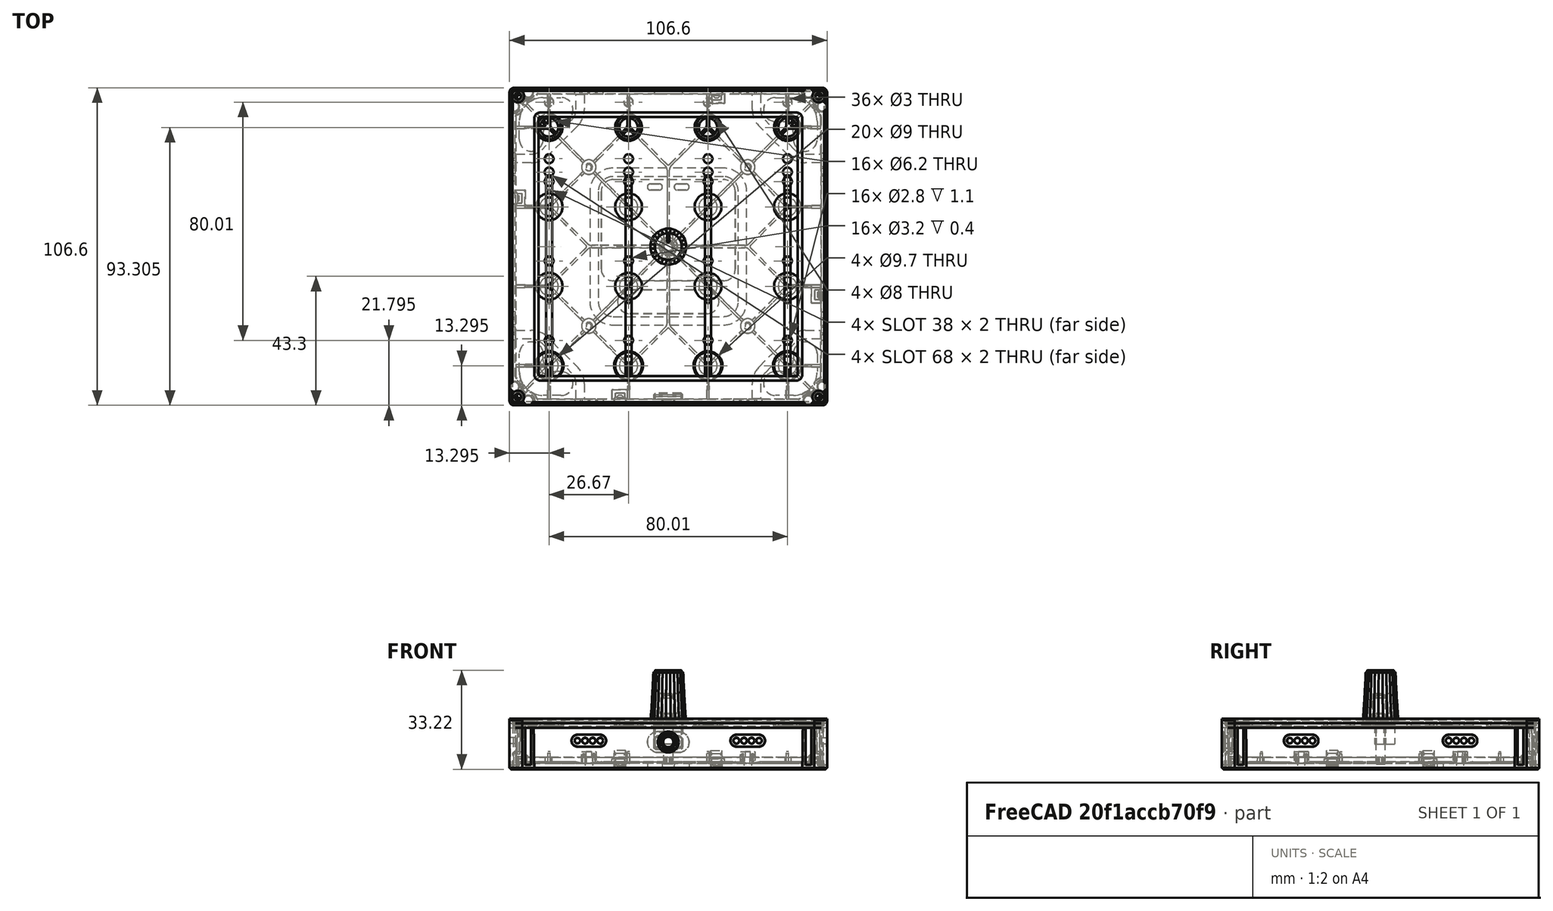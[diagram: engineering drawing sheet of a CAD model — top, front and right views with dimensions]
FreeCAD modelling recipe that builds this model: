
FCSTD DOCUMENT  (FreeCAD 0.20R29410 (Git))
Label: grid_module
License: All rights reserved
LicenseURL: http://en.wikipedia.org/wiki/All_rights_reserved
objects: Sketcher::SketchObject×346, App::Part×144, PartDesign::Body×128, PartDesign::Pocket×109, PartDesign::Chamfer×80, PartDesign::Pad×69, PartDesign::Revolution×59, PartDesign::Fillet×40, PartDesign::AdditiveLoft×36, Part::Feature×15, App::VRMLObject×11, Mesh::Feature×4, PartDesign::Hole×1, PartDesign::Draft×1
note: 1279 computed .brp shape members not serialized (recipe doc carries the construction recipe); baked Part::Feature solids carry a one-line shape summary decoded from their .brp

FEATURE [Sketcher::SketchObject] Sketch
  FullyConstrained = false
  MapMode = 5
  Support = -> [XY_Plane]
  sketch-geometry (25):
    g0: LineSegment StartX=-0.789915 StartY=6 StartZ=0 EndX=-2.31591 EndY=5.59111 EndZ=0
    g1: LineSegment StartX=-2.31591 StartY=5.59111 StartZ=0 EndX=-3.68409 EndY=4.80119 EndZ=0
    g2: LineSegment StartX=-3.68409 StartY=4.80119 StartZ=0 EndX=-4.80119 EndY=3.68409 EndZ=0
    g3: LineSegment StartX=-4.80119 StartY=3.68409 StartZ=0 EndX=-5.59111 EndY=2.31591 EndZ=0
    g4: LineSegment StartX=-5.59111 StartY=2.31591 StartZ=0 EndX=-6 EndY=0.789915 EndZ=0
    g5: LineSegment StartX=-6 StartY=0.789915 StartZ=0 EndX=-6 EndY=-0.789915 EndZ=0
    g6: LineSegment StartX=-6 StartY=-0.789915 StartZ=0 EndX=-5.59111 EndY=-2.31591 EndZ=0
    g7: LineSegment StartX=-5.59111 StartY=-2.31591 StartZ=0 EndX=-4.80119 EndY=-3.68409 EndZ=0
    g8: LineSegment StartX=-4.80119 StartY=-3.68409 StartZ=0 EndX=-3.68409 EndY=-4.80119 EndZ=0
    g9: LineSegment StartX=-3.68409 StartY=-4.80119 StartZ=0 EndX=-2.31591 EndY=-5.59111 EndZ=0
    g10: LineSegment StartX=-2.31591 StartY=-5.59111 StartZ=0 EndX=-0.789915 EndY=-6 EndZ=0
    g11: LineSegment StartX=-0.789915 StartY=-6 StartZ=0 EndX=0.789915 EndY=-6 EndZ=0
    g12: LineSegment StartX=0.789915 StartY=-6 StartZ=0 EndX=2.31591 EndY=-5.59111 EndZ=0
    g13: LineSegment StartX=2.31591 StartY=-5.59111 StartZ=0 EndX=3.68409 EndY=-4.80119 EndZ=0
    g14: LineSegment StartX=3.68409 StartY=-4.80119 StartZ=0 EndX=4.80119 EndY=-3.68409 EndZ=0
    g15: LineSegment StartX=4.80119 StartY=-3.68409 StartZ=0 EndX=5.59111 EndY=-2.31591 EndZ=0
    g16: LineSegment StartX=5.59111 StartY=-2.31591 StartZ=0 EndX=6 EndY=-0.789915 EndZ=0
    g17: LineSegment StartX=6 StartY=-0.789915 StartZ=0 EndX=6 EndY=0.789915 EndZ=0
    g18: LineSegment StartX=6 StartY=0.789915 StartZ=0 EndX=5.59111 EndY=2.31591 EndZ=0
    g19: LineSegment StartX=5.59111 StartY=2.31591 StartZ=0 EndX=4.80119 EndY=3.68409 EndZ=0
    g20: LineSegment StartX=4.80119 StartY=3.68409 StartZ=0 EndX=3.68409 EndY=4.80119 EndZ=0
    g21: LineSegment StartX=3.68409 StartY=4.80119 StartZ=0 EndX=2.31591 EndY=5.59111 EndZ=0
    g22: LineSegment StartX=2.31591 StartY=5.59111 StartZ=0 EndX=0.789915 EndY=6 EndZ=0
    g23: LineSegment StartX=0.789915 StartY=6 StartZ=0 EndX=-0.789915 EndY=6 EndZ=0
    g24: Circle CenterX=0 CenterY=0 CenterZ=0 NormalX=0 NormalY=0 NormalZ=1 AngleXU=0 Radius=6.05177
  constraints (52):
    c: Coincident(g0,g1)
    c: Coincident(g1,g2)
    c: Coincident(g2,g3)
    c: Coincident(g3,g4)
    c: Coincident(g4,g5)
    c: Coincident(g5,g6)
    c: Coincident(g6,g7)
    c: Coincident(g7,g8)
    c: Coincident(g8,g9)
    c: Coincident(g9,g10)
    c: Coincident(g10,g11)
    c: Coincident(g11,g12)
    c: Coincident(g12,g13)
    c: Coincident(g13,g14)
    c: Coincident(g14,g15)
    c: Coincident(g15,g16)
    c: Coincident(g16,g17)
    c: Coincident(g17,g18)
    c: Coincident(g18,g19)
    c: Coincident(g19,g20)
    c: Coincident(g20,g21)
    c: Coincident(g21,g22)
    c: Coincident(g22,g23)
    c: Coincident(g23,g0)
    c: Equal(g0, g1-g23) x23
    c: PointOnObject(g0,g24)
    c: PointOnObject(g1,g24)
    c: PointOnObject(g2,g24)
    c: PointOnObject(g3,g24)
    c: PointOnObject(g4,g24)
    c: PointOnObject(g5,g24)
    c: PointOnObject(g6,g24)
    c: PointOnObject(g7,g24)
    c: PointOnObject(g8,g24)
    c: PointOnObject(g9,g24)
    c: PointOnObject(g10,g24)
    c: PointOnObject(g11,g24)
    c: PointOnObject(g12,g24)
    c: PointOnObject(g13,g24)
    c: PointOnObject(g14,g24)
    c: PointOnObject(g15,g24)
    c: PointOnObject(g16,g24)
    c: PointOnObject(g17,g24)
    c: PointOnObject(g18,g24)
    c: PointOnObject(g19,g24)
    c: PointOnObject(g20,g24)
    c: PointOnObject(g21,g24)
    c: PointOnObject(g22,g24)
    c: PointOnObject(g23,g24)
    c: Coincident(g24,g-1)
    c: Horizontal(g23)
    c: DistanceX(g4,g17) = 12
FEATURE [Sketcher::SketchObject] Sketch001
  AttachmentOffset = pos=(0,0,7) rot=(0,0,1;0rad)
  FullyConstrained = false
  MapMode = 5
  Placement = pos=(0,0,7) rot=(0,0,1;0rad)
  Support = -> [XY_Plane]
  sketch-geometry (25):
    g0: LineSegment StartX=-0.724089 StartY=5.5 StartZ=0 EndX=-2.12292 EndY=5.12518 EndZ=0
    g1: LineSegment StartX=-2.12292 StartY=5.12518 StartZ=0 EndX=-3.37708 EndY=4.4011 EndZ=0
    g2: LineSegment StartX=-3.37708 StartY=4.4011 StartZ=0 EndX=-4.4011 EndY=3.37708 EndZ=0
    g3: LineSegment StartX=-4.4011 StartY=3.37708 StartZ=0 EndX=-5.12518 EndY=2.12292 EndZ=0
    g4: LineSegment StartX=-5.12518 StartY=2.12292 StartZ=0 EndX=-5.5 EndY=0.724089 EndZ=0
    g5: LineSegment StartX=-5.5 StartY=0.724089 StartZ=0 EndX=-5.5 EndY=-0.724089 EndZ=0
    g6: LineSegment StartX=-5.5 StartY=-0.724089 StartZ=0 EndX=-5.12518 EndY=-2.12292 EndZ=0
    g7: LineSegment StartX=-5.12518 StartY=-2.12292 StartZ=0 EndX=-4.4011 EndY=-3.37708 EndZ=0
    g8: LineSegment StartX=-4.4011 StartY=-3.37708 StartZ=0 EndX=-3.37708 EndY=-4.4011 EndZ=0
    g9: LineSegment StartX=-3.37708 StartY=-4.4011 StartZ=0 EndX=-2.12292 EndY=-5.12518 EndZ=0
    g10: LineSegment StartX=-2.12292 StartY=-5.12518 StartZ=0 EndX=-0.724089 EndY=-5.5 EndZ=0
    g11: LineSegment StartX=-0.724089 StartY=-5.5 StartZ=0 EndX=0.724089 EndY=-5.5 EndZ=0
    g12: LineSegment StartX=0.724089 StartY=-5.5 StartZ=0 EndX=2.12292 EndY=-5.12518 EndZ=0
    g13: LineSegment StartX=2.12292 StartY=-5.12518 StartZ=0 EndX=3.37708 EndY=-4.4011 EndZ=0
    g14: LineSegment StartX=3.37708 StartY=-4.4011 StartZ=0 EndX=4.4011 EndY=-3.37708 EndZ=0
    g15: LineSegment StartX=4.4011 StartY=-3.37708 StartZ=0 EndX=5.12518 EndY=-2.12292 EndZ=0
    g16: LineSegment StartX=5.12518 StartY=-2.12292 StartZ=0 EndX=5.5 EndY=-0.724089 EndZ=0
    g17: LineSegment StartX=5.5 StartY=-0.724089 StartZ=0 EndX=5.5 EndY=0.724089 EndZ=0
    g18: LineSegment StartX=5.5 StartY=0.724089 StartZ=0 EndX=5.12518 EndY=2.12292 EndZ=0
    g19: LineSegment StartX=5.12518 StartY=2.12292 StartZ=0 EndX=4.4011 EndY=3.37708 EndZ=0
    g20: LineSegment StartX=4.4011 StartY=3.37708 StartZ=0 EndX=3.37708 EndY=4.4011 EndZ=0
    g21: LineSegment StartX=3.37708 StartY=4.4011 StartZ=0 EndX=2.12292 EndY=5.12518 EndZ=0
    g22: LineSegment StartX=2.12292 StartY=5.12518 StartZ=0 EndX=0.724089 EndY=5.5 EndZ=0
    g23: LineSegment StartX=0.724089 StartY=5.5 StartZ=0 EndX=-0.724089 EndY=5.5 EndZ=0
    g24: Circle CenterX=0 CenterY=0 CenterZ=0 NormalX=0 NormalY=0 NormalZ=1 AngleXU=0 Radius=5.54746
  constraints (52):
    c: Coincident(g0,g1)
    c: Coincident(g1,g2)
    c: Coincident(g2,g3)
    c: Coincident(g3,g4)
    c: Coincident(g4,g5)
    c: Coincident(g5,g6)
    c: Coincident(g6,g7)
    c: Coincident(g7,g8)
    c: Coincident(g8,g9)
    c: Coincident(g9,g10)
    c: Coincident(g10,g11)
    c: Coincident(g11,g12)
    c: Coincident(g12,g13)
    c: Coincident(g13,g14)
    c: Coincident(g14,g15)
    c: Coincident(g15,g16)
    c: Coincident(g16,g17)
    c: Coincident(g17,g18)
    c: Coincident(g18,g19)
    c: Coincident(g19,g20)
    c: Coincident(g20,g21)
    c: Coincident(g21,g22)
    c: Coincident(g22,g23)
    c: Coincident(g23,g0)
    c: Equal(g0, g1-g23) x23
    c: PointOnObject(g0,g24)
    c: PointOnObject(g1,g24)
    c: PointOnObject(g2,g24)
    c: PointOnObject(g3,g24)
    c: PointOnObject(g4,g24)
    c: PointOnObject(g5,g24)
    c: PointOnObject(g6,g24)
    c: PointOnObject(g7,g24)
    c: PointOnObject(g8,g24)
    c: PointOnObject(g9,g24)
    c: PointOnObject(g10,g24)
    c: PointOnObject(g11,g24)
    c: PointOnObject(g12,g24)
    c: PointOnObject(g13,g24)
    c: PointOnObject(g14,g24)
    c: PointOnObject(g15,g24)
    c: PointOnObject(g16,g24)
    c: PointOnObject(g17,g24)
    c: PointOnObject(g18,g24)
    c: PointOnObject(g19,g24)
    c: PointOnObject(g20,g24)
    c: PointOnObject(g21,g24)
    c: PointOnObject(g22,g24)
    c: PointOnObject(g23,g24)
    c: Coincident(g24,g-1)
    c: Horizontal(g23)
    c: DistanceX(g4,g17) = 11
FEATURE [Sketcher::SketchObject] Sketch002
  AttachmentOffset = pos=(0,0,17) rot=(0,0,1;0rad)
  FullyConstrained = false
  MapMode = 5
  Placement = pos=(0,0,17) rot=(0,0,1;0rad)
  Support = -> [XY_Plane]
  sketch-geometry (25):
    g0: LineSegment StartX=-4.65926 StartY=1.92993 StartZ=0 EndX=-5 EndY=0.658262 EndZ=0
    g1: LineSegment StartX=-5 StartY=0.658262 StartZ=0 EndX=-5 EndY=-0.658262 EndZ=0
    g2: LineSegment StartX=-5 StartY=-0.658262 StartZ=0 EndX=-4.65926 EndY=-1.92993 EndZ=0
    g3: LineSegment StartX=-4.65926 StartY=-1.92993 StartZ=0 EndX=-4.001 EndY=-3.07007 EndZ=0
    g4: LineSegment StartX=-4.001 StartY=-3.07007 StartZ=0 EndX=-3.07007 EndY=-4.001 EndZ=0
    g5: LineSegment StartX=-3.07007 StartY=-4.001 StartZ=0 EndX=-1.92993 EndY=-4.65926 EndZ=0
    g6: LineSegment StartX=-1.92993 StartY=-4.65926 StartZ=0 EndX=-0.658262 EndY=-5 EndZ=0
    g7: LineSegment StartX=-0.658262 StartY=-5 StartZ=0 EndX=0.658262 EndY=-5 EndZ=0
    g8: LineSegment StartX=0.658262 StartY=-5 StartZ=0 EndX=1.92993 EndY=-4.65926 EndZ=0
    g9: LineSegment StartX=1.92993 StartY=-4.65926 StartZ=0 EndX=3.07007 EndY=-4.001 EndZ=0
    g10: LineSegment StartX=3.07007 StartY=-4.001 StartZ=0 EndX=4.001 EndY=-3.07007 EndZ=0
    g11: LineSegment StartX=4.001 StartY=-3.07007 StartZ=0 EndX=4.65926 EndY=-1.92993 EndZ=0
    g12: LineSegment StartX=4.65926 StartY=-1.92993 StartZ=0 EndX=5 EndY=-0.658262 EndZ=0
    g13: LineSegment StartX=5 StartY=-0.658262 StartZ=0 EndX=5 EndY=0.658262 EndZ=0
    g14: LineSegment StartX=5 StartY=0.658262 StartZ=0 EndX=4.65926 EndY=1.92993 EndZ=0
    g15: LineSegment StartX=4.65926 StartY=1.92993 StartZ=0 EndX=4.001 EndY=3.07007 EndZ=0
    g16: LineSegment StartX=4.001 StartY=3.07007 StartZ=0 EndX=3.07007 EndY=4.001 EndZ=0
    g17: LineSegment StartX=3.07007 StartY=4.001 StartZ=0 EndX=1.92993 EndY=4.65926 EndZ=0
    g18: LineSegment StartX=1.92993 StartY=4.65926 StartZ=0 EndX=0.658262 EndY=5 EndZ=0
    g19: LineSegment StartX=0.658262 StartY=5 StartZ=0 EndX=-0.658262 EndY=5 EndZ=0
    g20: LineSegment StartX=-0.658262 StartY=5 StartZ=0 EndX=-1.92993 EndY=4.65926 EndZ=0
    g21: LineSegment StartX=-1.92993 StartY=4.65926 StartZ=0 EndX=-3.07007 EndY=4.001 EndZ=0
    g22: LineSegment StartX=-3.07007 StartY=4.001 StartZ=0 EndX=-4.001 EndY=3.07007 EndZ=0
    g23: LineSegment StartX=-4.001 StartY=3.07007 StartZ=0 EndX=-4.65926 EndY=1.92993 EndZ=0
    g24: Circle CenterX=0 CenterY=0 CenterZ=0 NormalX=0 NormalY=0 NormalZ=1 AngleXU=0 Radius=5.04314
  constraints (52):
    c: Coincident(g0,g1)
    c: Coincident(g1,g2)
    c: Coincident(g2,g3)
    c: Coincident(g3,g4)
    c: Coincident(g4,g5)
    c: Coincident(g5,g6)
    c: Coincident(g6,g7)
    c: Coincident(g7,g8)
    c: Coincident(g8,g9)
    c: Coincident(g9,g10)
    c: Coincident(g10,g11)
    c: Coincident(g11,g12)
    c: Coincident(g12,g13)
    c: Coincident(g13,g14)
    c: Coincident(g14,g15)
    c: Coincident(g15,g16)
    c: Coincident(g16,g17)
    c: Coincident(g17,g18)
    c: Coincident(g18,g19)
    c: Coincident(g19,g20)
    c: Coincident(g20,g21)
    c: Coincident(g21,g22)
    c: Coincident(g22,g23)
    c: Coincident(g23,g0)
    c: Equal(g0, g1-g23) x23
    c: PointOnObject(g0,g24)
    c: PointOnObject(g1,g24)
    c: PointOnObject(g2,g24)
    c: PointOnObject(g3,g24)
    c: PointOnObject(g4,g24)
    c: PointOnObject(g5,g24)
    c: PointOnObject(g6,g24)
    c: PointOnObject(g7,g24)
    c: PointOnObject(g8,g24)
    c: PointOnObject(g9,g24)
    c: PointOnObject(g10,g24)
    c: PointOnObject(g11,g24)
    c: PointOnObject(g12,g24)
    c: PointOnObject(g13,g24)
    c: PointOnObject(g14,g24)
    c: PointOnObject(g15,g24)
    c: PointOnObject(g16,g24)
    c: PointOnObject(g17,g24)
    c: PointOnObject(g18,g24)
    c: PointOnObject(g19,g24)
    c: PointOnObject(g20,g24)
    c: PointOnObject(g21,g24)
    c: PointOnObject(g22,g24)
    c: PointOnObject(g23,g24)
    c: Coincident(g24,g-1)
    c: Horizontal(g19)
    c: DistanceX(g0,g13) = 10
FEATURE [PartDesign::AdditiveLoft] AdditiveLoft
  AllowMultiFace = false
  Closed = false
  Profile = -> Sketch
  Refine = true
  Ruled = false
  Sections = -> [Sketch001,Sketch002]
FEATURE [Sketcher::SketchObject] Sketch003
  FullyConstrained = false
  MapMode = 5
  Placement = pos=(0,0,17) rot=(0,0,1;0rad)
  Support = -> [AdditiveLoft]
  sketch-geometry (1):
    g0: Circle CenterX=0 CenterY=0 CenterZ=0 NormalX=0 NormalY=0 NormalZ=1 AngleXU=0 Radius=4.5
  constraints (2):
    c: Coincident(g0,g-1)
    c: Radius(g0) = 4.5
FEATURE [PartDesign::Pad] Pad
  AllowMultiFace = false
  BaseFeature = -> AdditiveLoft
  Direction = (1,1,1)
  Length = 0.7
  Length2 = 100
  Profile = -> Sketch003
  Refine = true
  Type = 0
FEATURE [Sketcher::SketchObject] Sketch004
  AttachmentOffset = pos=(0,0,17.7) rot=(0,0,1;0rad)
  FullyConstrained = false
  MapMode = 5
  Placement = pos=(0,0,17.7) rot=(0,0,1;0rad)
  Support = -> [XY_Plane001]
  sketch-geometry (10):
    g0: LineSegment StartX=-0.2 StartY=1.5 StartZ=0 EndX=0.2 EndY=1.5 EndZ=0
    g1: LineSegment StartX=0.4 StartY=1.7 StartZ=0 EndX=0.4 EndY=4.2 EndZ=0
    g2: LineSegment StartX=0.2 StartY=4.4 StartZ=0 EndX=-0.2 EndY=4.4 EndZ=0
    g3: LineSegment StartX=-0.4 StartY=4.2 StartZ=0 EndX=-0.4 EndY=1.7 EndZ=0
    g4: ArcOfCircle CenterX=-0.2 CenterY=1.7 CenterZ=0 NormalX=0 NormalY=0 NormalZ=1 AngleXU=0 Radius=0.2 StartAngle=3.14159 EndAngle=4.71239
    g5: ArcOfCircle CenterX=0.2 CenterY=1.7 CenterZ=0 NormalX=0 NormalY=0 NormalZ=1 AngleXU=0 Radius=0.2 StartAngle=4.71239 EndAngle=6.28319
    g6: ArcOfCircle CenterX=0.2 CenterY=4.2 CenterZ=0 NormalX=0 NormalY=0 NormalZ=1 AngleXU=0 Radius=0.2 StartAngle=1.4e-15 EndAngle=1.5708
    g7: ArcOfCircle CenterX=-0.2 CenterY=4.2 CenterZ=0 NormalX=0 NormalY=0 NormalZ=1 AngleXU=0 Radius=0.2 StartAngle=1.5708 EndAngle=3.14159
    g8: LineSegment StartX=-0.2 StartY=1.7 StartZ=0 EndX=0 EndY=0 EndZ=0
    g9: LineSegment StartX=0 StartY=0 StartZ=0 EndX=0.2 EndY=1.7 EndZ=0
  constraints (24):
    c: Horizontal(g0)
    c: Horizontal(g2)
    c: Vertical(g1)
    c: Vertical(g3)
    c: Tangent(g3,g4) = -1.5708
    c: Tangent(g0,g4) = -1.5708
    c: Tangent(g0,g5) = -1.5708
    c: Tangent(g1,g5) = -1.5708
    c: Tangent(g1,g6) = -1.5708
    c: Tangent(g2,g6) = -1.5708
    c: Tangent(g2,g7) = -1.5708
    c: Tangent(g3,g7) = -1.5708
    c: Radius(g7) = 0.2
    c: Equal(g7,g6)
    c: Equal(g7,g5)
    c: Equal(g7,g4)
    c: Coincident(g8,g4)
    c: Coincident(g8,g-1)
    c: Coincident(g9,g-1)
    c: Coincident(g9,g5)
    c: Equal(g9,g8)
    c: DistanceX(g3,g1) = 0.8
    c: DistanceY(g-1,g2) = 4.4
    c: DistanceY(g-1,g0) = 1.5
FEATURE [PartDesign::Pad] Pad001
  AllowMultiFace = false
  Direction = (1,1,1)
  Length = 0.02
  Length2 = 100
  Profile = -> Sketch004
  Refine = true
  Type = 0
FEATURE [PartDesign::Body] Body001  label="Indicator"
  Group = -> [Sketch004,Pad001]
  Origin = -> Origin001
  Tip = -> Pad001
FEATURE [Sketcher::SketchObject] Sketch005
  FullyConstrained = false
  MapMode = 5
  Placement = pos=(0,0,0) rot=(1,0,0;3.14159rad)
  Support = -> [Pad]
  sketch-geometry (1):
    g0: Circle CenterX=0 CenterY=0 CenterZ=0 NormalX=0 NormalY=0 NormalZ=1 AngleXU=0 Radius=5
  constraints (2):
    c: Coincident(g0,g-1)
    c: Radius(g0) = 5
FEATURE [PartDesign::Pocket] Pocket
  AllowMultiFace = false
  BaseFeature = -> Pad
  Direction = (1,1,1)
  Length = 1
  Length2 = 100
  Profile = -> Sketch005
  Refine = true
  Type = 0
FEATURE [Sketcher::SketchObject] Sketch006
  FullyConstrained = false
  MapMode = 5
  Placement = pos=(0,0,1) rot=(1,0,0;3.14159rad)
  Support = -> [Pocket]
  sketch-geometry (1):
    g0: Circle CenterX=0 CenterY=0 CenterZ=0 NormalX=0 NormalY=0 NormalZ=1 AngleXU=0 Radius=4.65
  constraints (2):
    c: Coincident(g0,g-1)
    c: Radius(g0) = 4.65
FEATURE [PartDesign::Pocket] Pocket001
  AllowMultiFace = false
  BaseFeature = -> Pocket
  Direction = (1,1,1)
  Length = 1
  Length2 = 100
  Profile = -> Sketch006
  Refine = true
  Type = 0
FEATURE [Sketcher::SketchObject] Sketch007
  FullyConstrained = false
  MapMode = 5
  Placement = pos=(0,0,2) rot=(1,0,0;3.14159rad)
  Support = -> [Pocket001]
  sketch-geometry (2):
    g0: ArcOfCircle CenterX=0 CenterY=0 CenterZ=0 NormalX=0 NormalY=0 NormalZ=1 AngleXU=0 Radius=3 StartAngle=2.19024 EndAngle=7.23453
    g1: LineSegment StartX=-1.74176 StartY=2.4426 StartZ=0 EndX=1.74176 EndY=2.4426 EndZ=0
  constraints (5):
    c: Coincident(g0,g-1)
    c: Coincident(g1,g0)
    c: Coincident(g1,g0)
    c: Horizontal(g1)
    c: Radius(g0) = 3
FEATURE [PartDesign::Pocket] Pocket002
  AllowMultiFace = false
  BaseFeature = -> Pocket001
  Direction = (1,1,1)
  Length = 8
  Length2 = 100
  Profile = -> Sketch007
  Refine = true
  Type = 0
FEATURE [PartDesign::Chamfer] Chamfer
  Angle = 45
  Base = -> Pocket002 [Edge82,Edge83]
  BaseFeature = -> Pocket002
  ChamferType = 0
  FlipDirection = false
  Size = 1.4
  Size2 = 1
  SupportTransform = false
  UseAllEdges = false
FEATURE [PartDesign::Chamfer] Chamfer001
  Angle = 45
  Base = -> Chamfer [Edge8]
  BaseFeature = -> Chamfer
  ChamferType = 0
  FlipDirection = false
  Size = 0.3
  Size2 = 1
  SupportTransform = false
  UseAllEdges = false
FEATURE [PartDesign::Fillet] Fillet
  Base = -> Chamfer001 [Edge93,Face36]
  BaseFeature = -> Chamfer001
  Radius = 0.1
  SupportTransform = false
  UseAllEdges = false
FEATURE [PartDesign::Body] Body
  Group = -> [Sketch,Sketch001,Sketch002,AdditiveLoft,Sketch003,Pad,Sketch005,Pocket,Sketch006,Pocket001,Sketch007,Pocket002,Chamfer,Chamfer001,Fillet]
  Origin = -> Origin
  Tip = -> Fillet
FEATURE [App::Part] Part  label="Cap1"
  Group = -> [Body,Body001]
  Origin = -> Origin004
  Placement = pos=(-40.005,40.005,0) rot=(0,0,1;0rad)
  expr: .Placement.Base.x = -40.005
  expr: .Placement.Base.y = 40.005
FEATURE [Sketcher::SketchObject] Sketch012
  AttachmentOffset = pos=(0,0,7) rot=(0,0,1;0rad)
  FullyConstrained = false
  MapMode = 5
  Placement = pos=(0,0,7) rot=(0,0,1;0rad)
  Support = -> [XY_Plane005]
  sketch-geometry (25):
    g0: LineSegment StartX=-0.724089 StartY=5.5 StartZ=0 EndX=-2.12292 EndY=5.12518 EndZ=0
    g1: LineSegment StartX=-2.12292 StartY=5.12518 StartZ=0 EndX=-3.37708 EndY=4.4011 EndZ=0
    g2: LineSegment StartX=-3.37708 StartY=4.4011 StartZ=0 EndX=-4.4011 EndY=3.37708 EndZ=0
    g3: LineSegment StartX=-4.4011 StartY=3.37708 StartZ=0 EndX=-5.12518 EndY=2.12292 EndZ=0
    g4: LineSegment StartX=-5.12518 StartY=2.12292 StartZ=0 EndX=-5.5 EndY=0.724089 EndZ=0
    g5: LineSegment StartX=-5.5 StartY=0.724089 StartZ=0 EndX=-5.5 EndY=-0.724089 EndZ=0
    g6: LineSegment StartX=-5.5 StartY=-0.724089 StartZ=0 EndX=-5.12518 EndY=-2.12292 EndZ=0
    g7: LineSegment StartX=-5.12518 StartY=-2.12292 StartZ=0 EndX=-4.4011 EndY=-3.37708 EndZ=0
    g8: LineSegment StartX=-4.4011 StartY=-3.37708 StartZ=0 EndX=-3.37708 EndY=-4.4011 EndZ=0
    g9: LineSegment StartX=-3.37708 StartY=-4.4011 StartZ=0 EndX=-2.12292 EndY=-5.12518 EndZ=0
    g10: LineSegment StartX=-2.12292 StartY=-5.12518 StartZ=0 EndX=-0.724089 EndY=-5.5 EndZ=0
    g11: LineSegment StartX=-0.724089 StartY=-5.5 StartZ=0 EndX=0.724089 EndY=-5.5 EndZ=0
    g12: LineSegment StartX=0.724089 StartY=-5.5 StartZ=0 EndX=2.12292 EndY=-5.12518 EndZ=0
    g13: LineSegment StartX=2.12292 StartY=-5.12518 StartZ=0 EndX=3.37708 EndY=-4.4011 EndZ=0
    g14: LineSegment StartX=3.37708 StartY=-4.4011 StartZ=0 EndX=4.4011 EndY=-3.37708 EndZ=0
    g15: LineSegment StartX=4.4011 StartY=-3.37708 StartZ=0 EndX=5.12518 EndY=-2.12292 EndZ=0
    g16: LineSegment StartX=5.12518 StartY=-2.12292 StartZ=0 EndX=5.5 EndY=-0.724089 EndZ=0
    g17: LineSegment StartX=5.5 StartY=-0.724089 StartZ=0 EndX=5.5 EndY=0.724089 EndZ=0
    g18: LineSegment StartX=5.5 StartY=0.724089 StartZ=0 EndX=5.12518 EndY=2.12292 EndZ=0
    g19: LineSegment StartX=5.12518 StartY=2.12292 StartZ=0 EndX=4.4011 EndY=3.37708 EndZ=0
    g20: LineSegment StartX=4.4011 StartY=3.37708 StartZ=0 EndX=3.37708 EndY=4.4011 EndZ=0
    g21: LineSegment StartX=3.37708 StartY=4.4011 StartZ=0 EndX=2.12292 EndY=5.12518 EndZ=0
    g22: LineSegment StartX=2.12292 StartY=5.12518 StartZ=0 EndX=0.724089 EndY=5.5 EndZ=0
    g23: LineSegment StartX=0.724089 StartY=5.5 StartZ=0 EndX=-0.724089 EndY=5.5 EndZ=0
    g24: Circle CenterX=0 CenterY=0 CenterZ=0 NormalX=0 NormalY=0 NormalZ=1 AngleXU=0 Radius=5.54746
  constraints (52):
    c: Coincident(g0,g1)
    c: Coincident(g1,g2)
    c: Coincident(g2,g3)
    c: Coincident(g3,g4)
    c: Coincident(g4,g5)
    c: Coincident(g5,g6)
    c: Coincident(g6,g7)
    c: Coincident(g7,g8)
    c: Coincident(g8,g9)
    c: Coincident(g9,g10)
    c: Coincident(g10,g11)
    c: Coincident(g11,g12)
    c: Coincident(g12,g13)
    c: Coincident(g13,g14)
    c: Coincident(g14,g15)
    c: Coincident(g15,g16)
    c: Coincident(g16,g17)
    c: Coincident(g17,g18)
    c: Coincident(g18,g19)
    c: Coincident(g19,g20)
    c: Coincident(g20,g21)
    c: Coincident(g21,g22)
    c: Coincident(g22,g23)
    c: Coincident(g23,g0)
    c: Equal(g0, g1-g23) x23
    c: PointOnObject(g0,g24)
    c: PointOnObject(g1,g24)
    c: PointOnObject(g2,g24)
    c: PointOnObject(g3,g24)
    c: PointOnObject(g4,g24)
    c: PointOnObject(g5,g24)
    c: PointOnObject(g6,g24)
    c: PointOnObject(g7,g24)
    c: PointOnObject(g8,g24)
    c: PointOnObject(g9,g24)
    c: PointOnObject(g10,g24)
    c: PointOnObject(g11,g24)
    c: PointOnObject(g12,g24)
    c: PointOnObject(g13,g24)
    c: PointOnObject(g14,g24)
    c: PointOnObject(g15,g24)
    c: PointOnObject(g16,g24)
    c: PointOnObject(g17,g24)
    c: PointOnObject(g18,g24)
    c: PointOnObject(g19,g24)
    c: PointOnObject(g20,g24)
    c: PointOnObject(g21,g24)
    c: PointOnObject(g22,g24)
    c: PointOnObject(g23,g24)
    c: Coincident(g24,g-1)
    c: Horizontal(g23)
    c: DistanceX(g4,g17) = 11
FEATURE [Sketcher::SketchObject] Sketch013
  FullyConstrained = false
  MapMode = 5
  Support = -> [XY_Plane005]
  sketch-geometry (25):
    g0: LineSegment StartX=-0.789915 StartY=6 StartZ=0 EndX=-2.31591 EndY=5.59111 EndZ=0
    g1: LineSegment StartX=-2.31591 StartY=5.59111 StartZ=0 EndX=-3.68409 EndY=4.80119 EndZ=0
    g2: LineSegment StartX=-3.68409 StartY=4.80119 StartZ=0 EndX=-4.80119 EndY=3.68409 EndZ=0
    g3: LineSegment StartX=-4.80119 StartY=3.68409 StartZ=0 EndX=-5.59111 EndY=2.31591 EndZ=0
    g4: LineSegment StartX=-5.59111 StartY=2.31591 StartZ=0 EndX=-6 EndY=0.789915 EndZ=0
    g5: LineSegment StartX=-6 StartY=0.789915 StartZ=0 EndX=-6 EndY=-0.789915 EndZ=0
    g6: LineSegment StartX=-6 StartY=-0.789915 StartZ=0 EndX=-5.59111 EndY=-2.31591 EndZ=0
    g7: LineSegment StartX=-5.59111 StartY=-2.31591 StartZ=0 EndX=-4.80119 EndY=-3.68409 EndZ=0
    g8: LineSegment StartX=-4.80119 StartY=-3.68409 StartZ=0 EndX=-3.68409 EndY=-4.80119 EndZ=0
    g9: LineSegment StartX=-3.68409 StartY=-4.80119 StartZ=0 EndX=-2.31591 EndY=-5.59111 EndZ=0
    g10: LineSegment StartX=-2.31591 StartY=-5.59111 StartZ=0 EndX=-0.789915 EndY=-6 EndZ=0
    g11: LineSegment StartX=-0.789915 StartY=-6 StartZ=0 EndX=0.789915 EndY=-6 EndZ=0
    g12: LineSegment StartX=0.789915 StartY=-6 StartZ=0 EndX=2.31591 EndY=-5.59111 EndZ=0
    g13: LineSegment StartX=2.31591 StartY=-5.59111 StartZ=0 EndX=3.68409 EndY=-4.80119 EndZ=0
    g14: LineSegment StartX=3.68409 StartY=-4.80119 StartZ=0 EndX=4.80119 EndY=-3.68409 EndZ=0
    g15: LineSegment StartX=4.80119 StartY=-3.68409 StartZ=0 EndX=5.59111 EndY=-2.31591 EndZ=0
    g16: LineSegment StartX=5.59111 StartY=-2.31591 StartZ=0 EndX=6 EndY=-0.789915 EndZ=0
    g17: LineSegment StartX=6 StartY=-0.789915 StartZ=0 EndX=6 EndY=0.789915 EndZ=0
    g18: LineSegment StartX=6 StartY=0.789915 StartZ=0 EndX=5.59111 EndY=2.31591 EndZ=0
    g19: LineSegment StartX=5.59111 StartY=2.31591 StartZ=0 EndX=4.80119 EndY=3.68409 EndZ=0
    g20: LineSegment StartX=4.80119 StartY=3.68409 StartZ=0 EndX=3.68409 EndY=4.80119 EndZ=0
    g21: LineSegment StartX=3.68409 StartY=4.80119 StartZ=0 EndX=2.31591 EndY=5.59111 EndZ=0
    g22: LineSegment StartX=2.31591 StartY=5.59111 StartZ=0 EndX=0.789915 EndY=6 EndZ=0
    g23: LineSegment StartX=0.789915 StartY=6 StartZ=0 EndX=-0.789915 EndY=6 EndZ=0
    g24: Circle CenterX=0 CenterY=0 CenterZ=0 NormalX=0 NormalY=0 NormalZ=1 AngleXU=0 Radius=6.05177
  constraints (52):
    c: Coincident(g0,g1)
    c: Coincident(g1,g2)
    c: Coincident(g2,g3)
    c: Coincident(g3,g4)
    c: Coincident(g4,g5)
    c: Coincident(g5,g6)
    c: Coincident(g6,g7)
    c: Coincident(g7,g8)
    c: Coincident(g8,g9)
    c: Coincident(g9,g10)
    c: Coincident(g10,g11)
    c: Coincident(g11,g12)
    c: Coincident(g12,g13)
    c: Coincident(g13,g14)
    c: Coincident(g14,g15)
    c: Coincident(g15,g16)
    c: Coincident(g16,g17)
    c: Coincident(g17,g18)
    c: Coincident(g18,g19)
    c: Coincident(g19,g20)
    c: Coincident(g20,g21)
    c: Coincident(g21,g22)
    c: Coincident(g22,g23)
    c: Coincident(g23,g0)
    c: Equal(g0, g1-g23) x23
    c: PointOnObject(g0,g24)
    c: PointOnObject(g1,g24)
    c: PointOnObject(g2,g24)
    c: PointOnObject(g3,g24)
    c: PointOnObject(g4,g24)
    c: PointOnObject(g5,g24)
    c: PointOnObject(g6,g24)
    c: PointOnObject(g7,g24)
    c: PointOnObject(g8,g24)
    c: PointOnObject(g9,g24)
    c: PointOnObject(g10,g24)
    c: PointOnObject(g11,g24)
    c: PointOnObject(g12,g24)
    c: PointOnObject(g13,g24)
    c: PointOnObject(g14,g24)
    c: PointOnObject(g15,g24)
    c: PointOnObject(g16,g24)
    c: PointOnObject(g17,g24)
    c: PointOnObject(g18,g24)
    c: PointOnObject(g19,g24)
    c: PointOnObject(g20,g24)
    c: PointOnObject(g21,g24)
    c: PointOnObject(g22,g24)
    c: PointOnObject(g23,g24)
    c: Coincident(g24,g-1)
    c: Horizontal(g23)
    c: DistanceX(g4,g17) = 12
FEATURE [Sketcher::SketchObject] Sketch014
  AttachmentOffset = pos=(0,0,17) rot=(0,0,1;0rad)
  FullyConstrained = false
  MapMode = 5
  Placement = pos=(0,0,17) rot=(0,0,1;0rad)
  Support = -> [XY_Plane005]
  sketch-geometry (25):
    g0: LineSegment StartX=-4.65926 StartY=1.92993 StartZ=0 EndX=-5 EndY=0.658262 EndZ=0
    g1: LineSegment StartX=-5 StartY=0.658262 StartZ=0 EndX=-5 EndY=-0.658262 EndZ=0
    g2: LineSegment StartX=-5 StartY=-0.658262 StartZ=0 EndX=-4.65926 EndY=-1.92993 EndZ=0
    g3: LineSegment StartX=-4.65926 StartY=-1.92993 StartZ=0 EndX=-4.001 EndY=-3.07007 EndZ=0
    g4: LineSegment StartX=-4.001 StartY=-3.07007 StartZ=0 EndX=-3.07007 EndY=-4.001 EndZ=0
    g5: LineSegment StartX=-3.07007 StartY=-4.001 StartZ=0 EndX=-1.92993 EndY=-4.65926 EndZ=0
    g6: LineSegment StartX=-1.92993 StartY=-4.65926 StartZ=0 EndX=-0.658262 EndY=-5 EndZ=0
    g7: LineSegment StartX=-0.658262 StartY=-5 StartZ=0 EndX=0.658262 EndY=-5 EndZ=0
    g8: LineSegment StartX=0.658262 StartY=-5 StartZ=0 EndX=1.92993 EndY=-4.65926 EndZ=0
    g9: LineSegment StartX=1.92993 StartY=-4.65926 StartZ=0 EndX=3.07007 EndY=-4.001 EndZ=0
    g10: LineSegment StartX=3.07007 StartY=-4.001 StartZ=0 EndX=4.001 EndY=-3.07007 EndZ=0
    g11: LineSegment StartX=4.001 StartY=-3.07007 StartZ=0 EndX=4.65926 EndY=-1.92993 EndZ=0
    g12: LineSegment StartX=4.65926 StartY=-1.92993 StartZ=0 EndX=5 EndY=-0.658262 EndZ=0
    g13: LineSegment StartX=5 StartY=-0.658262 StartZ=0 EndX=5 EndY=0.658262 EndZ=0
    g14: LineSegment StartX=5 StartY=0.658262 StartZ=0 EndX=4.65926 EndY=1.92993 EndZ=0
    g15: LineSegment StartX=4.65926 StartY=1.92993 StartZ=0 EndX=4.001 EndY=3.07007 EndZ=0
    g16: LineSegment StartX=4.001 StartY=3.07007 StartZ=0 EndX=3.07007 EndY=4.001 EndZ=0
    g17: LineSegment StartX=3.07007 StartY=4.001 StartZ=0 EndX=1.92993 EndY=4.65926 EndZ=0
    g18: LineSegment StartX=1.92993 StartY=4.65926 StartZ=0 EndX=0.658262 EndY=5 EndZ=0
    g19: LineSegment StartX=0.658262 StartY=5 StartZ=0 EndX=-0.658262 EndY=5 EndZ=0
    g20: LineSegment StartX=-0.658262 StartY=5 StartZ=0 EndX=-1.92993 EndY=4.65926 EndZ=0
    g21: LineSegment StartX=-1.92993 StartY=4.65926 StartZ=0 EndX=-3.07007 EndY=4.001 EndZ=0
    g22: LineSegment StartX=-3.07007 StartY=4.001 StartZ=0 EndX=-4.001 EndY=3.07007 EndZ=0
    g23: LineSegment StartX=-4.001 StartY=3.07007 StartZ=0 EndX=-4.65926 EndY=1.92993 EndZ=0
    g24: Circle CenterX=0 CenterY=0 CenterZ=0 NormalX=0 NormalY=0 NormalZ=1 AngleXU=0 Radius=5.04314
  constraints (52):
    c: Coincident(g0,g1)
    c: Coincident(g1,g2)
    c: Coincident(g2,g3)
    c: Coincident(g3,g4)
    c: Coincident(g4,g5)
    c: Coincident(g5,g6)
    c: Coincident(g6,g7)
    c: Coincident(g7,g8)
    c: Coincident(g8,g9)
    c: Coincident(g9,g10)
    c: Coincident(g10,g11)
    c: Coincident(g11,g12)
    c: Coincident(g12,g13)
    c: Coincident(g13,g14)
    c: Coincident(g14,g15)
    c: Coincident(g15,g16)
    c: Coincident(g16,g17)
    c: Coincident(g17,g18)
    c: Coincident(g18,g19)
    c: Coincident(g19,g20)
    c: Coincident(g20,g21)
    c: Coincident(g21,g22)
    c: Coincident(g22,g23)
    c: Coincident(g23,g0)
    c: Equal(g0, g1-g23) x23
    c: PointOnObject(g0,g24)
    c: PointOnObject(g1,g24)
    c: PointOnObject(g2,g24)
    c: PointOnObject(g3,g24)
    c: PointOnObject(g4,g24)
    c: PointOnObject(g5,g24)
    c: PointOnObject(g6,g24)
    c: PointOnObject(g7,g24)
    c: PointOnObject(g8,g24)
    c: PointOnObject(g9,g24)
    c: PointOnObject(g10,g24)
    c: PointOnObject(g11,g24)
    c: PointOnObject(g12,g24)
    c: PointOnObject(g13,g24)
    c: PointOnObject(g14,g24)
    c: PointOnObject(g15,g24)
    c: PointOnObject(g16,g24)
    c: PointOnObject(g17,g24)
    c: PointOnObject(g18,g24)
    c: PointOnObject(g19,g24)
    c: PointOnObject(g20,g24)
    c: PointOnObject(g21,g24)
    c: PointOnObject(g22,g24)
    c: PointOnObject(g23,g24)
    c: Coincident(g24,g-1)
    c: Horizontal(g19)
    c: DistanceX(g0,g13) = 10
FEATURE [PartDesign::AdditiveLoft] AdditiveLoft001
  AllowMultiFace = false
  Closed = false
  Profile = -> Sketch013
  Refine = true
  Ruled = false
  Sections = -> [Sketch012,Sketch014]
FEATURE [Sketcher::SketchObject] Sketch011
  FullyConstrained = false
  MapMode = 5
  Placement = pos=(0,0,17) rot=(0,0,1;0rad)
  Support = -> [AdditiveLoft001]
  sketch-geometry (1):
    g0: Circle CenterX=0 CenterY=0 CenterZ=0 NormalX=0 NormalY=0 NormalZ=1 AngleXU=0 Radius=4.5
  constraints (2):
    c: Coincident(g0,g-1)
    c: Radius(g0) = 4.5
FEATURE [PartDesign::Pad] Pad002
  AllowMultiFace = false
  BaseFeature = -> AdditiveLoft001
  Direction = (1,1,1)
  Length = 0.7
  Length2 = 100
  Profile = -> Sketch011
  Refine = true
  Type = 0
FEATURE [Sketcher::SketchObject] Sketch010
  FullyConstrained = false
  MapMode = 5
  Placement = pos=(0,0,0) rot=(1,0,0;3.14159rad)
  Support = -> [Pad002]
  sketch-geometry (1):
    g0: Circle CenterX=0 CenterY=0 CenterZ=0 NormalX=0 NormalY=0 NormalZ=1 AngleXU=0 Radius=5
  constraints (2):
    c: Coincident(g0,g-1)
    c: Radius(g0) = 5
FEATURE [PartDesign::Pocket] Pocket004
  AllowMultiFace = false
  BaseFeature = -> Pad002
  Direction = (1,1,1)
  Length = 1
  Length2 = 100
  Profile = -> Sketch010
  Refine = true
  Type = 0
FEATURE [Sketcher::SketchObject] Sketch008
  FullyConstrained = false
  MapMode = 5
  Placement = pos=(0,0,1) rot=(1,0,0;3.14159rad)
  Support = -> [Pocket004]
  sketch-geometry (1):
    g0: Circle CenterX=0 CenterY=0 CenterZ=0 NormalX=0 NormalY=0 NormalZ=1 AngleXU=0 Radius=4.65
  constraints (2):
    c: Coincident(g0,g-1)
    c: Radius(g0) = 4.65
FEATURE [PartDesign::Pocket] Pocket003
  AllowMultiFace = false
  BaseFeature = -> Pocket004
  Direction = (1,1,1)
  Length = 1
  Length2 = 100
  Profile = -> Sketch008
  Refine = true
  Type = 0
FEATURE [Sketcher::SketchObject] Sketch009
  FullyConstrained = false
  MapMode = 5
  Placement = pos=(0,0,2) rot=(1,0,0;3.14159rad)
  Support = -> [Pocket003]
  sketch-geometry (2):
    g0: ArcOfCircle CenterX=0 CenterY=0 CenterZ=0 NormalX=0 NormalY=0 NormalZ=1 AngleXU=0 Radius=3 StartAngle=2.19024 EndAngle=7.23453
    g1: LineSegment StartX=-1.74176 StartY=2.4426 StartZ=0 EndX=1.74176 EndY=2.4426 EndZ=0
  constraints (5):
    c: Coincident(g0,g-1)
    c: Coincident(g1,g0)
    c: Coincident(g1,g0)
    c: Horizontal(g1)
    c: Radius(g0) = 3
FEATURE [PartDesign::Pocket] Pocket005
  AllowMultiFace = false
  BaseFeature = -> Pocket003
  Direction = (1,1,1)
  Length = 8
  Length2 = 100
  Profile = -> Sketch009
  Refine = true
  Type = 0
FEATURE [PartDesign::Chamfer] Chamfer002
  Angle = 45
  Base = -> Pocket005 [Edge82,Edge83]
  BaseFeature = -> Pocket005
  ChamferType = 0
  FlipDirection = false
  Size = 1.4
  Size2 = 1
  SupportTransform = false
  UseAllEdges = false
FEATURE [PartDesign::Chamfer] Chamfer003
  Angle = 45
  Base = -> Chamfer002 [Edge8]
  BaseFeature = -> Chamfer002
  ChamferType = 0
  FlipDirection = false
  Size = 0.3
  Size2 = 1
  SupportTransform = false
  UseAllEdges = false
FEATURE [PartDesign::Fillet] Fillet001
  Base = -> Chamfer003 [Edge93,Face36]
  BaseFeature = -> Chamfer003
  Radius = 0.1
  SupportTransform = false
  UseAllEdges = false
FEATURE [PartDesign::Body] Body002
  Group = -> [Sketch013,Sketch012,Sketch014,AdditiveLoft001,Sketch011,Pad002,Sketch010,Pocket004,Sketch008,Pocket003,Sketch009,Pocket005,Chamfer002,Chamfer003,Fillet001]
  Origin = -> Origin005
  Tip = -> Fillet001
FEATURE [Sketcher::SketchObject] Sketch015
  AttachmentOffset = pos=(0,0,17.7) rot=(0,0,1;0rad)
  FullyConstrained = false
  MapMode = 5
  Placement = pos=(0,0,17.7) rot=(0,0,1;0rad)
  Support = -> [XY_Plane006]
  sketch-geometry (10):
    g0: LineSegment StartX=-0.2 StartY=1.5 StartZ=0 EndX=0.2 EndY=1.5 EndZ=0
    g1: LineSegment StartX=0.4 StartY=1.7 StartZ=0 EndX=0.4 EndY=4.2 EndZ=0
    g2: LineSegment StartX=0.2 StartY=4.4 StartZ=0 EndX=-0.2 EndY=4.4 EndZ=0
    g3: LineSegment StartX=-0.4 StartY=4.2 StartZ=0 EndX=-0.4 EndY=1.7 EndZ=0
    g4: ArcOfCircle CenterX=-0.2 CenterY=1.7 CenterZ=0 NormalX=0 NormalY=0 NormalZ=1 AngleXU=0 Radius=0.2 StartAngle=3.14159 EndAngle=4.71239
    g5: ArcOfCircle CenterX=0.2 CenterY=1.7 CenterZ=0 NormalX=0 NormalY=0 NormalZ=1 AngleXU=0 Radius=0.2 StartAngle=4.71239 EndAngle=6.28319
    g6: ArcOfCircle CenterX=0.2 CenterY=4.2 CenterZ=0 NormalX=0 NormalY=0 NormalZ=1 AngleXU=0 Radius=0.2 StartAngle=1.4e-15 EndAngle=1.5708
    g7: ArcOfCircle CenterX=-0.2 CenterY=4.2 CenterZ=0 NormalX=0 NormalY=0 NormalZ=1 AngleXU=0 Radius=0.2 StartAngle=1.5708 EndAngle=3.14159
    g8: LineSegment StartX=-0.2 StartY=1.7 StartZ=0 EndX=0 EndY=0 EndZ=0
    g9: LineSegment StartX=0 StartY=0 StartZ=0 EndX=0.2 EndY=1.7 EndZ=0
  constraints (24):
    c: Horizontal(g0)
    c: Horizontal(g2)
    c: Vertical(g1)
    c: Vertical(g3)
    c: Tangent(g3,g4) = -1.5708
    c: Tangent(g0,g4) = -1.5708
    c: Tangent(g0,g5) = -1.5708
    c: Tangent(g1,g5) = -1.5708
    c: Tangent(g1,g6) = -1.5708
    c: Tangent(g2,g6) = -1.5708
    c: Tangent(g2,g7) = -1.5708
    c: Tangent(g3,g7) = -1.5708
    c: Radius(g7) = 0.2
    c: Equal(g7,g6)
    c: Equal(g7,g5)
    c: Equal(g7,g4)
    c: Coincident(g8,g4)
    c: Coincident(g8,g-1)
    c: Coincident(g9,g-1)
    c: Coincident(g9,g5)
    c: Equal(g9,g8)
    c: DistanceX(g3,g1) = 0.8
    c: DistanceY(g-1,g2) = 4.4
    c: DistanceY(g-1,g0) = 1.5
FEATURE [PartDesign::Pad] Pad003
  AllowMultiFace = false
  Direction = (1,1,1)
  Length = 0.02
  Length2 = 100
  Profile = -> Sketch015
  Refine = true
  Type = 0
FEATURE [PartDesign::Body] Body003  label="Indicator001"
  Group = -> [Sketch015,Pad003]
  Origin = -> Origin006
  Tip = -> Pad003
FEATURE [App::Part] Part001  label="Cap2"
  Group = -> [Body002,Body003]
  Origin = -> Origin007
  Placement = pos=(-13.34,40.005,0) rot=(0,0,1;0rad)
  expr: .Placement.Base.x = -13.335
  expr: .Placement.Base.y = 40.005
FEATURE [Sketcher::SketchObject] Sketch020
  AttachmentOffset = pos=(0,0,7) rot=(0,0,1;0rad)
  FullyConstrained = false
  MapMode = 5
  Placement = pos=(0,0,7) rot=(0,0,1;0rad)
  Support = -> [XY_Plane008]
  sketch-geometry (25):
    g0: LineSegment StartX=-0.724089 StartY=5.5 StartZ=0 EndX=-2.12292 EndY=5.12518 EndZ=0
    g1: LineSegment StartX=-2.12292 StartY=5.12518 StartZ=0 EndX=-3.37708 EndY=4.4011 EndZ=0
    g2: LineSegment StartX=-3.37708 StartY=4.4011 StartZ=0 EndX=-4.4011 EndY=3.37708 EndZ=0
    g3: LineSegment StartX=-4.4011 StartY=3.37708 StartZ=0 EndX=-5.12518 EndY=2.12292 EndZ=0
    g4: LineSegment StartX=-5.12518 StartY=2.12292 StartZ=0 EndX=-5.5 EndY=0.724089 EndZ=0
    g5: LineSegment StartX=-5.5 StartY=0.724089 StartZ=0 EndX=-5.5 EndY=-0.724089 EndZ=0
    g6: LineSegment StartX=-5.5 StartY=-0.724089 StartZ=0 EndX=-5.12518 EndY=-2.12292 EndZ=0
    g7: LineSegment StartX=-5.12518 StartY=-2.12292 StartZ=0 EndX=-4.4011 EndY=-3.37708 EndZ=0
    g8: LineSegment StartX=-4.4011 StartY=-3.37708 StartZ=0 EndX=-3.37708 EndY=-4.4011 EndZ=0
    g9: LineSegment StartX=-3.37708 StartY=-4.4011 StartZ=0 EndX=-2.12292 EndY=-5.12518 EndZ=0
    g10: LineSegment StartX=-2.12292 StartY=-5.12518 StartZ=0 EndX=-0.724089 EndY=-5.5 EndZ=0
    g11: LineSegment StartX=-0.724089 StartY=-5.5 StartZ=0 EndX=0.724089 EndY=-5.5 EndZ=0
    g12: LineSegment StartX=0.724089 StartY=-5.5 StartZ=0 EndX=2.12292 EndY=-5.12518 EndZ=0
    g13: LineSegment StartX=2.12292 StartY=-5.12518 StartZ=0 EndX=3.37708 EndY=-4.4011 EndZ=0
    g14: LineSegment StartX=3.37708 StartY=-4.4011 StartZ=0 EndX=4.4011 EndY=-3.37708 EndZ=0
    g15: LineSegment StartX=4.4011 StartY=-3.37708 StartZ=0 EndX=5.12518 EndY=-2.12292 EndZ=0
    g16: LineSegment StartX=5.12518 StartY=-2.12292 StartZ=0 EndX=5.5 EndY=-0.724089 EndZ=0
    g17: LineSegment StartX=5.5 StartY=-0.724089 StartZ=0 EndX=5.5 EndY=0.724089 EndZ=0
    g18: LineSegment StartX=5.5 StartY=0.724089 StartZ=0 EndX=5.12518 EndY=2.12292 EndZ=0
    g19: LineSegment StartX=5.12518 StartY=2.12292 StartZ=0 EndX=4.4011 EndY=3.37708 EndZ=0
    g20: LineSegment StartX=4.4011 StartY=3.37708 StartZ=0 EndX=3.37708 EndY=4.4011 EndZ=0
    g21: LineSegment StartX=3.37708 StartY=4.4011 StartZ=0 EndX=2.12292 EndY=5.12518 EndZ=0
    g22: LineSegment StartX=2.12292 StartY=5.12518 StartZ=0 EndX=0.724089 EndY=5.5 EndZ=0
    g23: LineSegment StartX=0.724089 StartY=5.5 StartZ=0 EndX=-0.724089 EndY=5.5 EndZ=0
    g24: Circle CenterX=0 CenterY=0 CenterZ=0 NormalX=0 NormalY=0 NormalZ=1 AngleXU=0 Radius=5.54746
  constraints (52):
    c: Coincident(g0,g1)
    c: Coincident(g1,g2)
    c: Coincident(g2,g3)
    c: Coincident(g3,g4)
    c: Coincident(g4,g5)
    c: Coincident(g5,g6)
    c: Coincident(g6,g7)
    c: Coincident(g7,g8)
    c: Coincident(g8,g9)
    c: Coincident(g9,g10)
    c: Coincident(g10,g11)
    c: Coincident(g11,g12)
    c: Coincident(g12,g13)
    c: Coincident(g13,g14)
    c: Coincident(g14,g15)
    c: Coincident(g15,g16)
    c: Coincident(g16,g17)
    c: Coincident(g17,g18)
    c: Coincident(g18,g19)
    c: Coincident(g19,g20)
    c: Coincident(g20,g21)
    c: Coincident(g21,g22)
    c: Coincident(g22,g23)
    c: Coincident(g23,g0)
    c: Equal(g0, g1-g23) x23
    c: PointOnObject(g0,g24)
    c: PointOnObject(g1,g24)
    c: PointOnObject(g2,g24)
    c: PointOnObject(g3,g24)
    c: PointOnObject(g4,g24)
    c: PointOnObject(g5,g24)
    c: PointOnObject(g6,g24)
    c: PointOnObject(g7,g24)
    c: PointOnObject(g8,g24)
    c: PointOnObject(g9,g24)
    c: PointOnObject(g10,g24)
    c: PointOnObject(g11,g24)
    c: PointOnObject(g12,g24)
    c: PointOnObject(g13,g24)
    c: PointOnObject(g14,g24)
    c: PointOnObject(g15,g24)
    c: PointOnObject(g16,g24)
    c: PointOnObject(g17,g24)
    c: PointOnObject(g18,g24)
    c: PointOnObject(g19,g24)
    c: PointOnObject(g20,g24)
    c: PointOnObject(g21,g24)
    c: PointOnObject(g22,g24)
    c: PointOnObject(g23,g24)
    c: Coincident(g24,g-1)
    c: Horizontal(g23)
    c: DistanceX(g4,g17) = 11
FEATURE [Sketcher::SketchObject] Sketch021
  FullyConstrained = false
  MapMode = 5
  Support = -> [XY_Plane008]
  sketch-geometry (25):
    g0: LineSegment StartX=-0.789915 StartY=6 StartZ=0 EndX=-2.31591 EndY=5.59111 EndZ=0
    g1: LineSegment StartX=-2.31591 StartY=5.59111 StartZ=0 EndX=-3.68409 EndY=4.80119 EndZ=0
    g2: LineSegment StartX=-3.68409 StartY=4.80119 StartZ=0 EndX=-4.80119 EndY=3.68409 EndZ=0
    g3: LineSegment StartX=-4.80119 StartY=3.68409 StartZ=0 EndX=-5.59111 EndY=2.31591 EndZ=0
    g4: LineSegment StartX=-5.59111 StartY=2.31591 StartZ=0 EndX=-6 EndY=0.789915 EndZ=0
    g5: LineSegment StartX=-6 StartY=0.789915 StartZ=0 EndX=-6 EndY=-0.789915 EndZ=0
    g6: LineSegment StartX=-6 StartY=-0.789915 StartZ=0 EndX=-5.59111 EndY=-2.31591 EndZ=0
    g7: LineSegment StartX=-5.59111 StartY=-2.31591 StartZ=0 EndX=-4.80119 EndY=-3.68409 EndZ=0
    g8: LineSegment StartX=-4.80119 StartY=-3.68409 StartZ=0 EndX=-3.68409 EndY=-4.80119 EndZ=0
    g9: LineSegment StartX=-3.68409 StartY=-4.80119 StartZ=0 EndX=-2.31591 EndY=-5.59111 EndZ=0
    g10: LineSegment StartX=-2.31591 StartY=-5.59111 StartZ=0 EndX=-0.789915 EndY=-6 EndZ=0
    g11: LineSegment StartX=-0.789915 StartY=-6 StartZ=0 EndX=0.789915 EndY=-6 EndZ=0
    g12: LineSegment StartX=0.789915 StartY=-6 StartZ=0 EndX=2.31591 EndY=-5.59111 EndZ=0
    g13: LineSegment StartX=2.31591 StartY=-5.59111 StartZ=0 EndX=3.68409 EndY=-4.80119 EndZ=0
    g14: LineSegment StartX=3.68409 StartY=-4.80119 StartZ=0 EndX=4.80119 EndY=-3.68409 EndZ=0
    g15: LineSegment StartX=4.80119 StartY=-3.68409 StartZ=0 EndX=5.59111 EndY=-2.31591 EndZ=0
    g16: LineSegment StartX=5.59111 StartY=-2.31591 StartZ=0 EndX=6 EndY=-0.789915 EndZ=0
    g17: LineSegment StartX=6 StartY=-0.789915 StartZ=0 EndX=6 EndY=0.789915 EndZ=0
    g18: LineSegment StartX=6 StartY=0.789915 StartZ=0 EndX=5.59111 EndY=2.31591 EndZ=0
    g19: LineSegment StartX=5.59111 StartY=2.31591 StartZ=0 EndX=4.80119 EndY=3.68409 EndZ=0
    g20: LineSegment StartX=4.80119 StartY=3.68409 StartZ=0 EndX=3.68409 EndY=4.80119 EndZ=0
    g21: LineSegment StartX=3.68409 StartY=4.80119 StartZ=0 EndX=2.31591 EndY=5.59111 EndZ=0
    g22: LineSegment StartX=2.31591 StartY=5.59111 StartZ=0 EndX=0.789915 EndY=6 EndZ=0
    g23: LineSegment StartX=0.789915 StartY=6 StartZ=0 EndX=-0.789915 EndY=6 EndZ=0
    g24: Circle CenterX=0 CenterY=0 CenterZ=0 NormalX=0 NormalY=0 NormalZ=1 AngleXU=0 Radius=6.05177
  constraints (52):
    c: Coincident(g0,g1)
    c: Coincident(g1,g2)
    c: Coincident(g2,g3)
    c: Coincident(g3,g4)
    c: Coincident(g4,g5)
    c: Coincident(g5,g6)
    c: Coincident(g6,g7)
    c: Coincident(g7,g8)
    c: Coincident(g8,g9)
    c: Coincident(g9,g10)
    c: Coincident(g10,g11)
    c: Coincident(g11,g12)
    c: Coincident(g12,g13)
    c: Coincident(g13,g14)
    c: Coincident(g14,g15)
    c: Coincident(g15,g16)
    c: Coincident(g16,g17)
    c: Coincident(g17,g18)
    c: Coincident(g18,g19)
    c: Coincident(g19,g20)
    c: Coincident(g20,g21)
    c: Coincident(g21,g22)
    c: Coincident(g22,g23)
    c: Coincident(g23,g0)
    c: Equal(g0, g1-g23) x23
    c: PointOnObject(g0,g24)
    c: PointOnObject(g1,g24)
    c: PointOnObject(g2,g24)
    c: PointOnObject(g3,g24)
    c: PointOnObject(g4,g24)
    c: PointOnObject(g5,g24)
    c: PointOnObject(g6,g24)
    c: PointOnObject(g7,g24)
    c: PointOnObject(g8,g24)
    c: PointOnObject(g9,g24)
    c: PointOnObject(g10,g24)
    c: PointOnObject(g11,g24)
    c: PointOnObject(g12,g24)
    c: PointOnObject(g13,g24)
    c: PointOnObject(g14,g24)
    c: PointOnObject(g15,g24)
    c: PointOnObject(g16,g24)
    c: PointOnObject(g17,g24)
    c: PointOnObject(g18,g24)
    c: PointOnObject(g19,g24)
    c: PointOnObject(g20,g24)
    c: PointOnObject(g21,g24)
    c: PointOnObject(g22,g24)
    c: PointOnObject(g23,g24)
    c: Coincident(g24,g-1)
    c: Horizontal(g23)
    c: DistanceX(g4,g17) = 12
FEATURE [Sketcher::SketchObject] Sketch022
  AttachmentOffset = pos=(0,0,17) rot=(0,0,1;0rad)
  FullyConstrained = false
  MapMode = 5
  Placement = pos=(0,0,17) rot=(0,0,1;0rad)
  Support = -> [XY_Plane008]
  sketch-geometry (25):
    g0: LineSegment StartX=-4.65926 StartY=1.92993 StartZ=0 EndX=-5 EndY=0.658262 EndZ=0
    g1: LineSegment StartX=-5 StartY=0.658262 StartZ=0 EndX=-5 EndY=-0.658262 EndZ=0
    g2: LineSegment StartX=-5 StartY=-0.658262 StartZ=0 EndX=-4.65926 EndY=-1.92993 EndZ=0
    g3: LineSegment StartX=-4.65926 StartY=-1.92993 StartZ=0 EndX=-4.001 EndY=-3.07007 EndZ=0
    g4: LineSegment StartX=-4.001 StartY=-3.07007 StartZ=0 EndX=-3.07007 EndY=-4.001 EndZ=0
    g5: LineSegment StartX=-3.07007 StartY=-4.001 StartZ=0 EndX=-1.92993 EndY=-4.65926 EndZ=0
    g6: LineSegment StartX=-1.92993 StartY=-4.65926 StartZ=0 EndX=-0.658262 EndY=-5 EndZ=0
    g7: LineSegment StartX=-0.658262 StartY=-5 StartZ=0 EndX=0.658262 EndY=-5 EndZ=0
    g8: LineSegment StartX=0.658262 StartY=-5 StartZ=0 EndX=1.92993 EndY=-4.65926 EndZ=0
    g9: LineSegment StartX=1.92993 StartY=-4.65926 StartZ=0 EndX=3.07007 EndY=-4.001 EndZ=0
    g10: LineSegment StartX=3.07007 StartY=-4.001 StartZ=0 EndX=4.001 EndY=-3.07007 EndZ=0
    g11: LineSegment StartX=4.001 StartY=-3.07007 StartZ=0 EndX=4.65926 EndY=-1.92993 EndZ=0
    g12: LineSegment StartX=4.65926 StartY=-1.92993 StartZ=0 EndX=5 EndY=-0.658262 EndZ=0
    g13: LineSegment StartX=5 StartY=-0.658262 StartZ=0 EndX=5 EndY=0.658262 EndZ=0
    g14: LineSegment StartX=5 StartY=0.658262 StartZ=0 EndX=4.65926 EndY=1.92993 EndZ=0
    g15: LineSegment StartX=4.65926 StartY=1.92993 StartZ=0 EndX=4.001 EndY=3.07007 EndZ=0
    g16: LineSegment StartX=4.001 StartY=3.07007 StartZ=0 EndX=3.07007 EndY=4.001 EndZ=0
    g17: LineSegment StartX=3.07007 StartY=4.001 StartZ=0 EndX=1.92993 EndY=4.65926 EndZ=0
    g18: LineSegment StartX=1.92993 StartY=4.65926 StartZ=0 EndX=0.658262 EndY=5 EndZ=0
    g19: LineSegment StartX=0.658262 StartY=5 StartZ=0 EndX=-0.658262 EndY=5 EndZ=0
    g20: LineSegment StartX=-0.658262 StartY=5 StartZ=0 EndX=-1.92993 EndY=4.65926 EndZ=0
    g21: LineSegment StartX=-1.92993 StartY=4.65926 StartZ=0 EndX=-3.07007 EndY=4.001 EndZ=0
    g22: LineSegment StartX=-3.07007 StartY=4.001 StartZ=0 EndX=-4.001 EndY=3.07007 EndZ=0
    g23: LineSegment StartX=-4.001 StartY=3.07007 StartZ=0 EndX=-4.65926 EndY=1.92993 EndZ=0
    g24: Circle CenterX=0 CenterY=0 CenterZ=0 NormalX=0 NormalY=0 NormalZ=1 AngleXU=0 Radius=5.04314
  constraints (52):
    c: Coincident(g0,g1)
    c: Coincident(g1,g2)
    c: Coincident(g2,g3)
    c: Coincident(g3,g4)
    c: Coincident(g4,g5)
    c: Coincident(g5,g6)
    c: Coincident(g6,g7)
    c: Coincident(g7,g8)
    c: Coincident(g8,g9)
    c: Coincident(g9,g10)
    c: Coincident(g10,g11)
    c: Coincident(g11,g12)
    c: Coincident(g12,g13)
    c: Coincident(g13,g14)
    c: Coincident(g14,g15)
    c: Coincident(g15,g16)
    c: Coincident(g16,g17)
    c: Coincident(g17,g18)
    c: Coincident(g18,g19)
    c: Coincident(g19,g20)
    c: Coincident(g20,g21)
    c: Coincident(g21,g22)
    c: Coincident(g22,g23)
    c: Coincident(g23,g0)
    c: Equal(g0, g1-g23) x23
    c: PointOnObject(g0,g24)
    c: PointOnObject(g1,g24)
    c: PointOnObject(g2,g24)
    c: PointOnObject(g3,g24)
    c: PointOnObject(g4,g24)
    c: PointOnObject(g5,g24)
    c: PointOnObject(g6,g24)
    c: PointOnObject(g7,g24)
    c: PointOnObject(g8,g24)
    c: PointOnObject(g9,g24)
    c: PointOnObject(g10,g24)
    c: PointOnObject(g11,g24)
    c: PointOnObject(g12,g24)
    c: PointOnObject(g13,g24)
    c: PointOnObject(g14,g24)
    c: PointOnObject(g15,g24)
    c: PointOnObject(g16,g24)
    c: PointOnObject(g17,g24)
    c: PointOnObject(g18,g24)
    c: PointOnObject(g19,g24)
    c: PointOnObject(g20,g24)
    c: PointOnObject(g21,g24)
    c: PointOnObject(g22,g24)
    c: PointOnObject(g23,g24)
    c: Coincident(g24,g-1)
    c: Horizontal(g19)
    c: DistanceX(g0,g13) = 10
FEATURE [PartDesign::AdditiveLoft] AdditiveLoft002
  AllowMultiFace = false
  Closed = false
  Profile = -> Sketch021
  Refine = true
  Ruled = false
  Sections = -> [Sketch020,Sketch022]
FEATURE [Sketcher::SketchObject] Sketch019
  FullyConstrained = false
  MapMode = 5
  Placement = pos=(0,0,17) rot=(0,0,1;0rad)
  Support = -> [AdditiveLoft002]
  sketch-geometry (1):
    g0: Circle CenterX=0 CenterY=0 CenterZ=0 NormalX=0 NormalY=0 NormalZ=1 AngleXU=0 Radius=4.5
  constraints (2):
    c: Coincident(g0,g-1)
    c: Radius(g0) = 4.5
FEATURE [PartDesign::Pad] Pad004
  AllowMultiFace = false
  BaseFeature = -> AdditiveLoft002
  Direction = (1,1,1)
  Length = 0.7
  Length2 = 100
  Profile = -> Sketch019
  Refine = true
  Type = 0
FEATURE [Sketcher::SketchObject] Sketch018
  FullyConstrained = false
  MapMode = 5
  Placement = pos=(0,0,0) rot=(1,0,0;3.14159rad)
  Support = -> [Pad004]
  sketch-geometry (1):
    g0: Circle CenterX=0 CenterY=0 CenterZ=0 NormalX=0 NormalY=0 NormalZ=1 AngleXU=0 Radius=5
  constraints (2):
    c: Coincident(g0,g-1)
    c: Radius(g0) = 5
FEATURE [PartDesign::Pocket] Pocket007
  AllowMultiFace = false
  BaseFeature = -> Pad004
  Direction = (1,1,1)
  Length = 1
  Length2 = 100
  Profile = -> Sketch018
  Refine = true
  Type = 0
FEATURE [Sketcher::SketchObject] Sketch016
  FullyConstrained = false
  MapMode = 5
  Placement = pos=(0,0,1) rot=(1,0,0;3.14159rad)
  Support = -> [Pocket007]
  sketch-geometry (1):
    g0: Circle CenterX=0 CenterY=0 CenterZ=0 NormalX=0 NormalY=0 NormalZ=1 AngleXU=0 Radius=4.65
  constraints (2):
    c: Coincident(g0,g-1)
    c: Radius(g0) = 4.65
FEATURE [PartDesign::Pocket] Pocket006
  AllowMultiFace = false
  BaseFeature = -> Pocket007
  Direction = (1,1,1)
  Length = 1
  Length2 = 100
  Profile = -> Sketch016
  Refine = true
  Type = 0
FEATURE [Sketcher::SketchObject] Sketch017
  FullyConstrained = false
  MapMode = 5
  Placement = pos=(0,0,2) rot=(1,0,0;3.14159rad)
  Support = -> [Pocket006]
  sketch-geometry (2):
    g0: ArcOfCircle CenterX=0 CenterY=0 CenterZ=0 NormalX=0 NormalY=0 NormalZ=1 AngleXU=0 Radius=3 StartAngle=2.19024 EndAngle=7.23453
    g1: LineSegment StartX=-1.74176 StartY=2.4426 StartZ=0 EndX=1.74176 EndY=2.4426 EndZ=0
  constraints (5):
    c: Coincident(g0,g-1)
    c: Coincident(g1,g0)
    c: Coincident(g1,g0)
    c: Horizontal(g1)
    c: Radius(g0) = 3
FEATURE [PartDesign::Pocket] Pocket008
  AllowMultiFace = false
  BaseFeature = -> Pocket006
  Direction = (1,1,1)
  Length = 8
  Length2 = 100
  Profile = -> Sketch017
  Refine = true
  Type = 0
FEATURE [PartDesign::Chamfer] Chamfer005
  Angle = 45
  Base = -> Pocket008 [Edge82,Edge83]
  BaseFeature = -> Pocket008
  ChamferType = 0
  FlipDirection = false
  Size = 1.4
  Size2 = 1
  SupportTransform = false
  UseAllEdges = false
FEATURE [PartDesign::Chamfer] Chamfer004
  Angle = 45
  Base = -> Chamfer005 [Edge8]
  BaseFeature = -> Chamfer005
  ChamferType = 0
  FlipDirection = false
  Size = 0.3
  Size2 = 1
  SupportTransform = false
  UseAllEdges = false
FEATURE [PartDesign::Fillet] Fillet002
  Base = -> Chamfer004 [Edge93,Face36]
  BaseFeature = -> Chamfer004
  Radius = 0.1
  SupportTransform = false
  UseAllEdges = false
FEATURE [PartDesign::Body] Body004
  Group = -> [Sketch021,Sketch020,Sketch022,AdditiveLoft002,Sketch019,Pad004,Sketch018,Pocket007,Sketch016,Pocket006,Sketch017,Pocket008,Chamfer005,Chamfer004,Fillet002]
  Origin = -> Origin010
  Tip = -> Fillet002
FEATURE [Sketcher::SketchObject] Sketch023
  AttachmentOffset = pos=(0,0,17.7) rot=(0,0,1;0rad)
  FullyConstrained = false
  MapMode = 5
  Placement = pos=(0,0,17.7) rot=(0,0,1;0rad)
  Support = -> [XY_Plane009]
  sketch-geometry (10):
    g0: LineSegment StartX=-0.2 StartY=1.5 StartZ=0 EndX=0.2 EndY=1.5 EndZ=0
    g1: LineSegment StartX=0.4 StartY=1.7 StartZ=0 EndX=0.4 EndY=4.2 EndZ=0
    g2: LineSegment StartX=0.2 StartY=4.4 StartZ=0 EndX=-0.2 EndY=4.4 EndZ=0
    g3: LineSegment StartX=-0.4 StartY=4.2 StartZ=0 EndX=-0.4 EndY=1.7 EndZ=0
    g4: ArcOfCircle CenterX=-0.2 CenterY=1.7 CenterZ=0 NormalX=0 NormalY=0 NormalZ=1 AngleXU=0 Radius=0.2 StartAngle=3.14159 EndAngle=4.71239
    g5: ArcOfCircle CenterX=0.2 CenterY=1.7 CenterZ=0 NormalX=0 NormalY=0 NormalZ=1 AngleXU=0 Radius=0.2 StartAngle=4.71239 EndAngle=6.28319
    g6: ArcOfCircle CenterX=0.2 CenterY=4.2 CenterZ=0 NormalX=0 NormalY=0 NormalZ=1 AngleXU=0 Radius=0.2 StartAngle=1.4e-15 EndAngle=1.5708
    g7: ArcOfCircle CenterX=-0.2 CenterY=4.2 CenterZ=0 NormalX=0 NormalY=0 NormalZ=1 AngleXU=0 Radius=0.2 StartAngle=1.5708 EndAngle=3.14159
    g8: LineSegment StartX=-0.2 StartY=1.7 StartZ=0 EndX=0 EndY=0 EndZ=0
    g9: LineSegment StartX=0 StartY=0 StartZ=0 EndX=0.2 EndY=1.7 EndZ=0
  constraints (24):
    c: Horizontal(g0)
    c: Horizontal(g2)
    c: Vertical(g1)
    c: Vertical(g3)
    c: Tangent(g3,g4) = -1.5708
    c: Tangent(g0,g4) = -1.5708
    c: Tangent(g0,g5) = -1.5708
    c: Tangent(g1,g5) = -1.5708
    c: Tangent(g1,g6) = -1.5708
    c: Tangent(g2,g6) = -1.5708
    c: Tangent(g2,g7) = -1.5708
    c: Tangent(g3,g7) = -1.5708
    c: Radius(g7) = 0.2
    c: Equal(g7,g6)
    c: Equal(g7,g5)
    c: Equal(g7,g4)
    c: Coincident(g8,g4)
    c: Coincident(g8,g-1)
    c: Coincident(g9,g-1)
    c: Coincident(g9,g5)
    c: Equal(g9,g8)
    c: DistanceX(g3,g1) = 0.8
    c: DistanceY(g-1,g2) = 4.4
    c: DistanceY(g-1,g0) = 1.5
FEATURE [PartDesign::Pad] Pad005
  AllowMultiFace = false
  Direction = (1,1,1)
  Length = 0.02
  Length2 = 100
  Profile = -> Sketch023
  Refine = true
  Type = 0
FEATURE [PartDesign::Body] Body005  label="Indicator002"
  Group = -> [Sketch023,Pad005]
  Origin = -> Origin009
  Tip = -> Pad005
FEATURE [App::Part] Part002  label="Cap3"
  Group = -> [Body004,Body005]
  Origin = -> Origin008
  Placement = pos=(13.335,40.005,0) rot=(0,0,1;0rad)
  expr: .Placement.Base.x = 13.335
  expr: .Placement.Base.y = 40.005
FEATURE [Sketcher::SketchObject] Sketch028
  AttachmentOffset = pos=(0,0,7) rot=(0,0,1;0rad)
  FullyConstrained = false
  MapMode = 5
  Placement = pos=(0,0,7) rot=(0,0,1;0rad)
  Support = -> [XY_Plane011]
  sketch-geometry (25):
    g0: LineSegment StartX=-0.724089 StartY=5.5 StartZ=0 EndX=-2.12292 EndY=5.12518 EndZ=0
    g1: LineSegment StartX=-2.12292 StartY=5.12518 StartZ=0 EndX=-3.37708 EndY=4.4011 EndZ=0
    g2: LineSegment StartX=-3.37708 StartY=4.4011 StartZ=0 EndX=-4.4011 EndY=3.37708 EndZ=0
    g3: LineSegment StartX=-4.4011 StartY=3.37708 StartZ=0 EndX=-5.12518 EndY=2.12292 EndZ=0
    g4: LineSegment StartX=-5.12518 StartY=2.12292 StartZ=0 EndX=-5.5 EndY=0.724089 EndZ=0
    g5: LineSegment StartX=-5.5 StartY=0.724089 StartZ=0 EndX=-5.5 EndY=-0.724089 EndZ=0
    g6: LineSegment StartX=-5.5 StartY=-0.724089 StartZ=0 EndX=-5.12518 EndY=-2.12292 EndZ=0
    g7: LineSegment StartX=-5.12518 StartY=-2.12292 StartZ=0 EndX=-4.4011 EndY=-3.37708 EndZ=0
    g8: LineSegment StartX=-4.4011 StartY=-3.37708 StartZ=0 EndX=-3.37708 EndY=-4.4011 EndZ=0
    g9: LineSegment StartX=-3.37708 StartY=-4.4011 StartZ=0 EndX=-2.12292 EndY=-5.12518 EndZ=0
    g10: LineSegment StartX=-2.12292 StartY=-5.12518 StartZ=0 EndX=-0.724089 EndY=-5.5 EndZ=0
    g11: LineSegment StartX=-0.724089 StartY=-5.5 StartZ=0 EndX=0.724089 EndY=-5.5 EndZ=0
    g12: LineSegment StartX=0.724089 StartY=-5.5 StartZ=0 EndX=2.12292 EndY=-5.12518 EndZ=0
    g13: LineSegment StartX=2.12292 StartY=-5.12518 StartZ=0 EndX=3.37708 EndY=-4.4011 EndZ=0
    g14: LineSegment StartX=3.37708 StartY=-4.4011 StartZ=0 EndX=4.4011 EndY=-3.37708 EndZ=0
    g15: LineSegment StartX=4.4011 StartY=-3.37708 StartZ=0 EndX=5.12518 EndY=-2.12292 EndZ=0
    g16: LineSegment StartX=5.12518 StartY=-2.12292 StartZ=0 EndX=5.5 EndY=-0.724089 EndZ=0
    g17: LineSegment StartX=5.5 StartY=-0.724089 StartZ=0 EndX=5.5 EndY=0.724089 EndZ=0
    g18: LineSegment StartX=5.5 StartY=0.724089 StartZ=0 EndX=5.12518 EndY=2.12292 EndZ=0
    g19: LineSegment StartX=5.12518 StartY=2.12292 StartZ=0 EndX=4.4011 EndY=3.37708 EndZ=0
    g20: LineSegment StartX=4.4011 StartY=3.37708 StartZ=0 EndX=3.37708 EndY=4.4011 EndZ=0
    g21: LineSegment StartX=3.37708 StartY=4.4011 StartZ=0 EndX=2.12292 EndY=5.12518 EndZ=0
    g22: LineSegment StartX=2.12292 StartY=5.12518 StartZ=0 EndX=0.724089 EndY=5.5 EndZ=0
    g23: LineSegment StartX=0.724089 StartY=5.5 StartZ=0 EndX=-0.724089 EndY=5.5 EndZ=0
    g24: Circle CenterX=0 CenterY=0 CenterZ=0 NormalX=0 NormalY=0 NormalZ=1 AngleXU=0 Radius=5.54746
  constraints (52):
    c: Coincident(g0,g1)
    c: Coincident(g1,g2)
    c: Coincident(g2,g3)
    c: Coincident(g3,g4)
    c: Coincident(g4,g5)
    c: Coincident(g5,g6)
    c: Coincident(g6,g7)
    c: Coincident(g7,g8)
    c: Coincident(g8,g9)
    c: Coincident(g9,g10)
    c: Coincident(g10,g11)
    c: Coincident(g11,g12)
    c: Coincident(g12,g13)
    c: Coincident(g13,g14)
    c: Coincident(g14,g15)
    c: Coincident(g15,g16)
    c: Coincident(g16,g17)
    c: Coincident(g17,g18)
    c: Coincident(g18,g19)
    c: Coincident(g19,g20)
    c: Coincident(g20,g21)
    c: Coincident(g21,g22)
    c: Coincident(g22,g23)
    c: Coincident(g23,g0)
    c: Equal(g0, g1-g23) x23
    c: PointOnObject(g0,g24)
    c: PointOnObject(g1,g24)
    c: PointOnObject(g2,g24)
    c: PointOnObject(g3,g24)
    c: PointOnObject(g4,g24)
    c: PointOnObject(g5,g24)
    c: PointOnObject(g6,g24)
    c: PointOnObject(g7,g24)
    c: PointOnObject(g8,g24)
    c: PointOnObject(g9,g24)
    c: PointOnObject(g10,g24)
    c: PointOnObject(g11,g24)
    c: PointOnObject(g12,g24)
    c: PointOnObject(g13,g24)
    c: PointOnObject(g14,g24)
    c: PointOnObject(g15,g24)
    c: PointOnObject(g16,g24)
    c: PointOnObject(g17,g24)
    c: PointOnObject(g18,g24)
    c: PointOnObject(g19,g24)
    c: PointOnObject(g20,g24)
    c: PointOnObject(g21,g24)
    c: PointOnObject(g22,g24)
    c: PointOnObject(g23,g24)
    c: Coincident(g24,g-1)
    c: Horizontal(g23)
    c: DistanceX(g4,g17) = 11
FEATURE [Sketcher::SketchObject] Sketch029
  FullyConstrained = false
  MapMode = 5
  Support = -> [XY_Plane011]
  sketch-geometry (25):
    g0: LineSegment StartX=-0.789915 StartY=6 StartZ=0 EndX=-2.31591 EndY=5.59111 EndZ=0
    g1: LineSegment StartX=-2.31591 StartY=5.59111 StartZ=0 EndX=-3.68409 EndY=4.80119 EndZ=0
    g2: LineSegment StartX=-3.68409 StartY=4.80119 StartZ=0 EndX=-4.80119 EndY=3.68409 EndZ=0
    g3: LineSegment StartX=-4.80119 StartY=3.68409 StartZ=0 EndX=-5.59111 EndY=2.31591 EndZ=0
    g4: LineSegment StartX=-5.59111 StartY=2.31591 StartZ=0 EndX=-6 EndY=0.789915 EndZ=0
    g5: LineSegment StartX=-6 StartY=0.789915 StartZ=0 EndX=-6 EndY=-0.789915 EndZ=0
    g6: LineSegment StartX=-6 StartY=-0.789915 StartZ=0 EndX=-5.59111 EndY=-2.31591 EndZ=0
    g7: LineSegment StartX=-5.59111 StartY=-2.31591 StartZ=0 EndX=-4.80119 EndY=-3.68409 EndZ=0
    g8: LineSegment StartX=-4.80119 StartY=-3.68409 StartZ=0 EndX=-3.68409 EndY=-4.80119 EndZ=0
    g9: LineSegment StartX=-3.68409 StartY=-4.80119 StartZ=0 EndX=-2.31591 EndY=-5.59111 EndZ=0
    g10: LineSegment StartX=-2.31591 StartY=-5.59111 StartZ=0 EndX=-0.789915 EndY=-6 EndZ=0
    g11: LineSegment StartX=-0.789915 StartY=-6 StartZ=0 EndX=0.789915 EndY=-6 EndZ=0
    g12: LineSegment StartX=0.789915 StartY=-6 StartZ=0 EndX=2.31591 EndY=-5.59111 EndZ=0
    g13: LineSegment StartX=2.31591 StartY=-5.59111 StartZ=0 EndX=3.68409 EndY=-4.80119 EndZ=0
    g14: LineSegment StartX=3.68409 StartY=-4.80119 StartZ=0 EndX=4.80119 EndY=-3.68409 EndZ=0
    g15: LineSegment StartX=4.80119 StartY=-3.68409 StartZ=0 EndX=5.59111 EndY=-2.31591 EndZ=0
    g16: LineSegment StartX=5.59111 StartY=-2.31591 StartZ=0 EndX=6 EndY=-0.789915 EndZ=0
    g17: LineSegment StartX=6 StartY=-0.789915 StartZ=0 EndX=6 EndY=0.789915 EndZ=0
    g18: LineSegment StartX=6 StartY=0.789915 StartZ=0 EndX=5.59111 EndY=2.31591 EndZ=0
    g19: LineSegment StartX=5.59111 StartY=2.31591 StartZ=0 EndX=4.80119 EndY=3.68409 EndZ=0
    g20: LineSegment StartX=4.80119 StartY=3.68409 StartZ=0 EndX=3.68409 EndY=4.80119 EndZ=0
    g21: LineSegment StartX=3.68409 StartY=4.80119 StartZ=0 EndX=2.31591 EndY=5.59111 EndZ=0
    g22: LineSegment StartX=2.31591 StartY=5.59111 StartZ=0 EndX=0.789915 EndY=6 EndZ=0
    g23: LineSegment StartX=0.789915 StartY=6 StartZ=0 EndX=-0.789915 EndY=6 EndZ=0
    g24: Circle CenterX=0 CenterY=0 CenterZ=0 NormalX=0 NormalY=0 NormalZ=1 AngleXU=0 Radius=6.05177
  constraints (52):
    c: Coincident(g0,g1)
    c: Coincident(g1,g2)
    c: Coincident(g2,g3)
    c: Coincident(g3,g4)
    c: Coincident(g4,g5)
    c: Coincident(g5,g6)
    c: Coincident(g6,g7)
    c: Coincident(g7,g8)
    c: Coincident(g8,g9)
    c: Coincident(g9,g10)
    c: Coincident(g10,g11)
    c: Coincident(g11,g12)
    c: Coincident(g12,g13)
    c: Coincident(g13,g14)
    c: Coincident(g14,g15)
    c: Coincident(g15,g16)
    c: Coincident(g16,g17)
    c: Coincident(g17,g18)
    c: Coincident(g18,g19)
    c: Coincident(g19,g20)
    c: Coincident(g20,g21)
    c: Coincident(g21,g22)
    c: Coincident(g22,g23)
    c: Coincident(g23,g0)
    c: Equal(g0, g1-g23) x23
    c: PointOnObject(g0,g24)
    c: PointOnObject(g1,g24)
    c: PointOnObject(g2,g24)
    c: PointOnObject(g3,g24)
    c: PointOnObject(g4,g24)
    c: PointOnObject(g5,g24)
    c: PointOnObject(g6,g24)
    c: PointOnObject(g7,g24)
    c: PointOnObject(g8,g24)
    c: PointOnObject(g9,g24)
    c: PointOnObject(g10,g24)
    c: PointOnObject(g11,g24)
    c: PointOnObject(g12,g24)
    c: PointOnObject(g13,g24)
    c: PointOnObject(g14,g24)
    c: PointOnObject(g15,g24)
    c: PointOnObject(g16,g24)
    c: PointOnObject(g17,g24)
    c: PointOnObject(g18,g24)
    c: PointOnObject(g19,g24)
    c: PointOnObject(g20,g24)
    c: PointOnObject(g21,g24)
    c: PointOnObject(g22,g24)
    c: PointOnObject(g23,g24)
    c: Coincident(g24,g-1)
    c: Horizontal(g23)
    c: DistanceX(g4,g17) = 12
FEATURE [Sketcher::SketchObject] Sketch030
  AttachmentOffset = pos=(0,0,17) rot=(0,0,1;0rad)
  FullyConstrained = false
  MapMode = 5
  Placement = pos=(0,0,17) rot=(0,0,1;0rad)
  Support = -> [XY_Plane011]
  sketch-geometry (25):
    g0: LineSegment StartX=-4.65926 StartY=1.92993 StartZ=0 EndX=-5 EndY=0.658262 EndZ=0
    g1: LineSegment StartX=-5 StartY=0.658262 StartZ=0 EndX=-5 EndY=-0.658262 EndZ=0
    g2: LineSegment StartX=-5 StartY=-0.658262 StartZ=0 EndX=-4.65926 EndY=-1.92993 EndZ=0
    g3: LineSegment StartX=-4.65926 StartY=-1.92993 StartZ=0 EndX=-4.001 EndY=-3.07007 EndZ=0
    g4: LineSegment StartX=-4.001 StartY=-3.07007 StartZ=0 EndX=-3.07007 EndY=-4.001 EndZ=0
    g5: LineSegment StartX=-3.07007 StartY=-4.001 StartZ=0 EndX=-1.92993 EndY=-4.65926 EndZ=0
    g6: LineSegment StartX=-1.92993 StartY=-4.65926 StartZ=0 EndX=-0.658262 EndY=-5 EndZ=0
    g7: LineSegment StartX=-0.658262 StartY=-5 StartZ=0 EndX=0.658262 EndY=-5 EndZ=0
    g8: LineSegment StartX=0.658262 StartY=-5 StartZ=0 EndX=1.92993 EndY=-4.65926 EndZ=0
    g9: LineSegment StartX=1.92993 StartY=-4.65926 StartZ=0 EndX=3.07007 EndY=-4.001 EndZ=0
    g10: LineSegment StartX=3.07007 StartY=-4.001 StartZ=0 EndX=4.001 EndY=-3.07007 EndZ=0
    g11: LineSegment StartX=4.001 StartY=-3.07007 StartZ=0 EndX=4.65926 EndY=-1.92993 EndZ=0
    g12: LineSegment StartX=4.65926 StartY=-1.92993 StartZ=0 EndX=5 EndY=-0.658262 EndZ=0
    g13: LineSegment StartX=5 StartY=-0.658262 StartZ=0 EndX=5 EndY=0.658262 EndZ=0
    g14: LineSegment StartX=5 StartY=0.658262 StartZ=0 EndX=4.65926 EndY=1.92993 EndZ=0
    g15: LineSegment StartX=4.65926 StartY=1.92993 StartZ=0 EndX=4.001 EndY=3.07007 EndZ=0
    g16: LineSegment StartX=4.001 StartY=3.07007 StartZ=0 EndX=3.07007 EndY=4.001 EndZ=0
    g17: LineSegment StartX=3.07007 StartY=4.001 StartZ=0 EndX=1.92993 EndY=4.65926 EndZ=0
    g18: LineSegment StartX=1.92993 StartY=4.65926 StartZ=0 EndX=0.658262 EndY=5 EndZ=0
    g19: LineSegment StartX=0.658262 StartY=5 StartZ=0 EndX=-0.658262 EndY=5 EndZ=0
    g20: LineSegment StartX=-0.658262 StartY=5 StartZ=0 EndX=-1.92993 EndY=4.65926 EndZ=0
    g21: LineSegment StartX=-1.92993 StartY=4.65926 StartZ=0 EndX=-3.07007 EndY=4.001 EndZ=0
    g22: LineSegment StartX=-3.07007 StartY=4.001 StartZ=0 EndX=-4.001 EndY=3.07007 EndZ=0
    g23: LineSegment StartX=-4.001 StartY=3.07007 StartZ=0 EndX=-4.65926 EndY=1.92993 EndZ=0
    g24: Circle CenterX=0 CenterY=0 CenterZ=0 NormalX=0 NormalY=0 NormalZ=1 AngleXU=0 Radius=5.04314
  constraints (52):
    c: Coincident(g0,g1)
    c: Coincident(g1,g2)
    c: Coincident(g2,g3)
    c: Coincident(g3,g4)
    c: Coincident(g4,g5)
    c: Coincident(g5,g6)
    c: Coincident(g6,g7)
    c: Coincident(g7,g8)
    c: Coincident(g8,g9)
    c: Coincident(g9,g10)
    c: Coincident(g10,g11)
    c: Coincident(g11,g12)
    c: Coincident(g12,g13)
    c: Coincident(g13,g14)
    c: Coincident(g14,g15)
    c: Coincident(g15,g16)
    c: Coincident(g16,g17)
    c: Coincident(g17,g18)
    c: Coincident(g18,g19)
    c: Coincident(g19,g20)
    c: Coincident(g20,g21)
    c: Coincident(g21,g22)
    c: Coincident(g22,g23)
    c: Coincident(g23,g0)
    c: Equal(g0, g1-g23) x23
    c: PointOnObject(g0,g24)
    c: PointOnObject(g1,g24)
    c: PointOnObject(g2,g24)
    c: PointOnObject(g3,g24)
    c: PointOnObject(g4,g24)
    c: PointOnObject(g5,g24)
    c: PointOnObject(g6,g24)
    c: PointOnObject(g7,g24)
    c: PointOnObject(g8,g24)
    c: PointOnObject(g9,g24)
    c: PointOnObject(g10,g24)
    c: PointOnObject(g11,g24)
    c: PointOnObject(g12,g24)
    c: PointOnObject(g13,g24)
    c: PointOnObject(g14,g24)
    c: PointOnObject(g15,g24)
    c: PointOnObject(g16,g24)
    c: PointOnObject(g17,g24)
    c: PointOnObject(g18,g24)
    c: PointOnObject(g19,g24)
    c: PointOnObject(g20,g24)
    c: PointOnObject(g21,g24)
    c: PointOnObject(g22,g24)
    c: PointOnObject(g23,g24)
    c: Coincident(g24,g-1)
    c: Horizontal(g19)
    c: DistanceX(g0,g13) = 10
FEATURE [PartDesign::AdditiveLoft] AdditiveLoft003
  AllowMultiFace = false
  Closed = false
  Profile = -> Sketch029
  Refine = true
  Ruled = false
  Sections = -> [Sketch028,Sketch030]
FEATURE [Sketcher::SketchObject] Sketch027
  FullyConstrained = false
  MapMode = 5
  Placement = pos=(0,0,17) rot=(0,0,1;0rad)
  Support = -> [AdditiveLoft003]
  sketch-geometry (1):
    g0: Circle CenterX=0 CenterY=0 CenterZ=0 NormalX=0 NormalY=0 NormalZ=1 AngleXU=0 Radius=4.5
  constraints (2):
    c: Coincident(g0,g-1)
    c: Radius(g0) = 4.5
FEATURE [PartDesign::Pad] Pad006
  AllowMultiFace = false
  BaseFeature = -> AdditiveLoft003
  Direction = (1,1,1)
  Length = 0.7
  Length2 = 100
  Profile = -> Sketch027
  Refine = true
  Type = 0
FEATURE [Sketcher::SketchObject] Sketch026
  FullyConstrained = false
  MapMode = 5
  Placement = pos=(0,0,0) rot=(1,0,0;3.14159rad)
  Support = -> [Pad006]
  sketch-geometry (1):
    g0: Circle CenterX=0 CenterY=0 CenterZ=0 NormalX=0 NormalY=0 NormalZ=1 AngleXU=0 Radius=5
  constraints (2):
    c: Coincident(g0,g-1)
    c: Radius(g0) = 5
FEATURE [PartDesign::Pocket] Pocket010
  AllowMultiFace = false
  BaseFeature = -> Pad006
  Direction = (1,1,1)
  Length = 1
  Length2 = 100
  Profile = -> Sketch026
  Refine = true
  Type = 0
FEATURE [Sketcher::SketchObject] Sketch024
  FullyConstrained = false
  MapMode = 5
  Placement = pos=(0,0,1) rot=(1,0,0;3.14159rad)
  Support = -> [Pocket010]
  sketch-geometry (1):
    g0: Circle CenterX=0 CenterY=0 CenterZ=0 NormalX=0 NormalY=0 NormalZ=1 AngleXU=0 Radius=4.65
  constraints (2):
    c: Coincident(g0,g-1)
    c: Radius(g0) = 4.65
FEATURE [PartDesign::Pocket] Pocket009
  AllowMultiFace = false
  BaseFeature = -> Pocket010
  Direction = (1,1,1)
  Length = 1
  Length2 = 100
  Profile = -> Sketch024
  Refine = true
  Type = 0
FEATURE [Sketcher::SketchObject] Sketch025
  FullyConstrained = false
  MapMode = 5
  Placement = pos=(0,0,2) rot=(1,0,0;3.14159rad)
  Support = -> [Pocket009]
  sketch-geometry (2):
    g0: ArcOfCircle CenterX=0 CenterY=0 CenterZ=0 NormalX=0 NormalY=0 NormalZ=1 AngleXU=0 Radius=3 StartAngle=2.19024 EndAngle=7.23453
    g1: LineSegment StartX=-1.74176 StartY=2.4426 StartZ=0 EndX=1.74176 EndY=2.4426 EndZ=0
  constraints (5):
    c: Coincident(g0,g-1)
    c: Coincident(g1,g0)
    c: Coincident(g1,g0)
    c: Horizontal(g1)
    c: Radius(g0) = 3
FEATURE [PartDesign::Pocket] Pocket011
  AllowMultiFace = false
  BaseFeature = -> Pocket009
  Direction = (1,1,1)
  Length = 8
  Length2 = 100
  Profile = -> Sketch025
  Refine = true
  Type = 0
FEATURE [PartDesign::Chamfer] Chamfer007
  Angle = 45
  Base = -> Pocket011 [Edge82,Edge83]
  BaseFeature = -> Pocket011
  ChamferType = 0
  FlipDirection = false
  Size = 1.4
  Size2 = 1
  SupportTransform = false
  UseAllEdges = false
FEATURE [PartDesign::Chamfer] Chamfer006
  Angle = 45
  Base = -> Chamfer007 [Edge8]
  BaseFeature = -> Chamfer007
  ChamferType = 0
  FlipDirection = false
  Size = 0.3
  Size2 = 1
  SupportTransform = false
  UseAllEdges = false
FEATURE [PartDesign::Fillet] Fillet003
  Base = -> Chamfer006 [Edge93,Face36]
  BaseFeature = -> Chamfer006
  Radius = 0.1
  SupportTransform = false
  UseAllEdges = false
FEATURE [PartDesign::Body] Body006
  Group = -> [Sketch029,Sketch028,Sketch030,AdditiveLoft003,Sketch027,Pad006,Sketch026,Pocket010,Sketch024,Pocket009,Sketch025,Pocket011,Chamfer007,Chamfer006,Fillet003]
  Origin = -> Origin013
  Tip = -> Fillet003
FEATURE [Sketcher::SketchObject] Sketch031
  AttachmentOffset = pos=(0,0,17.7) rot=(0,0,1;0rad)
  FullyConstrained = false
  MapMode = 5
  Placement = pos=(0,0,17.7) rot=(0,0,1;0rad)
  Support = -> [XY_Plane012]
  sketch-geometry (10):
    g0: LineSegment StartX=-0.2 StartY=1.5 StartZ=0 EndX=0.2 EndY=1.5 EndZ=0
    g1: LineSegment StartX=0.4 StartY=1.7 StartZ=0 EndX=0.4 EndY=4.2 EndZ=0
    g2: LineSegment StartX=0.2 StartY=4.4 StartZ=0 EndX=-0.2 EndY=4.4 EndZ=0
    g3: LineSegment StartX=-0.4 StartY=4.2 StartZ=0 EndX=-0.4 EndY=1.7 EndZ=0
    g4: ArcOfCircle CenterX=-0.2 CenterY=1.7 CenterZ=0 NormalX=0 NormalY=0 NormalZ=1 AngleXU=0 Radius=0.2 StartAngle=3.14159 EndAngle=4.71239
    g5: ArcOfCircle CenterX=0.2 CenterY=1.7 CenterZ=0 NormalX=0 NormalY=0 NormalZ=1 AngleXU=0 Radius=0.2 StartAngle=4.71239 EndAngle=6.28319
    g6: ArcOfCircle CenterX=0.2 CenterY=4.2 CenterZ=0 NormalX=0 NormalY=0 NormalZ=1 AngleXU=0 Radius=0.2 StartAngle=1.4e-15 EndAngle=1.5708
    g7: ArcOfCircle CenterX=-0.2 CenterY=4.2 CenterZ=0 NormalX=0 NormalY=0 NormalZ=1 AngleXU=0 Radius=0.2 StartAngle=1.5708 EndAngle=3.14159
    g8: LineSegment StartX=-0.2 StartY=1.7 StartZ=0 EndX=0 EndY=0 EndZ=0
    g9: LineSegment StartX=0 StartY=0 StartZ=0 EndX=0.2 EndY=1.7 EndZ=0
  constraints (24):
    c: Horizontal(g0)
    c: Horizontal(g2)
    c: Vertical(g1)
    c: Vertical(g3)
    c: Tangent(g3,g4) = -1.5708
    c: Tangent(g0,g4) = -1.5708
    c: Tangent(g0,g5) = -1.5708
    c: Tangent(g1,g5) = -1.5708
    c: Tangent(g1,g6) = -1.5708
    c: Tangent(g2,g6) = -1.5708
    c: Tangent(g2,g7) = -1.5708
    c: Tangent(g3,g7) = -1.5708
    c: Radius(g7) = 0.2
    c: Equal(g7,g6)
    c: Equal(g7,g5)
    c: Equal(g7,g4)
    c: Coincident(g8,g4)
    c: Coincident(g8,g-1)
    c: Coincident(g9,g-1)
    c: Coincident(g9,g5)
    c: Equal(g9,g8)
    c: DistanceX(g3,g1) = 0.8
    c: DistanceY(g-1,g2) = 4.4
    c: DistanceY(g-1,g0) = 1.5
FEATURE [PartDesign::Pad] Pad007
  AllowMultiFace = false
  Direction = (1,1,1)
  Length = 0.02
  Length2 = 100
  Profile = -> Sketch031
  Refine = true
  Type = 0
FEATURE [PartDesign::Body] Body007  label="Indicator003"
  Group = -> [Sketch031,Pad007]
  Origin = -> Origin012
  Tip = -> Pad007
FEATURE [App::Part] Part003  label="Cap4"
  Group = -> [Body006,Body007]
  Origin = -> Origin011
  Placement = pos=(40.005,40.005,0) rot=(0,0,1;0rad)
  expr: .Placement.Base.x = 40.005
  expr: .Placement.Base.y = 40.005
FEATURE [Sketcher::SketchObject] Sketch036
  AttachmentOffset = pos=(0,0,7) rot=(0,0,1;0rad)
  FullyConstrained = false
  MapMode = 5
  Placement = pos=(0,0,7) rot=(0,0,1;0rad)
  Support = -> [XY_Plane014]
  sketch-geometry (25):
    g0: LineSegment StartX=-0.724089 StartY=5.5 StartZ=0 EndX=-2.12292 EndY=5.12518 EndZ=0
    g1: LineSegment StartX=-2.12292 StartY=5.12518 StartZ=0 EndX=-3.37708 EndY=4.4011 EndZ=0
    g2: LineSegment StartX=-3.37708 StartY=4.4011 StartZ=0 EndX=-4.4011 EndY=3.37708 EndZ=0
    g3: LineSegment StartX=-4.4011 StartY=3.37708 StartZ=0 EndX=-5.12518 EndY=2.12292 EndZ=0
    g4: LineSegment StartX=-5.12518 StartY=2.12292 StartZ=0 EndX=-5.5 EndY=0.724089 EndZ=0
    g5: LineSegment StartX=-5.5 StartY=0.724089 StartZ=0 EndX=-5.5 EndY=-0.724089 EndZ=0
    g6: LineSegment StartX=-5.5 StartY=-0.724089 StartZ=0 EndX=-5.12518 EndY=-2.12292 EndZ=0
    g7: LineSegment StartX=-5.12518 StartY=-2.12292 StartZ=0 EndX=-4.4011 EndY=-3.37708 EndZ=0
    g8: LineSegment StartX=-4.4011 StartY=-3.37708 StartZ=0 EndX=-3.37708 EndY=-4.4011 EndZ=0
    g9: LineSegment StartX=-3.37708 StartY=-4.4011 StartZ=0 EndX=-2.12292 EndY=-5.12518 EndZ=0
    g10: LineSegment StartX=-2.12292 StartY=-5.12518 StartZ=0 EndX=-0.724089 EndY=-5.5 EndZ=0
    g11: LineSegment StartX=-0.724089 StartY=-5.5 StartZ=0 EndX=0.724089 EndY=-5.5 EndZ=0
    g12: LineSegment StartX=0.724089 StartY=-5.5 StartZ=0 EndX=2.12292 EndY=-5.12518 EndZ=0
    g13: LineSegment StartX=2.12292 StartY=-5.12518 StartZ=0 EndX=3.37708 EndY=-4.4011 EndZ=0
    g14: LineSegment StartX=3.37708 StartY=-4.4011 StartZ=0 EndX=4.4011 EndY=-3.37708 EndZ=0
    g15: LineSegment StartX=4.4011 StartY=-3.37708 StartZ=0 EndX=5.12518 EndY=-2.12292 EndZ=0
    g16: LineSegment StartX=5.12518 StartY=-2.12292 StartZ=0 EndX=5.5 EndY=-0.724089 EndZ=0
    g17: LineSegment StartX=5.5 StartY=-0.724089 StartZ=0 EndX=5.5 EndY=0.724089 EndZ=0
    g18: LineSegment StartX=5.5 StartY=0.724089 StartZ=0 EndX=5.12518 EndY=2.12292 EndZ=0
    g19: LineSegment StartX=5.12518 StartY=2.12292 StartZ=0 EndX=4.4011 EndY=3.37708 EndZ=0
    g20: LineSegment StartX=4.4011 StartY=3.37708 StartZ=0 EndX=3.37708 EndY=4.4011 EndZ=0
    g21: LineSegment StartX=3.37708 StartY=4.4011 StartZ=0 EndX=2.12292 EndY=5.12518 EndZ=0
    g22: LineSegment StartX=2.12292 StartY=5.12518 StartZ=0 EndX=0.724089 EndY=5.5 EndZ=0
    g23: LineSegment StartX=0.724089 StartY=5.5 StartZ=0 EndX=-0.724089 EndY=5.5 EndZ=0
    g24: Circle CenterX=0 CenterY=0 CenterZ=0 NormalX=0 NormalY=0 NormalZ=1 AngleXU=0 Radius=5.54746
  constraints (52):
    c: Coincident(g0,g1)
    c: Coincident(g1,g2)
    c: Coincident(g2,g3)
    c: Coincident(g3,g4)
    c: Coincident(g4,g5)
    c: Coincident(g5,g6)
    c: Coincident(g6,g7)
    c: Coincident(g7,g8)
    c: Coincident(g8,g9)
    c: Coincident(g9,g10)
    c: Coincident(g10,g11)
    c: Coincident(g11,g12)
    c: Coincident(g12,g13)
    c: Coincident(g13,g14)
    c: Coincident(g14,g15)
    c: Coincident(g15,g16)
    c: Coincident(g16,g17)
    c: Coincident(g17,g18)
    c: Coincident(g18,g19)
    c: Coincident(g19,g20)
    c: Coincident(g20,g21)
    c: Coincident(g21,g22)
    c: Coincident(g22,g23)
    c: Coincident(g23,g0)
    c: Equal(g0, g1-g23) x23
    c: PointOnObject(g0,g24)
    c: PointOnObject(g1,g24)
    c: PointOnObject(g2,g24)
    c: PointOnObject(g3,g24)
    c: PointOnObject(g4,g24)
    c: PointOnObject(g5,g24)
    c: PointOnObject(g6,g24)
    c: PointOnObject(g7,g24)
    c: PointOnObject(g8,g24)
    c: PointOnObject(g9,g24)
    c: PointOnObject(g10,g24)
    c: PointOnObject(g11,g24)
    c: PointOnObject(g12,g24)
    c: PointOnObject(g13,g24)
    c: PointOnObject(g14,g24)
    c: PointOnObject(g15,g24)
    c: PointOnObject(g16,g24)
    c: PointOnObject(g17,g24)
    c: PointOnObject(g18,g24)
    c: PointOnObject(g19,g24)
    c: PointOnObject(g20,g24)
    c: PointOnObject(g21,g24)
    c: PointOnObject(g22,g24)
    c: PointOnObject(g23,g24)
    c: Coincident(g24,g-1)
    c: Horizontal(g23)
    c: DistanceX(g4,g17) = 11
FEATURE [Sketcher::SketchObject] Sketch041
  FullyConstrained = false
  MapMode = 5
  Support = -> [XY_Plane014]
  sketch-geometry (25):
    g0: LineSegment StartX=-0.789915 StartY=6 StartZ=0 EndX=-2.31591 EndY=5.59111 EndZ=0
    g1: LineSegment StartX=-2.31591 StartY=5.59111 StartZ=0 EndX=-3.68409 EndY=4.80119 EndZ=0
    g2: LineSegment StartX=-3.68409 StartY=4.80119 StartZ=0 EndX=-4.80119 EndY=3.68409 EndZ=0
    g3: LineSegment StartX=-4.80119 StartY=3.68409 StartZ=0 EndX=-5.59111 EndY=2.31591 EndZ=0
    g4: LineSegment StartX=-5.59111 StartY=2.31591 StartZ=0 EndX=-6 EndY=0.789915 EndZ=0
    g5: LineSegment StartX=-6 StartY=0.789915 StartZ=0 EndX=-6 EndY=-0.789915 EndZ=0
    g6: LineSegment StartX=-6 StartY=-0.789915 StartZ=0 EndX=-5.59111 EndY=-2.31591 EndZ=0
    g7: LineSegment StartX=-5.59111 StartY=-2.31591 StartZ=0 EndX=-4.80119 EndY=-3.68409 EndZ=0
    g8: LineSegment StartX=-4.80119 StartY=-3.68409 StartZ=0 EndX=-3.68409 EndY=-4.80119 EndZ=0
    g9: LineSegment StartX=-3.68409 StartY=-4.80119 StartZ=0 EndX=-2.31591 EndY=-5.59111 EndZ=0
    g10: LineSegment StartX=-2.31591 StartY=-5.59111 StartZ=0 EndX=-0.789915 EndY=-6 EndZ=0
    g11: LineSegment StartX=-0.789915 StartY=-6 StartZ=0 EndX=0.789915 EndY=-6 EndZ=0
    g12: LineSegment StartX=0.789915 StartY=-6 StartZ=0 EndX=2.31591 EndY=-5.59111 EndZ=0
    g13: LineSegment StartX=2.31591 StartY=-5.59111 StartZ=0 EndX=3.68409 EndY=-4.80119 EndZ=0
    g14: LineSegment StartX=3.68409 StartY=-4.80119 StartZ=0 EndX=4.80119 EndY=-3.68409 EndZ=0
    g15: LineSegment StartX=4.80119 StartY=-3.68409 StartZ=0 EndX=5.59111 EndY=-2.31591 EndZ=0
    g16: LineSegment StartX=5.59111 StartY=-2.31591 StartZ=0 EndX=6 EndY=-0.789915 EndZ=0
    g17: LineSegment StartX=6 StartY=-0.789915 StartZ=0 EndX=6 EndY=0.789915 EndZ=0
    g18: LineSegment StartX=6 StartY=0.789915 StartZ=0 EndX=5.59111 EndY=2.31591 EndZ=0
    g19: LineSegment StartX=5.59111 StartY=2.31591 StartZ=0 EndX=4.80119 EndY=3.68409 EndZ=0
    g20: LineSegment StartX=4.80119 StartY=3.68409 StartZ=0 EndX=3.68409 EndY=4.80119 EndZ=0
    g21: LineSegment StartX=3.68409 StartY=4.80119 StartZ=0 EndX=2.31591 EndY=5.59111 EndZ=0
    g22: LineSegment StartX=2.31591 StartY=5.59111 StartZ=0 EndX=0.789915 EndY=6 EndZ=0
    g23: LineSegment StartX=0.789915 StartY=6 StartZ=0 EndX=-0.789915 EndY=6 EndZ=0
    g24: Circle CenterX=0 CenterY=0 CenterZ=0 NormalX=0 NormalY=0 NormalZ=1 AngleXU=0 Radius=6.05177
  constraints (52):
    c: Coincident(g0,g1)
    c: Coincident(g1,g2)
    c: Coincident(g2,g3)
    c: Coincident(g3,g4)
    c: Coincident(g4,g5)
    c: Coincident(g5,g6)
    c: Coincident(g6,g7)
    c: Coincident(g7,g8)
    c: Coincident(g8,g9)
    c: Coincident(g9,g10)
    c: Coincident(g10,g11)
    c: Coincident(g11,g12)
    c: Coincident(g12,g13)
    c: Coincident(g13,g14)
    c: Coincident(g14,g15)
    c: Coincident(g15,g16)
    c: Coincident(g16,g17)
    c: Coincident(g17,g18)
    c: Coincident(g18,g19)
    c: Coincident(g19,g20)
    c: Coincident(g20,g21)
    c: Coincident(g21,g22)
    c: Coincident(g22,g23)
    c: Coincident(g23,g0)
    c: Equal(g0, g1-g23) x23
    c: PointOnObject(g0,g24)
    c: PointOnObject(g1,g24)
    c: PointOnObject(g2,g24)
    c: PointOnObject(g3,g24)
    c: PointOnObject(g4,g24)
    c: PointOnObject(g5,g24)
    c: PointOnObject(g6,g24)
    c: PointOnObject(g7,g24)
    c: PointOnObject(g8,g24)
    c: PointOnObject(g9,g24)
    c: PointOnObject(g10,g24)
    c: PointOnObject(g11,g24)
    c: PointOnObject(g12,g24)
    c: PointOnObject(g13,g24)
    c: PointOnObject(g14,g24)
    c: PointOnObject(g15,g24)
    c: PointOnObject(g16,g24)
    c: PointOnObject(g17,g24)
    c: PointOnObject(g18,g24)
    c: PointOnObject(g19,g24)
    c: PointOnObject(g20,g24)
    c: PointOnObject(g21,g24)
    c: PointOnObject(g22,g24)
    c: PointOnObject(g23,g24)
    c: Coincident(g24,g-1)
    c: Horizontal(g23)
    c: DistanceX(g4,g17) = 12
FEATURE [Sketcher::SketchObject] Sketch042
  AttachmentOffset = pos=(0,0,17) rot=(0,0,1;0rad)
  FullyConstrained = false
  MapMode = 5
  Placement = pos=(0,0,17) rot=(0,0,1;0rad)
  Support = -> [XY_Plane014]
  sketch-geometry (25):
    g0: LineSegment StartX=-4.65926 StartY=1.92993 StartZ=0 EndX=-5 EndY=0.658262 EndZ=0
    g1: LineSegment StartX=-5 StartY=0.658262 StartZ=0 EndX=-5 EndY=-0.658262 EndZ=0
    g2: LineSegment StartX=-5 StartY=-0.658262 StartZ=0 EndX=-4.65926 EndY=-1.92993 EndZ=0
    g3: LineSegment StartX=-4.65926 StartY=-1.92993 StartZ=0 EndX=-4.001 EndY=-3.07007 EndZ=0
    g4: LineSegment StartX=-4.001 StartY=-3.07007 StartZ=0 EndX=-3.07007 EndY=-4.001 EndZ=0
    g5: LineSegment StartX=-3.07007 StartY=-4.001 StartZ=0 EndX=-1.92993 EndY=-4.65926 EndZ=0
    g6: LineSegment StartX=-1.92993 StartY=-4.65926 StartZ=0 EndX=-0.658262 EndY=-5 EndZ=0
    g7: LineSegment StartX=-0.658262 StartY=-5 StartZ=0 EndX=0.658262 EndY=-5 EndZ=0
    g8: LineSegment StartX=0.658262 StartY=-5 StartZ=0 EndX=1.92993 EndY=-4.65926 EndZ=0
    g9: LineSegment StartX=1.92993 StartY=-4.65926 StartZ=0 EndX=3.07007 EndY=-4.001 EndZ=0
    g10: LineSegment StartX=3.07007 StartY=-4.001 StartZ=0 EndX=4.001 EndY=-3.07007 EndZ=0
    g11: LineSegment StartX=4.001 StartY=-3.07007 StartZ=0 EndX=4.65926 EndY=-1.92993 EndZ=0
    g12: LineSegment StartX=4.65926 StartY=-1.92993 StartZ=0 EndX=5 EndY=-0.658262 EndZ=0
    g13: LineSegment StartX=5 StartY=-0.658262 StartZ=0 EndX=5 EndY=0.658262 EndZ=0
    g14: LineSegment StartX=5 StartY=0.658262 StartZ=0 EndX=4.65926 EndY=1.92993 EndZ=0
    g15: LineSegment StartX=4.65926 StartY=1.92993 StartZ=0 EndX=4.001 EndY=3.07007 EndZ=0
    g16: LineSegment StartX=4.001 StartY=3.07007 StartZ=0 EndX=3.07007 EndY=4.001 EndZ=0
    g17: LineSegment StartX=3.07007 StartY=4.001 StartZ=0 EndX=1.92993 EndY=4.65926 EndZ=0
    g18: LineSegment StartX=1.92993 StartY=4.65926 StartZ=0 EndX=0.658262 EndY=5 EndZ=0
    g19: LineSegment StartX=0.658262 StartY=5 StartZ=0 EndX=-0.658262 EndY=5 EndZ=0
    g20: LineSegment StartX=-0.658262 StartY=5 StartZ=0 EndX=-1.92993 EndY=4.65926 EndZ=0
    g21: LineSegment StartX=-1.92993 StartY=4.65926 StartZ=0 EndX=-3.07007 EndY=4.001 EndZ=0
    g22: LineSegment StartX=-3.07007 StartY=4.001 StartZ=0 EndX=-4.001 EndY=3.07007 EndZ=0
    g23: LineSegment StartX=-4.001 StartY=3.07007 StartZ=0 EndX=-4.65926 EndY=1.92993 EndZ=0
    g24: Circle CenterX=0 CenterY=0 CenterZ=0 NormalX=0 NormalY=0 NormalZ=1 AngleXU=0 Radius=5.04314
  constraints (52):
    c: Coincident(g0,g1)
    c: Coincident(g1,g2)
    c: Coincident(g2,g3)
    c: Coincident(g3,g4)
    c: Coincident(g4,g5)
    c: Coincident(g5,g6)
    c: Coincident(g6,g7)
    c: Coincident(g7,g8)
    c: Coincident(g8,g9)
    c: Coincident(g9,g10)
    c: Coincident(g10,g11)
    c: Coincident(g11,g12)
    c: Coincident(g12,g13)
    c: Coincident(g13,g14)
    c: Coincident(g14,g15)
    c: Coincident(g15,g16)
    c: Coincident(g16,g17)
    c: Coincident(g17,g18)
    c: Coincident(g18,g19)
    c: Coincident(g19,g20)
    c: Coincident(g20,g21)
    c: Coincident(g21,g22)
    c: Coincident(g22,g23)
    c: Coincident(g23,g0)
    c: Equal(g0, g1-g23) x23
    c: PointOnObject(g0,g24)
    c: PointOnObject(g1,g24)
    c: PointOnObject(g2,g24)
    c: PointOnObject(g3,g24)
    c: PointOnObject(g4,g24)
    c: PointOnObject(g5,g24)
    c: PointOnObject(g6,g24)
    c: PointOnObject(g7,g24)
    c: PointOnObject(g8,g24)
    c: PointOnObject(g9,g24)
    c: PointOnObject(g10,g24)
    c: PointOnObject(g11,g24)
    c: PointOnObject(g12,g24)
    c: PointOnObject(g13,g24)
    c: PointOnObject(g14,g24)
    c: PointOnObject(g15,g24)
    c: PointOnObject(g16,g24)
    c: PointOnObject(g17,g24)
    c: PointOnObject(g18,g24)
    c: PointOnObject(g19,g24)
    c: PointOnObject(g20,g24)
    c: PointOnObject(g21,g24)
    c: PointOnObject(g22,g24)
    c: PointOnObject(g23,g24)
    c: Coincident(g24,g-1)
    c: Horizontal(g19)
    c: DistanceX(g0,g13) = 10
FEATURE [PartDesign::AdditiveLoft] AdditiveLoft006
  AllowMultiFace = false
  Closed = false
  Profile = -> Sketch041
  Refine = true
  Ruled = false
  Sections = -> [Sketch036,Sketch042]
FEATURE [Sketcher::SketchObject] Sketch035
  FullyConstrained = false
  MapMode = 5
  Placement = pos=(0,0,17) rot=(0,0,1;0rad)
  Support = -> [AdditiveLoft006]
  sketch-geometry (1):
    g0: Circle CenterX=0 CenterY=0 CenterZ=0 NormalX=0 NormalY=0 NormalZ=1 AngleXU=0 Radius=4.5
  constraints (2):
    c: Coincident(g0,g-1)
    c: Radius(g0) = 4.5
FEATURE [PartDesign::Pad] Pad008
  AllowMultiFace = false
  BaseFeature = -> AdditiveLoft006
  Direction = (1,1,1)
  Length = 0.7
  Length2 = 100
  Profile = -> Sketch035
  Refine = true
  Type = 0
FEATURE [Sketcher::SketchObject] Sketch034
  FullyConstrained = false
  MapMode = 5
  Placement = pos=(0,0,0) rot=(1,0,0;3.14159rad)
  Support = -> [Pad008]
  sketch-geometry (1):
    g0: Circle CenterX=0 CenterY=0 CenterZ=0 NormalX=0 NormalY=0 NormalZ=1 AngleXU=0 Radius=5
  constraints (2):
    c: Coincident(g0,g-1)
    c: Radius(g0) = 5
FEATURE [PartDesign::Pocket] Pocket013
  AllowMultiFace = false
  BaseFeature = -> Pad008
  Direction = (1,1,1)
  Length = 1
  Length2 = 100
  Profile = -> Sketch034
  Refine = true
  Type = 0
FEATURE [Sketcher::SketchObject] Sketch032
  FullyConstrained = false
  MapMode = 5
  Placement = pos=(0,0,1) rot=(1,0,0;3.14159rad)
  Support = -> [Pocket013]
  sketch-geometry (1):
    g0: Circle CenterX=0 CenterY=0 CenterZ=0 NormalX=0 NormalY=0 NormalZ=1 AngleXU=0 Radius=4.65
  constraints (2):
    c: Coincident(g0,g-1)
    c: Radius(g0) = 4.65
FEATURE [PartDesign::Pocket] Pocket012
  AllowMultiFace = false
  BaseFeature = -> Pocket013
  Direction = (1,1,1)
  Length = 1
  Length2 = 100
  Profile = -> Sketch032
  Refine = true
  Type = 0
FEATURE [Sketcher::SketchObject] Sketch033
  FullyConstrained = false
  MapMode = 5
  Placement = pos=(0,0,2) rot=(1,0,0;3.14159rad)
  Support = -> [Pocket012]
  sketch-geometry (2):
    g0: ArcOfCircle CenterX=0 CenterY=0 CenterZ=0 NormalX=0 NormalY=0 NormalZ=1 AngleXU=0 Radius=3 StartAngle=2.19024 EndAngle=7.23453
    g1: LineSegment StartX=-1.74176 StartY=2.4426 StartZ=0 EndX=1.74176 EndY=2.4426 EndZ=0
  constraints (5):
    c: Coincident(g0,g-1)
    c: Coincident(g1,g0)
    c: Coincident(g1,g0)
    c: Horizontal(g1)
    c: Radius(g0) = 3
FEATURE [PartDesign::Pocket] Pocket014
  AllowMultiFace = false
  BaseFeature = -> Pocket012
  Direction = (1,1,1)
  Length = 8
  Length2 = 100
  Profile = -> Sketch033
  Refine = true
  Type = 0
FEATURE [PartDesign::Chamfer] Chamfer008
  Angle = 45
  Base = -> Pocket014 [Edge82,Edge83]
  BaseFeature = -> Pocket014
  ChamferType = 0
  FlipDirection = false
  Size = 1.4
  Size2 = 1
  SupportTransform = false
  UseAllEdges = false
FEATURE [PartDesign::Chamfer] Chamfer009
  Angle = 45
  Base = -> Chamfer008 [Edge8]
  BaseFeature = -> Chamfer008
  ChamferType = 0
  FlipDirection = false
  Size = 0.3
  Size2 = 1
  SupportTransform = false
  UseAllEdges = false
FEATURE [PartDesign::Fillet] Fillet004
  Base = -> Chamfer009 [Edge93,Face36]
  BaseFeature = -> Chamfer009
  Radius = 0.1
  SupportTransform = false
  UseAllEdges = false
FEATURE [PartDesign::Body] Body008
  Group = -> [Sketch041,Sketch036,Sketch042,AdditiveLoft006,Sketch035,Pad008,Sketch034,Pocket013,Sketch032,Pocket012,Sketch033,Pocket014,Chamfer008,Chamfer009,Fillet004]
  Origin = -> Origin022
  Tip = -> Fillet004
FEATURE [Sketcher::SketchObject] Sketch043
  AttachmentOffset = pos=(0,0,17.7) rot=(0,0,1;0rad)
  FullyConstrained = false
  MapMode = 5
  Placement = pos=(0,0,17.7) rot=(0,0,1;0rad)
  Support = -> [XY_Plane015]
  sketch-geometry (10):
    g0: LineSegment StartX=-0.2 StartY=1.5 StartZ=0 EndX=0.2 EndY=1.5 EndZ=0
    g1: LineSegment StartX=0.4 StartY=1.7 StartZ=0 EndX=0.4 EndY=4.2 EndZ=0
    g2: LineSegment StartX=0.2 StartY=4.4 StartZ=0 EndX=-0.2 EndY=4.4 EndZ=0
    g3: LineSegment StartX=-0.4 StartY=4.2 StartZ=0 EndX=-0.4 EndY=1.7 EndZ=0
    g4: ArcOfCircle CenterX=-0.2 CenterY=1.7 CenterZ=0 NormalX=0 NormalY=0 NormalZ=1 AngleXU=0 Radius=0.2 StartAngle=3.14159 EndAngle=4.71239
    g5: ArcOfCircle CenterX=0.2 CenterY=1.7 CenterZ=0 NormalX=0 NormalY=0 NormalZ=1 AngleXU=0 Radius=0.2 StartAngle=4.71239 EndAngle=6.28319
    g6: ArcOfCircle CenterX=0.2 CenterY=4.2 CenterZ=0 NormalX=0 NormalY=0 NormalZ=1 AngleXU=0 Radius=0.2 StartAngle=1.4e-15 EndAngle=1.5708
    g7: ArcOfCircle CenterX=-0.2 CenterY=4.2 CenterZ=0 NormalX=0 NormalY=0 NormalZ=1 AngleXU=0 Radius=0.2 StartAngle=1.5708 EndAngle=3.14159
    g8: LineSegment StartX=-0.2 StartY=1.7 StartZ=0 EndX=0 EndY=0 EndZ=0
    g9: LineSegment StartX=0 StartY=0 StartZ=0 EndX=0.2 EndY=1.7 EndZ=0
  constraints (24):
    c: Horizontal(g0)
    c: Horizontal(g2)
    c: Vertical(g1)
    c: Vertical(g3)
    c: Tangent(g3,g4) = -1.5708
    c: Tangent(g0,g4) = -1.5708
    c: Tangent(g0,g5) = -1.5708
    c: Tangent(g1,g5) = -1.5708
    c: Tangent(g1,g6) = -1.5708
    c: Tangent(g2,g6) = -1.5708
    c: Tangent(g2,g7) = -1.5708
    c: Tangent(g3,g7) = -1.5708
    c: Radius(g7) = 0.2
    c: Equal(g7,g6)
    c: Equal(g7,g5)
    c: Equal(g7,g4)
    c: Coincident(g8,g4)
    c: Coincident(g8,g-1)
    c: Coincident(g9,g-1)
    c: Coincident(g9,g5)
    c: Equal(g9,g8)
    c: DistanceX(g3,g1) = 0.8
    c: DistanceY(g-1,g2) = 4.4
    c: DistanceY(g-1,g0) = 1.5
FEATURE [PartDesign::Pad] Pad009
  AllowMultiFace = false
  Direction = (1,1,1)
  Length = 0.02
  Length2 = 100
  Profile = -> Sketch043
  Refine = true
  Type = 0
FEATURE [PartDesign::Body] Body009  label="Indicator004"
  Group = -> [Sketch043,Pad009]
  Origin = -> Origin023
  Tip = -> Pad009
FEATURE [App::Part] Part006  label="Cap007"
  Group = -> [Body008,Body009]
  Origin = -> Origin024
  Placement = pos=(-40.005,13.335,0) rot=(0,0,1;0rad)
  expr: .Placement.Base.x = -40.005
  expr: .Placement.Base.y = 13.335
FEATURE [Sketcher::SketchObject] Sketch044
  AttachmentOffset = pos=(0,0,7) rot=(0,0,1;0rad)
  FullyConstrained = false
  MapMode = 5
  Placement = pos=(0,0,7) rot=(0,0,1;0rad)
  Support = -> [XY_Plane017]
  sketch-geometry (25):
    g0: LineSegment StartX=-0.724089 StartY=5.5 StartZ=0 EndX=-2.12292 EndY=5.12518 EndZ=0
    g1: LineSegment StartX=-2.12292 StartY=5.12518 StartZ=0 EndX=-3.37708 EndY=4.4011 EndZ=0
    g2: LineSegment StartX=-3.37708 StartY=4.4011 StartZ=0 EndX=-4.4011 EndY=3.37708 EndZ=0
    g3: LineSegment StartX=-4.4011 StartY=3.37708 StartZ=0 EndX=-5.12518 EndY=2.12292 EndZ=0
    g4: LineSegment StartX=-5.12518 StartY=2.12292 StartZ=0 EndX=-5.5 EndY=0.724089 EndZ=0
    g5: LineSegment StartX=-5.5 StartY=0.724089 StartZ=0 EndX=-5.5 EndY=-0.724089 EndZ=0
    g6: LineSegment StartX=-5.5 StartY=-0.724089 StartZ=0 EndX=-5.12518 EndY=-2.12292 EndZ=0
    g7: LineSegment StartX=-5.12518 StartY=-2.12292 StartZ=0 EndX=-4.4011 EndY=-3.37708 EndZ=0
    g8: LineSegment StartX=-4.4011 StartY=-3.37708 StartZ=0 EndX=-3.37708 EndY=-4.4011 EndZ=0
    g9: LineSegment StartX=-3.37708 StartY=-4.4011 StartZ=0 EndX=-2.12292 EndY=-5.12518 EndZ=0
    g10: LineSegment StartX=-2.12292 StartY=-5.12518 StartZ=0 EndX=-0.724089 EndY=-5.5 EndZ=0
    g11: LineSegment StartX=-0.724089 StartY=-5.5 StartZ=0 EndX=0.724089 EndY=-5.5 EndZ=0
    g12: LineSegment StartX=0.724089 StartY=-5.5 StartZ=0 EndX=2.12292 EndY=-5.12518 EndZ=0
    g13: LineSegment StartX=2.12292 StartY=-5.12518 StartZ=0 EndX=3.37708 EndY=-4.4011 EndZ=0
    g14: LineSegment StartX=3.37708 StartY=-4.4011 StartZ=0 EndX=4.4011 EndY=-3.37708 EndZ=0
    g15: LineSegment StartX=4.4011 StartY=-3.37708 StartZ=0 EndX=5.12518 EndY=-2.12292 EndZ=0
    g16: LineSegment StartX=5.12518 StartY=-2.12292 StartZ=0 EndX=5.5 EndY=-0.724089 EndZ=0
    g17: LineSegment StartX=5.5 StartY=-0.724089 StartZ=0 EndX=5.5 EndY=0.724089 EndZ=0
    g18: LineSegment StartX=5.5 StartY=0.724089 StartZ=0 EndX=5.12518 EndY=2.12292 EndZ=0
    g19: LineSegment StartX=5.12518 StartY=2.12292 StartZ=0 EndX=4.4011 EndY=3.37708 EndZ=0
    g20: LineSegment StartX=4.4011 StartY=3.37708 StartZ=0 EndX=3.37708 EndY=4.4011 EndZ=0
    g21: LineSegment StartX=3.37708 StartY=4.4011 StartZ=0 EndX=2.12292 EndY=5.12518 EndZ=0
    g22: LineSegment StartX=2.12292 StartY=5.12518 StartZ=0 EndX=0.724089 EndY=5.5 EndZ=0
    g23: LineSegment StartX=0.724089 StartY=5.5 StartZ=0 EndX=-0.724089 EndY=5.5 EndZ=0
    g24: Circle CenterX=0 CenterY=0 CenterZ=0 NormalX=0 NormalY=0 NormalZ=1 AngleXU=0 Radius=5.54746
  constraints (52):
    c: Coincident(g0,g1)
    c: Coincident(g1,g2)
    c: Coincident(g2,g3)
    c: Coincident(g3,g4)
    c: Coincident(g4,g5)
    c: Coincident(g5,g6)
    c: Coincident(g6,g7)
    c: Coincident(g7,g8)
    c: Coincident(g8,g9)
    c: Coincident(g9,g10)
    c: Coincident(g10,g11)
    c: Coincident(g11,g12)
    c: Coincident(g12,g13)
    c: Coincident(g13,g14)
    c: Coincident(g14,g15)
    c: Coincident(g15,g16)
    c: Coincident(g16,g17)
    c: Coincident(g17,g18)
    c: Coincident(g18,g19)
    c: Coincident(g19,g20)
    c: Coincident(g20,g21)
    c: Coincident(g21,g22)
    c: Coincident(g22,g23)
    c: Coincident(g23,g0)
    c: Equal(g0, g1-g23) x23
    c: PointOnObject(g0,g24)
    c: PointOnObject(g1,g24)
    c: PointOnObject(g2,g24)
    c: PointOnObject(g3,g24)
    c: PointOnObject(g4,g24)
    c: PointOnObject(g5,g24)
    c: PointOnObject(g6,g24)
    c: PointOnObject(g7,g24)
    c: PointOnObject(g8,g24)
    c: PointOnObject(g9,g24)
    c: PointOnObject(g10,g24)
    c: PointOnObject(g11,g24)
    c: PointOnObject(g12,g24)
    c: PointOnObject(g13,g24)
    c: PointOnObject(g14,g24)
    c: PointOnObject(g15,g24)
    c: PointOnObject(g16,g24)
    c: PointOnObject(g17,g24)
    c: PointOnObject(g18,g24)
    c: PointOnObject(g19,g24)
    c: PointOnObject(g20,g24)
    c: PointOnObject(g21,g24)
    c: PointOnObject(g22,g24)
    c: PointOnObject(g23,g24)
    c: Coincident(g24,g-1)
    c: Horizontal(g23)
    c: DistanceX(g4,g17) = 11
FEATURE [Sketcher::SketchObject] Sketch045
  FullyConstrained = false
  MapMode = 5
  Support = -> [XY_Plane017]
  sketch-geometry (25):
    g0: LineSegment StartX=-0.789915 StartY=6 StartZ=0 EndX=-2.31591 EndY=5.59111 EndZ=0
    g1: LineSegment StartX=-2.31591 StartY=5.59111 StartZ=0 EndX=-3.68409 EndY=4.80119 EndZ=0
    g2: LineSegment StartX=-3.68409 StartY=4.80119 StartZ=0 EndX=-4.80119 EndY=3.68409 EndZ=0
    g3: LineSegment StartX=-4.80119 StartY=3.68409 StartZ=0 EndX=-5.59111 EndY=2.31591 EndZ=0
    g4: LineSegment StartX=-5.59111 StartY=2.31591 StartZ=0 EndX=-6 EndY=0.789915 EndZ=0
    g5: LineSegment StartX=-6 StartY=0.789915 StartZ=0 EndX=-6 EndY=-0.789915 EndZ=0
    g6: LineSegment StartX=-6 StartY=-0.789915 StartZ=0 EndX=-5.59111 EndY=-2.31591 EndZ=0
    g7: LineSegment StartX=-5.59111 StartY=-2.31591 StartZ=0 EndX=-4.80119 EndY=-3.68409 EndZ=0
    g8: LineSegment StartX=-4.80119 StartY=-3.68409 StartZ=0 EndX=-3.68409 EndY=-4.80119 EndZ=0
    g9: LineSegment StartX=-3.68409 StartY=-4.80119 StartZ=0 EndX=-2.31591 EndY=-5.59111 EndZ=0
    g10: LineSegment StartX=-2.31591 StartY=-5.59111 StartZ=0 EndX=-0.789915 EndY=-6 EndZ=0
    g11: LineSegment StartX=-0.789915 StartY=-6 StartZ=0 EndX=0.789915 EndY=-6 EndZ=0
    g12: LineSegment StartX=0.789915 StartY=-6 StartZ=0 EndX=2.31591 EndY=-5.59111 EndZ=0
    g13: LineSegment StartX=2.31591 StartY=-5.59111 StartZ=0 EndX=3.68409 EndY=-4.80119 EndZ=0
    g14: LineSegment StartX=3.68409 StartY=-4.80119 StartZ=0 EndX=4.80119 EndY=-3.68409 EndZ=0
    g15: LineSegment StartX=4.80119 StartY=-3.68409 StartZ=0 EndX=5.59111 EndY=-2.31591 EndZ=0
    g16: LineSegment StartX=5.59111 StartY=-2.31591 StartZ=0 EndX=6 EndY=-0.789915 EndZ=0
    g17: LineSegment StartX=6 StartY=-0.789915 StartZ=0 EndX=6 EndY=0.789915 EndZ=0
    g18: LineSegment StartX=6 StartY=0.789915 StartZ=0 EndX=5.59111 EndY=2.31591 EndZ=0
    g19: LineSegment StartX=5.59111 StartY=2.31591 StartZ=0 EndX=4.80119 EndY=3.68409 EndZ=0
    g20: LineSegment StartX=4.80119 StartY=3.68409 StartZ=0 EndX=3.68409 EndY=4.80119 EndZ=0
    g21: LineSegment StartX=3.68409 StartY=4.80119 StartZ=0 EndX=2.31591 EndY=5.59111 EndZ=0
    g22: LineSegment StartX=2.31591 StartY=5.59111 StartZ=0 EndX=0.789915 EndY=6 EndZ=0
    g23: LineSegment StartX=0.789915 StartY=6 StartZ=0 EndX=-0.789915 EndY=6 EndZ=0
    g24: Circle CenterX=0 CenterY=0 CenterZ=0 NormalX=0 NormalY=0 NormalZ=1 AngleXU=0 Radius=6.05177
  constraints (52):
    c: Coincident(g0,g1)
    c: Coincident(g1,g2)
    c: Coincident(g2,g3)
    c: Coincident(g3,g4)
    c: Coincident(g4,g5)
    c: Coincident(g5,g6)
    c: Coincident(g6,g7)
    c: Coincident(g7,g8)
    c: Coincident(g8,g9)
    c: Coincident(g9,g10)
    c: Coincident(g10,g11)
    c: Coincident(g11,g12)
    c: Coincident(g12,g13)
    c: Coincident(g13,g14)
    c: Coincident(g14,g15)
    c: Coincident(g15,g16)
    c: Coincident(g16,g17)
    c: Coincident(g17,g18)
    c: Coincident(g18,g19)
    c: Coincident(g19,g20)
    c: Coincident(g20,g21)
    c: Coincident(g21,g22)
    c: Coincident(g22,g23)
    c: Coincident(g23,g0)
    c: Equal(g0, g1-g23) x23
    c: PointOnObject(g0,g24)
    c: PointOnObject(g1,g24)
    c: PointOnObject(g2,g24)
    c: PointOnObject(g3,g24)
    c: PointOnObject(g4,g24)
    c: PointOnObject(g5,g24)
    c: PointOnObject(g6,g24)
    c: PointOnObject(g7,g24)
    c: PointOnObject(g8,g24)
    c: PointOnObject(g9,g24)
    c: PointOnObject(g10,g24)
    c: PointOnObject(g11,g24)
    c: PointOnObject(g12,g24)
    c: PointOnObject(g13,g24)
    c: PointOnObject(g14,g24)
    c: PointOnObject(g15,g24)
    c: PointOnObject(g16,g24)
    c: PointOnObject(g17,g24)
    c: PointOnObject(g18,g24)
    c: PointOnObject(g19,g24)
    c: PointOnObject(g20,g24)
    c: PointOnObject(g21,g24)
    c: PointOnObject(g22,g24)
    c: PointOnObject(g23,g24)
    c: Coincident(g24,g-1)
    c: Horizontal(g23)
    c: DistanceX(g4,g17) = 12
FEATURE [Sketcher::SketchObject] Sketch046
  AttachmentOffset = pos=(0,0,17) rot=(0,0,1;0rad)
  FullyConstrained = false
  MapMode = 5
  Placement = pos=(0,0,17) rot=(0,0,1;0rad)
  Support = -> [XY_Plane017]
  sketch-geometry (25):
    g0: LineSegment StartX=-4.65926 StartY=1.92993 StartZ=0 EndX=-5 EndY=0.658262 EndZ=0
    g1: LineSegment StartX=-5 StartY=0.658262 StartZ=0 EndX=-5 EndY=-0.658262 EndZ=0
    g2: LineSegment StartX=-5 StartY=-0.658262 StartZ=0 EndX=-4.65926 EndY=-1.92993 EndZ=0
    g3: LineSegment StartX=-4.65926 StartY=-1.92993 StartZ=0 EndX=-4.001 EndY=-3.07007 EndZ=0
    g4: LineSegment StartX=-4.001 StartY=-3.07007 StartZ=0 EndX=-3.07007 EndY=-4.001 EndZ=0
    g5: LineSegment StartX=-3.07007 StartY=-4.001 StartZ=0 EndX=-1.92993 EndY=-4.65926 EndZ=0
    g6: LineSegment StartX=-1.92993 StartY=-4.65926 StartZ=0 EndX=-0.658262 EndY=-5 EndZ=0
    g7: LineSegment StartX=-0.658262 StartY=-5 StartZ=0 EndX=0.658262 EndY=-5 EndZ=0
    g8: LineSegment StartX=0.658262 StartY=-5 StartZ=0 EndX=1.92993 EndY=-4.65926 EndZ=0
    g9: LineSegment StartX=1.92993 StartY=-4.65926 StartZ=0 EndX=3.07007 EndY=-4.001 EndZ=0
    g10: LineSegment StartX=3.07007 StartY=-4.001 StartZ=0 EndX=4.001 EndY=-3.07007 EndZ=0
    g11: LineSegment StartX=4.001 StartY=-3.07007 StartZ=0 EndX=4.65926 EndY=-1.92993 EndZ=0
    g12: LineSegment StartX=4.65926 StartY=-1.92993 StartZ=0 EndX=5 EndY=-0.658262 EndZ=0
    g13: LineSegment StartX=5 StartY=-0.658262 StartZ=0 EndX=5 EndY=0.658262 EndZ=0
    g14: LineSegment StartX=5 StartY=0.658262 StartZ=0 EndX=4.65926 EndY=1.92993 EndZ=0
    g15: LineSegment StartX=4.65926 StartY=1.92993 StartZ=0 EndX=4.001 EndY=3.07007 EndZ=0
    g16: LineSegment StartX=4.001 StartY=3.07007 StartZ=0 EndX=3.07007 EndY=4.001 EndZ=0
    g17: LineSegment StartX=3.07007 StartY=4.001 StartZ=0 EndX=1.92993 EndY=4.65926 EndZ=0
    g18: LineSegment StartX=1.92993 StartY=4.65926 StartZ=0 EndX=0.658262 EndY=5 EndZ=0
    g19: LineSegment StartX=0.658262 StartY=5 StartZ=0 EndX=-0.658262 EndY=5 EndZ=0
    g20: LineSegment StartX=-0.658262 StartY=5 StartZ=0 EndX=-1.92993 EndY=4.65926 EndZ=0
    g21: LineSegment StartX=-1.92993 StartY=4.65926 StartZ=0 EndX=-3.07007 EndY=4.001 EndZ=0
    g22: LineSegment StartX=-3.07007 StartY=4.001 StartZ=0 EndX=-4.001 EndY=3.07007 EndZ=0
    g23: LineSegment StartX=-4.001 StartY=3.07007 StartZ=0 EndX=-4.65926 EndY=1.92993 EndZ=0
    g24: Circle CenterX=0 CenterY=0 CenterZ=0 NormalX=0 NormalY=0 NormalZ=1 AngleXU=0 Radius=5.04314
  constraints (52):
    c: Coincident(g0,g1)
    c: Coincident(g1,g2)
    c: Coincident(g2,g3)
    c: Coincident(g3,g4)
    c: Coincident(g4,g5)
    c: Coincident(g5,g6)
    c: Coincident(g6,g7)
    c: Coincident(g7,g8)
    c: Coincident(g8,g9)
    c: Coincident(g9,g10)
    c: Coincident(g10,g11)
    c: Coincident(g11,g12)
    c: Coincident(g12,g13)
    c: Coincident(g13,g14)
    c: Coincident(g14,g15)
    c: Coincident(g15,g16)
    c: Coincident(g16,g17)
    c: Coincident(g17,g18)
    c: Coincident(g18,g19)
    c: Coincident(g19,g20)
    c: Coincident(g20,g21)
    c: Coincident(g21,g22)
    c: Coincident(g22,g23)
    c: Coincident(g23,g0)
    c: Equal(g0, g1-g23) x23
    c: PointOnObject(g0,g24)
    c: PointOnObject(g1,g24)
    c: PointOnObject(g2,g24)
    c: PointOnObject(g3,g24)
    c: PointOnObject(g4,g24)
    c: PointOnObject(g5,g24)
    c: PointOnObject(g6,g24)
    c: PointOnObject(g7,g24)
    c: PointOnObject(g8,g24)
    c: PointOnObject(g9,g24)
    c: PointOnObject(g10,g24)
    c: PointOnObject(g11,g24)
    c: PointOnObject(g12,g24)
    c: PointOnObject(g13,g24)
    c: PointOnObject(g14,g24)
    c: PointOnObject(g15,g24)
    c: PointOnObject(g16,g24)
    c: PointOnObject(g17,g24)
    c: PointOnObject(g18,g24)
    c: PointOnObject(g19,g24)
    c: PointOnObject(g20,g24)
    c: PointOnObject(g21,g24)
    c: PointOnObject(g22,g24)
    c: PointOnObject(g23,g24)
    c: Coincident(g24,g-1)
    c: Horizontal(g19)
    c: DistanceX(g0,g13) = 10
FEATURE [PartDesign::AdditiveLoft] AdditiveLoft004
  AllowMultiFace = false
  Closed = false
  Profile = -> Sketch045
  Refine = true
  Ruled = false
  Sections = -> [Sketch044,Sketch046]
FEATURE [Sketcher::SketchObject] Sketch040
  FullyConstrained = false
  MapMode = 5
  Placement = pos=(0,0,17) rot=(0,0,1;0rad)
  Support = -> [AdditiveLoft004]
  sketch-geometry (1):
    g0: Circle CenterX=0 CenterY=0 CenterZ=0 NormalX=0 NormalY=0 NormalZ=1 AngleXU=0 Radius=4.5
  constraints (2):
    c: Coincident(g0,g-1)
    c: Radius(g0) = 4.5
FEATURE [PartDesign::Pad] Pad010
  AllowMultiFace = false
  BaseFeature = -> AdditiveLoft004
  Direction = (1,1,1)
  Length = 0.7
  Length2 = 100
  Profile = -> Sketch040
  Refine = true
  Type = 0
FEATURE [Sketcher::SketchObject] Sketch039
  FullyConstrained = false
  MapMode = 5
  Placement = pos=(0,0,0) rot=(1,0,0;3.14159rad)
  Support = -> [Pad010]
  sketch-geometry (1):
    g0: Circle CenterX=0 CenterY=0 CenterZ=0 NormalX=0 NormalY=0 NormalZ=1 AngleXU=0 Radius=5
  constraints (2):
    c: Coincident(g0,g-1)
    c: Radius(g0) = 5
FEATURE [PartDesign::Pocket] Pocket016
  AllowMultiFace = false
  BaseFeature = -> Pad010
  Direction = (1,1,1)
  Length = 1
  Length2 = 100
  Profile = -> Sketch039
  Refine = true
  Type = 0
FEATURE [Sketcher::SketchObject] Sketch037
  FullyConstrained = false
  MapMode = 5
  Placement = pos=(0,0,1) rot=(1,0,0;3.14159rad)
  Support = -> [Pocket016]
  sketch-geometry (1):
    g0: Circle CenterX=0 CenterY=0 CenterZ=0 NormalX=0 NormalY=0 NormalZ=1 AngleXU=0 Radius=4.65
  constraints (2):
    c: Coincident(g0,g-1)
    c: Radius(g0) = 4.65
FEATURE [PartDesign::Pocket] Pocket015
  AllowMultiFace = false
  BaseFeature = -> Pocket016
  Direction = (1,1,1)
  Length = 1
  Length2 = 100
  Profile = -> Sketch037
  Refine = true
  Type = 0
FEATURE [Sketcher::SketchObject] Sketch038
  FullyConstrained = false
  MapMode = 5
  Placement = pos=(0,0,2) rot=(1,0,0;3.14159rad)
  Support = -> [Pocket015]
  sketch-geometry (2):
    g0: ArcOfCircle CenterX=0 CenterY=0 CenterZ=0 NormalX=0 NormalY=0 NormalZ=1 AngleXU=0 Radius=3 StartAngle=2.19024 EndAngle=7.23453
    g1: LineSegment StartX=-1.74176 StartY=2.4426 StartZ=0 EndX=1.74176 EndY=2.4426 EndZ=0
  constraints (5):
    c: Coincident(g0,g-1)
    c: Coincident(g1,g0)
    c: Coincident(g1,g0)
    c: Horizontal(g1)
    c: Radius(g0) = 3
FEATURE [PartDesign::Pocket] Pocket017
  AllowMultiFace = false
  BaseFeature = -> Pocket015
  Direction = (1,1,1)
  Length = 8
  Length2 = 100
  Profile = -> Sketch038
  Refine = true
  Type = 0
FEATURE [PartDesign::Chamfer] Chamfer012
  Angle = 45
  Base = -> Pocket017 [Edge82,Edge83]
  BaseFeature = -> Pocket017
  ChamferType = 0
  FlipDirection = false
  Size = 1.4
  Size2 = 1
  SupportTransform = false
  UseAllEdges = false
FEATURE [PartDesign::Chamfer] Chamfer011
  Angle = 45
  Base = -> Chamfer012 [Edge8]
  BaseFeature = -> Chamfer012
  ChamferType = 0
  FlipDirection = false
  Size = 0.3
  Size2 = 1
  SupportTransform = false
  UseAllEdges = false
FEATURE [PartDesign::Fillet] Fillet005
  Base = -> Chamfer011 [Edge93,Face36]
  BaseFeature = -> Chamfer011
  Radius = 0.1
  SupportTransform = false
  UseAllEdges = false
FEATURE [PartDesign::Body] Body010
  Group = -> [Sketch045,Sketch044,Sketch046,AdditiveLoft004,Sketch040,Pad010,Sketch039,Pocket016,Sketch037,Pocket015,Sketch038,Pocket017,Chamfer012,Chamfer011,Fillet005]
  Origin = -> Origin025
  Tip = -> Fillet005
FEATURE [Sketcher::SketchObject] Sketch047
  AttachmentOffset = pos=(0,0,17.7) rot=(0,0,1;0rad)
  FullyConstrained = false
  MapMode = 5
  Placement = pos=(0,0,17.7) rot=(0,0,1;0rad)
  Support = -> [XY_Plane018]
  sketch-geometry (10):
    g0: LineSegment StartX=-0.2 StartY=1.5 StartZ=0 EndX=0.2 EndY=1.5 EndZ=0
    g1: LineSegment StartX=0.4 StartY=1.7 StartZ=0 EndX=0.4 EndY=4.2 EndZ=0
    g2: LineSegment StartX=0.2 StartY=4.4 StartZ=0 EndX=-0.2 EndY=4.4 EndZ=0
    g3: LineSegment StartX=-0.4 StartY=4.2 StartZ=0 EndX=-0.4 EndY=1.7 EndZ=0
    g4: ArcOfCircle CenterX=-0.2 CenterY=1.7 CenterZ=0 NormalX=0 NormalY=0 NormalZ=1 AngleXU=0 Radius=0.2 StartAngle=3.14159 EndAngle=4.71239
    g5: ArcOfCircle CenterX=0.2 CenterY=1.7 CenterZ=0 NormalX=0 NormalY=0 NormalZ=1 AngleXU=0 Radius=0.2 StartAngle=4.71239 EndAngle=6.28319
    g6: ArcOfCircle CenterX=0.2 CenterY=4.2 CenterZ=0 NormalX=0 NormalY=0 NormalZ=1 AngleXU=0 Radius=0.2 StartAngle=1.4e-15 EndAngle=1.5708
    g7: ArcOfCircle CenterX=-0.2 CenterY=4.2 CenterZ=0 NormalX=0 NormalY=0 NormalZ=1 AngleXU=0 Radius=0.2 StartAngle=1.5708 EndAngle=3.14159
    g8: LineSegment StartX=-0.2 StartY=1.7 StartZ=0 EndX=0 EndY=0 EndZ=0
    g9: LineSegment StartX=0 StartY=0 StartZ=0 EndX=0.2 EndY=1.7 EndZ=0
  constraints (24):
    c: Horizontal(g0)
    c: Horizontal(g2)
    c: Vertical(g1)
    c: Vertical(g3)
    c: Tangent(g3,g4) = -1.5708
    c: Tangent(g0,g4) = -1.5708
    c: Tangent(g0,g5) = -1.5708
    c: Tangent(g1,g5) = -1.5708
    c: Tangent(g1,g6) = -1.5708
    c: Tangent(g2,g6) = -1.5708
    c: Tangent(g2,g7) = -1.5708
    c: Tangent(g3,g7) = -1.5708
    c: Radius(g7) = 0.2
    c: Equal(g7,g6)
    c: Equal(g7,g5)
    c: Equal(g7,g4)
    c: Coincident(g8,g4)
    c: Coincident(g8,g-1)
    c: Coincident(g9,g-1)
    c: Coincident(g9,g5)
    c: Equal(g9,g8)
    c: DistanceX(g3,g1) = 0.8
    c: DistanceY(g-1,g2) = 4.4
    c: DistanceY(g-1,g0) = 1.5
FEATURE [PartDesign::Pad] Pad011
  AllowMultiFace = false
  Direction = (1,1,1)
  Length = 0.02
  Length2 = 100
  Profile = -> Sketch047
  Refine = true
  Type = 0
FEATURE [PartDesign::Body] Body011  label="Indicator005"
  Group = -> [Sketch047,Pad011]
  Origin = -> Origin015
  Tip = -> Pad011
FEATURE [App::Part] Part007  label="Cap008"
  Group = -> [Body010,Body011]
  Origin = -> Origin014
  Placement = pos=(-13.335,13.335,0) rot=(0,0,1;0rad)
  expr: .Placement.Base.x = -13.335
  expr: .Placement.Base.y = 13.335
FEATURE [Sketcher::SketchObject] Sketch052
  AttachmentOffset = pos=(0,0,7) rot=(0,0,1;0rad)
  FullyConstrained = false
  MapMode = 5
  Placement = pos=(0,0,7) rot=(0,0,1;0rad)
  Support = -> [XY_Plane020]
  sketch-geometry (25):
    g0: LineSegment StartX=-0.724089 StartY=5.5 StartZ=0 EndX=-2.12292 EndY=5.12518 EndZ=0
    g1: LineSegment StartX=-2.12292 StartY=5.12518 StartZ=0 EndX=-3.37708 EndY=4.4011 EndZ=0
    g2: LineSegment StartX=-3.37708 StartY=4.4011 StartZ=0 EndX=-4.4011 EndY=3.37708 EndZ=0
    g3: LineSegment StartX=-4.4011 StartY=3.37708 StartZ=0 EndX=-5.12518 EndY=2.12292 EndZ=0
    g4: LineSegment StartX=-5.12518 StartY=2.12292 StartZ=0 EndX=-5.5 EndY=0.724089 EndZ=0
    g5: LineSegment StartX=-5.5 StartY=0.724089 StartZ=0 EndX=-5.5 EndY=-0.724089 EndZ=0
    g6: LineSegment StartX=-5.5 StartY=-0.724089 StartZ=0 EndX=-5.12518 EndY=-2.12292 EndZ=0
    g7: LineSegment StartX=-5.12518 StartY=-2.12292 StartZ=0 EndX=-4.4011 EndY=-3.37708 EndZ=0
    g8: LineSegment StartX=-4.4011 StartY=-3.37708 StartZ=0 EndX=-3.37708 EndY=-4.4011 EndZ=0
    g9: LineSegment StartX=-3.37708 StartY=-4.4011 StartZ=0 EndX=-2.12292 EndY=-5.12518 EndZ=0
    g10: LineSegment StartX=-2.12292 StartY=-5.12518 StartZ=0 EndX=-0.724089 EndY=-5.5 EndZ=0
    g11: LineSegment StartX=-0.724089 StartY=-5.5 StartZ=0 EndX=0.724089 EndY=-5.5 EndZ=0
    g12: LineSegment StartX=0.724089 StartY=-5.5 StartZ=0 EndX=2.12292 EndY=-5.12518 EndZ=0
    g13: LineSegment StartX=2.12292 StartY=-5.12518 StartZ=0 EndX=3.37708 EndY=-4.4011 EndZ=0
    g14: LineSegment StartX=3.37708 StartY=-4.4011 StartZ=0 EndX=4.4011 EndY=-3.37708 EndZ=0
    g15: LineSegment StartX=4.4011 StartY=-3.37708 StartZ=0 EndX=5.12518 EndY=-2.12292 EndZ=0
    g16: LineSegment StartX=5.12518 StartY=-2.12292 StartZ=0 EndX=5.5 EndY=-0.724089 EndZ=0
    g17: LineSegment StartX=5.5 StartY=-0.724089 StartZ=0 EndX=5.5 EndY=0.724089 EndZ=0
    g18: LineSegment StartX=5.5 StartY=0.724089 StartZ=0 EndX=5.12518 EndY=2.12292 EndZ=0
    g19: LineSegment StartX=5.12518 StartY=2.12292 StartZ=0 EndX=4.4011 EndY=3.37708 EndZ=0
    g20: LineSegment StartX=4.4011 StartY=3.37708 StartZ=0 EndX=3.37708 EndY=4.4011 EndZ=0
    g21: LineSegment StartX=3.37708 StartY=4.4011 StartZ=0 EndX=2.12292 EndY=5.12518 EndZ=0
    g22: LineSegment StartX=2.12292 StartY=5.12518 StartZ=0 EndX=0.724089 EndY=5.5 EndZ=0
    g23: LineSegment StartX=0.724089 StartY=5.5 StartZ=0 EndX=-0.724089 EndY=5.5 EndZ=0
    g24: Circle CenterX=0 CenterY=0 CenterZ=0 NormalX=0 NormalY=0 NormalZ=1 AngleXU=0 Radius=5.54746
  constraints (52):
    c: Coincident(g0,g1)
    c: Coincident(g1,g2)
    c: Coincident(g2,g3)
    c: Coincident(g3,g4)
    c: Coincident(g4,g5)
    c: Coincident(g5,g6)
    c: Coincident(g6,g7)
    c: Coincident(g7,g8)
    c: Coincident(g8,g9)
    c: Coincident(g9,g10)
    c: Coincident(g10,g11)
    c: Coincident(g11,g12)
    c: Coincident(g12,g13)
    c: Coincident(g13,g14)
    c: Coincident(g14,g15)
    c: Coincident(g15,g16)
    c: Coincident(g16,g17)
    c: Coincident(g17,g18)
    c: Coincident(g18,g19)
    c: Coincident(g19,g20)
    c: Coincident(g20,g21)
    c: Coincident(g21,g22)
    c: Coincident(g22,g23)
    c: Coincident(g23,g0)
    c: Equal(g0, g1-g23) x23
    c: PointOnObject(g0,g24)
    c: PointOnObject(g1,g24)
    c: PointOnObject(g2,g24)
    c: PointOnObject(g3,g24)
    c: PointOnObject(g4,g24)
    c: PointOnObject(g5,g24)
    c: PointOnObject(g6,g24)
    c: PointOnObject(g7,g24)
    c: PointOnObject(g8,g24)
    c: PointOnObject(g9,g24)
    c: PointOnObject(g10,g24)
    c: PointOnObject(g11,g24)
    c: PointOnObject(g12,g24)
    c: PointOnObject(g13,g24)
    c: PointOnObject(g14,g24)
    c: PointOnObject(g15,g24)
    c: PointOnObject(g16,g24)
    c: PointOnObject(g17,g24)
    c: PointOnObject(g18,g24)
    c: PointOnObject(g19,g24)
    c: PointOnObject(g20,g24)
    c: PointOnObject(g21,g24)
    c: PointOnObject(g22,g24)
    c: PointOnObject(g23,g24)
    c: Coincident(g24,g-1)
    c: Horizontal(g23)
    c: DistanceX(g4,g17) = 11
FEATURE [Sketcher::SketchObject] Sketch053
  FullyConstrained = false
  MapMode = 5
  Support = -> [XY_Plane020]
  sketch-geometry (25):
    g0: LineSegment StartX=-0.789915 StartY=6 StartZ=0 EndX=-2.31591 EndY=5.59111 EndZ=0
    g1: LineSegment StartX=-2.31591 StartY=5.59111 StartZ=0 EndX=-3.68409 EndY=4.80119 EndZ=0
    g2: LineSegment StartX=-3.68409 StartY=4.80119 StartZ=0 EndX=-4.80119 EndY=3.68409 EndZ=0
    g3: LineSegment StartX=-4.80119 StartY=3.68409 StartZ=0 EndX=-5.59111 EndY=2.31591 EndZ=0
    g4: LineSegment StartX=-5.59111 StartY=2.31591 StartZ=0 EndX=-6 EndY=0.789915 EndZ=0
    g5: LineSegment StartX=-6 StartY=0.789915 StartZ=0 EndX=-6 EndY=-0.789915 EndZ=0
    g6: LineSegment StartX=-6 StartY=-0.789915 StartZ=0 EndX=-5.59111 EndY=-2.31591 EndZ=0
    g7: LineSegment StartX=-5.59111 StartY=-2.31591 StartZ=0 EndX=-4.80119 EndY=-3.68409 EndZ=0
    g8: LineSegment StartX=-4.80119 StartY=-3.68409 StartZ=0 EndX=-3.68409 EndY=-4.80119 EndZ=0
    g9: LineSegment StartX=-3.68409 StartY=-4.80119 StartZ=0 EndX=-2.31591 EndY=-5.59111 EndZ=0
    g10: LineSegment StartX=-2.31591 StartY=-5.59111 StartZ=0 EndX=-0.789915 EndY=-6 EndZ=0
    g11: LineSegment StartX=-0.789915 StartY=-6 StartZ=0 EndX=0.789915 EndY=-6 EndZ=0
    g12: LineSegment StartX=0.789915 StartY=-6 StartZ=0 EndX=2.31591 EndY=-5.59111 EndZ=0
    g13: LineSegment StartX=2.31591 StartY=-5.59111 StartZ=0 EndX=3.68409 EndY=-4.80119 EndZ=0
    g14: LineSegment StartX=3.68409 StartY=-4.80119 StartZ=0 EndX=4.80119 EndY=-3.68409 EndZ=0
    g15: LineSegment StartX=4.80119 StartY=-3.68409 StartZ=0 EndX=5.59111 EndY=-2.31591 EndZ=0
    g16: LineSegment StartX=5.59111 StartY=-2.31591 StartZ=0 EndX=6 EndY=-0.789915 EndZ=0
    g17: LineSegment StartX=6 StartY=-0.789915 StartZ=0 EndX=6 EndY=0.789915 EndZ=0
    g18: LineSegment StartX=6 StartY=0.789915 StartZ=0 EndX=5.59111 EndY=2.31591 EndZ=0
    g19: LineSegment StartX=5.59111 StartY=2.31591 StartZ=0 EndX=4.80119 EndY=3.68409 EndZ=0
    g20: LineSegment StartX=4.80119 StartY=3.68409 StartZ=0 EndX=3.68409 EndY=4.80119 EndZ=0
    g21: LineSegment StartX=3.68409 StartY=4.80119 StartZ=0 EndX=2.31591 EndY=5.59111 EndZ=0
    g22: LineSegment StartX=2.31591 StartY=5.59111 StartZ=0 EndX=0.789915 EndY=6 EndZ=0
    g23: LineSegment StartX=0.789915 StartY=6 StartZ=0 EndX=-0.789915 EndY=6 EndZ=0
    g24: Circle CenterX=0 CenterY=0 CenterZ=0 NormalX=0 NormalY=0 NormalZ=1 AngleXU=0 Radius=6.05177
  constraints (52):
    c: Coincident(g0,g1)
    c: Coincident(g1,g2)
    c: Coincident(g2,g3)
    c: Coincident(g3,g4)
    c: Coincident(g4,g5)
    c: Coincident(g5,g6)
    c: Coincident(g6,g7)
    c: Coincident(g7,g8)
    c: Coincident(g8,g9)
    c: Coincident(g9,g10)
    c: Coincident(g10,g11)
    c: Coincident(g11,g12)
    c: Coincident(g12,g13)
    c: Coincident(g13,g14)
    c: Coincident(g14,g15)
    c: Coincident(g15,g16)
    c: Coincident(g16,g17)
    c: Coincident(g17,g18)
    c: Coincident(g18,g19)
    c: Coincident(g19,g20)
    c: Coincident(g20,g21)
    c: Coincident(g21,g22)
    c: Coincident(g22,g23)
    c: Coincident(g23,g0)
    c: Equal(g0, g1-g23) x23
    c: PointOnObject(g0,g24)
    c: PointOnObject(g1,g24)
    c: PointOnObject(g2,g24)
    c: PointOnObject(g3,g24)
    c: PointOnObject(g4,g24)
    c: PointOnObject(g5,g24)
    c: PointOnObject(g6,g24)
    c: PointOnObject(g7,g24)
    c: PointOnObject(g8,g24)
    c: PointOnObject(g9,g24)
    c: PointOnObject(g10,g24)
    c: PointOnObject(g11,g24)
    c: PointOnObject(g12,g24)
    c: PointOnObject(g13,g24)
    c: PointOnObject(g14,g24)
    c: PointOnObject(g15,g24)
    c: PointOnObject(g16,g24)
    c: PointOnObject(g17,g24)
    c: PointOnObject(g18,g24)
    c: PointOnObject(g19,g24)
    c: PointOnObject(g20,g24)
    c: PointOnObject(g21,g24)
    c: PointOnObject(g22,g24)
    c: PointOnObject(g23,g24)
    c: Coincident(g24,g-1)
    c: Horizontal(g23)
    c: DistanceX(g4,g17) = 12
FEATURE [Sketcher::SketchObject] Sketch054
  AttachmentOffset = pos=(0,0,17) rot=(0,0,1;0rad)
  FullyConstrained = false
  MapMode = 5
  Placement = pos=(0,0,17) rot=(0,0,1;0rad)
  Support = -> [XY_Plane020]
  sketch-geometry (25):
    g0: LineSegment StartX=-4.65926 StartY=1.92993 StartZ=0 EndX=-5 EndY=0.658262 EndZ=0
    g1: LineSegment StartX=-5 StartY=0.658262 StartZ=0 EndX=-5 EndY=-0.658262 EndZ=0
    g2: LineSegment StartX=-5 StartY=-0.658262 StartZ=0 EndX=-4.65926 EndY=-1.92993 EndZ=0
    g3: LineSegment StartX=-4.65926 StartY=-1.92993 StartZ=0 EndX=-4.001 EndY=-3.07007 EndZ=0
    g4: LineSegment StartX=-4.001 StartY=-3.07007 StartZ=0 EndX=-3.07007 EndY=-4.001 EndZ=0
    g5: LineSegment StartX=-3.07007 StartY=-4.001 StartZ=0 EndX=-1.92993 EndY=-4.65926 EndZ=0
    g6: LineSegment StartX=-1.92993 StartY=-4.65926 StartZ=0 EndX=-0.658262 EndY=-5 EndZ=0
    g7: LineSegment StartX=-0.658262 StartY=-5 StartZ=0 EndX=0.658262 EndY=-5 EndZ=0
    g8: LineSegment StartX=0.658262 StartY=-5 StartZ=0 EndX=1.92993 EndY=-4.65926 EndZ=0
    g9: LineSegment StartX=1.92993 StartY=-4.65926 StartZ=0 EndX=3.07007 EndY=-4.001 EndZ=0
    g10: LineSegment StartX=3.07007 StartY=-4.001 StartZ=0 EndX=4.001 EndY=-3.07007 EndZ=0
    g11: LineSegment StartX=4.001 StartY=-3.07007 StartZ=0 EndX=4.65926 EndY=-1.92993 EndZ=0
    g12: LineSegment StartX=4.65926 StartY=-1.92993 StartZ=0 EndX=5 EndY=-0.658262 EndZ=0
    g13: LineSegment StartX=5 StartY=-0.658262 StartZ=0 EndX=5 EndY=0.658262 EndZ=0
    g14: LineSegment StartX=5 StartY=0.658262 StartZ=0 EndX=4.65926 EndY=1.92993 EndZ=0
    g15: LineSegment StartX=4.65926 StartY=1.92993 StartZ=0 EndX=4.001 EndY=3.07007 EndZ=0
    g16: LineSegment StartX=4.001 StartY=3.07007 StartZ=0 EndX=3.07007 EndY=4.001 EndZ=0
    g17: LineSegment StartX=3.07007 StartY=4.001 StartZ=0 EndX=1.92993 EndY=4.65926 EndZ=0
    g18: LineSegment StartX=1.92993 StartY=4.65926 StartZ=0 EndX=0.658262 EndY=5 EndZ=0
    g19: LineSegment StartX=0.658262 StartY=5 StartZ=0 EndX=-0.658262 EndY=5 EndZ=0
    g20: LineSegment StartX=-0.658262 StartY=5 StartZ=0 EndX=-1.92993 EndY=4.65926 EndZ=0
    g21: LineSegment StartX=-1.92993 StartY=4.65926 StartZ=0 EndX=-3.07007 EndY=4.001 EndZ=0
    g22: LineSegment StartX=-3.07007 StartY=4.001 StartZ=0 EndX=-4.001 EndY=3.07007 EndZ=0
    g23: LineSegment StartX=-4.001 StartY=3.07007 StartZ=0 EndX=-4.65926 EndY=1.92993 EndZ=0
    g24: Circle CenterX=0 CenterY=0 CenterZ=0 NormalX=0 NormalY=0 NormalZ=1 AngleXU=0 Radius=5.04314
  constraints (52):
    c: Coincident(g0,g1)
    c: Coincident(g1,g2)
    c: Coincident(g2,g3)
    c: Coincident(g3,g4)
    c: Coincident(g4,g5)
    c: Coincident(g5,g6)
    c: Coincident(g6,g7)
    c: Coincident(g7,g8)
    c: Coincident(g8,g9)
    c: Coincident(g9,g10)
    c: Coincident(g10,g11)
    c: Coincident(g11,g12)
    c: Coincident(g12,g13)
    c: Coincident(g13,g14)
    c: Coincident(g14,g15)
    c: Coincident(g15,g16)
    c: Coincident(g16,g17)
    c: Coincident(g17,g18)
    c: Coincident(g18,g19)
    c: Coincident(g19,g20)
    c: Coincident(g20,g21)
    c: Coincident(g21,g22)
    c: Coincident(g22,g23)
    c: Coincident(g23,g0)
    c: Equal(g0, g1-g23) x23
    c: PointOnObject(g0,g24)
    c: PointOnObject(g1,g24)
    c: PointOnObject(g2,g24)
    c: PointOnObject(g3,g24)
    c: PointOnObject(g4,g24)
    c: PointOnObject(g5,g24)
    c: PointOnObject(g6,g24)
    c: PointOnObject(g7,g24)
    c: PointOnObject(g8,g24)
    c: PointOnObject(g9,g24)
    c: PointOnObject(g10,g24)
    c: PointOnObject(g11,g24)
    c: PointOnObject(g12,g24)
    c: PointOnObject(g13,g24)
    c: PointOnObject(g14,g24)
    c: PointOnObject(g15,g24)
    c: PointOnObject(g16,g24)
    c: PointOnObject(g17,g24)
    c: PointOnObject(g18,g24)
    c: PointOnObject(g19,g24)
    c: PointOnObject(g20,g24)
    c: PointOnObject(g21,g24)
    c: PointOnObject(g22,g24)
    c: PointOnObject(g23,g24)
    c: Coincident(g24,g-1)
    c: Horizontal(g19)
    c: DistanceX(g0,g13) = 10
FEATURE [PartDesign::AdditiveLoft] AdditiveLoft005
  AllowMultiFace = false
  Closed = false
  Profile = -> Sketch053
  Refine = true
  Ruled = false
  Sections = -> [Sketch052,Sketch054]
FEATURE [Sketcher::SketchObject] Sketch051
  FullyConstrained = false
  MapMode = 5
  Placement = pos=(0,0,17) rot=(0,0,1;0rad)
  Support = -> [AdditiveLoft005]
  sketch-geometry (1):
    g0: Circle CenterX=0 CenterY=0 CenterZ=0 NormalX=0 NormalY=0 NormalZ=1 AngleXU=0 Radius=4.5
  constraints (2):
    c: Coincident(g0,g-1)
    c: Radius(g0) = 4.5
FEATURE [PartDesign::Pad] Pad012
  AllowMultiFace = false
  BaseFeature = -> AdditiveLoft005
  Direction = (1,1,1)
  Length = 0.7
  Length2 = 100
  Profile = -> Sketch051
  Refine = true
  Type = 0
FEATURE [Sketcher::SketchObject] Sketch050
  FullyConstrained = false
  MapMode = 5
  Placement = pos=(0,0,0) rot=(1,0,0;3.14159rad)
  Support = -> [Pad012]
  sketch-geometry (1):
    g0: Circle CenterX=0 CenterY=0 CenterZ=0 NormalX=0 NormalY=0 NormalZ=1 AngleXU=0 Radius=5
  constraints (2):
    c: Coincident(g0,g-1)
    c: Radius(g0) = 5
FEATURE [PartDesign::Pocket] Pocket019
  AllowMultiFace = false
  BaseFeature = -> Pad012
  Direction = (1,1,1)
  Length = 1
  Length2 = 100
  Profile = -> Sketch050
  Refine = true
  Type = 0
FEATURE [Sketcher::SketchObject] Sketch048
  FullyConstrained = false
  MapMode = 5
  Placement = pos=(0,0,1) rot=(1,0,0;3.14159rad)
  Support = -> [Pocket019]
  sketch-geometry (1):
    g0: Circle CenterX=0 CenterY=0 CenterZ=0 NormalX=0 NormalY=0 NormalZ=1 AngleXU=0 Radius=4.65
  constraints (2):
    c: Coincident(g0,g-1)
    c: Radius(g0) = 4.65
FEATURE [PartDesign::Pocket] Pocket018
  AllowMultiFace = false
  BaseFeature = -> Pocket019
  Direction = (1,1,1)
  Length = 1
  Length2 = 100
  Profile = -> Sketch048
  Refine = true
  Type = 0
FEATURE [Sketcher::SketchObject] Sketch049
  FullyConstrained = false
  MapMode = 5
  Placement = pos=(0,0,2) rot=(1,0,0;3.14159rad)
  Support = -> [Pocket018]
  sketch-geometry (2):
    g0: ArcOfCircle CenterX=0 CenterY=0 CenterZ=0 NormalX=0 NormalY=0 NormalZ=1 AngleXU=0 Radius=3 StartAngle=2.19024 EndAngle=7.23453
    g1: LineSegment StartX=-1.74176 StartY=2.4426 StartZ=0 EndX=1.74176 EndY=2.4426 EndZ=0
  constraints (5):
    c: Coincident(g0,g-1)
    c: Coincident(g1,g0)
    c: Coincident(g1,g0)
    c: Horizontal(g1)
    c: Radius(g0) = 3
FEATURE [PartDesign::Pocket] Pocket020
  AllowMultiFace = false
  BaseFeature = -> Pocket018
  Direction = (1,1,1)
  Length = 8
  Length2 = 100
  Profile = -> Sketch049
  Refine = true
  Type = 0
FEATURE [PartDesign::Chamfer] Chamfer014
  Angle = 45
  Base = -> Pocket020 [Edge82,Edge83]
  BaseFeature = -> Pocket020
  ChamferType = 0
  FlipDirection = false
  Size = 1.4
  Size2 = 1
  SupportTransform = false
  UseAllEdges = false
FEATURE [PartDesign::Chamfer] Chamfer010
  Angle = 45
  Base = -> Chamfer014 [Edge8]
  BaseFeature = -> Chamfer014
  ChamferType = 0
  FlipDirection = false
  Size = 0.3
  Size2 = 1
  SupportTransform = false
  UseAllEdges = false
FEATURE [PartDesign::Fillet] Fillet007
  Base = -> Chamfer010 [Edge93,Face36]
  BaseFeature = -> Chamfer010
  Radius = 0.1
  SupportTransform = false
  UseAllEdges = false
FEATURE [PartDesign::Body] Body012
  Group = -> [Sketch053,Sketch052,Sketch054,AdditiveLoft005,Sketch051,Pad012,Sketch050,Pocket019,Sketch048,Pocket018,Sketch049,Pocket020,Chamfer014,Chamfer010,Fillet007]
  Origin = -> Origin018
  Tip = -> Fillet007
FEATURE [Sketcher::SketchObject] Sketch055
  AttachmentOffset = pos=(0,0,17.7) rot=(0,0,1;0rad)
  FullyConstrained = false
  MapMode = 5
  Placement = pos=(0,0,17.7) rot=(0,0,1;0rad)
  Support = -> [XY_Plane021]
  sketch-geometry (10):
    g0: LineSegment StartX=-0.2 StartY=1.5 StartZ=0 EndX=0.2 EndY=1.5 EndZ=0
    g1: LineSegment StartX=0.4 StartY=1.7 StartZ=0 EndX=0.4 EndY=4.2 EndZ=0
    g2: LineSegment StartX=0.2 StartY=4.4 StartZ=0 EndX=-0.2 EndY=4.4 EndZ=0
    g3: LineSegment StartX=-0.4 StartY=4.2 StartZ=0 EndX=-0.4 EndY=1.7 EndZ=0
    g4: ArcOfCircle CenterX=-0.2 CenterY=1.7 CenterZ=0 NormalX=0 NormalY=0 NormalZ=1 AngleXU=0 Radius=0.2 StartAngle=3.14159 EndAngle=4.71239
    g5: ArcOfCircle CenterX=0.2 CenterY=1.7 CenterZ=0 NormalX=0 NormalY=0 NormalZ=1 AngleXU=0 Radius=0.2 StartAngle=4.71239 EndAngle=6.28319
    g6: ArcOfCircle CenterX=0.2 CenterY=4.2 CenterZ=0 NormalX=0 NormalY=0 NormalZ=1 AngleXU=0 Radius=0.2 StartAngle=1.4e-15 EndAngle=1.5708
    g7: ArcOfCircle CenterX=-0.2 CenterY=4.2 CenterZ=0 NormalX=0 NormalY=0 NormalZ=1 AngleXU=0 Radius=0.2 StartAngle=1.5708 EndAngle=3.14159
    g8: LineSegment StartX=-0.2 StartY=1.7 StartZ=0 EndX=0 EndY=0 EndZ=0
    g9: LineSegment StartX=0 StartY=0 StartZ=0 EndX=0.2 EndY=1.7 EndZ=0
  constraints (24):
    c: Horizontal(g0)
    c: Horizontal(g2)
    c: Vertical(g1)
    c: Vertical(g3)
    c: Tangent(g3,g4) = -1.5708
    c: Tangent(g0,g4) = -1.5708
    c: Tangent(g0,g5) = -1.5708
    c: Tangent(g1,g5) = -1.5708
    c: Tangent(g1,g6) = -1.5708
    c: Tangent(g2,g6) = -1.5708
    c: Tangent(g2,g7) = -1.5708
    c: Tangent(g3,g7) = -1.5708
    c: Radius(g7) = 0.2
    c: Equal(g7,g6)
    c: Equal(g7,g5)
    c: Equal(g7,g4)
    c: Coincident(g8,g4)
    c: Coincident(g8,g-1)
    c: Coincident(g9,g-1)
    c: Coincident(g9,g5)
    c: Equal(g9,g8)
    c: DistanceX(g3,g1) = 0.8
    c: DistanceY(g-1,g2) = 4.4
    c: DistanceY(g-1,g0) = 1.5
FEATURE [PartDesign::Pad] Pad013
  AllowMultiFace = false
  Direction = (1,1,1)
  Length = 0.02
  Length2 = 100
  Profile = -> Sketch055
  Refine = true
  Type = 0
FEATURE [PartDesign::Body] Body013  label="Indicator006"
  Group = -> [Sketch055,Pad013]
  Origin = -> Origin016
  Tip = -> Pad013
FEATURE [App::Part] Part005  label="Cap006"
  Group = -> [Body012,Body013]
  Origin = -> Origin017
  Placement = pos=(13.335,13.335,0) rot=(0,0,1;0rad)
  expr: .Placement.Base.x = 13.335
  expr: .Placement.Base.y = 13.335
FEATURE [Sketcher::SketchObject] Sketch060
  AttachmentOffset = pos=(0,0,7) rot=(0,0,1;0rad)
  FullyConstrained = false
  MapMode = 5
  Placement = pos=(0,0,7) rot=(0,0,1;0rad)
  Support = -> [XY_Plane023]
  sketch-geometry (25):
    g0: LineSegment StartX=-0.724089 StartY=5.5 StartZ=0 EndX=-2.12292 EndY=5.12518 EndZ=0
    g1: LineSegment StartX=-2.12292 StartY=5.12518 StartZ=0 EndX=-3.37708 EndY=4.4011 EndZ=0
    g2: LineSegment StartX=-3.37708 StartY=4.4011 StartZ=0 EndX=-4.4011 EndY=3.37708 EndZ=0
    g3: LineSegment StartX=-4.4011 StartY=3.37708 StartZ=0 EndX=-5.12518 EndY=2.12292 EndZ=0
    g4: LineSegment StartX=-5.12518 StartY=2.12292 StartZ=0 EndX=-5.5 EndY=0.724089 EndZ=0
    g5: LineSegment StartX=-5.5 StartY=0.724089 StartZ=0 EndX=-5.5 EndY=-0.724089 EndZ=0
    g6: LineSegment StartX=-5.5 StartY=-0.724089 StartZ=0 EndX=-5.12518 EndY=-2.12292 EndZ=0
    g7: LineSegment StartX=-5.12518 StartY=-2.12292 StartZ=0 EndX=-4.4011 EndY=-3.37708 EndZ=0
    g8: LineSegment StartX=-4.4011 StartY=-3.37708 StartZ=0 EndX=-3.37708 EndY=-4.4011 EndZ=0
    g9: LineSegment StartX=-3.37708 StartY=-4.4011 StartZ=0 EndX=-2.12292 EndY=-5.12518 EndZ=0
    g10: LineSegment StartX=-2.12292 StartY=-5.12518 StartZ=0 EndX=-0.724089 EndY=-5.5 EndZ=0
    g11: LineSegment StartX=-0.724089 StartY=-5.5 StartZ=0 EndX=0.724089 EndY=-5.5 EndZ=0
    g12: LineSegment StartX=0.724089 StartY=-5.5 StartZ=0 EndX=2.12292 EndY=-5.12518 EndZ=0
    g13: LineSegment StartX=2.12292 StartY=-5.12518 StartZ=0 EndX=3.37708 EndY=-4.4011 EndZ=0
    g14: LineSegment StartX=3.37708 StartY=-4.4011 StartZ=0 EndX=4.4011 EndY=-3.37708 EndZ=0
    g15: LineSegment StartX=4.4011 StartY=-3.37708 StartZ=0 EndX=5.12518 EndY=-2.12292 EndZ=0
    g16: LineSegment StartX=5.12518 StartY=-2.12292 StartZ=0 EndX=5.5 EndY=-0.724089 EndZ=0
    g17: LineSegment StartX=5.5 StartY=-0.724089 StartZ=0 EndX=5.5 EndY=0.724089 EndZ=0
    g18: LineSegment StartX=5.5 StartY=0.724089 StartZ=0 EndX=5.12518 EndY=2.12292 EndZ=0
    g19: LineSegment StartX=5.12518 StartY=2.12292 StartZ=0 EndX=4.4011 EndY=3.37708 EndZ=0
    g20: LineSegment StartX=4.4011 StartY=3.37708 StartZ=0 EndX=3.37708 EndY=4.4011 EndZ=0
    g21: LineSegment StartX=3.37708 StartY=4.4011 StartZ=0 EndX=2.12292 EndY=5.12518 EndZ=0
    g22: LineSegment StartX=2.12292 StartY=5.12518 StartZ=0 EndX=0.724089 EndY=5.5 EndZ=0
    g23: LineSegment StartX=0.724089 StartY=5.5 StartZ=0 EndX=-0.724089 EndY=5.5 EndZ=0
    g24: Circle CenterX=0 CenterY=0 CenterZ=0 NormalX=0 NormalY=0 NormalZ=1 AngleXU=0 Radius=5.54746
  constraints (52):
    c: Coincident(g0,g1)
    c: Coincident(g1,g2)
    c: Coincident(g2,g3)
    c: Coincident(g3,g4)
    c: Coincident(g4,g5)
    c: Coincident(g5,g6)
    c: Coincident(g6,g7)
    c: Coincident(g7,g8)
    c: Coincident(g8,g9)
    c: Coincident(g9,g10)
    c: Coincident(g10,g11)
    c: Coincident(g11,g12)
    c: Coincident(g12,g13)
    c: Coincident(g13,g14)
    c: Coincident(g14,g15)
    c: Coincident(g15,g16)
    c: Coincident(g16,g17)
    c: Coincident(g17,g18)
    c: Coincident(g18,g19)
    c: Coincident(g19,g20)
    c: Coincident(g20,g21)
    c: Coincident(g21,g22)
    c: Coincident(g22,g23)
    c: Coincident(g23,g0)
    c: Equal(g0, g1-g23) x23
    c: PointOnObject(g0,g24)
    c: PointOnObject(g1,g24)
    c: PointOnObject(g2,g24)
    c: PointOnObject(g3,g24)
    c: PointOnObject(g4,g24)
    c: PointOnObject(g5,g24)
    c: PointOnObject(g6,g24)
    c: PointOnObject(g7,g24)
    c: PointOnObject(g8,g24)
    c: PointOnObject(g9,g24)
    c: PointOnObject(g10,g24)
    c: PointOnObject(g11,g24)
    c: PointOnObject(g12,g24)
    c: PointOnObject(g13,g24)
    c: PointOnObject(g14,g24)
    c: PointOnObject(g15,g24)
    c: PointOnObject(g16,g24)
    c: PointOnObject(g17,g24)
    c: PointOnObject(g18,g24)
    c: PointOnObject(g19,g24)
    c: PointOnObject(g20,g24)
    c: PointOnObject(g21,g24)
    c: PointOnObject(g22,g24)
    c: PointOnObject(g23,g24)
    c: Coincident(g24,g-1)
    c: Horizontal(g23)
    c: DistanceX(g4,g17) = 11
FEATURE [Sketcher::SketchObject] Sketch061
  FullyConstrained = false
  MapMode = 5
  Support = -> [XY_Plane023]
  sketch-geometry (25):
    g0: LineSegment StartX=-0.789915 StartY=6 StartZ=0 EndX=-2.31591 EndY=5.59111 EndZ=0
    g1: LineSegment StartX=-2.31591 StartY=5.59111 StartZ=0 EndX=-3.68409 EndY=4.80119 EndZ=0
    g2: LineSegment StartX=-3.68409 StartY=4.80119 StartZ=0 EndX=-4.80119 EndY=3.68409 EndZ=0
    g3: LineSegment StartX=-4.80119 StartY=3.68409 StartZ=0 EndX=-5.59111 EndY=2.31591 EndZ=0
    g4: LineSegment StartX=-5.59111 StartY=2.31591 StartZ=0 EndX=-6 EndY=0.789915 EndZ=0
    g5: LineSegment StartX=-6 StartY=0.789915 StartZ=0 EndX=-6 EndY=-0.789915 EndZ=0
    g6: LineSegment StartX=-6 StartY=-0.789915 StartZ=0 EndX=-5.59111 EndY=-2.31591 EndZ=0
    g7: LineSegment StartX=-5.59111 StartY=-2.31591 StartZ=0 EndX=-4.80119 EndY=-3.68409 EndZ=0
    g8: LineSegment StartX=-4.80119 StartY=-3.68409 StartZ=0 EndX=-3.68409 EndY=-4.80119 EndZ=0
    g9: LineSegment StartX=-3.68409 StartY=-4.80119 StartZ=0 EndX=-2.31591 EndY=-5.59111 EndZ=0
    g10: LineSegment StartX=-2.31591 StartY=-5.59111 StartZ=0 EndX=-0.789915 EndY=-6 EndZ=0
    g11: LineSegment StartX=-0.789915 StartY=-6 StartZ=0 EndX=0.789915 EndY=-6 EndZ=0
    g12: LineSegment StartX=0.789915 StartY=-6 StartZ=0 EndX=2.31591 EndY=-5.59111 EndZ=0
    g13: LineSegment StartX=2.31591 StartY=-5.59111 StartZ=0 EndX=3.68409 EndY=-4.80119 EndZ=0
    g14: LineSegment StartX=3.68409 StartY=-4.80119 StartZ=0 EndX=4.80119 EndY=-3.68409 EndZ=0
    g15: LineSegment StartX=4.80119 StartY=-3.68409 StartZ=0 EndX=5.59111 EndY=-2.31591 EndZ=0
    g16: LineSegment StartX=5.59111 StartY=-2.31591 StartZ=0 EndX=6 EndY=-0.789915 EndZ=0
    g17: LineSegment StartX=6 StartY=-0.789915 StartZ=0 EndX=6 EndY=0.789915 EndZ=0
    g18: LineSegment StartX=6 StartY=0.789915 StartZ=0 EndX=5.59111 EndY=2.31591 EndZ=0
    g19: LineSegment StartX=5.59111 StartY=2.31591 StartZ=0 EndX=4.80119 EndY=3.68409 EndZ=0
    g20: LineSegment StartX=4.80119 StartY=3.68409 StartZ=0 EndX=3.68409 EndY=4.80119 EndZ=0
    g21: LineSegment StartX=3.68409 StartY=4.80119 StartZ=0 EndX=2.31591 EndY=5.59111 EndZ=0
    g22: LineSegment StartX=2.31591 StartY=5.59111 StartZ=0 EndX=0.789915 EndY=6 EndZ=0
    g23: LineSegment StartX=0.789915 StartY=6 StartZ=0 EndX=-0.789915 EndY=6 EndZ=0
    g24: Circle CenterX=0 CenterY=0 CenterZ=0 NormalX=0 NormalY=0 NormalZ=1 AngleXU=0 Radius=6.05177
  constraints (52):
    c: Coincident(g0,g1)
    c: Coincident(g1,g2)
    c: Coincident(g2,g3)
    c: Coincident(g3,g4)
    c: Coincident(g4,g5)
    c: Coincident(g5,g6)
    c: Coincident(g6,g7)
    c: Coincident(g7,g8)
    c: Coincident(g8,g9)
    c: Coincident(g9,g10)
    c: Coincident(g10,g11)
    c: Coincident(g11,g12)
    c: Coincident(g12,g13)
    c: Coincident(g13,g14)
    c: Coincident(g14,g15)
    c: Coincident(g15,g16)
    c: Coincident(g16,g17)
    c: Coincident(g17,g18)
    c: Coincident(g18,g19)
    c: Coincident(g19,g20)
    c: Coincident(g20,g21)
    c: Coincident(g21,g22)
    c: Coincident(g22,g23)
    c: Coincident(g23,g0)
    c: Equal(g0, g1-g23) x23
    c: PointOnObject(g0,g24)
    c: PointOnObject(g1,g24)
    c: PointOnObject(g2,g24)
    c: PointOnObject(g3,g24)
    c: PointOnObject(g4,g24)
    c: PointOnObject(g5,g24)
    c: PointOnObject(g6,g24)
    c: PointOnObject(g7,g24)
    c: PointOnObject(g8,g24)
    c: PointOnObject(g9,g24)
    c: PointOnObject(g10,g24)
    c: PointOnObject(g11,g24)
    c: PointOnObject(g12,g24)
    c: PointOnObject(g13,g24)
    c: PointOnObject(g14,g24)
    c: PointOnObject(g15,g24)
    c: PointOnObject(g16,g24)
    c: PointOnObject(g17,g24)
    c: PointOnObject(g18,g24)
    c: PointOnObject(g19,g24)
    c: PointOnObject(g20,g24)
    c: PointOnObject(g21,g24)
    c: PointOnObject(g22,g24)
    c: PointOnObject(g23,g24)
    c: Coincident(g24,g-1)
    c: Horizontal(g23)
    c: DistanceX(g4,g17) = 12
FEATURE [Sketcher::SketchObject] Sketch062
  AttachmentOffset = pos=(0,0,17) rot=(0,0,1;0rad)
  FullyConstrained = false
  MapMode = 5
  Placement = pos=(0,0,17) rot=(0,0,1;0rad)
  Support = -> [XY_Plane023]
  sketch-geometry (25):
    g0: LineSegment StartX=-4.65926 StartY=1.92993 StartZ=0 EndX=-5 EndY=0.658262 EndZ=0
    g1: LineSegment StartX=-5 StartY=0.658262 StartZ=0 EndX=-5 EndY=-0.658262 EndZ=0
    g2: LineSegment StartX=-5 StartY=-0.658262 StartZ=0 EndX=-4.65926 EndY=-1.92993 EndZ=0
    g3: LineSegment StartX=-4.65926 StartY=-1.92993 StartZ=0 EndX=-4.001 EndY=-3.07007 EndZ=0
    g4: LineSegment StartX=-4.001 StartY=-3.07007 StartZ=0 EndX=-3.07007 EndY=-4.001 EndZ=0
    g5: LineSegment StartX=-3.07007 StartY=-4.001 StartZ=0 EndX=-1.92993 EndY=-4.65926 EndZ=0
    g6: LineSegment StartX=-1.92993 StartY=-4.65926 StartZ=0 EndX=-0.658262 EndY=-5 EndZ=0
    g7: LineSegment StartX=-0.658262 StartY=-5 StartZ=0 EndX=0.658262 EndY=-5 EndZ=0
    g8: LineSegment StartX=0.658262 StartY=-5 StartZ=0 EndX=1.92993 EndY=-4.65926 EndZ=0
    g9: LineSegment StartX=1.92993 StartY=-4.65926 StartZ=0 EndX=3.07007 EndY=-4.001 EndZ=0
    g10: LineSegment StartX=3.07007 StartY=-4.001 StartZ=0 EndX=4.001 EndY=-3.07007 EndZ=0
    g11: LineSegment StartX=4.001 StartY=-3.07007 StartZ=0 EndX=4.65926 EndY=-1.92993 EndZ=0
    g12: LineSegment StartX=4.65926 StartY=-1.92993 StartZ=0 EndX=5 EndY=-0.658262 EndZ=0
    g13: LineSegment StartX=5 StartY=-0.658262 StartZ=0 EndX=5 EndY=0.658262 EndZ=0
    g14: LineSegment StartX=5 StartY=0.658262 StartZ=0 EndX=4.65926 EndY=1.92993 EndZ=0
    g15: LineSegment StartX=4.65926 StartY=1.92993 StartZ=0 EndX=4.001 EndY=3.07007 EndZ=0
    g16: LineSegment StartX=4.001 StartY=3.07007 StartZ=0 EndX=3.07007 EndY=4.001 EndZ=0
    g17: LineSegment StartX=3.07007 StartY=4.001 StartZ=0 EndX=1.92993 EndY=4.65926 EndZ=0
    g18: LineSegment StartX=1.92993 StartY=4.65926 StartZ=0 EndX=0.658262 EndY=5 EndZ=0
    g19: LineSegment StartX=0.658262 StartY=5 StartZ=0 EndX=-0.658262 EndY=5 EndZ=0
    g20: LineSegment StartX=-0.658262 StartY=5 StartZ=0 EndX=-1.92993 EndY=4.65926 EndZ=0
    g21: LineSegment StartX=-1.92993 StartY=4.65926 StartZ=0 EndX=-3.07007 EndY=4.001 EndZ=0
    g22: LineSegment StartX=-3.07007 StartY=4.001 StartZ=0 EndX=-4.001 EndY=3.07007 EndZ=0
    g23: LineSegment StartX=-4.001 StartY=3.07007 StartZ=0 EndX=-4.65926 EndY=1.92993 EndZ=0
    g24: Circle CenterX=0 CenterY=0 CenterZ=0 NormalX=0 NormalY=0 NormalZ=1 AngleXU=0 Radius=5.04314
  constraints (52):
    c: Coincident(g0,g1)
    c: Coincident(g1,g2)
    c: Coincident(g2,g3)
    c: Coincident(g3,g4)
    c: Coincident(g4,g5)
    c: Coincident(g5,g6)
    c: Coincident(g6,g7)
    c: Coincident(g7,g8)
    c: Coincident(g8,g9)
    c: Coincident(g9,g10)
    c: Coincident(g10,g11)
    c: Coincident(g11,g12)
    c: Coincident(g12,g13)
    c: Coincident(g13,g14)
    c: Coincident(g14,g15)
    c: Coincident(g15,g16)
    c: Coincident(g16,g17)
    c: Coincident(g17,g18)
    c: Coincident(g18,g19)
    c: Coincident(g19,g20)
    c: Coincident(g20,g21)
    c: Coincident(g21,g22)
    c: Coincident(g22,g23)
    c: Coincident(g23,g0)
    c: Equal(g0, g1-g23) x23
    c: PointOnObject(g0,g24)
    c: PointOnObject(g1,g24)
    c: PointOnObject(g2,g24)
    c: PointOnObject(g3,g24)
    c: PointOnObject(g4,g24)
    c: PointOnObject(g5,g24)
    c: PointOnObject(g6,g24)
    c: PointOnObject(g7,g24)
    c: PointOnObject(g8,g24)
    c: PointOnObject(g9,g24)
    c: PointOnObject(g10,g24)
    c: PointOnObject(g11,g24)
    c: PointOnObject(g12,g24)
    c: PointOnObject(g13,g24)
    c: PointOnObject(g14,g24)
    c: PointOnObject(g15,g24)
    c: PointOnObject(g16,g24)
    c: PointOnObject(g17,g24)
    c: PointOnObject(g18,g24)
    c: PointOnObject(g19,g24)
    c: PointOnObject(g20,g24)
    c: PointOnObject(g21,g24)
    c: PointOnObject(g22,g24)
    c: PointOnObject(g23,g24)
    c: Coincident(g24,g-1)
    c: Horizontal(g19)
    c: DistanceX(g0,g13) = 10
FEATURE [PartDesign::AdditiveLoft] AdditiveLoft007
  AllowMultiFace = false
  Closed = false
  Profile = -> Sketch061
  Refine = true
  Ruled = false
  Sections = -> [Sketch060,Sketch062]
FEATURE [Sketcher::SketchObject] Sketch059
  FullyConstrained = false
  MapMode = 5
  Placement = pos=(0,0,17) rot=(0,0,1;0rad)
  Support = -> [AdditiveLoft007]
  sketch-geometry (1):
    g0: Circle CenterX=0 CenterY=0 CenterZ=0 NormalX=0 NormalY=0 NormalZ=1 AngleXU=0 Radius=4.5
  constraints (2):
    c: Coincident(g0,g-1)
    c: Radius(g0) = 4.5
FEATURE [PartDesign::Pad] Pad014
  AllowMultiFace = false
  BaseFeature = -> AdditiveLoft007
  Direction = (1,1,1)
  Length = 0.7
  Length2 = 100
  Profile = -> Sketch059
  Refine = true
  Type = 0
FEATURE [Sketcher::SketchObject] Sketch058
  FullyConstrained = false
  MapMode = 5
  Placement = pos=(0,0,0) rot=(1,0,0;3.14159rad)
  Support = -> [Pad014]
  sketch-geometry (1):
    g0: Circle CenterX=0 CenterY=0 CenterZ=0 NormalX=0 NormalY=0 NormalZ=1 AngleXU=0 Radius=5
  constraints (2):
    c: Coincident(g0,g-1)
    c: Radius(g0) = 5
FEATURE [PartDesign::Pocket] Pocket022
  AllowMultiFace = false
  BaseFeature = -> Pad014
  Direction = (1,1,1)
  Length = 1
  Length2 = 100
  Profile = -> Sketch058
  Refine = true
  Type = 0
FEATURE [Sketcher::SketchObject] Sketch056
  FullyConstrained = false
  MapMode = 5
  Placement = pos=(0,0,1) rot=(1,0,0;3.14159rad)
  Support = -> [Pocket022]
  sketch-geometry (1):
    g0: Circle CenterX=0 CenterY=0 CenterZ=0 NormalX=0 NormalY=0 NormalZ=1 AngleXU=0 Radius=4.65
  constraints (2):
    c: Coincident(g0,g-1)
    c: Radius(g0) = 4.65
FEATURE [PartDesign::Pocket] Pocket021
  AllowMultiFace = false
  BaseFeature = -> Pocket022
  Direction = (1,1,1)
  Length = 1
  Length2 = 100
  Profile = -> Sketch056
  Refine = true
  Type = 0
FEATURE [Sketcher::SketchObject] Sketch057
  FullyConstrained = false
  MapMode = 5
  Placement = pos=(0,0,2) rot=(1,0,0;3.14159rad)
  Support = -> [Pocket021]
  sketch-geometry (2):
    g0: ArcOfCircle CenterX=0 CenterY=0 CenterZ=0 NormalX=0 NormalY=0 NormalZ=1 AngleXU=0 Radius=3 StartAngle=2.19024 EndAngle=7.23453
    g1: LineSegment StartX=-1.74176 StartY=2.4426 StartZ=0 EndX=1.74176 EndY=2.4426 EndZ=0
  constraints (5):
    c: Coincident(g0,g-1)
    c: Coincident(g1,g0)
    c: Coincident(g1,g0)
    c: Horizontal(g1)
    c: Radius(g0) = 3
FEATURE [PartDesign::Pocket] Pocket023
  AllowMultiFace = false
  BaseFeature = -> Pocket021
  Direction = (1,1,1)
  Length = 8
  Length2 = 100
  Profile = -> Sketch057
  Refine = true
  Type = 0
FEATURE [PartDesign::Chamfer] Chamfer013
  Angle = 45
  Base = -> Pocket023 [Edge82,Edge83]
  BaseFeature = -> Pocket023
  ChamferType = 0
  FlipDirection = false
  Size = 1.4
  Size2 = 1
  SupportTransform = false
  UseAllEdges = false
FEATURE [PartDesign::Chamfer] Chamfer015
  Angle = 45
  Base = -> Chamfer013 [Edge8]
  BaseFeature = -> Chamfer013
  ChamferType = 0
  FlipDirection = false
  Size = 0.3
  Size2 = 1
  SupportTransform = false
  UseAllEdges = false
FEATURE [PartDesign::Fillet] Fillet006
  Base = -> Chamfer015 [Edge93,Face36]
  BaseFeature = -> Chamfer015
  Radius = 0.1
  SupportTransform = false
  UseAllEdges = false
FEATURE [PartDesign::Body] Body014
  Group = -> [Sketch061,Sketch060,Sketch062,AdditiveLoft007,Sketch059,Pad014,Sketch058,Pocket022,Sketch056,Pocket021,Sketch057,Pocket023,Chamfer013,Chamfer015,Fillet006]
  Origin = -> Origin021
  Tip = -> Fillet006
FEATURE [Sketcher::SketchObject] Sketch063
  AttachmentOffset = pos=(0,0,17.7) rot=(0,0,1;0rad)
  FullyConstrained = false
  MapMode = 5
  Placement = pos=(0,0,17.7) rot=(0,0,1;0rad)
  Support = -> [XY_Plane024]
  sketch-geometry (10):
    g0: LineSegment StartX=-0.2 StartY=1.5 StartZ=0 EndX=0.2 EndY=1.5 EndZ=0
    g1: LineSegment StartX=0.4 StartY=1.7 StartZ=0 EndX=0.4 EndY=4.2 EndZ=0
    g2: LineSegment StartX=0.2 StartY=4.4 StartZ=0 EndX=-0.2 EndY=4.4 EndZ=0
    g3: LineSegment StartX=-0.4 StartY=4.2 StartZ=0 EndX=-0.4 EndY=1.7 EndZ=0
    g4: ArcOfCircle CenterX=-0.2 CenterY=1.7 CenterZ=0 NormalX=0 NormalY=0 NormalZ=1 AngleXU=0 Radius=0.2 StartAngle=3.14159 EndAngle=4.71239
    g5: ArcOfCircle CenterX=0.2 CenterY=1.7 CenterZ=0 NormalX=0 NormalY=0 NormalZ=1 AngleXU=0 Radius=0.2 StartAngle=4.71239 EndAngle=6.28319
    g6: ArcOfCircle CenterX=0.2 CenterY=4.2 CenterZ=0 NormalX=0 NormalY=0 NormalZ=1 AngleXU=0 Radius=0.2 StartAngle=1.4e-15 EndAngle=1.5708
    g7: ArcOfCircle CenterX=-0.2 CenterY=4.2 CenterZ=0 NormalX=0 NormalY=0 NormalZ=1 AngleXU=0 Radius=0.2 StartAngle=1.5708 EndAngle=3.14159
    g8: LineSegment StartX=-0.2 StartY=1.7 StartZ=0 EndX=0 EndY=0 EndZ=0
    g9: LineSegment StartX=0 StartY=0 StartZ=0 EndX=0.2 EndY=1.7 EndZ=0
  constraints (24):
    c: Horizontal(g0)
    c: Horizontal(g2)
    c: Vertical(g1)
    c: Vertical(g3)
    c: Tangent(g3,g4) = -1.5708
    c: Tangent(g0,g4) = -1.5708
    c: Tangent(g0,g5) = -1.5708
    c: Tangent(g1,g5) = -1.5708
    c: Tangent(g1,g6) = -1.5708
    c: Tangent(g2,g6) = -1.5708
    c: Tangent(g2,g7) = -1.5708
    c: Tangent(g3,g7) = -1.5708
    c: Radius(g7) = 0.2
    c: Equal(g7,g6)
    c: Equal(g7,g5)
    c: Equal(g7,g4)
    c: Coincident(g8,g4)
    c: Coincident(g8,g-1)
    c: Coincident(g9,g-1)
    c: Coincident(g9,g5)
    c: Equal(g9,g8)
    c: DistanceX(g3,g1) = 0.8
    c: DistanceY(g-1,g2) = 4.4
    c: DistanceY(g-1,g0) = 1.5
FEATURE [PartDesign::Pad] Pad015
  AllowMultiFace = false
  Direction = (1,1,1)
  Length = 0.02
  Length2 = 100
  Profile = -> Sketch063
  Refine = true
  Type = 0
FEATURE [PartDesign::Body] Body015  label="Indicator007"
  Group = -> [Sketch063,Pad015]
  Origin = -> Origin019
  Tip = -> Pad015
FEATURE [App::Part] Part004  label="Cap005"
  Group = -> [Body014,Body015]
  Origin = -> Origin020
  Placement = pos=(40.005,13.335,0) rot=(0,0,1;0rad)
  expr: .Placement.Base.x = 40.005
  expr: .Placement.Base.y = 13.335
FEATURE [Sketcher::SketchObject] Sketch068
  AttachmentOffset = pos=(0,0,7) rot=(0,0,1;0rad)
  FullyConstrained = false
  MapMode = 5
  Placement = pos=(0,0,7) rot=(0,0,1;0rad)
  Support = -> [XY_Plane026]
  sketch-geometry (25):
    g0: LineSegment StartX=-0.724089 StartY=5.5 StartZ=0 EndX=-2.12292 EndY=5.12518 EndZ=0
    g1: LineSegment StartX=-2.12292 StartY=5.12518 StartZ=0 EndX=-3.37708 EndY=4.4011 EndZ=0
    g2: LineSegment StartX=-3.37708 StartY=4.4011 StartZ=0 EndX=-4.4011 EndY=3.37708 EndZ=0
    g3: LineSegment StartX=-4.4011 StartY=3.37708 StartZ=0 EndX=-5.12518 EndY=2.12292 EndZ=0
    g4: LineSegment StartX=-5.12518 StartY=2.12292 StartZ=0 EndX=-5.5 EndY=0.724089 EndZ=0
    g5: LineSegment StartX=-5.5 StartY=0.724089 StartZ=0 EndX=-5.5 EndY=-0.724089 EndZ=0
    g6: LineSegment StartX=-5.5 StartY=-0.724089 StartZ=0 EndX=-5.12518 EndY=-2.12292 EndZ=0
    g7: LineSegment StartX=-5.12518 StartY=-2.12292 StartZ=0 EndX=-4.4011 EndY=-3.37708 EndZ=0
    g8: LineSegment StartX=-4.4011 StartY=-3.37708 StartZ=0 EndX=-3.37708 EndY=-4.4011 EndZ=0
    g9: LineSegment StartX=-3.37708 StartY=-4.4011 StartZ=0 EndX=-2.12292 EndY=-5.12518 EndZ=0
    g10: LineSegment StartX=-2.12292 StartY=-5.12518 StartZ=0 EndX=-0.724089 EndY=-5.5 EndZ=0
    g11: LineSegment StartX=-0.724089 StartY=-5.5 StartZ=0 EndX=0.724089 EndY=-5.5 EndZ=0
    g12: LineSegment StartX=0.724089 StartY=-5.5 StartZ=0 EndX=2.12292 EndY=-5.12518 EndZ=0
    g13: LineSegment StartX=2.12292 StartY=-5.12518 StartZ=0 EndX=3.37708 EndY=-4.4011 EndZ=0
    g14: LineSegment StartX=3.37708 StartY=-4.4011 StartZ=0 EndX=4.4011 EndY=-3.37708 EndZ=0
    g15: LineSegment StartX=4.4011 StartY=-3.37708 StartZ=0 EndX=5.12518 EndY=-2.12292 EndZ=0
    g16: LineSegment StartX=5.12518 StartY=-2.12292 StartZ=0 EndX=5.5 EndY=-0.724089 EndZ=0
    g17: LineSegment StartX=5.5 StartY=-0.724089 StartZ=0 EndX=5.5 EndY=0.724089 EndZ=0
    g18: LineSegment StartX=5.5 StartY=0.724089 StartZ=0 EndX=5.12518 EndY=2.12292 EndZ=0
    g19: LineSegment StartX=5.12518 StartY=2.12292 StartZ=0 EndX=4.4011 EndY=3.37708 EndZ=0
    g20: LineSegment StartX=4.4011 StartY=3.37708 StartZ=0 EndX=3.37708 EndY=4.4011 EndZ=0
    g21: LineSegment StartX=3.37708 StartY=4.4011 StartZ=0 EndX=2.12292 EndY=5.12518 EndZ=0
    g22: LineSegment StartX=2.12292 StartY=5.12518 StartZ=0 EndX=0.724089 EndY=5.5 EndZ=0
    g23: LineSegment StartX=0.724089 StartY=5.5 StartZ=0 EndX=-0.724089 EndY=5.5 EndZ=0
    g24: Circle CenterX=0 CenterY=0 CenterZ=0 NormalX=0 NormalY=0 NormalZ=1 AngleXU=0 Radius=5.54746
  constraints (52):
    c: Coincident(g0,g1)
    c: Coincident(g1,g2)
    c: Coincident(g2,g3)
    c: Coincident(g3,g4)
    c: Coincident(g4,g5)
    c: Coincident(g5,g6)
    c: Coincident(g6,g7)
    c: Coincident(g7,g8)
    c: Coincident(g8,g9)
    c: Coincident(g9,g10)
    c: Coincident(g10,g11)
    c: Coincident(g11,g12)
    c: Coincident(g12,g13)
    c: Coincident(g13,g14)
    c: Coincident(g14,g15)
    c: Coincident(g15,g16)
    c: Coincident(g16,g17)
    c: Coincident(g17,g18)
    c: Coincident(g18,g19)
    c: Coincident(g19,g20)
    c: Coincident(g20,g21)
    c: Coincident(g21,g22)
    c: Coincident(g22,g23)
    c: Coincident(g23,g0)
    c: Equal(g0, g1-g23) x23
    c: PointOnObject(g0,g24)
    c: PointOnObject(g1,g24)
    c: PointOnObject(g2,g24)
    c: PointOnObject(g3,g24)
    c: PointOnObject(g4,g24)
    c: PointOnObject(g5,g24)
    c: PointOnObject(g6,g24)
    c: PointOnObject(g7,g24)
    c: PointOnObject(g8,g24)
    c: PointOnObject(g9,g24)
    c: PointOnObject(g10,g24)
    c: PointOnObject(g11,g24)
    c: PointOnObject(g12,g24)
    c: PointOnObject(g13,g24)
    c: PointOnObject(g14,g24)
    c: PointOnObject(g15,g24)
    c: PointOnObject(g16,g24)
    c: PointOnObject(g17,g24)
    c: PointOnObject(g18,g24)
    c: PointOnObject(g19,g24)
    c: PointOnObject(g20,g24)
    c: PointOnObject(g21,g24)
    c: PointOnObject(g22,g24)
    c: PointOnObject(g23,g24)
    c: Coincident(g24,g-1)
    c: Horizontal(g23)
    c: DistanceX(g4,g17) = 11
FEATURE [Sketcher::SketchObject] Sketch073
  FullyConstrained = false
  MapMode = 5
  Support = -> [XY_Plane026]
  sketch-geometry (25):
    g0: LineSegment StartX=-0.789915 StartY=6 StartZ=0 EndX=-2.31591 EndY=5.59111 EndZ=0
    g1: LineSegment StartX=-2.31591 StartY=5.59111 StartZ=0 EndX=-3.68409 EndY=4.80119 EndZ=0
    g2: LineSegment StartX=-3.68409 StartY=4.80119 StartZ=0 EndX=-4.80119 EndY=3.68409 EndZ=0
    g3: LineSegment StartX=-4.80119 StartY=3.68409 StartZ=0 EndX=-5.59111 EndY=2.31591 EndZ=0
    g4: LineSegment StartX=-5.59111 StartY=2.31591 StartZ=0 EndX=-6 EndY=0.789915 EndZ=0
    g5: LineSegment StartX=-6 StartY=0.789915 StartZ=0 EndX=-6 EndY=-0.789915 EndZ=0
    g6: LineSegment StartX=-6 StartY=-0.789915 StartZ=0 EndX=-5.59111 EndY=-2.31591 EndZ=0
    g7: LineSegment StartX=-5.59111 StartY=-2.31591 StartZ=0 EndX=-4.80119 EndY=-3.68409 EndZ=0
    g8: LineSegment StartX=-4.80119 StartY=-3.68409 StartZ=0 EndX=-3.68409 EndY=-4.80119 EndZ=0
    g9: LineSegment StartX=-3.68409 StartY=-4.80119 StartZ=0 EndX=-2.31591 EndY=-5.59111 EndZ=0
    g10: LineSegment StartX=-2.31591 StartY=-5.59111 StartZ=0 EndX=-0.789915 EndY=-6 EndZ=0
    g11: LineSegment StartX=-0.789915 StartY=-6 StartZ=0 EndX=0.789915 EndY=-6 EndZ=0
    g12: LineSegment StartX=0.789915 StartY=-6 StartZ=0 EndX=2.31591 EndY=-5.59111 EndZ=0
    g13: LineSegment StartX=2.31591 StartY=-5.59111 StartZ=0 EndX=3.68409 EndY=-4.80119 EndZ=0
    g14: LineSegment StartX=3.68409 StartY=-4.80119 StartZ=0 EndX=4.80119 EndY=-3.68409 EndZ=0
    g15: LineSegment StartX=4.80119 StartY=-3.68409 StartZ=0 EndX=5.59111 EndY=-2.31591 EndZ=0
    g16: LineSegment StartX=5.59111 StartY=-2.31591 StartZ=0 EndX=6 EndY=-0.789915 EndZ=0
    g17: LineSegment StartX=6 StartY=-0.789915 StartZ=0 EndX=6 EndY=0.789915 EndZ=0
    g18: LineSegment StartX=6 StartY=0.789915 StartZ=0 EndX=5.59111 EndY=2.31591 EndZ=0
    g19: LineSegment StartX=5.59111 StartY=2.31591 StartZ=0 EndX=4.80119 EndY=3.68409 EndZ=0
    g20: LineSegment StartX=4.80119 StartY=3.68409 StartZ=0 EndX=3.68409 EndY=4.80119 EndZ=0
    g21: LineSegment StartX=3.68409 StartY=4.80119 StartZ=0 EndX=2.31591 EndY=5.59111 EndZ=0
    g22: LineSegment StartX=2.31591 StartY=5.59111 StartZ=0 EndX=0.789915 EndY=6 EndZ=0
    g23: LineSegment StartX=0.789915 StartY=6 StartZ=0 EndX=-0.789915 EndY=6 EndZ=0
    g24: Circle CenterX=0 CenterY=0 CenterZ=0 NormalX=0 NormalY=0 NormalZ=1 AngleXU=0 Radius=6.05177
  constraints (52):
    c: Coincident(g0,g1)
    c: Coincident(g1,g2)
    c: Coincident(g2,g3)
    c: Coincident(g3,g4)
    c: Coincident(g4,g5)
    c: Coincident(g5,g6)
    c: Coincident(g6,g7)
    c: Coincident(g7,g8)
    c: Coincident(g8,g9)
    c: Coincident(g9,g10)
    c: Coincident(g10,g11)
    c: Coincident(g11,g12)
    c: Coincident(g12,g13)
    c: Coincident(g13,g14)
    c: Coincident(g14,g15)
    c: Coincident(g15,g16)
    c: Coincident(g16,g17)
    c: Coincident(g17,g18)
    c: Coincident(g18,g19)
    c: Coincident(g19,g20)
    c: Coincident(g20,g21)
    c: Coincident(g21,g22)
    c: Coincident(g22,g23)
    c: Coincident(g23,g0)
    c: Equal(g0, g1-g23) x23
    c: PointOnObject(g0,g24)
    c: PointOnObject(g1,g24)
    c: PointOnObject(g2,g24)
    c: PointOnObject(g3,g24)
    c: PointOnObject(g4,g24)
    c: PointOnObject(g5,g24)
    c: PointOnObject(g6,g24)
    c: PointOnObject(g7,g24)
    c: PointOnObject(g8,g24)
    c: PointOnObject(g9,g24)
    c: PointOnObject(g10,g24)
    c: PointOnObject(g11,g24)
    c: PointOnObject(g12,g24)
    c: PointOnObject(g13,g24)
    c: PointOnObject(g14,g24)
    c: PointOnObject(g15,g24)
    c: PointOnObject(g16,g24)
    c: PointOnObject(g17,g24)
    c: PointOnObject(g18,g24)
    c: PointOnObject(g19,g24)
    c: PointOnObject(g20,g24)
    c: PointOnObject(g21,g24)
    c: PointOnObject(g22,g24)
    c: PointOnObject(g23,g24)
    c: Coincident(g24,g-1)
    c: Horizontal(g23)
    c: DistanceX(g4,g17) = 12
FEATURE [Sketcher::SketchObject] Sketch074
  AttachmentOffset = pos=(0,0,17) rot=(0,0,1;0rad)
  FullyConstrained = false
  MapMode = 5
  Placement = pos=(0,0,17) rot=(0,0,1;0rad)
  Support = -> [XY_Plane026]
  sketch-geometry (25):
    g0: LineSegment StartX=-4.65926 StartY=1.92993 StartZ=0 EndX=-5 EndY=0.658262 EndZ=0
    g1: LineSegment StartX=-5 StartY=0.658262 StartZ=0 EndX=-5 EndY=-0.658262 EndZ=0
    g2: LineSegment StartX=-5 StartY=-0.658262 StartZ=0 EndX=-4.65926 EndY=-1.92993 EndZ=0
    g3: LineSegment StartX=-4.65926 StartY=-1.92993 StartZ=0 EndX=-4.001 EndY=-3.07007 EndZ=0
    g4: LineSegment StartX=-4.001 StartY=-3.07007 StartZ=0 EndX=-3.07007 EndY=-4.001 EndZ=0
    g5: LineSegment StartX=-3.07007 StartY=-4.001 StartZ=0 EndX=-1.92993 EndY=-4.65926 EndZ=0
    g6: LineSegment StartX=-1.92993 StartY=-4.65926 StartZ=0 EndX=-0.658262 EndY=-5 EndZ=0
    g7: LineSegment StartX=-0.658262 StartY=-5 StartZ=0 EndX=0.658262 EndY=-5 EndZ=0
    g8: LineSegment StartX=0.658262 StartY=-5 StartZ=0 EndX=1.92993 EndY=-4.65926 EndZ=0
    g9: LineSegment StartX=1.92993 StartY=-4.65926 StartZ=0 EndX=3.07007 EndY=-4.001 EndZ=0
    g10: LineSegment StartX=3.07007 StartY=-4.001 StartZ=0 EndX=4.001 EndY=-3.07007 EndZ=0
    g11: LineSegment StartX=4.001 StartY=-3.07007 StartZ=0 EndX=4.65926 EndY=-1.92993 EndZ=0
    g12: LineSegment StartX=4.65926 StartY=-1.92993 StartZ=0 EndX=5 EndY=-0.658262 EndZ=0
    g13: LineSegment StartX=5 StartY=-0.658262 StartZ=0 EndX=5 EndY=0.658262 EndZ=0
    g14: LineSegment StartX=5 StartY=0.658262 StartZ=0 EndX=4.65926 EndY=1.92993 EndZ=0
    g15: LineSegment StartX=4.65926 StartY=1.92993 StartZ=0 EndX=4.001 EndY=3.07007 EndZ=0
    g16: LineSegment StartX=4.001 StartY=3.07007 StartZ=0 EndX=3.07007 EndY=4.001 EndZ=0
    g17: LineSegment StartX=3.07007 StartY=4.001 StartZ=0 EndX=1.92993 EndY=4.65926 EndZ=0
    g18: LineSegment StartX=1.92993 StartY=4.65926 StartZ=0 EndX=0.658262 EndY=5 EndZ=0
    g19: LineSegment StartX=0.658262 StartY=5 StartZ=0 EndX=-0.658262 EndY=5 EndZ=0
    g20: LineSegment StartX=-0.658262 StartY=5 StartZ=0 EndX=-1.92993 EndY=4.65926 EndZ=0
    g21: LineSegment StartX=-1.92993 StartY=4.65926 StartZ=0 EndX=-3.07007 EndY=4.001 EndZ=0
    g22: LineSegment StartX=-3.07007 StartY=4.001 StartZ=0 EndX=-4.001 EndY=3.07007 EndZ=0
    g23: LineSegment StartX=-4.001 StartY=3.07007 StartZ=0 EndX=-4.65926 EndY=1.92993 EndZ=0
    g24: Circle CenterX=0 CenterY=0 CenterZ=0 NormalX=0 NormalY=0 NormalZ=1 AngleXU=0 Radius=5.04314
  constraints (52):
    c: Coincident(g0,g1)
    c: Coincident(g1,g2)
    c: Coincident(g2,g3)
    c: Coincident(g3,g4)
    c: Coincident(g4,g5)
    c: Coincident(g5,g6)
    c: Coincident(g6,g7)
    c: Coincident(g7,g8)
    c: Coincident(g8,g9)
    c: Coincident(g9,g10)
    c: Coincident(g10,g11)
    c: Coincident(g11,g12)
    c: Coincident(g12,g13)
    c: Coincident(g13,g14)
    c: Coincident(g14,g15)
    c: Coincident(g15,g16)
    c: Coincident(g16,g17)
    c: Coincident(g17,g18)
    c: Coincident(g18,g19)
    c: Coincident(g19,g20)
    c: Coincident(g20,g21)
    c: Coincident(g21,g22)
    c: Coincident(g22,g23)
    c: Coincident(g23,g0)
    c: Equal(g0, g1-g23) x23
    c: PointOnObject(g0,g24)
    c: PointOnObject(g1,g24)
    c: PointOnObject(g2,g24)
    c: PointOnObject(g3,g24)
    c: PointOnObject(g4,g24)
    c: PointOnObject(g5,g24)
    c: PointOnObject(g6,g24)
    c: PointOnObject(g7,g24)
    c: PointOnObject(g8,g24)
    c: PointOnObject(g9,g24)
    c: PointOnObject(g10,g24)
    c: PointOnObject(g11,g24)
    c: PointOnObject(g12,g24)
    c: PointOnObject(g13,g24)
    c: PointOnObject(g14,g24)
    c: PointOnObject(g15,g24)
    c: PointOnObject(g16,g24)
    c: PointOnObject(g17,g24)
    c: PointOnObject(g18,g24)
    c: PointOnObject(g19,g24)
    c: PointOnObject(g20,g24)
    c: PointOnObject(g21,g24)
    c: PointOnObject(g22,g24)
    c: PointOnObject(g23,g24)
    c: Coincident(g24,g-1)
    c: Horizontal(g19)
    c: DistanceX(g0,g13) = 10
FEATURE [PartDesign::AdditiveLoft] AdditiveLoft014
  AllowMultiFace = false
  Closed = false
  Profile = -> Sketch073
  Refine = true
  Ruled = false
  Sections = -> [Sketch068,Sketch074]
FEATURE [Sketcher::SketchObject] Sketch067
  FullyConstrained = false
  MapMode = 5
  Placement = pos=(0,0,17) rot=(0,0,1;0rad)
  Support = -> [AdditiveLoft014]
  sketch-geometry (1):
    g0: Circle CenterX=0 CenterY=0 CenterZ=0 NormalX=0 NormalY=0 NormalZ=1 AngleXU=0 Radius=4.5
  constraints (2):
    c: Coincident(g0,g-1)
    c: Radius(g0) = 4.5
FEATURE [PartDesign::Pad] Pad016
  AllowMultiFace = false
  BaseFeature = -> AdditiveLoft014
  Direction = (1,1,1)
  Length = 0.7
  Length2 = 100
  Profile = -> Sketch067
  Refine = true
  Type = 0
FEATURE [Sketcher::SketchObject] Sketch066
  FullyConstrained = false
  MapMode = 5
  Placement = pos=(0,0,0) rot=(1,0,0;3.14159rad)
  Support = -> [Pad016]
  sketch-geometry (1):
    g0: Circle CenterX=0 CenterY=0 CenterZ=0 NormalX=0 NormalY=0 NormalZ=1 AngleXU=0 Radius=5
  constraints (2):
    c: Coincident(g0,g-1)
    c: Radius(g0) = 5
FEATURE [PartDesign::Pocket] Pocket025
  AllowMultiFace = false
  BaseFeature = -> Pad016
  Direction = (1,1,1)
  Length = 1
  Length2 = 100
  Profile = -> Sketch066
  Refine = true
  Type = 0
FEATURE [Sketcher::SketchObject] Sketch064
  FullyConstrained = false
  MapMode = 5
  Placement = pos=(0,0,1) rot=(1,0,0;3.14159rad)
  Support = -> [Pocket025]
  sketch-geometry (1):
    g0: Circle CenterX=0 CenterY=0 CenterZ=0 NormalX=0 NormalY=0 NormalZ=1 AngleXU=0 Radius=4.65
  constraints (2):
    c: Coincident(g0,g-1)
    c: Radius(g0) = 4.65
FEATURE [PartDesign::Pocket] Pocket024
  AllowMultiFace = false
  BaseFeature = -> Pocket025
  Direction = (1,1,1)
  Length = 1
  Length2 = 100
  Profile = -> Sketch064
  Refine = true
  Type = 0
FEATURE [Sketcher::SketchObject] Sketch065
  FullyConstrained = false
  MapMode = 5
  Placement = pos=(0,0,2) rot=(1,0,0;3.14159rad)
  Support = -> [Pocket024]
  sketch-geometry (2):
    g0: ArcOfCircle CenterX=0 CenterY=0 CenterZ=0 NormalX=0 NormalY=0 NormalZ=1 AngleXU=0 Radius=3 StartAngle=2.19024 EndAngle=7.23453
    g1: LineSegment StartX=-1.74176 StartY=2.4426 StartZ=0 EndX=1.74176 EndY=2.4426 EndZ=0
  constraints (5):
    c: Coincident(g0,g-1)
    c: Coincident(g1,g0)
    c: Coincident(g1,g0)
    c: Horizontal(g1)
    c: Radius(g0) = 3
FEATURE [PartDesign::Pocket] Pocket026
  AllowMultiFace = false
  BaseFeature = -> Pocket024
  Direction = (1,1,1)
  Length = 8
  Length2 = 100
  Profile = -> Sketch065
  Refine = true
  Type = 0
FEATURE [PartDesign::Chamfer] Chamfer016
  Angle = 45
  Base = -> Pocket026 [Edge82,Edge83]
  BaseFeature = -> Pocket026
  ChamferType = 0
  FlipDirection = false
  Size = 1.4
  Size2 = 1
  SupportTransform = false
  UseAllEdges = false
FEATURE [PartDesign::Chamfer] Chamfer017
  Angle = 45
  Base = -> Chamfer016 [Edge8]
  BaseFeature = -> Chamfer016
  ChamferType = 0
  FlipDirection = false
  Size = 0.3
  Size2 = 1
  SupportTransform = false
  UseAllEdges = false
FEATURE [PartDesign::Fillet] Fillet008
  Base = -> Chamfer017 [Edge93,Face36]
  BaseFeature = -> Chamfer017
  Radius = 0.1
  SupportTransform = false
  UseAllEdges = false
FEATURE [PartDesign::Body] Body016
  Group = -> [Sketch073,Sketch068,Sketch074,AdditiveLoft014,Sketch067,Pad016,Sketch066,Pocket025,Sketch064,Pocket024,Sketch065,Pocket026,Chamfer016,Chamfer017,Fillet008]
  Origin = -> Origin046
  Tip = -> Fillet008
FEATURE [Sketcher::SketchObject] Sketch075
  AttachmentOffset = pos=(0,0,17.7) rot=(0,0,1;0rad)
  FullyConstrained = false
  MapMode = 5
  Placement = pos=(0,0,17.7) rot=(0,0,1;0rad)
  Support = -> [XY_Plane027]
  sketch-geometry (10):
    g0: LineSegment StartX=-0.2 StartY=1.5 StartZ=0 EndX=0.2 EndY=1.5 EndZ=0
    g1: LineSegment StartX=0.4 StartY=1.7 StartZ=0 EndX=0.4 EndY=4.2 EndZ=0
    g2: LineSegment StartX=0.2 StartY=4.4 StartZ=0 EndX=-0.2 EndY=4.4 EndZ=0
    g3: LineSegment StartX=-0.4 StartY=4.2 StartZ=0 EndX=-0.4 EndY=1.7 EndZ=0
    g4: ArcOfCircle CenterX=-0.2 CenterY=1.7 CenterZ=0 NormalX=0 NormalY=0 NormalZ=1 AngleXU=0 Radius=0.2 StartAngle=3.14159 EndAngle=4.71239
    g5: ArcOfCircle CenterX=0.2 CenterY=1.7 CenterZ=0 NormalX=0 NormalY=0 NormalZ=1 AngleXU=0 Radius=0.2 StartAngle=4.71239 EndAngle=6.28319
    g6: ArcOfCircle CenterX=0.2 CenterY=4.2 CenterZ=0 NormalX=0 NormalY=0 NormalZ=1 AngleXU=0 Radius=0.2 StartAngle=1.4e-15 EndAngle=1.5708
    g7: ArcOfCircle CenterX=-0.2 CenterY=4.2 CenterZ=0 NormalX=0 NormalY=0 NormalZ=1 AngleXU=0 Radius=0.2 StartAngle=1.5708 EndAngle=3.14159
    g8: LineSegment StartX=-0.2 StartY=1.7 StartZ=0 EndX=0 EndY=0 EndZ=0
    g9: LineSegment StartX=0 StartY=0 StartZ=0 EndX=0.2 EndY=1.7 EndZ=0
  constraints (24):
    c: Horizontal(g0)
    c: Horizontal(g2)
    c: Vertical(g1)
    c: Vertical(g3)
    c: Tangent(g3,g4) = -1.5708
    c: Tangent(g0,g4) = -1.5708
    c: Tangent(g0,g5) = -1.5708
    c: Tangent(g1,g5) = -1.5708
    c: Tangent(g1,g6) = -1.5708
    c: Tangent(g2,g6) = -1.5708
    c: Tangent(g2,g7) = -1.5708
    c: Tangent(g3,g7) = -1.5708
    c: Radius(g7) = 0.2
    c: Equal(g7,g6)
    c: Equal(g7,g5)
    c: Equal(g7,g4)
    c: Coincident(g8,g4)
    c: Coincident(g8,g-1)
    c: Coincident(g9,g-1)
    c: Coincident(g9,g5)
    c: Equal(g9,g8)
    c: DistanceX(g3,g1) = 0.8
    c: DistanceY(g-1,g2) = 4.4
    c: DistanceY(g-1,g0) = 1.5
FEATURE [PartDesign::Pad] Pad017
  AllowMultiFace = false
  Direction = (1,1,1)
  Length = 0.02
  Length2 = 100
  Profile = -> Sketch075
  Refine = true
  Type = 0
FEATURE [PartDesign::Body] Body017  label="Indicator008"
  Group = -> [Sketch075,Pad017]
  Origin = -> Origin047
  Tip = -> Pad017
FEATURE [App::Part] Part014  label="Cap015"
  Group = -> [Body016,Body017]
  Origin = -> Origin048
  Placement = pos=(-40.005,-40.005,0) rot=(0,0,1;0rad)
  expr: .Placement.Base.x = -40.005
  expr: .Placement.Base.y = -40.005
FEATURE [Sketcher::SketchObject] Sketch076
  AttachmentOffset = pos=(0,0,7) rot=(0,0,1;0rad)
  FullyConstrained = false
  MapMode = 5
  Placement = pos=(0,0,7) rot=(0,0,1;0rad)
  Support = -> [XY_Plane029]
  sketch-geometry (25):
    g0: LineSegment StartX=-0.724089 StartY=5.5 StartZ=0 EndX=-2.12292 EndY=5.12518 EndZ=0
    g1: LineSegment StartX=-2.12292 StartY=5.12518 StartZ=0 EndX=-3.37708 EndY=4.4011 EndZ=0
    g2: LineSegment StartX=-3.37708 StartY=4.4011 StartZ=0 EndX=-4.4011 EndY=3.37708 EndZ=0
    g3: LineSegment StartX=-4.4011 StartY=3.37708 StartZ=0 EndX=-5.12518 EndY=2.12292 EndZ=0
    g4: LineSegment StartX=-5.12518 StartY=2.12292 StartZ=0 EndX=-5.5 EndY=0.724089 EndZ=0
    g5: LineSegment StartX=-5.5 StartY=0.724089 StartZ=0 EndX=-5.5 EndY=-0.724089 EndZ=0
    g6: LineSegment StartX=-5.5 StartY=-0.724089 StartZ=0 EndX=-5.12518 EndY=-2.12292 EndZ=0
    g7: LineSegment StartX=-5.12518 StartY=-2.12292 StartZ=0 EndX=-4.4011 EndY=-3.37708 EndZ=0
    g8: LineSegment StartX=-4.4011 StartY=-3.37708 StartZ=0 EndX=-3.37708 EndY=-4.4011 EndZ=0
    g9: LineSegment StartX=-3.37708 StartY=-4.4011 StartZ=0 EndX=-2.12292 EndY=-5.12518 EndZ=0
    g10: LineSegment StartX=-2.12292 StartY=-5.12518 StartZ=0 EndX=-0.724089 EndY=-5.5 EndZ=0
    g11: LineSegment StartX=-0.724089 StartY=-5.5 StartZ=0 EndX=0.724089 EndY=-5.5 EndZ=0
    g12: LineSegment StartX=0.724089 StartY=-5.5 StartZ=0 EndX=2.12292 EndY=-5.12518 EndZ=0
    g13: LineSegment StartX=2.12292 StartY=-5.12518 StartZ=0 EndX=3.37708 EndY=-4.4011 EndZ=0
    g14: LineSegment StartX=3.37708 StartY=-4.4011 StartZ=0 EndX=4.4011 EndY=-3.37708 EndZ=0
    g15: LineSegment StartX=4.4011 StartY=-3.37708 StartZ=0 EndX=5.12518 EndY=-2.12292 EndZ=0
    g16: LineSegment StartX=5.12518 StartY=-2.12292 StartZ=0 EndX=5.5 EndY=-0.724089 EndZ=0
    g17: LineSegment StartX=5.5 StartY=-0.724089 StartZ=0 EndX=5.5 EndY=0.724089 EndZ=0
    g18: LineSegment StartX=5.5 StartY=0.724089 StartZ=0 EndX=5.12518 EndY=2.12292 EndZ=0
    g19: LineSegment StartX=5.12518 StartY=2.12292 StartZ=0 EndX=4.4011 EndY=3.37708 EndZ=0
    g20: LineSegment StartX=4.4011 StartY=3.37708 StartZ=0 EndX=3.37708 EndY=4.4011 EndZ=0
    g21: LineSegment StartX=3.37708 StartY=4.4011 StartZ=0 EndX=2.12292 EndY=5.12518 EndZ=0
    g22: LineSegment StartX=2.12292 StartY=5.12518 StartZ=0 EndX=0.724089 EndY=5.5 EndZ=0
    g23: LineSegment StartX=0.724089 StartY=5.5 StartZ=0 EndX=-0.724089 EndY=5.5 EndZ=0
    g24: Circle CenterX=0 CenterY=0 CenterZ=0 NormalX=0 NormalY=0 NormalZ=1 AngleXU=0 Radius=5.54746
  constraints (52):
    c: Coincident(g0,g1)
    c: Coincident(g1,g2)
    c: Coincident(g2,g3)
    c: Coincident(g3,g4)
    c: Coincident(g4,g5)
    c: Coincident(g5,g6)
    c: Coincident(g6,g7)
    c: Coincident(g7,g8)
    c: Coincident(g8,g9)
    c: Coincident(g9,g10)
    c: Coincident(g10,g11)
    c: Coincident(g11,g12)
    c: Coincident(g12,g13)
    c: Coincident(g13,g14)
    c: Coincident(g14,g15)
    c: Coincident(g15,g16)
    c: Coincident(g16,g17)
    c: Coincident(g17,g18)
    c: Coincident(g18,g19)
    c: Coincident(g19,g20)
    c: Coincident(g20,g21)
    c: Coincident(g21,g22)
    c: Coincident(g22,g23)
    c: Coincident(g23,g0)
    c: Equal(g0, g1-g23) x23
    c: PointOnObject(g0,g24)
    c: PointOnObject(g1,g24)
    c: PointOnObject(g2,g24)
    c: PointOnObject(g3,g24)
    c: PointOnObject(g4,g24)
    c: PointOnObject(g5,g24)
    c: PointOnObject(g6,g24)
    c: PointOnObject(g7,g24)
    c: PointOnObject(g8,g24)
    c: PointOnObject(g9,g24)
    c: PointOnObject(g10,g24)
    c: PointOnObject(g11,g24)
    c: PointOnObject(g12,g24)
    c: PointOnObject(g13,g24)
    c: PointOnObject(g14,g24)
    c: PointOnObject(g15,g24)
    c: PointOnObject(g16,g24)
    c: PointOnObject(g17,g24)
    c: PointOnObject(g18,g24)
    c: PointOnObject(g19,g24)
    c: PointOnObject(g20,g24)
    c: PointOnObject(g21,g24)
    c: PointOnObject(g22,g24)
    c: PointOnObject(g23,g24)
    c: Coincident(g24,g-1)
    c: Horizontal(g23)
    c: DistanceX(g4,g17) = 11
FEATURE [Sketcher::SketchObject] Sketch077
  FullyConstrained = false
  MapMode = 5
  Support = -> [XY_Plane029]
  sketch-geometry (25):
    g0: LineSegment StartX=-0.789915 StartY=6 StartZ=0 EndX=-2.31591 EndY=5.59111 EndZ=0
    g1: LineSegment StartX=-2.31591 StartY=5.59111 StartZ=0 EndX=-3.68409 EndY=4.80119 EndZ=0
    g2: LineSegment StartX=-3.68409 StartY=4.80119 StartZ=0 EndX=-4.80119 EndY=3.68409 EndZ=0
    g3: LineSegment StartX=-4.80119 StartY=3.68409 StartZ=0 EndX=-5.59111 EndY=2.31591 EndZ=0
    g4: LineSegment StartX=-5.59111 StartY=2.31591 StartZ=0 EndX=-6 EndY=0.789915 EndZ=0
    g5: LineSegment StartX=-6 StartY=0.789915 StartZ=0 EndX=-6 EndY=-0.789915 EndZ=0
    g6: LineSegment StartX=-6 StartY=-0.789915 StartZ=0 EndX=-5.59111 EndY=-2.31591 EndZ=0
    g7: LineSegment StartX=-5.59111 StartY=-2.31591 StartZ=0 EndX=-4.80119 EndY=-3.68409 EndZ=0
    g8: LineSegment StartX=-4.80119 StartY=-3.68409 StartZ=0 EndX=-3.68409 EndY=-4.80119 EndZ=0
    g9: LineSegment StartX=-3.68409 StartY=-4.80119 StartZ=0 EndX=-2.31591 EndY=-5.59111 EndZ=0
    g10: LineSegment StartX=-2.31591 StartY=-5.59111 StartZ=0 EndX=-0.789915 EndY=-6 EndZ=0
    g11: LineSegment StartX=-0.789915 StartY=-6 StartZ=0 EndX=0.789915 EndY=-6 EndZ=0
    g12: LineSegment StartX=0.789915 StartY=-6 StartZ=0 EndX=2.31591 EndY=-5.59111 EndZ=0
    g13: LineSegment StartX=2.31591 StartY=-5.59111 StartZ=0 EndX=3.68409 EndY=-4.80119 EndZ=0
    g14: LineSegment StartX=3.68409 StartY=-4.80119 StartZ=0 EndX=4.80119 EndY=-3.68409 EndZ=0
    g15: LineSegment StartX=4.80119 StartY=-3.68409 StartZ=0 EndX=5.59111 EndY=-2.31591 EndZ=0
    g16: LineSegment StartX=5.59111 StartY=-2.31591 StartZ=0 EndX=6 EndY=-0.789915 EndZ=0
    g17: LineSegment StartX=6 StartY=-0.789915 StartZ=0 EndX=6 EndY=0.789915 EndZ=0
    g18: LineSegment StartX=6 StartY=0.789915 StartZ=0 EndX=5.59111 EndY=2.31591 EndZ=0
    g19: LineSegment StartX=5.59111 StartY=2.31591 StartZ=0 EndX=4.80119 EndY=3.68409 EndZ=0
    g20: LineSegment StartX=4.80119 StartY=3.68409 StartZ=0 EndX=3.68409 EndY=4.80119 EndZ=0
    g21: LineSegment StartX=3.68409 StartY=4.80119 StartZ=0 EndX=2.31591 EndY=5.59111 EndZ=0
    g22: LineSegment StartX=2.31591 StartY=5.59111 StartZ=0 EndX=0.789915 EndY=6 EndZ=0
    g23: LineSegment StartX=0.789915 StartY=6 StartZ=0 EndX=-0.789915 EndY=6 EndZ=0
    g24: Circle CenterX=0 CenterY=0 CenterZ=0 NormalX=0 NormalY=0 NormalZ=1 AngleXU=0 Radius=6.05177
  constraints (52):
    c: Coincident(g0,g1)
    c: Coincident(g1,g2)
    c: Coincident(g2,g3)
    c: Coincident(g3,g4)
    c: Coincident(g4,g5)
    c: Coincident(g5,g6)
    c: Coincident(g6,g7)
    c: Coincident(g7,g8)
    c: Coincident(g8,g9)
    c: Coincident(g9,g10)
    c: Coincident(g10,g11)
    c: Coincident(g11,g12)
    c: Coincident(g12,g13)
    c: Coincident(g13,g14)
    c: Coincident(g14,g15)
    c: Coincident(g15,g16)
    c: Coincident(g16,g17)
    c: Coincident(g17,g18)
    c: Coincident(g18,g19)
    c: Coincident(g19,g20)
    c: Coincident(g20,g21)
    c: Coincident(g21,g22)
    c: Coincident(g22,g23)
    c: Coincident(g23,g0)
    c: Equal(g0, g1-g23) x23
    c: PointOnObject(g0,g24)
    c: PointOnObject(g1,g24)
    c: PointOnObject(g2,g24)
    c: PointOnObject(g3,g24)
    c: PointOnObject(g4,g24)
    c: PointOnObject(g5,g24)
    c: PointOnObject(g6,g24)
    c: PointOnObject(g7,g24)
    c: PointOnObject(g8,g24)
    c: PointOnObject(g9,g24)
    c: PointOnObject(g10,g24)
    c: PointOnObject(g11,g24)
    c: PointOnObject(g12,g24)
    c: PointOnObject(g13,g24)
    c: PointOnObject(g14,g24)
    c: PointOnObject(g15,g24)
    c: PointOnObject(g16,g24)
    c: PointOnObject(g17,g24)
    c: PointOnObject(g18,g24)
    c: PointOnObject(g19,g24)
    c: PointOnObject(g20,g24)
    c: PointOnObject(g21,g24)
    c: PointOnObject(g22,g24)
    c: PointOnObject(g23,g24)
    c: Coincident(g24,g-1)
    c: Horizontal(g23)
    c: DistanceX(g4,g17) = 12
FEATURE [Sketcher::SketchObject] Sketch078
  AttachmentOffset = pos=(0,0,17) rot=(0,0,1;0rad)
  FullyConstrained = false
  MapMode = 5
  Placement = pos=(0,0,17) rot=(0,0,1;0rad)
  Support = -> [XY_Plane029]
  sketch-geometry (25):
    g0: LineSegment StartX=-4.65926 StartY=1.92993 StartZ=0 EndX=-5 EndY=0.658262 EndZ=0
    g1: LineSegment StartX=-5 StartY=0.658262 StartZ=0 EndX=-5 EndY=-0.658262 EndZ=0
    g2: LineSegment StartX=-5 StartY=-0.658262 StartZ=0 EndX=-4.65926 EndY=-1.92993 EndZ=0
    g3: LineSegment StartX=-4.65926 StartY=-1.92993 StartZ=0 EndX=-4.001 EndY=-3.07007 EndZ=0
    g4: LineSegment StartX=-4.001 StartY=-3.07007 StartZ=0 EndX=-3.07007 EndY=-4.001 EndZ=0
    g5: LineSegment StartX=-3.07007 StartY=-4.001 StartZ=0 EndX=-1.92993 EndY=-4.65926 EndZ=0
    g6: LineSegment StartX=-1.92993 StartY=-4.65926 StartZ=0 EndX=-0.658262 EndY=-5 EndZ=0
    g7: LineSegment StartX=-0.658262 StartY=-5 StartZ=0 EndX=0.658262 EndY=-5 EndZ=0
    g8: LineSegment StartX=0.658262 StartY=-5 StartZ=0 EndX=1.92993 EndY=-4.65926 EndZ=0
    g9: LineSegment StartX=1.92993 StartY=-4.65926 StartZ=0 EndX=3.07007 EndY=-4.001 EndZ=0
    g10: LineSegment StartX=3.07007 StartY=-4.001 StartZ=0 EndX=4.001 EndY=-3.07007 EndZ=0
    g11: LineSegment StartX=4.001 StartY=-3.07007 StartZ=0 EndX=4.65926 EndY=-1.92993 EndZ=0
    g12: LineSegment StartX=4.65926 StartY=-1.92993 StartZ=0 EndX=5 EndY=-0.658262 EndZ=0
    g13: LineSegment StartX=5 StartY=-0.658262 StartZ=0 EndX=5 EndY=0.658262 EndZ=0
    g14: LineSegment StartX=5 StartY=0.658262 StartZ=0 EndX=4.65926 EndY=1.92993 EndZ=0
    g15: LineSegment StartX=4.65926 StartY=1.92993 StartZ=0 EndX=4.001 EndY=3.07007 EndZ=0
    g16: LineSegment StartX=4.001 StartY=3.07007 StartZ=0 EndX=3.07007 EndY=4.001 EndZ=0
    g17: LineSegment StartX=3.07007 StartY=4.001 StartZ=0 EndX=1.92993 EndY=4.65926 EndZ=0
    g18: LineSegment StartX=1.92993 StartY=4.65926 StartZ=0 EndX=0.658262 EndY=5 EndZ=0
    g19: LineSegment StartX=0.658262 StartY=5 StartZ=0 EndX=-0.658262 EndY=5 EndZ=0
    g20: LineSegment StartX=-0.658262 StartY=5 StartZ=0 EndX=-1.92993 EndY=4.65926 EndZ=0
    g21: LineSegment StartX=-1.92993 StartY=4.65926 StartZ=0 EndX=-3.07007 EndY=4.001 EndZ=0
    g22: LineSegment StartX=-3.07007 StartY=4.001 StartZ=0 EndX=-4.001 EndY=3.07007 EndZ=0
    g23: LineSegment StartX=-4.001 StartY=3.07007 StartZ=0 EndX=-4.65926 EndY=1.92993 EndZ=0
    g24: Circle CenterX=0 CenterY=0 CenterZ=0 NormalX=0 NormalY=0 NormalZ=1 AngleXU=0 Radius=5.04314
  constraints (52):
    c: Coincident(g0,g1)
    c: Coincident(g1,g2)
    c: Coincident(g2,g3)
    c: Coincident(g3,g4)
    c: Coincident(g4,g5)
    c: Coincident(g5,g6)
    c: Coincident(g6,g7)
    c: Coincident(g7,g8)
    c: Coincident(g8,g9)
    c: Coincident(g9,g10)
    c: Coincident(g10,g11)
    c: Coincident(g11,g12)
    c: Coincident(g12,g13)
    c: Coincident(g13,g14)
    c: Coincident(g14,g15)
    c: Coincident(g15,g16)
    c: Coincident(g16,g17)
    c: Coincident(g17,g18)
    c: Coincident(g18,g19)
    c: Coincident(g19,g20)
    c: Coincident(g20,g21)
    c: Coincident(g21,g22)
    c: Coincident(g22,g23)
    c: Coincident(g23,g0)
    c: Equal(g0, g1-g23) x23
    c: PointOnObject(g0,g24)
    c: PointOnObject(g1,g24)
    c: PointOnObject(g2,g24)
    c: PointOnObject(g3,g24)
    c: PointOnObject(g4,g24)
    c: PointOnObject(g5,g24)
    c: PointOnObject(g6,g24)
    c: PointOnObject(g7,g24)
    c: PointOnObject(g8,g24)
    c: PointOnObject(g9,g24)
    c: PointOnObject(g10,g24)
    c: PointOnObject(g11,g24)
    c: PointOnObject(g12,g24)
    c: PointOnObject(g13,g24)
    c: PointOnObject(g14,g24)
    c: PointOnObject(g15,g24)
    c: PointOnObject(g16,g24)
    c: PointOnObject(g17,g24)
    c: PointOnObject(g18,g24)
    c: PointOnObject(g19,g24)
    c: PointOnObject(g20,g24)
    c: PointOnObject(g21,g24)
    c: PointOnObject(g22,g24)
    c: PointOnObject(g23,g24)
    c: Coincident(g24,g-1)
    c: Horizontal(g19)
    c: DistanceX(g0,g13) = 10
FEATURE [PartDesign::AdditiveLoft] AdditiveLoft008
  AllowMultiFace = false
  Closed = false
  Profile = -> Sketch077
  Refine = true
  Ruled = false
  Sections = -> [Sketch076,Sketch078]
FEATURE [Sketcher::SketchObject] Sketch072
  FullyConstrained = false
  MapMode = 5
  Placement = pos=(0,0,17) rot=(0,0,1;0rad)
  Support = -> [AdditiveLoft008]
  sketch-geometry (1):
    g0: Circle CenterX=0 CenterY=0 CenterZ=0 NormalX=0 NormalY=0 NormalZ=1 AngleXU=0 Radius=4.5
  constraints (2):
    c: Coincident(g0,g-1)
    c: Radius(g0) = 4.5
FEATURE [PartDesign::Pad] Pad018
  AllowMultiFace = false
  BaseFeature = -> AdditiveLoft008
  Direction = (1,1,1)
  Length = 0.7
  Length2 = 100
  Profile = -> Sketch072
  Refine = true
  Type = 0
FEATURE [Sketcher::SketchObject] Sketch071
  FullyConstrained = false
  MapMode = 5
  Placement = pos=(0,0,0) rot=(1,0,0;3.14159rad)
  Support = -> [Pad018]
  sketch-geometry (1):
    g0: Circle CenterX=0 CenterY=0 CenterZ=0 NormalX=0 NormalY=0 NormalZ=1 AngleXU=0 Radius=5
  constraints (2):
    c: Coincident(g0,g-1)
    c: Radius(g0) = 5
FEATURE [PartDesign::Pocket] Pocket028
  AllowMultiFace = false
  BaseFeature = -> Pad018
  Direction = (1,1,1)
  Length = 1
  Length2 = 100
  Profile = -> Sketch071
  Refine = true
  Type = 0
FEATURE [Sketcher::SketchObject] Sketch069
  FullyConstrained = false
  MapMode = 5
  Placement = pos=(0,0,1) rot=(1,0,0;3.14159rad)
  Support = -> [Pocket028]
  sketch-geometry (1):
    g0: Circle CenterX=0 CenterY=0 CenterZ=0 NormalX=0 NormalY=0 NormalZ=1 AngleXU=0 Radius=4.65
  constraints (2):
    c: Coincident(g0,g-1)
    c: Radius(g0) = 4.65
FEATURE [PartDesign::Pocket] Pocket027
  AllowMultiFace = false
  BaseFeature = -> Pocket028
  Direction = (1,1,1)
  Length = 1
  Length2 = 100
  Profile = -> Sketch069
  Refine = true
  Type = 0
FEATURE [Sketcher::SketchObject] Sketch070
  FullyConstrained = false
  MapMode = 5
  Placement = pos=(0,0,2) rot=(1,0,0;3.14159rad)
  Support = -> [Pocket027]
  sketch-geometry (2):
    g0: ArcOfCircle CenterX=0 CenterY=0 CenterZ=0 NormalX=0 NormalY=0 NormalZ=1 AngleXU=0 Radius=3 StartAngle=2.19024 EndAngle=7.23453
    g1: LineSegment StartX=-1.74176 StartY=2.4426 StartZ=0 EndX=1.74176 EndY=2.4426 EndZ=0
  constraints (5):
    c: Coincident(g0,g-1)
    c: Coincident(g1,g0)
    c: Coincident(g1,g0)
    c: Horizontal(g1)
    c: Radius(g0) = 3
FEATURE [PartDesign::Pocket] Pocket029
  AllowMultiFace = false
  BaseFeature = -> Pocket027
  Direction = (1,1,1)
  Length = 8
  Length2 = 100
  Profile = -> Sketch070
  Refine = true
  Type = 0
FEATURE [PartDesign::Chamfer] Chamfer021
  Angle = 45
  Base = -> Pocket029 [Edge82,Edge83]
  BaseFeature = -> Pocket029
  ChamferType = 0
  FlipDirection = false
  Size = 1.4
  Size2 = 1
  SupportTransform = false
  UseAllEdges = false
FEATURE [PartDesign::Chamfer] Chamfer020
  Angle = 45
  Base = -> Chamfer021 [Edge8]
  BaseFeature = -> Chamfer021
  ChamferType = 0
  FlipDirection = false
  Size = 0.3
  Size2 = 1
  SupportTransform = false
  UseAllEdges = false
FEATURE [PartDesign::Fillet] Fillet009
  Base = -> Chamfer020 [Edge93,Face36]
  BaseFeature = -> Chamfer020
  Radius = 0.1
  SupportTransform = false
  UseAllEdges = false
FEATURE [PartDesign::Body] Body018
  Group = -> [Sketch077,Sketch076,Sketch078,AdditiveLoft008,Sketch072,Pad018,Sketch071,Pocket028,Sketch069,Pocket027,Sketch070,Pocket029,Chamfer021,Chamfer020,Fillet009]
  Origin = -> Origin049
  Tip = -> Fillet009
FEATURE [Sketcher::SketchObject] Sketch079
  AttachmentOffset = pos=(0,0,17.7) rot=(0,0,1;0rad)
  FullyConstrained = false
  MapMode = 5
  Placement = pos=(0,0,17.7) rot=(0,0,1;0rad)
  Support = -> [XY_Plane030]
  sketch-geometry (10):
    g0: LineSegment StartX=-0.2 StartY=1.5 StartZ=0 EndX=0.2 EndY=1.5 EndZ=0
    g1: LineSegment StartX=0.4 StartY=1.7 StartZ=0 EndX=0.4 EndY=4.2 EndZ=0
    g2: LineSegment StartX=0.2 StartY=4.4 StartZ=0 EndX=-0.2 EndY=4.4 EndZ=0
    g3: LineSegment StartX=-0.4 StartY=4.2 StartZ=0 EndX=-0.4 EndY=1.7 EndZ=0
    g4: ArcOfCircle CenterX=-0.2 CenterY=1.7 CenterZ=0 NormalX=0 NormalY=0 NormalZ=1 AngleXU=0 Radius=0.2 StartAngle=3.14159 EndAngle=4.71239
    g5: ArcOfCircle CenterX=0.2 CenterY=1.7 CenterZ=0 NormalX=0 NormalY=0 NormalZ=1 AngleXU=0 Radius=0.2 StartAngle=4.71239 EndAngle=6.28319
    g6: ArcOfCircle CenterX=0.2 CenterY=4.2 CenterZ=0 NormalX=0 NormalY=0 NormalZ=1 AngleXU=0 Radius=0.2 StartAngle=1.4e-15 EndAngle=1.5708
    g7: ArcOfCircle CenterX=-0.2 CenterY=4.2 CenterZ=0 NormalX=0 NormalY=0 NormalZ=1 AngleXU=0 Radius=0.2 StartAngle=1.5708 EndAngle=3.14159
    g8: LineSegment StartX=-0.2 StartY=1.7 StartZ=0 EndX=0 EndY=0 EndZ=0
    g9: LineSegment StartX=0 StartY=0 StartZ=0 EndX=0.2 EndY=1.7 EndZ=0
  constraints (24):
    c: Horizontal(g0)
    c: Horizontal(g2)
    c: Vertical(g1)
    c: Vertical(g3)
    c: Tangent(g3,g4) = -1.5708
    c: Tangent(g0,g4) = -1.5708
    c: Tangent(g0,g5) = -1.5708
    c: Tangent(g1,g5) = -1.5708
    c: Tangent(g1,g6) = -1.5708
    c: Tangent(g2,g6) = -1.5708
    c: Tangent(g2,g7) = -1.5708
    c: Tangent(g3,g7) = -1.5708
    c: Radius(g7) = 0.2
    c: Equal(g7,g6)
    c: Equal(g7,g5)
    c: Equal(g7,g4)
    c: Coincident(g8,g4)
    c: Coincident(g8,g-1)
    c: Coincident(g9,g-1)
    c: Coincident(g9,g5)
    c: Equal(g9,g8)
    c: DistanceX(g3,g1) = 0.8
    c: DistanceY(g-1,g2) = 4.4
    c: DistanceY(g-1,g0) = 1.5
FEATURE [PartDesign::Pad] Pad019
  AllowMultiFace = false
  Direction = (1,1,1)
  Length = 0.02
  Length2 = 100
  Profile = -> Sketch079
  Refine = true
  Type = 0
FEATURE [PartDesign::Body] Body019  label="Indicator009"
  Group = -> [Sketch079,Pad019]
  Origin = -> Origin027
  Tip = -> Pad019
FEATURE [App::Part] Part015  label="Cap016"
  Group = -> [Body018,Body019]
  Origin = -> Origin026
  Placement = pos=(-13.335,-40.005,0) rot=(0,0,1;0rad)
  expr: .Placement.Base.x = -13.335
  expr: .Placement.Base.y = -40.005
FEATURE [Sketcher::SketchObject] Sketch084
  AttachmentOffset = pos=(0,0,7) rot=(0,0,1;0rad)
  FullyConstrained = false
  MapMode = 5
  Placement = pos=(0,0,7) rot=(0,0,1;0rad)
  Support = -> [XY_Plane033]
  sketch-geometry (25):
    g0: LineSegment StartX=-0.724089 StartY=5.5 StartZ=0 EndX=-2.12292 EndY=5.12518 EndZ=0
    g1: LineSegment StartX=-2.12292 StartY=5.12518 StartZ=0 EndX=-3.37708 EndY=4.4011 EndZ=0
    g2: LineSegment StartX=-3.37708 StartY=4.4011 StartZ=0 EndX=-4.4011 EndY=3.37708 EndZ=0
    g3: LineSegment StartX=-4.4011 StartY=3.37708 StartZ=0 EndX=-5.12518 EndY=2.12292 EndZ=0
    g4: LineSegment StartX=-5.12518 StartY=2.12292 StartZ=0 EndX=-5.5 EndY=0.724089 EndZ=0
    g5: LineSegment StartX=-5.5 StartY=0.724089 StartZ=0 EndX=-5.5 EndY=-0.724089 EndZ=0
    g6: LineSegment StartX=-5.5 StartY=-0.724089 StartZ=0 EndX=-5.12518 EndY=-2.12292 EndZ=0
    g7: LineSegment StartX=-5.12518 StartY=-2.12292 StartZ=0 EndX=-4.4011 EndY=-3.37708 EndZ=0
    g8: LineSegment StartX=-4.4011 StartY=-3.37708 StartZ=0 EndX=-3.37708 EndY=-4.4011 EndZ=0
    g9: LineSegment StartX=-3.37708 StartY=-4.4011 StartZ=0 EndX=-2.12292 EndY=-5.12518 EndZ=0
    g10: LineSegment StartX=-2.12292 StartY=-5.12518 StartZ=0 EndX=-0.724089 EndY=-5.5 EndZ=0
    g11: LineSegment StartX=-0.724089 StartY=-5.5 StartZ=0 EndX=0.724089 EndY=-5.5 EndZ=0
    g12: LineSegment StartX=0.724089 StartY=-5.5 StartZ=0 EndX=2.12292 EndY=-5.12518 EndZ=0
    g13: LineSegment StartX=2.12292 StartY=-5.12518 StartZ=0 EndX=3.37708 EndY=-4.4011 EndZ=0
    g14: LineSegment StartX=3.37708 StartY=-4.4011 StartZ=0 EndX=4.4011 EndY=-3.37708 EndZ=0
    g15: LineSegment StartX=4.4011 StartY=-3.37708 StartZ=0 EndX=5.12518 EndY=-2.12292 EndZ=0
    g16: LineSegment StartX=5.12518 StartY=-2.12292 StartZ=0 EndX=5.5 EndY=-0.724089 EndZ=0
    g17: LineSegment StartX=5.5 StartY=-0.724089 StartZ=0 EndX=5.5 EndY=0.724089 EndZ=0
    g18: LineSegment StartX=5.5 StartY=0.724089 StartZ=0 EndX=5.12518 EndY=2.12292 EndZ=0
    g19: LineSegment StartX=5.12518 StartY=2.12292 StartZ=0 EndX=4.4011 EndY=3.37708 EndZ=0
    g20: LineSegment StartX=4.4011 StartY=3.37708 StartZ=0 EndX=3.37708 EndY=4.4011 EndZ=0
    g21: LineSegment StartX=3.37708 StartY=4.4011 StartZ=0 EndX=2.12292 EndY=5.12518 EndZ=0
    g22: LineSegment StartX=2.12292 StartY=5.12518 StartZ=0 EndX=0.724089 EndY=5.5 EndZ=0
    g23: LineSegment StartX=0.724089 StartY=5.5 StartZ=0 EndX=-0.724089 EndY=5.5 EndZ=0
    g24: Circle CenterX=0 CenterY=0 CenterZ=0 NormalX=0 NormalY=0 NormalZ=1 AngleXU=0 Radius=5.54746
  constraints (52):
    c: Coincident(g0,g1)
    c: Coincident(g1,g2)
    c: Coincident(g2,g3)
    c: Coincident(g3,g4)
    c: Coincident(g4,g5)
    c: Coincident(g5,g6)
    c: Coincident(g6,g7)
    c: Coincident(g7,g8)
    c: Coincident(g8,g9)
    c: Coincident(g9,g10)
    c: Coincident(g10,g11)
    c: Coincident(g11,g12)
    c: Coincident(g12,g13)
    c: Coincident(g13,g14)
    c: Coincident(g14,g15)
    c: Coincident(g15,g16)
    c: Coincident(g16,g17)
    c: Coincident(g17,g18)
    c: Coincident(g18,g19)
    c: Coincident(g19,g20)
    c: Coincident(g20,g21)
    c: Coincident(g21,g22)
    c: Coincident(g22,g23)
    c: Coincident(g23,g0)
    c: Equal(g0, g1-g23) x23
    c: PointOnObject(g0,g24)
    c: PointOnObject(g1,g24)
    c: PointOnObject(g2,g24)
    c: PointOnObject(g3,g24)
    c: PointOnObject(g4,g24)
    c: PointOnObject(g5,g24)
    c: PointOnObject(g6,g24)
    c: PointOnObject(g7,g24)
    c: PointOnObject(g8,g24)
    c: PointOnObject(g9,g24)
    c: PointOnObject(g10,g24)
    c: PointOnObject(g11,g24)
    c: PointOnObject(g12,g24)
    c: PointOnObject(g13,g24)
    c: PointOnObject(g14,g24)
    c: PointOnObject(g15,g24)
    c: PointOnObject(g16,g24)
    c: PointOnObject(g17,g24)
    c: PointOnObject(g18,g24)
    c: PointOnObject(g19,g24)
    c: PointOnObject(g20,g24)
    c: PointOnObject(g21,g24)
    c: PointOnObject(g22,g24)
    c: PointOnObject(g23,g24)
    c: Coincident(g24,g-1)
    c: Horizontal(g23)
    c: DistanceX(g4,g17) = 11
FEATURE [Sketcher::SketchObject] Sketch085
  FullyConstrained = false
  MapMode = 5
  Support = -> [XY_Plane033]
  sketch-geometry (25):
    g0: LineSegment StartX=-0.789915 StartY=6 StartZ=0 EndX=-2.31591 EndY=5.59111 EndZ=0
    g1: LineSegment StartX=-2.31591 StartY=5.59111 StartZ=0 EndX=-3.68409 EndY=4.80119 EndZ=0
    g2: LineSegment StartX=-3.68409 StartY=4.80119 StartZ=0 EndX=-4.80119 EndY=3.68409 EndZ=0
    g3: LineSegment StartX=-4.80119 StartY=3.68409 StartZ=0 EndX=-5.59111 EndY=2.31591 EndZ=0
    g4: LineSegment StartX=-5.59111 StartY=2.31591 StartZ=0 EndX=-6 EndY=0.789915 EndZ=0
    g5: LineSegment StartX=-6 StartY=0.789915 StartZ=0 EndX=-6 EndY=-0.789915 EndZ=0
    g6: LineSegment StartX=-6 StartY=-0.789915 StartZ=0 EndX=-5.59111 EndY=-2.31591 EndZ=0
    g7: LineSegment StartX=-5.59111 StartY=-2.31591 StartZ=0 EndX=-4.80119 EndY=-3.68409 EndZ=0
    g8: LineSegment StartX=-4.80119 StartY=-3.68409 StartZ=0 EndX=-3.68409 EndY=-4.80119 EndZ=0
    g9: LineSegment StartX=-3.68409 StartY=-4.80119 StartZ=0 EndX=-2.31591 EndY=-5.59111 EndZ=0
    g10: LineSegment StartX=-2.31591 StartY=-5.59111 StartZ=0 EndX=-0.789915 EndY=-6 EndZ=0
    g11: LineSegment StartX=-0.789915 StartY=-6 StartZ=0 EndX=0.789915 EndY=-6 EndZ=0
    g12: LineSegment StartX=0.789915 StartY=-6 StartZ=0 EndX=2.31591 EndY=-5.59111 EndZ=0
    g13: LineSegment StartX=2.31591 StartY=-5.59111 StartZ=0 EndX=3.68409 EndY=-4.80119 EndZ=0
    g14: LineSegment StartX=3.68409 StartY=-4.80119 StartZ=0 EndX=4.80119 EndY=-3.68409 EndZ=0
    g15: LineSegment StartX=4.80119 StartY=-3.68409 StartZ=0 EndX=5.59111 EndY=-2.31591 EndZ=0
    g16: LineSegment StartX=5.59111 StartY=-2.31591 StartZ=0 EndX=6 EndY=-0.789915 EndZ=0
    g17: LineSegment StartX=6 StartY=-0.789915 StartZ=0 EndX=6 EndY=0.789915 EndZ=0
    g18: LineSegment StartX=6 StartY=0.789915 StartZ=0 EndX=5.59111 EndY=2.31591 EndZ=0
    g19: LineSegment StartX=5.59111 StartY=2.31591 StartZ=0 EndX=4.80119 EndY=3.68409 EndZ=0
    g20: LineSegment StartX=4.80119 StartY=3.68409 StartZ=0 EndX=3.68409 EndY=4.80119 EndZ=0
    g21: LineSegment StartX=3.68409 StartY=4.80119 StartZ=0 EndX=2.31591 EndY=5.59111 EndZ=0
    g22: LineSegment StartX=2.31591 StartY=5.59111 StartZ=0 EndX=0.789915 EndY=6 EndZ=0
    g23: LineSegment StartX=0.789915 StartY=6 StartZ=0 EndX=-0.789915 EndY=6 EndZ=0
    g24: Circle CenterX=0 CenterY=0 CenterZ=0 NormalX=0 NormalY=0 NormalZ=1 AngleXU=0 Radius=6.05177
  constraints (52):
    c: Coincident(g0,g1)
    c: Coincident(g1,g2)
    c: Coincident(g2,g3)
    c: Coincident(g3,g4)
    c: Coincident(g4,g5)
    c: Coincident(g5,g6)
    c: Coincident(g6,g7)
    c: Coincident(g7,g8)
    c: Coincident(g8,g9)
    c: Coincident(g9,g10)
    c: Coincident(g10,g11)
    c: Coincident(g11,g12)
    c: Coincident(g12,g13)
    c: Coincident(g13,g14)
    c: Coincident(g14,g15)
    c: Coincident(g15,g16)
    c: Coincident(g16,g17)
    c: Coincident(g17,g18)
    c: Coincident(g18,g19)
    c: Coincident(g19,g20)
    c: Coincident(g20,g21)
    c: Coincident(g21,g22)
    c: Coincident(g22,g23)
    c: Coincident(g23,g0)
    c: Equal(g0, g1-g23) x23
    c: PointOnObject(g0,g24)
    c: PointOnObject(g1,g24)
    c: PointOnObject(g2,g24)
    c: PointOnObject(g3,g24)
    c: PointOnObject(g4,g24)
    c: PointOnObject(g5,g24)
    c: PointOnObject(g6,g24)
    c: PointOnObject(g7,g24)
    c: PointOnObject(g8,g24)
    c: PointOnObject(g9,g24)
    c: PointOnObject(g10,g24)
    c: PointOnObject(g11,g24)
    c: PointOnObject(g12,g24)
    c: PointOnObject(g13,g24)
    c: PointOnObject(g14,g24)
    c: PointOnObject(g15,g24)
    c: PointOnObject(g16,g24)
    c: PointOnObject(g17,g24)
    c: PointOnObject(g18,g24)
    c: PointOnObject(g19,g24)
    c: PointOnObject(g20,g24)
    c: PointOnObject(g21,g24)
    c: PointOnObject(g22,g24)
    c: PointOnObject(g23,g24)
    c: Coincident(g24,g-1)
    c: Horizontal(g23)
    c: DistanceX(g4,g17) = 12
FEATURE [Sketcher::SketchObject] Sketch086
  AttachmentOffset = pos=(0,0,17) rot=(0,0,1;0rad)
  FullyConstrained = false
  MapMode = 5
  Placement = pos=(0,0,17) rot=(0,0,1;0rad)
  Support = -> [XY_Plane033]
  sketch-geometry (25):
    g0: LineSegment StartX=-4.65926 StartY=1.92993 StartZ=0 EndX=-5 EndY=0.658262 EndZ=0
    g1: LineSegment StartX=-5 StartY=0.658262 StartZ=0 EndX=-5 EndY=-0.658262 EndZ=0
    g2: LineSegment StartX=-5 StartY=-0.658262 StartZ=0 EndX=-4.65926 EndY=-1.92993 EndZ=0
    g3: LineSegment StartX=-4.65926 StartY=-1.92993 StartZ=0 EndX=-4.001 EndY=-3.07007 EndZ=0
    g4: LineSegment StartX=-4.001 StartY=-3.07007 StartZ=0 EndX=-3.07007 EndY=-4.001 EndZ=0
    g5: LineSegment StartX=-3.07007 StartY=-4.001 StartZ=0 EndX=-1.92993 EndY=-4.65926 EndZ=0
    g6: LineSegment StartX=-1.92993 StartY=-4.65926 StartZ=0 EndX=-0.658262 EndY=-5 EndZ=0
    g7: LineSegment StartX=-0.658262 StartY=-5 StartZ=0 EndX=0.658262 EndY=-5 EndZ=0
    g8: LineSegment StartX=0.658262 StartY=-5 StartZ=0 EndX=1.92993 EndY=-4.65926 EndZ=0
    g9: LineSegment StartX=1.92993 StartY=-4.65926 StartZ=0 EndX=3.07007 EndY=-4.001 EndZ=0
    g10: LineSegment StartX=3.07007 StartY=-4.001 StartZ=0 EndX=4.001 EndY=-3.07007 EndZ=0
    g11: LineSegment StartX=4.001 StartY=-3.07007 StartZ=0 EndX=4.65926 EndY=-1.92993 EndZ=0
    g12: LineSegment StartX=4.65926 StartY=-1.92993 StartZ=0 EndX=5 EndY=-0.658262 EndZ=0
    g13: LineSegment StartX=5 StartY=-0.658262 StartZ=0 EndX=5 EndY=0.658262 EndZ=0
    g14: LineSegment StartX=5 StartY=0.658262 StartZ=0 EndX=4.65926 EndY=1.92993 EndZ=0
    g15: LineSegment StartX=4.65926 StartY=1.92993 StartZ=0 EndX=4.001 EndY=3.07007 EndZ=0
    g16: LineSegment StartX=4.001 StartY=3.07007 StartZ=0 EndX=3.07007 EndY=4.001 EndZ=0
    g17: LineSegment StartX=3.07007 StartY=4.001 StartZ=0 EndX=1.92993 EndY=4.65926 EndZ=0
    g18: LineSegment StartX=1.92993 StartY=4.65926 StartZ=0 EndX=0.658262 EndY=5 EndZ=0
    g19: LineSegment StartX=0.658262 StartY=5 StartZ=0 EndX=-0.658262 EndY=5 EndZ=0
    g20: LineSegment StartX=-0.658262 StartY=5 StartZ=0 EndX=-1.92993 EndY=4.65926 EndZ=0
    g21: LineSegment StartX=-1.92993 StartY=4.65926 StartZ=0 EndX=-3.07007 EndY=4.001 EndZ=0
    g22: LineSegment StartX=-3.07007 StartY=4.001 StartZ=0 EndX=-4.001 EndY=3.07007 EndZ=0
    g23: LineSegment StartX=-4.001 StartY=3.07007 StartZ=0 EndX=-4.65926 EndY=1.92993 EndZ=0
    g24: Circle CenterX=0 CenterY=0 CenterZ=0 NormalX=0 NormalY=0 NormalZ=1 AngleXU=0 Radius=5.04314
  constraints (52):
    c: Coincident(g0,g1)
    c: Coincident(g1,g2)
    c: Coincident(g2,g3)
    c: Coincident(g3,g4)
    c: Coincident(g4,g5)
    c: Coincident(g5,g6)
    c: Coincident(g6,g7)
    c: Coincident(g7,g8)
    c: Coincident(g8,g9)
    c: Coincident(g9,g10)
    c: Coincident(g10,g11)
    c: Coincident(g11,g12)
    c: Coincident(g12,g13)
    c: Coincident(g13,g14)
    c: Coincident(g14,g15)
    c: Coincident(g15,g16)
    c: Coincident(g16,g17)
    c: Coincident(g17,g18)
    c: Coincident(g18,g19)
    c: Coincident(g19,g20)
    c: Coincident(g20,g21)
    c: Coincident(g21,g22)
    c: Coincident(g22,g23)
    c: Coincident(g23,g0)
    c: Equal(g0, g1-g23) x23
    c: PointOnObject(g0,g24)
    c: PointOnObject(g1,g24)
    c: PointOnObject(g2,g24)
    c: PointOnObject(g3,g24)
    c: PointOnObject(g4,g24)
    c: PointOnObject(g5,g24)
    c: PointOnObject(g6,g24)
    c: PointOnObject(g7,g24)
    c: PointOnObject(g8,g24)
    c: PointOnObject(g9,g24)
    c: PointOnObject(g10,g24)
    c: PointOnObject(g11,g24)
    c: PointOnObject(g12,g24)
    c: PointOnObject(g13,g24)
    c: PointOnObject(g14,g24)
    c: PointOnObject(g15,g24)
    c: PointOnObject(g16,g24)
    c: PointOnObject(g17,g24)
    c: PointOnObject(g18,g24)
    c: PointOnObject(g19,g24)
    c: PointOnObject(g20,g24)
    c: PointOnObject(g21,g24)
    c: PointOnObject(g22,g24)
    c: PointOnObject(g23,g24)
    c: Coincident(g24,g-1)
    c: Horizontal(g19)
    c: DistanceX(g0,g13) = 10
FEATURE [PartDesign::AdditiveLoft] AdditiveLoft010
  AllowMultiFace = false
  Closed = false
  Profile = -> Sketch085
  Refine = true
  Ruled = false
  Sections = -> [Sketch084,Sketch086]
FEATURE [Sketcher::SketchObject] Sketch083
  FullyConstrained = false
  MapMode = 5
  Placement = pos=(0,0,17) rot=(0,0,1;0rad)
  Support = -> [AdditiveLoft010]
  sketch-geometry (1):
    g0: Circle CenterX=0 CenterY=0 CenterZ=0 NormalX=0 NormalY=0 NormalZ=1 AngleXU=0 Radius=4.5
  constraints (2):
    c: Coincident(g0,g-1)
    c: Radius(g0) = 4.5
FEATURE [PartDesign::Pad] Pad020
  AllowMultiFace = false
  BaseFeature = -> AdditiveLoft010
  Direction = (1,1,1)
  Length = 0.7
  Length2 = 100
  Profile = -> Sketch083
  Refine = true
  Type = 0
FEATURE [Sketcher::SketchObject] Sketch082
  FullyConstrained = false
  MapMode = 5
  Placement = pos=(0,0,0) rot=(1,0,0;3.14159rad)
  Support = -> [Pad020]
  sketch-geometry (1):
    g0: Circle CenterX=0 CenterY=0 CenterZ=0 NormalX=0 NormalY=0 NormalZ=1 AngleXU=0 Radius=5
  constraints (2):
    c: Coincident(g0,g-1)
    c: Radius(g0) = 5
FEATURE [PartDesign::Pocket] Pocket031
  AllowMultiFace = false
  BaseFeature = -> Pad020
  Direction = (1,1,1)
  Length = 1
  Length2 = 100
  Profile = -> Sketch082
  Refine = true
  Type = 0
FEATURE [Sketcher::SketchObject] Sketch080
  FullyConstrained = false
  MapMode = 5
  Placement = pos=(0,0,1) rot=(1,0,0;3.14159rad)
  Support = -> [Pocket031]
  sketch-geometry (1):
    g0: Circle CenterX=0 CenterY=0 CenterZ=0 NormalX=0 NormalY=0 NormalZ=1 AngleXU=0 Radius=4.65
  constraints (2):
    c: Coincident(g0,g-1)
    c: Radius(g0) = 4.65
FEATURE [PartDesign::Pocket] Pocket030
  AllowMultiFace = false
  BaseFeature = -> Pocket031
  Direction = (1,1,1)
  Length = 1
  Length2 = 100
  Profile = -> Sketch080
  Refine = true
  Type = 0
FEATURE [Sketcher::SketchObject] Sketch081
  FullyConstrained = false
  MapMode = 5
  Placement = pos=(0,0,2) rot=(1,0,0;3.14159rad)
  Support = -> [Pocket030]
  sketch-geometry (2):
    g0: ArcOfCircle CenterX=0 CenterY=0 CenterZ=0 NormalX=0 NormalY=0 NormalZ=1 AngleXU=0 Radius=3 StartAngle=2.19024 EndAngle=7.23453
    g1: LineSegment StartX=-1.74176 StartY=2.4426 StartZ=0 EndX=1.74176 EndY=2.4426 EndZ=0
  constraints (5):
    c: Coincident(g0,g-1)
    c: Coincident(g1,g0)
    c: Coincident(g1,g0)
    c: Horizontal(g1)
    c: Radius(g0) = 3
FEATURE [PartDesign::Pocket] Pocket032
  AllowMultiFace = false
  BaseFeature = -> Pocket030
  Direction = (1,1,1)
  Length = 8
  Length2 = 100
  Profile = -> Sketch081
  Refine = true
  Type = 0
FEATURE [PartDesign::Chamfer] Chamfer024
  Angle = 45
  Base = -> Pocket032 [Edge82,Edge83]
  BaseFeature = -> Pocket032
  ChamferType = 0
  FlipDirection = false
  Size = 1.4
  Size2 = 1
  SupportTransform = false
  UseAllEdges = false
FEATURE [PartDesign::Chamfer] Chamfer019
  Angle = 45
  Base = -> Chamfer024 [Edge8]
  BaseFeature = -> Chamfer024
  ChamferType = 0
  FlipDirection = false
  Size = 0.3
  Size2 = 1
  SupportTransform = false
  UseAllEdges = false
FEATURE [PartDesign::Fillet] Fillet011
  Base = -> Chamfer019 [Edge93,Face36]
  BaseFeature = -> Chamfer019
  Radius = 0.1
  SupportTransform = false
  UseAllEdges = false
FEATURE [PartDesign::Body] Body020
  Group = -> [Sketch085,Sketch084,Sketch086,AdditiveLoft010,Sketch083,Pad020,Sketch082,Pocket031,Sketch080,Pocket030,Sketch081,Pocket032,Chamfer024,Chamfer019,Fillet011]
  Origin = -> Origin030
  Tip = -> Fillet011
FEATURE [Sketcher::SketchObject] Sketch087
  AttachmentOffset = pos=(0,0,17.7) rot=(0,0,1;0rad)
  FullyConstrained = false
  MapMode = 5
  Placement = pos=(0,0,17.7) rot=(0,0,1;0rad)
  Support = -> [XY_Plane034]
  sketch-geometry (10):
    g0: LineSegment StartX=-0.2 StartY=1.5 StartZ=0 EndX=0.2 EndY=1.5 EndZ=0
    g1: LineSegment StartX=0.4 StartY=1.7 StartZ=0 EndX=0.4 EndY=4.2 EndZ=0
    g2: LineSegment StartX=0.2 StartY=4.4 StartZ=0 EndX=-0.2 EndY=4.4 EndZ=0
    g3: LineSegment StartX=-0.4 StartY=4.2 StartZ=0 EndX=-0.4 EndY=1.7 EndZ=0
    g4: ArcOfCircle CenterX=-0.2 CenterY=1.7 CenterZ=0 NormalX=0 NormalY=0 NormalZ=1 AngleXU=0 Radius=0.2 StartAngle=3.14159 EndAngle=4.71239
    g5: ArcOfCircle CenterX=0.2 CenterY=1.7 CenterZ=0 NormalX=0 NormalY=0 NormalZ=1 AngleXU=0 Radius=0.2 StartAngle=4.71239 EndAngle=6.28319
    g6: ArcOfCircle CenterX=0.2 CenterY=4.2 CenterZ=0 NormalX=0 NormalY=0 NormalZ=1 AngleXU=0 Radius=0.2 StartAngle=1.4e-15 EndAngle=1.5708
    g7: ArcOfCircle CenterX=-0.2 CenterY=4.2 CenterZ=0 NormalX=0 NormalY=0 NormalZ=1 AngleXU=0 Radius=0.2 StartAngle=1.5708 EndAngle=3.14159
    g8: LineSegment StartX=-0.2 StartY=1.7 StartZ=0 EndX=0 EndY=0 EndZ=0
    g9: LineSegment StartX=0 StartY=0 StartZ=0 EndX=0.2 EndY=1.7 EndZ=0
  constraints (24):
    c: Horizontal(g0)
    c: Horizontal(g2)
    c: Vertical(g1)
    c: Vertical(g3)
    c: Tangent(g3,g4) = -1.5708
    c: Tangent(g0,g4) = -1.5708
    c: Tangent(g0,g5) = -1.5708
    c: Tangent(g1,g5) = -1.5708
    c: Tangent(g1,g6) = -1.5708
    c: Tangent(g2,g6) = -1.5708
    c: Tangent(g2,g7) = -1.5708
    c: Tangent(g3,g7) = -1.5708
    c: Radius(g7) = 0.2
    c: Equal(g7,g6)
    c: Equal(g7,g5)
    c: Equal(g7,g4)
    c: Coincident(g8,g4)
    c: Coincident(g8,g-1)
    c: Coincident(g9,g-1)
    c: Coincident(g9,g5)
    c: Equal(g9,g8)
    c: DistanceX(g3,g1) = 0.8
    c: DistanceY(g-1,g2) = 4.4
    c: DistanceY(g-1,g0) = 1.5
FEATURE [PartDesign::Pad] Pad021
  AllowMultiFace = false
  Direction = (1,1,1)
  Length = 0.02
  Length2 = 100
  Profile = -> Sketch087
  Refine = true
  Type = 0
FEATURE [PartDesign::Body] Body021  label="Indicator010"
  Group = -> [Sketch087,Pad021]
  Origin = -> Origin028
  Tip = -> Pad021
FEATURE [App::Part] Part013  label="Cap014"
  Group = -> [Body020,Body021]
  Origin = -> Origin029
  Placement = pos=(13.335,-40.005,0) rot=(0,0,1;0rad)
  expr: .Placement.Base.x = 13.335
  expr: .Placement.Base.y = -40.005
FEATURE [Sketcher::SketchObject] Sketch092
  AttachmentOffset = pos=(0,0,7) rot=(0,0,1;0rad)
  FullyConstrained = false
  MapMode = 5
  Placement = pos=(0,0,7) rot=(0,0,1;0rad)
  Support = -> [XY_Plane036]
  sketch-geometry (25):
    g0: LineSegment StartX=-0.724089 StartY=5.5 StartZ=0 EndX=-2.12292 EndY=5.12518 EndZ=0
    g1: LineSegment StartX=-2.12292 StartY=5.12518 StartZ=0 EndX=-3.37708 EndY=4.4011 EndZ=0
    g2: LineSegment StartX=-3.37708 StartY=4.4011 StartZ=0 EndX=-4.4011 EndY=3.37708 EndZ=0
    g3: LineSegment StartX=-4.4011 StartY=3.37708 StartZ=0 EndX=-5.12518 EndY=2.12292 EndZ=0
    g4: LineSegment StartX=-5.12518 StartY=2.12292 StartZ=0 EndX=-5.5 EndY=0.724089 EndZ=0
    g5: LineSegment StartX=-5.5 StartY=0.724089 StartZ=0 EndX=-5.5 EndY=-0.724089 EndZ=0
    g6: LineSegment StartX=-5.5 StartY=-0.724089 StartZ=0 EndX=-5.12518 EndY=-2.12292 EndZ=0
    g7: LineSegment StartX=-5.12518 StartY=-2.12292 StartZ=0 EndX=-4.4011 EndY=-3.37708 EndZ=0
    g8: LineSegment StartX=-4.4011 StartY=-3.37708 StartZ=0 EndX=-3.37708 EndY=-4.4011 EndZ=0
    g9: LineSegment StartX=-3.37708 StartY=-4.4011 StartZ=0 EndX=-2.12292 EndY=-5.12518 EndZ=0
    g10: LineSegment StartX=-2.12292 StartY=-5.12518 StartZ=0 EndX=-0.724089 EndY=-5.5 EndZ=0
    g11: LineSegment StartX=-0.724089 StartY=-5.5 StartZ=0 EndX=0.724089 EndY=-5.5 EndZ=0
    g12: LineSegment StartX=0.724089 StartY=-5.5 StartZ=0 EndX=2.12292 EndY=-5.12518 EndZ=0
    g13: LineSegment StartX=2.12292 StartY=-5.12518 StartZ=0 EndX=3.37708 EndY=-4.4011 EndZ=0
    g14: LineSegment StartX=3.37708 StartY=-4.4011 StartZ=0 EndX=4.4011 EndY=-3.37708 EndZ=0
    g15: LineSegment StartX=4.4011 StartY=-3.37708 StartZ=0 EndX=5.12518 EndY=-2.12292 EndZ=0
    g16: LineSegment StartX=5.12518 StartY=-2.12292 StartZ=0 EndX=5.5 EndY=-0.724089 EndZ=0
    g17: LineSegment StartX=5.5 StartY=-0.724089 StartZ=0 EndX=5.5 EndY=0.724089 EndZ=0
    g18: LineSegment StartX=5.5 StartY=0.724089 StartZ=0 EndX=5.12518 EndY=2.12292 EndZ=0
    g19: LineSegment StartX=5.12518 StartY=2.12292 StartZ=0 EndX=4.4011 EndY=3.37708 EndZ=0
    g20: LineSegment StartX=4.4011 StartY=3.37708 StartZ=0 EndX=3.37708 EndY=4.4011 EndZ=0
    g21: LineSegment StartX=3.37708 StartY=4.4011 StartZ=0 EndX=2.12292 EndY=5.12518 EndZ=0
    g22: LineSegment StartX=2.12292 StartY=5.12518 StartZ=0 EndX=0.724089 EndY=5.5 EndZ=0
    g23: LineSegment StartX=0.724089 StartY=5.5 StartZ=0 EndX=-0.724089 EndY=5.5 EndZ=0
    g24: Circle CenterX=0 CenterY=0 CenterZ=0 NormalX=0 NormalY=0 NormalZ=1 AngleXU=0 Radius=5.54746
  constraints (52):
    c: Coincident(g0,g1)
    c: Coincident(g1,g2)
    c: Coincident(g2,g3)
    c: Coincident(g3,g4)
    c: Coincident(g4,g5)
    c: Coincident(g5,g6)
    c: Coincident(g6,g7)
    c: Coincident(g7,g8)
    c: Coincident(g8,g9)
    c: Coincident(g9,g10)
    c: Coincident(g10,g11)
    c: Coincident(g11,g12)
    c: Coincident(g12,g13)
    c: Coincident(g13,g14)
    c: Coincident(g14,g15)
    c: Coincident(g15,g16)
    c: Coincident(g16,g17)
    c: Coincident(g17,g18)
    c: Coincident(g18,g19)
    c: Coincident(g19,g20)
    c: Coincident(g20,g21)
    c: Coincident(g21,g22)
    c: Coincident(g22,g23)
    c: Coincident(g23,g0)
    c: Equal(g0, g1-g23) x23
    c: PointOnObject(g0,g24)
    c: PointOnObject(g1,g24)
    c: PointOnObject(g2,g24)
    c: PointOnObject(g3,g24)
    c: PointOnObject(g4,g24)
    c: PointOnObject(g5,g24)
    c: PointOnObject(g6,g24)
    c: PointOnObject(g7,g24)
    c: PointOnObject(g8,g24)
    c: PointOnObject(g9,g24)
    c: PointOnObject(g10,g24)
    c: PointOnObject(g11,g24)
    c: PointOnObject(g12,g24)
    c: PointOnObject(g13,g24)
    c: PointOnObject(g14,g24)
    c: PointOnObject(g15,g24)
    c: PointOnObject(g16,g24)
    c: PointOnObject(g17,g24)
    c: PointOnObject(g18,g24)
    c: PointOnObject(g19,g24)
    c: PointOnObject(g20,g24)
    c: PointOnObject(g21,g24)
    c: PointOnObject(g22,g24)
    c: PointOnObject(g23,g24)
    c: Coincident(g24,g-1)
    c: Horizontal(g23)
    c: DistanceX(g4,g17) = 11
FEATURE [Sketcher::SketchObject] Sketch093
  FullyConstrained = false
  MapMode = 5
  Support = -> [XY_Plane036]
  sketch-geometry (25):
    g0: LineSegment StartX=-0.789915 StartY=6 StartZ=0 EndX=-2.31591 EndY=5.59111 EndZ=0
    g1: LineSegment StartX=-2.31591 StartY=5.59111 StartZ=0 EndX=-3.68409 EndY=4.80119 EndZ=0
    g2: LineSegment StartX=-3.68409 StartY=4.80119 StartZ=0 EndX=-4.80119 EndY=3.68409 EndZ=0
    g3: LineSegment StartX=-4.80119 StartY=3.68409 StartZ=0 EndX=-5.59111 EndY=2.31591 EndZ=0
    g4: LineSegment StartX=-5.59111 StartY=2.31591 StartZ=0 EndX=-6 EndY=0.789915 EndZ=0
    g5: LineSegment StartX=-6 StartY=0.789915 StartZ=0 EndX=-6 EndY=-0.789915 EndZ=0
    g6: LineSegment StartX=-6 StartY=-0.789915 StartZ=0 EndX=-5.59111 EndY=-2.31591 EndZ=0
    g7: LineSegment StartX=-5.59111 StartY=-2.31591 StartZ=0 EndX=-4.80119 EndY=-3.68409 EndZ=0
    g8: LineSegment StartX=-4.80119 StartY=-3.68409 StartZ=0 EndX=-3.68409 EndY=-4.80119 EndZ=0
    g9: LineSegment StartX=-3.68409 StartY=-4.80119 StartZ=0 EndX=-2.31591 EndY=-5.59111 EndZ=0
    g10: LineSegment StartX=-2.31591 StartY=-5.59111 StartZ=0 EndX=-0.789915 EndY=-6 EndZ=0
    g11: LineSegment StartX=-0.789915 StartY=-6 StartZ=0 EndX=0.789915 EndY=-6 EndZ=0
    g12: LineSegment StartX=0.789915 StartY=-6 StartZ=0 EndX=2.31591 EndY=-5.59111 EndZ=0
    g13: LineSegment StartX=2.31591 StartY=-5.59111 StartZ=0 EndX=3.68409 EndY=-4.80119 EndZ=0
    g14: LineSegment StartX=3.68409 StartY=-4.80119 StartZ=0 EndX=4.80119 EndY=-3.68409 EndZ=0
    g15: LineSegment StartX=4.80119 StartY=-3.68409 StartZ=0 EndX=5.59111 EndY=-2.31591 EndZ=0
    g16: LineSegment StartX=5.59111 StartY=-2.31591 StartZ=0 EndX=6 EndY=-0.789915 EndZ=0
    g17: LineSegment StartX=6 StartY=-0.789915 StartZ=0 EndX=6 EndY=0.789915 EndZ=0
    g18: LineSegment StartX=6 StartY=0.789915 StartZ=0 EndX=5.59111 EndY=2.31591 EndZ=0
    g19: LineSegment StartX=5.59111 StartY=2.31591 StartZ=0 EndX=4.80119 EndY=3.68409 EndZ=0
    g20: LineSegment StartX=4.80119 StartY=3.68409 StartZ=0 EndX=3.68409 EndY=4.80119 EndZ=0
    g21: LineSegment StartX=3.68409 StartY=4.80119 StartZ=0 EndX=2.31591 EndY=5.59111 EndZ=0
    g22: LineSegment StartX=2.31591 StartY=5.59111 StartZ=0 EndX=0.789915 EndY=6 EndZ=0
    g23: LineSegment StartX=0.789915 StartY=6 StartZ=0 EndX=-0.789915 EndY=6 EndZ=0
    g24: Circle CenterX=0 CenterY=0 CenterZ=0 NormalX=0 NormalY=0 NormalZ=1 AngleXU=0 Radius=6.05177
  constraints (52):
    c: Coincident(g0,g1)
    c: Coincident(g1,g2)
    c: Coincident(g2,g3)
    c: Coincident(g3,g4)
    c: Coincident(g4,g5)
    c: Coincident(g5,g6)
    c: Coincident(g6,g7)
    c: Coincident(g7,g8)
    c: Coincident(g8,g9)
    c: Coincident(g9,g10)
    c: Coincident(g10,g11)
    c: Coincident(g11,g12)
    c: Coincident(g12,g13)
    c: Coincident(g13,g14)
    c: Coincident(g14,g15)
    c: Coincident(g15,g16)
    c: Coincident(g16,g17)
    c: Coincident(g17,g18)
    c: Coincident(g18,g19)
    c: Coincident(g19,g20)
    c: Coincident(g20,g21)
    c: Coincident(g21,g22)
    c: Coincident(g22,g23)
    c: Coincident(g23,g0)
    c: Equal(g0, g1-g23) x23
    c: PointOnObject(g0,g24)
    c: PointOnObject(g1,g24)
    c: PointOnObject(g2,g24)
    c: PointOnObject(g3,g24)
    c: PointOnObject(g4,g24)
    c: PointOnObject(g5,g24)
    c: PointOnObject(g6,g24)
    c: PointOnObject(g7,g24)
    c: PointOnObject(g8,g24)
    c: PointOnObject(g9,g24)
    c: PointOnObject(g10,g24)
    c: PointOnObject(g11,g24)
    c: PointOnObject(g12,g24)
    c: PointOnObject(g13,g24)
    c: PointOnObject(g14,g24)
    c: PointOnObject(g15,g24)
    c: PointOnObject(g16,g24)
    c: PointOnObject(g17,g24)
    c: PointOnObject(g18,g24)
    c: PointOnObject(g19,g24)
    c: PointOnObject(g20,g24)
    c: PointOnObject(g21,g24)
    c: PointOnObject(g22,g24)
    c: PointOnObject(g23,g24)
    c: Coincident(g24,g-1)
    c: Horizontal(g23)
    c: DistanceX(g4,g17) = 12
FEATURE [Sketcher::SketchObject] Sketch094
  AttachmentOffset = pos=(0,0,17) rot=(0,0,1;0rad)
  FullyConstrained = false
  MapMode = 5
  Placement = pos=(0,0,17) rot=(0,0,1;0rad)
  Support = -> [XY_Plane036]
  sketch-geometry (25):
    g0: LineSegment StartX=-4.65926 StartY=1.92993 StartZ=0 EndX=-5 EndY=0.658262 EndZ=0
    g1: LineSegment StartX=-5 StartY=0.658262 StartZ=0 EndX=-5 EndY=-0.658262 EndZ=0
    g2: LineSegment StartX=-5 StartY=-0.658262 StartZ=0 EndX=-4.65926 EndY=-1.92993 EndZ=0
    g3: LineSegment StartX=-4.65926 StartY=-1.92993 StartZ=0 EndX=-4.001 EndY=-3.07007 EndZ=0
    g4: LineSegment StartX=-4.001 StartY=-3.07007 StartZ=0 EndX=-3.07007 EndY=-4.001 EndZ=0
    g5: LineSegment StartX=-3.07007 StartY=-4.001 StartZ=0 EndX=-1.92993 EndY=-4.65926 EndZ=0
    g6: LineSegment StartX=-1.92993 StartY=-4.65926 StartZ=0 EndX=-0.658262 EndY=-5 EndZ=0
    g7: LineSegment StartX=-0.658262 StartY=-5 StartZ=0 EndX=0.658262 EndY=-5 EndZ=0
    g8: LineSegment StartX=0.658262 StartY=-5 StartZ=0 EndX=1.92993 EndY=-4.65926 EndZ=0
    g9: LineSegment StartX=1.92993 StartY=-4.65926 StartZ=0 EndX=3.07007 EndY=-4.001 EndZ=0
    g10: LineSegment StartX=3.07007 StartY=-4.001 StartZ=0 EndX=4.001 EndY=-3.07007 EndZ=0
    g11: LineSegment StartX=4.001 StartY=-3.07007 StartZ=0 EndX=4.65926 EndY=-1.92993 EndZ=0
    g12: LineSegment StartX=4.65926 StartY=-1.92993 StartZ=0 EndX=5 EndY=-0.658262 EndZ=0
    g13: LineSegment StartX=5 StartY=-0.658262 StartZ=0 EndX=5 EndY=0.658262 EndZ=0
    g14: LineSegment StartX=5 StartY=0.658262 StartZ=0 EndX=4.65926 EndY=1.92993 EndZ=0
    g15: LineSegment StartX=4.65926 StartY=1.92993 StartZ=0 EndX=4.001 EndY=3.07007 EndZ=0
    g16: LineSegment StartX=4.001 StartY=3.07007 StartZ=0 EndX=3.07007 EndY=4.001 EndZ=0
    g17: LineSegment StartX=3.07007 StartY=4.001 StartZ=0 EndX=1.92993 EndY=4.65926 EndZ=0
    g18: LineSegment StartX=1.92993 StartY=4.65926 StartZ=0 EndX=0.658262 EndY=5 EndZ=0
    g19: LineSegment StartX=0.658262 StartY=5 StartZ=0 EndX=-0.658262 EndY=5 EndZ=0
    g20: LineSegment StartX=-0.658262 StartY=5 StartZ=0 EndX=-1.92993 EndY=4.65926 EndZ=0
    g21: LineSegment StartX=-1.92993 StartY=4.65926 StartZ=0 EndX=-3.07007 EndY=4.001 EndZ=0
    g22: LineSegment StartX=-3.07007 StartY=4.001 StartZ=0 EndX=-4.001 EndY=3.07007 EndZ=0
    g23: LineSegment StartX=-4.001 StartY=3.07007 StartZ=0 EndX=-4.65926 EndY=1.92993 EndZ=0
    g24: Circle CenterX=0 CenterY=0 CenterZ=0 NormalX=0 NormalY=0 NormalZ=1 AngleXU=0 Radius=5.04314
  constraints (52):
    c: Coincident(g0,g1)
    c: Coincident(g1,g2)
    c: Coincident(g2,g3)
    c: Coincident(g3,g4)
    c: Coincident(g4,g5)
    c: Coincident(g5,g6)
    c: Coincident(g6,g7)
    c: Coincident(g7,g8)
    c: Coincident(g8,g9)
    c: Coincident(g9,g10)
    c: Coincident(g10,g11)
    c: Coincident(g11,g12)
    c: Coincident(g12,g13)
    c: Coincident(g13,g14)
    c: Coincident(g14,g15)
    c: Coincident(g15,g16)
    c: Coincident(g16,g17)
    c: Coincident(g17,g18)
    c: Coincident(g18,g19)
    c: Coincident(g19,g20)
    c: Coincident(g20,g21)
    c: Coincident(g21,g22)
    c: Coincident(g22,g23)
    c: Coincident(g23,g0)
    c: Equal(g0, g1-g23) x23
    c: PointOnObject(g0,g24)
    c: PointOnObject(g1,g24)
    c: PointOnObject(g2,g24)
    c: PointOnObject(g3,g24)
    c: PointOnObject(g4,g24)
    c: PointOnObject(g5,g24)
    c: PointOnObject(g6,g24)
    c: PointOnObject(g7,g24)
    c: PointOnObject(g8,g24)
    c: PointOnObject(g9,g24)
    c: PointOnObject(g10,g24)
    c: PointOnObject(g11,g24)
    c: PointOnObject(g12,g24)
    c: PointOnObject(g13,g24)
    c: PointOnObject(g14,g24)
    c: PointOnObject(g15,g24)
    c: PointOnObject(g16,g24)
    c: PointOnObject(g17,g24)
    c: PointOnObject(g18,g24)
    c: PointOnObject(g19,g24)
    c: PointOnObject(g20,g24)
    c: PointOnObject(g21,g24)
    c: PointOnObject(g22,g24)
    c: PointOnObject(g23,g24)
    c: Coincident(g24,g-1)
    c: Horizontal(g19)
    c: DistanceX(g0,g13) = 10
FEATURE [PartDesign::AdditiveLoft] AdditiveLoft015
  AllowMultiFace = false
  Closed = false
  Profile = -> Sketch093
  Refine = true
  Ruled = false
  Sections = -> [Sketch092,Sketch094]
FEATURE [Sketcher::SketchObject] Sketch091
  FullyConstrained = false
  MapMode = 5
  Placement = pos=(0,0,17) rot=(0,0,1;0rad)
  Support = -> [AdditiveLoft015]
  sketch-geometry (1):
    g0: Circle CenterX=0 CenterY=0 CenterZ=0 NormalX=0 NormalY=0 NormalZ=1 AngleXU=0 Radius=4.5
  constraints (2):
    c: Coincident(g0,g-1)
    c: Radius(g0) = 4.5
FEATURE [PartDesign::Pad] Pad022
  AllowMultiFace = false
  BaseFeature = -> AdditiveLoft015
  Direction = (1,1,1)
  Length = 0.7
  Length2 = 100
  Profile = -> Sketch091
  Refine = true
  Type = 0
FEATURE [Sketcher::SketchObject] Sketch090
  FullyConstrained = false
  MapMode = 5
  Placement = pos=(0,0,0) rot=(1,0,0;3.14159rad)
  Support = -> [Pad022]
  sketch-geometry (1):
    g0: Circle CenterX=0 CenterY=0 CenterZ=0 NormalX=0 NormalY=0 NormalZ=1 AngleXU=0 Radius=5
  constraints (2):
    c: Coincident(g0,g-1)
    c: Radius(g0) = 5
FEATURE [PartDesign::Pocket] Pocket034
  AllowMultiFace = false
  BaseFeature = -> Pad022
  Direction = (1,1,1)
  Length = 1
  Length2 = 100
  Profile = -> Sketch090
  Refine = true
  Type = 0
FEATURE [Sketcher::SketchObject] Sketch088
  FullyConstrained = false
  MapMode = 5
  Placement = pos=(0,0,1) rot=(1,0,0;3.14159rad)
  Support = -> [Pocket034]
  sketch-geometry (1):
    g0: Circle CenterX=0 CenterY=0 CenterZ=0 NormalX=0 NormalY=0 NormalZ=1 AngleXU=0 Radius=4.65
  constraints (2):
    c: Coincident(g0,g-1)
    c: Radius(g0) = 4.65
FEATURE [PartDesign::Pocket] Pocket033
  AllowMultiFace = false
  BaseFeature = -> Pocket034
  Direction = (1,1,1)
  Length = 1
  Length2 = 100
  Profile = -> Sketch088
  Refine = true
  Type = 0
FEATURE [Sketcher::SketchObject] Sketch089
  FullyConstrained = false
  MapMode = 5
  Placement = pos=(0,0,2) rot=(1,0,0;3.14159rad)
  Support = -> [Pocket033]
  sketch-geometry (2):
    g0: ArcOfCircle CenterX=0 CenterY=0 CenterZ=0 NormalX=0 NormalY=0 NormalZ=1 AngleXU=0 Radius=3 StartAngle=2.19024 EndAngle=7.23453
    g1: LineSegment StartX=-1.74176 StartY=2.4426 StartZ=0 EndX=1.74176 EndY=2.4426 EndZ=0
  constraints (5):
    c: Coincident(g0,g-1)
    c: Coincident(g1,g0)
    c: Coincident(g1,g0)
    c: Horizontal(g1)
    c: Radius(g0) = 3
FEATURE [PartDesign::Pocket] Pocket035
  AllowMultiFace = false
  BaseFeature = -> Pocket033
  Direction = (1,1,1)
  Length = 8
  Length2 = 100
  Profile = -> Sketch089
  Refine = true
  Type = 0
FEATURE [PartDesign::Chamfer] Chamfer022
  Angle = 45
  Base = -> Pocket035 [Edge82,Edge83]
  BaseFeature = -> Pocket035
  ChamferType = 0
  FlipDirection = false
  Size = 1.4
  Size2 = 1
  SupportTransform = false
  UseAllEdges = false
FEATURE [PartDesign::Chamfer] Chamfer025
  Angle = 45
  Base = -> Chamfer022 [Edge8]
  BaseFeature = -> Chamfer022
  ChamferType = 0
  FlipDirection = false
  Size = 0.3
  Size2 = 1
  SupportTransform = false
  UseAllEdges = false
FEATURE [PartDesign::Fillet] Fillet010
  Base = -> Chamfer025 [Edge93,Face36]
  BaseFeature = -> Chamfer025
  Radius = 0.1
  SupportTransform = false
  UseAllEdges = false
FEATURE [PartDesign::Body] Body024
  Group = -> [Sketch093,Sketch092,Sketch094,AdditiveLoft015,Sketch091,Pad022,Sketch090,Pocket034,Sketch088,Pocket033,Sketch089,Pocket035,Chamfer022,Chamfer025,Fillet010]
  Origin = -> Origin043
  Tip = -> Fillet010
FEATURE [Sketcher::SketchObject] Sketch095
  AttachmentOffset = pos=(0,0,17.7) rot=(0,0,1;0rad)
  FullyConstrained = false
  MapMode = 5
  Placement = pos=(0,0,17.7) rot=(0,0,1;0rad)
  Support = -> [XY_Plane037]
  sketch-geometry (10):
    g0: LineSegment StartX=-0.2 StartY=1.5 StartZ=0 EndX=0.2 EndY=1.5 EndZ=0
    g1: LineSegment StartX=0.4 StartY=1.7 StartZ=0 EndX=0.4 EndY=4.2 EndZ=0
    g2: LineSegment StartX=0.2 StartY=4.4 StartZ=0 EndX=-0.2 EndY=4.4 EndZ=0
    g3: LineSegment StartX=-0.4 StartY=4.2 StartZ=0 EndX=-0.4 EndY=1.7 EndZ=0
    g4: ArcOfCircle CenterX=-0.2 CenterY=1.7 CenterZ=0 NormalX=0 NormalY=0 NormalZ=1 AngleXU=0 Radius=0.2 StartAngle=3.14159 EndAngle=4.71239
    g5: ArcOfCircle CenterX=0.2 CenterY=1.7 CenterZ=0 NormalX=0 NormalY=0 NormalZ=1 AngleXU=0 Radius=0.2 StartAngle=4.71239 EndAngle=6.28319
    g6: ArcOfCircle CenterX=0.2 CenterY=4.2 CenterZ=0 NormalX=0 NormalY=0 NormalZ=1 AngleXU=0 Radius=0.2 StartAngle=1.4e-15 EndAngle=1.5708
    g7: ArcOfCircle CenterX=-0.2 CenterY=4.2 CenterZ=0 NormalX=0 NormalY=0 NormalZ=1 AngleXU=0 Radius=0.2 StartAngle=1.5708 EndAngle=3.14159
    g8: LineSegment StartX=-0.2 StartY=1.7 StartZ=0 EndX=0 EndY=0 EndZ=0
    g9: LineSegment StartX=0 StartY=0 StartZ=0 EndX=0.2 EndY=1.7 EndZ=0
  constraints (24):
    c: Horizontal(g0)
    c: Horizontal(g2)
    c: Vertical(g1)
    c: Vertical(g3)
    c: Tangent(g3,g4) = -1.5708
    c: Tangent(g0,g4) = -1.5708
    c: Tangent(g0,g5) = -1.5708
    c: Tangent(g1,g5) = -1.5708
    c: Tangent(g1,g6) = -1.5708
    c: Tangent(g2,g6) = -1.5708
    c: Tangent(g2,g7) = -1.5708
    c: Tangent(g3,g7) = -1.5708
    c: Radius(g7) = 0.2
    c: Equal(g7,g6)
    c: Equal(g7,g5)
    c: Equal(g7,g4)
    c: Coincident(g8,g4)
    c: Coincident(g8,g-1)
    c: Coincident(g9,g-1)
    c: Coincident(g9,g5)
    c: Equal(g9,g8)
    c: DistanceX(g3,g1) = 0.8
    c: DistanceY(g-1,g2) = 4.4
    c: DistanceY(g-1,g0) = 1.5
FEATURE [PartDesign::Pad] Pad023
  AllowMultiFace = false
  Direction = (1,1,1)
  Length = 0.02
  Length2 = 100
  Profile = -> Sketch095
  Refine = true
  Type = 0
FEATURE [PartDesign::Body] Body025  label="Indicator012"
  Group = -> [Sketch095,Pad023]
  Origin = -> Origin041
  Tip = -> Pad023
FEATURE [App::Part] Part011  label="Cap012"
  Group = -> [Body024,Body025]
  Origin = -> Origin042
  Placement = pos=(40.005,-40.005,0) rot=(0,0,1;0rad)
  expr: .Placement.Base.x = 40.005
  expr: .Placement.Base.y = -40.005
FEATURE [Sketcher::SketchObject] Sketch100
  AttachmentOffset = pos=(0,0,7) rot=(0,0,1;0rad)
  FullyConstrained = false
  MapMode = 5
  Placement = pos=(0,0,7) rot=(0,0,1;0rad)
  Support = -> [XY_Plane039]
  sketch-geometry (25):
    g0: LineSegment StartX=-0.724089 StartY=5.5 StartZ=0 EndX=-2.12292 EndY=5.12518 EndZ=0
    g1: LineSegment StartX=-2.12292 StartY=5.12518 StartZ=0 EndX=-3.37708 EndY=4.4011 EndZ=0
    g2: LineSegment StartX=-3.37708 StartY=4.4011 StartZ=0 EndX=-4.4011 EndY=3.37708 EndZ=0
    g3: LineSegment StartX=-4.4011 StartY=3.37708 StartZ=0 EndX=-5.12518 EndY=2.12292 EndZ=0
    g4: LineSegment StartX=-5.12518 StartY=2.12292 StartZ=0 EndX=-5.5 EndY=0.724089 EndZ=0
    g5: LineSegment StartX=-5.5 StartY=0.724089 StartZ=0 EndX=-5.5 EndY=-0.724089 EndZ=0
    g6: LineSegment StartX=-5.5 StartY=-0.724089 StartZ=0 EndX=-5.12518 EndY=-2.12292 EndZ=0
    g7: LineSegment StartX=-5.12518 StartY=-2.12292 StartZ=0 EndX=-4.4011 EndY=-3.37708 EndZ=0
    g8: LineSegment StartX=-4.4011 StartY=-3.37708 StartZ=0 EndX=-3.37708 EndY=-4.4011 EndZ=0
    g9: LineSegment StartX=-3.37708 StartY=-4.4011 StartZ=0 EndX=-2.12292 EndY=-5.12518 EndZ=0
    g10: LineSegment StartX=-2.12292 StartY=-5.12518 StartZ=0 EndX=-0.724089 EndY=-5.5 EndZ=0
    g11: LineSegment StartX=-0.724089 StartY=-5.5 StartZ=0 EndX=0.724089 EndY=-5.5 EndZ=0
    g12: LineSegment StartX=0.724089 StartY=-5.5 StartZ=0 EndX=2.12292 EndY=-5.12518 EndZ=0
    g13: LineSegment StartX=2.12292 StartY=-5.12518 StartZ=0 EndX=3.37708 EndY=-4.4011 EndZ=0
    g14: LineSegment StartX=3.37708 StartY=-4.4011 StartZ=0 EndX=4.4011 EndY=-3.37708 EndZ=0
    g15: LineSegment StartX=4.4011 StartY=-3.37708 StartZ=0 EndX=5.12518 EndY=-2.12292 EndZ=0
    g16: LineSegment StartX=5.12518 StartY=-2.12292 StartZ=0 EndX=5.5 EndY=-0.724089 EndZ=0
    g17: LineSegment StartX=5.5 StartY=-0.724089 StartZ=0 EndX=5.5 EndY=0.724089 EndZ=0
    g18: LineSegment StartX=5.5 StartY=0.724089 StartZ=0 EndX=5.12518 EndY=2.12292 EndZ=0
    g19: LineSegment StartX=5.12518 StartY=2.12292 StartZ=0 EndX=4.4011 EndY=3.37708 EndZ=0
    g20: LineSegment StartX=4.4011 StartY=3.37708 StartZ=0 EndX=3.37708 EndY=4.4011 EndZ=0
    g21: LineSegment StartX=3.37708 StartY=4.4011 StartZ=0 EndX=2.12292 EndY=5.12518 EndZ=0
    g22: LineSegment StartX=2.12292 StartY=5.12518 StartZ=0 EndX=0.724089 EndY=5.5 EndZ=0
    g23: LineSegment StartX=0.724089 StartY=5.5 StartZ=0 EndX=-0.724089 EndY=5.5 EndZ=0
    g24: Circle CenterX=0 CenterY=0 CenterZ=0 NormalX=0 NormalY=0 NormalZ=1 AngleXU=0 Radius=5.54746
  constraints (52):
    c: Coincident(g0,g1)
    c: Coincident(g1,g2)
    c: Coincident(g2,g3)
    c: Coincident(g3,g4)
    c: Coincident(g4,g5)
    c: Coincident(g5,g6)
    c: Coincident(g6,g7)
    c: Coincident(g7,g8)
    c: Coincident(g8,g9)
    c: Coincident(g9,g10)
    c: Coincident(g10,g11)
    c: Coincident(g11,g12)
    c: Coincident(g12,g13)
    c: Coincident(g13,g14)
    c: Coincident(g14,g15)
    c: Coincident(g15,g16)
    c: Coincident(g16,g17)
    c: Coincident(g17,g18)
    c: Coincident(g18,g19)
    c: Coincident(g19,g20)
    c: Coincident(g20,g21)
    c: Coincident(g21,g22)
    c: Coincident(g22,g23)
    c: Coincident(g23,g0)
    c: Equal(g0, g1-g23) x23
    c: PointOnObject(g0,g24)
    c: PointOnObject(g1,g24)
    c: PointOnObject(g2,g24)
    c: PointOnObject(g3,g24)
    c: PointOnObject(g4,g24)
    c: PointOnObject(g5,g24)
    c: PointOnObject(g6,g24)
    c: PointOnObject(g7,g24)
    c: PointOnObject(g8,g24)
    c: PointOnObject(g9,g24)
    c: PointOnObject(g10,g24)
    c: PointOnObject(g11,g24)
    c: PointOnObject(g12,g24)
    c: PointOnObject(g13,g24)
    c: PointOnObject(g14,g24)
    c: PointOnObject(g15,g24)
    c: PointOnObject(g16,g24)
    c: PointOnObject(g17,g24)
    c: PointOnObject(g18,g24)
    c: PointOnObject(g19,g24)
    c: PointOnObject(g20,g24)
    c: PointOnObject(g21,g24)
    c: PointOnObject(g22,g24)
    c: PointOnObject(g23,g24)
    c: Coincident(g24,g-1)
    c: Horizontal(g23)
    c: DistanceX(g4,g17) = 11
FEATURE [Sketcher::SketchObject] Sketch105
  FullyConstrained = false
  MapMode = 5
  Support = -> [XY_Plane039]
  sketch-geometry (25):
    g0: LineSegment StartX=-0.789915 StartY=6 StartZ=0 EndX=-2.31591 EndY=5.59111 EndZ=0
    g1: LineSegment StartX=-2.31591 StartY=5.59111 StartZ=0 EndX=-3.68409 EndY=4.80119 EndZ=0
    g2: LineSegment StartX=-3.68409 StartY=4.80119 StartZ=0 EndX=-4.80119 EndY=3.68409 EndZ=0
    g3: LineSegment StartX=-4.80119 StartY=3.68409 StartZ=0 EndX=-5.59111 EndY=2.31591 EndZ=0
    g4: LineSegment StartX=-5.59111 StartY=2.31591 StartZ=0 EndX=-6 EndY=0.789915 EndZ=0
    g5: LineSegment StartX=-6 StartY=0.789915 StartZ=0 EndX=-6 EndY=-0.789915 EndZ=0
    g6: LineSegment StartX=-6 StartY=-0.789915 StartZ=0 EndX=-5.59111 EndY=-2.31591 EndZ=0
    g7: LineSegment StartX=-5.59111 StartY=-2.31591 StartZ=0 EndX=-4.80119 EndY=-3.68409 EndZ=0
    g8: LineSegment StartX=-4.80119 StartY=-3.68409 StartZ=0 EndX=-3.68409 EndY=-4.80119 EndZ=0
    g9: LineSegment StartX=-3.68409 StartY=-4.80119 StartZ=0 EndX=-2.31591 EndY=-5.59111 EndZ=0
    g10: LineSegment StartX=-2.31591 StartY=-5.59111 StartZ=0 EndX=-0.789915 EndY=-6 EndZ=0
    g11: LineSegment StartX=-0.789915 StartY=-6 StartZ=0 EndX=0.789915 EndY=-6 EndZ=0
    g12: LineSegment StartX=0.789915 StartY=-6 StartZ=0 EndX=2.31591 EndY=-5.59111 EndZ=0
    g13: LineSegment StartX=2.31591 StartY=-5.59111 StartZ=0 EndX=3.68409 EndY=-4.80119 EndZ=0
    g14: LineSegment StartX=3.68409 StartY=-4.80119 StartZ=0 EndX=4.80119 EndY=-3.68409 EndZ=0
    g15: LineSegment StartX=4.80119 StartY=-3.68409 StartZ=0 EndX=5.59111 EndY=-2.31591 EndZ=0
    g16: LineSegment StartX=5.59111 StartY=-2.31591 StartZ=0 EndX=6 EndY=-0.789915 EndZ=0
    g17: LineSegment StartX=6 StartY=-0.789915 StartZ=0 EndX=6 EndY=0.789915 EndZ=0
    g18: LineSegment StartX=6 StartY=0.789915 StartZ=0 EndX=5.59111 EndY=2.31591 EndZ=0
    g19: LineSegment StartX=5.59111 StartY=2.31591 StartZ=0 EndX=4.80119 EndY=3.68409 EndZ=0
    g20: LineSegment StartX=4.80119 StartY=3.68409 StartZ=0 EndX=3.68409 EndY=4.80119 EndZ=0
    g21: LineSegment StartX=3.68409 StartY=4.80119 StartZ=0 EndX=2.31591 EndY=5.59111 EndZ=0
    g22: LineSegment StartX=2.31591 StartY=5.59111 StartZ=0 EndX=0.789915 EndY=6 EndZ=0
    g23: LineSegment StartX=0.789915 StartY=6 StartZ=0 EndX=-0.789915 EndY=6 EndZ=0
    g24: Circle CenterX=0 CenterY=0 CenterZ=0 NormalX=0 NormalY=0 NormalZ=1 AngleXU=0 Radius=6.05177
  constraints (52):
    c: Coincident(g0,g1)
    c: Coincident(g1,g2)
    c: Coincident(g2,g3)
    c: Coincident(g3,g4)
    c: Coincident(g4,g5)
    c: Coincident(g5,g6)
    c: Coincident(g6,g7)
    c: Coincident(g7,g8)
    c: Coincident(g8,g9)
    c: Coincident(g9,g10)
    c: Coincident(g10,g11)
    c: Coincident(g11,g12)
    c: Coincident(g12,g13)
    c: Coincident(g13,g14)
    c: Coincident(g14,g15)
    c: Coincident(g15,g16)
    c: Coincident(g16,g17)
    c: Coincident(g17,g18)
    c: Coincident(g18,g19)
    c: Coincident(g19,g20)
    c: Coincident(g20,g21)
    c: Coincident(g21,g22)
    c: Coincident(g22,g23)
    c: Coincident(g23,g0)
    c: Equal(g0, g1-g23) x23
    c: PointOnObject(g0,g24)
    c: PointOnObject(g1,g24)
    c: PointOnObject(g2,g24)
    c: PointOnObject(g3,g24)
    c: PointOnObject(g4,g24)
    c: PointOnObject(g5,g24)
    c: PointOnObject(g6,g24)
    c: PointOnObject(g7,g24)
    c: PointOnObject(g8,g24)
    c: PointOnObject(g9,g24)
    c: PointOnObject(g10,g24)
    c: PointOnObject(g11,g24)
    c: PointOnObject(g12,g24)
    c: PointOnObject(g13,g24)
    c: PointOnObject(g14,g24)
    c: PointOnObject(g15,g24)
    c: PointOnObject(g16,g24)
    c: PointOnObject(g17,g24)
    c: PointOnObject(g18,g24)
    c: PointOnObject(g19,g24)
    c: PointOnObject(g20,g24)
    c: PointOnObject(g21,g24)
    c: PointOnObject(g22,g24)
    c: PointOnObject(g23,g24)
    c: Coincident(g24,g-1)
    c: Horizontal(g23)
    c: DistanceX(g4,g17) = 12
FEATURE [Sketcher::SketchObject] Sketch106
  AttachmentOffset = pos=(0,0,17) rot=(0,0,1;0rad)
  FullyConstrained = false
  MapMode = 5
  Placement = pos=(0,0,17) rot=(0,0,1;0rad)
  Support = -> [XY_Plane039]
  sketch-geometry (25):
    g0: LineSegment StartX=-4.65926 StartY=1.92993 StartZ=0 EndX=-5 EndY=0.658262 EndZ=0
    g1: LineSegment StartX=-5 StartY=0.658262 StartZ=0 EndX=-5 EndY=-0.658262 EndZ=0
    g2: LineSegment StartX=-5 StartY=-0.658262 StartZ=0 EndX=-4.65926 EndY=-1.92993 EndZ=0
    g3: LineSegment StartX=-4.65926 StartY=-1.92993 StartZ=0 EndX=-4.001 EndY=-3.07007 EndZ=0
    g4: LineSegment StartX=-4.001 StartY=-3.07007 StartZ=0 EndX=-3.07007 EndY=-4.001 EndZ=0
    g5: LineSegment StartX=-3.07007 StartY=-4.001 StartZ=0 EndX=-1.92993 EndY=-4.65926 EndZ=0
    g6: LineSegment StartX=-1.92993 StartY=-4.65926 StartZ=0 EndX=-0.658262 EndY=-5 EndZ=0
    g7: LineSegment StartX=-0.658262 StartY=-5 StartZ=0 EndX=0.658262 EndY=-5 EndZ=0
    g8: LineSegment StartX=0.658262 StartY=-5 StartZ=0 EndX=1.92993 EndY=-4.65926 EndZ=0
    g9: LineSegment StartX=1.92993 StartY=-4.65926 StartZ=0 EndX=3.07007 EndY=-4.001 EndZ=0
    g10: LineSegment StartX=3.07007 StartY=-4.001 StartZ=0 EndX=4.001 EndY=-3.07007 EndZ=0
    g11: LineSegment StartX=4.001 StartY=-3.07007 StartZ=0 EndX=4.65926 EndY=-1.92993 EndZ=0
    g12: LineSegment StartX=4.65926 StartY=-1.92993 StartZ=0 EndX=5 EndY=-0.658262 EndZ=0
    g13: LineSegment StartX=5 StartY=-0.658262 StartZ=0 EndX=5 EndY=0.658262 EndZ=0
    g14: LineSegment StartX=5 StartY=0.658262 StartZ=0 EndX=4.65926 EndY=1.92993 EndZ=0
    g15: LineSegment StartX=4.65926 StartY=1.92993 StartZ=0 EndX=4.001 EndY=3.07007 EndZ=0
    g16: LineSegment StartX=4.001 StartY=3.07007 StartZ=0 EndX=3.07007 EndY=4.001 EndZ=0
    g17: LineSegment StartX=3.07007 StartY=4.001 StartZ=0 EndX=1.92993 EndY=4.65926 EndZ=0
    g18: LineSegment StartX=1.92993 StartY=4.65926 StartZ=0 EndX=0.658262 EndY=5 EndZ=0
    g19: LineSegment StartX=0.658262 StartY=5 StartZ=0 EndX=-0.658262 EndY=5 EndZ=0
    g20: LineSegment StartX=-0.658262 StartY=5 StartZ=0 EndX=-1.92993 EndY=4.65926 EndZ=0
    g21: LineSegment StartX=-1.92993 StartY=4.65926 StartZ=0 EndX=-3.07007 EndY=4.001 EndZ=0
    g22: LineSegment StartX=-3.07007 StartY=4.001 StartZ=0 EndX=-4.001 EndY=3.07007 EndZ=0
    g23: LineSegment StartX=-4.001 StartY=3.07007 StartZ=0 EndX=-4.65926 EndY=1.92993 EndZ=0
    g24: Circle CenterX=0 CenterY=0 CenterZ=0 NormalX=0 NormalY=0 NormalZ=1 AngleXU=0 Radius=5.04314
  constraints (52):
    c: Coincident(g0,g1)
    c: Coincident(g1,g2)
    c: Coincident(g2,g3)
    c: Coincident(g3,g4)
    c: Coincident(g4,g5)
    c: Coincident(g5,g6)
    c: Coincident(g6,g7)
    c: Coincident(g7,g8)
    c: Coincident(g8,g9)
    c: Coincident(g9,g10)
    c: Coincident(g10,g11)
    c: Coincident(g11,g12)
    c: Coincident(g12,g13)
    c: Coincident(g13,g14)
    c: Coincident(g14,g15)
    c: Coincident(g15,g16)
    c: Coincident(g16,g17)
    c: Coincident(g17,g18)
    c: Coincident(g18,g19)
    c: Coincident(g19,g20)
    c: Coincident(g20,g21)
    c: Coincident(g21,g22)
    c: Coincident(g22,g23)
    c: Coincident(g23,g0)
    c: Equal(g0, g1-g23) x23
    c: PointOnObject(g0,g24)
    c: PointOnObject(g1,g24)
    c: PointOnObject(g2,g24)
    c: PointOnObject(g3,g24)
    c: PointOnObject(g4,g24)
    c: PointOnObject(g5,g24)
    c: PointOnObject(g6,g24)
    c: PointOnObject(g7,g24)
    c: PointOnObject(g8,g24)
    c: PointOnObject(g9,g24)
    c: PointOnObject(g10,g24)
    c: PointOnObject(g11,g24)
    c: PointOnObject(g12,g24)
    c: PointOnObject(g13,g24)
    c: PointOnObject(g14,g24)
    c: PointOnObject(g15,g24)
    c: PointOnObject(g16,g24)
    c: PointOnObject(g17,g24)
    c: PointOnObject(g18,g24)
    c: PointOnObject(g19,g24)
    c: PointOnObject(g20,g24)
    c: PointOnObject(g21,g24)
    c: PointOnObject(g22,g24)
    c: PointOnObject(g23,g24)
    c: Coincident(g24,g-1)
    c: Horizontal(g19)
    c: DistanceX(g0,g13) = 10
FEATURE [PartDesign::AdditiveLoft] AdditiveLoft012
  AllowMultiFace = false
  Closed = false
  Profile = -> Sketch105
  Refine = true
  Ruled = false
  Sections = -> [Sketch100,Sketch106]
FEATURE [Sketcher::SketchObject] Sketch099
  FullyConstrained = false
  MapMode = 5
  Placement = pos=(0,0,17) rot=(0,0,1;0rad)
  Support = -> [AdditiveLoft012]
  sketch-geometry (1):
    g0: Circle CenterX=0 CenterY=0 CenterZ=0 NormalX=0 NormalY=0 NormalZ=1 AngleXU=0 Radius=4.5
  constraints (2):
    c: Coincident(g0,g-1)
    c: Radius(g0) = 4.5
FEATURE [PartDesign::Pad] Pad025
  AllowMultiFace = false
  BaseFeature = -> AdditiveLoft012
  Direction = (1,1,1)
  Length = 0.7
  Length2 = 100
  Profile = -> Sketch099
  Refine = true
  Type = 0
FEATURE [Sketcher::SketchObject] Sketch098
  FullyConstrained = false
  MapMode = 5
  Placement = pos=(0,0,0) rot=(1,0,0;3.14159rad)
  Support = -> [Pad025]
  sketch-geometry (1):
    g0: Circle CenterX=0 CenterY=0 CenterZ=0 NormalX=0 NormalY=0 NormalZ=1 AngleXU=0 Radius=5
  constraints (2):
    c: Coincident(g0,g-1)
    c: Radius(g0) = 5
FEATURE [PartDesign::Pocket] Pocket037
  AllowMultiFace = false
  BaseFeature = -> Pad025
  Direction = (1,1,1)
  Length = 1
  Length2 = 100
  Profile = -> Sketch098
  Refine = true
  Type = 0
FEATURE [Sketcher::SketchObject] Sketch096
  FullyConstrained = false
  MapMode = 5
  Placement = pos=(0,0,1) rot=(1,0,0;3.14159rad)
  Support = -> [Pocket037]
  sketch-geometry (1):
    g0: Circle CenterX=0 CenterY=0 CenterZ=0 NormalX=0 NormalY=0 NormalZ=1 AngleXU=0 Radius=4.65
  constraints (2):
    c: Coincident(g0,g-1)
    c: Radius(g0) = 4.65
FEATURE [PartDesign::Pocket] Pocket036
  AllowMultiFace = false
  BaseFeature = -> Pocket037
  Direction = (1,1,1)
  Length = 1
  Length2 = 100
  Profile = -> Sketch096
  Refine = true
  Type = 0
FEATURE [Sketcher::SketchObject] Sketch097
  FullyConstrained = false
  MapMode = 5
  Placement = pos=(0,0,2) rot=(1,0,0;3.14159rad)
  Support = -> [Pocket036]
  sketch-geometry (2):
    g0: ArcOfCircle CenterX=0 CenterY=0 CenterZ=0 NormalX=0 NormalY=0 NormalZ=1 AngleXU=0 Radius=3 StartAngle=2.19024 EndAngle=7.23453
    g1: LineSegment StartX=-1.74176 StartY=2.4426 StartZ=0 EndX=1.74176 EndY=2.4426 EndZ=0
  constraints (5):
    c: Coincident(g0,g-1)
    c: Coincident(g1,g0)
    c: Coincident(g1,g0)
    c: Horizontal(g1)
    c: Radius(g0) = 3
FEATURE [PartDesign::Pocket] Pocket038
  AllowMultiFace = false
  BaseFeature = -> Pocket036
  Direction = (1,1,1)
  Length = 8
  Length2 = 100
  Profile = -> Sketch097
  Refine = true
  Type = 0
FEATURE [PartDesign::Chamfer] Chamfer018
  Angle = 45
  Base = -> Pocket038 [Edge82,Edge83]
  BaseFeature = -> Pocket038
  ChamferType = 0
  FlipDirection = false
  Size = 1.4
  Size2 = 1
  SupportTransform = false
  UseAllEdges = false
FEATURE [PartDesign::Chamfer] Chamfer026
  Angle = 45
  Base = -> Chamfer018 [Edge8]
  BaseFeature = -> Chamfer018
  ChamferType = 0
  FlipDirection = false
  Size = 0.3
  Size2 = 1
  SupportTransform = false
  UseAllEdges = false
FEATURE [PartDesign::Fillet] Fillet012
  Base = -> Chamfer026 [Edge93,Face36]
  BaseFeature = -> Chamfer026
  Radius = 0.1
  SupportTransform = false
  UseAllEdges = false
FEATURE [PartDesign::Body] Body022
  Group = -> [Sketch105,Sketch100,Sketch106,AdditiveLoft012,Sketch099,Pad025,Sketch098,Pocket037,Sketch096,Pocket036,Sketch097,Pocket038,Chamfer018,Chamfer026,Fillet012]
  Origin = -> Origin034
  Tip = -> Fillet012
FEATURE [Sketcher::SketchObject] Sketch107
  AttachmentOffset = pos=(0,0,17.7) rot=(0,0,1;0rad)
  FullyConstrained = false
  MapMode = 5
  Placement = pos=(0,0,17.7) rot=(0,0,1;0rad)
  Support = -> [XY_Plane032]
  sketch-geometry (10):
    g0: LineSegment StartX=-0.2 StartY=1.5 StartZ=0 EndX=0.2 EndY=1.5 EndZ=0
    g1: LineSegment StartX=0.4 StartY=1.7 StartZ=0 EndX=0.4 EndY=4.2 EndZ=0
    g2: LineSegment StartX=0.2 StartY=4.4 StartZ=0 EndX=-0.2 EndY=4.4 EndZ=0
    g3: LineSegment StartX=-0.4 StartY=4.2 StartZ=0 EndX=-0.4 EndY=1.7 EndZ=0
    g4: ArcOfCircle CenterX=-0.2 CenterY=1.7 CenterZ=0 NormalX=0 NormalY=0 NormalZ=1 AngleXU=0 Radius=0.2 StartAngle=3.14159 EndAngle=4.71239
    g5: ArcOfCircle CenterX=0.2 CenterY=1.7 CenterZ=0 NormalX=0 NormalY=0 NormalZ=1 AngleXU=0 Radius=0.2 StartAngle=4.71239 EndAngle=6.28319
    g6: ArcOfCircle CenterX=0.2 CenterY=4.2 CenterZ=0 NormalX=0 NormalY=0 NormalZ=1 AngleXU=0 Radius=0.2 StartAngle=1.4e-15 EndAngle=1.5708
    g7: ArcOfCircle CenterX=-0.2 CenterY=4.2 CenterZ=0 NormalX=0 NormalY=0 NormalZ=1 AngleXU=0 Radius=0.2 StartAngle=1.5708 EndAngle=3.14159
    g8: LineSegment StartX=-0.2 StartY=1.7 StartZ=0 EndX=0 EndY=0 EndZ=0
    g9: LineSegment StartX=0 StartY=0 StartZ=0 EndX=0.2 EndY=1.7 EndZ=0
  constraints (24):
    c: Horizontal(g0)
    c: Horizontal(g2)
    c: Vertical(g1)
    c: Vertical(g3)
    c: Tangent(g3,g4) = -1.5708
    c: Tangent(g0,g4) = -1.5708
    c: Tangent(g0,g5) = -1.5708
    c: Tangent(g1,g5) = -1.5708
    c: Tangent(g1,g6) = -1.5708
    c: Tangent(g2,g6) = -1.5708
    c: Tangent(g2,g7) = -1.5708
    c: Tangent(g3,g7) = -1.5708
    c: Radius(g7) = 0.2
    c: Equal(g7,g6)
    c: Equal(g7,g5)
    c: Equal(g7,g4)
    c: Coincident(g8,g4)
    c: Coincident(g8,g-1)
    c: Coincident(g9,g-1)
    c: Coincident(g9,g5)
    c: Equal(g9,g8)
    c: DistanceX(g3,g1) = 0.8
    c: DistanceY(g-1,g2) = 4.4
    c: DistanceY(g-1,g0) = 1.5
FEATURE [PartDesign::Pad] Pad026
  AllowMultiFace = false
  Direction = (1,1,1)
  Length = 0.02
  Length2 = 100
  Profile = -> Sketch107
  Refine = true
  Type = 0
FEATURE [PartDesign::Body] Body023  label="Indicator011"
  Group = -> [Sketch107,Pad026]
  Origin = -> Origin036
  Tip = -> Pad026
FEATURE [App::Part] Part012  label="Cap013"
  Group = -> [Body022,Body023]
  Origin = -> Origin032
  Placement = pos=(-40.005,-13.335,0) rot=(0,0,1;0rad)
  expr: .Placement.Base.x = -40.005
  expr: .Placement.Base.y = -13.335
FEATURE [Sketcher::SketchObject] Sketch108
  AttachmentOffset = pos=(0,0,7) rot=(0,0,1;0rad)
  FullyConstrained = false
  MapMode = 5
  Placement = pos=(0,0,7) rot=(0,0,1;0rad)
  Support = -> [XY_Plane041]
  sketch-geometry (25):
    g0: LineSegment StartX=-0.724089 StartY=5.5 StartZ=0 EndX=-2.12292 EndY=5.12518 EndZ=0
    g1: LineSegment StartX=-2.12292 StartY=5.12518 StartZ=0 EndX=-3.37708 EndY=4.4011 EndZ=0
    g2: LineSegment StartX=-3.37708 StartY=4.4011 StartZ=0 EndX=-4.4011 EndY=3.37708 EndZ=0
    g3: LineSegment StartX=-4.4011 StartY=3.37708 StartZ=0 EndX=-5.12518 EndY=2.12292 EndZ=0
    g4: LineSegment StartX=-5.12518 StartY=2.12292 StartZ=0 EndX=-5.5 EndY=0.724089 EndZ=0
    g5: LineSegment StartX=-5.5 StartY=0.724089 StartZ=0 EndX=-5.5 EndY=-0.724089 EndZ=0
    g6: LineSegment StartX=-5.5 StartY=-0.724089 StartZ=0 EndX=-5.12518 EndY=-2.12292 EndZ=0
    g7: LineSegment StartX=-5.12518 StartY=-2.12292 StartZ=0 EndX=-4.4011 EndY=-3.37708 EndZ=0
    g8: LineSegment StartX=-4.4011 StartY=-3.37708 StartZ=0 EndX=-3.37708 EndY=-4.4011 EndZ=0
    g9: LineSegment StartX=-3.37708 StartY=-4.4011 StartZ=0 EndX=-2.12292 EndY=-5.12518 EndZ=0
    g10: LineSegment StartX=-2.12292 StartY=-5.12518 StartZ=0 EndX=-0.724089 EndY=-5.5 EndZ=0
    g11: LineSegment StartX=-0.724089 StartY=-5.5 StartZ=0 EndX=0.724089 EndY=-5.5 EndZ=0
    g12: LineSegment StartX=0.724089 StartY=-5.5 StartZ=0 EndX=2.12292 EndY=-5.12518 EndZ=0
    g13: LineSegment StartX=2.12292 StartY=-5.12518 StartZ=0 EndX=3.37708 EndY=-4.4011 EndZ=0
    g14: LineSegment StartX=3.37708 StartY=-4.4011 StartZ=0 EndX=4.4011 EndY=-3.37708 EndZ=0
    g15: LineSegment StartX=4.4011 StartY=-3.37708 StartZ=0 EndX=5.12518 EndY=-2.12292 EndZ=0
    g16: LineSegment StartX=5.12518 StartY=-2.12292 StartZ=0 EndX=5.5 EndY=-0.724089 EndZ=0
    g17: LineSegment StartX=5.5 StartY=-0.724089 StartZ=0 EndX=5.5 EndY=0.724089 EndZ=0
    g18: LineSegment StartX=5.5 StartY=0.724089 StartZ=0 EndX=5.12518 EndY=2.12292 EndZ=0
    g19: LineSegment StartX=5.12518 StartY=2.12292 StartZ=0 EndX=4.4011 EndY=3.37708 EndZ=0
    g20: LineSegment StartX=4.4011 StartY=3.37708 StartZ=0 EndX=3.37708 EndY=4.4011 EndZ=0
    g21: LineSegment StartX=3.37708 StartY=4.4011 StartZ=0 EndX=2.12292 EndY=5.12518 EndZ=0
    g22: LineSegment StartX=2.12292 StartY=5.12518 StartZ=0 EndX=0.724089 EndY=5.5 EndZ=0
    g23: LineSegment StartX=0.724089 StartY=5.5 StartZ=0 EndX=-0.724089 EndY=5.5 EndZ=0
    g24: Circle CenterX=0 CenterY=0 CenterZ=0 NormalX=0 NormalY=0 NormalZ=1 AngleXU=0 Radius=5.54746
  constraints (52):
    c: Coincident(g0,g1)
    c: Coincident(g1,g2)
    c: Coincident(g2,g3)
    c: Coincident(g3,g4)
    c: Coincident(g4,g5)
    c: Coincident(g5,g6)
    c: Coincident(g6,g7)
    c: Coincident(g7,g8)
    c: Coincident(g8,g9)
    c: Coincident(g9,g10)
    c: Coincident(g10,g11)
    c: Coincident(g11,g12)
    c: Coincident(g12,g13)
    c: Coincident(g13,g14)
    c: Coincident(g14,g15)
    c: Coincident(g15,g16)
    c: Coincident(g16,g17)
    c: Coincident(g17,g18)
    c: Coincident(g18,g19)
    c: Coincident(g19,g20)
    c: Coincident(g20,g21)
    c: Coincident(g21,g22)
    c: Coincident(g22,g23)
    c: Coincident(g23,g0)
    c: Equal(g0, g1-g23) x23
    c: PointOnObject(g0,g24)
    c: PointOnObject(g1,g24)
    c: PointOnObject(g2,g24)
    c: PointOnObject(g3,g24)
    c: PointOnObject(g4,g24)
    c: PointOnObject(g5,g24)
    c: PointOnObject(g6,g24)
    c: PointOnObject(g7,g24)
    c: PointOnObject(g8,g24)
    c: PointOnObject(g9,g24)
    c: PointOnObject(g10,g24)
    c: PointOnObject(g11,g24)
    c: PointOnObject(g12,g24)
    c: PointOnObject(g13,g24)
    c: PointOnObject(g14,g24)
    c: PointOnObject(g15,g24)
    c: PointOnObject(g16,g24)
    c: PointOnObject(g17,g24)
    c: PointOnObject(g18,g24)
    c: PointOnObject(g19,g24)
    c: PointOnObject(g20,g24)
    c: PointOnObject(g21,g24)
    c: PointOnObject(g22,g24)
    c: PointOnObject(g23,g24)
    c: Coincident(g24,g-1)
    c: Horizontal(g23)
    c: DistanceX(g4,g17) = 11
FEATURE [Sketcher::SketchObject] Sketch109
  FullyConstrained = false
  MapMode = 5
  Support = -> [XY_Plane041]
  sketch-geometry (25):
    g0: LineSegment StartX=-0.789915 StartY=6 StartZ=0 EndX=-2.31591 EndY=5.59111 EndZ=0
    g1: LineSegment StartX=-2.31591 StartY=5.59111 StartZ=0 EndX=-3.68409 EndY=4.80119 EndZ=0
    g2: LineSegment StartX=-3.68409 StartY=4.80119 StartZ=0 EndX=-4.80119 EndY=3.68409 EndZ=0
    g3: LineSegment StartX=-4.80119 StartY=3.68409 StartZ=0 EndX=-5.59111 EndY=2.31591 EndZ=0
    g4: LineSegment StartX=-5.59111 StartY=2.31591 StartZ=0 EndX=-6 EndY=0.789915 EndZ=0
    g5: LineSegment StartX=-6 StartY=0.789915 StartZ=0 EndX=-6 EndY=-0.789915 EndZ=0
    g6: LineSegment StartX=-6 StartY=-0.789915 StartZ=0 EndX=-5.59111 EndY=-2.31591 EndZ=0
    g7: LineSegment StartX=-5.59111 StartY=-2.31591 StartZ=0 EndX=-4.80119 EndY=-3.68409 EndZ=0
    g8: LineSegment StartX=-4.80119 StartY=-3.68409 StartZ=0 EndX=-3.68409 EndY=-4.80119 EndZ=0
    g9: LineSegment StartX=-3.68409 StartY=-4.80119 StartZ=0 EndX=-2.31591 EndY=-5.59111 EndZ=0
    g10: LineSegment StartX=-2.31591 StartY=-5.59111 StartZ=0 EndX=-0.789915 EndY=-6 EndZ=0
    g11: LineSegment StartX=-0.789915 StartY=-6 StartZ=0 EndX=0.789915 EndY=-6 EndZ=0
    g12: LineSegment StartX=0.789915 StartY=-6 StartZ=0 EndX=2.31591 EndY=-5.59111 EndZ=0
    g13: LineSegment StartX=2.31591 StartY=-5.59111 StartZ=0 EndX=3.68409 EndY=-4.80119 EndZ=0
    g14: LineSegment StartX=3.68409 StartY=-4.80119 StartZ=0 EndX=4.80119 EndY=-3.68409 EndZ=0
    g15: LineSegment StartX=4.80119 StartY=-3.68409 StartZ=0 EndX=5.59111 EndY=-2.31591 EndZ=0
    g16: LineSegment StartX=5.59111 StartY=-2.31591 StartZ=0 EndX=6 EndY=-0.789915 EndZ=0
    g17: LineSegment StartX=6 StartY=-0.789915 StartZ=0 EndX=6 EndY=0.789915 EndZ=0
    g18: LineSegment StartX=6 StartY=0.789915 StartZ=0 EndX=5.59111 EndY=2.31591 EndZ=0
    g19: LineSegment StartX=5.59111 StartY=2.31591 StartZ=0 EndX=4.80119 EndY=3.68409 EndZ=0
    g20: LineSegment StartX=4.80119 StartY=3.68409 StartZ=0 EndX=3.68409 EndY=4.80119 EndZ=0
    g21: LineSegment StartX=3.68409 StartY=4.80119 StartZ=0 EndX=2.31591 EndY=5.59111 EndZ=0
    g22: LineSegment StartX=2.31591 StartY=5.59111 StartZ=0 EndX=0.789915 EndY=6 EndZ=0
    g23: LineSegment StartX=0.789915 StartY=6 StartZ=0 EndX=-0.789915 EndY=6 EndZ=0
    g24: Circle CenterX=0 CenterY=0 CenterZ=0 NormalX=0 NormalY=0 NormalZ=1 AngleXU=0 Radius=6.05177
  constraints (52):
    c: Coincident(g0,g1)
    c: Coincident(g1,g2)
    c: Coincident(g2,g3)
    c: Coincident(g3,g4)
    c: Coincident(g4,g5)
    c: Coincident(g5,g6)
    c: Coincident(g6,g7)
    c: Coincident(g7,g8)
    c: Coincident(g8,g9)
    c: Coincident(g9,g10)
    c: Coincident(g10,g11)
    c: Coincident(g11,g12)
    c: Coincident(g12,g13)
    c: Coincident(g13,g14)
    c: Coincident(g14,g15)
    c: Coincident(g15,g16)
    c: Coincident(g16,g17)
    c: Coincident(g17,g18)
    c: Coincident(g18,g19)
    c: Coincident(g19,g20)
    c: Coincident(g20,g21)
    c: Coincident(g21,g22)
    c: Coincident(g22,g23)
    c: Coincident(g23,g0)
    c: Equal(g0, g1-g23) x23
    c: PointOnObject(g0,g24)
    c: PointOnObject(g1,g24)
    c: PointOnObject(g2,g24)
    c: PointOnObject(g3,g24)
    c: PointOnObject(g4,g24)
    c: PointOnObject(g5,g24)
    c: PointOnObject(g6,g24)
    c: PointOnObject(g7,g24)
    c: PointOnObject(g8,g24)
    c: PointOnObject(g9,g24)
    c: PointOnObject(g10,g24)
    c: PointOnObject(g11,g24)
    c: PointOnObject(g12,g24)
    c: PointOnObject(g13,g24)
    c: PointOnObject(g14,g24)
    c: PointOnObject(g15,g24)
    c: PointOnObject(g16,g24)
    c: PointOnObject(g17,g24)
    c: PointOnObject(g18,g24)
    c: PointOnObject(g19,g24)
    c: PointOnObject(g20,g24)
    c: PointOnObject(g21,g24)
    c: PointOnObject(g22,g24)
    c: PointOnObject(g23,g24)
    c: Coincident(g24,g-1)
    c: Horizontal(g23)
    c: DistanceX(g4,g17) = 12
FEATURE [Sketcher::SketchObject] Sketch110
  AttachmentOffset = pos=(0,0,17) rot=(0,0,1;0rad)
  FullyConstrained = false
  MapMode = 5
  Placement = pos=(0,0,17) rot=(0,0,1;0rad)
  Support = -> [XY_Plane041]
  sketch-geometry (25):
    g0: LineSegment StartX=-4.65926 StartY=1.92993 StartZ=0 EndX=-5 EndY=0.658262 EndZ=0
    g1: LineSegment StartX=-5 StartY=0.658262 StartZ=0 EndX=-5 EndY=-0.658262 EndZ=0
    g2: LineSegment StartX=-5 StartY=-0.658262 StartZ=0 EndX=-4.65926 EndY=-1.92993 EndZ=0
    g3: LineSegment StartX=-4.65926 StartY=-1.92993 StartZ=0 EndX=-4.001 EndY=-3.07007 EndZ=0
    g4: LineSegment StartX=-4.001 StartY=-3.07007 StartZ=0 EndX=-3.07007 EndY=-4.001 EndZ=0
    g5: LineSegment StartX=-3.07007 StartY=-4.001 StartZ=0 EndX=-1.92993 EndY=-4.65926 EndZ=0
    g6: LineSegment StartX=-1.92993 StartY=-4.65926 StartZ=0 EndX=-0.658262 EndY=-5 EndZ=0
    g7: LineSegment StartX=-0.658262 StartY=-5 StartZ=0 EndX=0.658262 EndY=-5 EndZ=0
    g8: LineSegment StartX=0.658262 StartY=-5 StartZ=0 EndX=1.92993 EndY=-4.65926 EndZ=0
    g9: LineSegment StartX=1.92993 StartY=-4.65926 StartZ=0 EndX=3.07007 EndY=-4.001 EndZ=0
    g10: LineSegment StartX=3.07007 StartY=-4.001 StartZ=0 EndX=4.001 EndY=-3.07007 EndZ=0
    g11: LineSegment StartX=4.001 StartY=-3.07007 StartZ=0 EndX=4.65926 EndY=-1.92993 EndZ=0
    g12: LineSegment StartX=4.65926 StartY=-1.92993 StartZ=0 EndX=5 EndY=-0.658262 EndZ=0
    g13: LineSegment StartX=5 StartY=-0.658262 StartZ=0 EndX=5 EndY=0.658262 EndZ=0
    g14: LineSegment StartX=5 StartY=0.658262 StartZ=0 EndX=4.65926 EndY=1.92993 EndZ=0
    g15: LineSegment StartX=4.65926 StartY=1.92993 StartZ=0 EndX=4.001 EndY=3.07007 EndZ=0
    g16: LineSegment StartX=4.001 StartY=3.07007 StartZ=0 EndX=3.07007 EndY=4.001 EndZ=0
    g17: LineSegment StartX=3.07007 StartY=4.001 StartZ=0 EndX=1.92993 EndY=4.65926 EndZ=0
    g18: LineSegment StartX=1.92993 StartY=4.65926 StartZ=0 EndX=0.658262 EndY=5 EndZ=0
    g19: LineSegment StartX=0.658262 StartY=5 StartZ=0 EndX=-0.658262 EndY=5 EndZ=0
    g20: LineSegment StartX=-0.658262 StartY=5 StartZ=0 EndX=-1.92993 EndY=4.65926 EndZ=0
    g21: LineSegment StartX=-1.92993 StartY=4.65926 StartZ=0 EndX=-3.07007 EndY=4.001 EndZ=0
    g22: LineSegment StartX=-3.07007 StartY=4.001 StartZ=0 EndX=-4.001 EndY=3.07007 EndZ=0
    g23: LineSegment StartX=-4.001 StartY=3.07007 StartZ=0 EndX=-4.65926 EndY=1.92993 EndZ=0
    g24: Circle CenterX=0 CenterY=0 CenterZ=0 NormalX=0 NormalY=0 NormalZ=1 AngleXU=0 Radius=5.04314
  constraints (52):
    c: Coincident(g0,g1)
    c: Coincident(g1,g2)
    c: Coincident(g2,g3)
    c: Coincident(g3,g4)
    c: Coincident(g4,g5)
    c: Coincident(g5,g6)
    c: Coincident(g6,g7)
    c: Coincident(g7,g8)
    c: Coincident(g8,g9)
    c: Coincident(g9,g10)
    c: Coincident(g10,g11)
    c: Coincident(g11,g12)
    c: Coincident(g12,g13)
    c: Coincident(g13,g14)
    c: Coincident(g14,g15)
    c: Coincident(g15,g16)
    c: Coincident(g16,g17)
    c: Coincident(g17,g18)
    c: Coincident(g18,g19)
    c: Coincident(g19,g20)
    c: Coincident(g20,g21)
    c: Coincident(g21,g22)
    c: Coincident(g22,g23)
    c: Coincident(g23,g0)
    c: Equal(g0, g1-g23) x23
    c: PointOnObject(g0,g24)
    c: PointOnObject(g1,g24)
    c: PointOnObject(g2,g24)
    c: PointOnObject(g3,g24)
    c: PointOnObject(g4,g24)
    c: PointOnObject(g5,g24)
    c: PointOnObject(g6,g24)
    c: PointOnObject(g7,g24)
    c: PointOnObject(g8,g24)
    c: PointOnObject(g9,g24)
    c: PointOnObject(g10,g24)
    c: PointOnObject(g11,g24)
    c: PointOnObject(g12,g24)
    c: PointOnObject(g13,g24)
    c: PointOnObject(g14,g24)
    c: PointOnObject(g15,g24)
    c: PointOnObject(g16,g24)
    c: PointOnObject(g17,g24)
    c: PointOnObject(g18,g24)
    c: PointOnObject(g19,g24)
    c: PointOnObject(g20,g24)
    c: PointOnObject(g21,g24)
    c: PointOnObject(g22,g24)
    c: PointOnObject(g23,g24)
    c: Coincident(g24,g-1)
    c: Horizontal(g19)
    c: DistanceX(g0,g13) = 10
FEATURE [PartDesign::AdditiveLoft] AdditiveLoft009
  AllowMultiFace = false
  Closed = false
  Profile = -> Sketch109
  Refine = true
  Ruled = false
  Sections = -> [Sketch108,Sketch110]
FEATURE [Sketcher::SketchObject] Sketch104
  FullyConstrained = false
  MapMode = 5
  Placement = pos=(0,0,17) rot=(0,0,1;0rad)
  Support = -> [AdditiveLoft009]
  sketch-geometry (1):
    g0: Circle CenterX=0 CenterY=0 CenterZ=0 NormalX=0 NormalY=0 NormalZ=1 AngleXU=0 Radius=4.5
  constraints (2):
    c: Coincident(g0,g-1)
    c: Radius(g0) = 4.5
FEATURE [PartDesign::Pad] Pad024
  AllowMultiFace = false
  BaseFeature = -> AdditiveLoft009
  Direction = (1,1,1)
  Length = 0.7
  Length2 = 100
  Profile = -> Sketch104
  Refine = true
  Type = 0
FEATURE [Sketcher::SketchObject] Sketch103
  FullyConstrained = false
  MapMode = 5
  Placement = pos=(0,0,0) rot=(1,0,0;3.14159rad)
  Support = -> [Pad024]
  sketch-geometry (1):
    g0: Circle CenterX=0 CenterY=0 CenterZ=0 NormalX=0 NormalY=0 NormalZ=1 AngleXU=0 Radius=5
  constraints (2):
    c: Coincident(g0,g-1)
    c: Radius(g0) = 5
FEATURE [PartDesign::Pocket] Pocket040
  AllowMultiFace = false
  BaseFeature = -> Pad024
  Direction = (1,1,1)
  Length = 1
  Length2 = 100
  Profile = -> Sketch103
  Refine = true
  Type = 0
FEATURE [Sketcher::SketchObject] Sketch101
  FullyConstrained = false
  MapMode = 5
  Placement = pos=(0,0,1) rot=(1,0,0;3.14159rad)
  Support = -> [Pocket040]
  sketch-geometry (1):
    g0: Circle CenterX=0 CenterY=0 CenterZ=0 NormalX=0 NormalY=0 NormalZ=1 AngleXU=0 Radius=4.65
  constraints (2):
    c: Coincident(g0,g-1)
    c: Radius(g0) = 4.65
FEATURE [PartDesign::Pocket] Pocket039
  AllowMultiFace = false
  BaseFeature = -> Pocket040
  Direction = (1,1,1)
  Length = 1
  Length2 = 100
  Profile = -> Sketch101
  Refine = true
  Type = 0
FEATURE [Sketcher::SketchObject] Sketch102
  FullyConstrained = false
  MapMode = 5
  Placement = pos=(0,0,2) rot=(1,0,0;3.14159rad)
  Support = -> [Pocket039]
  sketch-geometry (2):
    g0: ArcOfCircle CenterX=0 CenterY=0 CenterZ=0 NormalX=0 NormalY=0 NormalZ=1 AngleXU=0 Radius=3 StartAngle=2.19024 EndAngle=7.23453
    g1: LineSegment StartX=-1.74176 StartY=2.4426 StartZ=0 EndX=1.74176 EndY=2.4426 EndZ=0
  constraints (5):
    c: Coincident(g0,g-1)
    c: Coincident(g1,g0)
    c: Coincident(g1,g0)
    c: Horizontal(g1)
    c: Radius(g0) = 3
FEATURE [Sketcher::SketchObject] Sketch111
  AttachmentOffset = pos=(0,0,17.7) rot=(0,0,1;0rad)
  FullyConstrained = false
  MapMode = 5
  Placement = pos=(0,0,17.7) rot=(0,0,1;0rad)
  Support = -> [XY_Plane042]
  sketch-geometry (10):
    g0: LineSegment StartX=-0.2 StartY=1.5 StartZ=0 EndX=0.2 EndY=1.5 EndZ=0
    g1: LineSegment StartX=0.4 StartY=1.7 StartZ=0 EndX=0.4 EndY=4.2 EndZ=0
    g2: LineSegment StartX=0.2 StartY=4.4 StartZ=0 EndX=-0.2 EndY=4.4 EndZ=0
    g3: LineSegment StartX=-0.4 StartY=4.2 StartZ=0 EndX=-0.4 EndY=1.7 EndZ=0
    g4: ArcOfCircle CenterX=-0.2 CenterY=1.7 CenterZ=0 NormalX=0 NormalY=0 NormalZ=1 AngleXU=0 Radius=0.2 StartAngle=3.14159 EndAngle=4.71239
    g5: ArcOfCircle CenterX=0.2 CenterY=1.7 CenterZ=0 NormalX=0 NormalY=0 NormalZ=1 AngleXU=0 Radius=0.2 StartAngle=4.71239 EndAngle=6.28319
    g6: ArcOfCircle CenterX=0.2 CenterY=4.2 CenterZ=0 NormalX=0 NormalY=0 NormalZ=1 AngleXU=0 Radius=0.2 StartAngle=1.4e-15 EndAngle=1.5708
    g7: ArcOfCircle CenterX=-0.2 CenterY=4.2 CenterZ=0 NormalX=0 NormalY=0 NormalZ=1 AngleXU=0 Radius=0.2 StartAngle=1.5708 EndAngle=3.14159
    g8: LineSegment StartX=-0.2 StartY=1.7 StartZ=0 EndX=0 EndY=0 EndZ=0
    g9: LineSegment StartX=0 StartY=0 StartZ=0 EndX=0.2 EndY=1.7 EndZ=0
  constraints (24):
    c: Horizontal(g0)
    c: Horizontal(g2)
    c: Vertical(g1)
    c: Vertical(g3)
    c: Tangent(g3,g4) = -1.5708
    c: Tangent(g0,g4) = -1.5708
    c: Tangent(g0,g5) = -1.5708
    c: Tangent(g1,g5) = -1.5708
    c: Tangent(g1,g6) = -1.5708
    c: Tangent(g2,g6) = -1.5708
    c: Tangent(g2,g7) = -1.5708
    c: Tangent(g3,g7) = -1.5708
    c: Radius(g7) = 0.2
    c: Equal(g7,g6)
    c: Equal(g7,g5)
    c: Equal(g7,g4)
    c: Coincident(g8,g4)
    c: Coincident(g8,g-1)
    c: Coincident(g9,g-1)
    c: Coincident(g9,g5)
    c: Equal(g9,g8)
    c: DistanceX(g3,g1) = 0.8
    c: DistanceY(g-1,g2) = 4.4
    c: DistanceY(g-1,g0) = 1.5
FEATURE [PartDesign::Pad] Pad027
  AllowMultiFace = false
  Direction = (1,1,1)
  Length = 0.02
  Length2 = 100
  Profile = -> Sketch111
  Refine = true
  Type = 0
FEATURE [PartDesign::Body] Body027  label="Indicator013"
  Group = -> [Sketch111,Pad027]
  Origin = -> Origin045
  Tip = -> Pad027
FEATURE [PartDesign::Pocket] Pocket041
  AllowMultiFace = false
  BaseFeature = -> Pocket039
  Direction = (1,1,1)
  Length = 8
  Length2 = 100
  Profile = -> Sketch102
  Refine = true
  Type = 0
FEATURE [PartDesign::Chamfer] Chamfer029
  Angle = 45
  Base = -> Pocket041 [Edge82,Edge83]
  BaseFeature = -> Pocket041
  ChamferType = 0
  FlipDirection = false
  Size = 1.4
  Size2 = 1
  SupportTransform = false
  UseAllEdges = false
FEATURE [PartDesign::Chamfer] Chamfer028
  Angle = 45
  Base = -> Chamfer029 [Edge8]
  BaseFeature = -> Chamfer029
  ChamferType = 0
  FlipDirection = false
  Size = 0.3
  Size2 = 1
  SupportTransform = false
  UseAllEdges = false
FEATURE [PartDesign::Fillet] Fillet013
  Base = -> Chamfer028 [Edge93,Face36]
  BaseFeature = -> Chamfer028
  Radius = 0.1
  SupportTransform = false
  UseAllEdges = false
FEATURE [PartDesign::Body] Body026
  Group = -> [Sketch109,Sketch108,Sketch110,AdditiveLoft009,Sketch104,Pad024,Sketch103,Pocket040,Sketch101,Pocket039,Sketch102,Pocket041,Chamfer029,Chamfer028,Fillet013]
  Origin = -> Origin031
  Tip = -> Fillet013
FEATURE [App::Part] Part010  label="Cap011"
  Group = -> [Body026,Body027]
  Origin = -> Origin044
  Placement = pos=(-13.335,-13.335,0) rot=(0,0,1;0rad)
  expr: .Placement.Base.x = -13.335
  expr: .Placement.Base.y = -13.335
FEATURE [Sketcher::SketchObject] Sketch116
  AttachmentOffset = pos=(0,0,7) rot=(0,0,1;0rad)
  FullyConstrained = false
  MapMode = 5
  Placement = pos=(0,0,7) rot=(0,0,1;0rad)
  Support = -> [XY_Plane044]
  sketch-geometry (25):
    g0: LineSegment StartX=-0.724089 StartY=5.5 StartZ=0 EndX=-2.12292 EndY=5.12518 EndZ=0
    g1: LineSegment StartX=-2.12292 StartY=5.12518 StartZ=0 EndX=-3.37708 EndY=4.4011 EndZ=0
    g2: LineSegment StartX=-3.37708 StartY=4.4011 StartZ=0 EndX=-4.4011 EndY=3.37708 EndZ=0
    g3: LineSegment StartX=-4.4011 StartY=3.37708 StartZ=0 EndX=-5.12518 EndY=2.12292 EndZ=0
    g4: LineSegment StartX=-5.12518 StartY=2.12292 StartZ=0 EndX=-5.5 EndY=0.724089 EndZ=0
    g5: LineSegment StartX=-5.5 StartY=0.724089 StartZ=0 EndX=-5.5 EndY=-0.724089 EndZ=0
    g6: LineSegment StartX=-5.5 StartY=-0.724089 StartZ=0 EndX=-5.12518 EndY=-2.12292 EndZ=0
    g7: LineSegment StartX=-5.12518 StartY=-2.12292 StartZ=0 EndX=-4.4011 EndY=-3.37708 EndZ=0
    g8: LineSegment StartX=-4.4011 StartY=-3.37708 StartZ=0 EndX=-3.37708 EndY=-4.4011 EndZ=0
    g9: LineSegment StartX=-3.37708 StartY=-4.4011 StartZ=0 EndX=-2.12292 EndY=-5.12518 EndZ=0
    g10: LineSegment StartX=-2.12292 StartY=-5.12518 StartZ=0 EndX=-0.724089 EndY=-5.5 EndZ=0
    g11: LineSegment StartX=-0.724089 StartY=-5.5 StartZ=0 EndX=0.724089 EndY=-5.5 EndZ=0
    g12: LineSegment StartX=0.724089 StartY=-5.5 StartZ=0 EndX=2.12292 EndY=-5.12518 EndZ=0
    g13: LineSegment StartX=2.12292 StartY=-5.12518 StartZ=0 EndX=3.37708 EndY=-4.4011 EndZ=0
    g14: LineSegment StartX=3.37708 StartY=-4.4011 StartZ=0 EndX=4.4011 EndY=-3.37708 EndZ=0
    g15: LineSegment StartX=4.4011 StartY=-3.37708 StartZ=0 EndX=5.12518 EndY=-2.12292 EndZ=0
    g16: LineSegment StartX=5.12518 StartY=-2.12292 StartZ=0 EndX=5.5 EndY=-0.724089 EndZ=0
    g17: LineSegment StartX=5.5 StartY=-0.724089 StartZ=0 EndX=5.5 EndY=0.724089 EndZ=0
    g18: LineSegment StartX=5.5 StartY=0.724089 StartZ=0 EndX=5.12518 EndY=2.12292 EndZ=0
    g19: LineSegment StartX=5.12518 StartY=2.12292 StartZ=0 EndX=4.4011 EndY=3.37708 EndZ=0
    g20: LineSegment StartX=4.4011 StartY=3.37708 StartZ=0 EndX=3.37708 EndY=4.4011 EndZ=0
    g21: LineSegment StartX=3.37708 StartY=4.4011 StartZ=0 EndX=2.12292 EndY=5.12518 EndZ=0
    g22: LineSegment StartX=2.12292 StartY=5.12518 StartZ=0 EndX=0.724089 EndY=5.5 EndZ=0
    g23: LineSegment StartX=0.724089 StartY=5.5 StartZ=0 EndX=-0.724089 EndY=5.5 EndZ=0
    g24: Circle CenterX=0 CenterY=0 CenterZ=0 NormalX=0 NormalY=0 NormalZ=1 AngleXU=0 Radius=5.54746
  constraints (52):
    c: Coincident(g0,g1)
    c: Coincident(g1,g2)
    c: Coincident(g2,g3)
    c: Coincident(g3,g4)
    c: Coincident(g4,g5)
    c: Coincident(g5,g6)
    c: Coincident(g6,g7)
    c: Coincident(g7,g8)
    c: Coincident(g8,g9)
    c: Coincident(g9,g10)
    c: Coincident(g10,g11)
    c: Coincident(g11,g12)
    c: Coincident(g12,g13)
    c: Coincident(g13,g14)
    c: Coincident(g14,g15)
    c: Coincident(g15,g16)
    c: Coincident(g16,g17)
    c: Coincident(g17,g18)
    c: Coincident(g18,g19)
    c: Coincident(g19,g20)
    c: Coincident(g20,g21)
    c: Coincident(g21,g22)
    c: Coincident(g22,g23)
    c: Coincident(g23,g0)
    c: Equal(g0, g1-g23) x23
    c: PointOnObject(g0,g24)
    c: PointOnObject(g1,g24)
    c: PointOnObject(g2,g24)
    c: PointOnObject(g3,g24)
    c: PointOnObject(g4,g24)
    c: PointOnObject(g5,g24)
    c: PointOnObject(g6,g24)
    c: PointOnObject(g7,g24)
    c: PointOnObject(g8,g24)
    c: PointOnObject(g9,g24)
    c: PointOnObject(g10,g24)
    c: PointOnObject(g11,g24)
    c: PointOnObject(g12,g24)
    c: PointOnObject(g13,g24)
    c: PointOnObject(g14,g24)
    c: PointOnObject(g15,g24)
    c: PointOnObject(g16,g24)
    c: PointOnObject(g17,g24)
    c: PointOnObject(g18,g24)
    c: PointOnObject(g19,g24)
    c: PointOnObject(g20,g24)
    c: PointOnObject(g21,g24)
    c: PointOnObject(g22,g24)
    c: PointOnObject(g23,g24)
    c: Coincident(g24,g-1)
    c: Horizontal(g23)
    c: DistanceX(g4,g17) = 11
FEATURE [Sketcher::SketchObject] Sketch117
  FullyConstrained = false
  MapMode = 5
  Support = -> [XY_Plane044]
  sketch-geometry (25):
    g0: LineSegment StartX=-0.789915 StartY=6 StartZ=0 EndX=-2.31591 EndY=5.59111 EndZ=0
    g1: LineSegment StartX=-2.31591 StartY=5.59111 StartZ=0 EndX=-3.68409 EndY=4.80119 EndZ=0
    g2: LineSegment StartX=-3.68409 StartY=4.80119 StartZ=0 EndX=-4.80119 EndY=3.68409 EndZ=0
    g3: LineSegment StartX=-4.80119 StartY=3.68409 StartZ=0 EndX=-5.59111 EndY=2.31591 EndZ=0
    g4: LineSegment StartX=-5.59111 StartY=2.31591 StartZ=0 EndX=-6 EndY=0.789915 EndZ=0
    g5: LineSegment StartX=-6 StartY=0.789915 StartZ=0 EndX=-6 EndY=-0.789915 EndZ=0
    g6: LineSegment StartX=-6 StartY=-0.789915 StartZ=0 EndX=-5.59111 EndY=-2.31591 EndZ=0
    g7: LineSegment StartX=-5.59111 StartY=-2.31591 StartZ=0 EndX=-4.80119 EndY=-3.68409 EndZ=0
    g8: LineSegment StartX=-4.80119 StartY=-3.68409 StartZ=0 EndX=-3.68409 EndY=-4.80119 EndZ=0
    g9: LineSegment StartX=-3.68409 StartY=-4.80119 StartZ=0 EndX=-2.31591 EndY=-5.59111 EndZ=0
    g10: LineSegment StartX=-2.31591 StartY=-5.59111 StartZ=0 EndX=-0.789915 EndY=-6 EndZ=0
    g11: LineSegment StartX=-0.789915 StartY=-6 StartZ=0 EndX=0.789915 EndY=-6 EndZ=0
    g12: LineSegment StartX=0.789915 StartY=-6 StartZ=0 EndX=2.31591 EndY=-5.59111 EndZ=0
    g13: LineSegment StartX=2.31591 StartY=-5.59111 StartZ=0 EndX=3.68409 EndY=-4.80119 EndZ=0
    g14: LineSegment StartX=3.68409 StartY=-4.80119 StartZ=0 EndX=4.80119 EndY=-3.68409 EndZ=0
    g15: LineSegment StartX=4.80119 StartY=-3.68409 StartZ=0 EndX=5.59111 EndY=-2.31591 EndZ=0
    g16: LineSegment StartX=5.59111 StartY=-2.31591 StartZ=0 EndX=6 EndY=-0.789915 EndZ=0
    g17: LineSegment StartX=6 StartY=-0.789915 StartZ=0 EndX=6 EndY=0.789915 EndZ=0
    g18: LineSegment StartX=6 StartY=0.789915 StartZ=0 EndX=5.59111 EndY=2.31591 EndZ=0
    g19: LineSegment StartX=5.59111 StartY=2.31591 StartZ=0 EndX=4.80119 EndY=3.68409 EndZ=0
    g20: LineSegment StartX=4.80119 StartY=3.68409 StartZ=0 EndX=3.68409 EndY=4.80119 EndZ=0
    g21: LineSegment StartX=3.68409 StartY=4.80119 StartZ=0 EndX=2.31591 EndY=5.59111 EndZ=0
    g22: LineSegment StartX=2.31591 StartY=5.59111 StartZ=0 EndX=0.789915 EndY=6 EndZ=0
    g23: LineSegment StartX=0.789915 StartY=6 StartZ=0 EndX=-0.789915 EndY=6 EndZ=0
    g24: Circle CenterX=0 CenterY=0 CenterZ=0 NormalX=0 NormalY=0 NormalZ=1 AngleXU=0 Radius=6.05177
  constraints (52):
    c: Coincident(g0,g1)
    c: Coincident(g1,g2)
    c: Coincident(g2,g3)
    c: Coincident(g3,g4)
    c: Coincident(g4,g5)
    c: Coincident(g5,g6)
    c: Coincident(g6,g7)
    c: Coincident(g7,g8)
    c: Coincident(g8,g9)
    c: Coincident(g9,g10)
    c: Coincident(g10,g11)
    c: Coincident(g11,g12)
    c: Coincident(g12,g13)
    c: Coincident(g13,g14)
    c: Coincident(g14,g15)
    c: Coincident(g15,g16)
    c: Coincident(g16,g17)
    c: Coincident(g17,g18)
    c: Coincident(g18,g19)
    c: Coincident(g19,g20)
    c: Coincident(g20,g21)
    c: Coincident(g21,g22)
    c: Coincident(g22,g23)
    c: Coincident(g23,g0)
    c: Equal(g0, g1-g23) x23
    c: PointOnObject(g0,g24)
    c: PointOnObject(g1,g24)
    c: PointOnObject(g2,g24)
    c: PointOnObject(g3,g24)
    c: PointOnObject(g4,g24)
    c: PointOnObject(g5,g24)
    c: PointOnObject(g6,g24)
    c: PointOnObject(g7,g24)
    c: PointOnObject(g8,g24)
    c: PointOnObject(g9,g24)
    c: PointOnObject(g10,g24)
    c: PointOnObject(g11,g24)
    c: PointOnObject(g12,g24)
    c: PointOnObject(g13,g24)
    c: PointOnObject(g14,g24)
    c: PointOnObject(g15,g24)
    c: PointOnObject(g16,g24)
    c: PointOnObject(g17,g24)
    c: PointOnObject(g18,g24)
    c: PointOnObject(g19,g24)
    c: PointOnObject(g20,g24)
    c: PointOnObject(g21,g24)
    c: PointOnObject(g22,g24)
    c: PointOnObject(g23,g24)
    c: Coincident(g24,g-1)
    c: Horizontal(g23)
    c: DistanceX(g4,g17) = 12
FEATURE [Sketcher::SketchObject] Sketch118
  AttachmentOffset = pos=(0,0,17) rot=(0,0,1;0rad)
  FullyConstrained = false
  MapMode = 5
  Placement = pos=(0,0,17) rot=(0,0,1;0rad)
  Support = -> [XY_Plane044]
  sketch-geometry (25):
    g0: LineSegment StartX=-4.65926 StartY=1.92993 StartZ=0 EndX=-5 EndY=0.658262 EndZ=0
    g1: LineSegment StartX=-5 StartY=0.658262 StartZ=0 EndX=-5 EndY=-0.658262 EndZ=0
    g2: LineSegment StartX=-5 StartY=-0.658262 StartZ=0 EndX=-4.65926 EndY=-1.92993 EndZ=0
    g3: LineSegment StartX=-4.65926 StartY=-1.92993 StartZ=0 EndX=-4.001 EndY=-3.07007 EndZ=0
    g4: LineSegment StartX=-4.001 StartY=-3.07007 StartZ=0 EndX=-3.07007 EndY=-4.001 EndZ=0
    g5: LineSegment StartX=-3.07007 StartY=-4.001 StartZ=0 EndX=-1.92993 EndY=-4.65926 EndZ=0
    g6: LineSegment StartX=-1.92993 StartY=-4.65926 StartZ=0 EndX=-0.658262 EndY=-5 EndZ=0
    g7: LineSegment StartX=-0.658262 StartY=-5 StartZ=0 EndX=0.658262 EndY=-5 EndZ=0
    g8: LineSegment StartX=0.658262 StartY=-5 StartZ=0 EndX=1.92993 EndY=-4.65926 EndZ=0
    g9: LineSegment StartX=1.92993 StartY=-4.65926 StartZ=0 EndX=3.07007 EndY=-4.001 EndZ=0
    g10: LineSegment StartX=3.07007 StartY=-4.001 StartZ=0 EndX=4.001 EndY=-3.07007 EndZ=0
    g11: LineSegment StartX=4.001 StartY=-3.07007 StartZ=0 EndX=4.65926 EndY=-1.92993 EndZ=0
    g12: LineSegment StartX=4.65926 StartY=-1.92993 StartZ=0 EndX=5 EndY=-0.658262 EndZ=0
    g13: LineSegment StartX=5 StartY=-0.658262 StartZ=0 EndX=5 EndY=0.658262 EndZ=0
    g14: LineSegment StartX=5 StartY=0.658262 StartZ=0 EndX=4.65926 EndY=1.92993 EndZ=0
    g15: LineSegment StartX=4.65926 StartY=1.92993 StartZ=0 EndX=4.001 EndY=3.07007 EndZ=0
    g16: LineSegment StartX=4.001 StartY=3.07007 StartZ=0 EndX=3.07007 EndY=4.001 EndZ=0
    g17: LineSegment StartX=3.07007 StartY=4.001 StartZ=0 EndX=1.92993 EndY=4.65926 EndZ=0
    g18: LineSegment StartX=1.92993 StartY=4.65926 StartZ=0 EndX=0.658262 EndY=5 EndZ=0
    g19: LineSegment StartX=0.658262 StartY=5 StartZ=0 EndX=-0.658262 EndY=5 EndZ=0
    g20: LineSegment StartX=-0.658262 StartY=5 StartZ=0 EndX=-1.92993 EndY=4.65926 EndZ=0
    g21: LineSegment StartX=-1.92993 StartY=4.65926 StartZ=0 EndX=-3.07007 EndY=4.001 EndZ=0
    g22: LineSegment StartX=-3.07007 StartY=4.001 StartZ=0 EndX=-4.001 EndY=3.07007 EndZ=0
    g23: LineSegment StartX=-4.001 StartY=3.07007 StartZ=0 EndX=-4.65926 EndY=1.92993 EndZ=0
    g24: Circle CenterX=0 CenterY=0 CenterZ=0 NormalX=0 NormalY=0 NormalZ=1 AngleXU=0 Radius=5.04314
  constraints (52):
    c: Coincident(g0,g1)
    c: Coincident(g1,g2)
    c: Coincident(g2,g3)
    c: Coincident(g3,g4)
    c: Coincident(g4,g5)
    c: Coincident(g5,g6)
    c: Coincident(g6,g7)
    c: Coincident(g7,g8)
    c: Coincident(g8,g9)
    c: Coincident(g9,g10)
    c: Coincident(g10,g11)
    c: Coincident(g11,g12)
    c: Coincident(g12,g13)
    c: Coincident(g13,g14)
    c: Coincident(g14,g15)
    c: Coincident(g15,g16)
    c: Coincident(g16,g17)
    c: Coincident(g17,g18)
    c: Coincident(g18,g19)
    c: Coincident(g19,g20)
    c: Coincident(g20,g21)
    c: Coincident(g21,g22)
    c: Coincident(g22,g23)
    c: Coincident(g23,g0)
    c: Equal(g0, g1-g23) x23
    c: PointOnObject(g0,g24)
    c: PointOnObject(g1,g24)
    c: PointOnObject(g2,g24)
    c: PointOnObject(g3,g24)
    c: PointOnObject(g4,g24)
    c: PointOnObject(g5,g24)
    c: PointOnObject(g6,g24)
    c: PointOnObject(g7,g24)
    c: PointOnObject(g8,g24)
    c: PointOnObject(g9,g24)
    c: PointOnObject(g10,g24)
    c: PointOnObject(g11,g24)
    c: PointOnObject(g12,g24)
    c: PointOnObject(g13,g24)
    c: PointOnObject(g14,g24)
    c: PointOnObject(g15,g24)
    c: PointOnObject(g16,g24)
    c: PointOnObject(g17,g24)
    c: PointOnObject(g18,g24)
    c: PointOnObject(g19,g24)
    c: PointOnObject(g20,g24)
    c: PointOnObject(g21,g24)
    c: PointOnObject(g22,g24)
    c: PointOnObject(g23,g24)
    c: Coincident(g24,g-1)
    c: Horizontal(g19)
    c: DistanceX(g0,g13) = 10
FEATURE [PartDesign::AdditiveLoft] AdditiveLoft013
  AllowMultiFace = false
  Closed = false
  Profile = -> Sketch117
  Refine = true
  Ruled = false
  Sections = -> [Sketch116,Sketch118]
FEATURE [Sketcher::SketchObject] Sketch115
  FullyConstrained = false
  MapMode = 5
  Placement = pos=(0,0,17) rot=(0,0,1;0rad)
  Support = -> [AdditiveLoft013]
  sketch-geometry (1):
    g0: Circle CenterX=0 CenterY=0 CenterZ=0 NormalX=0 NormalY=0 NormalZ=1 AngleXU=0 Radius=4.5
  constraints (2):
    c: Coincident(g0,g-1)
    c: Radius(g0) = 4.5
FEATURE [PartDesign::Pad] Pad028
  AllowMultiFace = false
  BaseFeature = -> AdditiveLoft013
  Direction = (1,1,1)
  Length = 0.7
  Length2 = 100
  Profile = -> Sketch115
  Refine = true
  Type = 0
FEATURE [Sketcher::SketchObject] Sketch114
  FullyConstrained = false
  MapMode = 5
  Placement = pos=(0,0,0) rot=(1,0,0;3.14159rad)
  Support = -> [Pad028]
  sketch-geometry (1):
    g0: Circle CenterX=0 CenterY=0 CenterZ=0 NormalX=0 NormalY=0 NormalZ=1 AngleXU=0 Radius=5
  constraints (2):
    c: Coincident(g0,g-1)
    c: Radius(g0) = 5
FEATURE [PartDesign::Pocket] Pocket043
  AllowMultiFace = false
  BaseFeature = -> Pad028
  Direction = (1,1,1)
  Length = 1
  Length2 = 100
  Profile = -> Sketch114
  Refine = true
  Type = 0
FEATURE [Sketcher::SketchObject] Sketch112
  FullyConstrained = false
  MapMode = 5
  Placement = pos=(0,0,1) rot=(1,0,0;3.14159rad)
  Support = -> [Pocket043]
  sketch-geometry (1):
    g0: Circle CenterX=0 CenterY=0 CenterZ=0 NormalX=0 NormalY=0 NormalZ=1 AngleXU=0 Radius=4.65
  constraints (2):
    c: Coincident(g0,g-1)
    c: Radius(g0) = 4.65
FEATURE [PartDesign::Pocket] Pocket042
  AllowMultiFace = false
  BaseFeature = -> Pocket043
  Direction = (1,1,1)
  Length = 1
  Length2 = 100
  Profile = -> Sketch112
  Refine = true
  Type = 0
FEATURE [Sketcher::SketchObject] Sketch113
  FullyConstrained = false
  MapMode = 5
  Placement = pos=(0,0,2) rot=(1,0,0;3.14159rad)
  Support = -> [Pocket042]
  sketch-geometry (2):
    g0: ArcOfCircle CenterX=0 CenterY=0 CenterZ=0 NormalX=0 NormalY=0 NormalZ=1 AngleXU=0 Radius=3 StartAngle=2.19024 EndAngle=7.23453
    g1: LineSegment StartX=-1.74176 StartY=2.4426 StartZ=0 EndX=1.74176 EndY=2.4426 EndZ=0
  constraints (5):
    c: Coincident(g0,g-1)
    c: Coincident(g1,g0)
    c: Coincident(g1,g0)
    c: Horizontal(g1)
    c: Radius(g0) = 3
FEATURE [PartDesign::Pocket] Pocket044
  AllowMultiFace = false
  BaseFeature = -> Pocket042
  Direction = (1,1,1)
  Length = 8
  Length2 = 100
  Profile = -> Sketch113
  Refine = true
  Type = 0
FEATURE [PartDesign::Chamfer] Chamfer031
  Angle = 45
  Base = -> Pocket044 [Edge82,Edge83]
  BaseFeature = -> Pocket044
  ChamferType = 0
  FlipDirection = false
  Size = 1.4
  Size2 = 1
  SupportTransform = false
  UseAllEdges = false
FEATURE [PartDesign::Chamfer] Chamfer027
  Angle = 45
  Base = -> Chamfer031 [Edge8]
  BaseFeature = -> Chamfer031
  ChamferType = 0
  FlipDirection = false
  Size = 0.3
  Size2 = 1
  SupportTransform = false
  UseAllEdges = false
FEATURE [PartDesign::Fillet] Fillet015
  Base = -> Chamfer027 [Edge93,Face36]
  BaseFeature = -> Chamfer027
  Radius = 0.1
  SupportTransform = false
  UseAllEdges = false
FEATURE [Sketcher::SketchObject] Sketch119
  AttachmentOffset = pos=(0,0,17.7) rot=(0,0,1;0rad)
  FullyConstrained = false
  MapMode = 5
  Placement = pos=(0,0,17.7) rot=(0,0,1;0rad)
  Support = -> [XY_Plane045]
  sketch-geometry (10):
    g0: LineSegment StartX=-0.2 StartY=1.5 StartZ=0 EndX=0.2 EndY=1.5 EndZ=0
    g1: LineSegment StartX=0.4 StartY=1.7 StartZ=0 EndX=0.4 EndY=4.2 EndZ=0
    g2: LineSegment StartX=0.2 StartY=4.4 StartZ=0 EndX=-0.2 EndY=4.4 EndZ=0
    g3: LineSegment StartX=-0.4 StartY=4.2 StartZ=0 EndX=-0.4 EndY=1.7 EndZ=0
    g4: ArcOfCircle CenterX=-0.2 CenterY=1.7 CenterZ=0 NormalX=0 NormalY=0 NormalZ=1 AngleXU=0 Radius=0.2 StartAngle=3.14159 EndAngle=4.71239
    g5: ArcOfCircle CenterX=0.2 CenterY=1.7 CenterZ=0 NormalX=0 NormalY=0 NormalZ=1 AngleXU=0 Radius=0.2 StartAngle=4.71239 EndAngle=6.28319
    g6: ArcOfCircle CenterX=0.2 CenterY=4.2 CenterZ=0 NormalX=0 NormalY=0 NormalZ=1 AngleXU=0 Radius=0.2 StartAngle=1.4e-15 EndAngle=1.5708
    g7: ArcOfCircle CenterX=-0.2 CenterY=4.2 CenterZ=0 NormalX=0 NormalY=0 NormalZ=1 AngleXU=0 Radius=0.2 StartAngle=1.5708 EndAngle=3.14159
    g8: LineSegment StartX=-0.2 StartY=1.7 StartZ=0 EndX=0 EndY=0 EndZ=0
    g9: LineSegment StartX=0 StartY=0 StartZ=0 EndX=0.2 EndY=1.7 EndZ=0
  constraints (24):
    c: Horizontal(g0)
    c: Horizontal(g2)
    c: Vertical(g1)
    c: Vertical(g3)
    c: Tangent(g3,g4) = -1.5708
    c: Tangent(g0,g4) = -1.5708
    c: Tangent(g0,g5) = -1.5708
    c: Tangent(g1,g5) = -1.5708
    c: Tangent(g1,g6) = -1.5708
    c: Tangent(g2,g6) = -1.5708
    c: Tangent(g2,g7) = -1.5708
    c: Tangent(g3,g7) = -1.5708
    c: Radius(g7) = 0.2
    c: Equal(g7,g6)
    c: Equal(g7,g5)
    c: Equal(g7,g4)
    c: Coincident(g8,g4)
    c: Coincident(g8,g-1)
    c: Coincident(g9,g-1)
    c: Coincident(g9,g5)
    c: Equal(g9,g8)
    c: DistanceX(g3,g1) = 0.8
    c: DistanceY(g-1,g2) = 4.4
    c: DistanceY(g-1,g0) = 1.5
FEATURE [PartDesign::Pad] Pad029
  AllowMultiFace = false
  Direction = (1,1,1)
  Length = 0.02
  Length2 = 100
  Profile = -> Sketch119
  Refine = true
  Type = 0
FEATURE [Sketcher::SketchObject] Sketch124
  AttachmentOffset = pos=(0,0,7) rot=(0,0,1;0rad)
  FullyConstrained = false
  MapMode = 5
  Placement = pos=(0,0,7) rot=(0,0,1;0rad)
  Support = -> [XY_Plane047]
  sketch-geometry (25):
    g0: LineSegment StartX=-0.724089 StartY=5.5 StartZ=0 EndX=-2.12292 EndY=5.12518 EndZ=0
    g1: LineSegment StartX=-2.12292 StartY=5.12518 StartZ=0 EndX=-3.37708 EndY=4.4011 EndZ=0
    g2: LineSegment StartX=-3.37708 StartY=4.4011 StartZ=0 EndX=-4.4011 EndY=3.37708 EndZ=0
    g3: LineSegment StartX=-4.4011 StartY=3.37708 StartZ=0 EndX=-5.12518 EndY=2.12292 EndZ=0
    g4: LineSegment StartX=-5.12518 StartY=2.12292 StartZ=0 EndX=-5.5 EndY=0.724089 EndZ=0
    g5: LineSegment StartX=-5.5 StartY=0.724089 StartZ=0 EndX=-5.5 EndY=-0.724089 EndZ=0
    g6: LineSegment StartX=-5.5 StartY=-0.724089 StartZ=0 EndX=-5.12518 EndY=-2.12292 EndZ=0
    g7: LineSegment StartX=-5.12518 StartY=-2.12292 StartZ=0 EndX=-4.4011 EndY=-3.37708 EndZ=0
    g8: LineSegment StartX=-4.4011 StartY=-3.37708 StartZ=0 EndX=-3.37708 EndY=-4.4011 EndZ=0
    g9: LineSegment StartX=-3.37708 StartY=-4.4011 StartZ=0 EndX=-2.12292 EndY=-5.12518 EndZ=0
    g10: LineSegment StartX=-2.12292 StartY=-5.12518 StartZ=0 EndX=-0.724089 EndY=-5.5 EndZ=0
    g11: LineSegment StartX=-0.724089 StartY=-5.5 StartZ=0 EndX=0.724089 EndY=-5.5 EndZ=0
    g12: LineSegment StartX=0.724089 StartY=-5.5 StartZ=0 EndX=2.12292 EndY=-5.12518 EndZ=0
    g13: LineSegment StartX=2.12292 StartY=-5.12518 StartZ=0 EndX=3.37708 EndY=-4.4011 EndZ=0
    g14: LineSegment StartX=3.37708 StartY=-4.4011 StartZ=0 EndX=4.4011 EndY=-3.37708 EndZ=0
    g15: LineSegment StartX=4.4011 StartY=-3.37708 StartZ=0 EndX=5.12518 EndY=-2.12292 EndZ=0
    g16: LineSegment StartX=5.12518 StartY=-2.12292 StartZ=0 EndX=5.5 EndY=-0.724089 EndZ=0
    g17: LineSegment StartX=5.5 StartY=-0.724089 StartZ=0 EndX=5.5 EndY=0.724089 EndZ=0
    g18: LineSegment StartX=5.5 StartY=0.724089 StartZ=0 EndX=5.12518 EndY=2.12292 EndZ=0
    g19: LineSegment StartX=5.12518 StartY=2.12292 StartZ=0 EndX=4.4011 EndY=3.37708 EndZ=0
    g20: LineSegment StartX=4.4011 StartY=3.37708 StartZ=0 EndX=3.37708 EndY=4.4011 EndZ=0
    g21: LineSegment StartX=3.37708 StartY=4.4011 StartZ=0 EndX=2.12292 EndY=5.12518 EndZ=0
    g22: LineSegment StartX=2.12292 StartY=5.12518 StartZ=0 EndX=0.724089 EndY=5.5 EndZ=0
    g23: LineSegment StartX=0.724089 StartY=5.5 StartZ=0 EndX=-0.724089 EndY=5.5 EndZ=0
    g24: Circle CenterX=0 CenterY=0 CenterZ=0 NormalX=0 NormalY=0 NormalZ=1 AngleXU=0 Radius=5.54746
  constraints (52):
    c: Coincident(g0,g1)
    c: Coincident(g1,g2)
    c: Coincident(g2,g3)
    c: Coincident(g3,g4)
    c: Coincident(g4,g5)
    c: Coincident(g5,g6)
    c: Coincident(g6,g7)
    c: Coincident(g7,g8)
    c: Coincident(g8,g9)
    c: Coincident(g9,g10)
    c: Coincident(g10,g11)
    c: Coincident(g11,g12)
    c: Coincident(g12,g13)
    c: Coincident(g13,g14)
    c: Coincident(g14,g15)
    c: Coincident(g15,g16)
    c: Coincident(g16,g17)
    c: Coincident(g17,g18)
    c: Coincident(g18,g19)
    c: Coincident(g19,g20)
    c: Coincident(g20,g21)
    c: Coincident(g21,g22)
    c: Coincident(g22,g23)
    c: Coincident(g23,g0)
    c: Equal(g0, g1-g23) x23
    c: PointOnObject(g0,g24)
    c: PointOnObject(g1,g24)
    c: PointOnObject(g2,g24)
    c: PointOnObject(g3,g24)
    c: PointOnObject(g4,g24)
    c: PointOnObject(g5,g24)
    c: PointOnObject(g6,g24)
    c: PointOnObject(g7,g24)
    c: PointOnObject(g8,g24)
    c: PointOnObject(g9,g24)
    c: PointOnObject(g10,g24)
    c: PointOnObject(g11,g24)
    c: PointOnObject(g12,g24)
    c: PointOnObject(g13,g24)
    c: PointOnObject(g14,g24)
    c: PointOnObject(g15,g24)
    c: PointOnObject(g16,g24)
    c: PointOnObject(g17,g24)
    c: PointOnObject(g18,g24)
    c: PointOnObject(g19,g24)
    c: PointOnObject(g20,g24)
    c: PointOnObject(g21,g24)
    c: PointOnObject(g22,g24)
    c: PointOnObject(g23,g24)
    c: Coincident(g24,g-1)
    c: Horizontal(g23)
    c: DistanceX(g4,g17) = 11
FEATURE [Sketcher::SketchObject] Sketch125
  FullyConstrained = false
  MapMode = 5
  Support = -> [XY_Plane047]
  sketch-geometry (25):
    g0: LineSegment StartX=-0.789915 StartY=6 StartZ=0 EndX=-2.31591 EndY=5.59111 EndZ=0
    g1: LineSegment StartX=-2.31591 StartY=5.59111 StartZ=0 EndX=-3.68409 EndY=4.80119 EndZ=0
    g2: LineSegment StartX=-3.68409 StartY=4.80119 StartZ=0 EndX=-4.80119 EndY=3.68409 EndZ=0
    g3: LineSegment StartX=-4.80119 StartY=3.68409 StartZ=0 EndX=-5.59111 EndY=2.31591 EndZ=0
    g4: LineSegment StartX=-5.59111 StartY=2.31591 StartZ=0 EndX=-6 EndY=0.789915 EndZ=0
    g5: LineSegment StartX=-6 StartY=0.789915 StartZ=0 EndX=-6 EndY=-0.789915 EndZ=0
    g6: LineSegment StartX=-6 StartY=-0.789915 StartZ=0 EndX=-5.59111 EndY=-2.31591 EndZ=0
    g7: LineSegment StartX=-5.59111 StartY=-2.31591 StartZ=0 EndX=-4.80119 EndY=-3.68409 EndZ=0
    g8: LineSegment StartX=-4.80119 StartY=-3.68409 StartZ=0 EndX=-3.68409 EndY=-4.80119 EndZ=0
    g9: LineSegment StartX=-3.68409 StartY=-4.80119 StartZ=0 EndX=-2.31591 EndY=-5.59111 EndZ=0
    g10: LineSegment StartX=-2.31591 StartY=-5.59111 StartZ=0 EndX=-0.789915 EndY=-6 EndZ=0
    g11: LineSegment StartX=-0.789915 StartY=-6 StartZ=0 EndX=0.789915 EndY=-6 EndZ=0
    g12: LineSegment StartX=0.789915 StartY=-6 StartZ=0 EndX=2.31591 EndY=-5.59111 EndZ=0
    g13: LineSegment StartX=2.31591 StartY=-5.59111 StartZ=0 EndX=3.68409 EndY=-4.80119 EndZ=0
    g14: LineSegment StartX=3.68409 StartY=-4.80119 StartZ=0 EndX=4.80119 EndY=-3.68409 EndZ=0
    g15: LineSegment StartX=4.80119 StartY=-3.68409 StartZ=0 EndX=5.59111 EndY=-2.31591 EndZ=0
    g16: LineSegment StartX=5.59111 StartY=-2.31591 StartZ=0 EndX=6 EndY=-0.789915 EndZ=0
    g17: LineSegment StartX=6 StartY=-0.789915 StartZ=0 EndX=6 EndY=0.789915 EndZ=0
    g18: LineSegment StartX=6 StartY=0.789915 StartZ=0 EndX=5.59111 EndY=2.31591 EndZ=0
    g19: LineSegment StartX=5.59111 StartY=2.31591 StartZ=0 EndX=4.80119 EndY=3.68409 EndZ=0
    g20: LineSegment StartX=4.80119 StartY=3.68409 StartZ=0 EndX=3.68409 EndY=4.80119 EndZ=0
    g21: LineSegment StartX=3.68409 StartY=4.80119 StartZ=0 EndX=2.31591 EndY=5.59111 EndZ=0
    g22: LineSegment StartX=2.31591 StartY=5.59111 StartZ=0 EndX=0.789915 EndY=6 EndZ=0
    g23: LineSegment StartX=0.789915 StartY=6 StartZ=0 EndX=-0.789915 EndY=6 EndZ=0
    g24: Circle CenterX=0 CenterY=0 CenterZ=0 NormalX=0 NormalY=0 NormalZ=1 AngleXU=0 Radius=6.05177
  constraints (52):
    c: Coincident(g0,g1)
    c: Coincident(g1,g2)
    c: Coincident(g2,g3)
    c: Coincident(g3,g4)
    c: Coincident(g4,g5)
    c: Coincident(g5,g6)
    c: Coincident(g6,g7)
    c: Coincident(g7,g8)
    c: Coincident(g8,g9)
    c: Coincident(g9,g10)
    c: Coincident(g10,g11)
    c: Coincident(g11,g12)
    c: Coincident(g12,g13)
    c: Coincident(g13,g14)
    c: Coincident(g14,g15)
    c: Coincident(g15,g16)
    c: Coincident(g16,g17)
    c: Coincident(g17,g18)
    c: Coincident(g18,g19)
    c: Coincident(g19,g20)
    c: Coincident(g20,g21)
    c: Coincident(g21,g22)
    c: Coincident(g22,g23)
    c: Coincident(g23,g0)
    c: Equal(g0, g1-g23) x23
    c: PointOnObject(g0,g24)
    c: PointOnObject(g1,g24)
    c: PointOnObject(g2,g24)
    c: PointOnObject(g3,g24)
    c: PointOnObject(g4,g24)
    c: PointOnObject(g5,g24)
    c: PointOnObject(g6,g24)
    c: PointOnObject(g7,g24)
    c: PointOnObject(g8,g24)
    c: PointOnObject(g9,g24)
    c: PointOnObject(g10,g24)
    c: PointOnObject(g11,g24)
    c: PointOnObject(g12,g24)
    c: PointOnObject(g13,g24)
    c: PointOnObject(g14,g24)
    c: PointOnObject(g15,g24)
    c: PointOnObject(g16,g24)
    c: PointOnObject(g17,g24)
    c: PointOnObject(g18,g24)
    c: PointOnObject(g19,g24)
    c: PointOnObject(g20,g24)
    c: PointOnObject(g21,g24)
    c: PointOnObject(g22,g24)
    c: PointOnObject(g23,g24)
    c: Coincident(g24,g-1)
    c: Horizontal(g23)
    c: DistanceX(g4,g17) = 12
FEATURE [PartDesign::Body] Body028
  Group = -> [Sketch117,Sketch116,Sketch118,AdditiveLoft013,Sketch115,Pad028,Sketch114,Pocket043,Sketch112,Pocket042,Sketch113,Pocket044,Chamfer031,Chamfer027,Fillet015]
  Origin = -> Origin035
  Tip = -> Fillet015
FEATURE [PartDesign::Body] Body029  label="Indicator014"
  Group = -> [Sketch119,Pad029]
  Origin = -> Origin037
  Tip = -> Pad029
FEATURE [App::Part] Part009  label="Cap010"
  Group = -> [Body028,Body029]
  Origin = -> Origin038
  Placement = pos=(13.335,-13.335,0) rot=(0,0,1;0rad)
  expr: .Placement.Base.x = 13.335
  expr: .Placement.Base.y = -13.335
FEATURE [Sketcher::SketchObject] Sketch126
  AttachmentOffset = pos=(0,0,17) rot=(0,0,1;0rad)
  FullyConstrained = false
  MapMode = 5
  Placement = pos=(0,0,17) rot=(0,0,1;0rad)
  Support = -> [XY_Plane047]
  sketch-geometry (25):
    g0: LineSegment StartX=-4.65926 StartY=1.92993 StartZ=0 EndX=-5 EndY=0.658262 EndZ=0
    g1: LineSegment StartX=-5 StartY=0.658262 StartZ=0 EndX=-5 EndY=-0.658262 EndZ=0
    g2: LineSegment StartX=-5 StartY=-0.658262 StartZ=0 EndX=-4.65926 EndY=-1.92993 EndZ=0
    g3: LineSegment StartX=-4.65926 StartY=-1.92993 StartZ=0 EndX=-4.001 EndY=-3.07007 EndZ=0
    g4: LineSegment StartX=-4.001 StartY=-3.07007 StartZ=0 EndX=-3.07007 EndY=-4.001 EndZ=0
    g5: LineSegment StartX=-3.07007 StartY=-4.001 StartZ=0 EndX=-1.92993 EndY=-4.65926 EndZ=0
    g6: LineSegment StartX=-1.92993 StartY=-4.65926 StartZ=0 EndX=-0.658262 EndY=-5 EndZ=0
    g7: LineSegment StartX=-0.658262 StartY=-5 StartZ=0 EndX=0.658262 EndY=-5 EndZ=0
    g8: LineSegment StartX=0.658262 StartY=-5 StartZ=0 EndX=1.92993 EndY=-4.65926 EndZ=0
    g9: LineSegment StartX=1.92993 StartY=-4.65926 StartZ=0 EndX=3.07007 EndY=-4.001 EndZ=0
    g10: LineSegment StartX=3.07007 StartY=-4.001 StartZ=0 EndX=4.001 EndY=-3.07007 EndZ=0
    g11: LineSegment StartX=4.001 StartY=-3.07007 StartZ=0 EndX=4.65926 EndY=-1.92993 EndZ=0
    g12: LineSegment StartX=4.65926 StartY=-1.92993 StartZ=0 EndX=5 EndY=-0.658262 EndZ=0
    g13: LineSegment StartX=5 StartY=-0.658262 StartZ=0 EndX=5 EndY=0.658262 EndZ=0
    g14: LineSegment StartX=5 StartY=0.658262 StartZ=0 EndX=4.65926 EndY=1.92993 EndZ=0
    g15: LineSegment StartX=4.65926 StartY=1.92993 StartZ=0 EndX=4.001 EndY=3.07007 EndZ=0
    g16: LineSegment StartX=4.001 StartY=3.07007 StartZ=0 EndX=3.07007 EndY=4.001 EndZ=0
    g17: LineSegment StartX=3.07007 StartY=4.001 StartZ=0 EndX=1.92993 EndY=4.65926 EndZ=0
    g18: LineSegment StartX=1.92993 StartY=4.65926 StartZ=0 EndX=0.658262 EndY=5 EndZ=0
    g19: LineSegment StartX=0.658262 StartY=5 StartZ=0 EndX=-0.658262 EndY=5 EndZ=0
    g20: LineSegment StartX=-0.658262 StartY=5 StartZ=0 EndX=-1.92993 EndY=4.65926 EndZ=0
    g21: LineSegment StartX=-1.92993 StartY=4.65926 StartZ=0 EndX=-3.07007 EndY=4.001 EndZ=0
    g22: LineSegment StartX=-3.07007 StartY=4.001 StartZ=0 EndX=-4.001 EndY=3.07007 EndZ=0
    g23: LineSegment StartX=-4.001 StartY=3.07007 StartZ=0 EndX=-4.65926 EndY=1.92993 EndZ=0
    g24: Circle CenterX=0 CenterY=0 CenterZ=0 NormalX=0 NormalY=0 NormalZ=1 AngleXU=0 Radius=5.04314
  constraints (52):
    c: Coincident(g0,g1)
    c: Coincident(g1,g2)
    c: Coincident(g2,g3)
    c: Coincident(g3,g4)
    c: Coincident(g4,g5)
    c: Coincident(g5,g6)
    c: Coincident(g6,g7)
    c: Coincident(g7,g8)
    c: Coincident(g8,g9)
    c: Coincident(g9,g10)
    c: Coincident(g10,g11)
    c: Coincident(g11,g12)
    c: Coincident(g12,g13)
    c: Coincident(g13,g14)
    c: Coincident(g14,g15)
    c: Coincident(g15,g16)
    c: Coincident(g16,g17)
    c: Coincident(g17,g18)
    c: Coincident(g18,g19)
    c: Coincident(g19,g20)
    c: Coincident(g20,g21)
    c: Coincident(g21,g22)
    c: Coincident(g22,g23)
    c: Coincident(g23,g0)
    c: Equal(g0, g1-g23) x23
    c: PointOnObject(g0,g24)
    c: PointOnObject(g1,g24)
    c: PointOnObject(g2,g24)
    c: PointOnObject(g3,g24)
    c: PointOnObject(g4,g24)
    c: PointOnObject(g5,g24)
    c: PointOnObject(g6,g24)
    c: PointOnObject(g7,g24)
    c: PointOnObject(g8,g24)
    c: PointOnObject(g9,g24)
    c: PointOnObject(g10,g24)
    c: PointOnObject(g11,g24)
    c: PointOnObject(g12,g24)
    c: PointOnObject(g13,g24)
    c: PointOnObject(g14,g24)
    c: PointOnObject(g15,g24)
    c: PointOnObject(g16,g24)
    c: PointOnObject(g17,g24)
    c: PointOnObject(g18,g24)
    c: PointOnObject(g19,g24)
    c: PointOnObject(g20,g24)
    c: PointOnObject(g21,g24)
    c: PointOnObject(g22,g24)
    c: PointOnObject(g23,g24)
    c: Coincident(g24,g-1)
    c: Horizontal(g19)
    c: DistanceX(g0,g13) = 10
FEATURE [PartDesign::AdditiveLoft] AdditiveLoft011
  AllowMultiFace = false
  Closed = false
  Profile = -> Sketch125
  Refine = true
  Ruled = false
  Sections = -> [Sketch124,Sketch126]
FEATURE [Sketcher::SketchObject] Sketch123
  FullyConstrained = false
  MapMode = 5
  Placement = pos=(0,0,17) rot=(0,0,1;0rad)
  Support = -> [AdditiveLoft011]
  sketch-geometry (1):
    g0: Circle CenterX=0 CenterY=0 CenterZ=0 NormalX=0 NormalY=0 NormalZ=1 AngleXU=0 Radius=4.5
  constraints (2):
    c: Coincident(g0,g-1)
    c: Radius(g0) = 4.5
FEATURE [PartDesign::Pad] Pad030
  AllowMultiFace = false
  BaseFeature = -> AdditiveLoft011
  Direction = (1,1,1)
  Length = 0.7
  Length2 = 100
  Profile = -> Sketch123
  Refine = true
  Type = 0
FEATURE [Sketcher::SketchObject] Sketch122
  FullyConstrained = false
  MapMode = 5
  Placement = pos=(0,0,0) rot=(1,0,0;3.14159rad)
  Support = -> [Pad030]
  sketch-geometry (1):
    g0: Circle CenterX=0 CenterY=0 CenterZ=0 NormalX=0 NormalY=0 NormalZ=1 AngleXU=0 Radius=5
  constraints (2):
    c: Coincident(g0,g-1)
    c: Radius(g0) = 5
FEATURE [PartDesign::Pocket] Pocket046
  AllowMultiFace = false
  BaseFeature = -> Pad030
  Direction = (1,1,1)
  Length = 1
  Length2 = 100
  Profile = -> Sketch122
  Refine = true
  Type = 0
FEATURE [Sketcher::SketchObject] Sketch120
  FullyConstrained = false
  MapMode = 5
  Placement = pos=(0,0,1) rot=(1,0,0;3.14159rad)
  Support = -> [Pocket046]
  sketch-geometry (1):
    g0: Circle CenterX=0 CenterY=0 CenterZ=0 NormalX=0 NormalY=0 NormalZ=1 AngleXU=0 Radius=4.65
  constraints (2):
    c: Coincident(g0,g-1)
    c: Radius(g0) = 4.65
FEATURE [PartDesign::Pocket] Pocket045
  AllowMultiFace = false
  BaseFeature = -> Pocket046
  Direction = (1,1,1)
  Length = 1
  Length2 = 100
  Profile = -> Sketch120
  Refine = true
  Type = 0
FEATURE [Sketcher::SketchObject] Sketch121
  FullyConstrained = false
  MapMode = 5
  Placement = pos=(0,0,2) rot=(1,0,0;3.14159rad)
  Support = -> [Pocket045]
  sketch-geometry (2):
    g0: ArcOfCircle CenterX=0 CenterY=0 CenterZ=0 NormalX=0 NormalY=0 NormalZ=1 AngleXU=0 Radius=3 StartAngle=2.19024 EndAngle=7.23453
    g1: LineSegment StartX=-1.74176 StartY=2.4426 StartZ=0 EndX=1.74176 EndY=2.4426 EndZ=0
  constraints (5):
    c: Coincident(g0,g-1)
    c: Coincident(g1,g0)
    c: Coincident(g1,g0)
    c: Horizontal(g1)
    c: Radius(g0) = 3
FEATURE [PartDesign::Pocket] Pocket047
  AllowMultiFace = false
  BaseFeature = -> Pocket045
  Direction = (1,1,1)
  Length = 8
  Length2 = 100
  Profile = -> Sketch121
  Refine = true
  Type = 0
FEATURE [PartDesign::Chamfer] Chamfer030
  Angle = 45
  Base = -> Pocket047 [Edge82,Edge83]
  BaseFeature = -> Pocket047
  ChamferType = 0
  FlipDirection = false
  Size = 1.4
  Size2 = 1
  SupportTransform = false
  UseAllEdges = false
FEATURE [PartDesign::Chamfer] Chamfer023
  Angle = 45
  Base = -> Chamfer030 [Edge8]
  BaseFeature = -> Chamfer030
  ChamferType = 0
  FlipDirection = false
  Size = 0.3
  Size2 = 1
  SupportTransform = false
  UseAllEdges = false
FEATURE [PartDesign::Fillet] Fillet014
  Base = -> Chamfer023 [Edge93,Face36]
  BaseFeature = -> Chamfer023
  Radius = 0.1
  SupportTransform = false
  UseAllEdges = false
FEATURE [PartDesign::Body] Body030
  Group = -> [Sketch125,Sketch124,Sketch126,AdditiveLoft011,Sketch123,Pad030,Sketch122,Pocket046,Sketch120,Pocket045,Sketch121,Pocket047,Chamfer030,Chamfer023,Fillet014]
  Origin = -> Origin039
  Tip = -> Fillet014
FEATURE [Sketcher::SketchObject] Sketch127
  AttachmentOffset = pos=(0,0,17.7) rot=(0,0,1;0rad)
  FullyConstrained = false
  MapMode = 5
  Placement = pos=(0,0,17.7) rot=(0,0,1;0rad)
  Support = -> [XY_Plane048]
  sketch-geometry (10):
    g0: LineSegment StartX=-0.2 StartY=1.5 StartZ=0 EndX=0.2 EndY=1.5 EndZ=0
    g1: LineSegment StartX=0.4 StartY=1.7 StartZ=0 EndX=0.4 EndY=4.2 EndZ=0
    g2: LineSegment StartX=0.2 StartY=4.4 StartZ=0 EndX=-0.2 EndY=4.4 EndZ=0
    g3: LineSegment StartX=-0.4 StartY=4.2 StartZ=0 EndX=-0.4 EndY=1.7 EndZ=0
    g4: ArcOfCircle CenterX=-0.2 CenterY=1.7 CenterZ=0 NormalX=0 NormalY=0 NormalZ=1 AngleXU=0 Radius=0.2 StartAngle=3.14159 EndAngle=4.71239
    g5: ArcOfCircle CenterX=0.2 CenterY=1.7 CenterZ=0 NormalX=0 NormalY=0 NormalZ=1 AngleXU=0 Radius=0.2 StartAngle=4.71239 EndAngle=6.28319
    g6: ArcOfCircle CenterX=0.2 CenterY=4.2 CenterZ=0 NormalX=0 NormalY=0 NormalZ=1 AngleXU=0 Radius=0.2 StartAngle=1.4e-15 EndAngle=1.5708
    g7: ArcOfCircle CenterX=-0.2 CenterY=4.2 CenterZ=0 NormalX=0 NormalY=0 NormalZ=1 AngleXU=0 Radius=0.2 StartAngle=1.5708 EndAngle=3.14159
    g8: LineSegment StartX=-0.2 StartY=1.7 StartZ=0 EndX=0 EndY=0 EndZ=0
    g9: LineSegment StartX=0 StartY=0 StartZ=0 EndX=0.2 EndY=1.7 EndZ=0
  constraints (24):
    c: Horizontal(g0)
    c: Horizontal(g2)
    c: Vertical(g1)
    c: Vertical(g3)
    c: Tangent(g3,g4) = -1.5708
    c: Tangent(g0,g4) = -1.5708
    c: Tangent(g0,g5) = -1.5708
    c: Tangent(g1,g5) = -1.5708
    c: Tangent(g1,g6) = -1.5708
    c: Tangent(g2,g6) = -1.5708
    c: Tangent(g2,g7) = -1.5708
    c: Tangent(g3,g7) = -1.5708
    c: Radius(g7) = 0.2
    c: Equal(g7,g6)
    c: Equal(g7,g5)
    c: Equal(g7,g4)
    c: Coincident(g8,g4)
    c: Coincident(g8,g-1)
    c: Coincident(g9,g-1)
    c: Coincident(g9,g5)
    c: Equal(g9,g8)
    c: DistanceX(g3,g1) = 0.8
    c: DistanceY(g-1,g2) = 4.4
    c: DistanceY(g-1,g0) = 1.5
FEATURE [PartDesign::Pad] Pad031
  AllowMultiFace = false
  Direction = (1,1,1)
  Length = 0.02
  Length2 = 100
  Profile = -> Sketch127
  Refine = true
  Type = 0
FEATURE [PartDesign::Body] Body031  label="Indicator015"
  Group = -> [Sketch127,Pad031]
  Origin = -> Origin040
  Tip = -> Pad031
FEATURE [App::Part] Part008  label="Cap009"
  Group = -> [Body030,Body031]
  Origin = -> Origin033
  Placement = pos=(40.005,-13.335,0) rot=(0,0,1;0rad)
  expr: .Placement.Base.x = 40.005
  expr: .Placement.Base.y = -13.335
FEATURE [App::Part] Part016  label="PO16_Caps"
  Group = -> [Part,Part001,Part002,Part003,Part004,Part005,Part006,Part007,Part008,Part009,Part010,Part011,Part012,Part013,Part014,Part015]
  Origin = -> Origin050
FEATURE [Sketcher::SketchObject] Sketch256
  FullyConstrained = false
  MapMode = 5
  Placement = pos=(0,0,0) rot=(0.57735,0.57735,0.57735;2.0944rad)
  Support = -> [YZ_Plane100]
  sketch-geometry (6):
    g0: LineSegment StartX=0 StartY=0 StartZ=0 EndX=-1.6 EndY=0 EndZ=0
    g1: LineSegment StartX=-1.6 StartY=0 StartZ=0 EndX=-1.6 EndY=-0.4 EndZ=0
    g2: LineSegment StartX=-1.6 StartY=-0.4 StartZ=0 EndX=-1.5 EndY=-0.4 EndZ=0
    g3: LineSegment StartX=-1.5 StartY=-0.4 StartZ=0 EndX=-1.5 EndY=-7 EndZ=0
    g4: LineSegment StartX=-1.5 StartY=-7 StartZ=0 EndX=0 EndY=-7 EndZ=0
    g5: LineSegment StartX=0 StartY=-7 StartZ=0 EndX=0 EndY=0 EndZ=0
  constraints (17):
    c: Coincident(g0,g-1)
    c: Horizontal(g0)
    c: Coincident(g1,g0)
    c: Coincident(g2,g1)
    c: Coincident(g3,g2)
    c: Vertical(g3)
    c: Coincident(g4,g3)
    c: Coincident(g5,g4)
    c: Coincident(g5,g-1)
    c: Vertical(g5)
    c: Horizontal(g4)
    c: Horizontal(g2)
    c: Vertical(g1)
    c: DistanceY(g1,g1) = 0.4
    c: DistanceX(g4,g4) = 1.5
    c: DistanceX(g0,g0) = 1.6
    c: DistanceY(g5,g5) = 7
FEATURE [PartDesign::Revolution] Revolution
  AllowMultiFace = false
  Angle = 360
  Axis = (0,0,1)
  Base = (0,0,0)
  Placement = pos=(0,0,0) rot=(0.57735,0.57735,0.57735;2.0944rad)
  Profile = -> Sketch256
  ReferenceAxis = -> Sketch256 [V_Axis]
FEATURE [PartDesign::Body] Body064
  Group = -> [Sketch256,Revolution]
  Origin = -> Origin100
  Tip = -> Revolution
FEATURE [App::Part] Part031  label="Lightpipe1"
  Group = -> [Body064]
  Origin = -> Origin078
  Placement = pos=(-40.005,40.005,0) rot=(0,0,1;0rad)
  expr: .Placement.Base.x = -40.005
  expr: .Placement.Base.y = 40.005
FEATURE [Sketcher::SketchObject] Sketch257
  FullyConstrained = false
  MapMode = 5
  Placement = pos=(0,0,0) rot=(0.57735,0.57735,0.57735;2.0944rad)
  Support = -> [YZ_Plane101]
  sketch-geometry (6):
    g0: LineSegment StartX=0 StartY=0 StartZ=0 EndX=-1.6 EndY=0 EndZ=0
    g1: LineSegment StartX=-1.6 StartY=0 StartZ=0 EndX=-1.6 EndY=-0.4 EndZ=0
    g2: LineSegment StartX=-1.6 StartY=-0.4 StartZ=0 EndX=-1.5 EndY=-0.4 EndZ=0
    g3: LineSegment StartX=-1.5 StartY=-0.4 StartZ=0 EndX=-1.5 EndY=-7 EndZ=0
    g4: LineSegment StartX=-1.5 StartY=-7 StartZ=0 EndX=0 EndY=-7 EndZ=0
    g5: LineSegment StartX=0 StartY=-7 StartZ=0 EndX=0 EndY=0 EndZ=0
  constraints (17):
    c: Coincident(g0,g-1)
    c: Horizontal(g0)
    c: Coincident(g1,g0)
    c: Coincident(g2,g1)
    c: Coincident(g3,g2)
    c: Vertical(g3)
    c: Coincident(g4,g3)
    c: Coincident(g5,g4)
    c: Coincident(g5,g-1)
    c: Vertical(g5)
    c: Horizontal(g4)
    c: Horizontal(g2)
    c: Vertical(g1)
    c: DistanceY(g1,g1) = 0.4
    c: DistanceX(g4,g4) = 1.5
    c: DistanceX(g0,g0) = 1.6
    c: DistanceY(g5,g5) = 7
FEATURE [PartDesign::Revolution] Revolution001
  AllowMultiFace = false
  Angle = 360
  Axis = (0,0,1)
  Base = (0,0,0)
  Placement = pos=(0,0,0) rot=(0.57735,0.57735,0.57735;2.0944rad)
  Profile = -> Sketch257
  ReferenceAxis = -> Sketch257 [V_Axis]
FEATURE [PartDesign::Body] Body065
  Group = -> [Sketch257,Revolution001]
  Origin = -> Origin101
  Tip = -> Revolution001
FEATURE [App::Part] Part032  label="Lightpipe2"
  Group = -> [Body065]
  Origin = -> Origin051
  Placement = pos=(-13.34,40.005,0) rot=(0,0,1;0rad)
  expr: .Placement.Base.x = -13.335
  expr: .Placement.Base.y = 40.005
FEATURE [Sketcher::SketchObject] Sketch258
  FullyConstrained = false
  MapMode = 5
  Placement = pos=(0,0,0) rot=(0.57735,0.57735,0.57735;2.0944rad)
  Support = -> [YZ_Plane102]
  sketch-geometry (6):
    g0: LineSegment StartX=0 StartY=0 StartZ=0 EndX=-1.6 EndY=0 EndZ=0
    g1: LineSegment StartX=-1.6 StartY=0 StartZ=0 EndX=-1.6 EndY=-0.4 EndZ=0
    g2: LineSegment StartX=-1.6 StartY=-0.4 StartZ=0 EndX=-1.5 EndY=-0.4 EndZ=0
    g3: LineSegment StartX=-1.5 StartY=-0.4 StartZ=0 EndX=-1.5 EndY=-7 EndZ=0
    g4: LineSegment StartX=-1.5 StartY=-7 StartZ=0 EndX=0 EndY=-7 EndZ=0
    g5: LineSegment StartX=0 StartY=-7 StartZ=0 EndX=0 EndY=0 EndZ=0
  constraints (17):
    c: Coincident(g0,g-1)
    c: Horizontal(g0)
    c: Coincident(g1,g0)
    c: Coincident(g2,g1)
    c: Coincident(g3,g2)
    c: Vertical(g3)
    c: Coincident(g4,g3)
    c: Coincident(g5,g4)
    c: Coincident(g5,g-1)
    c: Vertical(g5)
    c: Horizontal(g4)
    c: Horizontal(g2)
    c: Vertical(g1)
    c: DistanceY(g1,g1) = 0.4
    c: DistanceX(g4,g4) = 1.5
    c: DistanceX(g0,g0) = 1.6
    c: DistanceY(g5,g5) = 7
FEATURE [PartDesign::Revolution] Revolution002
  AllowMultiFace = false
  Angle = 360
  Axis = (0,0,1)
  Base = (0,0,0)
  Placement = pos=(0,0,0) rot=(0.57735,0.57735,0.57735;2.0944rad)
  Profile = -> Sketch258
  ReferenceAxis = -> Sketch258 [V_Axis]
FEATURE [PartDesign::Body] Body066
  Group = -> [Sketch258,Revolution002]
  Origin = -> Origin102
  Tip = -> Revolution002
FEATURE [App::Part] Part030  label="Lightpipe3"
  Group = -> [Body066]
  Origin = -> Origin054
  Placement = pos=(13.335,40.005,0) rot=(0,0,1;0rad)
  expr: .Placement.Base.x = 13.335
  expr: .Placement.Base.y = 40.005
FEATURE [Sketcher::SketchObject] Sketch259
  FullyConstrained = false
  MapMode = 5
  Placement = pos=(0,0,0) rot=(0.57735,0.57735,0.57735;2.0944rad)
  Support = -> [YZ_Plane103]
  sketch-geometry (6):
    g0: LineSegment StartX=0 StartY=0 StartZ=0 EndX=-1.6 EndY=0 EndZ=0
    g1: LineSegment StartX=-1.6 StartY=0 StartZ=0 EndX=-1.6 EndY=-0.4 EndZ=0
    g2: LineSegment StartX=-1.6 StartY=-0.4 StartZ=0 EndX=-1.5 EndY=-0.4 EndZ=0
    g3: LineSegment StartX=-1.5 StartY=-0.4 StartZ=0 EndX=-1.5 EndY=-7 EndZ=0
    g4: LineSegment StartX=-1.5 StartY=-7 StartZ=0 EndX=0 EndY=-7 EndZ=0
    g5: LineSegment StartX=0 StartY=-7 StartZ=0 EndX=0 EndY=0 EndZ=0
  constraints (17):
    c: Coincident(g0,g-1)
    c: Horizontal(g0)
    c: Coincident(g1,g0)
    c: Coincident(g2,g1)
    c: Coincident(g3,g2)
    c: Vertical(g3)
    c: Coincident(g4,g3)
    c: Coincident(g5,g4)
    c: Coincident(g5,g-1)
    c: Vertical(g5)
    c: Horizontal(g4)
    c: Horizontal(g2)
    c: Vertical(g1)
    c: DistanceY(g1,g1) = 0.4
    c: DistanceX(g4,g4) = 1.5
    c: DistanceX(g0,g0) = 1.6
    c: DistanceY(g5,g5) = 7
FEATURE [PartDesign::Revolution] Revolution003
  AllowMultiFace = false
  Angle = 360
  Axis = (0,0,1)
  Base = (0,0,0)
  Placement = pos=(0,0,0) rot=(0.57735,0.57735,0.57735;2.0944rad)
  Profile = -> Sketch259
  ReferenceAxis = -> Sketch259 [V_Axis]
FEATURE [PartDesign::Body] Body067
  Group = -> [Sketch259,Revolution003]
  Origin = -> Origin103
  Tip = -> Revolution003
FEATURE [App::Part] Part028  label="Lightpipe4"
  Group = -> [Body067]
  Origin = -> Origin068
  Placement = pos=(40.005,40.005,0) rot=(0,0,1;0rad)
  expr: .Placement.Base.x = 40.005
  expr: .Placement.Base.y = 40.005
FEATURE [Sketcher::SketchObject] Sketch260
  FullyConstrained = false
  MapMode = 5
  Placement = pos=(0,0,0) rot=(0.57735,0.57735,0.57735;2.0944rad)
  Support = -> [YZ_Plane104]
  sketch-geometry (6):
    g0: LineSegment StartX=0 StartY=0 StartZ=0 EndX=-1.6 EndY=0 EndZ=0
    g1: LineSegment StartX=-1.6 StartY=0 StartZ=0 EndX=-1.6 EndY=-0.4 EndZ=0
    g2: LineSegment StartX=-1.6 StartY=-0.4 StartZ=0 EndX=-1.5 EndY=-0.4 EndZ=0
    g3: LineSegment StartX=-1.5 StartY=-0.4 StartZ=0 EndX=-1.5 EndY=-7 EndZ=0
    g4: LineSegment StartX=-1.5 StartY=-7 StartZ=0 EndX=0 EndY=-7 EndZ=0
    g5: LineSegment StartX=0 StartY=-7 StartZ=0 EndX=0 EndY=0 EndZ=0
  constraints (17):
    c: Coincident(g0,g-1)
    c: Horizontal(g0)
    c: Coincident(g1,g0)
    c: Coincident(g2,g1)
    c: Coincident(g3,g2)
    c: Vertical(g3)
    c: Coincident(g4,g3)
    c: Coincident(g5,g4)
    c: Coincident(g5,g-1)
    c: Vertical(g5)
    c: Horizontal(g4)
    c: Horizontal(g2)
    c: Vertical(g1)
    c: DistanceY(g1,g1) = 0.4
    c: DistanceX(g4,g4) = 1.5
    c: DistanceX(g0,g0) = 1.6
    c: DistanceY(g5,g5) = 7
FEATURE [PartDesign::Revolution] Revolution004
  AllowMultiFace = false
  Angle = 360
  Axis = (0,0,1)
  Base = (0,0,0)
  Placement = pos=(0,0,0) rot=(0.57735,0.57735,0.57735;2.0944rad)
  Profile = -> Sketch260
  ReferenceAxis = -> Sketch260 [V_Axis]
FEATURE [PartDesign::Body] Body068
  Group = -> [Sketch260,Revolution004]
  Origin = -> Origin104
  Tip = -> Revolution004
FEATURE [App::Part] Part017  label="Lightpipe5"
  Group = -> [Body068]
  Origin = -> Origin058
  Placement = pos=(40.005,13.335,0) rot=(0,0,1;0rad)
  expr: .Placement.Base.x = 40.005
  expr: .Placement.Base.y = 13.335
FEATURE [Sketcher::SketchObject] Sketch261
  FullyConstrained = false
  MapMode = 5
  Placement = pos=(0,0,0) rot=(0.57735,0.57735,0.57735;2.0944rad)
  Support = -> [YZ_Plane105]
  sketch-geometry (6):
    g0: LineSegment StartX=0 StartY=0 StartZ=0 EndX=-1.6 EndY=0 EndZ=0
    g1: LineSegment StartX=-1.6 StartY=0 StartZ=0 EndX=-1.6 EndY=-0.4 EndZ=0
    g2: LineSegment StartX=-1.6 StartY=-0.4 StartZ=0 EndX=-1.5 EndY=-0.4 EndZ=0
    g3: LineSegment StartX=-1.5 StartY=-0.4 StartZ=0 EndX=-1.5 EndY=-7 EndZ=0
    g4: LineSegment StartX=-1.5 StartY=-7 StartZ=0 EndX=0 EndY=-7 EndZ=0
    g5: LineSegment StartX=0 StartY=-7 StartZ=0 EndX=0 EndY=0 EndZ=0
  constraints (17):
    c: Coincident(g0,g-1)
    c: Horizontal(g0)
    c: Coincident(g1,g0)
    c: Coincident(g2,g1)
    c: Coincident(g3,g2)
    c: Vertical(g3)
    c: Coincident(g4,g3)
    c: Coincident(g5,g4)
    c: Coincident(g5,g-1)
    c: Vertical(g5)
    c: Horizontal(g4)
    c: Horizontal(g2)
    c: Vertical(g1)
    c: DistanceY(g1,g1) = 0.4
    c: DistanceX(g4,g4) = 1.5
    c: DistanceX(g0,g0) = 1.6
    c: DistanceY(g5,g5) = 7
FEATURE [PartDesign::Revolution] Revolution005
  AllowMultiFace = false
  Angle = 360
  Axis = (0,0,1)
  Base = (0,0,0)
  Placement = pos=(0,0,0) rot=(0.57735,0.57735,0.57735;2.0944rad)
  Profile = -> Sketch261
  ReferenceAxis = -> Sketch261 [V_Axis]
FEATURE [PartDesign::Body] Body069
  Group = -> [Sketch261,Revolution005]
  Origin = -> Origin105
  Tip = -> Revolution005
FEATURE [App::Part] Part018  label="Lightpipe6"
  Group = -> [Body069]
  Origin = -> Origin063
  Placement = pos=(13.335,13.335,0) rot=(0,0,1;0rad)
  expr: .Placement.Base.x = 13.335
  expr: .Placement.Base.y = 13.335
FEATURE [Sketcher::SketchObject] Sketch262
  FullyConstrained = false
  MapMode = 5
  Placement = pos=(0,0,0) rot=(0.57735,0.57735,0.57735;2.0944rad)
  Support = -> [YZ_Plane106]
  sketch-geometry (6):
    g0: LineSegment StartX=0 StartY=0 StartZ=0 EndX=-1.6 EndY=0 EndZ=0
    g1: LineSegment StartX=-1.6 StartY=0 StartZ=0 EndX=-1.6 EndY=-0.4 EndZ=0
    g2: LineSegment StartX=-1.6 StartY=-0.4 StartZ=0 EndX=-1.5 EndY=-0.4 EndZ=0
    g3: LineSegment StartX=-1.5 StartY=-0.4 StartZ=0 EndX=-1.5 EndY=-7 EndZ=0
    g4: LineSegment StartX=-1.5 StartY=-7 StartZ=0 EndX=0 EndY=-7 EndZ=0
    g5: LineSegment StartX=0 StartY=-7 StartZ=0 EndX=0 EndY=0 EndZ=0
  constraints (17):
    c: Coincident(g0,g-1)
    c: Horizontal(g0)
    c: Coincident(g1,g0)
    c: Coincident(g2,g1)
    c: Coincident(g3,g2)
    c: Vertical(g3)
    c: Coincident(g4,g3)
    c: Coincident(g5,g4)
    c: Coincident(g5,g-1)
    c: Vertical(g5)
    c: Horizontal(g4)
    c: Horizontal(g2)
    c: Vertical(g1)
    c: DistanceY(g1,g1) = 0.4
    c: DistanceX(g4,g4) = 1.5
    c: DistanceX(g0,g0) = 1.6
    c: DistanceY(g5,g5) = 7
FEATURE [PartDesign::Revolution] Revolution006
  AllowMultiFace = false
  Angle = 360
  Axis = (0,0,1)
  Base = (0,0,0)
  Placement = pos=(0,0,0) rot=(0.57735,0.57735,0.57735;2.0944rad)
  Profile = -> Sketch262
  ReferenceAxis = -> Sketch262 [V_Axis]
FEATURE [PartDesign::Body] Body070
  Group = -> [Sketch262,Revolution006]
  Origin = -> Origin106
  Tip = -> Revolution006
FEATURE [App::Part] Part029  label="Lightpipe7"
  Group = -> [Body070]
  Origin = -> Origin057
  Placement = pos=(-40.005,13.335,0) rot=(0,0,1;0rad)
  expr: .Placement.Base.x = -40.005
  expr: .Placement.Base.y = 13.335
FEATURE [Sketcher::SketchObject] Sketch263
  FullyConstrained = false
  MapMode = 5
  Placement = pos=(0,0,0) rot=(0.57735,0.57735,0.57735;2.0944rad)
  Support = -> [YZ_Plane107]
  sketch-geometry (6):
    g0: LineSegment StartX=0 StartY=0 StartZ=0 EndX=-1.6 EndY=0 EndZ=0
    g1: LineSegment StartX=-1.6 StartY=0 StartZ=0 EndX=-1.6 EndY=-0.4 EndZ=0
    g2: LineSegment StartX=-1.6 StartY=-0.4 StartZ=0 EndX=-1.5 EndY=-0.4 EndZ=0
    g3: LineSegment StartX=-1.5 StartY=-0.4 StartZ=0 EndX=-1.5 EndY=-7 EndZ=0
    g4: LineSegment StartX=-1.5 StartY=-7 StartZ=0 EndX=0 EndY=-7 EndZ=0
    g5: LineSegment StartX=0 StartY=-7 StartZ=0 EndX=0 EndY=0 EndZ=0
  constraints (17):
    c: Coincident(g0,g-1)
    c: Horizontal(g0)
    c: Coincident(g1,g0)
    c: Coincident(g2,g1)
    c: Coincident(g3,g2)
    c: Vertical(g3)
    c: Coincident(g4,g3)
    c: Coincident(g5,g4)
    c: Coincident(g5,g-1)
    c: Vertical(g5)
    c: Horizontal(g4)
    c: Horizontal(g2)
    c: Vertical(g1)
    c: DistanceY(g1,g1) = 0.4
    c: DistanceX(g4,g4) = 1.5
    c: DistanceX(g0,g0) = 1.6
    c: DistanceY(g5,g5) = 7
FEATURE [PartDesign::Revolution] Revolution007
  AllowMultiFace = false
  Angle = 360
  Axis = (0,0,1)
  Base = (0,0,0)
  Placement = pos=(0,0,0) rot=(0.57735,0.57735,0.57735;2.0944rad)
  Profile = -> Sketch263
  ReferenceAxis = -> Sketch263 [V_Axis]
FEATURE [PartDesign::Body] Body071
  Group = -> [Sketch263,Revolution007]
  Origin = -> Origin107
  Tip = -> Revolution007
FEATURE [App::Part] Part026  label="Lightpipe8"
  Group = -> [Body071]
  Origin = -> Origin070
  Placement = pos=(-13.335,13.335,0) rot=(0,0,1;0rad)
  expr: .Placement.Base.x = -13.335
  expr: .Placement.Base.y = 13.335
FEATURE [Sketcher::SketchObject] Sketch264
  FullyConstrained = false
  MapMode = 5
  Placement = pos=(0,0,0) rot=(0.57735,0.57735,0.57735;2.0944rad)
  Support = -> [YZ_Plane108]
  sketch-geometry (6):
    g0: LineSegment StartX=0 StartY=0 StartZ=0 EndX=-1.6 EndY=0 EndZ=0
    g1: LineSegment StartX=-1.6 StartY=0 StartZ=0 EndX=-1.6 EndY=-0.4 EndZ=0
    g2: LineSegment StartX=-1.6 StartY=-0.4 StartZ=0 EndX=-1.5 EndY=-0.4 EndZ=0
    g3: LineSegment StartX=-1.5 StartY=-0.4 StartZ=0 EndX=-1.5 EndY=-7 EndZ=0
    g4: LineSegment StartX=-1.5 StartY=-7 StartZ=0 EndX=0 EndY=-7 EndZ=0
    g5: LineSegment StartX=0 StartY=-7 StartZ=0 EndX=0 EndY=0 EndZ=0
  constraints (17):
    c: Coincident(g0,g-1)
    c: Horizontal(g0)
    c: Coincident(g1,g0)
    c: Coincident(g2,g1)
    c: Coincident(g3,g2)
    c: Vertical(g3)
    c: Coincident(g4,g3)
    c: Coincident(g5,g4)
    c: Coincident(g5,g-1)
    c: Vertical(g5)
    c: Horizontal(g4)
    c: Horizontal(g2)
    c: Vertical(g1)
    c: DistanceY(g1,g1) = 0.4
    c: DistanceX(g4,g4) = 1.5
    c: DistanceX(g0,g0) = 1.6
    c: DistanceY(g5,g5) = 7
FEATURE [PartDesign::Revolution] Revolution008
  AllowMultiFace = false
  Angle = 360
  Axis = (0,0,1)
  Base = (0,0,0)
  Placement = pos=(0,0,0) rot=(0.57735,0.57735,0.57735;2.0944rad)
  Profile = -> Sketch264
  ReferenceAxis = -> Sketch264 [V_Axis]
FEATURE [PartDesign::Body] Body072
  Group = -> [Sketch264,Revolution008]
  Origin = -> Origin108
  Tip = -> Revolution008
FEATURE [App::Part] Part021  label="Lightpipe12"
  Group = -> [Body072]
  Origin = -> Origin080
  Placement = pos=(40.005,-40.005,0) rot=(0,0,1;0rad)
  expr: .Placement.Base.x = 40.005
  expr: .Placement.Base.y = -40.005
FEATURE [Sketcher::SketchObject] Sketch265
  FullyConstrained = false
  MapMode = 5
  Placement = pos=(0,0,0) rot=(0.57735,0.57735,0.57735;2.0944rad)
  Support = -> [YZ_Plane109]
  sketch-geometry (6):
    g0: LineSegment StartX=0 StartY=0 StartZ=0 EndX=-1.6 EndY=0 EndZ=0
    g1: LineSegment StartX=-1.6 StartY=0 StartZ=0 EndX=-1.6 EndY=-0.4 EndZ=0
    g2: LineSegment StartX=-1.6 StartY=-0.4 StartZ=0 EndX=-1.5 EndY=-0.4 EndZ=0
    g3: LineSegment StartX=-1.5 StartY=-0.4 StartZ=0 EndX=-1.5 EndY=-7 EndZ=0
    g4: LineSegment StartX=-1.5 StartY=-7 StartZ=0 EndX=0 EndY=-7 EndZ=0
    g5: LineSegment StartX=0 StartY=-7 StartZ=0 EndX=0 EndY=0 EndZ=0
  constraints (17):
    c: Coincident(g0,g-1)
    c: Horizontal(g0)
    c: Coincident(g1,g0)
    c: Coincident(g2,g1)
    c: Coincident(g3,g2)
    c: Vertical(g3)
    c: Coincident(g4,g3)
    c: Coincident(g5,g4)
    c: Coincident(g5,g-1)
    c: Vertical(g5)
    c: Horizontal(g4)
    c: Horizontal(g2)
    c: Vertical(g1)
    c: DistanceY(g1,g1) = 0.4
    c: DistanceX(g4,g4) = 1.5
    c: DistanceX(g0,g0) = 1.6
    c: DistanceY(g5,g5) = 7
FEATURE [PartDesign::Revolution] Revolution009
  AllowMultiFace = false
  Angle = 360
  Axis = (0,0,1)
  Base = (0,0,0)
  Placement = pos=(0,0,0) rot=(0.57735,0.57735,0.57735;2.0944rad)
  Profile = -> Sketch265
  ReferenceAxis = -> Sketch265 [V_Axis]
FEATURE [PartDesign::Body] Body073
  Group = -> [Sketch265,Revolution009]
  Origin = -> Origin109
  Tip = -> Revolution009
FEATURE [App::Part] Part020  label="Lightpipe11"
  Group = -> [Body073]
  Origin = -> Origin082
  Placement = pos=(-13.335,-13.335,0) rot=(0,0,1;0rad)
  expr: .Placement.Base.x = -13.335
  expr: .Placement.Base.y = -13.335
FEATURE [Sketcher::SketchObject] Sketch266
  FullyConstrained = false
  MapMode = 5
  Placement = pos=(0,0,0) rot=(0.57735,0.57735,0.57735;2.0944rad)
  Support = -> [YZ_Plane110]
  sketch-geometry (6):
    g0: LineSegment StartX=0 StartY=0 StartZ=0 EndX=-1.6 EndY=0 EndZ=0
    g1: LineSegment StartX=-1.6 StartY=0 StartZ=0 EndX=-1.6 EndY=-0.4 EndZ=0
    g2: LineSegment StartX=-1.6 StartY=-0.4 StartZ=0 EndX=-1.5 EndY=-0.4 EndZ=0
    g3: LineSegment StartX=-1.5 StartY=-0.4 StartZ=0 EndX=-1.5 EndY=-7 EndZ=0
    g4: LineSegment StartX=-1.5 StartY=-7 StartZ=0 EndX=0 EndY=-7 EndZ=0
    g5: LineSegment StartX=0 StartY=-7 StartZ=0 EndX=0 EndY=0 EndZ=0
  constraints (17):
    c: Coincident(g0,g-1)
    c: Horizontal(g0)
    c: Coincident(g1,g0)
    c: Coincident(g2,g1)
    c: Coincident(g3,g2)
    c: Vertical(g3)
    c: Coincident(g4,g3)
    c: Coincident(g5,g4)
    c: Coincident(g5,g-1)
    c: Vertical(g5)
    c: Horizontal(g4)
    c: Horizontal(g2)
    c: Vertical(g1)
    c: DistanceY(g1,g1) = 0.4
    c: DistanceX(g4,g4) = 1.5
    c: DistanceX(g0,g0) = 1.6
    c: DistanceY(g5,g5) = 7
FEATURE [PartDesign::Revolution] Revolution010
  AllowMultiFace = false
  Angle = 360
  Axis = (0,0,1)
  Base = (0,0,0)
  Placement = pos=(0,0,0) rot=(0.57735,0.57735,0.57735;2.0944rad)
  Profile = -> Sketch266
  ReferenceAxis = -> Sketch266 [V_Axis]
FEATURE [PartDesign::Body] Body074
  Group = -> [Sketch266,Revolution010]
  Origin = -> Origin110
  Tip = -> Revolution010
FEATURE [App::Part] Part027  label="Lightpipe10"
  Group = -> [Body074]
  Origin = -> Origin097
  Placement = pos=(13.335,-13.335,0) rot=(0,0,1;0rad)
  expr: .Placement.Base.x = 13.335
  expr: .Placement.Base.y = -13.335
FEATURE [Sketcher::SketchObject] Sketch267
  FullyConstrained = false
  MapMode = 5
  Placement = pos=(0,0,0) rot=(0.57735,0.57735,0.57735;2.0944rad)
  Support = -> [YZ_Plane111]
  sketch-geometry (6):
    g0: LineSegment StartX=0 StartY=0 StartZ=0 EndX=-1.6 EndY=0 EndZ=0
    g1: LineSegment StartX=-1.6 StartY=0 StartZ=0 EndX=-1.6 EndY=-0.4 EndZ=0
    g2: LineSegment StartX=-1.6 StartY=-0.4 StartZ=0 EndX=-1.5 EndY=-0.4 EndZ=0
    g3: LineSegment StartX=-1.5 StartY=-0.4 StartZ=0 EndX=-1.5 EndY=-7 EndZ=0
    g4: LineSegment StartX=-1.5 StartY=-7 StartZ=0 EndX=0 EndY=-7 EndZ=0
    g5: LineSegment StartX=0 StartY=-7 StartZ=0 EndX=0 EndY=0 EndZ=0
  constraints (17):
    c: Coincident(g0,g-1)
    c: Horizontal(g0)
    c: Coincident(g1,g0)
    c: Coincident(g2,g1)
    c: Coincident(g3,g2)
    c: Vertical(g3)
    c: Coincident(g4,g3)
    c: Coincident(g5,g4)
    c: Coincident(g5,g-1)
    c: Vertical(g5)
    c: Horizontal(g4)
    c: Horizontal(g2)
    c: Vertical(g1)
    c: DistanceY(g1,g1) = 0.4
    c: DistanceX(g4,g4) = 1.5
    c: DistanceX(g0,g0) = 1.6
    c: DistanceY(g5,g5) = 7
FEATURE [PartDesign::Revolution] Revolution011
  AllowMultiFace = false
  Angle = 360
  Axis = (0,0,1)
  Base = (0,0,0)
  Placement = pos=(0,0,0) rot=(0.57735,0.57735,0.57735;2.0944rad)
  Profile = -> Sketch267
  ReferenceAxis = -> Sketch267 [V_Axis]
FEATURE [PartDesign::Body] Body075
  Group = -> [Sketch267,Revolution011]
  Origin = -> Origin111
  Tip = -> Revolution011
FEATURE [App::Part] Part019  label="Lightpipe9"
  Group = -> [Body075]
  Origin = -> Origin092
  Placement = pos=(40.005,-13.335,0) rot=(0,0,1;0rad)
  expr: .Placement.Base.x = 40.005
  expr: .Placement.Base.y = -13.335
FEATURE [Sketcher::SketchObject] Sketch268
  FullyConstrained = false
  MapMode = 5
  Placement = pos=(0,0,0) rot=(0.57735,0.57735,0.57735;2.0944rad)
  Support = -> [YZ_Plane112]
  sketch-geometry (6):
    g0: LineSegment StartX=0 StartY=0 StartZ=0 EndX=-1.6 EndY=0 EndZ=0
    g1: LineSegment StartX=-1.6 StartY=0 StartZ=0 EndX=-1.6 EndY=-0.4 EndZ=0
    g2: LineSegment StartX=-1.6 StartY=-0.4 StartZ=0 EndX=-1.5 EndY=-0.4 EndZ=0
    g3: LineSegment StartX=-1.5 StartY=-0.4 StartZ=0 EndX=-1.5 EndY=-7 EndZ=0
    g4: LineSegment StartX=-1.5 StartY=-7 StartZ=0 EndX=0 EndY=-7 EndZ=0
    g5: LineSegment StartX=0 StartY=-7 StartZ=0 EndX=0 EndY=0 EndZ=0
  constraints (17):
    c: Coincident(g0,g-1)
    c: Horizontal(g0)
    c: Coincident(g1,g0)
    c: Coincident(g2,g1)
    c: Coincident(g3,g2)
    c: Vertical(g3)
    c: Coincident(g4,g3)
    c: Coincident(g5,g4)
    c: Coincident(g5,g-1)
    c: Vertical(g5)
    c: Horizontal(g4)
    c: Horizontal(g2)
    c: Vertical(g1)
    c: DistanceY(g1,g1) = 0.4
    c: DistanceX(g4,g4) = 1.5
    c: DistanceX(g0,g0) = 1.6
    c: DistanceY(g5,g5) = 7
FEATURE [PartDesign::Revolution] Revolution012
  AllowMultiFace = false
  Angle = 360
  Axis = (0,0,1)
  Base = (0,0,0)
  Placement = pos=(0,0,0) rot=(0.57735,0.57735,0.57735;2.0944rad)
  Profile = -> Sketch268
  ReferenceAxis = -> Sketch268 [V_Axis]
FEATURE [Sketcher::SketchObject] Sketch269
  FullyConstrained = false
  MapMode = 5
  Placement = pos=(0,0,0) rot=(0.57735,0.57735,0.57735;2.0944rad)
  Support = -> [YZ_Plane113]
  sketch-geometry (6):
    g0: LineSegment StartX=0 StartY=0 StartZ=0 EndX=-1.6 EndY=0 EndZ=0
    g1: LineSegment StartX=-1.6 StartY=0 StartZ=0 EndX=-1.6 EndY=-0.4 EndZ=0
    g2: LineSegment StartX=-1.6 StartY=-0.4 StartZ=0 EndX=-1.5 EndY=-0.4 EndZ=0
    g3: LineSegment StartX=-1.5 StartY=-0.4 StartZ=0 EndX=-1.5 EndY=-7 EndZ=0
    g4: LineSegment StartX=-1.5 StartY=-7 StartZ=0 EndX=0 EndY=-7 EndZ=0
    g5: LineSegment StartX=0 StartY=-7 StartZ=0 EndX=0 EndY=0 EndZ=0
  constraints (17):
    c: Coincident(g0,g-1)
    c: Horizontal(g0)
    c: Coincident(g1,g0)
    c: Coincident(g2,g1)
    c: Coincident(g3,g2)
    c: Vertical(g3)
    c: Coincident(g4,g3)
    c: Coincident(g5,g4)
    c: Coincident(g5,g-1)
    c: Vertical(g5)
    c: Horizontal(g4)
    c: Horizontal(g2)
    c: Vertical(g1)
    c: DistanceY(g1,g1) = 0.4
    c: DistanceX(g4,g4) = 1.5
    c: DistanceX(g0,g0) = 1.6
    c: DistanceY(g5,g5) = 7
FEATURE [PartDesign::Revolution] Revolution013
  AllowMultiFace = false
  Angle = 360
  Axis = (0,0,1)
  Base = (0,0,0)
  Placement = pos=(0,0,0) rot=(0.57735,0.57735,0.57735;2.0944rad)
  Profile = -> Sketch269
  ReferenceAxis = -> Sketch269 [V_Axis]
FEATURE [Sketcher::SketchObject] Sketch270
  FullyConstrained = false
  MapMode = 5
  Placement = pos=(0,0,0) rot=(0.57735,0.57735,0.57735;2.0944rad)
  Support = -> [YZ_Plane114]
  sketch-geometry (6):
    g0: LineSegment StartX=0 StartY=0 StartZ=0 EndX=-1.6 EndY=0 EndZ=0
    g1: LineSegment StartX=-1.6 StartY=0 StartZ=0 EndX=-1.6 EndY=-0.4 EndZ=0
    g2: LineSegment StartX=-1.6 StartY=-0.4 StartZ=0 EndX=-1.5 EndY=-0.4 EndZ=0
    g3: LineSegment StartX=-1.5 StartY=-0.4 StartZ=0 EndX=-1.5 EndY=-7 EndZ=0
    g4: LineSegment StartX=-1.5 StartY=-7 StartZ=0 EndX=0 EndY=-7 EndZ=0
    g5: LineSegment StartX=0 StartY=-7 StartZ=0 EndX=0 EndY=0 EndZ=0
  constraints (17):
    c: Coincident(g0,g-1)
    c: Horizontal(g0)
    c: Coincident(g1,g0)
    c: Coincident(g2,g1)
    c: Coincident(g3,g2)
    c: Vertical(g3)
    c: Coincident(g4,g3)
    c: Coincident(g5,g4)
    c: Coincident(g5,g-1)
    c: Vertical(g5)
    c: Horizontal(g4)
    c: Horizontal(g2)
    c: Vertical(g1)
    c: DistanceY(g1,g1) = 0.4
    c: DistanceX(g4,g4) = 1.5
    c: DistanceX(g0,g0) = 1.6
    c: DistanceY(g5,g5) = 7
FEATURE [PartDesign::Revolution] Revolution014
  AllowMultiFace = false
  Angle = 360
  Axis = (0,0,1)
  Base = (0,0,0)
  Placement = pos=(0,0,0) rot=(0.57735,0.57735,0.57735;2.0944rad)
  Profile = -> Sketch270
  ReferenceAxis = -> Sketch270 [V_Axis]
FEATURE [Sketcher::SketchObject] Sketch271
  FullyConstrained = false
  MapMode = 5
  Placement = pos=(0,0,0) rot=(0.57735,0.57735,0.57735;2.0944rad)
  Support = -> [YZ_Plane115]
  sketch-geometry (6):
    g0: LineSegment StartX=0 StartY=0 StartZ=0 EndX=-1.6 EndY=0 EndZ=0
    g1: LineSegment StartX=-1.6 StartY=0 StartZ=0 EndX=-1.6 EndY=-0.4 EndZ=0
    g2: LineSegment StartX=-1.6 StartY=-0.4 StartZ=0 EndX=-1.5 EndY=-0.4 EndZ=0
    g3: LineSegment StartX=-1.5 StartY=-0.4 StartZ=0 EndX=-1.5 EndY=-7 EndZ=0
    g4: LineSegment StartX=-1.5 StartY=-7 StartZ=0 EndX=0 EndY=-7 EndZ=0
    g5: LineSegment StartX=0 StartY=-7 StartZ=0 EndX=0 EndY=0 EndZ=0
  constraints (17):
    c: Coincident(g0,g-1)
    c: Horizontal(g0)
    c: Coincident(g1,g0)
    c: Coincident(g2,g1)
    c: Coincident(g3,g2)
    c: Vertical(g3)
    c: Coincident(g4,g3)
    c: Coincident(g5,g4)
    c: Coincident(g5,g-1)
    c: Vertical(g5)
    c: Horizontal(g4)
    c: Horizontal(g2)
    c: Vertical(g1)
    c: DistanceY(g1,g1) = 0.4
    c: DistanceX(g4,g4) = 1.5
    c: DistanceX(g0,g0) = 1.6
    c: DistanceY(g5,g5) = 7
FEATURE [PartDesign::Revolution] Revolution015
  AllowMultiFace = false
  Angle = 360
  Axis = (0,0,1)
  Base = (0,0,0)
  Placement = pos=(0,0,0) rot=(0.57735,0.57735,0.57735;2.0944rad)
  Profile = -> Sketch271
  ReferenceAxis = -> Sketch271 [V_Axis]
FEATURE [PartDesign::Body] Body076
  Group = -> [Sketch268,Revolution012]
  Origin = -> Origin115
  Tip = -> Revolution012
FEATURE [App::Part] Part022  label="Lightpipe13"
  Group = -> [Body076]
  Origin = -> Origin089
  Placement = pos=(-40.005,-13.335,0) rot=(0,0,1;0rad)
  expr: .Placement.Base.x = -40.005
  expr: .Placement.Base.y = -13.335
FEATURE [PartDesign::Body] Body077
  Group = -> [Sketch269,Revolution013]
  Origin = -> Origin114
  Tip = -> Revolution013
FEATURE [App::Part] Part023  label="Lightpipe14"
  Group = -> [Body077]
  Origin = -> Origin091
  Placement = pos=(13.335,-40.005,0) rot=(0,0,1;0rad)
  expr: .Placement.Base.x = 13.335
  expr: .Placement.Base.y = -40.005
FEATURE [PartDesign::Body] Body078
  Group = -> [Sketch270,Revolution014]
  Origin = -> Origin113
  Tip = -> Revolution014
FEATURE [App::Part] Part024  label="Lightpipe15"
  Group = -> [Body078]
  Origin = -> Origin086
  Placement = pos=(-40.005,-40.005,0) rot=(0,0,1;0rad)
  expr: .Placement.Base.x = -40.005
  expr: .Placement.Base.y = -40.005
FEATURE [PartDesign::Body] Body079
  Group = -> [Sketch271,Revolution015]
  Origin = -> Origin112
  Tip = -> Revolution015
FEATURE [App::Part] Part025  label="Lightpipe16"
  Group = -> [Body079]
  Origin = -> Origin075
  Placement = pos=(-13.335,-40.005,0) rot=(0,0,1;0rad)
  expr: .Placement.Base.x = -13.335
  expr: .Placement.Base.y = -40.005
FEATURE [App::Part] Part033  label="PO16_Lightpipes"
  Group = -> [Part031,Part032,Part030,Part028,Part017,Part018,Part029,Part026,Part019,Part027,Part020,Part021,Part022,Part023,Part024,Part025]
  Origin = -> Origin099
  Placement = pos=(0,8.5,0) rot=(0,0,1;0rad)
  expr: .Placement.Base.y = 8.5
FEATURE [App::Part] Part035  label="PO16_Frontpanel"
  Origin = -> Origin117
FEATURE [Sketcher::SketchObject] Sketch277
  FullyConstrained = false
  MapMode = 5
  Support = -> [XY_Plane121]
  sketch-geometry (1):
    g0: Circle CenterX=0 CenterY=0 CenterZ=0 NormalX=0 NormalY=0 NormalZ=1 AngleXU=0 Radius=1.5
  constraints (2):
    c: Coincident(g0,g-1)
    c: Radius(g0) = 1.5
FEATURE [PartDesign::Pad] Pad033
  AllowMultiFace = false
  Direction = (1,1,1)
  Length = 13.6
  Length2 = 100
  Profile = -> Sketch277
  Refine = true
  Reversed = true
  Type = 0
FEATURE [PartDesign::Chamfer] Chamfer033
  Angle = 45
  Base = -> Pad033 [Edge2,Edge3]
  BaseFeature = -> Pad033
  ChamferType = 0
  FlipDirection = false
  Size = 0.1
  Size2 = 1
  SupportTransform = false
  UseAllEdges = false
FEATURE [PartDesign::Body] Body080
  Group = -> [Sketch277,Pad033,Chamfer033]
  Origin = -> Origin121
  Placement = pos=(0,0,-0.2) rot=(0,0,1;0rad)
  Tip = -> Chamfer033
FEATURE [App::Part] Part038  label="Magnet001"
  Group = -> [Body080]
  Origin = -> Origin120
  Placement = pos=(47,51.45,0) rot=(0,0,1;0rad)
FEATURE [Sketcher::SketchObject] Sketch292
  FullyConstrained = false
  MapMode = 5
  Support = -> [XY_Plane439]
  sketch-geometry (5):
    g0: LineSegment StartX=-1.5 StartY=1.5 StartZ=0 EndX=-1.5 EndY=-1.5 EndZ=0
    g1: LineSegment StartX=-1.5 StartY=-1.5 StartZ=0 EndX=1.5 EndY=-1.5 EndZ=0
    g2: LineSegment StartX=1.5 StartY=-1.5 StartZ=0 EndX=1.5 EndY=1.5 EndZ=0
    g3: LineSegment StartX=1.5 StartY=1.5 StartZ=0 EndX=-1.5 EndY=1.5 EndZ=0
    g4: Circle CenterX=0 CenterY=0 CenterZ=0 NormalX=0 NormalY=0 NormalZ=1 AngleXU=0 Radius=2.12132
  constraints (14):
    c: Coincident(g0,g1)
    c: Coincident(g1,g2)
    c: Coincident(g2,g3)
    c: Coincident(g3,g0)
    c: Equal(g0,g1)
    c: Equal(g0,g2)
    c: Equal(g0,g3)
    c: PointOnObject(g0,g4)
    c: PointOnObject(g1,g4)
    c: PointOnObject(g2,g4)
    c: PointOnObject(g3,g4)
    c: Coincident(g4,g-1)
    c: Horizontal(g3)
    c: DistanceX(g3,g3) = 3
FEATURE [PartDesign::Pad] Pad048
  AllowMultiFace = false
  Direction = (1,1,1)
  Length = 3
  Length2 = 100
  Profile = -> Sketch292
  Refine = true
  Type = 0
FEATURE [PartDesign::Fillet] Fillet017
  Base = -> Pad048 [Face3,Face6,Face2,Face4,Face1,Face5]
  BaseFeature = -> Pad048
  Radius = 0.1
  SupportTransform = false
  UseAllEdges = false
FEATURE [PartDesign::Body] Body095
  Group = -> [Sketch292,Pad048,Fillet017]
  Origin = -> Origin439
  Tip = -> Fillet017
FEATURE [App::Part] Part058  label="M1"
  Group = -> [Body095]
  Origin = -> Origin440
  Placement = pos=(15.59,49.8,-13) rot=(0,0,1;0rad)
FEATURE [Sketcher::SketchObject] Sketch293
  FullyConstrained = false
  MapMode = 5
  Support = -> [XY_Plane441]
  sketch-geometry (5):
    g0: LineSegment StartX=-1.5 StartY=1.5 StartZ=0 EndX=-1.5 EndY=-1.5 EndZ=0
    g1: LineSegment StartX=-1.5 StartY=-1.5 StartZ=0 EndX=1.5 EndY=-1.5 EndZ=0
    g2: LineSegment StartX=1.5 StartY=-1.5 StartZ=0 EndX=1.5 EndY=1.5 EndZ=0
    g3: LineSegment StartX=1.5 StartY=1.5 StartZ=0 EndX=-1.5 EndY=1.5 EndZ=0
    g4: Circle CenterX=0 CenterY=0 CenterZ=0 NormalX=0 NormalY=0 NormalZ=1 AngleXU=0 Radius=2.12132
  constraints (14):
    c: Coincident(g0,g1)
    c: Coincident(g1,g2)
    c: Coincident(g2,g3)
    c: Coincident(g3,g0)
    c: Equal(g0,g1)
    c: Equal(g0,g2)
    c: Equal(g0,g3)
    c: PointOnObject(g0,g4)
    c: PointOnObject(g1,g4)
    c: PointOnObject(g2,g4)
    c: PointOnObject(g3,g4)
    c: Coincident(g4,g-1)
    c: Horizontal(g3)
    c: DistanceX(g3,g3) = 3
FEATURE [PartDesign::Pad] Pad049
  AllowMultiFace = false
  Direction = (1,1,1)
  Length = 3
  Length2 = 100
  Profile = -> Sketch293
  Refine = true
  Type = 0
FEATURE [PartDesign::Fillet] Fillet018
  Base = -> Pad049 [Face3,Face6,Face2,Face4,Face1,Face5]
  BaseFeature = -> Pad049
  Radius = 0.1
  SupportTransform = false
  UseAllEdges = false
FEATURE [PartDesign::Body] Body096
  Group = -> [Sketch293,Pad049,Fillet018]
  Origin = -> Origin442
  Tip = -> Fillet018
FEATURE [App::Part] Part059  label="M003"
  Group = -> [Body096]
  Origin = -> Origin441
  Placement = pos=(15.59,49.8,-13) rot=(0,0,1;0rad)
FEATURE [Sketcher::SketchObject] Sketch294
  FullyConstrained = false
  MapMode = 5
  Support = -> [XY_Plane443]
  sketch-geometry (5):
    g0: LineSegment StartX=-1.5 StartY=1.5 StartZ=0 EndX=-1.5 EndY=-1.5 EndZ=0
    g1: LineSegment StartX=-1.5 StartY=-1.5 StartZ=0 EndX=1.5 EndY=-1.5 EndZ=0
    g2: LineSegment StartX=1.5 StartY=-1.5 StartZ=0 EndX=1.5 EndY=1.5 EndZ=0
    g3: LineSegment StartX=1.5 StartY=1.5 StartZ=0 EndX=-1.5 EndY=1.5 EndZ=0
    g4: Circle CenterX=0 CenterY=0 CenterZ=0 NormalX=0 NormalY=0 NormalZ=1 AngleXU=0 Radius=2.12132
  constraints (14):
    c: Coincident(g0,g1)
    c: Coincident(g1,g2)
    c: Coincident(g2,g3)
    c: Coincident(g3,g0)
    c: Equal(g0,g1)
    c: Equal(g0,g2)
    c: Equal(g0,g3)
    c: PointOnObject(g0,g4)
    c: PointOnObject(g1,g4)
    c: PointOnObject(g2,g4)
    c: PointOnObject(g3,g4)
    c: Coincident(g4,g-1)
    c: Horizontal(g3)
    c: DistanceX(g3,g3) = 3
FEATURE [PartDesign::Pad] Pad050
  AllowMultiFace = false
  Direction = (1,1,1)
  Length = 3
  Length2 = 100
  Profile = -> Sketch294
  Refine = true
  Type = 0
FEATURE [PartDesign::Fillet] Fillet019
  Base = -> Pad050 [Face3,Face6,Face2,Face4,Face1,Face5]
  BaseFeature = -> Pad050
  Radius = 0.1
  SupportTransform = false
  UseAllEdges = false
FEATURE [PartDesign::Body] Body097
  Group = -> [Sketch294,Pad050,Fillet019]
  Origin = -> Origin444
  Tip = -> Fillet019
FEATURE [App::Part] Part060  label="M004"
  Group = -> [Body097]
  Origin = -> Origin443
  Placement = pos=(15.59,49.8,-13) rot=(0,0,1;0rad)
FEATURE [Sketcher::SketchObject] Sketch295
  FullyConstrained = false
  MapMode = 5
  Support = -> [XY_Plane445]
  sketch-geometry (5):
    g0: LineSegment StartX=-1.5 StartY=1.5 StartZ=0 EndX=-1.5 EndY=-1.5 EndZ=0
    g1: LineSegment StartX=-1.5 StartY=-1.5 StartZ=0 EndX=1.5 EndY=-1.5 EndZ=0
    g2: LineSegment StartX=1.5 StartY=-1.5 StartZ=0 EndX=1.5 EndY=1.5 EndZ=0
    g3: LineSegment StartX=1.5 StartY=1.5 StartZ=0 EndX=-1.5 EndY=1.5 EndZ=0
    g4: Circle CenterX=0 CenterY=0 CenterZ=0 NormalX=0 NormalY=0 NormalZ=1 AngleXU=0 Radius=2.12132
  constraints (14):
    c: Coincident(g0,g1)
    c: Coincident(g1,g2)
    c: Coincident(g2,g3)
    c: Coincident(g3,g0)
    c: Equal(g0,g1)
    c: Equal(g0,g2)
    c: Equal(g0,g3)
    c: PointOnObject(g0,g4)
    c: PointOnObject(g1,g4)
    c: PointOnObject(g2,g4)
    c: PointOnObject(g3,g4)
    c: Coincident(g4,g-1)
    c: Horizontal(g3)
    c: DistanceX(g3,g3) = 3
FEATURE [PartDesign::Pad] Pad051
  AllowMultiFace = false
  Direction = (1,1,1)
  Length = 3
  Length2 = 100
  Profile = -> Sketch295
  Refine = true
  Type = 0
FEATURE [PartDesign::Fillet] Fillet020
  Base = -> Pad051 [Face3,Face6,Face2,Face4,Face1,Face5]
  BaseFeature = -> Pad051
  Radius = 0.1
  SupportTransform = false
  UseAllEdges = false
FEATURE [PartDesign::Body] Body098
  Group = -> [Sketch295,Pad051,Fillet020]
  Origin = -> Origin446
  Tip = -> Fillet020
FEATURE [App::Part] Part061  label="M005"
  Group = -> [Body098]
  Origin = -> Origin445
  Placement = pos=(15.59,49.8,-13) rot=(0,0,1;0rad)
FEATURE [App::Part] Part062
  Group = -> [Part058]
  Origin = -> Origin447
FEATURE [App::Part] Part063
  Group = -> [Part059]
  Origin = -> Origin448
  Placement = pos=(0,0,0) rot=(0,0,1;1.5708rad)
FEATURE [App::Part] Part064
  Group = -> [Part060]
  Origin = -> Origin449
  Placement = pos=(0,0,0) rot=(0,0,1;3.14159rad)
FEATURE [App::Part] Part065
  Group = -> [Part061]
  Origin = -> Origin450
  Placement = pos=(0,0,0) rot=(0,0,1;4.71239rad)
FEATURE [App::Part] Part057  label="MagnetSense"
  Group = -> [Part062,Part063,Part064,Part065]
  Origin = -> Origin438
  Placement = pos=(0,0,-0.25) rot=(0,0,1;0rad)
FEATURE [Sketcher::SketchObject] Sketch296
  FullyConstrained = false
  MapMode = 5
  Placement = pos=(0,0,0) rot=(1,0,0;1.5708rad)
  Support = -> [XZ_Plane746]
  sketch-geometry (5):
    g0: LineSegment StartX=0 StartY=0 StartZ=0 EndX=-3.175 EndY=0 EndZ=0
    g1: LineSegment StartX=-3.175 StartY=0 StartZ=0 EndX=-3.175 EndY=-0.2 EndZ=0
    g2: LineSegment StartX=-3.175 StartY=-0.2 StartZ=0 EndX=-2.875 EndY=-0.2 EndZ=0
    g3: ArcOfCircle CenterX=0 CenterY=2.10479 CenterZ=0 NormalX=0 NormalY=0 NormalZ=1 AngleXU=0 Radius=3.68479 StartAngle=3.81735 EndAngle=4.71239
    g4: LineSegment StartX=0 StartY=-1.58 StartZ=0 EndX=0 EndY=0 EndZ=0
  constraints (15):
    c: Coincident(g0,g-1)
    c: PointOnObject(g0,g-1)
    c: Coincident(g1,g0)
    c: Coincident(g2,g1)
    c: Horizontal(g2)
    c: DistanceX(g0,g0) = 3.175
    c: Vertical(g1)
    c: DistanceY(g1,g1) = 0.2
    c: Coincident(g3,g2)
    c: PointOnObject(g3,g-2)
    c: Coincident(g4,g3)
    c: Coincident(g4,g0)
    c: DistanceY(g4,g4) = 1.58
    c: DistanceX(g1,g2) = 0.3
    c: PointOnObject(g3,g-2)
FEATURE [PartDesign::Revolution] Revolution016
  AllowMultiFace = false
  Angle = 360
  Axis = (0,2e-16,1)
  Base = (0,0,0)
  Placement = pos=(0,0,0) rot=(1,0,0;1.5708rad)
  Profile = -> Sketch296
  ReferenceAxis = -> Sketch296 [V_Axis]
  Refine = true
FEATURE [PartDesign::Body] Body099
  Group = -> [Sketch296,Revolution016]
  Origin = -> Origin746
  Tip = -> Revolution016
FEATURE [App::Part] Part048
  Group = -> [Body099]
  Origin = -> Origin142
  Placement = pos=(-44,-44,-15.1) rot=(0,0,1;0rad)
FEATURE [Sketcher::SketchObject] Sketch297
  FullyConstrained = false
  MapMode = 5
  Placement = pos=(0,0,0) rot=(1,0,0;1.5708rad)
  Support = -> [XZ_Plane748]
  sketch-geometry (5):
    g0: LineSegment StartX=0 StartY=0 StartZ=0 EndX=-3.175 EndY=0 EndZ=0
    g1: LineSegment StartX=-3.175 StartY=0 StartZ=0 EndX=-3.175 EndY=-0.2 EndZ=0
    g2: LineSegment StartX=-3.175 StartY=-0.2 StartZ=0 EndX=-2.875 EndY=-0.2 EndZ=0
    g3: ArcOfCircle CenterX=0 CenterY=2.10479 CenterZ=0 NormalX=0 NormalY=0 NormalZ=1 AngleXU=0 Radius=3.68479 StartAngle=3.81735 EndAngle=4.71239
    g4: LineSegment StartX=0 StartY=-1.58 StartZ=0 EndX=0 EndY=0 EndZ=0
  constraints (15):
    c: Coincident(g0,g-1)
    c: PointOnObject(g0,g-1)
    c: Coincident(g1,g0)
    c: Coincident(g2,g1)
    c: Horizontal(g2)
    c: DistanceX(g0,g0) = 3.175
    c: Vertical(g1)
    c: DistanceY(g1,g1) = 0.2
    c: Coincident(g3,g2)
    c: PointOnObject(g3,g-2)
    c: Coincident(g4,g3)
    c: Coincident(g4,g0)
    c: DistanceY(g4,g4) = 1.58
    c: DistanceX(g1,g2) = 0.3
    c: PointOnObject(g3,g-2)
FEATURE [PartDesign::Revolution] Revolution017
  AllowMultiFace = false
  Angle = 360
  Axis = (0,2e-16,1)
  Base = (0,0,0)
  Placement = pos=(0,0,0) rot=(1,0,0;1.5708rad)
  Profile = -> Sketch297
  ReferenceAxis = -> Sketch297 [V_Axis]
  Refine = true
FEATURE [PartDesign::Body] Body100
  Group = -> [Sketch297,Revolution017]
  Origin = -> Origin748
  Tip = -> Revolution017
FEATURE [App::Part] Part067
  Group = -> [Body100]
  Origin = -> Origin747
  Placement = pos=(44,-44,-15.1) rot=(0,0,1;0rad)
FEATURE [Sketcher::SketchObject] Sketch298
  FullyConstrained = false
  MapMode = 5
  Placement = pos=(0,0,0) rot=(1,0,0;1.5708rad)
  Support = -> [XZ_Plane750]
  sketch-geometry (5):
    g0: LineSegment StartX=0 StartY=0 StartZ=0 EndX=-3.175 EndY=0 EndZ=0
    g1: LineSegment StartX=-3.175 StartY=0 StartZ=0 EndX=-3.175 EndY=-0.2 EndZ=0
    g2: LineSegment StartX=-3.175 StartY=-0.2 StartZ=0 EndX=-2.875 EndY=-0.2 EndZ=0
    g3: ArcOfCircle CenterX=0 CenterY=2.10479 CenterZ=0 NormalX=0 NormalY=0 NormalZ=1 AngleXU=0 Radius=3.68479 StartAngle=3.81735 EndAngle=4.71239
    g4: LineSegment StartX=0 StartY=-1.58 StartZ=0 EndX=0 EndY=0 EndZ=0
  constraints (15):
    c: Coincident(g0,g-1)
    c: PointOnObject(g0,g-1)
    c: Coincident(g1,g0)
    c: Coincident(g2,g1)
    c: Horizontal(g2)
    c: DistanceX(g0,g0) = 3.175
    c: Vertical(g1)
    c: DistanceY(g1,g1) = 0.2
    c: Coincident(g3,g2)
    c: PointOnObject(g3,g-2)
    c: Coincident(g4,g3)
    c: Coincident(g4,g0)
    c: DistanceY(g4,g4) = 1.58
    c: DistanceX(g1,g2) = 0.3
    c: PointOnObject(g3,g-2)
FEATURE [PartDesign::Revolution] Revolution018
  AllowMultiFace = false
  Angle = 360
  Axis = (0,2e-16,1)
  Base = (0,0,0)
  Placement = pos=(0,0,0) rot=(1,0,0;1.5708rad)
  Profile = -> Sketch298
  ReferenceAxis = -> Sketch298 [V_Axis]
  Refine = true
FEATURE [PartDesign::Body] Body101
  Group = -> [Sketch298,Revolution018]
  Origin = -> Origin750
  Tip = -> Revolution018
FEATURE [App::Part] Part068
  Group = -> [Body101]
  Origin = -> Origin749
  Placement = pos=(-44,44,-15.1) rot=(0,0,1;0rad)
FEATURE [Sketcher::SketchObject] Sketch299
  FullyConstrained = false
  MapMode = 5
  Placement = pos=(0,0,0) rot=(1,0,0;1.5708rad)
  Support = -> [XZ_Plane752]
  sketch-geometry (5):
    g0: LineSegment StartX=0 StartY=0 StartZ=0 EndX=-3.175 EndY=0 EndZ=0
    g1: LineSegment StartX=-3.175 StartY=0 StartZ=0 EndX=-3.175 EndY=-0.2 EndZ=0
    g2: LineSegment StartX=-3.175 StartY=-0.2 StartZ=0 EndX=-2.875 EndY=-0.2 EndZ=0
    g3: ArcOfCircle CenterX=0 CenterY=2.10479 CenterZ=0 NormalX=0 NormalY=0 NormalZ=1 AngleXU=0 Radius=3.68479 StartAngle=3.81735 EndAngle=4.71239
    g4: LineSegment StartX=0 StartY=-1.58 StartZ=0 EndX=0 EndY=0 EndZ=0
  constraints (15):
    c: Coincident(g0,g-1)
    c: PointOnObject(g0,g-1)
    c: Coincident(g1,g0)
    c: Coincident(g2,g1)
    c: Horizontal(g2)
    c: DistanceX(g0,g0) = 3.175
    c: Vertical(g1)
    c: DistanceY(g1,g1) = 0.2
    c: Coincident(g3,g2)
    c: PointOnObject(g3,g-2)
    c: Coincident(g4,g3)
    c: Coincident(g4,g0)
    c: DistanceY(g4,g4) = 1.58
    c: DistanceX(g1,g2) = 0.3
    c: PointOnObject(g3,g-2)
FEATURE [PartDesign::Revolution] Revolution019
  AllowMultiFace = false
  Angle = 360
  Axis = (0,2e-16,1)
  Base = (0,0,0)
  Placement = pos=(0,0,0) rot=(1,0,0;1.5708rad)
  Profile = -> Sketch299
  ReferenceAxis = -> Sketch299 [V_Axis]
  Refine = true
FEATURE [PartDesign::Body] Body102
  Group = -> [Sketch299,Revolution019]
  Origin = -> Origin752
  Tip = -> Revolution019
FEATURE [App::Part] Part069
  Group = -> [Body102]
  Origin = -> Origin751
  Placement = pos=(44,44,-15.1) rot=(0,0,1;0rad)
FEATURE [App::Part] Part047  label="Feet"
  Group = -> [Part048,Part067,Part068,Part069]
  Origin = -> Origin137
  Placement = pos=(0,0,0.5) rot=(0,0,1;0rad)
FEATURE [Sketcher::SketchObject] Sketch300
  FullyConstrained = false
  MapMode = 5
  Support = -> [XY_Plane755]
  sketch-geometry (11):
    g0: LineSegment StartX=-51.3 StartY=53.3 StartZ=0 EndX=51.3 EndY=53.3 EndZ=0
    g1: LineSegment StartX=53.3 StartY=51.3 StartZ=0 EndX=53.3 EndY=-51.3 EndZ=0
    g2: LineSegment StartX=51.3 StartY=-53.3 StartZ=0 EndX=-51.3 EndY=-53.3 EndZ=0
    g3: LineSegment StartX=-53.3 StartY=-51.3 StartZ=0 EndX=-53.3 EndY=51.3 EndZ=0
    g4: ArcOfCircle CenterX=-51.3 CenterY=51.3 CenterZ=0 NormalX=0 NormalY=0 NormalZ=1 AngleXU=0 Radius=2 StartAngle=1.5708 EndAngle=3.14159
    g5: ArcOfCircle CenterX=51.3 CenterY=51.3 CenterZ=0 NormalX=0 NormalY=0 NormalZ=1 AngleXU=0 Radius=2 StartAngle=8e-16 EndAngle=1.5708
    g6: ArcOfCircle CenterX=51.3 CenterY=-51.3 CenterZ=0 NormalX=0 NormalY=0 NormalZ=1 AngleXU=0 Radius=2 StartAngle=4.71239 EndAngle=6.28319
    g7: ArcOfCircle CenterX=-51.3 CenterY=-51.3 CenterZ=0 NormalX=0 NormalY=0 NormalZ=1 AngleXU=0 Radius=2 StartAngle=3.14159 EndAngle=4.71239
    g8: LineSegment StartX=-51.3 StartY=51.3 StartZ=0 EndX=0 EndY=0 EndZ=0
    g9: LineSegment StartX=0 StartY=0 StartZ=0 EndX=51.3 EndY=51.3 EndZ=0
    g10: LineSegment StartX=0 StartY=0 StartZ=0 EndX=-51.3 EndY=-51.3 EndZ=0
  constraints (26):
    c: Horizontal(g0)
    c: Horizontal(g2)
    c: Vertical(g1)
    c: Vertical(g3)
    c: Tangent(g3,g4) = 1.5708
    c: Tangent(g0,g4) = 1.5708
    c: Tangent(g0,g5) = 1.5708
    c: Tangent(g1,g5) = 1.5708
    c: Tangent(g1,g6) = 1.5708
    c: Tangent(g2,g6) = 1.5708
    c: Tangent(g2,g7) = 1.5708
    c: Tangent(g3,g7) = 1.5708
    c: Equal(g0,g3)
    c: Radius(g4) = 2
    c: Equal(g4,g5)
    c: Equal(g4,g6)
    c: Equal(g4,g7)
    c: Coincident(g8,g4)
    c: Coincident(g8,g-1)
    c: Coincident(g9,g-1)
    c: Coincident(g9,g5)
    c: Coincident(g10,g-1)
    c: Coincident(g10,g7)
    c: Equal(g10,g8)
    c: Equal(g8,g9)
    c: DistanceX(g3,g1) = 106.6
FEATURE [PartDesign::Pad] Pad052  label="Face"
  AllowMultiFace = false
  Direction = (1,1,1)
  Length = 1.5
  Length2 = 100
  Profile = -> Sketch300
  Refine = true
  Type = 0
FEATURE [Sketcher::SketchObject] Sketch301
  FullyConstrained = false
  MapMode = 5
  Placement = pos=(0,0,1.5) rot=(0,0,1;0rad)
  Support = -> [Pad052]
  sketch-geometry (9):
    g0: LineSegment StartX=-50.5 StartY=50.5 StartZ=0 EndX=-50.5 EndY=-50.5 EndZ=0
    g1: LineSegment StartX=-50.5 StartY=-50.5 StartZ=0 EndX=50.5 EndY=-50.5 EndZ=0
    g2: LineSegment StartX=50.5 StartY=-50.5 StartZ=0 EndX=50.5 EndY=50.5 EndZ=0
    g3: LineSegment StartX=50.5 StartY=50.5 StartZ=0 EndX=-50.5 EndY=50.5 EndZ=0
    g4: Circle CenterX=0 CenterY=0 CenterZ=0 NormalX=0 NormalY=0 NormalZ=1 AngleXU=0 Radius=71.4178
    g5: Circle CenterX=-50.5 CenterY=50.5 CenterZ=0 NormalX=0 NormalY=0 NormalZ=1 AngleXU=0 Radius=0.5
    g6: Circle CenterX=50.5 CenterY=50.5 CenterZ=0 NormalX=0 NormalY=0 NormalZ=1 AngleXU=0 Radius=0.5
    g7: Circle CenterX=-50.5 CenterY=-50.5 CenterZ=0 NormalX=0 NormalY=0 NormalZ=1 AngleXU=0 Radius=0.5
    g8: Circle CenterX=50.5 CenterY=-50.5 CenterZ=0 NormalX=0 NormalY=0 NormalZ=1 AngleXU=0 Radius=0.5
  constraints (22):
    c: Coincident(g0,g1)
    c: Coincident(g1,g2)
    c: Coincident(g2,g3)
    c: Coincident(g3,g0)
    c: Equal(g0,g1)
    c: Equal(g0,g2)
    c: Equal(g0,g3)
    c: PointOnObject(g0,g4)
    c: PointOnObject(g1,g4)
    c: PointOnObject(g2,g4)
    c: PointOnObject(g3,g4)
    c: Coincident(g4,g-1)
    c: Horizontal(g3)
    c: DistanceX(g3,g3) = 101
    c: Coincident(g5,g0)
    c: Coincident(g6,g2)
    c: Coincident(g7,g0)
    c: Coincident(g8,g1)
    c: Radius(g8) = 0.5
    c: Equal(g8,g7)
    c: Equal(g8,g5)
    c: Equal(g8,g6)
FEATURE [PartDesign::Hole] Hole  label="CornerHole"
  AllowMultiFace = false
  BaseFeature = -> Pad052
  CustomThreadClearance = 0
  Depth = 26
  DepthType = 1
  Diameter = 2.2
  DrillForDepth = false
  DrillPoint = 0
  DrillPointAngle = 118
  HoleCutCountersinkAngle = 90
  HoleCutCustomValues = false
  HoleCutDepth = 0
  HoleCutDiameter = 4.2
  HoleCutType = 2
  ModelThread = false
  Profile = -> Sketch301
  Refine = true
  Tapered = false
  TaperedAngle = 90
  ThreadClass = 0
  ThreadDepth = 23.5
  ThreadDepthType = 0
  ThreadDirection = 0
  ThreadFit = 0
  ThreadSize = 0
  ThreadType = 0
  Threaded = false
  UseCustomThreadClearance = false
FEATURE [Sketcher::SketchObject] Sketch302
  FullyConstrained = false
  MapMode = 5
  Placement = pos=(0,0,1.5) rot=(0,0,1;0rad)
  Support = -> [Hole]
  sketch-geometry (11):
    g0: LineSegment StartX=-43 StartY=45 StartZ=0 EndX=43 EndY=45 EndZ=0
    g1: LineSegment StartX=45 StartY=43 StartZ=0 EndX=45 EndY=-43 EndZ=0
    g2: LineSegment StartX=43 StartY=-45 StartZ=0 EndX=-43 EndY=-45 EndZ=0
    g3: LineSegment StartX=-45 StartY=-43 StartZ=0 EndX=-45 EndY=43 EndZ=0
    g4: ArcOfCircle CenterX=-43 CenterY=43 CenterZ=0 NormalX=0 NormalY=0 NormalZ=1 AngleXU=0 Radius=2 StartAngle=1.5708 EndAngle=3.14159
    g5: ArcOfCircle CenterX=43 CenterY=43 CenterZ=0 NormalX=0 NormalY=0 NormalZ=1 AngleXU=0 Radius=2 StartAngle=4e-16 EndAngle=1.5708
    g6: ArcOfCircle CenterX=43 CenterY=-43 CenterZ=0 NormalX=0 NormalY=0 NormalZ=1 AngleXU=0 Radius=2 StartAngle=4.71239 EndAngle=6.28319
    g7: ArcOfCircle CenterX=-43 CenterY=-43 CenterZ=0 NormalX=0 NormalY=0 NormalZ=1 AngleXU=0 Radius=2 StartAngle=3.14159 EndAngle=4.71239
    g8: LineSegment StartX=-43 StartY=43 StartZ=0 EndX=0 EndY=0 EndZ=0
    g9: LineSegment StartX=0 StartY=0 StartZ=0 EndX=43 EndY=43 EndZ=0
    g10: LineSegment StartX=0 StartY=0 StartZ=0 EndX=43 EndY=-43 EndZ=0
  constraints (26):
    c: Horizontal(g0)
    c: Horizontal(g2)
    c: Vertical(g1)
    c: Vertical(g3)
    c: Tangent(g3,g4) = 1.5708
    c: Tangent(g0,g4) = 1.5708
    c: Tangent(g0,g5) = 1.5708
    c: Tangent(g1,g5) = 1.5708
    c: Tangent(g1,g6) = 1.5708
    c: Tangent(g2,g6) = 1.5708
    c: Tangent(g2,g7) = 1.5708
    c: Tangent(g3,g7) = 1.5708
    c: Equal(g4,g5)
    c: Equal(g5,g6)
    c: Equal(g6,g7)
    c: Equal(g3,g0)
    c: Coincident(g8,g4)
    c: Coincident(g8,g-1)
    c: Coincident(g8,g9)
    c: Coincident(g9,g5)
    c: Coincident(g-1,g10)
    c: Coincident(g10,g6)
    c: Equal(g10,g9)
    c: Equal(g9,g8)
    c: Radius(g4) = 2
    c: DistanceX(g3,g1) = 90
FEATURE [PartDesign::Pocket] Pocket048
  AllowMultiFace = false
  BaseFeature = -> Hole
  Direction = (1,1,1)
  Length = 5
  Length2 = 100
  Profile = -> Sketch302
  Type = 0
FEATURE [PartDesign::Draft] Draft
  Angle = 45
  Base = -> Pocket048 [Face19,Face18,Face17,Face16,Face15,Face14,Face12,Face13]
  BaseFeature = -> Pocket048
  NeutralPlane = -> Pocket048 [Face5]
  Reversed = true
  SupportTransform = false
FEATURE [PartDesign::Body] Body103  label="grid_frontpanel_common"
  Group = -> [Sketch300,Pad052,Sketch301,Hole,Sketch302,Pocket048,Draft]
  Origin = -> Origin755
  Tip = -> Draft
FEATURE [App::VRMLObject] XY
  Placement = pos=(0,0,-0.8) rot=(0,0,1;0rad)
FEATURE [App::Part] Part071  label="XY001"
  Group = -> [Body103,XY]
  Origin = -> Origin754
FEATURE [Sketcher::SketchObject] Sketch303
  FullyConstrained = false
  MapMode = 5
  Support = -> [XY_Plane757]
  sketch-geometry (1):
    g0: Circle CenterX=0 CenterY=0 CenterZ=0 NormalX=0 NormalY=0 NormalZ=1 AngleXU=0 Radius=1.5
  constraints (2):
    c: Coincident(g0,g-1)
    c: Radius(g0) = 1.5
FEATURE [PartDesign::Pad] Pad053
  AllowMultiFace = false
  Direction = (1,1,1)
  Length = 13.6
  Length2 = 100
  Profile = -> Sketch303
  Refine = true
  Reversed = true
  Type = 0
FEATURE [PartDesign::Chamfer] Chamfer034
  Angle = 45
  Base = -> Pad053 [Edge2,Edge3]
  BaseFeature = -> Pad053
  ChamferType = 0
  FlipDirection = false
  Size = 0.1
  Size2 = 1
  SupportTransform = false
  UseAllEdges = false
FEATURE [PartDesign::Body] Body104
  Group = -> [Sketch303,Pad053,Chamfer034]
  Origin = -> Origin757
  Placement = pos=(0,0,-0.2) rot=(0,0,1;0rad)
  Tip = -> Chamfer034
FEATURE [App::Part] Part072  label="Magnet002"
  Group = -> [Body104]
  Origin = -> Origin756
  Placement = pos=(-47,51.45,0) rot=(0,0,1;0rad)
FEATURE [Sketcher::SketchObject] Sketch304
  FullyConstrained = false
  MapMode = 5
  Support = -> [XY_Plane759]
  sketch-geometry (1):
    g0: Circle CenterX=0 CenterY=0 CenterZ=0 NormalX=0 NormalY=0 NormalZ=1 AngleXU=0 Radius=1.5
  constraints (2):
    c: Coincident(g0,g-1)
    c: Radius(g0) = 1.5
FEATURE [PartDesign::Pad] Pad054
  AllowMultiFace = false
  Direction = (1,1,1)
  Length = 13.6
  Length2 = 100
  Profile = -> Sketch304
  Refine = true
  Reversed = true
  Type = 0
FEATURE [PartDesign::Chamfer] Chamfer035
  Angle = 45
  Base = -> Pad054 [Edge2,Edge3]
  BaseFeature = -> Pad054
  ChamferType = 0
  FlipDirection = false
  Size = 0.1
  Size2 = 1
  SupportTransform = false
  UseAllEdges = false
FEATURE [PartDesign::Body] Body105
  Group = -> [Sketch304,Pad054,Chamfer035]
  Origin = -> Origin759
  Placement = pos=(0,0,-0.2) rot=(0,0,1;0rad)
  Tip = -> Chamfer035
FEATURE [App::Part] Part073  label="Magnet003"
  Group = -> [Body105]
  Origin = -> Origin758
  Placement = pos=(47,-51.45,0) rot=(0,0,1;0rad)
FEATURE [Sketcher::SketchObject] Sketch305
  FullyConstrained = false
  MapMode = 5
  Support = -> [XY_Plane761]
  sketch-geometry (1):
    g0: Circle CenterX=0 CenterY=0 CenterZ=0 NormalX=0 NormalY=0 NormalZ=1 AngleXU=0 Radius=1.5
  constraints (2):
    c: Coincident(g0,g-1)
    c: Radius(g0) = 1.5
FEATURE [PartDesign::Pad] Pad055
  AllowMultiFace = false
  Direction = (1,1,1)
  Length = 13.6
  Length2 = 100
  Profile = -> Sketch305
  Refine = true
  Reversed = true
  Type = 0
FEATURE [PartDesign::Chamfer] Chamfer036
  Angle = 45
  Base = -> Pad055 [Edge2,Edge3]
  BaseFeature = -> Pad055
  ChamferType = 0
  FlipDirection = false
  Size = 0.1
  Size2 = 1
  SupportTransform = false
  UseAllEdges = false
FEATURE [PartDesign::Body] Body106
  Group = -> [Sketch305,Pad055,Chamfer036]
  Origin = -> Origin761
  Placement = pos=(0,0,-0.2) rot=(0,0,1;0rad)
  Tip = -> Chamfer036
FEATURE [App::Part] Part074  label="Magnet004"
  Group = -> [Body106]
  Origin = -> Origin760
  Placement = pos=(-47,-51.45,0) rot=(0,0,1;0rad)
FEATURE [Sketcher::SketchObject] Sketch306
  FullyConstrained = false
  MapMode = 5
  Support = -> [XY_Plane763]
  sketch-geometry (1):
    g0: Circle CenterX=0 CenterY=0 CenterZ=0 NormalX=0 NormalY=0 NormalZ=1 AngleXU=0 Radius=1.5
  constraints (2):
    c: Coincident(g0,g-1)
    c: Radius(g0) = 1.5
FEATURE [PartDesign::Pad] Pad056
  AllowMultiFace = false
  Direction = (1,1,1)
  Length = 13.6
  Length2 = 100
  Profile = -> Sketch306
  Refine = true
  Reversed = true
  Type = 0
FEATURE [PartDesign::Chamfer] Chamfer037
  Angle = 45
  Base = -> Pad056 [Edge2,Edge3]
  BaseFeature = -> Pad056
  ChamferType = 0
  FlipDirection = false
  Size = 0.1
  Size2 = 1
  SupportTransform = false
  UseAllEdges = false
FEATURE [PartDesign::Body] Body107
  Group = -> [Sketch306,Pad056,Chamfer037]
  Origin = -> Origin763
  Placement = pos=(0,0,-0.2) rot=(0,0,1;0rad)
  Tip = -> Chamfer037
FEATURE [App::Part] Part075  label="Magnet005"
  Group = -> [Body107]
  Origin = -> Origin762
  Placement = pos=(51.45,47,0) rot=(0,0,1;0rad)
FEATURE [Sketcher::SketchObject] Sketch307
  FullyConstrained = false
  MapMode = 5
  Support = -> [XY_Plane765]
  sketch-geometry (1):
    g0: Circle CenterX=0 CenterY=0 CenterZ=0 NormalX=0 NormalY=0 NormalZ=1 AngleXU=0 Radius=1.5
  constraints (2):
    c: Coincident(g0,g-1)
    c: Radius(g0) = 1.5
FEATURE [PartDesign::Pad] Pad057
  AllowMultiFace = false
  Direction = (1,1,1)
  Length = 13.6
  Length2 = 100
  Profile = -> Sketch307
  Refine = true
  Reversed = true
  Type = 0
FEATURE [PartDesign::Chamfer] Chamfer038
  Angle = 45
  Base = -> Pad057 [Edge2,Edge3]
  BaseFeature = -> Pad057
  ChamferType = 0
  FlipDirection = false
  Size = 0.1
  Size2 = 1
  SupportTransform = false
  UseAllEdges = false
FEATURE [PartDesign::Body] Body108
  Group = -> [Sketch307,Pad057,Chamfer038]
  Origin = -> Origin764
  Placement = pos=(0,0,-0.2) rot=(0,0,1;0rad)
  Tip = -> Chamfer038
FEATURE [App::Part] Part076  label="Magnet006"
  Group = -> [Body108]
  Origin = -> Origin765
  Placement = pos=(-51.45,47,0) rot=(0,0,1;0rad)
FEATURE [Sketcher::SketchObject] Sketch308
  FullyConstrained = false
  MapMode = 5
  Support = -> [XY_Plane767]
  sketch-geometry (1):
    g0: Circle CenterX=0 CenterY=0 CenterZ=0 NormalX=0 NormalY=0 NormalZ=1 AngleXU=0 Radius=1.5
  constraints (2):
    c: Coincident(g0,g-1)
    c: Radius(g0) = 1.5
FEATURE [PartDesign::Pad] Pad058
  AllowMultiFace = false
  Direction = (1,1,1)
  Length = 13.6
  Length2 = 100
  Profile = -> Sketch308
  Refine = true
  Reversed = true
  Type = 0
FEATURE [PartDesign::Chamfer] Chamfer039
  Angle = 45
  Base = -> Pad058 [Edge2,Edge3]
  BaseFeature = -> Pad058
  ChamferType = 0
  FlipDirection = false
  Size = 0.1
  Size2 = 1
  SupportTransform = false
  UseAllEdges = false
FEATURE [PartDesign::Body] Body109
  Group = -> [Sketch308,Pad058,Chamfer039]
  Origin = -> Origin766
  Placement = pos=(0,0,-0.2) rot=(0,0,1;0rad)
  Tip = -> Chamfer039
FEATURE [App::Part] Part077  label="Magnet007"
  Group = -> [Body109]
  Origin = -> Origin767
  Placement = pos=(51.45,-47,0) rot=(0,0,1;0rad)
FEATURE [Sketcher::SketchObject] Sketch309
  FullyConstrained = false
  MapMode = 5
  Support = -> [XY_Plane769]
  sketch-geometry (1):
    g0: Circle CenterX=0 CenterY=0 CenterZ=0 NormalX=0 NormalY=0 NormalZ=1 AngleXU=0 Radius=1.5
  constraints (2):
    c: Coincident(g0,g-1)
    c: Radius(g0) = 1.5
FEATURE [PartDesign::Pad] Pad059
  AllowMultiFace = false
  Direction = (1,1,1)
  Length = 13.6
  Length2 = 100
  Profile = -> Sketch309
  Refine = true
  Reversed = true
  Type = 0
FEATURE [PartDesign::Chamfer] Chamfer040
  Angle = 45
  Base = -> Pad059 [Edge2,Edge3]
  BaseFeature = -> Pad059
  ChamferType = 0
  FlipDirection = false
  Size = 0.1
  Size2 = 1
  SupportTransform = false
  UseAllEdges = false
FEATURE [PartDesign::Body] Body110
  Group = -> [Sketch309,Pad059,Chamfer040]
  Origin = -> Origin768
  Placement = pos=(0,0,-0.2) rot=(0,0,1;0rad)
  Tip = -> Chamfer040
FEATURE [App::Part] Part078  label="Magnet008"
  Group = -> [Body110]
  Origin = -> Origin769
  Placement = pos=(-51.45,-47,0) rot=(0,0,1;0rad)
FEATURE [App::Part] Part037  label="Magnet"
  Group = -> [Part038,Part072,Part073,Part074,Part075,Part076,Part077,Part078]
  Origin = -> Origin119
FEATURE [Part::Feature] Part__Feature1021  label="mapmode8"
  Placement = pos=(0,0,0) rot=(0,0,1;3.14159rad)
  shape: bbox 9.75 x 4.15 x 8.375 mm, 19 faces (baked)
FEATURE [Mesh::Feature] Body111
  Placement = pos=(50.5,50.5,1.5) rot=(0,0,1;0rad)
FEATURE [Mesh::Feature] Body112
  Placement = pos=(-50.5,50.5,1.5) rot=(0,0,1;0rad)
FEATURE [Mesh::Feature] Body113
  Placement = pos=(50.5,-50.5,1.5) rot=(0,0,1;0rad)
FEATURE [Mesh::Feature] Body114
  Placement = pos=(-50.5,-50.5,1.5) rot=(0,0,1;0rad)
FEATURE [App::Part] Part079  label="Screws"
  Group = -> [Body111,Body112,Body113,Body114]
  Origin = -> Origin770
FEATURE [Sketcher::SketchObject] Sketch310
  FullyConstrained = false
  MapMode = 5
  Placement = pos=(0,0,0) rot=(0.57735,0.57735,0.57735;2.0944rad)
  Support = -> [YZ_Plane788]
  sketch-geometry (6):
    g0: LineSegment StartX=0 StartY=0 StartZ=0 EndX=-1.6 EndY=0 EndZ=0
    g1: LineSegment StartX=-1.6 StartY=0 StartZ=0 EndX=-1.6 EndY=-0.4 EndZ=0
    g2: LineSegment StartX=-1.6 StartY=-0.4 StartZ=0 EndX=-1.5 EndY=-0.4 EndZ=0
    g3: LineSegment StartX=-1.5 StartY=-0.4 StartZ=0 EndX=-1.5 EndY=-7 EndZ=0
    g4: LineSegment StartX=-1.5 StartY=-7 StartZ=0 EndX=0 EndY=-7 EndZ=0
    g5: LineSegment StartX=0 StartY=-7 StartZ=0 EndX=0 EndY=0 EndZ=0
  constraints (17):
    c: Coincident(g0,g-1)
    c: Horizontal(g0)
    c: Coincident(g1,g0)
    c: Coincident(g2,g1)
    c: Coincident(g3,g2)
    c: Vertical(g3)
    c: Coincident(g4,g3)
    c: Coincident(g5,g4)
    c: Coincident(g5,g-1)
    c: Vertical(g5)
    c: Horizontal(g4)
    c: Horizontal(g2)
    c: Vertical(g1)
    c: DistanceY(g1,g1) = 0.4
    c: DistanceX(g4,g4) = 1.5
    c: DistanceX(g0,g0) = 1.6
    c: DistanceY(g5,g5) = 7
FEATURE [PartDesign::Revolution] Revolution023
  AllowMultiFace = false
  Angle = 360
  Axis = (0,0,1)
  Base = (0,0,0)
  Placement = pos=(0,0,0) rot=(0.57735,0.57735,0.57735;2.0944rad)
  Profile = -> Sketch310
  ReferenceAxis = -> Sketch310 [V_Axis]
FEATURE [Sketcher::SketchObject] Sketch311
  FullyConstrained = false
  MapMode = 5
  Placement = pos=(0,0,0) rot=(0.57735,0.57735,0.57735;2.0944rad)
  Support = -> [YZ_Plane786]
  sketch-geometry (6):
    g0: LineSegment StartX=0 StartY=0 StartZ=0 EndX=-1.6 EndY=0 EndZ=0
    g1: LineSegment StartX=-1.6 StartY=0 StartZ=0 EndX=-1.6 EndY=-0.4 EndZ=0
    g2: LineSegment StartX=-1.6 StartY=-0.4 StartZ=0 EndX=-1.5 EndY=-0.4 EndZ=0
    g3: LineSegment StartX=-1.5 StartY=-0.4 StartZ=0 EndX=-1.5 EndY=-7 EndZ=0
    g4: LineSegment StartX=-1.5 StartY=-7 StartZ=0 EndX=0 EndY=-7 EndZ=0
    g5: LineSegment StartX=0 StartY=-7 StartZ=0 EndX=0 EndY=0 EndZ=0
  constraints (17):
    c: Coincident(g0,g-1)
    c: Horizontal(g0)
    c: Coincident(g1,g0)
    c: Coincident(g2,g1)
    c: Coincident(g3,g2)
    c: Vertical(g3)
    c: Coincident(g4,g3)
    c: Coincident(g5,g4)
    c: Coincident(g5,g-1)
    c: Vertical(g5)
    c: Horizontal(g4)
    c: Horizontal(g2)
    c: Vertical(g1)
    c: DistanceY(g1,g1) = 0.4
    c: DistanceX(g4,g4) = 1.5
    c: DistanceX(g0,g0) = 1.6
    c: DistanceY(g5,g5) = 7
FEATURE [PartDesign::Revolution] Revolution026
  AllowMultiFace = false
  Angle = 360
  Axis = (0,0,1)
  Base = (0,0,0)
  Placement = pos=(0,0,0) rot=(0.57735,0.57735,0.57735;2.0944rad)
  Profile = -> Sketch311
  ReferenceAxis = -> Sketch311 [V_Axis]
FEATURE [Sketcher::SketchObject] Sketch312
  FullyConstrained = false
  MapMode = 5
  Placement = pos=(0,0,0) rot=(0.57735,0.57735,0.57735;2.0944rad)
  Support = -> [YZ_Plane787]
  sketch-geometry (6):
    g0: LineSegment StartX=0 StartY=0 StartZ=0 EndX=-1.6 EndY=0 EndZ=0
    g1: LineSegment StartX=-1.6 StartY=0 StartZ=0 EndX=-1.6 EndY=-0.4 EndZ=0
    g2: LineSegment StartX=-1.6 StartY=-0.4 StartZ=0 EndX=-1.5 EndY=-0.4 EndZ=0
    g3: LineSegment StartX=-1.5 StartY=-0.4 StartZ=0 EndX=-1.5 EndY=-7 EndZ=0
    g4: LineSegment StartX=-1.5 StartY=-7 StartZ=0 EndX=0 EndY=-7 EndZ=0
    g5: LineSegment StartX=0 StartY=-7 StartZ=0 EndX=0 EndY=0 EndZ=0
  constraints (17):
    c: Coincident(g0,g-1)
    c: Horizontal(g0)
    c: Coincident(g1,g0)
    c: Coincident(g2,g1)
    c: Coincident(g3,g2)
    c: Vertical(g3)
    c: Coincident(g4,g3)
    c: Coincident(g5,g4)
    c: Coincident(g5,g-1)
    c: Vertical(g5)
    c: Horizontal(g4)
    c: Horizontal(g2)
    c: Vertical(g1)
    c: DistanceY(g1,g1) = 0.4
    c: DistanceX(g4,g4) = 1.5
    c: DistanceX(g0,g0) = 1.6
    c: DistanceY(g5,g5) = 7
FEATURE [PartDesign::Revolution] Revolution025
  AllowMultiFace = false
  Angle = 360
  Axis = (0,0,1)
  Base = (0,0,0)
  Placement = pos=(0,0,0) rot=(0.57735,0.57735,0.57735;2.0944rad)
  Profile = -> Sketch312
  ReferenceAxis = -> Sketch312 [V_Axis]
FEATURE [Sketcher::SketchObject] Sketch313
  FullyConstrained = false
  MapMode = 5
  Placement = pos=(0,0,0) rot=(0.57735,0.57735,0.57735;2.0944rad)
  Support = -> [YZ_Plane792]
  sketch-geometry (6):
    g0: LineSegment StartX=0 StartY=0 StartZ=0 EndX=-1.6 EndY=0 EndZ=0
    g1: LineSegment StartX=-1.6 StartY=0 StartZ=0 EndX=-1.6 EndY=-0.4 EndZ=0
    g2: LineSegment StartX=-1.6 StartY=-0.4 StartZ=0 EndX=-1.5 EndY=-0.4 EndZ=0
    g3: LineSegment StartX=-1.5 StartY=-0.4 StartZ=0 EndX=-1.5 EndY=-7 EndZ=0
    g4: LineSegment StartX=-1.5 StartY=-7 StartZ=0 EndX=0 EndY=-7 EndZ=0
    g5: LineSegment StartX=0 StartY=-7 StartZ=0 EndX=0 EndY=0 EndZ=0
  constraints (17):
    c: Coincident(g0,g-1)
    c: Horizontal(g0)
    c: Coincident(g1,g0)
    c: Coincident(g2,g1)
    c: Coincident(g3,g2)
    c: Vertical(g3)
    c: Coincident(g4,g3)
    c: Coincident(g5,g4)
    c: Coincident(g5,g-1)
    c: Vertical(g5)
    c: Horizontal(g4)
    c: Horizontal(g2)
    c: Vertical(g1)
    c: DistanceY(g1,g1) = 0.4
    c: DistanceX(g4,g4) = 1.5
    c: DistanceX(g0,g0) = 1.6
    c: DistanceY(g5,g5) = 7
FEATURE [PartDesign::Revolution] Revolution022
  AllowMultiFace = false
  Angle = 360
  Axis = (0,0,1)
  Base = (0,0,0)
  Placement = pos=(0,0,0) rot=(0.57735,0.57735,0.57735;2.0944rad)
  Profile = -> Sketch313
  ReferenceAxis = -> Sketch313 [V_Axis]
FEATURE [Sketcher::SketchObject] Sketch314
  FullyConstrained = false
  MapMode = 5
  Placement = pos=(0,0,0) rot=(0.57735,0.57735,0.57735;2.0944rad)
  Support = -> [YZ_Plane801]
  sketch-geometry (6):
    g0: LineSegment StartX=0 StartY=0 StartZ=0 EndX=-1.6 EndY=0 EndZ=0
    g1: LineSegment StartX=-1.6 StartY=0 StartZ=0 EndX=-1.6 EndY=-0.4 EndZ=0
    g2: LineSegment StartX=-1.6 StartY=-0.4 StartZ=0 EndX=-1.5 EndY=-0.4 EndZ=0
    g3: LineSegment StartX=-1.5 StartY=-0.4 StartZ=0 EndX=-1.5 EndY=-7 EndZ=0
    g4: LineSegment StartX=-1.5 StartY=-7 StartZ=0 EndX=0 EndY=-7 EndZ=0
    g5: LineSegment StartX=0 StartY=-7 StartZ=0 EndX=0 EndY=0 EndZ=0
  constraints (17):
    c: Coincident(g0,g-1)
    c: Horizontal(g0)
    c: Coincident(g1,g0)
    c: Coincident(g2,g1)
    c: Coincident(g3,g2)
    c: Vertical(g3)
    c: Coincident(g4,g3)
    c: Coincident(g5,g4)
    c: Coincident(g5,g-1)
    c: Vertical(g5)
    c: Horizontal(g4)
    c: Horizontal(g2)
    c: Vertical(g1)
    c: DistanceY(g1,g1) = 0.4
    c: DistanceX(g4,g4) = 1.5
    c: DistanceX(g0,g0) = 1.6
    c: DistanceY(g5,g5) = 7
FEATURE [PartDesign::Revolution] Revolution021
  AllowMultiFace = false
  Angle = 360
  Axis = (0,0,1)
  Base = (0,0,0)
  Placement = pos=(0,0,0) rot=(0.57735,0.57735,0.57735;2.0944rad)
  Profile = -> Sketch314
  ReferenceAxis = -> Sketch314 [V_Axis]
FEATURE [Sketcher::SketchObject] Sketch315
  FullyConstrained = false
  MapMode = 5
  Placement = pos=(0,0,0) rot=(0.57735,0.57735,0.57735;2.0944rad)
  Support = -> [YZ_Plane802]
  sketch-geometry (6):
    g0: LineSegment StartX=0 StartY=0 StartZ=0 EndX=-1.6 EndY=0 EndZ=0
    g1: LineSegment StartX=-1.6 StartY=0 StartZ=0 EndX=-1.6 EndY=-0.4 EndZ=0
    g2: LineSegment StartX=-1.6 StartY=-0.4 StartZ=0 EndX=-1.5 EndY=-0.4 EndZ=0
    g3: LineSegment StartX=-1.5 StartY=-0.4 StartZ=0 EndX=-1.5 EndY=-7 EndZ=0
    g4: LineSegment StartX=-1.5 StartY=-7 StartZ=0 EndX=0 EndY=-7 EndZ=0
    g5: LineSegment StartX=0 StartY=-7 StartZ=0 EndX=0 EndY=0 EndZ=0
  constraints (17):
    c: Coincident(g0,g-1)
    c: Horizontal(g0)
    c: Coincident(g1,g0)
    c: Coincident(g2,g1)
    c: Coincident(g3,g2)
    c: Vertical(g3)
    c: Coincident(g4,g3)
    c: Coincident(g5,g4)
    c: Coincident(g5,g-1)
    c: Vertical(g5)
    c: Horizontal(g4)
    c: Horizontal(g2)
    c: Vertical(g1)
    c: DistanceY(g1,g1) = 0.4
    c: DistanceX(g4,g4) = 1.5
    c: DistanceX(g0,g0) = 1.6
    c: DistanceY(g5,g5) = 7
FEATURE [PartDesign::Revolution] Revolution027
  AllowMultiFace = false
  Angle = 360
  Axis = (0,0,1)
  Base = (0,0,0)
  Placement = pos=(0,0,0) rot=(0.57735,0.57735,0.57735;2.0944rad)
  Profile = -> Sketch315
  ReferenceAxis = -> Sketch315 [V_Axis]
FEATURE [Sketcher::SketchObject] Sketch316
  FullyConstrained = false
  MapMode = 5
  Placement = pos=(0,0,0) rot=(0.57735,0.57735,0.57735;2.0944rad)
  Support = -> [YZ_Plane793]
  sketch-geometry (6):
    g0: LineSegment StartX=0 StartY=0 StartZ=0 EndX=-1.6 EndY=0 EndZ=0
    g1: LineSegment StartX=-1.6 StartY=0 StartZ=0 EndX=-1.6 EndY=-0.4 EndZ=0
    g2: LineSegment StartX=-1.6 StartY=-0.4 StartZ=0 EndX=-1.5 EndY=-0.4 EndZ=0
    g3: LineSegment StartX=-1.5 StartY=-0.4 StartZ=0 EndX=-1.5 EndY=-7 EndZ=0
    g4: LineSegment StartX=-1.5 StartY=-7 StartZ=0 EndX=0 EndY=-7 EndZ=0
    g5: LineSegment StartX=0 StartY=-7 StartZ=0 EndX=0 EndY=0 EndZ=0
  constraints (17):
    c: Coincident(g0,g-1)
    c: Horizontal(g0)
    c: Coincident(g1,g0)
    c: Coincident(g2,g1)
    c: Coincident(g3,g2)
    c: Vertical(g3)
    c: Coincident(g4,g3)
    c: Coincident(g5,g4)
    c: Coincident(g5,g-1)
    c: Vertical(g5)
    c: Horizontal(g4)
    c: Horizontal(g2)
    c: Vertical(g1)
    c: DistanceY(g1,g1) = 0.4
    c: DistanceX(g4,g4) = 1.5
    c: DistanceX(g0,g0) = 1.6
    c: DistanceY(g5,g5) = 7
FEATURE [PartDesign::Revolution] Revolution024
  AllowMultiFace = false
  Angle = 360
  Axis = (0,0,1)
  Base = (0,0,0)
  Placement = pos=(0,0,0) rot=(0.57735,0.57735,0.57735;2.0944rad)
  Profile = -> Sketch316
  ReferenceAxis = -> Sketch316 [V_Axis]
FEATURE [Sketcher::SketchObject] Sketch317
  FullyConstrained = false
  MapMode = 5
  Placement = pos=(0,0,0) rot=(0.57735,0.57735,0.57735;2.0944rad)
  Support = -> [YZ_Plane798]
  sketch-geometry (6):
    g0: LineSegment StartX=0 StartY=0 StartZ=0 EndX=-1.6 EndY=0 EndZ=0
    g1: LineSegment StartX=-1.6 StartY=0 StartZ=0 EndX=-1.6 EndY=-0.4 EndZ=0
    g2: LineSegment StartX=-1.6 StartY=-0.4 StartZ=0 EndX=-1.5 EndY=-0.4 EndZ=0
    g3: LineSegment StartX=-1.5 StartY=-0.4 StartZ=0 EndX=-1.5 EndY=-7 EndZ=0
    g4: LineSegment StartX=-1.5 StartY=-7 StartZ=0 EndX=0 EndY=-7 EndZ=0
    g5: LineSegment StartX=0 StartY=-7 StartZ=0 EndX=0 EndY=0 EndZ=0
  constraints (17):
    c: Coincident(g0,g-1)
    c: Horizontal(g0)
    c: Coincident(g1,g0)
    c: Coincident(g2,g1)
    c: Coincident(g3,g2)
    c: Vertical(g3)
    c: Coincident(g4,g3)
    c: Coincident(g5,g4)
    c: Coincident(g5,g-1)
    c: Vertical(g5)
    c: Horizontal(g4)
    c: Horizontal(g2)
    c: Vertical(g1)
    c: DistanceY(g1,g1) = 0.4
    c: DistanceX(g4,g4) = 1.5
    c: DistanceX(g0,g0) = 1.6
    c: DistanceY(g5,g5) = 7
FEATURE [Sketcher::SketchObject] Sketch318
  FullyConstrained = false
  MapMode = 5
  Placement = pos=(0,0,0) rot=(0.57735,0.57735,0.57735;2.0944rad)
  Support = -> [YZ_Plane800]
  sketch-geometry (6):
    g0: LineSegment StartX=0 StartY=0 StartZ=0 EndX=-1.6 EndY=0 EndZ=0
    g1: LineSegment StartX=-1.6 StartY=0 StartZ=0 EndX=-1.6 EndY=-0.4 EndZ=0
    g2: LineSegment StartX=-1.6 StartY=-0.4 StartZ=0 EndX=-1.5 EndY=-0.4 EndZ=0
    g3: LineSegment StartX=-1.5 StartY=-0.4 StartZ=0 EndX=-1.5 EndY=-7 EndZ=0
    g4: LineSegment StartX=-1.5 StartY=-7 StartZ=0 EndX=0 EndY=-7 EndZ=0
    g5: LineSegment StartX=0 StartY=-7 StartZ=0 EndX=0 EndY=0 EndZ=0
  constraints (17):
    c: Coincident(g0,g-1)
    c: Horizontal(g0)
    c: Coincident(g1,g0)
    c: Coincident(g2,g1)
    c: Coincident(g3,g2)
    c: Vertical(g3)
    c: Coincident(g4,g3)
    c: Coincident(g5,g4)
    c: Coincident(g5,g-1)
    c: Vertical(g5)
    c: Horizontal(g4)
    c: Horizontal(g2)
    c: Vertical(g1)
    c: DistanceY(g1,g1) = 0.4
    c: DistanceX(g4,g4) = 1.5
    c: DistanceX(g0,g0) = 1.6
    c: DistanceY(g5,g5) = 7
FEATURE [PartDesign::Revolution] Revolution020
  AllowMultiFace = false
  Angle = 360
  Axis = (0,0,1)
  Base = (0,0,0)
  Placement = pos=(0,0,0) rot=(0.57735,0.57735,0.57735;2.0944rad)
  Profile = -> Sketch318
  ReferenceAxis = -> Sketch318 [V_Axis]
FEATURE [Sketcher::SketchObject] Sketch319
  FullyConstrained = false
  MapMode = 5
  Placement = pos=(0,0,0) rot=(0.57735,0.57735,0.57735;2.0944rad)
  Support = -> [YZ_Plane796]
  sketch-geometry (6):
    g0: LineSegment StartX=0 StartY=0 StartZ=0 EndX=-1.6 EndY=0 EndZ=0
    g1: LineSegment StartX=-1.6 StartY=0 StartZ=0 EndX=-1.6 EndY=-0.4 EndZ=0
    g2: LineSegment StartX=-1.6 StartY=-0.4 StartZ=0 EndX=-1.5 EndY=-0.4 EndZ=0
    g3: LineSegment StartX=-1.5 StartY=-0.4 StartZ=0 EndX=-1.5 EndY=-7 EndZ=0
    g4: LineSegment StartX=-1.5 StartY=-7 StartZ=0 EndX=0 EndY=-7 EndZ=0
    g5: LineSegment StartX=0 StartY=-7 StartZ=0 EndX=0 EndY=0 EndZ=0
  constraints (17):
    c: Coincident(g0,g-1)
    c: Horizontal(g0)
    c: Coincident(g1,g0)
    c: Coincident(g2,g1)
    c: Coincident(g3,g2)
    c: Vertical(g3)
    c: Coincident(g4,g3)
    c: Coincident(g5,g4)
    c: Coincident(g5,g-1)
    c: Vertical(g5)
    c: Horizontal(g4)
    c: Horizontal(g2)
    c: Vertical(g1)
    c: DistanceY(g1,g1) = 0.4
    c: DistanceX(g4,g4) = 1.5
    c: DistanceX(g0,g0) = 1.6
    c: DistanceY(g5,g5) = 7
FEATURE [PartDesign::Revolution] Revolution028
  AllowMultiFace = false
  Angle = 360
  Axis = (0,0,1)
  Base = (0,0,0)
  Placement = pos=(0,0,0) rot=(0.57735,0.57735,0.57735;2.0944rad)
  Profile = -> Sketch319
  ReferenceAxis = -> Sketch319 [V_Axis]
FEATURE [Sketcher::SketchObject] Sketch320
  FullyConstrained = false
  MapMode = 5
  Placement = pos=(0,0,0) rot=(0.57735,0.57735,0.57735;2.0944rad)
  Support = -> [YZ_Plane794]
  sketch-geometry (6):
    g0: LineSegment StartX=0 StartY=0 StartZ=0 EndX=-1.6 EndY=0 EndZ=0
    g1: LineSegment StartX=-1.6 StartY=0 StartZ=0 EndX=-1.6 EndY=-0.4 EndZ=0
    g2: LineSegment StartX=-1.6 StartY=-0.4 StartZ=0 EndX=-1.5 EndY=-0.4 EndZ=0
    g3: LineSegment StartX=-1.5 StartY=-0.4 StartZ=0 EndX=-1.5 EndY=-7 EndZ=0
    g4: LineSegment StartX=-1.5 StartY=-7 StartZ=0 EndX=0 EndY=-7 EndZ=0
    g5: LineSegment StartX=0 StartY=-7 StartZ=0 EndX=0 EndY=0 EndZ=0
  constraints (17):
    c: Coincident(g0,g-1)
    c: Horizontal(g0)
    c: Coincident(g1,g0)
    c: Coincident(g2,g1)
    c: Coincident(g3,g2)
    c: Vertical(g3)
    c: Coincident(g4,g3)
    c: Coincident(g5,g4)
    c: Coincident(g5,g-1)
    c: Vertical(g5)
    c: Horizontal(g4)
    c: Horizontal(g2)
    c: Vertical(g1)
    c: DistanceY(g1,g1) = 0.4
    c: DistanceX(g4,g4) = 1.5
    c: DistanceX(g0,g0) = 1.6
    c: DistanceY(g5,g5) = 7
FEATURE [PartDesign::Revolution] Revolution030
  AllowMultiFace = false
  Angle = 360
  Axis = (0,0,1)
  Base = (0,0,0)
  Placement = pos=(0,0,0) rot=(0.57735,0.57735,0.57735;2.0944rad)
  Profile = -> Sketch320
  ReferenceAxis = -> Sketch320 [V_Axis]
FEATURE [Sketcher::SketchObject] Sketch321
  FullyConstrained = false
  MapMode = 5
  Placement = pos=(0,0,0) rot=(0.57735,0.57735,0.57735;2.0944rad)
  Support = -> [YZ_Plane804]
  sketch-geometry (6):
    g0: LineSegment StartX=0 StartY=0 StartZ=0 EndX=-1.6 EndY=0 EndZ=0
    g1: LineSegment StartX=-1.6 StartY=0 StartZ=0 EndX=-1.6 EndY=-0.4 EndZ=0
    g2: LineSegment StartX=-1.6 StartY=-0.4 StartZ=0 EndX=-1.5 EndY=-0.4 EndZ=0
    g3: LineSegment StartX=-1.5 StartY=-0.4 StartZ=0 EndX=-1.5 EndY=-7 EndZ=0
    g4: LineSegment StartX=-1.5 StartY=-7 StartZ=0 EndX=0 EndY=-7 EndZ=0
    g5: LineSegment StartX=0 StartY=-7 StartZ=0 EndX=0 EndY=0 EndZ=0
  constraints (17):
    c: Coincident(g0,g-1)
    c: Horizontal(g0)
    c: Coincident(g1,g0)
    c: Coincident(g2,g1)
    c: Coincident(g3,g2)
    c: Vertical(g3)
    c: Coincident(g4,g3)
    c: Coincident(g5,g4)
    c: Coincident(g5,g-1)
    c: Vertical(g5)
    c: Horizontal(g4)
    c: Horizontal(g2)
    c: Vertical(g1)
    c: DistanceY(g1,g1) = 0.4
    c: DistanceX(g4,g4) = 1.5
    c: DistanceX(g0,g0) = 1.6
    c: DistanceY(g5,g5) = 7
FEATURE [Sketcher::SketchObject] Sketch322
  FullyConstrained = false
  MapMode = 5
  Placement = pos=(0,0,0) rot=(0.57735,0.57735,0.57735;2.0944rad)
  Support = -> [YZ_Plane803]
  sketch-geometry (6):
    g0: LineSegment StartX=0 StartY=0 StartZ=0 EndX=-1.6 EndY=0 EndZ=0
    g1: LineSegment StartX=-1.6 StartY=0 StartZ=0 EndX=-1.6 EndY=-0.4 EndZ=0
    g2: LineSegment StartX=-1.6 StartY=-0.4 StartZ=0 EndX=-1.5 EndY=-0.4 EndZ=0
    g3: LineSegment StartX=-1.5 StartY=-0.4 StartZ=0 EndX=-1.5 EndY=-7 EndZ=0
    g4: LineSegment StartX=-1.5 StartY=-7 StartZ=0 EndX=0 EndY=-7 EndZ=0
    g5: LineSegment StartX=0 StartY=-7 StartZ=0 EndX=0 EndY=0 EndZ=0
  constraints (17):
    c: Coincident(g0,g-1)
    c: Horizontal(g0)
    c: Coincident(g1,g0)
    c: Coincident(g2,g1)
    c: Coincident(g3,g2)
    c: Vertical(g3)
    c: Coincident(g4,g3)
    c: Coincident(g5,g4)
    c: Coincident(g5,g-1)
    c: Vertical(g5)
    c: Horizontal(g4)
    c: Horizontal(g2)
    c: Vertical(g1)
    c: DistanceY(g1,g1) = 0.4
    c: DistanceX(g4,g4) = 1.5
    c: DistanceX(g0,g0) = 1.6
    c: DistanceY(g5,g5) = 7
FEATURE [Sketcher::SketchObject] Sketch323
  FullyConstrained = false
  MapMode = 5
  Placement = pos=(0,0,0) rot=(0.57735,0.57735,0.57735;2.0944rad)
  Support = -> [YZ_Plane799]
  sketch-geometry (6):
    g0: LineSegment StartX=0 StartY=0 StartZ=0 EndX=-1.6 EndY=0 EndZ=0
    g1: LineSegment StartX=-1.6 StartY=0 StartZ=0 EndX=-1.6 EndY=-0.4 EndZ=0
    g2: LineSegment StartX=-1.6 StartY=-0.4 StartZ=0 EndX=-1.5 EndY=-0.4 EndZ=0
    g3: LineSegment StartX=-1.5 StartY=-0.4 StartZ=0 EndX=-1.5 EndY=-7 EndZ=0
    g4: LineSegment StartX=-1.5 StartY=-7 StartZ=0 EndX=0 EndY=-7 EndZ=0
    g5: LineSegment StartX=0 StartY=-7 StartZ=0 EndX=0 EndY=0 EndZ=0
  constraints (17):
    c: Coincident(g0,g-1)
    c: Horizontal(g0)
    c: Coincident(g1,g0)
    c: Coincident(g2,g1)
    c: Coincident(g3,g2)
    c: Vertical(g3)
    c: Coincident(g4,g3)
    c: Coincident(g5,g4)
    c: Coincident(g5,g-1)
    c: Vertical(g5)
    c: Horizontal(g4)
    c: Horizontal(g2)
    c: Vertical(g1)
    c: DistanceY(g1,g1) = 0.4
    c: DistanceX(g4,g4) = 1.5
    c: DistanceX(g0,g0) = 1.6
    c: DistanceY(g5,g5) = 7
FEATURE [Sketcher::SketchObject] Sketch324
  FullyConstrained = false
  MapMode = 5
  Placement = pos=(0,0,0) rot=(0.57735,0.57735,0.57735;2.0944rad)
  Support = -> [YZ_Plane797]
  sketch-geometry (6):
    g0: LineSegment StartX=0 StartY=0 StartZ=0 EndX=-1.6 EndY=0 EndZ=0
    g1: LineSegment StartX=-1.6 StartY=0 StartZ=0 EndX=-1.6 EndY=-0.4 EndZ=0
    g2: LineSegment StartX=-1.6 StartY=-0.4 StartZ=0 EndX=-1.5 EndY=-0.4 EndZ=0
    g3: LineSegment StartX=-1.5 StartY=-0.4 StartZ=0 EndX=-1.5 EndY=-7 EndZ=0
    g4: LineSegment StartX=-1.5 StartY=-7 StartZ=0 EndX=0 EndY=-7 EndZ=0
    g5: LineSegment StartX=0 StartY=-7 StartZ=0 EndX=0 EndY=0 EndZ=0
  constraints (17):
    c: Coincident(g0,g-1)
    c: Horizontal(g0)
    c: Coincident(g1,g0)
    c: Coincident(g2,g1)
    c: Coincident(g3,g2)
    c: Vertical(g3)
    c: Coincident(g4,g3)
    c: Coincident(g5,g4)
    c: Coincident(g5,g-1)
    c: Vertical(g5)
    c: Horizontal(g4)
    c: Horizontal(g2)
    c: Vertical(g1)
    c: DistanceY(g1,g1) = 0.4
    c: DistanceX(g4,g4) = 1.5
    c: DistanceX(g0,g0) = 1.6
    c: DistanceY(g5,g5) = 7
FEATURE [PartDesign::Body] Body115
  Group = -> [Sketch314,Revolution021]
  Origin = -> Origin773
  Tip = -> Revolution021
FEATURE [App::Part] Part085  label="Lightpipe021"
  Group = -> [Body115]
  Origin = -> Origin791
  Placement = pos=(40.005,-13.335,0) rot=(0,0,1;0rad)
  expr: .Placement.Base.x = 40.005
  expr: .Placement.Base.y = -13.335
FEATURE [PartDesign::Body] Body116
  Group = -> [Sketch315,Revolution027]
  Origin = -> Origin780
  Tip = -> Revolution027
FEATURE [App::Part] Part090  label="Lightpipe026"
  Group = -> [Body116]
  Origin = -> Origin792
  Placement = pos=(-40.005,-13.335,0) rot=(0,0,1;0rad)
  expr: .Placement.Base.x = -40.005
  expr: .Placement.Base.y = -13.335
FEATURE [PartDesign::Body] Body117
  Group = -> [Sketch319,Revolution028]
  Origin = -> Origin778
  Tip = -> Revolution028
FEATURE [App::Part] Part086  label="Lightpipe022"
  Group = -> [Body117]
  Origin = -> Origin800
  Placement = pos=(13.335,-40.005,0) rot=(0,0,1;0rad)
  expr: .Placement.Base.x = 13.335
  expr: .Placement.Base.y = -40.005
FEATURE [PartDesign::Body] Body118
  Group = -> [Sketch320,Revolution030]
  Origin = -> Origin779
  Tip = -> Revolution030
FEATURE [App::Part] Part088  label="Lightpipe024"
  Group = -> [Body118]
  Origin = -> Origin799
  Placement = pos=(-40.005,-40.005,0) rot=(0,0,1;0rad)
  expr: .Placement.Base.x = -40.005
  expr: .Placement.Base.y = -40.005
FEATURE [PartDesign::Body] Body119
  Group = -> [Sketch313,Revolution022]
  Origin = -> Origin802
  Tip = -> Revolution022
FEATURE [PartDesign::Body] Body120
  Group = -> [Sketch310,Revolution023]
  Origin = -> Origin803
  Tip = -> Revolution023
FEATURE [App::Part] Part081  label="Lightpipe017"
  Group = -> [Body120]
  Origin = -> Origin788
  Placement = pos=(40.005,40.005,0) rot=(0,0,1;0rad)
  expr: .Placement.Base.x = 40.005
  expr: .Placement.Base.y = 40.005
FEATURE [PartDesign::Body] Body121
  Group = -> [Sketch316,Revolution024]
  Origin = -> Origin789
  Tip = -> Revolution024
FEATURE [App::Part] Part087  label="Lightpipe023"
  Group = -> [Body121]
  Origin = -> Origin784
  Placement = pos=(40.005,13.335,0) rot=(0,0,1;0rad)
  expr: .Placement.Base.x = 40.005
  expr: .Placement.Base.y = 13.335
FEATURE [PartDesign::Body] Body126
  Group = -> [Sketch311,Revolution026]
  Origin = -> Origin795
  Tip = -> Revolution026
FEATURE [PartDesign::Body] Body127
  Group = -> [Sketch312,Revolution025]
  Origin = -> Origin794
  Tip = -> Revolution025
FEATURE [PartDesign::Body] Body129
  Group = -> [Sketch318,Revolution020]
  Origin = -> Origin781
  Tip = -> Revolution020
FEATURE [App::Part] Part082  label="Lightpipe018"
  Group = -> [Body129]
  Origin = -> Origin801
  Placement = pos=(13.335,-13.335,0) rot=(0,0,1;0rad)
  expr: .Placement.Base.x = 13.335
  expr: .Placement.Base.y = -13.335
FEATURE [PartDesign::Revolution] Revolution031
  AllowMultiFace = false
  Angle = 360
  Axis = (0,0,1)
  Base = (0,0,0)
  Placement = pos=(0,0,0) rot=(0.57735,0.57735,0.57735;2.0944rad)
  Profile = -> Sketch322
  ReferenceAxis = -> Sketch322 [V_Axis]
FEATURE [PartDesign::Body] Body122
  Group = -> [Sketch322,Revolution031]
  Origin = -> Origin790
  Tip = -> Revolution031
FEATURE [App::Part] Part083  label="Lightpipe019"
  Group = -> [Body122]
  Origin = -> Origin785
  Placement = pos=(13.335,13.335,0) rot=(0,0,1;0rad)
  expr: .Placement.Base.x = 13.335
  expr: .Placement.Base.y = 13.335
FEATURE [PartDesign::Revolution] Revolution032
  AllowMultiFace = false
  Angle = 360
  Axis = (0,0,1)
  Base = (0,0,0)
  Placement = pos=(0,0,0) rot=(0.57735,0.57735,0.57735;2.0944rad)
  Profile = -> Sketch321
  ReferenceAxis = -> Sketch321 [V_Axis]
FEATURE [PartDesign::Body] Body123
  Group = -> [Sketch321,Revolution032]
  Origin = -> Origin775
  Tip = -> Revolution032
FEATURE [PartDesign::Revolution] Revolution033
  AllowMultiFace = false
  Angle = 360
  Axis = (0,0,1)
  Base = (0,0,0)
  Placement = pos=(0,0,0) rot=(0.57735,0.57735,0.57735;2.0944rad)
  Profile = -> Sketch324
  ReferenceAxis = -> Sketch324 [V_Axis]
FEATURE [PartDesign::Body] Body124
  Group = -> [Sketch324,Revolution033]
  Origin = -> Origin776
  Tip = -> Revolution033
FEATURE [App::Part] Part091  label="Lightpipe027"
  Group = -> [Body124]
  Origin = -> Origin786
  Placement = pos=(-13.335,13.335,0) rot=(0,0,1;0rad)
  expr: .Placement.Base.x = -13.335
  expr: .Placement.Base.y = 13.335
FEATURE [PartDesign::Revolution] Revolution034
  AllowMultiFace = false
  Angle = 360
  Axis = (0,0,1)
  Base = (0,0,0)
  Placement = pos=(0,0,0) rot=(0.57735,0.57735,0.57735;2.0944rad)
  Profile = -> Sketch317
  ReferenceAxis = -> Sketch317 [V_Axis]
FEATURE [PartDesign::Body] Body125
  Group = -> [Sketch317,Revolution034]
  Origin = -> Origin772
  Tip = -> Revolution034
FEATURE [App::Part] Part092  label="Lightpipe028"
  Group = -> [Body125]
  Origin = -> Origin796
  Placement = pos=(40.005,-40.005,0) rot=(0,0,1;0rad)
  expr: .Placement.Base.x = 40.005
  expr: .Placement.Base.y = -40.005
FEATURE [PartDesign::Revolution] Revolution035
  AllowMultiFace = false
  Angle = 360
  Axis = (0,0,1)
  Base = (0,0,0)
  Placement = pos=(0,0,0) rot=(0.57735,0.57735,0.57735;2.0944rad)
  Profile = -> Sketch323
  ReferenceAxis = -> Sketch323 [V_Axis]
FEATURE [PartDesign::Body] Body128
  Group = -> [Sketch323,Revolution035]
  Origin = -> Origin777
  Tip = -> Revolution035
FEATURE [App::Part] Part084  label="Lightpipe020"
  Group = -> [Body128]
  Origin = -> Origin798
  Placement = pos=(-13.335,-13.335,0) rot=(0,0,1;0rad)
  expr: .Placement.Base.x = -13.335
  expr: .Placement.Base.y = -13.335
FEATURE [App::Part] Part094  label="Lightpipe029"
  Group = -> [Body123]
  Origin = -> Origin782
  Placement = pos=(-40.005,13.335,0) rot=(0,0,1;0rad)
  expr: .Placement.Base.x = -40.005
  expr: .Placement.Base.y = 13.335
FEATURE [App::Part] Part095  label="Lightpipe030"
  Group = -> [Body126]
  Origin = -> Origin783
  Placement = pos=(-13.34,40.005,0) rot=(0,0,1;0rad)
  expr: .Placement.Base.x = -13.335
  expr: .Placement.Base.y = 40.005
FEATURE [App::Part] Part096  label="Lightpipe031"
  Group = -> [Body127]
  Origin = -> Origin797
  Placement = pos=(-40.005,40.005,0) rot=(0,0,1;0rad)
  expr: .Placement.Base.x = -40.005
  expr: .Placement.Base.y = 40.005
FEATURE [App::Part] Part097  label="Lightpipe032"
  Group = -> [Body119]
  Origin = -> Origin787
  Placement = pos=(13.335,40.005,0) rot=(0,0,1;0rad)
  expr: .Placement.Base.x = 13.335
  expr: .Placement.Base.y = 40.005
FEATURE [Sketcher::SketchObject] Sketch325
  FullyConstrained = false
  MapMode = 5
  Placement = pos=(0,0,0) rot=(0.57735,0.57735,0.57735;2.0944rad)
  Support = -> [YZ_Plane795]
  sketch-geometry (6):
    g0: LineSegment StartX=0 StartY=0 StartZ=0 EndX=-1.6 EndY=0 EndZ=0
    g1: LineSegment StartX=-1.6 StartY=0 StartZ=0 EndX=-1.6 EndY=-0.4 EndZ=0
    g2: LineSegment StartX=-1.6 StartY=-0.4 StartZ=0 EndX=-1.5 EndY=-0.4 EndZ=0
    g3: LineSegment StartX=-1.5 StartY=-0.4 StartZ=0 EndX=-1.5 EndY=-7 EndZ=0
    g4: LineSegment StartX=-1.5 StartY=-7 StartZ=0 EndX=0 EndY=-7 EndZ=0
    g5: LineSegment StartX=0 StartY=-7 StartZ=0 EndX=0 EndY=0 EndZ=0
  constraints (17):
    c: Coincident(g0,g-1)
    c: Horizontal(g0)
    c: Coincident(g1,g0)
    c: Coincident(g2,g1)
    c: Coincident(g3,g2)
    c: Vertical(g3)
    c: Coincident(g4,g3)
    c: Coincident(g5,g4)
    c: Coincident(g5,g-1)
    c: Vertical(g5)
    c: Horizontal(g4)
    c: Horizontal(g2)
    c: Vertical(g1)
    c: DistanceY(g1,g1) = 0.4
    c: DistanceX(g4,g4) = 1.5
    c: DistanceX(g0,g0) = 1.6
    c: DistanceY(g5,g5) = 7
FEATURE [PartDesign::Revolution] Revolution029
  AllowMultiFace = false
  Angle = 360
  Axis = (0,0,1)
  Base = (0,0,0)
  Placement = pos=(0,0,0) rot=(0.57735,0.57735,0.57735;2.0944rad)
  Profile = -> Sketch325
  ReferenceAxis = -> Sketch325 [V_Axis]
FEATURE [PartDesign::Body] Body130
  Group = -> [Sketch325,Revolution029]
  Origin = -> Origin774
  Tip = -> Revolution029
FEATURE [App::Part] Part089  label="Lightpipe025"
  Group = -> [Body130]
  Origin = -> Origin804
  Placement = pos=(-13.335,-40.005,0) rot=(0,0,1;0rad)
  expr: .Placement.Base.x = -13.335
  expr: .Placement.Base.y = -40.005
FEATURE [App::Part] Part093  label="BU16_Lightpipes"
  Group = -> [Part096,Part095,Part097,Part081,Part087,Part083,Part094,Part091,Part085,Part082,Part084,Part092,Part090,Part086,Part088,Part089]
  Origin = -> Origin793
  Placement = pos=(0,8.5,0) rot=(0,0,1;0rad)
  expr: .Placement.Base.y = 8.5
FEATURE [Sketcher::SketchObject] Sketch327
  FullyConstrained = false
  MapMode = 5
  Placement = pos=(0,0,0) rot=(0.57735,0.57735,0.57735;2.0944rad)
  Support = -> [YZ_Plane808]
  sketch-geometry (6):
    g0: LineSegment StartX=0 StartY=0 StartZ=0 EndX=-1.6 EndY=0 EndZ=0
    g1: LineSegment StartX=-1.6 StartY=0 StartZ=0 EndX=-1.6 EndY=-0.4 EndZ=0
    g2: LineSegment StartX=-1.6 StartY=-0.4 StartZ=0 EndX=-1.5 EndY=-0.4 EndZ=0
    g3: LineSegment StartX=-1.5 StartY=-0.4 StartZ=0 EndX=-1.5 EndY=-7 EndZ=0
    g4: LineSegment StartX=-1.5 StartY=-7 StartZ=0 EndX=0 EndY=-7 EndZ=0
    g5: LineSegment StartX=0 StartY=-7 StartZ=0 EndX=0 EndY=0 EndZ=0
  constraints (17):
    c: Coincident(g0,g-1)
    c: Horizontal(g0)
    c: Coincident(g1,g0)
    c: Coincident(g2,g1)
    c: Coincident(g3,g2)
    c: Vertical(g3)
    c: Coincident(g4,g3)
    c: Coincident(g5,g4)
    c: Coincident(g5,g-1)
    c: Vertical(g5)
    c: Horizontal(g4)
    c: Horizontal(g2)
    c: Vertical(g1)
    c: DistanceY(g1,g1) = 0.4
    c: DistanceX(g4,g4) = 1.5
    c: DistanceX(g0,g0) = 1.6
    c: DistanceY(g5,g5) = 7
FEATURE [PartDesign::Revolution] Revolution046
  AllowMultiFace = false
  Angle = 360
  Axis = (0,0,1)
  Base = (0,0,0)
  Placement = pos=(0,0,0) rot=(0.57735,0.57735,0.57735;2.0944rad)
  Profile = -> Sketch327
  ReferenceAxis = -> Sketch327 [V_Axis]
FEATURE [Sketcher::SketchObject] Sketch329
  FullyConstrained = false
  MapMode = 5
  Placement = pos=(0,0,0) rot=(0.57735,0.57735,0.57735;2.0944rad)
  Support = -> [YZ_Plane810]
  sketch-geometry (6):
    g0: LineSegment StartX=0 StartY=0 StartZ=0 EndX=-1.6 EndY=0 EndZ=0
    g1: LineSegment StartX=-1.6 StartY=0 StartZ=0 EndX=-1.6 EndY=-0.4 EndZ=0
    g2: LineSegment StartX=-1.6 StartY=-0.4 StartZ=0 EndX=-1.5 EndY=-0.4 EndZ=0
    g3: LineSegment StartX=-1.5 StartY=-0.4 StartZ=0 EndX=-1.5 EndY=-7 EndZ=0
    g4: LineSegment StartX=-1.5 StartY=-7 StartZ=0 EndX=0 EndY=-7 EndZ=0
    g5: LineSegment StartX=0 StartY=-7 StartZ=0 EndX=0 EndY=0 EndZ=0
  constraints (17):
    c: Coincident(g0,g-1)
    c: Horizontal(g0)
    c: Coincident(g1,g0)
    c: Coincident(g2,g1)
    c: Coincident(g3,g2)
    c: Vertical(g3)
    c: Coincident(g4,g3)
    c: Coincident(g5,g4)
    c: Coincident(g5,g-1)
    c: Vertical(g5)
    c: Horizontal(g4)
    c: Horizontal(g2)
    c: Vertical(g1)
    c: DistanceY(g1,g1) = 0.4
    c: DistanceX(g4,g4) = 1.5
    c: DistanceX(g0,g0) = 1.6
    c: DistanceY(g5,g5) = 7
FEATURE [PartDesign::Revolution] Revolution044
  AllowMultiFace = false
  Angle = 360
  Axis = (0,0,1)
  Base = (0,0,0)
  Placement = pos=(0,0,0) rot=(0.57735,0.57735,0.57735;2.0944rad)
  Profile = -> Sketch329
  ReferenceAxis = -> Sketch329 [V_Axis]
FEATURE [Sketcher::SketchObject] Sketch330
  FullyConstrained = false
  MapMode = 5
  Placement = pos=(0,0,0) rot=(0.57735,0.57735,0.57735;2.0944rad)
  Support = -> [YZ_Plane815]
  sketch-geometry (6):
    g0: LineSegment StartX=0 StartY=0 StartZ=0 EndX=-1.6 EndY=0 EndZ=0
    g1: LineSegment StartX=-1.6 StartY=0 StartZ=0 EndX=-1.6 EndY=-0.4 EndZ=0
    g2: LineSegment StartX=-1.6 StartY=-0.4 StartZ=0 EndX=-1.5 EndY=-0.4 EndZ=0
    g3: LineSegment StartX=-1.5 StartY=-0.4 StartZ=0 EndX=-1.5 EndY=-7 EndZ=0
    g4: LineSegment StartX=-1.5 StartY=-7 StartZ=0 EndX=0 EndY=-7 EndZ=0
    g5: LineSegment StartX=0 StartY=-7 StartZ=0 EndX=0 EndY=0 EndZ=0
  constraints (17):
    c: Coincident(g0,g-1)
    c: Horizontal(g0)
    c: Coincident(g1,g0)
    c: Coincident(g2,g1)
    c: Coincident(g3,g2)
    c: Vertical(g3)
    c: Coincident(g4,g3)
    c: Coincident(g5,g4)
    c: Coincident(g5,g-1)
    c: Vertical(g5)
    c: Horizontal(g4)
    c: Horizontal(g2)
    c: Vertical(g1)
    c: DistanceY(g1,g1) = 0.4
    c: DistanceX(g4,g4) = 1.5
    c: DistanceX(g0,g0) = 1.6
    c: DistanceY(g5,g5) = 7
FEATURE [PartDesign::Revolution] Revolution041
  AllowMultiFace = false
  Angle = 360
  Axis = (0,0,1)
  Base = (0,0,0)
  Placement = pos=(0,0,0) rot=(0.57735,0.57735,0.57735;2.0944rad)
  Profile = -> Sketch330
  ReferenceAxis = -> Sketch330 [V_Axis]
FEATURE [Sketcher::SketchObject] Sketch332
  FullyConstrained = false
  MapMode = 5
  Placement = pos=(0,0,0) rot=(0.57735,0.57735,0.57735;2.0944rad)
  Support = -> [YZ_Plane838]
  sketch-geometry (6):
    g0: LineSegment StartX=0 StartY=0 StartZ=0 EndX=-1.6 EndY=0 EndZ=0
    g1: LineSegment StartX=-1.6 StartY=0 StartZ=0 EndX=-1.6 EndY=-0.4 EndZ=0
    g2: LineSegment StartX=-1.6 StartY=-0.4 StartZ=0 EndX=-1.5 EndY=-0.4 EndZ=0
    g3: LineSegment StartX=-1.5 StartY=-0.4 StartZ=0 EndX=-1.5 EndY=-7 EndZ=0
    g4: LineSegment StartX=-1.5 StartY=-7 StartZ=0 EndX=0 EndY=-7 EndZ=0
    g5: LineSegment StartX=0 StartY=-7 StartZ=0 EndX=0 EndY=0 EndZ=0
  constraints (17):
    c: Coincident(g0,g-1)
    c: Horizontal(g0)
    c: Coincident(g1,g0)
    c: Coincident(g2,g1)
    c: Coincident(g3,g2)
    c: Vertical(g3)
    c: Coincident(g4,g3)
    c: Coincident(g5,g4)
    c: Coincident(g5,g-1)
    c: Vertical(g5)
    c: Horizontal(g4)
    c: Horizontal(g2)
    c: Vertical(g1)
    c: DistanceY(g1,g1) = 0.4
    c: DistanceX(g4,g4) = 1.5
    c: DistanceX(g0,g0) = 1.6
    c: DistanceY(g5,g5) = 7
FEATURE [PartDesign::Revolution] Revolution049
  AllowMultiFace = false
  Angle = 360
  Axis = (0,0,1)
  Base = (0,0,0)
  Placement = pos=(0,0,0) rot=(0.57735,0.57735,0.57735;2.0944rad)
  Profile = -> Sketch332
  ReferenceAxis = -> Sketch332 [V_Axis]
FEATURE [Sketcher::SketchObject] Sketch333
  FullyConstrained = false
  MapMode = 5
  Placement = pos=(0,0,0) rot=(0.57735,0.57735,0.57735;2.0944rad)
  Support = -> [YZ_Plane816]
  sketch-geometry (6):
    g0: LineSegment StartX=0 StartY=0 StartZ=0 EndX=-1.6 EndY=0 EndZ=0
    g1: LineSegment StartX=-1.6 StartY=0 StartZ=0 EndX=-1.6 EndY=-0.4 EndZ=0
    g2: LineSegment StartX=-1.6 StartY=-0.4 StartZ=0 EndX=-1.5 EndY=-0.4 EndZ=0
    g3: LineSegment StartX=-1.5 StartY=-0.4 StartZ=0 EndX=-1.5 EndY=-7 EndZ=0
    g4: LineSegment StartX=-1.5 StartY=-7 StartZ=0 EndX=0 EndY=-7 EndZ=0
    g5: LineSegment StartX=0 StartY=-7 StartZ=0 EndX=0 EndY=0 EndZ=0
  constraints (17):
    c: Coincident(g0,g-1)
    c: Horizontal(g0)
    c: Coincident(g1,g0)
    c: Coincident(g2,g1)
    c: Coincident(g3,g2)
    c: Vertical(g3)
    c: Coincident(g4,g3)
    c: Coincident(g5,g4)
    c: Coincident(g5,g-1)
    c: Vertical(g5)
    c: Horizontal(g4)
    c: Horizontal(g2)
    c: Vertical(g1)
    c: DistanceY(g1,g1) = 0.4
    c: DistanceX(g4,g4) = 1.5
    c: DistanceX(g0,g0) = 1.6
    c: DistanceY(g5,g5) = 7
FEATURE [PartDesign::Revolution] Revolution039
  AllowMultiFace = false
  Angle = 360
  Axis = (0,0,1)
  Base = (0,0,0)
  Placement = pos=(0,0,0) rot=(0.57735,0.57735,0.57735;2.0944rad)
  Profile = -> Sketch333
  ReferenceAxis = -> Sketch333 [V_Axis]
FEATURE [Sketcher::SketchObject] Sketch340
  FullyConstrained = false
  MapMode = 5
  Placement = pos=(0,0,0) rot=(0.57735,0.57735,0.57735;2.0944rad)
  Support = -> [YZ_Plane830]
  sketch-geometry (6):
    g0: LineSegment StartX=0 StartY=0 StartZ=0 EndX=-1.6 EndY=0 EndZ=0
    g1: LineSegment StartX=-1.6 StartY=0 StartZ=0 EndX=-1.6 EndY=-0.4 EndZ=0
    g2: LineSegment StartX=-1.6 StartY=-0.4 StartZ=0 EndX=-1.5 EndY=-0.4 EndZ=0
    g3: LineSegment StartX=-1.5 StartY=-0.4 StartZ=0 EndX=-1.5 EndY=-7 EndZ=0
    g4: LineSegment StartX=-1.5 StartY=-7 StartZ=0 EndX=0 EndY=-7 EndZ=0
    g5: LineSegment StartX=0 StartY=-7 StartZ=0 EndX=0 EndY=0 EndZ=0
  constraints (17):
    c: Coincident(g0,g-1)
    c: Horizontal(g0)
    c: Coincident(g1,g0)
    c: Coincident(g2,g1)
    c: Coincident(g3,g2)
    c: Vertical(g3)
    c: Coincident(g4,g3)
    c: Coincident(g5,g4)
    c: Coincident(g5,g-1)
    c: Vertical(g5)
    c: Horizontal(g4)
    c: Horizontal(g2)
    c: Vertical(g1)
    c: DistanceY(g1,g1) = 0.4
    c: DistanceX(g4,g4) = 1.5
    c: DistanceX(g0,g0) = 1.6
    c: DistanceY(g5,g5) = 7
FEATURE [PartDesign::Revolution] Revolution050
  AllowMultiFace = false
  Angle = 360
  Axis = (0,0,1)
  Base = (0,0,0)
  Placement = pos=(0,0,0) rot=(0.57735,0.57735,0.57735;2.0944rad)
  Profile = -> Sketch340
  ReferenceAxis = -> Sketch340 [V_Axis]
FEATURE [Sketcher::SketchObject] Sketch341
  FullyConstrained = false
  MapMode = 5
  Placement = pos=(0,0,0) rot=(0.57735,0.57735,0.57735;2.0944rad)
  Support = -> [YZ_Plane837]
  sketch-geometry (6):
    g0: LineSegment StartX=0 StartY=0 StartZ=0 EndX=-1.6 EndY=0 EndZ=0
    g1: LineSegment StartX=-1.6 StartY=0 StartZ=0 EndX=-1.6 EndY=-0.4 EndZ=0
    g2: LineSegment StartX=-1.6 StartY=-0.4 StartZ=0 EndX=-1.5 EndY=-0.4 EndZ=0
    g3: LineSegment StartX=-1.5 StartY=-0.4 StartZ=0 EndX=-1.5 EndY=-7 EndZ=0
    g4: LineSegment StartX=-1.5 StartY=-7 StartZ=0 EndX=0 EndY=-7 EndZ=0
    g5: LineSegment StartX=0 StartY=-7 StartZ=0 EndX=0 EndY=0 EndZ=0
  constraints (17):
    c: Coincident(g0,g-1)
    c: Horizontal(g0)
    c: Coincident(g1,g0)
    c: Coincident(g2,g1)
    c: Coincident(g3,g2)
    c: Vertical(g3)
    c: Coincident(g4,g3)
    c: Coincident(g5,g4)
    c: Coincident(g5,g-1)
    c: Vertical(g5)
    c: Horizontal(g4)
    c: Horizontal(g2)
    c: Vertical(g1)
    c: DistanceY(g1,g1) = 0.4
    c: DistanceX(g4,g4) = 1.5
    c: DistanceX(g0,g0) = 1.6
    c: DistanceY(g5,g5) = 7
FEATURE [PartDesign::Revolution] Revolution048
  AllowMultiFace = false
  Angle = 360
  Axis = (0,0,1)
  Base = (0,0,0)
  Placement = pos=(0,0,0) rot=(0.57735,0.57735,0.57735;2.0944rad)
  Profile = -> Sketch341
  ReferenceAxis = -> Sketch341 [V_Axis]
FEATURE [PartDesign::Body] Body134
  Group = -> [Sketch333,Revolution039]
  Origin = -> Origin813
  Placement = pos=(0,3.17,0) rot=(0,0,1;0rad)
  Tip = -> Revolution039
FEATURE [App::Part] Part099  label="Lightpipe034"
  Group = -> [Body134]
  Origin = -> Origin835
  Placement = pos=(40.005,13.335,0) rot=(0,0,1;0rad)
  expr: .Placement.Base.x = 40.005
  expr: .Placement.Base.y = 13.335
FEATURE [PartDesign::Body] Body135
  Group = -> [Sketch327,Revolution046]
  Origin = -> Origin833
  Tip = -> Revolution046
FEATURE [App::Part] Part106  label="Lightpipe040"
  Group = -> [Body135]
  Origin = -> Origin837
  Placement = pos=(-13.34,40.005,0) rot=(0,0,1;0rad)
  expr: .Placement.Base.x = -13.335
  expr: .Placement.Base.y = 40.005
FEATURE [PartDesign::Body] Body138
  Group = -> [Sketch330,Revolution041]
  Origin = -> Origin812
  Placement = pos=(0,-0.5,0) rot=(0,0,1;0rad)
  Tip = -> Revolution041
FEATURE [App::Part] Part113  label="Lightpipe046"
  Group = -> [Body138]
  Origin = -> Origin810
  Placement = pos=(13.335,40.005,0) rot=(0,0,1;0rad)
  expr: .Placement.Base.x = 13.335
  expr: .Placement.Base.y = 40.005
FEATURE [PartDesign::Body] Body139
  Group = -> [Sketch341,Revolution048]
  Origin = -> Origin823
  Placement = pos=(0,3.17,0) rot=(0,0,1;0rad)
  Tip = -> Revolution048
FEATURE [App::Part] Part109  label="Lightpipe042"
  Group = -> [Body139]
  Origin = -> Origin838
  Placement = pos=(13.335,13.335,0) rot=(0,0,1;0rad)
  expr: .Placement.Base.x = 13.335
  expr: .Placement.Base.y = 13.335
FEATURE [PartDesign::Body] Body140
  Group = -> [Sketch332,Revolution049]
  Origin = -> Origin819
  Placement = pos=(0,3.17,0) rot=(0,0,1;0rad)
  Tip = -> Revolution049
FEATURE [App::Part] Part105  label="Lightpipe039"
  Group = -> [Body140]
  Origin = -> Origin821
  Placement = pos=(-40.005,13.335,0) rot=(0,0,1;0rad)
  expr: .Placement.Base.x = -40.005
  expr: .Placement.Base.y = 13.335
FEATURE [PartDesign::Body] Body141
  Group = -> [Sketch340,Revolution050]
  Origin = -> Origin831
  Placement = pos=(0,3.17,0) rot=(0,0,1;0rad)
  Tip = -> Revolution050
FEATURE [App::Part] Part103  label="Lightpipe038"
  Group = -> [Body141]
  Origin = -> Origin832
  Placement = pos=(-13.335,13.335,0) rot=(0,0,1;0rad)
  expr: .Placement.Base.x = -13.335
  expr: .Placement.Base.y = 13.335
FEATURE [PartDesign::Body] Body144
  Group = -> [Sketch329,Revolution044]
  Origin = -> Origin834
  Tip = -> Revolution044
FEATURE [App::Part] Part112  label="Lightpipe045"
  Group = -> [Body144]
  Origin = -> Origin809
  Placement = pos=(-40.005,40.005,0) rot=(0,0,1;0rad)
  expr: .Placement.Base.x = -40.005
  expr: .Placement.Base.y = 40.005
FEATURE [Sketcher::SketchObject] Sketch345
  AttachmentOffset = pos=(0,0,7) rot=(0,0,1;0rad)
  FullyConstrained = false
  MapMode = 5
  Placement = pos=(0,0,7) rot=(0,0,1;0rad)
  Support = -> [XY_Plane843]
  sketch-geometry (25):
    g0: LineSegment StartX=-0.724089 StartY=5.5 StartZ=0 EndX=-2.12292 EndY=5.12518 EndZ=0
    g1: LineSegment StartX=-2.12292 StartY=5.12518 StartZ=0 EndX=-3.37708 EndY=4.4011 EndZ=0
    g2: LineSegment StartX=-3.37708 StartY=4.4011 StartZ=0 EndX=-4.4011 EndY=3.37708 EndZ=0
    g3: LineSegment StartX=-4.4011 StartY=3.37708 StartZ=0 EndX=-5.12518 EndY=2.12292 EndZ=0
    g4: LineSegment StartX=-5.12518 StartY=2.12292 StartZ=0 EndX=-5.5 EndY=0.724089 EndZ=0
    g5: LineSegment StartX=-5.5 StartY=0.724089 StartZ=0 EndX=-5.5 EndY=-0.724089 EndZ=0
    g6: LineSegment StartX=-5.5 StartY=-0.724089 StartZ=0 EndX=-5.12518 EndY=-2.12292 EndZ=0
    g7: LineSegment StartX=-5.12518 StartY=-2.12292 StartZ=0 EndX=-4.4011 EndY=-3.37708 EndZ=0
    g8: LineSegment StartX=-4.4011 StartY=-3.37708 StartZ=0 EndX=-3.37708 EndY=-4.4011 EndZ=0
    g9: LineSegment StartX=-3.37708 StartY=-4.4011 StartZ=0 EndX=-2.12292 EndY=-5.12518 EndZ=0
    g10: LineSegment StartX=-2.12292 StartY=-5.12518 StartZ=0 EndX=-0.724089 EndY=-5.5 EndZ=0
    g11: LineSegment StartX=-0.724089 StartY=-5.5 StartZ=0 EndX=0.724089 EndY=-5.5 EndZ=0
    g12: LineSegment StartX=0.724089 StartY=-5.5 StartZ=0 EndX=2.12292 EndY=-5.12518 EndZ=0
    g13: LineSegment StartX=2.12292 StartY=-5.12518 StartZ=0 EndX=3.37708 EndY=-4.4011 EndZ=0
    g14: LineSegment StartX=3.37708 StartY=-4.4011 StartZ=0 EndX=4.4011 EndY=-3.37708 EndZ=0
    g15: LineSegment StartX=4.4011 StartY=-3.37708 StartZ=0 EndX=5.12518 EndY=-2.12292 EndZ=0
    g16: LineSegment StartX=5.12518 StartY=-2.12292 StartZ=0 EndX=5.5 EndY=-0.724089 EndZ=0
    g17: LineSegment StartX=5.5 StartY=-0.724089 StartZ=0 EndX=5.5 EndY=0.724089 EndZ=0
    g18: LineSegment StartX=5.5 StartY=0.724089 StartZ=0 EndX=5.12518 EndY=2.12292 EndZ=0
    g19: LineSegment StartX=5.12518 StartY=2.12292 StartZ=0 EndX=4.4011 EndY=3.37708 EndZ=0
    g20: LineSegment StartX=4.4011 StartY=3.37708 StartZ=0 EndX=3.37708 EndY=4.4011 EndZ=0
    g21: LineSegment StartX=3.37708 StartY=4.4011 StartZ=0 EndX=2.12292 EndY=5.12518 EndZ=0
    g22: LineSegment StartX=2.12292 StartY=5.12518 StartZ=0 EndX=0.724089 EndY=5.5 EndZ=0
    g23: LineSegment StartX=0.724089 StartY=5.5 StartZ=0 EndX=-0.724089 EndY=5.5 EndZ=0
    g24: Circle CenterX=0 CenterY=0 CenterZ=0 NormalX=0 NormalY=0 NormalZ=1 AngleXU=0 Radius=5.54746
  constraints (52):
    c: Coincident(g0,g1)
    c: Coincident(g1,g2)
    c: Coincident(g2,g3)
    c: Coincident(g3,g4)
    c: Coincident(g4,g5)
    c: Coincident(g5,g6)
    c: Coincident(g6,g7)
    c: Coincident(g7,g8)
    c: Coincident(g8,g9)
    c: Coincident(g9,g10)
    c: Coincident(g10,g11)
    c: Coincident(g11,g12)
    c: Coincident(g12,g13)
    c: Coincident(g13,g14)
    c: Coincident(g14,g15)
    c: Coincident(g15,g16)
    c: Coincident(g16,g17)
    c: Coincident(g17,g18)
    c: Coincident(g18,g19)
    c: Coincident(g19,g20)
    c: Coincident(g20,g21)
    c: Coincident(g21,g22)
    c: Coincident(g22,g23)
    c: Coincident(g23,g0)
    c: Equal(g0, g1-g23) x23
    c: PointOnObject(g0,g24)
    c: PointOnObject(g1,g24)
    c: PointOnObject(g2,g24)
    c: PointOnObject(g3,g24)
    c: PointOnObject(g4,g24)
    c: PointOnObject(g5,g24)
    c: PointOnObject(g6,g24)
    c: PointOnObject(g7,g24)
    c: PointOnObject(g8,g24)
    c: PointOnObject(g9,g24)
    c: PointOnObject(g10,g24)
    c: PointOnObject(g11,g24)
    c: PointOnObject(g12,g24)
    c: PointOnObject(g13,g24)
    c: PointOnObject(g14,g24)
    c: PointOnObject(g15,g24)
    c: PointOnObject(g16,g24)
    c: PointOnObject(g17,g24)
    c: PointOnObject(g18,g24)
    c: PointOnObject(g19,g24)
    c: PointOnObject(g20,g24)
    c: PointOnObject(g21,g24)
    c: PointOnObject(g22,g24)
    c: PointOnObject(g23,g24)
    c: Coincident(g24,g-1)
    c: Horizontal(g23)
    c: DistanceX(g4,g17) = 11
FEATURE [Sketcher::SketchObject] Sketch346
  AttachmentOffset = pos=(0,0,17) rot=(0,0,1;0rad)
  FullyConstrained = false
  MapMode = 5
  Placement = pos=(0,0,17) rot=(0,0,1;0rad)
  Support = -> [XY_Plane843]
  sketch-geometry (25):
    g0: LineSegment StartX=-4.65926 StartY=1.92993 StartZ=0 EndX=-5 EndY=0.658262 EndZ=0
    g1: LineSegment StartX=-5 StartY=0.658262 StartZ=0 EndX=-5 EndY=-0.658262 EndZ=0
    g2: LineSegment StartX=-5 StartY=-0.658262 StartZ=0 EndX=-4.65926 EndY=-1.92993 EndZ=0
    g3: LineSegment StartX=-4.65926 StartY=-1.92993 StartZ=0 EndX=-4.001 EndY=-3.07007 EndZ=0
    g4: LineSegment StartX=-4.001 StartY=-3.07007 StartZ=0 EndX=-3.07007 EndY=-4.001 EndZ=0
    g5: LineSegment StartX=-3.07007 StartY=-4.001 StartZ=0 EndX=-1.92993 EndY=-4.65926 EndZ=0
    g6: LineSegment StartX=-1.92993 StartY=-4.65926 StartZ=0 EndX=-0.658262 EndY=-5 EndZ=0
    g7: LineSegment StartX=-0.658262 StartY=-5 StartZ=0 EndX=0.658262 EndY=-5 EndZ=0
    g8: LineSegment StartX=0.658262 StartY=-5 StartZ=0 EndX=1.92993 EndY=-4.65926 EndZ=0
    g9: LineSegment StartX=1.92993 StartY=-4.65926 StartZ=0 EndX=3.07007 EndY=-4.001 EndZ=0
    g10: LineSegment StartX=3.07007 StartY=-4.001 StartZ=0 EndX=4.001 EndY=-3.07007 EndZ=0
    g11: LineSegment StartX=4.001 StartY=-3.07007 StartZ=0 EndX=4.65926 EndY=-1.92993 EndZ=0
    g12: LineSegment StartX=4.65926 StartY=-1.92993 StartZ=0 EndX=5 EndY=-0.658262 EndZ=0
    g13: LineSegment StartX=5 StartY=-0.658262 StartZ=0 EndX=5 EndY=0.658262 EndZ=0
    g14: LineSegment StartX=5 StartY=0.658262 StartZ=0 EndX=4.65926 EndY=1.92993 EndZ=0
    g15: LineSegment StartX=4.65926 StartY=1.92993 StartZ=0 EndX=4.001 EndY=3.07007 EndZ=0
    g16: LineSegment StartX=4.001 StartY=3.07007 StartZ=0 EndX=3.07007 EndY=4.001 EndZ=0
    g17: LineSegment StartX=3.07007 StartY=4.001 StartZ=0 EndX=1.92993 EndY=4.65926 EndZ=0
    g18: LineSegment StartX=1.92993 StartY=4.65926 StartZ=0 EndX=0.658262 EndY=5 EndZ=0
    g19: LineSegment StartX=0.658262 StartY=5 StartZ=0 EndX=-0.658262 EndY=5 EndZ=0
    g20: LineSegment StartX=-0.658262 StartY=5 StartZ=0 EndX=-1.92993 EndY=4.65926 EndZ=0
    g21: LineSegment StartX=-1.92993 StartY=4.65926 StartZ=0 EndX=-3.07007 EndY=4.001 EndZ=0
    g22: LineSegment StartX=-3.07007 StartY=4.001 StartZ=0 EndX=-4.001 EndY=3.07007 EndZ=0
    g23: LineSegment StartX=-4.001 StartY=3.07007 StartZ=0 EndX=-4.65926 EndY=1.92993 EndZ=0
    g24: Circle CenterX=0 CenterY=0 CenterZ=0 NormalX=0 NormalY=0 NormalZ=1 AngleXU=0 Radius=5.04314
  constraints (52):
    c: Coincident(g0,g1)
    c: Coincident(g1,g2)
    c: Coincident(g2,g3)
    c: Coincident(g3,g4)
    c: Coincident(g4,g5)
    c: Coincident(g5,g6)
    c: Coincident(g6,g7)
    c: Coincident(g7,g8)
    c: Coincident(g8,g9)
    c: Coincident(g9,g10)
    c: Coincident(g10,g11)
    c: Coincident(g11,g12)
    c: Coincident(g12,g13)
    c: Coincident(g13,g14)
    c: Coincident(g14,g15)
    c: Coincident(g15,g16)
    c: Coincident(g16,g17)
    c: Coincident(g17,g18)
    c: Coincident(g18,g19)
    c: Coincident(g19,g20)
    c: Coincident(g20,g21)
    c: Coincident(g21,g22)
    c: Coincident(g22,g23)
    c: Coincident(g23,g0)
    c: Equal(g0, g1-g23) x23
    c: PointOnObject(g0,g24)
    c: PointOnObject(g1,g24)
    c: PointOnObject(g2,g24)
    c: PointOnObject(g3,g24)
    c: PointOnObject(g4,g24)
    c: PointOnObject(g5,g24)
    c: PointOnObject(g6,g24)
    c: PointOnObject(g7,g24)
    c: PointOnObject(g8,g24)
    c: PointOnObject(g9,g24)
    c: PointOnObject(g10,g24)
    c: PointOnObject(g11,g24)
    c: PointOnObject(g12,g24)
    c: PointOnObject(g13,g24)
    c: PointOnObject(g14,g24)
    c: PointOnObject(g15,g24)
    c: PointOnObject(g16,g24)
    c: PointOnObject(g17,g24)
    c: PointOnObject(g18,g24)
    c: PointOnObject(g19,g24)
    c: PointOnObject(g20,g24)
    c: PointOnObject(g21,g24)
    c: PointOnObject(g22,g24)
    c: PointOnObject(g23,g24)
    c: Coincident(g24,g-1)
    c: Horizontal(g19)
    c: DistanceX(g0,g13) = 10
FEATURE [Sketcher::SketchObject] Sketch347
  AttachmentOffset = pos=(0,0,17.7) rot=(0,0,1;0rad)
  FullyConstrained = false
  MapMode = 5
  Placement = pos=(0,0,17.7) rot=(0,0,1;0rad)
  Support = -> [XY_Plane839]
  sketch-geometry (10):
    g0: LineSegment StartX=-0.2 StartY=1.5 StartZ=0 EndX=0.2 EndY=1.5 EndZ=0
    g1: LineSegment StartX=0.4 StartY=1.7 StartZ=0 EndX=0.4 EndY=4.2 EndZ=0
    g2: LineSegment StartX=0.2 StartY=4.4 StartZ=0 EndX=-0.2 EndY=4.4 EndZ=0
    g3: LineSegment StartX=-0.4 StartY=4.2 StartZ=0 EndX=-0.4 EndY=1.7 EndZ=0
    g4: ArcOfCircle CenterX=-0.2 CenterY=1.7 CenterZ=0 NormalX=0 NormalY=0 NormalZ=1 AngleXU=0 Radius=0.2 StartAngle=3.14159 EndAngle=4.71239
    g5: ArcOfCircle CenterX=0.2 CenterY=1.7 CenterZ=0 NormalX=0 NormalY=0 NormalZ=1 AngleXU=0 Radius=0.2 StartAngle=4.71239 EndAngle=6.28319
    g6: ArcOfCircle CenterX=0.2 CenterY=4.2 CenterZ=0 NormalX=0 NormalY=0 NormalZ=1 AngleXU=0 Radius=0.2 StartAngle=1.4e-15 EndAngle=1.5708
    g7: ArcOfCircle CenterX=-0.2 CenterY=4.2 CenterZ=0 NormalX=0 NormalY=0 NormalZ=1 AngleXU=0 Radius=0.2 StartAngle=1.5708 EndAngle=3.14159
    g8: LineSegment StartX=-0.2 StartY=1.7 StartZ=0 EndX=0 EndY=0 EndZ=0
    g9: LineSegment StartX=0 StartY=0 StartZ=0 EndX=0.2 EndY=1.7 EndZ=0
  constraints (24):
    c: Horizontal(g0)
    c: Horizontal(g2)
    c: Vertical(g1)
    c: Vertical(g3)
    c: Tangent(g3,g4) = -1.5708
    c: Tangent(g0,g4) = -1.5708
    c: Tangent(g0,g5) = -1.5708
    c: Tangent(g1,g5) = -1.5708
    c: Tangent(g1,g6) = -1.5708
    c: Tangent(g2,g6) = -1.5708
    c: Tangent(g2,g7) = -1.5708
    c: Tangent(g3,g7) = -1.5708
    c: Radius(g7) = 0.2
    c: Equal(g7,g6)
    c: Equal(g7,g5)
    c: Equal(g7,g4)
    c: Coincident(g8,g4)
    c: Coincident(g8,g-1)
    c: Coincident(g9,g-1)
    c: Coincident(g9,g5)
    c: Equal(g9,g8)
    c: DistanceX(g3,g1) = 0.8
    c: DistanceY(g-1,g2) = 4.4
    c: DistanceY(g-1,g0) = 1.5
FEATURE [PartDesign::Pad] Pad061
  AllowMultiFace = false
  Direction = (1,1,1)
  Length = 0.02
  Length2 = 100
  Profile = -> Sketch347
  Refine = true
  Type = 0
FEATURE [Sketcher::SketchObject] Sketch348
  AttachmentOffset = pos=(0,0,7) rot=(0,0,1;0rad)
  FullyConstrained = false
  MapMode = 5
  Placement = pos=(0,0,7) rot=(0,0,1;0rad)
  Support = -> [XY_Plane840]
  sketch-geometry (25):
    g0: LineSegment StartX=-0.724089 StartY=5.5 StartZ=0 EndX=-2.12292 EndY=5.12518 EndZ=0
    g1: LineSegment StartX=-2.12292 StartY=5.12518 StartZ=0 EndX=-3.37708 EndY=4.4011 EndZ=0
    g2: LineSegment StartX=-3.37708 StartY=4.4011 StartZ=0 EndX=-4.4011 EndY=3.37708 EndZ=0
    g3: LineSegment StartX=-4.4011 StartY=3.37708 StartZ=0 EndX=-5.12518 EndY=2.12292 EndZ=0
    g4: LineSegment StartX=-5.12518 StartY=2.12292 StartZ=0 EndX=-5.5 EndY=0.724089 EndZ=0
    g5: LineSegment StartX=-5.5 StartY=0.724089 StartZ=0 EndX=-5.5 EndY=-0.724089 EndZ=0
    g6: LineSegment StartX=-5.5 StartY=-0.724089 StartZ=0 EndX=-5.12518 EndY=-2.12292 EndZ=0
    g7: LineSegment StartX=-5.12518 StartY=-2.12292 StartZ=0 EndX=-4.4011 EndY=-3.37708 EndZ=0
    g8: LineSegment StartX=-4.4011 StartY=-3.37708 StartZ=0 EndX=-3.37708 EndY=-4.4011 EndZ=0
    g9: LineSegment StartX=-3.37708 StartY=-4.4011 StartZ=0 EndX=-2.12292 EndY=-5.12518 EndZ=0
    g10: LineSegment StartX=-2.12292 StartY=-5.12518 StartZ=0 EndX=-0.724089 EndY=-5.5 EndZ=0
    g11: LineSegment StartX=-0.724089 StartY=-5.5 StartZ=0 EndX=0.724089 EndY=-5.5 EndZ=0
    g12: LineSegment StartX=0.724089 StartY=-5.5 StartZ=0 EndX=2.12292 EndY=-5.12518 EndZ=0
    g13: LineSegment StartX=2.12292 StartY=-5.12518 StartZ=0 EndX=3.37708 EndY=-4.4011 EndZ=0
    g14: LineSegment StartX=3.37708 StartY=-4.4011 StartZ=0 EndX=4.4011 EndY=-3.37708 EndZ=0
    g15: LineSegment StartX=4.4011 StartY=-3.37708 StartZ=0 EndX=5.12518 EndY=-2.12292 EndZ=0
    g16: LineSegment StartX=5.12518 StartY=-2.12292 StartZ=0 EndX=5.5 EndY=-0.724089 EndZ=0
    g17: LineSegment StartX=5.5 StartY=-0.724089 StartZ=0 EndX=5.5 EndY=0.724089 EndZ=0
    g18: LineSegment StartX=5.5 StartY=0.724089 StartZ=0 EndX=5.12518 EndY=2.12292 EndZ=0
    g19: LineSegment StartX=5.12518 StartY=2.12292 StartZ=0 EndX=4.4011 EndY=3.37708 EndZ=0
    g20: LineSegment StartX=4.4011 StartY=3.37708 StartZ=0 EndX=3.37708 EndY=4.4011 EndZ=0
    g21: LineSegment StartX=3.37708 StartY=4.4011 StartZ=0 EndX=2.12292 EndY=5.12518 EndZ=0
    g22: LineSegment StartX=2.12292 StartY=5.12518 StartZ=0 EndX=0.724089 EndY=5.5 EndZ=0
    g23: LineSegment StartX=0.724089 StartY=5.5 StartZ=0 EndX=-0.724089 EndY=5.5 EndZ=0
    g24: Circle CenterX=0 CenterY=0 CenterZ=0 NormalX=0 NormalY=0 NormalZ=1 AngleXU=0 Radius=5.54746
  constraints (52):
    c: Coincident(g0,g1)
    c: Coincident(g1,g2)
    c: Coincident(g2,g3)
    c: Coincident(g3,g4)
    c: Coincident(g4,g5)
    c: Coincident(g5,g6)
    c: Coincident(g6,g7)
    c: Coincident(g7,g8)
    c: Coincident(g8,g9)
    c: Coincident(g9,g10)
    c: Coincident(g10,g11)
    c: Coincident(g11,g12)
    c: Coincident(g12,g13)
    c: Coincident(g13,g14)
    c: Coincident(g14,g15)
    c: Coincident(g15,g16)
    c: Coincident(g16,g17)
    c: Coincident(g17,g18)
    c: Coincident(g18,g19)
    c: Coincident(g19,g20)
    c: Coincident(g20,g21)
    c: Coincident(g21,g22)
    c: Coincident(g22,g23)
    c: Coincident(g23,g0)
    c: Equal(g0, g1-g23) x23
    c: PointOnObject(g0,g24)
    c: PointOnObject(g1,g24)
    c: PointOnObject(g2,g24)
    c: PointOnObject(g3,g24)
    c: PointOnObject(g4,g24)
    c: PointOnObject(g5,g24)
    c: PointOnObject(g6,g24)
    c: PointOnObject(g7,g24)
    c: PointOnObject(g8,g24)
    c: PointOnObject(g9,g24)
    c: PointOnObject(g10,g24)
    c: PointOnObject(g11,g24)
    c: PointOnObject(g12,g24)
    c: PointOnObject(g13,g24)
    c: PointOnObject(g14,g24)
    c: PointOnObject(g15,g24)
    c: PointOnObject(g16,g24)
    c: PointOnObject(g17,g24)
    c: PointOnObject(g18,g24)
    c: PointOnObject(g19,g24)
    c: PointOnObject(g20,g24)
    c: PointOnObject(g21,g24)
    c: PointOnObject(g22,g24)
    c: PointOnObject(g23,g24)
    c: Coincident(g24,g-1)
    c: Horizontal(g23)
    c: DistanceX(g4,g17) = 11
FEATURE [Sketcher::SketchObject] Sketch349
  FullyConstrained = false
  MapMode = 5
  Support = -> [XY_Plane840]
  sketch-geometry (25):
    g0: LineSegment StartX=-0.789915 StartY=6 StartZ=0 EndX=-2.31591 EndY=5.59111 EndZ=0
    g1: LineSegment StartX=-2.31591 StartY=5.59111 StartZ=0 EndX=-3.68409 EndY=4.80119 EndZ=0
    g2: LineSegment StartX=-3.68409 StartY=4.80119 StartZ=0 EndX=-4.80119 EndY=3.68409 EndZ=0
    g3: LineSegment StartX=-4.80119 StartY=3.68409 StartZ=0 EndX=-5.59111 EndY=2.31591 EndZ=0
    g4: LineSegment StartX=-5.59111 StartY=2.31591 StartZ=0 EndX=-6 EndY=0.789915 EndZ=0
    g5: LineSegment StartX=-6 StartY=0.789915 StartZ=0 EndX=-6 EndY=-0.789915 EndZ=0
    g6: LineSegment StartX=-6 StartY=-0.789915 StartZ=0 EndX=-5.59111 EndY=-2.31591 EndZ=0
    g7: LineSegment StartX=-5.59111 StartY=-2.31591 StartZ=0 EndX=-4.80119 EndY=-3.68409 EndZ=0
    g8: LineSegment StartX=-4.80119 StartY=-3.68409 StartZ=0 EndX=-3.68409 EndY=-4.80119 EndZ=0
    g9: LineSegment StartX=-3.68409 StartY=-4.80119 StartZ=0 EndX=-2.31591 EndY=-5.59111 EndZ=0
    g10: LineSegment StartX=-2.31591 StartY=-5.59111 StartZ=0 EndX=-0.789915 EndY=-6 EndZ=0
    g11: LineSegment StartX=-0.789915 StartY=-6 StartZ=0 EndX=0.789915 EndY=-6 EndZ=0
    g12: LineSegment StartX=0.789915 StartY=-6 StartZ=0 EndX=2.31591 EndY=-5.59111 EndZ=0
    g13: LineSegment StartX=2.31591 StartY=-5.59111 StartZ=0 EndX=3.68409 EndY=-4.80119 EndZ=0
    g14: LineSegment StartX=3.68409 StartY=-4.80119 StartZ=0 EndX=4.80119 EndY=-3.68409 EndZ=0
    g15: LineSegment StartX=4.80119 StartY=-3.68409 StartZ=0 EndX=5.59111 EndY=-2.31591 EndZ=0
    g16: LineSegment StartX=5.59111 StartY=-2.31591 StartZ=0 EndX=6 EndY=-0.789915 EndZ=0
    g17: LineSegment StartX=6 StartY=-0.789915 StartZ=0 EndX=6 EndY=0.789915 EndZ=0
    g18: LineSegment StartX=6 StartY=0.789915 StartZ=0 EndX=5.59111 EndY=2.31591 EndZ=0
    g19: LineSegment StartX=5.59111 StartY=2.31591 StartZ=0 EndX=4.80119 EndY=3.68409 EndZ=0
    g20: LineSegment StartX=4.80119 StartY=3.68409 StartZ=0 EndX=3.68409 EndY=4.80119 EndZ=0
    g21: LineSegment StartX=3.68409 StartY=4.80119 StartZ=0 EndX=2.31591 EndY=5.59111 EndZ=0
    g22: LineSegment StartX=2.31591 StartY=5.59111 StartZ=0 EndX=0.789915 EndY=6 EndZ=0
    g23: LineSegment StartX=0.789915 StartY=6 StartZ=0 EndX=-0.789915 EndY=6 EndZ=0
    g24: Circle CenterX=0 CenterY=0 CenterZ=0 NormalX=0 NormalY=0 NormalZ=1 AngleXU=0 Radius=6.05177
  constraints (52):
    c: Coincident(g0,g1)
    c: Coincident(g1,g2)
    c: Coincident(g2,g3)
    c: Coincident(g3,g4)
    c: Coincident(g4,g5)
    c: Coincident(g5,g6)
    c: Coincident(g6,g7)
    c: Coincident(g7,g8)
    c: Coincident(g8,g9)
    c: Coincident(g9,g10)
    c: Coincident(g10,g11)
    c: Coincident(g11,g12)
    c: Coincident(g12,g13)
    c: Coincident(g13,g14)
    c: Coincident(g14,g15)
    c: Coincident(g15,g16)
    c: Coincident(g16,g17)
    c: Coincident(g17,g18)
    c: Coincident(g18,g19)
    c: Coincident(g19,g20)
    c: Coincident(g20,g21)
    c: Coincident(g21,g22)
    c: Coincident(g22,g23)
    c: Coincident(g23,g0)
    c: Equal(g0, g1-g23) x23
    c: PointOnObject(g0,g24)
    c: PointOnObject(g1,g24)
    c: PointOnObject(g2,g24)
    c: PointOnObject(g3,g24)
    c: PointOnObject(g4,g24)
    c: PointOnObject(g5,g24)
    c: PointOnObject(g6,g24)
    c: PointOnObject(g7,g24)
    c: PointOnObject(g8,g24)
    c: PointOnObject(g9,g24)
    c: PointOnObject(g10,g24)
    c: PointOnObject(g11,g24)
    c: PointOnObject(g12,g24)
    c: PointOnObject(g13,g24)
    c: PointOnObject(g14,g24)
    c: PointOnObject(g15,g24)
    c: PointOnObject(g16,g24)
    c: PointOnObject(g17,g24)
    c: PointOnObject(g18,g24)
    c: PointOnObject(g19,g24)
    c: PointOnObject(g20,g24)
    c: PointOnObject(g21,g24)
    c: PointOnObject(g22,g24)
    c: PointOnObject(g23,g24)
    c: Coincident(g24,g-1)
    c: Horizontal(g23)
    c: DistanceX(g4,g17) = 12
FEATURE [Sketcher::SketchObject] Sketch350
  AttachmentOffset = pos=(0,0,17) rot=(0,0,1;0rad)
  FullyConstrained = false
  MapMode = 5
  Placement = pos=(0,0,17) rot=(0,0,1;0rad)
  Support = -> [XY_Plane840]
  sketch-geometry (25):
    g0: LineSegment StartX=-4.65926 StartY=1.92993 StartZ=0 EndX=-5 EndY=0.658262 EndZ=0
    g1: LineSegment StartX=-5 StartY=0.658262 StartZ=0 EndX=-5 EndY=-0.658262 EndZ=0
    g2: LineSegment StartX=-5 StartY=-0.658262 StartZ=0 EndX=-4.65926 EndY=-1.92993 EndZ=0
    g3: LineSegment StartX=-4.65926 StartY=-1.92993 StartZ=0 EndX=-4.001 EndY=-3.07007 EndZ=0
    g4: LineSegment StartX=-4.001 StartY=-3.07007 StartZ=0 EndX=-3.07007 EndY=-4.001 EndZ=0
    g5: LineSegment StartX=-3.07007 StartY=-4.001 StartZ=0 EndX=-1.92993 EndY=-4.65926 EndZ=0
    g6: LineSegment StartX=-1.92993 StartY=-4.65926 StartZ=0 EndX=-0.658262 EndY=-5 EndZ=0
    g7: LineSegment StartX=-0.658262 StartY=-5 StartZ=0 EndX=0.658262 EndY=-5 EndZ=0
    g8: LineSegment StartX=0.658262 StartY=-5 StartZ=0 EndX=1.92993 EndY=-4.65926 EndZ=0
    g9: LineSegment StartX=1.92993 StartY=-4.65926 StartZ=0 EndX=3.07007 EndY=-4.001 EndZ=0
    g10: LineSegment StartX=3.07007 StartY=-4.001 StartZ=0 EndX=4.001 EndY=-3.07007 EndZ=0
    g11: LineSegment StartX=4.001 StartY=-3.07007 StartZ=0 EndX=4.65926 EndY=-1.92993 EndZ=0
    g12: LineSegment StartX=4.65926 StartY=-1.92993 StartZ=0 EndX=5 EndY=-0.658262 EndZ=0
    g13: LineSegment StartX=5 StartY=-0.658262 StartZ=0 EndX=5 EndY=0.658262 EndZ=0
    g14: LineSegment StartX=5 StartY=0.658262 StartZ=0 EndX=4.65926 EndY=1.92993 EndZ=0
    g15: LineSegment StartX=4.65926 StartY=1.92993 StartZ=0 EndX=4.001 EndY=3.07007 EndZ=0
    g16: LineSegment StartX=4.001 StartY=3.07007 StartZ=0 EndX=3.07007 EndY=4.001 EndZ=0
    g17: LineSegment StartX=3.07007 StartY=4.001 StartZ=0 EndX=1.92993 EndY=4.65926 EndZ=0
    g18: LineSegment StartX=1.92993 StartY=4.65926 StartZ=0 EndX=0.658262 EndY=5 EndZ=0
    g19: LineSegment StartX=0.658262 StartY=5 StartZ=0 EndX=-0.658262 EndY=5 EndZ=0
    g20: LineSegment StartX=-0.658262 StartY=5 StartZ=0 EndX=-1.92993 EndY=4.65926 EndZ=0
    g21: LineSegment StartX=-1.92993 StartY=4.65926 StartZ=0 EndX=-3.07007 EndY=4.001 EndZ=0
    g22: LineSegment StartX=-3.07007 StartY=4.001 StartZ=0 EndX=-4.001 EndY=3.07007 EndZ=0
    g23: LineSegment StartX=-4.001 StartY=3.07007 StartZ=0 EndX=-4.65926 EndY=1.92993 EndZ=0
    g24: Circle CenterX=0 CenterY=0 CenterZ=0 NormalX=0 NormalY=0 NormalZ=1 AngleXU=0 Radius=5.04314
  constraints (52):
    c: Coincident(g0,g1)
    c: Coincident(g1,g2)
    c: Coincident(g2,g3)
    c: Coincident(g3,g4)
    c: Coincident(g4,g5)
    c: Coincident(g5,g6)
    c: Coincident(g6,g7)
    c: Coincident(g7,g8)
    c: Coincident(g8,g9)
    c: Coincident(g9,g10)
    c: Coincident(g10,g11)
    c: Coincident(g11,g12)
    c: Coincident(g12,g13)
    c: Coincident(g13,g14)
    c: Coincident(g14,g15)
    c: Coincident(g15,g16)
    c: Coincident(g16,g17)
    c: Coincident(g17,g18)
    c: Coincident(g18,g19)
    c: Coincident(g19,g20)
    c: Coincident(g20,g21)
    c: Coincident(g21,g22)
    c: Coincident(g22,g23)
    c: Coincident(g23,g0)
    c: Equal(g0, g1-g23) x23
    c: PointOnObject(g0,g24)
    c: PointOnObject(g1,g24)
    c: PointOnObject(g2,g24)
    c: PointOnObject(g3,g24)
    c: PointOnObject(g4,g24)
    c: PointOnObject(g5,g24)
    c: PointOnObject(g6,g24)
    c: PointOnObject(g7,g24)
    c: PointOnObject(g8,g24)
    c: PointOnObject(g9,g24)
    c: PointOnObject(g10,g24)
    c: PointOnObject(g11,g24)
    c: PointOnObject(g12,g24)
    c: PointOnObject(g13,g24)
    c: PointOnObject(g14,g24)
    c: PointOnObject(g15,g24)
    c: PointOnObject(g16,g24)
    c: PointOnObject(g17,g24)
    c: PointOnObject(g18,g24)
    c: PointOnObject(g19,g24)
    c: PointOnObject(g20,g24)
    c: PointOnObject(g21,g24)
    c: PointOnObject(g22,g24)
    c: PointOnObject(g23,g24)
    c: Coincident(g24,g-1)
    c: Horizontal(g19)
    c: DistanceX(g0,g13) = 10
FEATURE [PartDesign::AdditiveLoft] AdditiveLoft016
  AllowMultiFace = false
  Closed = false
  Profile = -> Sketch349
  Refine = true
  Ruled = false
  Sections = -> [Sketch348,Sketch350]
FEATURE [Sketcher::SketchObject] Sketch351
  FullyConstrained = false
  MapMode = 5
  Placement = pos=(0,0,17) rot=(0,0,1;0rad)
  Support = -> [AdditiveLoft016]
  sketch-geometry (1):
    g0: Circle CenterX=0 CenterY=0 CenterZ=0 NormalX=0 NormalY=0 NormalZ=1 AngleXU=0 Radius=4.5
  constraints (2):
    c: Coincident(g0,g-1)
    c: Radius(g0) = 4.5
FEATURE [PartDesign::Pad] Pad060
  AllowMultiFace = false
  BaseFeature = -> AdditiveLoft016
  Direction = (1,1,1)
  Length = 0.7
  Length2 = 100
  Profile = -> Sketch351
  Refine = true
  Type = 0
FEATURE [Sketcher::SketchObject] Sketch352
  FullyConstrained = false
  MapMode = 5
  Placement = pos=(0,0,0) rot=(1,0,0;3.14159rad)
  Support = -> [Pad060]
  sketch-geometry (1):
    g0: Circle CenterX=0 CenterY=0 CenterZ=0 NormalX=0 NormalY=0 NormalZ=1 AngleXU=0 Radius=5
  constraints (2):
    c: Coincident(g0,g-1)
    c: Radius(g0) = 5
FEATURE [PartDesign::Pocket] Pocket050
  AllowMultiFace = false
  BaseFeature = -> Pad060
  Direction = (1,1,1)
  Length = 1
  Length2 = 100
  Profile = -> Sketch352
  Refine = true
  Type = 0
FEATURE [Sketcher::SketchObject] Sketch342
  FullyConstrained = false
  MapMode = 5
  Placement = pos=(0,0,1) rot=(1,0,0;3.14159rad)
  Support = -> [Pocket050]
  sketch-geometry (1):
    g0: Circle CenterX=0 CenterY=0 CenterZ=0 NormalX=0 NormalY=0 NormalZ=1 AngleXU=0 Radius=4.65
  constraints (2):
    c: Coincident(g0,g-1)
    c: Radius(g0) = 4.65
FEATURE [PartDesign::Pocket] Pocket051
  AllowMultiFace = false
  BaseFeature = -> Pocket050
  Direction = (1,1,1)
  Length = 1
  Length2 = 100
  Profile = -> Sketch342
  Refine = true
  Type = 0
FEATURE [Sketcher::SketchObject] Sketch353
  FullyConstrained = false
  MapMode = 5
  Placement = pos=(0,0,2) rot=(1,0,0;3.14159rad)
  Support = -> [Pocket051]
  sketch-geometry (2):
    g0: ArcOfCircle CenterX=0 CenterY=0 CenterZ=0 NormalX=0 NormalY=0 NormalZ=1 AngleXU=0 Radius=3 StartAngle=2.19024 EndAngle=7.23453
    g1: LineSegment StartX=-1.74176 StartY=2.4426 StartZ=0 EndX=1.74176 EndY=2.4426 EndZ=0
  constraints (5):
    c: Coincident(g0,g-1)
    c: Coincident(g1,g0)
    c: Coincident(g1,g0)
    c: Horizontal(g1)
    c: Radius(g0) = 3
FEATURE [PartDesign::Pocket] Pocket052
  AllowMultiFace = false
  BaseFeature = -> Pocket051
  Direction = (1,1,1)
  Length = 8
  Length2 = 100
  Profile = -> Sketch353
  Refine = true
  Type = 0
FEATURE [PartDesign::Chamfer] Chamfer041
  Angle = 45
  Base = -> Pocket052 [Edge82,Edge83]
  BaseFeature = -> Pocket052
  ChamferType = 0
  FlipDirection = false
  Size = 1.4
  Size2 = 1
  SupportTransform = false
  UseAllEdges = false
FEATURE [PartDesign::Chamfer] Chamfer042
  Angle = 45
  Base = -> Chamfer041 [Edge8]
  BaseFeature = -> Chamfer041
  ChamferType = 0
  FlipDirection = false
  Size = 0.3
  Size2 = 1
  SupportTransform = false
  UseAllEdges = false
FEATURE [PartDesign::Fillet] Fillet022
  Base = -> Chamfer042 [Edge93,Face36]
  BaseFeature = -> Chamfer042
  Radius = 0.1
  SupportTransform = false
  UseAllEdges = false
FEATURE [Sketcher::SketchObject] Sketch356
  FullyConstrained = false
  MapMode = 5
  Support = -> [XY_Plane843]
  sketch-geometry (25):
    g0: LineSegment StartX=-0.789915 StartY=6 StartZ=0 EndX=-2.31591 EndY=5.59111 EndZ=0
    g1: LineSegment StartX=-2.31591 StartY=5.59111 StartZ=0 EndX=-3.68409 EndY=4.80119 EndZ=0
    g2: LineSegment StartX=-3.68409 StartY=4.80119 StartZ=0 EndX=-4.80119 EndY=3.68409 EndZ=0
    g3: LineSegment StartX=-4.80119 StartY=3.68409 StartZ=0 EndX=-5.59111 EndY=2.31591 EndZ=0
    g4: LineSegment StartX=-5.59111 StartY=2.31591 StartZ=0 EndX=-6 EndY=0.789915 EndZ=0
    g5: LineSegment StartX=-6 StartY=0.789915 StartZ=0 EndX=-6 EndY=-0.789915 EndZ=0
    g6: LineSegment StartX=-6 StartY=-0.789915 StartZ=0 EndX=-5.59111 EndY=-2.31591 EndZ=0
    g7: LineSegment StartX=-5.59111 StartY=-2.31591 StartZ=0 EndX=-4.80119 EndY=-3.68409 EndZ=0
    g8: LineSegment StartX=-4.80119 StartY=-3.68409 StartZ=0 EndX=-3.68409 EndY=-4.80119 EndZ=0
    g9: LineSegment StartX=-3.68409 StartY=-4.80119 StartZ=0 EndX=-2.31591 EndY=-5.59111 EndZ=0
    g10: LineSegment StartX=-2.31591 StartY=-5.59111 StartZ=0 EndX=-0.789915 EndY=-6 EndZ=0
    g11: LineSegment StartX=-0.789915 StartY=-6 StartZ=0 EndX=0.789915 EndY=-6 EndZ=0
    g12: LineSegment StartX=0.789915 StartY=-6 StartZ=0 EndX=2.31591 EndY=-5.59111 EndZ=0
    g13: LineSegment StartX=2.31591 StartY=-5.59111 StartZ=0 EndX=3.68409 EndY=-4.80119 EndZ=0
    g14: LineSegment StartX=3.68409 StartY=-4.80119 StartZ=0 EndX=4.80119 EndY=-3.68409 EndZ=0
    g15: LineSegment StartX=4.80119 StartY=-3.68409 StartZ=0 EndX=5.59111 EndY=-2.31591 EndZ=0
    g16: LineSegment StartX=5.59111 StartY=-2.31591 StartZ=0 EndX=6 EndY=-0.789915 EndZ=0
    g17: LineSegment StartX=6 StartY=-0.789915 StartZ=0 EndX=6 EndY=0.789915 EndZ=0
    g18: LineSegment StartX=6 StartY=0.789915 StartZ=0 EndX=5.59111 EndY=2.31591 EndZ=0
    g19: LineSegment StartX=5.59111 StartY=2.31591 StartZ=0 EndX=4.80119 EndY=3.68409 EndZ=0
    g20: LineSegment StartX=4.80119 StartY=3.68409 StartZ=0 EndX=3.68409 EndY=4.80119 EndZ=0
    g21: LineSegment StartX=3.68409 StartY=4.80119 StartZ=0 EndX=2.31591 EndY=5.59111 EndZ=0
    g22: LineSegment StartX=2.31591 StartY=5.59111 StartZ=0 EndX=0.789915 EndY=6 EndZ=0
    g23: LineSegment StartX=0.789915 StartY=6 StartZ=0 EndX=-0.789915 EndY=6 EndZ=0
    g24: Circle CenterX=0 CenterY=0 CenterZ=0 NormalX=0 NormalY=0 NormalZ=1 AngleXU=0 Radius=6.05177
  constraints (52):
    c: Coincident(g0,g1)
    c: Coincident(g1,g2)
    c: Coincident(g2,g3)
    c: Coincident(g3,g4)
    c: Coincident(g4,g5)
    c: Coincident(g5,g6)
    c: Coincident(g6,g7)
    c: Coincident(g7,g8)
    c: Coincident(g8,g9)
    c: Coincident(g9,g10)
    c: Coincident(g10,g11)
    c: Coincident(g11,g12)
    c: Coincident(g12,g13)
    c: Coincident(g13,g14)
    c: Coincident(g14,g15)
    c: Coincident(g15,g16)
    c: Coincident(g16,g17)
    c: Coincident(g17,g18)
    c: Coincident(g18,g19)
    c: Coincident(g19,g20)
    c: Coincident(g20,g21)
    c: Coincident(g21,g22)
    c: Coincident(g22,g23)
    c: Coincident(g23,g0)
    c: Equal(g0, g1-g23) x23
    c: PointOnObject(g0,g24)
    c: PointOnObject(g1,g24)
    c: PointOnObject(g2,g24)
    c: PointOnObject(g3,g24)
    c: PointOnObject(g4,g24)
    c: PointOnObject(g5,g24)
    c: PointOnObject(g6,g24)
    c: PointOnObject(g7,g24)
    c: PointOnObject(g8,g24)
    c: PointOnObject(g9,g24)
    c: PointOnObject(g10,g24)
    c: PointOnObject(g11,g24)
    c: PointOnObject(g12,g24)
    c: PointOnObject(g13,g24)
    c: PointOnObject(g14,g24)
    c: PointOnObject(g15,g24)
    c: PointOnObject(g16,g24)
    c: PointOnObject(g17,g24)
    c: PointOnObject(g18,g24)
    c: PointOnObject(g19,g24)
    c: PointOnObject(g20,g24)
    c: PointOnObject(g21,g24)
    c: PointOnObject(g22,g24)
    c: PointOnObject(g23,g24)
    c: Coincident(g24,g-1)
    c: Horizontal(g23)
    c: DistanceX(g4,g17) = 12
FEATURE [Sketcher::SketchObject] Sketch357
  AttachmentOffset = pos=(0,0,7) rot=(0,0,1;0rad)
  FullyConstrained = false
  MapMode = 5
  Placement = pos=(0,0,7) rot=(0,0,1;0rad)
  Support = -> [XY_Plane848]
  sketch-geometry (25):
    g0: LineSegment StartX=-0.724089 StartY=5.5 StartZ=0 EndX=-2.12292 EndY=5.12518 EndZ=0
    g1: LineSegment StartX=-2.12292 StartY=5.12518 StartZ=0 EndX=-3.37708 EndY=4.4011 EndZ=0
    g2: LineSegment StartX=-3.37708 StartY=4.4011 StartZ=0 EndX=-4.4011 EndY=3.37708 EndZ=0
    g3: LineSegment StartX=-4.4011 StartY=3.37708 StartZ=0 EndX=-5.12518 EndY=2.12292 EndZ=0
    g4: LineSegment StartX=-5.12518 StartY=2.12292 StartZ=0 EndX=-5.5 EndY=0.724089 EndZ=0
    g5: LineSegment StartX=-5.5 StartY=0.724089 StartZ=0 EndX=-5.5 EndY=-0.724089 EndZ=0
    g6: LineSegment StartX=-5.5 StartY=-0.724089 StartZ=0 EndX=-5.12518 EndY=-2.12292 EndZ=0
    g7: LineSegment StartX=-5.12518 StartY=-2.12292 StartZ=0 EndX=-4.4011 EndY=-3.37708 EndZ=0
    g8: LineSegment StartX=-4.4011 StartY=-3.37708 StartZ=0 EndX=-3.37708 EndY=-4.4011 EndZ=0
    g9: LineSegment StartX=-3.37708 StartY=-4.4011 StartZ=0 EndX=-2.12292 EndY=-5.12518 EndZ=0
    g10: LineSegment StartX=-2.12292 StartY=-5.12518 StartZ=0 EndX=-0.724089 EndY=-5.5 EndZ=0
    g11: LineSegment StartX=-0.724089 StartY=-5.5 StartZ=0 EndX=0.724089 EndY=-5.5 EndZ=0
    g12: LineSegment StartX=0.724089 StartY=-5.5 StartZ=0 EndX=2.12292 EndY=-5.12518 EndZ=0
    g13: LineSegment StartX=2.12292 StartY=-5.12518 StartZ=0 EndX=3.37708 EndY=-4.4011 EndZ=0
    g14: LineSegment StartX=3.37708 StartY=-4.4011 StartZ=0 EndX=4.4011 EndY=-3.37708 EndZ=0
    g15: LineSegment StartX=4.4011 StartY=-3.37708 StartZ=0 EndX=5.12518 EndY=-2.12292 EndZ=0
    g16: LineSegment StartX=5.12518 StartY=-2.12292 StartZ=0 EndX=5.5 EndY=-0.724089 EndZ=0
    g17: LineSegment StartX=5.5 StartY=-0.724089 StartZ=0 EndX=5.5 EndY=0.724089 EndZ=0
    g18: LineSegment StartX=5.5 StartY=0.724089 StartZ=0 EndX=5.12518 EndY=2.12292 EndZ=0
    g19: LineSegment StartX=5.12518 StartY=2.12292 StartZ=0 EndX=4.4011 EndY=3.37708 EndZ=0
    g20: LineSegment StartX=4.4011 StartY=3.37708 StartZ=0 EndX=3.37708 EndY=4.4011 EndZ=0
    g21: LineSegment StartX=3.37708 StartY=4.4011 StartZ=0 EndX=2.12292 EndY=5.12518 EndZ=0
    g22: LineSegment StartX=2.12292 StartY=5.12518 StartZ=0 EndX=0.724089 EndY=5.5 EndZ=0
    g23: LineSegment StartX=0.724089 StartY=5.5 StartZ=0 EndX=-0.724089 EndY=5.5 EndZ=0
    g24: Circle CenterX=0 CenterY=0 CenterZ=0 NormalX=0 NormalY=0 NormalZ=1 AngleXU=0 Radius=5.54746
  constraints (52):
    c: Coincident(g0,g1)
    c: Coincident(g1,g2)
    c: Coincident(g2,g3)
    c: Coincident(g3,g4)
    c: Coincident(g4,g5)
    c: Coincident(g5,g6)
    c: Coincident(g6,g7)
    c: Coincident(g7,g8)
    c: Coincident(g8,g9)
    c: Coincident(g9,g10)
    c: Coincident(g10,g11)
    c: Coincident(g11,g12)
    c: Coincident(g12,g13)
    c: Coincident(g13,g14)
    c: Coincident(g14,g15)
    c: Coincident(g15,g16)
    c: Coincident(g16,g17)
    c: Coincident(g17,g18)
    c: Coincident(g18,g19)
    c: Coincident(g19,g20)
    c: Coincident(g20,g21)
    c: Coincident(g21,g22)
    c: Coincident(g22,g23)
    c: Coincident(g23,g0)
    c: Equal(g0, g1-g23) x23
    c: PointOnObject(g0,g24)
    c: PointOnObject(g1,g24)
    c: PointOnObject(g2,g24)
    c: PointOnObject(g3,g24)
    c: PointOnObject(g4,g24)
    c: PointOnObject(g5,g24)
    c: PointOnObject(g6,g24)
    c: PointOnObject(g7,g24)
    c: PointOnObject(g8,g24)
    c: PointOnObject(g9,g24)
    c: PointOnObject(g10,g24)
    c: PointOnObject(g11,g24)
    c: PointOnObject(g12,g24)
    c: PointOnObject(g13,g24)
    c: PointOnObject(g14,g24)
    c: PointOnObject(g15,g24)
    c: PointOnObject(g16,g24)
    c: PointOnObject(g17,g24)
    c: PointOnObject(g18,g24)
    c: PointOnObject(g19,g24)
    c: PointOnObject(g20,g24)
    c: PointOnObject(g21,g24)
    c: PointOnObject(g22,g24)
    c: PointOnObject(g23,g24)
    c: Coincident(g24,g-1)
    c: Horizontal(g23)
    c: DistanceX(g4,g17) = 11
FEATURE [Sketcher::SketchObject] Sketch362
  FullyConstrained = false
  MapMode = 5
  Support = -> [XY_Plane848]
  sketch-geometry (25):
    g0: LineSegment StartX=-0.789915 StartY=6 StartZ=0 EndX=-2.31591 EndY=5.59111 EndZ=0
    g1: LineSegment StartX=-2.31591 StartY=5.59111 StartZ=0 EndX=-3.68409 EndY=4.80119 EndZ=0
    g2: LineSegment StartX=-3.68409 StartY=4.80119 StartZ=0 EndX=-4.80119 EndY=3.68409 EndZ=0
    g3: LineSegment StartX=-4.80119 StartY=3.68409 StartZ=0 EndX=-5.59111 EndY=2.31591 EndZ=0
    g4: LineSegment StartX=-5.59111 StartY=2.31591 StartZ=0 EndX=-6 EndY=0.789915 EndZ=0
    g5: LineSegment StartX=-6 StartY=0.789915 StartZ=0 EndX=-6 EndY=-0.789915 EndZ=0
    g6: LineSegment StartX=-6 StartY=-0.789915 StartZ=0 EndX=-5.59111 EndY=-2.31591 EndZ=0
    g7: LineSegment StartX=-5.59111 StartY=-2.31591 StartZ=0 EndX=-4.80119 EndY=-3.68409 EndZ=0
    g8: LineSegment StartX=-4.80119 StartY=-3.68409 StartZ=0 EndX=-3.68409 EndY=-4.80119 EndZ=0
    g9: LineSegment StartX=-3.68409 StartY=-4.80119 StartZ=0 EndX=-2.31591 EndY=-5.59111 EndZ=0
    g10: LineSegment StartX=-2.31591 StartY=-5.59111 StartZ=0 EndX=-0.789915 EndY=-6 EndZ=0
    g11: LineSegment StartX=-0.789915 StartY=-6 StartZ=0 EndX=0.789915 EndY=-6 EndZ=0
    g12: LineSegment StartX=0.789915 StartY=-6 StartZ=0 EndX=2.31591 EndY=-5.59111 EndZ=0
    g13: LineSegment StartX=2.31591 StartY=-5.59111 StartZ=0 EndX=3.68409 EndY=-4.80119 EndZ=0
    g14: LineSegment StartX=3.68409 StartY=-4.80119 StartZ=0 EndX=4.80119 EndY=-3.68409 EndZ=0
    g15: LineSegment StartX=4.80119 StartY=-3.68409 StartZ=0 EndX=5.59111 EndY=-2.31591 EndZ=0
    g16: LineSegment StartX=5.59111 StartY=-2.31591 StartZ=0 EndX=6 EndY=-0.789915 EndZ=0
    g17: LineSegment StartX=6 StartY=-0.789915 StartZ=0 EndX=6 EndY=0.789915 EndZ=0
    g18: LineSegment StartX=6 StartY=0.789915 StartZ=0 EndX=5.59111 EndY=2.31591 EndZ=0
    g19: LineSegment StartX=5.59111 StartY=2.31591 StartZ=0 EndX=4.80119 EndY=3.68409 EndZ=0
    g20: LineSegment StartX=4.80119 StartY=3.68409 StartZ=0 EndX=3.68409 EndY=4.80119 EndZ=0
    g21: LineSegment StartX=3.68409 StartY=4.80119 StartZ=0 EndX=2.31591 EndY=5.59111 EndZ=0
    g22: LineSegment StartX=2.31591 StartY=5.59111 StartZ=0 EndX=0.789915 EndY=6 EndZ=0
    g23: LineSegment StartX=0.789915 StartY=6 StartZ=0 EndX=-0.789915 EndY=6 EndZ=0
    g24: Circle CenterX=0 CenterY=0 CenterZ=0 NormalX=0 NormalY=0 NormalZ=1 AngleXU=0 Radius=6.05177
  constraints (52):
    c: Coincident(g0,g1)
    c: Coincident(g1,g2)
    c: Coincident(g2,g3)
    c: Coincident(g3,g4)
    c: Coincident(g4,g5)
    c: Coincident(g5,g6)
    c: Coincident(g6,g7)
    c: Coincident(g7,g8)
    c: Coincident(g8,g9)
    c: Coincident(g9,g10)
    c: Coincident(g10,g11)
    c: Coincident(g11,g12)
    c: Coincident(g12,g13)
    c: Coincident(g13,g14)
    c: Coincident(g14,g15)
    c: Coincident(g15,g16)
    c: Coincident(g16,g17)
    c: Coincident(g17,g18)
    c: Coincident(g18,g19)
    c: Coincident(g19,g20)
    c: Coincident(g20,g21)
    c: Coincident(g21,g22)
    c: Coincident(g22,g23)
    c: Coincident(g23,g0)
    c: Equal(g0, g1-g23) x23
    c: PointOnObject(g0,g24)
    c: PointOnObject(g1,g24)
    c: PointOnObject(g2,g24)
    c: PointOnObject(g3,g24)
    c: PointOnObject(g4,g24)
    c: PointOnObject(g5,g24)
    c: PointOnObject(g6,g24)
    c: PointOnObject(g7,g24)
    c: PointOnObject(g8,g24)
    c: PointOnObject(g9,g24)
    c: PointOnObject(g10,g24)
    c: PointOnObject(g11,g24)
    c: PointOnObject(g12,g24)
    c: PointOnObject(g13,g24)
    c: PointOnObject(g14,g24)
    c: PointOnObject(g15,g24)
    c: PointOnObject(g16,g24)
    c: PointOnObject(g17,g24)
    c: PointOnObject(g18,g24)
    c: PointOnObject(g19,g24)
    c: PointOnObject(g20,g24)
    c: PointOnObject(g21,g24)
    c: PointOnObject(g22,g24)
    c: PointOnObject(g23,g24)
    c: Coincident(g24,g-1)
    c: Horizontal(g23)
    c: DistanceX(g4,g17) = 12
FEATURE [Sketcher::SketchObject] Sketch363
  AttachmentOffset = pos=(0,0,17.7) rot=(0,0,1;0rad)
  FullyConstrained = false
  MapMode = 5
  Placement = pos=(0,0,17.7) rot=(0,0,1;0rad)
  Support = -> [XY_Plane844]
  sketch-geometry (10):
    g0: LineSegment StartX=-0.2 StartY=1.5 StartZ=0 EndX=0.2 EndY=1.5 EndZ=0
    g1: LineSegment StartX=0.4 StartY=1.7 StartZ=0 EndX=0.4 EndY=4.2 EndZ=0
    g2: LineSegment StartX=0.2 StartY=4.4 StartZ=0 EndX=-0.2 EndY=4.4 EndZ=0
    g3: LineSegment StartX=-0.4 StartY=4.2 StartZ=0 EndX=-0.4 EndY=1.7 EndZ=0
    g4: ArcOfCircle CenterX=-0.2 CenterY=1.7 CenterZ=0 NormalX=0 NormalY=0 NormalZ=1 AngleXU=0 Radius=0.2 StartAngle=3.14159 EndAngle=4.71239
    g5: ArcOfCircle CenterX=0.2 CenterY=1.7 CenterZ=0 NormalX=0 NormalY=0 NormalZ=1 AngleXU=0 Radius=0.2 StartAngle=4.71239 EndAngle=6.28319
    g6: ArcOfCircle CenterX=0.2 CenterY=4.2 CenterZ=0 NormalX=0 NormalY=0 NormalZ=1 AngleXU=0 Radius=0.2 StartAngle=1.4e-15 EndAngle=1.5708
    g7: ArcOfCircle CenterX=-0.2 CenterY=4.2 CenterZ=0 NormalX=0 NormalY=0 NormalZ=1 AngleXU=0 Radius=0.2 StartAngle=1.5708 EndAngle=3.14159
    g8: LineSegment StartX=-0.2 StartY=1.7 StartZ=0 EndX=0 EndY=0 EndZ=0
    g9: LineSegment StartX=0 StartY=0 StartZ=0 EndX=0.2 EndY=1.7 EndZ=0
  constraints (24):
    c: Horizontal(g0)
    c: Horizontal(g2)
    c: Vertical(g1)
    c: Vertical(g3)
    c: Tangent(g3,g4) = -1.5708
    c: Tangent(g0,g4) = -1.5708
    c: Tangent(g0,g5) = -1.5708
    c: Tangent(g1,g5) = -1.5708
    c: Tangent(g1,g6) = -1.5708
    c: Tangent(g2,g6) = -1.5708
    c: Tangent(g2,g7) = -1.5708
    c: Tangent(g3,g7) = -1.5708
    c: Radius(g7) = 0.2
    c: Equal(g7,g6)
    c: Equal(g7,g5)
    c: Equal(g7,g4)
    c: Coincident(g8,g4)
    c: Coincident(g8,g-1)
    c: Coincident(g9,g-1)
    c: Coincident(g9,g5)
    c: Equal(g9,g8)
    c: DistanceX(g3,g1) = 0.8
    c: DistanceY(g-1,g2) = 4.4
    c: DistanceY(g-1,g0) = 1.5
FEATURE [PartDesign::Pad] Pad063
  AllowMultiFace = false
  Direction = (1,1,1)
  Length = 0.02
  Length2 = 100
  Profile = -> Sketch363
  Refine = true
  Type = 0
FEATURE [Sketcher::SketchObject] Sketch364
  AttachmentOffset = pos=(0,0,17) rot=(0,0,1;0rad)
  FullyConstrained = false
  MapMode = 5
  Placement = pos=(0,0,17) rot=(0,0,1;0rad)
  Support = -> [XY_Plane848]
  sketch-geometry (25):
    g0: LineSegment StartX=-4.65926 StartY=1.92993 StartZ=0 EndX=-5 EndY=0.658262 EndZ=0
    g1: LineSegment StartX=-5 StartY=0.658262 StartZ=0 EndX=-5 EndY=-0.658262 EndZ=0
    g2: LineSegment StartX=-5 StartY=-0.658262 StartZ=0 EndX=-4.65926 EndY=-1.92993 EndZ=0
    g3: LineSegment StartX=-4.65926 StartY=-1.92993 StartZ=0 EndX=-4.001 EndY=-3.07007 EndZ=0
    g4: LineSegment StartX=-4.001 StartY=-3.07007 StartZ=0 EndX=-3.07007 EndY=-4.001 EndZ=0
    g5: LineSegment StartX=-3.07007 StartY=-4.001 StartZ=0 EndX=-1.92993 EndY=-4.65926 EndZ=0
    g6: LineSegment StartX=-1.92993 StartY=-4.65926 StartZ=0 EndX=-0.658262 EndY=-5 EndZ=0
    g7: LineSegment StartX=-0.658262 StartY=-5 StartZ=0 EndX=0.658262 EndY=-5 EndZ=0
    g8: LineSegment StartX=0.658262 StartY=-5 StartZ=0 EndX=1.92993 EndY=-4.65926 EndZ=0
    g9: LineSegment StartX=1.92993 StartY=-4.65926 StartZ=0 EndX=3.07007 EndY=-4.001 EndZ=0
    g10: LineSegment StartX=3.07007 StartY=-4.001 StartZ=0 EndX=4.001 EndY=-3.07007 EndZ=0
    g11: LineSegment StartX=4.001 StartY=-3.07007 StartZ=0 EndX=4.65926 EndY=-1.92993 EndZ=0
    g12: LineSegment StartX=4.65926 StartY=-1.92993 StartZ=0 EndX=5 EndY=-0.658262 EndZ=0
    g13: LineSegment StartX=5 StartY=-0.658262 StartZ=0 EndX=5 EndY=0.658262 EndZ=0
    g14: LineSegment StartX=5 StartY=0.658262 StartZ=0 EndX=4.65926 EndY=1.92993 EndZ=0
    g15: LineSegment StartX=4.65926 StartY=1.92993 StartZ=0 EndX=4.001 EndY=3.07007 EndZ=0
    g16: LineSegment StartX=4.001 StartY=3.07007 StartZ=0 EndX=3.07007 EndY=4.001 EndZ=0
    g17: LineSegment StartX=3.07007 StartY=4.001 StartZ=0 EndX=1.92993 EndY=4.65926 EndZ=0
    g18: LineSegment StartX=1.92993 StartY=4.65926 StartZ=0 EndX=0.658262 EndY=5 EndZ=0
    g19: LineSegment StartX=0.658262 StartY=5 StartZ=0 EndX=-0.658262 EndY=5 EndZ=0
    g20: LineSegment StartX=-0.658262 StartY=5 StartZ=0 EndX=-1.92993 EndY=4.65926 EndZ=0
    g21: LineSegment StartX=-1.92993 StartY=4.65926 StartZ=0 EndX=-3.07007 EndY=4.001 EndZ=0
    g22: LineSegment StartX=-3.07007 StartY=4.001 StartZ=0 EndX=-4.001 EndY=3.07007 EndZ=0
    g23: LineSegment StartX=-4.001 StartY=3.07007 StartZ=0 EndX=-4.65926 EndY=1.92993 EndZ=0
    g24: Circle CenterX=0 CenterY=0 CenterZ=0 NormalX=0 NormalY=0 NormalZ=1 AngleXU=0 Radius=5.04314
  constraints (52):
    c: Coincident(g0,g1)
    c: Coincident(g1,g2)
    c: Coincident(g2,g3)
    c: Coincident(g3,g4)
    c: Coincident(g4,g5)
    c: Coincident(g5,g6)
    c: Coincident(g6,g7)
    c: Coincident(g7,g8)
    c: Coincident(g8,g9)
    c: Coincident(g9,g10)
    c: Coincident(g10,g11)
    c: Coincident(g11,g12)
    c: Coincident(g12,g13)
    c: Coincident(g13,g14)
    c: Coincident(g14,g15)
    c: Coincident(g15,g16)
    c: Coincident(g16,g17)
    c: Coincident(g17,g18)
    c: Coincident(g18,g19)
    c: Coincident(g19,g20)
    c: Coincident(g20,g21)
    c: Coincident(g21,g22)
    c: Coincident(g22,g23)
    c: Coincident(g23,g0)
    c: Equal(g0, g1-g23) x23
    c: PointOnObject(g0,g24)
    c: PointOnObject(g1,g24)
    c: PointOnObject(g2,g24)
    c: PointOnObject(g3,g24)
    c: PointOnObject(g4,g24)
    c: PointOnObject(g5,g24)
    c: PointOnObject(g6,g24)
    c: PointOnObject(g7,g24)
    c: PointOnObject(g8,g24)
    c: PointOnObject(g9,g24)
    c: PointOnObject(g10,g24)
    c: PointOnObject(g11,g24)
    c: PointOnObject(g12,g24)
    c: PointOnObject(g13,g24)
    c: PointOnObject(g14,g24)
    c: PointOnObject(g15,g24)
    c: PointOnObject(g16,g24)
    c: PointOnObject(g17,g24)
    c: PointOnObject(g18,g24)
    c: PointOnObject(g19,g24)
    c: PointOnObject(g20,g24)
    c: PointOnObject(g21,g24)
    c: PointOnObject(g22,g24)
    c: PointOnObject(g23,g24)
    c: Coincident(g24,g-1)
    c: Horizontal(g19)
    c: DistanceX(g0,g13) = 10
FEATURE [PartDesign::Body] Body147  label="Indicator016"
  Group = -> [Sketch347,Pad061]
  Origin = -> Origin839
  Tip = -> Pad061
FEATURE [PartDesign::Body] Body154  label="Indicator019"
  Group = -> [Sketch363,Pad063]
  Origin = -> Origin841
  Tip = -> Pad063
FEATURE [PartDesign::Body] Body157
  Group = -> [Sketch349,Sketch348,Sketch350,AdditiveLoft016,Sketch351,Pad060,Sketch352,Pocket050,Sketch342,Pocket051,Sketch353,Pocket052,Chamfer041,Chamfer042,Fillet022]
  Origin = -> Origin845
  Tip = -> Fillet022
FEATURE [App::Part] Part122  label="Cap023"
  Group = -> [Body157,Body147]
  Origin = -> Origin846
  Placement = pos=(-40.005,40.005,0) rot=(0,0,1;0rad)
  expr: .Placement.Base.x = -40.005
  expr: .Placement.Base.y = 40.005
FEATURE [PartDesign::AdditiveLoft] AdditiveLoft027
  AllowMultiFace = false
  Closed = false
  Profile = -> Sketch356
  Refine = true
  Ruled = false
  Sections = -> [Sketch345,Sketch346]
FEATURE [Sketcher::SketchObject] Sketch355
  FullyConstrained = false
  MapMode = 5
  Placement = pos=(0,0,17) rot=(0,0,1;0rad)
  Support = -> [AdditiveLoft027]
  sketch-geometry (1):
    g0: Circle CenterX=0 CenterY=0 CenterZ=0 NormalX=0 NormalY=0 NormalZ=1 AngleXU=0 Radius=4.5
  constraints (2):
    c: Coincident(g0,g-1)
    c: Radius(g0) = 4.5
FEATURE [PartDesign::Pad] Pad062
  AllowMultiFace = false
  BaseFeature = -> AdditiveLoft027
  Direction = (1,1,1)
  Length = 0.7
  Length2 = 100
  Profile = -> Sketch355
  Refine = true
  Type = 0
FEATURE [Sketcher::SketchObject] Sketch354
  FullyConstrained = false
  MapMode = 5
  Placement = pos=(0,0,0) rot=(1,0,0;3.14159rad)
  Support = -> [Pad062]
  sketch-geometry (1):
    g0: Circle CenterX=0 CenterY=0 CenterZ=0 NormalX=0 NormalY=0 NormalZ=1 AngleXU=0 Radius=5
  constraints (2):
    c: Coincident(g0,g-1)
    c: Radius(g0) = 5
FEATURE [PartDesign::Pocket] Pocket053
  AllowMultiFace = false
  BaseFeature = -> Pad062
  Direction = (1,1,1)
  Length = 1
  Length2 = 100
  Profile = -> Sketch354
  Refine = true
  Type = 0
FEATURE [Sketcher::SketchObject] Sketch343
  FullyConstrained = false
  MapMode = 5
  Placement = pos=(0,0,1) rot=(1,0,0;3.14159rad)
  Support = -> [Pocket053]
  sketch-geometry (1):
    g0: Circle CenterX=0 CenterY=0 CenterZ=0 NormalX=0 NormalY=0 NormalZ=1 AngleXU=0 Radius=4.65
  constraints (2):
    c: Coincident(g0,g-1)
    c: Radius(g0) = 4.65
FEATURE [PartDesign::Pocket] Pocket054
  AllowMultiFace = false
  BaseFeature = -> Pocket053
  Direction = (1,1,1)
  Length = 1
  Length2 = 100
  Profile = -> Sketch343
  Refine = true
  Type = 0
FEATURE [Sketcher::SketchObject] Sketch344
  FullyConstrained = false
  MapMode = 5
  Placement = pos=(0,0,2) rot=(1,0,0;3.14159rad)
  Support = -> [Pocket054]
  sketch-geometry (2):
    g0: ArcOfCircle CenterX=0 CenterY=0 CenterZ=0 NormalX=0 NormalY=0 NormalZ=1 AngleXU=0 Radius=3 StartAngle=2.19024 EndAngle=7.23453
    g1: LineSegment StartX=-1.74176 StartY=2.4426 StartZ=0 EndX=1.74176 EndY=2.4426 EndZ=0
  constraints (5):
    c: Coincident(g0,g-1)
    c: Coincident(g1,g0)
    c: Coincident(g1,g0)
    c: Horizontal(g1)
    c: Radius(g0) = 3
FEATURE [PartDesign::Pocket] Pocket049
  AllowMultiFace = false
  BaseFeature = -> Pocket054
  Direction = (1,1,1)
  Length = 8
  Length2 = 100
  Profile = -> Sketch344
  Refine = true
  Type = 0
FEATURE [PartDesign::Chamfer] Chamfer043
  Angle = 45
  Base = -> Pocket049 [Edge82,Edge83]
  BaseFeature = -> Pocket049
  ChamferType = 0
  FlipDirection = false
  Size = 1.4
  Size2 = 1
  SupportTransform = false
  UseAllEdges = false
FEATURE [PartDesign::Chamfer] Chamfer044
  Angle = 45
  Base = -> Chamfer043 [Edge8]
  BaseFeature = -> Chamfer043
  ChamferType = 0
  FlipDirection = false
  Size = 0.3
  Size2 = 1
  SupportTransform = false
  UseAllEdges = false
FEATURE [PartDesign::Fillet] Fillet023
  Base = -> Chamfer044 [Edge93,Face36]
  BaseFeature = -> Chamfer044
  Radius = 0.1
  SupportTransform = false
  UseAllEdges = false
FEATURE [PartDesign::Body] Body149
  Group = -> [Sketch356,Sketch345,Sketch346,AdditiveLoft027,Sketch355,Pad062,Sketch354,Pocket053,Sketch343,Pocket054,Sketch344,Pocket049,Chamfer043,Chamfer044,Fillet023]
  Origin = -> Origin840
  Tip = -> Fillet023
FEATURE [App::Part] Part124  label="Cap025"
  Group = -> [Body149,Body154]
  Origin = -> Origin842
  Placement = pos=(-13.34,40.005,0) rot=(0,0,1;0rad)
  expr: .Placement.Base.x = -13.335
  expr: .Placement.Base.y = 40.005
FEATURE [PartDesign::AdditiveLoft] AdditiveLoft028
  AllowMultiFace = false
  Closed = false
  Profile = -> Sketch362
  Refine = true
  Ruled = false
  Sections = -> [Sketch357,Sketch364]
FEATURE [Sketcher::SketchObject] Sketch361
  FullyConstrained = false
  MapMode = 5
  Placement = pos=(0,0,17) rot=(0,0,1;0rad)
  Support = -> [AdditiveLoft028]
  sketch-geometry (1):
    g0: Circle CenterX=0 CenterY=0 CenterZ=0 NormalX=0 NormalY=0 NormalZ=1 AngleXU=0 Radius=4.5
  constraints (2):
    c: Coincident(g0,g-1)
    c: Radius(g0) = 4.5
FEATURE [PartDesign::Pad] Pad064
  AllowMultiFace = false
  BaseFeature = -> AdditiveLoft028
  Direction = (1,1,1)
  Length = 0.7
  Length2 = 100
  Profile = -> Sketch361
  Refine = true
  Type = 0
FEATURE [Sketcher::SketchObject] Sketch360
  FullyConstrained = false
  MapMode = 5
  Placement = pos=(0,0,0) rot=(1,0,0;3.14159rad)
  Support = -> [Pad064]
  sketch-geometry (1):
    g0: Circle CenterX=0 CenterY=0 CenterZ=0 NormalX=0 NormalY=0 NormalZ=1 AngleXU=0 Radius=5
  constraints (2):
    c: Coincident(g0,g-1)
    c: Radius(g0) = 5
FEATURE [PartDesign::Pocket] Pocket061
  AllowMultiFace = false
  BaseFeature = -> Pad064
  Direction = (1,1,1)
  Length = 1
  Length2 = 100
  Profile = -> Sketch360
  Refine = true
  Type = 0
FEATURE [Sketcher::SketchObject] Sketch358
  FullyConstrained = false
  MapMode = 5
  Placement = pos=(0,0,1) rot=(1,0,0;3.14159rad)
  Support = -> [Pocket061]
  sketch-geometry (1):
    g0: Circle CenterX=0 CenterY=0 CenterZ=0 NormalX=0 NormalY=0 NormalZ=1 AngleXU=0 Radius=4.65
  constraints (2):
    c: Coincident(g0,g-1)
    c: Radius(g0) = 4.65
FEATURE [PartDesign::Pocket] Pocket055
  AllowMultiFace = false
  BaseFeature = -> Pocket061
  Direction = (1,1,1)
  Length = 1
  Length2 = 100
  Profile = -> Sketch358
  Refine = true
  Type = 0
FEATURE [Sketcher::SketchObject] Sketch359
  FullyConstrained = false
  MapMode = 5
  Placement = pos=(0,0,2) rot=(1,0,0;3.14159rad)
  Support = -> [Pocket055]
  sketch-geometry (2):
    g0: ArcOfCircle CenterX=0 CenterY=0 CenterZ=0 NormalX=0 NormalY=0 NormalZ=1 AngleXU=0 Radius=3 StartAngle=2.19024 EndAngle=7.23453
    g1: LineSegment StartX=-1.74176 StartY=2.4426 StartZ=0 EndX=1.74176 EndY=2.4426 EndZ=0
  constraints (5):
    c: Coincident(g0,g-1)
    c: Coincident(g1,g0)
    c: Coincident(g1,g0)
    c: Horizontal(g1)
    c: Radius(g0) = 3
FEATURE [PartDesign::Pocket] Pocket060
  AllowMultiFace = false
  BaseFeature = -> Pocket055
  Direction = (1,1,1)
  Length = 8
  Length2 = 100
  Profile = -> Sketch359
  Refine = true
  Type = 0
FEATURE [PartDesign::Chamfer] Chamfer049
  Angle = 45
  Base = -> Pocket060 [Edge82,Edge83]
  BaseFeature = -> Pocket060
  ChamferType = 0
  FlipDirection = false
  Size = 1.4
  Size2 = 1
  SupportTransform = false
  UseAllEdges = false
FEATURE [PartDesign::Chamfer] Chamfer048
  Angle = 45
  Base = -> Chamfer049 [Edge8]
  BaseFeature = -> Chamfer049
  ChamferType = 0
  FlipDirection = false
  Size = 0.3
  Size2 = 1
  SupportTransform = false
  UseAllEdges = false
FEATURE [PartDesign::Fillet] Fillet021
  Base = -> Chamfer048 [Edge93,Face36]
  BaseFeature = -> Chamfer048
  Radius = 0.1
  SupportTransform = false
  UseAllEdges = false
FEATURE [PartDesign::Body] Body148
  Group = -> [Sketch362,Sketch357,Sketch364,AdditiveLoft028,Sketch361,Pad064,Sketch360,Pocket061,Sketch358,Pocket055,Sketch359,Pocket060,Chamfer049,Chamfer048,Fillet021]
  Origin = -> Origin852
  Tip = -> Fillet021
FEATURE [Sketcher::SketchObject] Sketch368
  AttachmentOffset = pos=(0,0,17.7) rot=(0,0,1;0rad)
  FullyConstrained = false
  MapMode = 5
  Placement = pos=(0,0,17.7) rot=(0,0,1;0rad)
  Support = -> [XY_Plane850]
  sketch-geometry (10):
    g0: LineSegment StartX=-0.2 StartY=1.5 StartZ=0 EndX=0.2 EndY=1.5 EndZ=0
    g1: LineSegment StartX=0.4 StartY=1.7 StartZ=0 EndX=0.4 EndY=4.2 EndZ=0
    g2: LineSegment StartX=0.2 StartY=4.4 StartZ=0 EndX=-0.2 EndY=4.4 EndZ=0
    g3: LineSegment StartX=-0.4 StartY=4.2 StartZ=0 EndX=-0.4 EndY=1.7 EndZ=0
    g4: ArcOfCircle CenterX=-0.2 CenterY=1.7 CenterZ=0 NormalX=0 NormalY=0 NormalZ=1 AngleXU=0 Radius=0.2 StartAngle=3.14159 EndAngle=4.71239
    g5: ArcOfCircle CenterX=0.2 CenterY=1.7 CenterZ=0 NormalX=0 NormalY=0 NormalZ=1 AngleXU=0 Radius=0.2 StartAngle=4.71239 EndAngle=6.28319
    g6: ArcOfCircle CenterX=0.2 CenterY=4.2 CenterZ=0 NormalX=0 NormalY=0 NormalZ=1 AngleXU=0 Radius=0.2 StartAngle=1.4e-15 EndAngle=1.5708
    g7: ArcOfCircle CenterX=-0.2 CenterY=4.2 CenterZ=0 NormalX=0 NormalY=0 NormalZ=1 AngleXU=0 Radius=0.2 StartAngle=1.5708 EndAngle=3.14159
    g8: LineSegment StartX=-0.2 StartY=1.7 StartZ=0 EndX=0 EndY=0 EndZ=0
    g9: LineSegment StartX=0 StartY=0 StartZ=0 EndX=0.2 EndY=1.7 EndZ=0
  constraints (24):
    c: Horizontal(g0)
    c: Horizontal(g2)
    c: Vertical(g1)
    c: Vertical(g3)
    c: Tangent(g3,g4) = -1.5708
    c: Tangent(g0,g4) = -1.5708
    c: Tangent(g0,g5) = -1.5708
    c: Tangent(g1,g5) = -1.5708
    c: Tangent(g1,g6) = -1.5708
    c: Tangent(g2,g6) = -1.5708
    c: Tangent(g2,g7) = -1.5708
    c: Tangent(g3,g7) = -1.5708
    c: Radius(g7) = 0.2
    c: Equal(g7,g6)
    c: Equal(g7,g5)
    c: Equal(g7,g4)
    c: Coincident(g8,g4)
    c: Coincident(g8,g-1)
    c: Coincident(g9,g-1)
    c: Coincident(g9,g5)
    c: Equal(g9,g8)
    c: DistanceX(g3,g1) = 0.8
    c: DistanceY(g-1,g2) = 4.4
    c: DistanceY(g-1,g0) = 1.5
FEATURE [PartDesign::Pad] Pad066
  AllowMultiFace = false
  Direction = (1,1,1)
  Length = 0.02
  Length2 = 100
  Profile = -> Sketch368
  Refine = true
  Type = 0
FEATURE [PartDesign::Body] Body152  label="Indicator017"
  Group = -> [Sketch368,Pad066]
  Origin = -> Origin849
  Tip = -> Pad066
FEATURE [Sketcher::SketchObject] Sketch373
  AttachmentOffset = pos=(0,0,17.7) rot=(0,0,1;0rad)
  FullyConstrained = false
  MapMode = 5
  Placement = pos=(0,0,17.7) rot=(0,0,1;0rad)
  Support = -> [XY_Plane845]
  sketch-geometry (10):
    g0: LineSegment StartX=-0.2 StartY=1.5 StartZ=0 EndX=0.2 EndY=1.5 EndZ=0
    g1: LineSegment StartX=0.4 StartY=1.7 StartZ=0 EndX=0.4 EndY=4.2 EndZ=0
    g2: LineSegment StartX=0.2 StartY=4.4 StartZ=0 EndX=-0.2 EndY=4.4 EndZ=0
    g3: LineSegment StartX=-0.4 StartY=4.2 StartZ=0 EndX=-0.4 EndY=1.7 EndZ=0
    g4: ArcOfCircle CenterX=-0.2 CenterY=1.7 CenterZ=0 NormalX=0 NormalY=0 NormalZ=1 AngleXU=0 Radius=0.2 StartAngle=3.14159 EndAngle=4.71239
    g5: ArcOfCircle CenterX=0.2 CenterY=1.7 CenterZ=0 NormalX=0 NormalY=0 NormalZ=1 AngleXU=0 Radius=0.2 StartAngle=4.71239 EndAngle=6.28319
    g6: ArcOfCircle CenterX=0.2 CenterY=4.2 CenterZ=0 NormalX=0 NormalY=0 NormalZ=1 AngleXU=0 Radius=0.2 StartAngle=1.4e-15 EndAngle=1.5708
    g7: ArcOfCircle CenterX=-0.2 CenterY=4.2 CenterZ=0 NormalX=0 NormalY=0 NormalZ=1 AngleXU=0 Radius=0.2 StartAngle=1.5708 EndAngle=3.14159
    g8: LineSegment StartX=-0.2 StartY=1.7 StartZ=0 EndX=0 EndY=0 EndZ=0
    g9: LineSegment StartX=0 StartY=0 StartZ=0 EndX=0.2 EndY=1.7 EndZ=0
  constraints (24):
    c: Horizontal(g0)
    c: Horizontal(g2)
    c: Vertical(g1)
    c: Vertical(g3)
    c: Tangent(g3,g4) = -1.5708
    c: Tangent(g0,g4) = -1.5708
    c: Tangent(g0,g5) = -1.5708
    c: Tangent(g1,g5) = -1.5708
    c: Tangent(g1,g6) = -1.5708
    c: Tangent(g2,g6) = -1.5708
    c: Tangent(g2,g7) = -1.5708
    c: Tangent(g3,g7) = -1.5708
    c: Radius(g7) = 0.2
    c: Equal(g7,g6)
    c: Equal(g7,g5)
    c: Equal(g7,g4)
    c: Coincident(g8,g4)
    c: Coincident(g8,g-1)
    c: Coincident(g9,g-1)
    c: Coincident(g9,g5)
    c: Equal(g9,g8)
    c: DistanceX(g3,g1) = 0.8
    c: DistanceY(g-1,g2) = 4.4
    c: DistanceY(g-1,g0) = 1.5
FEATURE [PartDesign::Pad] Pad065
  AllowMultiFace = false
  Direction = (1,1,1)
  Length = 0.02
  Length2 = 100
  Profile = -> Sketch373
  Refine = true
  Type = 0
FEATURE [PartDesign::Body] Body155  label="Indicator020"
  Group = -> [Sketch373,Pad065]
  Origin = -> Origin844
  Tip = -> Pad065
FEATURE [App::Part] Part117  label="Cap018"
  Group = -> [Body148,Body155]
  Origin = -> Origin843
  Placement = pos=(13.335,40.005,0) rot=(0,0,1;0rad)
  expr: .Placement.Base.x = 13.335
  expr: .Placement.Base.y = 40.005
FEATURE [Sketcher::SketchObject] Sketch376
  AttachmentOffset = pos=(0,0,7) rot=(0,0,1;0rad)
  FullyConstrained = false
  MapMode = 5
  Placement = pos=(0,0,7) rot=(0,0,1;0rad)
  Support = -> [XY_Plane846]
  sketch-geometry (25):
    g0: LineSegment StartX=-0.724089 StartY=5.5 StartZ=0 EndX=-2.12292 EndY=5.12518 EndZ=0
    g1: LineSegment StartX=-2.12292 StartY=5.12518 StartZ=0 EndX=-3.37708 EndY=4.4011 EndZ=0
    g2: LineSegment StartX=-3.37708 StartY=4.4011 StartZ=0 EndX=-4.4011 EndY=3.37708 EndZ=0
    g3: LineSegment StartX=-4.4011 StartY=3.37708 StartZ=0 EndX=-5.12518 EndY=2.12292 EndZ=0
    g4: LineSegment StartX=-5.12518 StartY=2.12292 StartZ=0 EndX=-5.5 EndY=0.724089 EndZ=0
    g5: LineSegment StartX=-5.5 StartY=0.724089 StartZ=0 EndX=-5.5 EndY=-0.724089 EndZ=0
    g6: LineSegment StartX=-5.5 StartY=-0.724089 StartZ=0 EndX=-5.12518 EndY=-2.12292 EndZ=0
    g7: LineSegment StartX=-5.12518 StartY=-2.12292 StartZ=0 EndX=-4.4011 EndY=-3.37708 EndZ=0
    g8: LineSegment StartX=-4.4011 StartY=-3.37708 StartZ=0 EndX=-3.37708 EndY=-4.4011 EndZ=0
    g9: LineSegment StartX=-3.37708 StartY=-4.4011 StartZ=0 EndX=-2.12292 EndY=-5.12518 EndZ=0
    g10: LineSegment StartX=-2.12292 StartY=-5.12518 StartZ=0 EndX=-0.724089 EndY=-5.5 EndZ=0
    g11: LineSegment StartX=-0.724089 StartY=-5.5 StartZ=0 EndX=0.724089 EndY=-5.5 EndZ=0
    g12: LineSegment StartX=0.724089 StartY=-5.5 StartZ=0 EndX=2.12292 EndY=-5.12518 EndZ=0
    g13: LineSegment StartX=2.12292 StartY=-5.12518 StartZ=0 EndX=3.37708 EndY=-4.4011 EndZ=0
    g14: LineSegment StartX=3.37708 StartY=-4.4011 StartZ=0 EndX=4.4011 EndY=-3.37708 EndZ=0
    g15: LineSegment StartX=4.4011 StartY=-3.37708 StartZ=0 EndX=5.12518 EndY=-2.12292 EndZ=0
    g16: LineSegment StartX=5.12518 StartY=-2.12292 StartZ=0 EndX=5.5 EndY=-0.724089 EndZ=0
    g17: LineSegment StartX=5.5 StartY=-0.724089 StartZ=0 EndX=5.5 EndY=0.724089 EndZ=0
    g18: LineSegment StartX=5.5 StartY=0.724089 StartZ=0 EndX=5.12518 EndY=2.12292 EndZ=0
    g19: LineSegment StartX=5.12518 StartY=2.12292 StartZ=0 EndX=4.4011 EndY=3.37708 EndZ=0
    g20: LineSegment StartX=4.4011 StartY=3.37708 StartZ=0 EndX=3.37708 EndY=4.4011 EndZ=0
    g21: LineSegment StartX=3.37708 StartY=4.4011 StartZ=0 EndX=2.12292 EndY=5.12518 EndZ=0
    g22: LineSegment StartX=2.12292 StartY=5.12518 StartZ=0 EndX=0.724089 EndY=5.5 EndZ=0
    g23: LineSegment StartX=0.724089 StartY=5.5 StartZ=0 EndX=-0.724089 EndY=5.5 EndZ=0
    g24: Circle CenterX=0 CenterY=0 CenterZ=0 NormalX=0 NormalY=0 NormalZ=1 AngleXU=0 Radius=5.54746
  constraints (52):
    c: Coincident(g0,g1)
    c: Coincident(g1,g2)
    c: Coincident(g2,g3)
    c: Coincident(g3,g4)
    c: Coincident(g4,g5)
    c: Coincident(g5,g6)
    c: Coincident(g6,g7)
    c: Coincident(g7,g8)
    c: Coincident(g8,g9)
    c: Coincident(g9,g10)
    c: Coincident(g10,g11)
    c: Coincident(g11,g12)
    c: Coincident(g12,g13)
    c: Coincident(g13,g14)
    c: Coincident(g14,g15)
    c: Coincident(g15,g16)
    c: Coincident(g16,g17)
    c: Coincident(g17,g18)
    c: Coincident(g18,g19)
    c: Coincident(g19,g20)
    c: Coincident(g20,g21)
    c: Coincident(g21,g22)
    c: Coincident(g22,g23)
    c: Coincident(g23,g0)
    c: Equal(g0, g1-g23) x23
    c: PointOnObject(g0,g24)
    c: PointOnObject(g1,g24)
    c: PointOnObject(g2,g24)
    c: PointOnObject(g3,g24)
    c: PointOnObject(g4,g24)
    c: PointOnObject(g5,g24)
    c: PointOnObject(g6,g24)
    c: PointOnObject(g7,g24)
    c: PointOnObject(g8,g24)
    c: PointOnObject(g9,g24)
    c: PointOnObject(g10,g24)
    c: PointOnObject(g11,g24)
    c: PointOnObject(g12,g24)
    c: PointOnObject(g13,g24)
    c: PointOnObject(g14,g24)
    c: PointOnObject(g15,g24)
    c: PointOnObject(g16,g24)
    c: PointOnObject(g17,g24)
    c: PointOnObject(g18,g24)
    c: PointOnObject(g19,g24)
    c: PointOnObject(g20,g24)
    c: PointOnObject(g21,g24)
    c: PointOnObject(g22,g24)
    c: PointOnObject(g23,g24)
    c: Coincident(g24,g-1)
    c: Horizontal(g23)
    c: DistanceX(g4,g17) = 11
FEATURE [Sketcher::SketchObject] Sketch378
  AttachmentOffset = pos=(0,0,17) rot=(0,0,1;0rad)
  FullyConstrained = false
  MapMode = 5
  Placement = pos=(0,0,17) rot=(0,0,1;0rad)
  Support = -> [XY_Plane846]
  sketch-geometry (25):
    g0: LineSegment StartX=-4.65926 StartY=1.92993 StartZ=0 EndX=-5 EndY=0.658262 EndZ=0
    g1: LineSegment StartX=-5 StartY=0.658262 StartZ=0 EndX=-5 EndY=-0.658262 EndZ=0
    g2: LineSegment StartX=-5 StartY=-0.658262 StartZ=0 EndX=-4.65926 EndY=-1.92993 EndZ=0
    g3: LineSegment StartX=-4.65926 StartY=-1.92993 StartZ=0 EndX=-4.001 EndY=-3.07007 EndZ=0
    g4: LineSegment StartX=-4.001 StartY=-3.07007 StartZ=0 EndX=-3.07007 EndY=-4.001 EndZ=0
    g5: LineSegment StartX=-3.07007 StartY=-4.001 StartZ=0 EndX=-1.92993 EndY=-4.65926 EndZ=0
    g6: LineSegment StartX=-1.92993 StartY=-4.65926 StartZ=0 EndX=-0.658262 EndY=-5 EndZ=0
    g7: LineSegment StartX=-0.658262 StartY=-5 StartZ=0 EndX=0.658262 EndY=-5 EndZ=0
    g8: LineSegment StartX=0.658262 StartY=-5 StartZ=0 EndX=1.92993 EndY=-4.65926 EndZ=0
    g9: LineSegment StartX=1.92993 StartY=-4.65926 StartZ=0 EndX=3.07007 EndY=-4.001 EndZ=0
    g10: LineSegment StartX=3.07007 StartY=-4.001 StartZ=0 EndX=4.001 EndY=-3.07007 EndZ=0
    g11: LineSegment StartX=4.001 StartY=-3.07007 StartZ=0 EndX=4.65926 EndY=-1.92993 EndZ=0
    g12: LineSegment StartX=4.65926 StartY=-1.92993 StartZ=0 EndX=5 EndY=-0.658262 EndZ=0
    g13: LineSegment StartX=5 StartY=-0.658262 StartZ=0 EndX=5 EndY=0.658262 EndZ=0
    g14: LineSegment StartX=5 StartY=0.658262 StartZ=0 EndX=4.65926 EndY=1.92993 EndZ=0
    g15: LineSegment StartX=4.65926 StartY=1.92993 StartZ=0 EndX=4.001 EndY=3.07007 EndZ=0
    g16: LineSegment StartX=4.001 StartY=3.07007 StartZ=0 EndX=3.07007 EndY=4.001 EndZ=0
    g17: LineSegment StartX=3.07007 StartY=4.001 StartZ=0 EndX=1.92993 EndY=4.65926 EndZ=0
    g18: LineSegment StartX=1.92993 StartY=4.65926 StartZ=0 EndX=0.658262 EndY=5 EndZ=0
    g19: LineSegment StartX=0.658262 StartY=5 StartZ=0 EndX=-0.658262 EndY=5 EndZ=0
    g20: LineSegment StartX=-0.658262 StartY=5 StartZ=0 EndX=-1.92993 EndY=4.65926 EndZ=0
    g21: LineSegment StartX=-1.92993 StartY=4.65926 StartZ=0 EndX=-3.07007 EndY=4.001 EndZ=0
    g22: LineSegment StartX=-3.07007 StartY=4.001 StartZ=0 EndX=-4.001 EndY=3.07007 EndZ=0
    g23: LineSegment StartX=-4.001 StartY=3.07007 StartZ=0 EndX=-4.65926 EndY=1.92993 EndZ=0
    g24: Circle CenterX=0 CenterY=0 CenterZ=0 NormalX=0 NormalY=0 NormalZ=1 AngleXU=0 Radius=5.04314
  constraints (52):
    c: Coincident(g0,g1)
    c: Coincident(g1,g2)
    c: Coincident(g2,g3)
    c: Coincident(g3,g4)
    c: Coincident(g4,g5)
    c: Coincident(g5,g6)
    c: Coincident(g6,g7)
    c: Coincident(g7,g8)
    c: Coincident(g8,g9)
    c: Coincident(g9,g10)
    c: Coincident(g10,g11)
    c: Coincident(g11,g12)
    c: Coincident(g12,g13)
    c: Coincident(g13,g14)
    c: Coincident(g14,g15)
    c: Coincident(g15,g16)
    c: Coincident(g16,g17)
    c: Coincident(g17,g18)
    c: Coincident(g18,g19)
    c: Coincident(g19,g20)
    c: Coincident(g20,g21)
    c: Coincident(g21,g22)
    c: Coincident(g22,g23)
    c: Coincident(g23,g0)
    c: Equal(g0, g1-g23) x23
    c: PointOnObject(g0,g24)
    c: PointOnObject(g1,g24)
    c: PointOnObject(g2,g24)
    c: PointOnObject(g3,g24)
    c: PointOnObject(g4,g24)
    c: PointOnObject(g5,g24)
    c: PointOnObject(g6,g24)
    c: PointOnObject(g7,g24)
    c: PointOnObject(g8,g24)
    c: PointOnObject(g9,g24)
    c: PointOnObject(g10,g24)
    c: PointOnObject(g11,g24)
    c: PointOnObject(g12,g24)
    c: PointOnObject(g13,g24)
    c: PointOnObject(g14,g24)
    c: PointOnObject(g15,g24)
    c: PointOnObject(g16,g24)
    c: PointOnObject(g17,g24)
    c: PointOnObject(g18,g24)
    c: PointOnObject(g19,g24)
    c: PointOnObject(g20,g24)
    c: PointOnObject(g21,g24)
    c: PointOnObject(g22,g24)
    c: PointOnObject(g23,g24)
    c: Coincident(g24,g-1)
    c: Horizontal(g19)
    c: DistanceX(g0,g13) = 10
FEATURE [Sketcher::SketchObject] Sketch379
  FullyConstrained = false
  MapMode = 5
  Support = -> [XY_Plane846]
  sketch-geometry (25):
    g0: LineSegment StartX=-0.789915 StartY=6 StartZ=0 EndX=-2.31591 EndY=5.59111 EndZ=0
    g1: LineSegment StartX=-2.31591 StartY=5.59111 StartZ=0 EndX=-3.68409 EndY=4.80119 EndZ=0
    g2: LineSegment StartX=-3.68409 StartY=4.80119 StartZ=0 EndX=-4.80119 EndY=3.68409 EndZ=0
    g3: LineSegment StartX=-4.80119 StartY=3.68409 StartZ=0 EndX=-5.59111 EndY=2.31591 EndZ=0
    g4: LineSegment StartX=-5.59111 StartY=2.31591 StartZ=0 EndX=-6 EndY=0.789915 EndZ=0
    g5: LineSegment StartX=-6 StartY=0.789915 StartZ=0 EndX=-6 EndY=-0.789915 EndZ=0
    g6: LineSegment StartX=-6 StartY=-0.789915 StartZ=0 EndX=-5.59111 EndY=-2.31591 EndZ=0
    g7: LineSegment StartX=-5.59111 StartY=-2.31591 StartZ=0 EndX=-4.80119 EndY=-3.68409 EndZ=0
    g8: LineSegment StartX=-4.80119 StartY=-3.68409 StartZ=0 EndX=-3.68409 EndY=-4.80119 EndZ=0
    g9: LineSegment StartX=-3.68409 StartY=-4.80119 StartZ=0 EndX=-2.31591 EndY=-5.59111 EndZ=0
    g10: LineSegment StartX=-2.31591 StartY=-5.59111 StartZ=0 EndX=-0.789915 EndY=-6 EndZ=0
    g11: LineSegment StartX=-0.789915 StartY=-6 StartZ=0 EndX=0.789915 EndY=-6 EndZ=0
    g12: LineSegment StartX=0.789915 StartY=-6 StartZ=0 EndX=2.31591 EndY=-5.59111 EndZ=0
    g13: LineSegment StartX=2.31591 StartY=-5.59111 StartZ=0 EndX=3.68409 EndY=-4.80119 EndZ=0
    g14: LineSegment StartX=3.68409 StartY=-4.80119 StartZ=0 EndX=4.80119 EndY=-3.68409 EndZ=0
    g15: LineSegment StartX=4.80119 StartY=-3.68409 StartZ=0 EndX=5.59111 EndY=-2.31591 EndZ=0
    g16: LineSegment StartX=5.59111 StartY=-2.31591 StartZ=0 EndX=6 EndY=-0.789915 EndZ=0
    g17: LineSegment StartX=6 StartY=-0.789915 StartZ=0 EndX=6 EndY=0.789915 EndZ=0
    g18: LineSegment StartX=6 StartY=0.789915 StartZ=0 EndX=5.59111 EndY=2.31591 EndZ=0
    g19: LineSegment StartX=5.59111 StartY=2.31591 StartZ=0 EndX=4.80119 EndY=3.68409 EndZ=0
    g20: LineSegment StartX=4.80119 StartY=3.68409 StartZ=0 EndX=3.68409 EndY=4.80119 EndZ=0
    g21: LineSegment StartX=3.68409 StartY=4.80119 StartZ=0 EndX=2.31591 EndY=5.59111 EndZ=0
    g22: LineSegment StartX=2.31591 StartY=5.59111 StartZ=0 EndX=0.789915 EndY=6 EndZ=0
    g23: LineSegment StartX=0.789915 StartY=6 StartZ=0 EndX=-0.789915 EndY=6 EndZ=0
    g24: Circle CenterX=0 CenterY=0 CenterZ=0 NormalX=0 NormalY=0 NormalZ=1 AngleXU=0 Radius=6.05177
  constraints (52):
    c: Coincident(g0,g1)
    c: Coincident(g1,g2)
    c: Coincident(g2,g3)
    c: Coincident(g3,g4)
    c: Coincident(g4,g5)
    c: Coincident(g5,g6)
    c: Coincident(g6,g7)
    c: Coincident(g7,g8)
    c: Coincident(g8,g9)
    c: Coincident(g9,g10)
    c: Coincident(g10,g11)
    c: Coincident(g11,g12)
    c: Coincident(g12,g13)
    c: Coincident(g13,g14)
    c: Coincident(g14,g15)
    c: Coincident(g15,g16)
    c: Coincident(g16,g17)
    c: Coincident(g17,g18)
    c: Coincident(g18,g19)
    c: Coincident(g19,g20)
    c: Coincident(g20,g21)
    c: Coincident(g21,g22)
    c: Coincident(g22,g23)
    c: Coincident(g23,g0)
    c: Equal(g0, g1-g23) x23
    c: PointOnObject(g0,g24)
    c: PointOnObject(g1,g24)
    c: PointOnObject(g2,g24)
    c: PointOnObject(g3,g24)
    c: PointOnObject(g4,g24)
    c: PointOnObject(g5,g24)
    c: PointOnObject(g6,g24)
    c: PointOnObject(g7,g24)
    c: PointOnObject(g8,g24)
    c: PointOnObject(g9,g24)
    c: PointOnObject(g10,g24)
    c: PointOnObject(g11,g24)
    c: PointOnObject(g12,g24)
    c: PointOnObject(g13,g24)
    c: PointOnObject(g14,g24)
    c: PointOnObject(g15,g24)
    c: PointOnObject(g16,g24)
    c: PointOnObject(g17,g24)
    c: PointOnObject(g18,g24)
    c: PointOnObject(g19,g24)
    c: PointOnObject(g20,g24)
    c: PointOnObject(g21,g24)
    c: PointOnObject(g22,g24)
    c: PointOnObject(g23,g24)
    c: Coincident(g24,g-1)
    c: Horizontal(g23)
    c: DistanceX(g4,g17) = 12
FEATURE [PartDesign::AdditiveLoft] AdditiveLoft030
  AllowMultiFace = false
  Closed = false
  Profile = -> Sketch379
  Refine = true
  Ruled = false
  Sections = -> [Sketch376,Sketch378]
FEATURE [Sketcher::SketchObject] Sketch365
  FullyConstrained = false
  MapMode = 5
  Placement = pos=(0,0,17) rot=(0,0,1;0rad)
  Support = -> [AdditiveLoft030]
  sketch-geometry (1):
    g0: Circle CenterX=0 CenterY=0 CenterZ=0 NormalX=0 NormalY=0 NormalZ=1 AngleXU=0 Radius=4.5
  constraints (2):
    c: Coincident(g0,g-1)
    c: Radius(g0) = 4.5
FEATURE [PartDesign::Pad] Pad068
  AllowMultiFace = false
  BaseFeature = -> AdditiveLoft030
  Direction = (1,1,1)
  Length = 0.7
  Length2 = 100
  Profile = -> Sketch365
  Refine = true
  Type = 0
FEATURE [Sketcher::SketchObject] Sketch372
  FullyConstrained = false
  MapMode = 5
  Placement = pos=(0,0,0) rot=(1,0,0;3.14159rad)
  Support = -> [Pad068]
  sketch-geometry (1):
    g0: Circle CenterX=0 CenterY=0 CenterZ=0 NormalX=0 NormalY=0 NormalZ=1 AngleXU=0 Radius=5
  constraints (2):
    c: Coincident(g0,g-1)
    c: Radius(g0) = 5
FEATURE [PartDesign::Pocket] Pocket062
  AllowMultiFace = false
  BaseFeature = -> Pad068
  Direction = (1,1,1)
  Length = 1
  Length2 = 100
  Profile = -> Sketch372
  Refine = true
  Type = 0
FEATURE [Sketcher::SketchObject] Sketch366
  FullyConstrained = false
  MapMode = 5
  Placement = pos=(0,0,1) rot=(1,0,0;3.14159rad)
  Support = -> [Pocket062]
  sketch-geometry (1):
    g0: Circle CenterX=0 CenterY=0 CenterZ=0 NormalX=0 NormalY=0 NormalZ=1 AngleXU=0 Radius=4.65
  constraints (2):
    c: Coincident(g0,g-1)
    c: Radius(g0) = 4.65
FEATURE [PartDesign::Pocket] Pocket057
  AllowMultiFace = false
  BaseFeature = -> Pocket062
  Direction = (1,1,1)
  Length = 1
  Length2 = 100
  Profile = -> Sketch366
  Refine = true
  Type = 0
FEATURE [Sketcher::SketchObject] Sketch367
  FullyConstrained = false
  MapMode = 5
  Placement = pos=(0,0,2) rot=(1,0,0;3.14159rad)
  Support = -> [Pocket057]
  sketch-geometry (2):
    g0: ArcOfCircle CenterX=0 CenterY=0 CenterZ=0 NormalX=0 NormalY=0 NormalZ=1 AngleXU=0 Radius=3 StartAngle=2.19024 EndAngle=7.23453
    g1: LineSegment StartX=-1.74176 StartY=2.4426 StartZ=0 EndX=1.74176 EndY=2.4426 EndZ=0
  constraints (5):
    c: Coincident(g0,g-1)
    c: Coincident(g1,g0)
    c: Coincident(g1,g0)
    c: Horizontal(g1)
    c: Radius(g0) = 3
FEATURE [PartDesign::Pocket] Pocket058
  AllowMultiFace = false
  BaseFeature = -> Pocket057
  Direction = (1,1,1)
  Length = 8
  Length2 = 100
  Profile = -> Sketch367
  Refine = true
  Type = 0
FEATURE [PartDesign::Chamfer] Chamfer050
  Angle = 45
  Base = -> Pocket058 [Edge82,Edge83]
  BaseFeature = -> Pocket058
  ChamferType = 0
  FlipDirection = false
  Size = 1.4
  Size2 = 1
  SupportTransform = false
  UseAllEdges = false
FEATURE [PartDesign::Chamfer] Chamfer052
  Angle = 45
  Base = -> Chamfer050 [Edge8]
  BaseFeature = -> Chamfer050
  ChamferType = 0
  FlipDirection = false
  Size = 0.3
  Size2 = 1
  SupportTransform = false
  UseAllEdges = false
FEATURE [PartDesign::Fillet] Fillet027
  Base = -> Chamfer052 [Edge93,Face36]
  BaseFeature = -> Chamfer052
  Radius = 0.1
  SupportTransform = false
  UseAllEdges = false
FEATURE [PartDesign::Body] Body150
  Group = -> [Sketch379,Sketch376,Sketch378,AdditiveLoft030,Sketch365,Pad068,Sketch372,Pocket062,Sketch366,Pocket057,Sketch367,Pocket058,Chamfer050,Chamfer052,Fillet027]
  Origin = -> Origin861
  Tip = -> Fillet027
FEATURE [App::Part] Part125  label="Cap026"
  Group = -> [Body150,Body152]
  Origin = -> Origin847
  Placement = pos=(40.005,40.005,0) rot=(0,0,1;0rad)
  expr: .Placement.Base.x = 40.005
  expr: .Placement.Base.y = 40.005
FEATURE [App::Part] Part131  label="PBF4_Caps"
  Group = -> [Part122,Part124,Part117,Part125]
  Origin = -> Origin884
  Placement = pos=(0,0,0.5) rot=(0,0,1;0rad)
FEATURE [Sketcher::SketchObject] Sketch383
  AttachmentOffset = pos=(0,0,7) rot=(0,0,1;0rad)
  FullyConstrained = false
  MapMode = 5
  Placement = pos=(0,0,7) rot=(0,0,1;0rad)
  Support = -> [XY_Plane885]
  sketch-geometry (25):
    g0: LineSegment StartX=-0.724089 StartY=5.5 StartZ=0 EndX=-2.12292 EndY=5.12518 EndZ=0
    g1: LineSegment StartX=-2.12292 StartY=5.12518 StartZ=0 EndX=-3.37708 EndY=4.4011 EndZ=0
    g2: LineSegment StartX=-3.37708 StartY=4.4011 StartZ=0 EndX=-4.4011 EndY=3.37708 EndZ=0
    g3: LineSegment StartX=-4.4011 StartY=3.37708 StartZ=0 EndX=-5.12518 EndY=2.12292 EndZ=0
    g4: LineSegment StartX=-5.12518 StartY=2.12292 StartZ=0 EndX=-5.5 EndY=0.724089 EndZ=0
    g5: LineSegment StartX=-5.5 StartY=0.724089 StartZ=0 EndX=-5.5 EndY=-0.724089 EndZ=0
    g6: LineSegment StartX=-5.5 StartY=-0.724089 StartZ=0 EndX=-5.12518 EndY=-2.12292 EndZ=0
    g7: LineSegment StartX=-5.12518 StartY=-2.12292 StartZ=0 EndX=-4.4011 EndY=-3.37708 EndZ=0
    g8: LineSegment StartX=-4.4011 StartY=-3.37708 StartZ=0 EndX=-3.37708 EndY=-4.4011 EndZ=0
    g9: LineSegment StartX=-3.37708 StartY=-4.4011 StartZ=0 EndX=-2.12292 EndY=-5.12518 EndZ=0
    g10: LineSegment StartX=-2.12292 StartY=-5.12518 StartZ=0 EndX=-0.724089 EndY=-5.5 EndZ=0
    g11: LineSegment StartX=-0.724089 StartY=-5.5 StartZ=0 EndX=0.724089 EndY=-5.5 EndZ=0
    g12: LineSegment StartX=0.724089 StartY=-5.5 StartZ=0 EndX=2.12292 EndY=-5.12518 EndZ=0
    g13: LineSegment StartX=2.12292 StartY=-5.12518 StartZ=0 EndX=3.37708 EndY=-4.4011 EndZ=0
    g14: LineSegment StartX=3.37708 StartY=-4.4011 StartZ=0 EndX=4.4011 EndY=-3.37708 EndZ=0
    g15: LineSegment StartX=4.4011 StartY=-3.37708 StartZ=0 EndX=5.12518 EndY=-2.12292 EndZ=0
    g16: LineSegment StartX=5.12518 StartY=-2.12292 StartZ=0 EndX=5.5 EndY=-0.724089 EndZ=0
    g17: LineSegment StartX=5.5 StartY=-0.724089 StartZ=0 EndX=5.5 EndY=0.724089 EndZ=0
    g18: LineSegment StartX=5.5 StartY=0.724089 StartZ=0 EndX=5.12518 EndY=2.12292 EndZ=0
    g19: LineSegment StartX=5.12518 StartY=2.12292 StartZ=0 EndX=4.4011 EndY=3.37708 EndZ=0
    g20: LineSegment StartX=4.4011 StartY=3.37708 StartZ=0 EndX=3.37708 EndY=4.4011 EndZ=0
    g21: LineSegment StartX=3.37708 StartY=4.4011 StartZ=0 EndX=2.12292 EndY=5.12518 EndZ=0
    g22: LineSegment StartX=2.12292 StartY=5.12518 StartZ=0 EndX=0.724089 EndY=5.5 EndZ=0
    g23: LineSegment StartX=0.724089 StartY=5.5 StartZ=0 EndX=-0.724089 EndY=5.5 EndZ=0
    g24: Circle CenterX=0 CenterY=0 CenterZ=0 NormalX=0 NormalY=0 NormalZ=1 AngleXU=0 Radius=5.54746
  constraints (52):
    c: Coincident(g0,g1)
    c: Coincident(g1,g2)
    c: Coincident(g2,g3)
    c: Coincident(g3,g4)
    c: Coincident(g4,g5)
    c: Coincident(g5,g6)
    c: Coincident(g6,g7)
    c: Coincident(g7,g8)
    c: Coincident(g8,g9)
    c: Coincident(g9,g10)
    c: Coincident(g10,g11)
    c: Coincident(g11,g12)
    c: Coincident(g12,g13)
    c: Coincident(g13,g14)
    c: Coincident(g14,g15)
    c: Coincident(g15,g16)
    c: Coincident(g16,g17)
    c: Coincident(g17,g18)
    c: Coincident(g18,g19)
    c: Coincident(g19,g20)
    c: Coincident(g20,g21)
    c: Coincident(g21,g22)
    c: Coincident(g22,g23)
    c: Coincident(g23,g0)
    c: Equal(g0, g1-g23) x23
    c: PointOnObject(g0,g24)
    c: PointOnObject(g1,g24)
    c: PointOnObject(g2,g24)
    c: PointOnObject(g3,g24)
    c: PointOnObject(g4,g24)
    c: PointOnObject(g5,g24)
    c: PointOnObject(g6,g24)
    c: PointOnObject(g7,g24)
    c: PointOnObject(g8,g24)
    c: PointOnObject(g9,g24)
    c: PointOnObject(g10,g24)
    c: PointOnObject(g11,g24)
    c: PointOnObject(g12,g24)
    c: PointOnObject(g13,g24)
    c: PointOnObject(g14,g24)
    c: PointOnObject(g15,g24)
    c: PointOnObject(g16,g24)
    c: PointOnObject(g17,g24)
    c: PointOnObject(g18,g24)
    c: PointOnObject(g19,g24)
    c: PointOnObject(g20,g24)
    c: PointOnObject(g21,g24)
    c: PointOnObject(g22,g24)
    c: PointOnObject(g23,g24)
    c: Coincident(g24,g-1)
    c: Horizontal(g23)
    c: DistanceX(g4,g17) = 11
FEATURE [Sketcher::SketchObject] Sketch384
  AttachmentOffset = pos=(0,0,17) rot=(0,0,1;0rad)
  FullyConstrained = false
  MapMode = 5
  Placement = pos=(0,0,17) rot=(0,0,1;0rad)
  Support = -> [XY_Plane885]
  sketch-geometry (25):
    g0: LineSegment StartX=-4.65926 StartY=1.92993 StartZ=0 EndX=-5 EndY=0.658262 EndZ=0
    g1: LineSegment StartX=-5 StartY=0.658262 StartZ=0 EndX=-5 EndY=-0.658262 EndZ=0
    g2: LineSegment StartX=-5 StartY=-0.658262 StartZ=0 EndX=-4.65926 EndY=-1.92993 EndZ=0
    g3: LineSegment StartX=-4.65926 StartY=-1.92993 StartZ=0 EndX=-4.001 EndY=-3.07007 EndZ=0
    g4: LineSegment StartX=-4.001 StartY=-3.07007 StartZ=0 EndX=-3.07007 EndY=-4.001 EndZ=0
    g5: LineSegment StartX=-3.07007 StartY=-4.001 StartZ=0 EndX=-1.92993 EndY=-4.65926 EndZ=0
    g6: LineSegment StartX=-1.92993 StartY=-4.65926 StartZ=0 EndX=-0.658262 EndY=-5 EndZ=0
    g7: LineSegment StartX=-0.658262 StartY=-5 StartZ=0 EndX=0.658262 EndY=-5 EndZ=0
    g8: LineSegment StartX=0.658262 StartY=-5 StartZ=0 EndX=1.92993 EndY=-4.65926 EndZ=0
    g9: LineSegment StartX=1.92993 StartY=-4.65926 StartZ=0 EndX=3.07007 EndY=-4.001 EndZ=0
    g10: LineSegment StartX=3.07007 StartY=-4.001 StartZ=0 EndX=4.001 EndY=-3.07007 EndZ=0
    g11: LineSegment StartX=4.001 StartY=-3.07007 StartZ=0 EndX=4.65926 EndY=-1.92993 EndZ=0
    g12: LineSegment StartX=4.65926 StartY=-1.92993 StartZ=0 EndX=5 EndY=-0.658262 EndZ=0
    g13: LineSegment StartX=5 StartY=-0.658262 StartZ=0 EndX=5 EndY=0.658262 EndZ=0
    g14: LineSegment StartX=5 StartY=0.658262 StartZ=0 EndX=4.65926 EndY=1.92993 EndZ=0
    g15: LineSegment StartX=4.65926 StartY=1.92993 StartZ=0 EndX=4.001 EndY=3.07007 EndZ=0
    g16: LineSegment StartX=4.001 StartY=3.07007 StartZ=0 EndX=3.07007 EndY=4.001 EndZ=0
    g17: LineSegment StartX=3.07007 StartY=4.001 StartZ=0 EndX=1.92993 EndY=4.65926 EndZ=0
    g18: LineSegment StartX=1.92993 StartY=4.65926 StartZ=0 EndX=0.658262 EndY=5 EndZ=0
    g19: LineSegment StartX=0.658262 StartY=5 StartZ=0 EndX=-0.658262 EndY=5 EndZ=0
    g20: LineSegment StartX=-0.658262 StartY=5 StartZ=0 EndX=-1.92993 EndY=4.65926 EndZ=0
    g21: LineSegment StartX=-1.92993 StartY=4.65926 StartZ=0 EndX=-3.07007 EndY=4.001 EndZ=0
    g22: LineSegment StartX=-3.07007 StartY=4.001 StartZ=0 EndX=-4.001 EndY=3.07007 EndZ=0
    g23: LineSegment StartX=-4.001 StartY=3.07007 StartZ=0 EndX=-4.65926 EndY=1.92993 EndZ=0
    g24: Circle CenterX=0 CenterY=0 CenterZ=0 NormalX=0 NormalY=0 NormalZ=1 AngleXU=0 Radius=5.04314
  constraints (52):
    c: Coincident(g0,g1)
    c: Coincident(g1,g2)
    c: Coincident(g2,g3)
    c: Coincident(g3,g4)
    c: Coincident(g4,g5)
    c: Coincident(g5,g6)
    c: Coincident(g6,g7)
    c: Coincident(g7,g8)
    c: Coincident(g8,g9)
    c: Coincident(g9,g10)
    c: Coincident(g10,g11)
    c: Coincident(g11,g12)
    c: Coincident(g12,g13)
    c: Coincident(g13,g14)
    c: Coincident(g14,g15)
    c: Coincident(g15,g16)
    c: Coincident(g16,g17)
    c: Coincident(g17,g18)
    c: Coincident(g18,g19)
    c: Coincident(g19,g20)
    c: Coincident(g20,g21)
    c: Coincident(g21,g22)
    c: Coincident(g22,g23)
    c: Coincident(g23,g0)
    c: Equal(g0, g1-g23) x23
    c: PointOnObject(g0,g24)
    c: PointOnObject(g1,g24)
    c: PointOnObject(g2,g24)
    c: PointOnObject(g3,g24)
    c: PointOnObject(g4,g24)
    c: PointOnObject(g5,g24)
    c: PointOnObject(g6,g24)
    c: PointOnObject(g7,g24)
    c: PointOnObject(g8,g24)
    c: PointOnObject(g9,g24)
    c: PointOnObject(g10,g24)
    c: PointOnObject(g11,g24)
    c: PointOnObject(g12,g24)
    c: PointOnObject(g13,g24)
    c: PointOnObject(g14,g24)
    c: PointOnObject(g15,g24)
    c: PointOnObject(g16,g24)
    c: PointOnObject(g17,g24)
    c: PointOnObject(g18,g24)
    c: PointOnObject(g19,g24)
    c: PointOnObject(g20,g24)
    c: PointOnObject(g21,g24)
    c: PointOnObject(g22,g24)
    c: PointOnObject(g23,g24)
    c: Coincident(g24,g-1)
    c: Horizontal(g19)
    c: DistanceX(g0,g13) = 10
FEATURE [Sketcher::SketchObject] Sketch386
  AttachmentOffset = pos=(0,0,7) rot=(0,0,1;0rad)
  FullyConstrained = false
  MapMode = 5
  Placement = pos=(0,0,7) rot=(0,0,1;0rad)
  Support = -> [XY_Plane882]
  sketch-geometry (25):
    g0: LineSegment StartX=-0.724089 StartY=5.5 StartZ=0 EndX=-2.12292 EndY=5.12518 EndZ=0
    g1: LineSegment StartX=-2.12292 StartY=5.12518 StartZ=0 EndX=-3.37708 EndY=4.4011 EndZ=0
    g2: LineSegment StartX=-3.37708 StartY=4.4011 StartZ=0 EndX=-4.4011 EndY=3.37708 EndZ=0
    g3: LineSegment StartX=-4.4011 StartY=3.37708 StartZ=0 EndX=-5.12518 EndY=2.12292 EndZ=0
    g4: LineSegment StartX=-5.12518 StartY=2.12292 StartZ=0 EndX=-5.5 EndY=0.724089 EndZ=0
    g5: LineSegment StartX=-5.5 StartY=0.724089 StartZ=0 EndX=-5.5 EndY=-0.724089 EndZ=0
    g6: LineSegment StartX=-5.5 StartY=-0.724089 StartZ=0 EndX=-5.12518 EndY=-2.12292 EndZ=0
    g7: LineSegment StartX=-5.12518 StartY=-2.12292 StartZ=0 EndX=-4.4011 EndY=-3.37708 EndZ=0
    g8: LineSegment StartX=-4.4011 StartY=-3.37708 StartZ=0 EndX=-3.37708 EndY=-4.4011 EndZ=0
    g9: LineSegment StartX=-3.37708 StartY=-4.4011 StartZ=0 EndX=-2.12292 EndY=-5.12518 EndZ=0
    g10: LineSegment StartX=-2.12292 StartY=-5.12518 StartZ=0 EndX=-0.724089 EndY=-5.5 EndZ=0
    g11: LineSegment StartX=-0.724089 StartY=-5.5 StartZ=0 EndX=0.724089 EndY=-5.5 EndZ=0
    g12: LineSegment StartX=0.724089 StartY=-5.5 StartZ=0 EndX=2.12292 EndY=-5.12518 EndZ=0
    g13: LineSegment StartX=2.12292 StartY=-5.12518 StartZ=0 EndX=3.37708 EndY=-4.4011 EndZ=0
    g14: LineSegment StartX=3.37708 StartY=-4.4011 StartZ=0 EndX=4.4011 EndY=-3.37708 EndZ=0
    g15: LineSegment StartX=4.4011 StartY=-3.37708 StartZ=0 EndX=5.12518 EndY=-2.12292 EndZ=0
    g16: LineSegment StartX=5.12518 StartY=-2.12292 StartZ=0 EndX=5.5 EndY=-0.724089 EndZ=0
    g17: LineSegment StartX=5.5 StartY=-0.724089 StartZ=0 EndX=5.5 EndY=0.724089 EndZ=0
    g18: LineSegment StartX=5.5 StartY=0.724089 StartZ=0 EndX=5.12518 EndY=2.12292 EndZ=0
    g19: LineSegment StartX=5.12518 StartY=2.12292 StartZ=0 EndX=4.4011 EndY=3.37708 EndZ=0
    g20: LineSegment StartX=4.4011 StartY=3.37708 StartZ=0 EndX=3.37708 EndY=4.4011 EndZ=0
    g21: LineSegment StartX=3.37708 StartY=4.4011 StartZ=0 EndX=2.12292 EndY=5.12518 EndZ=0
    g22: LineSegment StartX=2.12292 StartY=5.12518 StartZ=0 EndX=0.724089 EndY=5.5 EndZ=0
    g23: LineSegment StartX=0.724089 StartY=5.5 StartZ=0 EndX=-0.724089 EndY=5.5 EndZ=0
    g24: Circle CenterX=0 CenterY=0 CenterZ=0 NormalX=0 NormalY=0 NormalZ=1 AngleXU=0 Radius=5.54746
  constraints (52):
    c: Coincident(g0,g1)
    c: Coincident(g1,g2)
    c: Coincident(g2,g3)
    c: Coincident(g3,g4)
    c: Coincident(g4,g5)
    c: Coincident(g5,g6)
    c: Coincident(g6,g7)
    c: Coincident(g7,g8)
    c: Coincident(g8,g9)
    c: Coincident(g9,g10)
    c: Coincident(g10,g11)
    c: Coincident(g11,g12)
    c: Coincident(g12,g13)
    c: Coincident(g13,g14)
    c: Coincident(g14,g15)
    c: Coincident(g15,g16)
    c: Coincident(g16,g17)
    c: Coincident(g17,g18)
    c: Coincident(g18,g19)
    c: Coincident(g19,g20)
    c: Coincident(g20,g21)
    c: Coincident(g21,g22)
    c: Coincident(g22,g23)
    c: Coincident(g23,g0)
    c: Equal(g0, g1-g23) x23
    c: PointOnObject(g0,g24)
    c: PointOnObject(g1,g24)
    c: PointOnObject(g2,g24)
    c: PointOnObject(g3,g24)
    c: PointOnObject(g4,g24)
    c: PointOnObject(g5,g24)
    c: PointOnObject(g6,g24)
    c: PointOnObject(g7,g24)
    c: PointOnObject(g8,g24)
    c: PointOnObject(g9,g24)
    c: PointOnObject(g10,g24)
    c: PointOnObject(g11,g24)
    c: PointOnObject(g12,g24)
    c: PointOnObject(g13,g24)
    c: PointOnObject(g14,g24)
    c: PointOnObject(g15,g24)
    c: PointOnObject(g16,g24)
    c: PointOnObject(g17,g24)
    c: PointOnObject(g18,g24)
    c: PointOnObject(g19,g24)
    c: PointOnObject(g20,g24)
    c: PointOnObject(g21,g24)
    c: PointOnObject(g22,g24)
    c: PointOnObject(g23,g24)
    c: Coincident(g24,g-1)
    c: Horizontal(g23)
    c: DistanceX(g4,g17) = 11
FEATURE [Sketcher::SketchObject] Sketch387
  FullyConstrained = false
  MapMode = 5
  Support = -> [XY_Plane882]
  sketch-geometry (25):
    g0: LineSegment StartX=-0.789915 StartY=6 StartZ=0 EndX=-2.31591 EndY=5.59111 EndZ=0
    g1: LineSegment StartX=-2.31591 StartY=5.59111 StartZ=0 EndX=-3.68409 EndY=4.80119 EndZ=0
    g2: LineSegment StartX=-3.68409 StartY=4.80119 StartZ=0 EndX=-4.80119 EndY=3.68409 EndZ=0
    g3: LineSegment StartX=-4.80119 StartY=3.68409 StartZ=0 EndX=-5.59111 EndY=2.31591 EndZ=0
    g4: LineSegment StartX=-5.59111 StartY=2.31591 StartZ=0 EndX=-6 EndY=0.789915 EndZ=0
    g5: LineSegment StartX=-6 StartY=0.789915 StartZ=0 EndX=-6 EndY=-0.789915 EndZ=0
    g6: LineSegment StartX=-6 StartY=-0.789915 StartZ=0 EndX=-5.59111 EndY=-2.31591 EndZ=0
    g7: LineSegment StartX=-5.59111 StartY=-2.31591 StartZ=0 EndX=-4.80119 EndY=-3.68409 EndZ=0
    g8: LineSegment StartX=-4.80119 StartY=-3.68409 StartZ=0 EndX=-3.68409 EndY=-4.80119 EndZ=0
    g9: LineSegment StartX=-3.68409 StartY=-4.80119 StartZ=0 EndX=-2.31591 EndY=-5.59111 EndZ=0
    g10: LineSegment StartX=-2.31591 StartY=-5.59111 StartZ=0 EndX=-0.789915 EndY=-6 EndZ=0
    g11: LineSegment StartX=-0.789915 StartY=-6 StartZ=0 EndX=0.789915 EndY=-6 EndZ=0
    g12: LineSegment StartX=0.789915 StartY=-6 StartZ=0 EndX=2.31591 EndY=-5.59111 EndZ=0
    g13: LineSegment StartX=2.31591 StartY=-5.59111 StartZ=0 EndX=3.68409 EndY=-4.80119 EndZ=0
    g14: LineSegment StartX=3.68409 StartY=-4.80119 StartZ=0 EndX=4.80119 EndY=-3.68409 EndZ=0
    g15: LineSegment StartX=4.80119 StartY=-3.68409 StartZ=0 EndX=5.59111 EndY=-2.31591 EndZ=0
    g16: LineSegment StartX=5.59111 StartY=-2.31591 StartZ=0 EndX=6 EndY=-0.789915 EndZ=0
    g17: LineSegment StartX=6 StartY=-0.789915 StartZ=0 EndX=6 EndY=0.789915 EndZ=0
    g18: LineSegment StartX=6 StartY=0.789915 StartZ=0 EndX=5.59111 EndY=2.31591 EndZ=0
    g19: LineSegment StartX=5.59111 StartY=2.31591 StartZ=0 EndX=4.80119 EndY=3.68409 EndZ=0
    g20: LineSegment StartX=4.80119 StartY=3.68409 StartZ=0 EndX=3.68409 EndY=4.80119 EndZ=0
    g21: LineSegment StartX=3.68409 StartY=4.80119 StartZ=0 EndX=2.31591 EndY=5.59111 EndZ=0
    g22: LineSegment StartX=2.31591 StartY=5.59111 StartZ=0 EndX=0.789915 EndY=6 EndZ=0
    g23: LineSegment StartX=0.789915 StartY=6 StartZ=0 EndX=-0.789915 EndY=6 EndZ=0
    g24: Circle CenterX=0 CenterY=0 CenterZ=0 NormalX=0 NormalY=0 NormalZ=1 AngleXU=0 Radius=6.05177
  constraints (52):
    c: Coincident(g0,g1)
    c: Coincident(g1,g2)
    c: Coincident(g2,g3)
    c: Coincident(g3,g4)
    c: Coincident(g4,g5)
    c: Coincident(g5,g6)
    c: Coincident(g6,g7)
    c: Coincident(g7,g8)
    c: Coincident(g8,g9)
    c: Coincident(g9,g10)
    c: Coincident(g10,g11)
    c: Coincident(g11,g12)
    c: Coincident(g12,g13)
    c: Coincident(g13,g14)
    c: Coincident(g14,g15)
    c: Coincident(g15,g16)
    c: Coincident(g16,g17)
    c: Coincident(g17,g18)
    c: Coincident(g18,g19)
    c: Coincident(g19,g20)
    c: Coincident(g20,g21)
    c: Coincident(g21,g22)
    c: Coincident(g22,g23)
    c: Coincident(g23,g0)
    c: Equal(g0, g1-g23) x23
    c: PointOnObject(g0,g24)
    c: PointOnObject(g1,g24)
    c: PointOnObject(g2,g24)
    c: PointOnObject(g3,g24)
    c: PointOnObject(g4,g24)
    c: PointOnObject(g5,g24)
    c: PointOnObject(g6,g24)
    c: PointOnObject(g7,g24)
    c: PointOnObject(g8,g24)
    c: PointOnObject(g9,g24)
    c: PointOnObject(g10,g24)
    c: PointOnObject(g11,g24)
    c: PointOnObject(g12,g24)
    c: PointOnObject(g13,g24)
    c: PointOnObject(g14,g24)
    c: PointOnObject(g15,g24)
    c: PointOnObject(g16,g24)
    c: PointOnObject(g17,g24)
    c: PointOnObject(g18,g24)
    c: PointOnObject(g19,g24)
    c: PointOnObject(g20,g24)
    c: PointOnObject(g21,g24)
    c: PointOnObject(g22,g24)
    c: PointOnObject(g23,g24)
    c: Coincident(g24,g-1)
    c: Horizontal(g23)
    c: DistanceX(g4,g17) = 12
FEATURE [Sketcher::SketchObject] Sketch388
  AttachmentOffset = pos=(0,0,17) rot=(0,0,1;0rad)
  FullyConstrained = false
  MapMode = 5
  Placement = pos=(0,0,17) rot=(0,0,1;0rad)
  Support = -> [XY_Plane882]
  sketch-geometry (25):
    g0: LineSegment StartX=-4.65926 StartY=1.92993 StartZ=0 EndX=-5 EndY=0.658262 EndZ=0
    g1: LineSegment StartX=-5 StartY=0.658262 StartZ=0 EndX=-5 EndY=-0.658262 EndZ=0
    g2: LineSegment StartX=-5 StartY=-0.658262 StartZ=0 EndX=-4.65926 EndY=-1.92993 EndZ=0
    g3: LineSegment StartX=-4.65926 StartY=-1.92993 StartZ=0 EndX=-4.001 EndY=-3.07007 EndZ=0
    g4: LineSegment StartX=-4.001 StartY=-3.07007 StartZ=0 EndX=-3.07007 EndY=-4.001 EndZ=0
    g5: LineSegment StartX=-3.07007 StartY=-4.001 StartZ=0 EndX=-1.92993 EndY=-4.65926 EndZ=0
    g6: LineSegment StartX=-1.92993 StartY=-4.65926 StartZ=0 EndX=-0.658262 EndY=-5 EndZ=0
    g7: LineSegment StartX=-0.658262 StartY=-5 StartZ=0 EndX=0.658262 EndY=-5 EndZ=0
    g8: LineSegment StartX=0.658262 StartY=-5 StartZ=0 EndX=1.92993 EndY=-4.65926 EndZ=0
    g9: LineSegment StartX=1.92993 StartY=-4.65926 StartZ=0 EndX=3.07007 EndY=-4.001 EndZ=0
    g10: LineSegment StartX=3.07007 StartY=-4.001 StartZ=0 EndX=4.001 EndY=-3.07007 EndZ=0
    g11: LineSegment StartX=4.001 StartY=-3.07007 StartZ=0 EndX=4.65926 EndY=-1.92993 EndZ=0
    g12: LineSegment StartX=4.65926 StartY=-1.92993 StartZ=0 EndX=5 EndY=-0.658262 EndZ=0
    g13: LineSegment StartX=5 StartY=-0.658262 StartZ=0 EndX=5 EndY=0.658262 EndZ=0
    g14: LineSegment StartX=5 StartY=0.658262 StartZ=0 EndX=4.65926 EndY=1.92993 EndZ=0
    g15: LineSegment StartX=4.65926 StartY=1.92993 StartZ=0 EndX=4.001 EndY=3.07007 EndZ=0
    g16: LineSegment StartX=4.001 StartY=3.07007 StartZ=0 EndX=3.07007 EndY=4.001 EndZ=0
    g17: LineSegment StartX=3.07007 StartY=4.001 StartZ=0 EndX=1.92993 EndY=4.65926 EndZ=0
    g18: LineSegment StartX=1.92993 StartY=4.65926 StartZ=0 EndX=0.658262 EndY=5 EndZ=0
    g19: LineSegment StartX=0.658262 StartY=5 StartZ=0 EndX=-0.658262 EndY=5 EndZ=0
    g20: LineSegment StartX=-0.658262 StartY=5 StartZ=0 EndX=-1.92993 EndY=4.65926 EndZ=0
    g21: LineSegment StartX=-1.92993 StartY=4.65926 StartZ=0 EndX=-3.07007 EndY=4.001 EndZ=0
    g22: LineSegment StartX=-3.07007 StartY=4.001 StartZ=0 EndX=-4.001 EndY=3.07007 EndZ=0
    g23: LineSegment StartX=-4.001 StartY=3.07007 StartZ=0 EndX=-4.65926 EndY=1.92993 EndZ=0
    g24: Circle CenterX=0 CenterY=0 CenterZ=0 NormalX=0 NormalY=0 NormalZ=1 AngleXU=0 Radius=5.04314
  constraints (52):
    c: Coincident(g0,g1)
    c: Coincident(g1,g2)
    c: Coincident(g2,g3)
    c: Coincident(g3,g4)
    c: Coincident(g4,g5)
    c: Coincident(g5,g6)
    c: Coincident(g6,g7)
    c: Coincident(g7,g8)
    c: Coincident(g8,g9)
    c: Coincident(g9,g10)
    c: Coincident(g10,g11)
    c: Coincident(g11,g12)
    c: Coincident(g12,g13)
    c: Coincident(g13,g14)
    c: Coincident(g14,g15)
    c: Coincident(g15,g16)
    c: Coincident(g16,g17)
    c: Coincident(g17,g18)
    c: Coincident(g18,g19)
    c: Coincident(g19,g20)
    c: Coincident(g20,g21)
    c: Coincident(g21,g22)
    c: Coincident(g22,g23)
    c: Coincident(g23,g0)
    c: Equal(g0, g1-g23) x23
    c: PointOnObject(g0,g24)
    c: PointOnObject(g1,g24)
    c: PointOnObject(g2,g24)
    c: PointOnObject(g3,g24)
    c: PointOnObject(g4,g24)
    c: PointOnObject(g5,g24)
    c: PointOnObject(g6,g24)
    c: PointOnObject(g7,g24)
    c: PointOnObject(g8,g24)
    c: PointOnObject(g9,g24)
    c: PointOnObject(g10,g24)
    c: PointOnObject(g11,g24)
    c: PointOnObject(g12,g24)
    c: PointOnObject(g13,g24)
    c: PointOnObject(g14,g24)
    c: PointOnObject(g15,g24)
    c: PointOnObject(g16,g24)
    c: PointOnObject(g17,g24)
    c: PointOnObject(g18,g24)
    c: PointOnObject(g19,g24)
    c: PointOnObject(g20,g24)
    c: PointOnObject(g21,g24)
    c: PointOnObject(g22,g24)
    c: PointOnObject(g23,g24)
    c: Coincident(g24,g-1)
    c: Horizontal(g19)
    c: DistanceX(g0,g13) = 10
FEATURE [PartDesign::AdditiveLoft] AdditiveLoft031
  AllowMultiFace = false
  Closed = false
  Profile = -> Sketch387
  Refine = true
  Ruled = false
  Sections = -> [Sketch386,Sketch388]
FEATURE [Sketcher::SketchObject] Sketch389
  FullyConstrained = false
  MapMode = 5
  Placement = pos=(0,0,17) rot=(0,0,1;0rad)
  Support = -> [AdditiveLoft031]
  sketch-geometry (1):
    g0: Circle CenterX=0 CenterY=0 CenterZ=0 NormalX=0 NormalY=0 NormalZ=1 AngleXU=0 Radius=4.5
  constraints (2):
    c: Coincident(g0,g-1)
    c: Radius(g0) = 4.5
FEATURE [PartDesign::Pad] Pad069
  AllowMultiFace = false
  BaseFeature = -> AdditiveLoft031
  Direction = (1,1,1)
  Length = 0.7
  Length2 = 100
  Profile = -> Sketch389
  Refine = true
  Type = 0
FEATURE [Sketcher::SketchObject] Sketch390
  FullyConstrained = false
  MapMode = 5
  Placement = pos=(0,0,0) rot=(1,0,0;3.14159rad)
  Support = -> [Pad069]
  sketch-geometry (1):
    g0: Circle CenterX=0 CenterY=0 CenterZ=0 NormalX=0 NormalY=0 NormalZ=1 AngleXU=0 Radius=5
  constraints (2):
    c: Coincident(g0,g-1)
    c: Radius(g0) = 5
FEATURE [PartDesign::Pocket] Pocket064
  AllowMultiFace = false
  BaseFeature = -> Pad069
  Direction = (1,1,1)
  Length = 1
  Length2 = 100
  Profile = -> Sketch390
  Refine = true
  Type = 0
FEATURE [Sketcher::SketchObject] Sketch380
  FullyConstrained = false
  MapMode = 5
  Placement = pos=(0,0,1) rot=(1,0,0;3.14159rad)
  Support = -> [Pocket064]
  sketch-geometry (1):
    g0: Circle CenterX=0 CenterY=0 CenterZ=0 NormalX=0 NormalY=0 NormalZ=1 AngleXU=0 Radius=4.65
  constraints (2):
    c: Coincident(g0,g-1)
    c: Radius(g0) = 4.65
FEATURE [PartDesign::Pocket] Pocket065
  AllowMultiFace = false
  BaseFeature = -> Pocket064
  Direction = (1,1,1)
  Length = 1
  Length2 = 100
  Profile = -> Sketch380
  Refine = true
  Type = 0
FEATURE [Sketcher::SketchObject] Sketch391
  FullyConstrained = false
  MapMode = 5
  Placement = pos=(0,0,2) rot=(1,0,0;3.14159rad)
  Support = -> [Pocket065]
  sketch-geometry (2):
    g0: ArcOfCircle CenterX=0 CenterY=0 CenterZ=0 NormalX=0 NormalY=0 NormalZ=1 AngleXU=0 Radius=3 StartAngle=2.19024 EndAngle=7.23453
    g1: LineSegment StartX=-1.74176 StartY=2.4426 StartZ=0 EndX=1.74176 EndY=2.4426 EndZ=0
  constraints (5):
    c: Coincident(g0,g-1)
    c: Coincident(g1,g0)
    c: Coincident(g1,g0)
    c: Horizontal(g1)
    c: Radius(g0) = 3
FEATURE [PartDesign::Pocket] Pocket066
  AllowMultiFace = false
  BaseFeature = -> Pocket065
  Direction = (1,1,1)
  Length = 8
  Length2 = 100
  Profile = -> Sketch391
  Refine = true
  Type = 0
FEATURE [PartDesign::Chamfer] Chamfer053
  Angle = 45
  Base = -> Pocket066 [Edge82,Edge83]
  BaseFeature = -> Pocket066
  ChamferType = 0
  FlipDirection = false
  Size = 1.4
  Size2 = 1
  SupportTransform = false
  UseAllEdges = false
FEATURE [PartDesign::Chamfer] Chamfer054
  Angle = 45
  Base = -> Chamfer053 [Edge8]
  BaseFeature = -> Chamfer053
  ChamferType = 0
  FlipDirection = false
  Size = 0.3
  Size2 = 1
  SupportTransform = false
  UseAllEdges = false
FEATURE [PartDesign::Fillet] Fillet029
  Base = -> Chamfer054 [Edge93,Face36]
  BaseFeature = -> Chamfer054
  Radius = 0.1
  SupportTransform = false
  UseAllEdges = false
FEATURE [Sketcher::SketchObject] Sketch394
  FullyConstrained = false
  MapMode = 5
  Support = -> [XY_Plane885]
  sketch-geometry (25):
    g0: LineSegment StartX=-0.789915 StartY=6 StartZ=0 EndX=-2.31591 EndY=5.59111 EndZ=0
    g1: LineSegment StartX=-2.31591 StartY=5.59111 StartZ=0 EndX=-3.68409 EndY=4.80119 EndZ=0
    g2: LineSegment StartX=-3.68409 StartY=4.80119 StartZ=0 EndX=-4.80119 EndY=3.68409 EndZ=0
    g3: LineSegment StartX=-4.80119 StartY=3.68409 StartZ=0 EndX=-5.59111 EndY=2.31591 EndZ=0
    g4: LineSegment StartX=-5.59111 StartY=2.31591 StartZ=0 EndX=-6 EndY=0.789915 EndZ=0
    g5: LineSegment StartX=-6 StartY=0.789915 StartZ=0 EndX=-6 EndY=-0.789915 EndZ=0
    g6: LineSegment StartX=-6 StartY=-0.789915 StartZ=0 EndX=-5.59111 EndY=-2.31591 EndZ=0
    g7: LineSegment StartX=-5.59111 StartY=-2.31591 StartZ=0 EndX=-4.80119 EndY=-3.68409 EndZ=0
    g8: LineSegment StartX=-4.80119 StartY=-3.68409 StartZ=0 EndX=-3.68409 EndY=-4.80119 EndZ=0
    g9: LineSegment StartX=-3.68409 StartY=-4.80119 StartZ=0 EndX=-2.31591 EndY=-5.59111 EndZ=0
    g10: LineSegment StartX=-2.31591 StartY=-5.59111 StartZ=0 EndX=-0.789915 EndY=-6 EndZ=0
    g11: LineSegment StartX=-0.789915 StartY=-6 StartZ=0 EndX=0.789915 EndY=-6 EndZ=0
    g12: LineSegment StartX=0.789915 StartY=-6 StartZ=0 EndX=2.31591 EndY=-5.59111 EndZ=0
    g13: LineSegment StartX=2.31591 StartY=-5.59111 StartZ=0 EndX=3.68409 EndY=-4.80119 EndZ=0
    g14: LineSegment StartX=3.68409 StartY=-4.80119 StartZ=0 EndX=4.80119 EndY=-3.68409 EndZ=0
    g15: LineSegment StartX=4.80119 StartY=-3.68409 StartZ=0 EndX=5.59111 EndY=-2.31591 EndZ=0
    g16: LineSegment StartX=5.59111 StartY=-2.31591 StartZ=0 EndX=6 EndY=-0.789915 EndZ=0
    g17: LineSegment StartX=6 StartY=-0.789915 StartZ=0 EndX=6 EndY=0.789915 EndZ=0
    g18: LineSegment StartX=6 StartY=0.789915 StartZ=0 EndX=5.59111 EndY=2.31591 EndZ=0
    g19: LineSegment StartX=5.59111 StartY=2.31591 StartZ=0 EndX=4.80119 EndY=3.68409 EndZ=0
    g20: LineSegment StartX=4.80119 StartY=3.68409 StartZ=0 EndX=3.68409 EndY=4.80119 EndZ=0
    g21: LineSegment StartX=3.68409 StartY=4.80119 StartZ=0 EndX=2.31591 EndY=5.59111 EndZ=0
    g22: LineSegment StartX=2.31591 StartY=5.59111 StartZ=0 EndX=0.789915 EndY=6 EndZ=0
    g23: LineSegment StartX=0.789915 StartY=6 StartZ=0 EndX=-0.789915 EndY=6 EndZ=0
    g24: Circle CenterX=0 CenterY=0 CenterZ=0 NormalX=0 NormalY=0 NormalZ=1 AngleXU=0 Radius=6.05177
  constraints (52):
    c: Coincident(g0,g1)
    c: Coincident(g1,g2)
    c: Coincident(g2,g3)
    c: Coincident(g3,g4)
    c: Coincident(g4,g5)
    c: Coincident(g5,g6)
    c: Coincident(g6,g7)
    c: Coincident(g7,g8)
    c: Coincident(g8,g9)
    c: Coincident(g9,g10)
    c: Coincident(g10,g11)
    c: Coincident(g11,g12)
    c: Coincident(g12,g13)
    c: Coincident(g13,g14)
    c: Coincident(g14,g15)
    c: Coincident(g15,g16)
    c: Coincident(g16,g17)
    c: Coincident(g17,g18)
    c: Coincident(g18,g19)
    c: Coincident(g19,g20)
    c: Coincident(g20,g21)
    c: Coincident(g21,g22)
    c: Coincident(g22,g23)
    c: Coincident(g23,g0)
    c: Equal(g0, g1-g23) x23
    c: PointOnObject(g0,g24)
    c: PointOnObject(g1,g24)
    c: PointOnObject(g2,g24)
    c: PointOnObject(g3,g24)
    c: PointOnObject(g4,g24)
    c: PointOnObject(g5,g24)
    c: PointOnObject(g6,g24)
    c: PointOnObject(g7,g24)
    c: PointOnObject(g8,g24)
    c: PointOnObject(g9,g24)
    c: PointOnObject(g10,g24)
    c: PointOnObject(g11,g24)
    c: PointOnObject(g12,g24)
    c: PointOnObject(g13,g24)
    c: PointOnObject(g14,g24)
    c: PointOnObject(g15,g24)
    c: PointOnObject(g16,g24)
    c: PointOnObject(g17,g24)
    c: PointOnObject(g18,g24)
    c: PointOnObject(g19,g24)
    c: PointOnObject(g20,g24)
    c: PointOnObject(g21,g24)
    c: PointOnObject(g22,g24)
    c: PointOnObject(g23,g24)
    c: Coincident(g24,g-1)
    c: Horizontal(g23)
    c: DistanceX(g4,g17) = 12
FEATURE [Sketcher::SketchObject] Sketch395
  AttachmentOffset = pos=(0,0,7) rot=(0,0,1;0rad)
  FullyConstrained = false
  MapMode = 5
  Placement = pos=(0,0,7) rot=(0,0,1;0rad)
  Support = -> [XY_Plane890]
  sketch-geometry (25):
    g0: LineSegment StartX=-0.724089 StartY=5.5 StartZ=0 EndX=-2.12292 EndY=5.12518 EndZ=0
    g1: LineSegment StartX=-2.12292 StartY=5.12518 StartZ=0 EndX=-3.37708 EndY=4.4011 EndZ=0
    g2: LineSegment StartX=-3.37708 StartY=4.4011 StartZ=0 EndX=-4.4011 EndY=3.37708 EndZ=0
    g3: LineSegment StartX=-4.4011 StartY=3.37708 StartZ=0 EndX=-5.12518 EndY=2.12292 EndZ=0
    g4: LineSegment StartX=-5.12518 StartY=2.12292 StartZ=0 EndX=-5.5 EndY=0.724089 EndZ=0
    g5: LineSegment StartX=-5.5 StartY=0.724089 StartZ=0 EndX=-5.5 EndY=-0.724089 EndZ=0
    g6: LineSegment StartX=-5.5 StartY=-0.724089 StartZ=0 EndX=-5.12518 EndY=-2.12292 EndZ=0
    g7: LineSegment StartX=-5.12518 StartY=-2.12292 StartZ=0 EndX=-4.4011 EndY=-3.37708 EndZ=0
    g8: LineSegment StartX=-4.4011 StartY=-3.37708 StartZ=0 EndX=-3.37708 EndY=-4.4011 EndZ=0
    g9: LineSegment StartX=-3.37708 StartY=-4.4011 StartZ=0 EndX=-2.12292 EndY=-5.12518 EndZ=0
    g10: LineSegment StartX=-2.12292 StartY=-5.12518 StartZ=0 EndX=-0.724089 EndY=-5.5 EndZ=0
    g11: LineSegment StartX=-0.724089 StartY=-5.5 StartZ=0 EndX=0.724089 EndY=-5.5 EndZ=0
    g12: LineSegment StartX=0.724089 StartY=-5.5 StartZ=0 EndX=2.12292 EndY=-5.12518 EndZ=0
    g13: LineSegment StartX=2.12292 StartY=-5.12518 StartZ=0 EndX=3.37708 EndY=-4.4011 EndZ=0
    g14: LineSegment StartX=3.37708 StartY=-4.4011 StartZ=0 EndX=4.4011 EndY=-3.37708 EndZ=0
    g15: LineSegment StartX=4.4011 StartY=-3.37708 StartZ=0 EndX=5.12518 EndY=-2.12292 EndZ=0
    g16: LineSegment StartX=5.12518 StartY=-2.12292 StartZ=0 EndX=5.5 EndY=-0.724089 EndZ=0
    g17: LineSegment StartX=5.5 StartY=-0.724089 StartZ=0 EndX=5.5 EndY=0.724089 EndZ=0
    g18: LineSegment StartX=5.5 StartY=0.724089 StartZ=0 EndX=5.12518 EndY=2.12292 EndZ=0
    g19: LineSegment StartX=5.12518 StartY=2.12292 StartZ=0 EndX=4.4011 EndY=3.37708 EndZ=0
    g20: LineSegment StartX=4.4011 StartY=3.37708 StartZ=0 EndX=3.37708 EndY=4.4011 EndZ=0
    g21: LineSegment StartX=3.37708 StartY=4.4011 StartZ=0 EndX=2.12292 EndY=5.12518 EndZ=0
    g22: LineSegment StartX=2.12292 StartY=5.12518 StartZ=0 EndX=0.724089 EndY=5.5 EndZ=0
    g23: LineSegment StartX=0.724089 StartY=5.5 StartZ=0 EndX=-0.724089 EndY=5.5 EndZ=0
    g24: Circle CenterX=0 CenterY=0 CenterZ=0 NormalX=0 NormalY=0 NormalZ=1 AngleXU=0 Radius=5.54746
  constraints (52):
    c: Coincident(g0,g1)
    c: Coincident(g1,g2)
    c: Coincident(g2,g3)
    c: Coincident(g3,g4)
    c: Coincident(g4,g5)
    c: Coincident(g5,g6)
    c: Coincident(g6,g7)
    c: Coincident(g7,g8)
    c: Coincident(g8,g9)
    c: Coincident(g9,g10)
    c: Coincident(g10,g11)
    c: Coincident(g11,g12)
    c: Coincident(g12,g13)
    c: Coincident(g13,g14)
    c: Coincident(g14,g15)
    c: Coincident(g15,g16)
    c: Coincident(g16,g17)
    c: Coincident(g17,g18)
    c: Coincident(g18,g19)
    c: Coincident(g19,g20)
    c: Coincident(g20,g21)
    c: Coincident(g21,g22)
    c: Coincident(g22,g23)
    c: Coincident(g23,g0)
    c: Equal(g0, g1-g23) x23
    c: PointOnObject(g0,g24)
    c: PointOnObject(g1,g24)
    c: PointOnObject(g2,g24)
    c: PointOnObject(g3,g24)
    c: PointOnObject(g4,g24)
    c: PointOnObject(g5,g24)
    c: PointOnObject(g6,g24)
    c: PointOnObject(g7,g24)
    c: PointOnObject(g8,g24)
    c: PointOnObject(g9,g24)
    c: PointOnObject(g10,g24)
    c: PointOnObject(g11,g24)
    c: PointOnObject(g12,g24)
    c: PointOnObject(g13,g24)
    c: PointOnObject(g14,g24)
    c: PointOnObject(g15,g24)
    c: PointOnObject(g16,g24)
    c: PointOnObject(g17,g24)
    c: PointOnObject(g18,g24)
    c: PointOnObject(g19,g24)
    c: PointOnObject(g20,g24)
    c: PointOnObject(g21,g24)
    c: PointOnObject(g22,g24)
    c: PointOnObject(g23,g24)
    c: Coincident(g24,g-1)
    c: Horizontal(g23)
    c: DistanceX(g4,g17) = 11
FEATURE [Sketcher::SketchObject] Sketch400
  FullyConstrained = false
  MapMode = 5
  Support = -> [XY_Plane890]
  sketch-geometry (25):
    g0: LineSegment StartX=-0.789915 StartY=6 StartZ=0 EndX=-2.31591 EndY=5.59111 EndZ=0
    g1: LineSegment StartX=-2.31591 StartY=5.59111 StartZ=0 EndX=-3.68409 EndY=4.80119 EndZ=0
    g2: LineSegment StartX=-3.68409 StartY=4.80119 StartZ=0 EndX=-4.80119 EndY=3.68409 EndZ=0
    g3: LineSegment StartX=-4.80119 StartY=3.68409 StartZ=0 EndX=-5.59111 EndY=2.31591 EndZ=0
    g4: LineSegment StartX=-5.59111 StartY=2.31591 StartZ=0 EndX=-6 EndY=0.789915 EndZ=0
    g5: LineSegment StartX=-6 StartY=0.789915 StartZ=0 EndX=-6 EndY=-0.789915 EndZ=0
    g6: LineSegment StartX=-6 StartY=-0.789915 StartZ=0 EndX=-5.59111 EndY=-2.31591 EndZ=0
    g7: LineSegment StartX=-5.59111 StartY=-2.31591 StartZ=0 EndX=-4.80119 EndY=-3.68409 EndZ=0
    g8: LineSegment StartX=-4.80119 StartY=-3.68409 StartZ=0 EndX=-3.68409 EndY=-4.80119 EndZ=0
    g9: LineSegment StartX=-3.68409 StartY=-4.80119 StartZ=0 EndX=-2.31591 EndY=-5.59111 EndZ=0
    g10: LineSegment StartX=-2.31591 StartY=-5.59111 StartZ=0 EndX=-0.789915 EndY=-6 EndZ=0
    g11: LineSegment StartX=-0.789915 StartY=-6 StartZ=0 EndX=0.789915 EndY=-6 EndZ=0
    g12: LineSegment StartX=0.789915 StartY=-6 StartZ=0 EndX=2.31591 EndY=-5.59111 EndZ=0
    g13: LineSegment StartX=2.31591 StartY=-5.59111 StartZ=0 EndX=3.68409 EndY=-4.80119 EndZ=0
    g14: LineSegment StartX=3.68409 StartY=-4.80119 StartZ=0 EndX=4.80119 EndY=-3.68409 EndZ=0
    g15: LineSegment StartX=4.80119 StartY=-3.68409 StartZ=0 EndX=5.59111 EndY=-2.31591 EndZ=0
    g16: LineSegment StartX=5.59111 StartY=-2.31591 StartZ=0 EndX=6 EndY=-0.789915 EndZ=0
    g17: LineSegment StartX=6 StartY=-0.789915 StartZ=0 EndX=6 EndY=0.789915 EndZ=0
    g18: LineSegment StartX=6 StartY=0.789915 StartZ=0 EndX=5.59111 EndY=2.31591 EndZ=0
    g19: LineSegment StartX=5.59111 StartY=2.31591 StartZ=0 EndX=4.80119 EndY=3.68409 EndZ=0
    g20: LineSegment StartX=4.80119 StartY=3.68409 StartZ=0 EndX=3.68409 EndY=4.80119 EndZ=0
    g21: LineSegment StartX=3.68409 StartY=4.80119 StartZ=0 EndX=2.31591 EndY=5.59111 EndZ=0
    g22: LineSegment StartX=2.31591 StartY=5.59111 StartZ=0 EndX=0.789915 EndY=6 EndZ=0
    g23: LineSegment StartX=0.789915 StartY=6 StartZ=0 EndX=-0.789915 EndY=6 EndZ=0
    g24: Circle CenterX=0 CenterY=0 CenterZ=0 NormalX=0 NormalY=0 NormalZ=1 AngleXU=0 Radius=6.05177
  constraints (52):
    c: Coincident(g0,g1)
    c: Coincident(g1,g2)
    c: Coincident(g2,g3)
    c: Coincident(g3,g4)
    c: Coincident(g4,g5)
    c: Coincident(g5,g6)
    c: Coincident(g6,g7)
    c: Coincident(g7,g8)
    c: Coincident(g8,g9)
    c: Coincident(g9,g10)
    c: Coincident(g10,g11)
    c: Coincident(g11,g12)
    c: Coincident(g12,g13)
    c: Coincident(g13,g14)
    c: Coincident(g14,g15)
    c: Coincident(g15,g16)
    c: Coincident(g16,g17)
    c: Coincident(g17,g18)
    c: Coincident(g18,g19)
    c: Coincident(g19,g20)
    c: Coincident(g20,g21)
    c: Coincident(g21,g22)
    c: Coincident(g22,g23)
    c: Coincident(g23,g0)
    c: Equal(g0, g1-g23) x23
    c: PointOnObject(g0,g24)
    c: PointOnObject(g1,g24)
    c: PointOnObject(g2,g24)
    c: PointOnObject(g3,g24)
    c: PointOnObject(g4,g24)
    c: PointOnObject(g5,g24)
    c: PointOnObject(g6,g24)
    c: PointOnObject(g7,g24)
    c: PointOnObject(g8,g24)
    c: PointOnObject(g9,g24)
    c: PointOnObject(g10,g24)
    c: PointOnObject(g11,g24)
    c: PointOnObject(g12,g24)
    c: PointOnObject(g13,g24)
    c: PointOnObject(g14,g24)
    c: PointOnObject(g15,g24)
    c: PointOnObject(g16,g24)
    c: PointOnObject(g17,g24)
    c: PointOnObject(g18,g24)
    c: PointOnObject(g19,g24)
    c: PointOnObject(g20,g24)
    c: PointOnObject(g21,g24)
    c: PointOnObject(g22,g24)
    c: PointOnObject(g23,g24)
    c: Coincident(g24,g-1)
    c: Horizontal(g23)
    c: DistanceX(g4,g17) = 12
FEATURE [Sketcher::SketchObject] Sketch402
  AttachmentOffset = pos=(0,0,17) rot=(0,0,1;0rad)
  FullyConstrained = false
  MapMode = 5
  Placement = pos=(0,0,17) rot=(0,0,1;0rad)
  Support = -> [XY_Plane890]
  sketch-geometry (25):
    g0: LineSegment StartX=-4.65926 StartY=1.92993 StartZ=0 EndX=-5 EndY=0.658262 EndZ=0
    g1: LineSegment StartX=-5 StartY=0.658262 StartZ=0 EndX=-5 EndY=-0.658262 EndZ=0
    g2: LineSegment StartX=-5 StartY=-0.658262 StartZ=0 EndX=-4.65926 EndY=-1.92993 EndZ=0
    g3: LineSegment StartX=-4.65926 StartY=-1.92993 StartZ=0 EndX=-4.001 EndY=-3.07007 EndZ=0
    g4: LineSegment StartX=-4.001 StartY=-3.07007 StartZ=0 EndX=-3.07007 EndY=-4.001 EndZ=0
    g5: LineSegment StartX=-3.07007 StartY=-4.001 StartZ=0 EndX=-1.92993 EndY=-4.65926 EndZ=0
    g6: LineSegment StartX=-1.92993 StartY=-4.65926 StartZ=0 EndX=-0.658262 EndY=-5 EndZ=0
    g7: LineSegment StartX=-0.658262 StartY=-5 StartZ=0 EndX=0.658262 EndY=-5 EndZ=0
    g8: LineSegment StartX=0.658262 StartY=-5 StartZ=0 EndX=1.92993 EndY=-4.65926 EndZ=0
    g9: LineSegment StartX=1.92993 StartY=-4.65926 StartZ=0 EndX=3.07007 EndY=-4.001 EndZ=0
    g10: LineSegment StartX=3.07007 StartY=-4.001 StartZ=0 EndX=4.001 EndY=-3.07007 EndZ=0
    g11: LineSegment StartX=4.001 StartY=-3.07007 StartZ=0 EndX=4.65926 EndY=-1.92993 EndZ=0
    g12: LineSegment StartX=4.65926 StartY=-1.92993 StartZ=0 EndX=5 EndY=-0.658262 EndZ=0
    g13: LineSegment StartX=5 StartY=-0.658262 StartZ=0 EndX=5 EndY=0.658262 EndZ=0
    g14: LineSegment StartX=5 StartY=0.658262 StartZ=0 EndX=4.65926 EndY=1.92993 EndZ=0
    g15: LineSegment StartX=4.65926 StartY=1.92993 StartZ=0 EndX=4.001 EndY=3.07007 EndZ=0
    g16: LineSegment StartX=4.001 StartY=3.07007 StartZ=0 EndX=3.07007 EndY=4.001 EndZ=0
    g17: LineSegment StartX=3.07007 StartY=4.001 StartZ=0 EndX=1.92993 EndY=4.65926 EndZ=0
    g18: LineSegment StartX=1.92993 StartY=4.65926 StartZ=0 EndX=0.658262 EndY=5 EndZ=0
    g19: LineSegment StartX=0.658262 StartY=5 StartZ=0 EndX=-0.658262 EndY=5 EndZ=0
    g20: LineSegment StartX=-0.658262 StartY=5 StartZ=0 EndX=-1.92993 EndY=4.65926 EndZ=0
    g21: LineSegment StartX=-1.92993 StartY=4.65926 StartZ=0 EndX=-3.07007 EndY=4.001 EndZ=0
    g22: LineSegment StartX=-3.07007 StartY=4.001 StartZ=0 EndX=-4.001 EndY=3.07007 EndZ=0
    g23: LineSegment StartX=-4.001 StartY=3.07007 StartZ=0 EndX=-4.65926 EndY=1.92993 EndZ=0
    g24: Circle CenterX=0 CenterY=0 CenterZ=0 NormalX=0 NormalY=0 NormalZ=1 AngleXU=0 Radius=5.04314
  constraints (52):
    c: Coincident(g0,g1)
    c: Coincident(g1,g2)
    c: Coincident(g2,g3)
    c: Coincident(g3,g4)
    c: Coincident(g4,g5)
    c: Coincident(g5,g6)
    c: Coincident(g6,g7)
    c: Coincident(g7,g8)
    c: Coincident(g8,g9)
    c: Coincident(g9,g10)
    c: Coincident(g10,g11)
    c: Coincident(g11,g12)
    c: Coincident(g12,g13)
    c: Coincident(g13,g14)
    c: Coincident(g14,g15)
    c: Coincident(g15,g16)
    c: Coincident(g16,g17)
    c: Coincident(g17,g18)
    c: Coincident(g18,g19)
    c: Coincident(g19,g20)
    c: Coincident(g20,g21)
    c: Coincident(g21,g22)
    c: Coincident(g22,g23)
    c: Coincident(g23,g0)
    c: Equal(g0, g1-g23) x23
    c: PointOnObject(g0,g24)
    c: PointOnObject(g1,g24)
    c: PointOnObject(g2,g24)
    c: PointOnObject(g3,g24)
    c: PointOnObject(g4,g24)
    c: PointOnObject(g5,g24)
    c: PointOnObject(g6,g24)
    c: PointOnObject(g7,g24)
    c: PointOnObject(g8,g24)
    c: PointOnObject(g9,g24)
    c: PointOnObject(g10,g24)
    c: PointOnObject(g11,g24)
    c: PointOnObject(g12,g24)
    c: PointOnObject(g13,g24)
    c: PointOnObject(g14,g24)
    c: PointOnObject(g15,g24)
    c: PointOnObject(g16,g24)
    c: PointOnObject(g17,g24)
    c: PointOnObject(g18,g24)
    c: PointOnObject(g19,g24)
    c: PointOnObject(g20,g24)
    c: PointOnObject(g21,g24)
    c: PointOnObject(g22,g24)
    c: PointOnObject(g23,g24)
    c: Coincident(g24,g-1)
    c: Horizontal(g19)
    c: DistanceX(g0,g13) = 10
FEATURE [PartDesign::Body] Body168
  Group = -> [Sketch387,Sketch386,Sketch388,AdditiveLoft031,Sketch389,Pad069,Sketch390,Pocket064,Sketch380,Pocket065,Sketch391,Pocket066,Chamfer053,Chamfer054,Fillet029]
  Origin = -> Origin891
  Tip = -> Fillet029
FEATURE [App::Part] Part140  label="Cap033"
  Group = -> [Body168]
  Origin = -> Origin892
  Placement = pos=(-40.005,40.005,0) rot=(0,0,1;0rad)
  expr: .Placement.Base.x = -40.005
  expr: .Placement.Base.y = 40.005
FEATURE [PartDesign::AdditiveLoft] AdditiveLoft042
  AllowMultiFace = false
  Closed = false
  Profile = -> Sketch394
  Refine = true
  Ruled = false
  Sections = -> [Sketch383,Sketch384]
FEATURE [Sketcher::SketchObject] Sketch393
  FullyConstrained = false
  MapMode = 5
  Placement = pos=(0,0,17) rot=(0,0,1;0rad)
  Support = -> [AdditiveLoft042]
  sketch-geometry (1):
    g0: Circle CenterX=0 CenterY=0 CenterZ=0 NormalX=0 NormalY=0 NormalZ=1 AngleXU=0 Radius=4.5
  constraints (2):
    c: Coincident(g0,g-1)
    c: Radius(g0) = 4.5
FEATURE [PartDesign::Pad] Pad071
  AllowMultiFace = false
  BaseFeature = -> AdditiveLoft042
  Direction = (1,1,1)
  Length = 0.7
  Length2 = 100
  Profile = -> Sketch393
  Refine = true
  Type = 0
FEATURE [Sketcher::SketchObject] Sketch392
  FullyConstrained = false
  MapMode = 5
  Placement = pos=(0,0,0) rot=(1,0,0;3.14159rad)
  Support = -> [Pad071]
  sketch-geometry (1):
    g0: Circle CenterX=0 CenterY=0 CenterZ=0 NormalX=0 NormalY=0 NormalZ=1 AngleXU=0 Radius=5
  constraints (2):
    c: Coincident(g0,g-1)
    c: Radius(g0) = 5
FEATURE [PartDesign::Pocket] Pocket067
  AllowMultiFace = false
  BaseFeature = -> Pad071
  Direction = (1,1,1)
  Length = 1
  Length2 = 100
  Profile = -> Sketch392
  Refine = true
  Type = 0
FEATURE [Sketcher::SketchObject] Sketch381
  FullyConstrained = false
  MapMode = 5
  Placement = pos=(0,0,1) rot=(1,0,0;3.14159rad)
  Support = -> [Pocket067]
  sketch-geometry (1):
    g0: Circle CenterX=0 CenterY=0 CenterZ=0 NormalX=0 NormalY=0 NormalZ=1 AngleXU=0 Radius=4.65
  constraints (2):
    c: Coincident(g0,g-1)
    c: Radius(g0) = 4.65
FEATURE [PartDesign::Pocket] Pocket068
  AllowMultiFace = false
  BaseFeature = -> Pocket067
  Direction = (1,1,1)
  Length = 1
  Length2 = 100
  Profile = -> Sketch381
  Refine = true
  Type = 0
FEATURE [Sketcher::SketchObject] Sketch382
  FullyConstrained = false
  MapMode = 5
  Placement = pos=(0,0,2) rot=(1,0,0;3.14159rad)
  Support = -> [Pocket068]
  sketch-geometry (2):
    g0: ArcOfCircle CenterX=0 CenterY=0 CenterZ=0 NormalX=0 NormalY=0 NormalZ=1 AngleXU=0 Radius=3 StartAngle=2.19024 EndAngle=7.23453
    g1: LineSegment StartX=-1.74176 StartY=2.4426 StartZ=0 EndX=1.74176 EndY=2.4426 EndZ=0
  constraints (5):
    c: Coincident(g0,g-1)
    c: Coincident(g1,g0)
    c: Coincident(g1,g0)
    c: Horizontal(g1)
    c: Radius(g0) = 3
FEATURE [PartDesign::Pocket] Pocket063
  AllowMultiFace = false
  BaseFeature = -> Pocket068
  Direction = (1,1,1)
  Length = 8
  Length2 = 100
  Profile = -> Sketch382
  Refine = true
  Type = 0
FEATURE [PartDesign::Chamfer] Chamfer055
  Angle = 45
  Base = -> Pocket063 [Edge82,Edge83]
  BaseFeature = -> Pocket063
  ChamferType = 0
  FlipDirection = false
  Size = 1.4
  Size2 = 1
  SupportTransform = false
  UseAllEdges = false
FEATURE [PartDesign::Chamfer] Chamfer056
  Angle = 45
  Base = -> Chamfer055 [Edge8]
  BaseFeature = -> Chamfer055
  ChamferType = 0
  FlipDirection = false
  Size = 0.3
  Size2 = 1
  SupportTransform = false
  UseAllEdges = false
FEATURE [PartDesign::Fillet] Fillet030
  Base = -> Chamfer056 [Edge93,Face36]
  BaseFeature = -> Chamfer056
  Radius = 0.1
  SupportTransform = false
  UseAllEdges = false
FEATURE [PartDesign::Body] Body160
  Group = -> [Sketch394,Sketch383,Sketch384,AdditiveLoft042,Sketch393,Pad071,Sketch392,Pocket067,Sketch381,Pocket068,Sketch382,Pocket063,Chamfer055,Chamfer056,Fillet030]
  Origin = -> Origin886
  Tip = -> Fillet030
FEATURE [App::Part] Part142  label="Cap035"
  Group = -> [Body160]
  Origin = -> Origin888
  Placement = pos=(-13.34,40.005,0) rot=(0,0,1;0rad)
  expr: .Placement.Base.x = -13.335
  expr: .Placement.Base.y = 40.005
FEATURE [PartDesign::AdditiveLoft] AdditiveLoft043
  AllowMultiFace = false
  Closed = false
  Profile = -> Sketch400
  Refine = true
  Ruled = false
  Sections = -> [Sketch395,Sketch402]
FEATURE [Sketcher::SketchObject] Sketch399
  FullyConstrained = false
  MapMode = 5
  Placement = pos=(0,0,17) rot=(0,0,1;0rad)
  Support = -> [AdditiveLoft043]
  sketch-geometry (1):
    g0: Circle CenterX=0 CenterY=0 CenterZ=0 NormalX=0 NormalY=0 NormalZ=1 AngleXU=0 Radius=4.5
  constraints (2):
    c: Coincident(g0,g-1)
    c: Radius(g0) = 4.5
FEATURE [PartDesign::Pad] Pad073
  AllowMultiFace = false
  BaseFeature = -> AdditiveLoft043
  Direction = (1,1,1)
  Length = 0.7
  Length2 = 100
  Profile = -> Sketch399
  Refine = true
  Type = 0
FEATURE [Sketcher::SketchObject] Sketch398
  FullyConstrained = false
  MapMode = 5
  Placement = pos=(0,0,0) rot=(1,0,0;3.14159rad)
  Support = -> [Pad073]
  sketch-geometry (1):
    g0: Circle CenterX=0 CenterY=0 CenterZ=0 NormalX=0 NormalY=0 NormalZ=1 AngleXU=0 Radius=5
  constraints (2):
    c: Coincident(g0,g-1)
    c: Radius(g0) = 5
FEATURE [PartDesign::Pocket] Pocket075
  AllowMultiFace = false
  BaseFeature = -> Pad073
  Direction = (1,1,1)
  Length = 1
  Length2 = 100
  Profile = -> Sketch398
  Refine = true
  Type = 0
FEATURE [Sketcher::SketchObject] Sketch396
  FullyConstrained = false
  MapMode = 5
  Placement = pos=(0,0,1) rot=(1,0,0;3.14159rad)
  Support = -> [Pocket075]
  sketch-geometry (1):
    g0: Circle CenterX=0 CenterY=0 CenterZ=0 NormalX=0 NormalY=0 NormalZ=1 AngleXU=0 Radius=4.65
  constraints (2):
    c: Coincident(g0,g-1)
    c: Radius(g0) = 4.65
FEATURE [PartDesign::Pocket] Pocket069
  AllowMultiFace = false
  BaseFeature = -> Pocket075
  Direction = (1,1,1)
  Length = 1
  Length2 = 100
  Profile = -> Sketch396
  Refine = true
  Type = 0
FEATURE [Sketcher::SketchObject] Sketch397
  FullyConstrained = false
  MapMode = 5
  Placement = pos=(0,0,2) rot=(1,0,0;3.14159rad)
  Support = -> [Pocket069]
  sketch-geometry (2):
    g0: ArcOfCircle CenterX=0 CenterY=0 CenterZ=0 NormalX=0 NormalY=0 NormalZ=1 AngleXU=0 Radius=3 StartAngle=2.19024 EndAngle=7.23453
    g1: LineSegment StartX=-1.74176 StartY=2.4426 StartZ=0 EndX=1.74176 EndY=2.4426 EndZ=0
  constraints (5):
    c: Coincident(g0,g-1)
    c: Coincident(g1,g0)
    c: Coincident(g1,g0)
    c: Horizontal(g1)
    c: Radius(g0) = 3
FEATURE [PartDesign::Pocket] Pocket074
  AllowMultiFace = false
  BaseFeature = -> Pocket069
  Direction = (1,1,1)
  Length = 8
  Length2 = 100
  Profile = -> Sketch397
  Refine = true
  Type = 0
FEATURE [PartDesign::Chamfer] Chamfer061
  Angle = 45
  Base = -> Pocket074 [Edge82,Edge83]
  BaseFeature = -> Pocket074
  ChamferType = 0
  FlipDirection = false
  Size = 1.4
  Size2 = 1
  SupportTransform = false
  UseAllEdges = false
FEATURE [PartDesign::Chamfer] Chamfer060
  Angle = 45
  Base = -> Chamfer061 [Edge8]
  BaseFeature = -> Chamfer061
  ChamferType = 0
  FlipDirection = false
  Size = 0.3
  Size2 = 1
  SupportTransform = false
  UseAllEdges = false
FEATURE [PartDesign::Fillet] Fillet028
  Base = -> Chamfer060 [Edge93,Face36]
  BaseFeature = -> Chamfer060
  Radius = 0.1
  SupportTransform = false
  UseAllEdges = false
FEATURE [PartDesign::Body] Body159
  Group = -> [Sketch400,Sketch395,Sketch402,AdditiveLoft043,Sketch399,Pad073,Sketch398,Pocket075,Sketch396,Pocket069,Sketch397,Pocket074,Chamfer061,Chamfer060,Fillet028]
  Origin = -> Origin911
  Tip = -> Fillet028
FEATURE [App::Part] Part135  label="Cap028"
  Group = -> [Body159]
  Origin = -> Origin889
  Placement = pos=(13.335,40.005,0) rot=(0,0,1;0rad)
  expr: .Placement.Base.x = 13.335
  expr: .Placement.Base.y = 40.005
FEATURE [Sketcher::SketchObject] Sketch413
  AttachmentOffset = pos=(0,0,7) rot=(0,0,1;0rad)
  FullyConstrained = false
  MapMode = 5
  Placement = pos=(0,0,7) rot=(0,0,1;0rad)
  Support = -> [XY_Plane891]
  sketch-geometry (25):
    g0: LineSegment StartX=-0.724089 StartY=5.5 StartZ=0 EndX=-2.12292 EndY=5.12518 EndZ=0
    g1: LineSegment StartX=-2.12292 StartY=5.12518 StartZ=0 EndX=-3.37708 EndY=4.4011 EndZ=0
    g2: LineSegment StartX=-3.37708 StartY=4.4011 StartZ=0 EndX=-4.4011 EndY=3.37708 EndZ=0
    g3: LineSegment StartX=-4.4011 StartY=3.37708 StartZ=0 EndX=-5.12518 EndY=2.12292 EndZ=0
    g4: LineSegment StartX=-5.12518 StartY=2.12292 StartZ=0 EndX=-5.5 EndY=0.724089 EndZ=0
    g5: LineSegment StartX=-5.5 StartY=0.724089 StartZ=0 EndX=-5.5 EndY=-0.724089 EndZ=0
    g6: LineSegment StartX=-5.5 StartY=-0.724089 StartZ=0 EndX=-5.12518 EndY=-2.12292 EndZ=0
    g7: LineSegment StartX=-5.12518 StartY=-2.12292 StartZ=0 EndX=-4.4011 EndY=-3.37708 EndZ=0
    g8: LineSegment StartX=-4.4011 StartY=-3.37708 StartZ=0 EndX=-3.37708 EndY=-4.4011 EndZ=0
    g9: LineSegment StartX=-3.37708 StartY=-4.4011 StartZ=0 EndX=-2.12292 EndY=-5.12518 EndZ=0
    g10: LineSegment StartX=-2.12292 StartY=-5.12518 StartZ=0 EndX=-0.724089 EndY=-5.5 EndZ=0
    g11: LineSegment StartX=-0.724089 StartY=-5.5 StartZ=0 EndX=0.724089 EndY=-5.5 EndZ=0
    g12: LineSegment StartX=0.724089 StartY=-5.5 StartZ=0 EndX=2.12292 EndY=-5.12518 EndZ=0
    g13: LineSegment StartX=2.12292 StartY=-5.12518 StartZ=0 EndX=3.37708 EndY=-4.4011 EndZ=0
    g14: LineSegment StartX=3.37708 StartY=-4.4011 StartZ=0 EndX=4.4011 EndY=-3.37708 EndZ=0
    g15: LineSegment StartX=4.4011 StartY=-3.37708 StartZ=0 EndX=5.12518 EndY=-2.12292 EndZ=0
    g16: LineSegment StartX=5.12518 StartY=-2.12292 StartZ=0 EndX=5.5 EndY=-0.724089 EndZ=0
    g17: LineSegment StartX=5.5 StartY=-0.724089 StartZ=0 EndX=5.5 EndY=0.724089 EndZ=0
    g18: LineSegment StartX=5.5 StartY=0.724089 StartZ=0 EndX=5.12518 EndY=2.12292 EndZ=0
    g19: LineSegment StartX=5.12518 StartY=2.12292 StartZ=0 EndX=4.4011 EndY=3.37708 EndZ=0
    g20: LineSegment StartX=4.4011 StartY=3.37708 StartZ=0 EndX=3.37708 EndY=4.4011 EndZ=0
    g21: LineSegment StartX=3.37708 StartY=4.4011 StartZ=0 EndX=2.12292 EndY=5.12518 EndZ=0
    g22: LineSegment StartX=2.12292 StartY=5.12518 StartZ=0 EndX=0.724089 EndY=5.5 EndZ=0
    g23: LineSegment StartX=0.724089 StartY=5.5 StartZ=0 EndX=-0.724089 EndY=5.5 EndZ=0
    g24: Circle CenterX=0 CenterY=0 CenterZ=0 NormalX=0 NormalY=0 NormalZ=1 AngleXU=0 Radius=5.54746
  constraints (52):
    c: Coincident(g0,g1)
    c: Coincident(g1,g2)
    c: Coincident(g2,g3)
    c: Coincident(g3,g4)
    c: Coincident(g4,g5)
    c: Coincident(g5,g6)
    c: Coincident(g6,g7)
    c: Coincident(g7,g8)
    c: Coincident(g8,g9)
    c: Coincident(g9,g10)
    c: Coincident(g10,g11)
    c: Coincident(g11,g12)
    c: Coincident(g12,g13)
    c: Coincident(g13,g14)
    c: Coincident(g14,g15)
    c: Coincident(g15,g16)
    c: Coincident(g16,g17)
    c: Coincident(g17,g18)
    c: Coincident(g18,g19)
    c: Coincident(g19,g20)
    c: Coincident(g20,g21)
    c: Coincident(g21,g22)
    c: Coincident(g22,g23)
    c: Coincident(g23,g0)
    c: Equal(g0, g1-g23) x23
    c: PointOnObject(g0,g24)
    c: PointOnObject(g1,g24)
    c: PointOnObject(g2,g24)
    c: PointOnObject(g3,g24)
    c: PointOnObject(g4,g24)
    c: PointOnObject(g5,g24)
    c: PointOnObject(g6,g24)
    c: PointOnObject(g7,g24)
    c: PointOnObject(g8,g24)
    c: PointOnObject(g9,g24)
    c: PointOnObject(g10,g24)
    c: PointOnObject(g11,g24)
    c: PointOnObject(g12,g24)
    c: PointOnObject(g13,g24)
    c: PointOnObject(g14,g24)
    c: PointOnObject(g15,g24)
    c: PointOnObject(g16,g24)
    c: PointOnObject(g17,g24)
    c: PointOnObject(g18,g24)
    c: PointOnObject(g19,g24)
    c: PointOnObject(g20,g24)
    c: PointOnObject(g21,g24)
    c: PointOnObject(g22,g24)
    c: PointOnObject(g23,g24)
    c: Coincident(g24,g-1)
    c: Horizontal(g23)
    c: DistanceX(g4,g17) = 11
FEATURE [Sketcher::SketchObject] Sketch414
  AttachmentOffset = pos=(0,0,7) rot=(0,0,1;0rad)
  FullyConstrained = false
  MapMode = 5
  Placement = pos=(0,0,7) rot=(0,0,1;0rad)
  Support = -> [XY_Plane888]
  sketch-geometry (25):
    g0: LineSegment StartX=-0.724089 StartY=5.5 StartZ=0 EndX=-2.12292 EndY=5.12518 EndZ=0
    g1: LineSegment StartX=-2.12292 StartY=5.12518 StartZ=0 EndX=-3.37708 EndY=4.4011 EndZ=0
    g2: LineSegment StartX=-3.37708 StartY=4.4011 StartZ=0 EndX=-4.4011 EndY=3.37708 EndZ=0
    g3: LineSegment StartX=-4.4011 StartY=3.37708 StartZ=0 EndX=-5.12518 EndY=2.12292 EndZ=0
    g4: LineSegment StartX=-5.12518 StartY=2.12292 StartZ=0 EndX=-5.5 EndY=0.724089 EndZ=0
    g5: LineSegment StartX=-5.5 StartY=0.724089 StartZ=0 EndX=-5.5 EndY=-0.724089 EndZ=0
    g6: LineSegment StartX=-5.5 StartY=-0.724089 StartZ=0 EndX=-5.12518 EndY=-2.12292 EndZ=0
    g7: LineSegment StartX=-5.12518 StartY=-2.12292 StartZ=0 EndX=-4.4011 EndY=-3.37708 EndZ=0
    g8: LineSegment StartX=-4.4011 StartY=-3.37708 StartZ=0 EndX=-3.37708 EndY=-4.4011 EndZ=0
    g9: LineSegment StartX=-3.37708 StartY=-4.4011 StartZ=0 EndX=-2.12292 EndY=-5.12518 EndZ=0
    g10: LineSegment StartX=-2.12292 StartY=-5.12518 StartZ=0 EndX=-0.724089 EndY=-5.5 EndZ=0
    g11: LineSegment StartX=-0.724089 StartY=-5.5 StartZ=0 EndX=0.724089 EndY=-5.5 EndZ=0
    g12: LineSegment StartX=0.724089 StartY=-5.5 StartZ=0 EndX=2.12292 EndY=-5.12518 EndZ=0
    g13: LineSegment StartX=2.12292 StartY=-5.12518 StartZ=0 EndX=3.37708 EndY=-4.4011 EndZ=0
    g14: LineSegment StartX=3.37708 StartY=-4.4011 StartZ=0 EndX=4.4011 EndY=-3.37708 EndZ=0
    g15: LineSegment StartX=4.4011 StartY=-3.37708 StartZ=0 EndX=5.12518 EndY=-2.12292 EndZ=0
    g16: LineSegment StartX=5.12518 StartY=-2.12292 StartZ=0 EndX=5.5 EndY=-0.724089 EndZ=0
    g17: LineSegment StartX=5.5 StartY=-0.724089 StartZ=0 EndX=5.5 EndY=0.724089 EndZ=0
    g18: LineSegment StartX=5.5 StartY=0.724089 StartZ=0 EndX=5.12518 EndY=2.12292 EndZ=0
    g19: LineSegment StartX=5.12518 StartY=2.12292 StartZ=0 EndX=4.4011 EndY=3.37708 EndZ=0
    g20: LineSegment StartX=4.4011 StartY=3.37708 StartZ=0 EndX=3.37708 EndY=4.4011 EndZ=0
    g21: LineSegment StartX=3.37708 StartY=4.4011 StartZ=0 EndX=2.12292 EndY=5.12518 EndZ=0
    g22: LineSegment StartX=2.12292 StartY=5.12518 StartZ=0 EndX=0.724089 EndY=5.5 EndZ=0
    g23: LineSegment StartX=0.724089 StartY=5.5 StartZ=0 EndX=-0.724089 EndY=5.5 EndZ=0
    g24: Circle CenterX=0 CenterY=0 CenterZ=0 NormalX=0 NormalY=0 NormalZ=1 AngleXU=0 Radius=5.54746
  constraints (52):
    c: Coincident(g0,g1)
    c: Coincident(g1,g2)
    c: Coincident(g2,g3)
    c: Coincident(g3,g4)
    c: Coincident(g4,g5)
    c: Coincident(g5,g6)
    c: Coincident(g6,g7)
    c: Coincident(g7,g8)
    c: Coincident(g8,g9)
    c: Coincident(g9,g10)
    c: Coincident(g10,g11)
    c: Coincident(g11,g12)
    c: Coincident(g12,g13)
    c: Coincident(g13,g14)
    c: Coincident(g14,g15)
    c: Coincident(g15,g16)
    c: Coincident(g16,g17)
    c: Coincident(g17,g18)
    c: Coincident(g18,g19)
    c: Coincident(g19,g20)
    c: Coincident(g20,g21)
    c: Coincident(g21,g22)
    c: Coincident(g22,g23)
    c: Coincident(g23,g0)
    c: Equal(g0, g1-g23) x23
    c: PointOnObject(g0,g24)
    c: PointOnObject(g1,g24)
    c: PointOnObject(g2,g24)
    c: PointOnObject(g3,g24)
    c: PointOnObject(g4,g24)
    c: PointOnObject(g5,g24)
    c: PointOnObject(g6,g24)
    c: PointOnObject(g7,g24)
    c: PointOnObject(g8,g24)
    c: PointOnObject(g9,g24)
    c: PointOnObject(g10,g24)
    c: PointOnObject(g11,g24)
    c: PointOnObject(g12,g24)
    c: PointOnObject(g13,g24)
    c: PointOnObject(g14,g24)
    c: PointOnObject(g15,g24)
    c: PointOnObject(g16,g24)
    c: PointOnObject(g17,g24)
    c: PointOnObject(g18,g24)
    c: PointOnObject(g19,g24)
    c: PointOnObject(g20,g24)
    c: PointOnObject(g21,g24)
    c: PointOnObject(g22,g24)
    c: PointOnObject(g23,g24)
    c: Coincident(g24,g-1)
    c: Horizontal(g23)
    c: DistanceX(g4,g17) = 11
FEATURE [Sketcher::SketchObject] Sketch416
  AttachmentOffset = pos=(0,0,17) rot=(0,0,1;0rad)
  FullyConstrained = false
  MapMode = 5
  Placement = pos=(0,0,17) rot=(0,0,1;0rad)
  Support = -> [XY_Plane888]
  sketch-geometry (25):
    g0: LineSegment StartX=-4.65926 StartY=1.92993 StartZ=0 EndX=-5 EndY=0.658262 EndZ=0
    g1: LineSegment StartX=-5 StartY=0.658262 StartZ=0 EndX=-5 EndY=-0.658262 EndZ=0
    g2: LineSegment StartX=-5 StartY=-0.658262 StartZ=0 EndX=-4.65926 EndY=-1.92993 EndZ=0
    g3: LineSegment StartX=-4.65926 StartY=-1.92993 StartZ=0 EndX=-4.001 EndY=-3.07007 EndZ=0
    g4: LineSegment StartX=-4.001 StartY=-3.07007 StartZ=0 EndX=-3.07007 EndY=-4.001 EndZ=0
    g5: LineSegment StartX=-3.07007 StartY=-4.001 StartZ=0 EndX=-1.92993 EndY=-4.65926 EndZ=0
    g6: LineSegment StartX=-1.92993 StartY=-4.65926 StartZ=0 EndX=-0.658262 EndY=-5 EndZ=0
    g7: LineSegment StartX=-0.658262 StartY=-5 StartZ=0 EndX=0.658262 EndY=-5 EndZ=0
    g8: LineSegment StartX=0.658262 StartY=-5 StartZ=0 EndX=1.92993 EndY=-4.65926 EndZ=0
    g9: LineSegment StartX=1.92993 StartY=-4.65926 StartZ=0 EndX=3.07007 EndY=-4.001 EndZ=0
    g10: LineSegment StartX=3.07007 StartY=-4.001 StartZ=0 EndX=4.001 EndY=-3.07007 EndZ=0
    g11: LineSegment StartX=4.001 StartY=-3.07007 StartZ=0 EndX=4.65926 EndY=-1.92993 EndZ=0
    g12: LineSegment StartX=4.65926 StartY=-1.92993 StartZ=0 EndX=5 EndY=-0.658262 EndZ=0
    g13: LineSegment StartX=5 StartY=-0.658262 StartZ=0 EndX=5 EndY=0.658262 EndZ=0
    g14: LineSegment StartX=5 StartY=0.658262 StartZ=0 EndX=4.65926 EndY=1.92993 EndZ=0
    g15: LineSegment StartX=4.65926 StartY=1.92993 StartZ=0 EndX=4.001 EndY=3.07007 EndZ=0
    g16: LineSegment StartX=4.001 StartY=3.07007 StartZ=0 EndX=3.07007 EndY=4.001 EndZ=0
    g17: LineSegment StartX=3.07007 StartY=4.001 StartZ=0 EndX=1.92993 EndY=4.65926 EndZ=0
    g18: LineSegment StartX=1.92993 StartY=4.65926 StartZ=0 EndX=0.658262 EndY=5 EndZ=0
    g19: LineSegment StartX=0.658262 StartY=5 StartZ=0 EndX=-0.658262 EndY=5 EndZ=0
    g20: LineSegment StartX=-0.658262 StartY=5 StartZ=0 EndX=-1.92993 EndY=4.65926 EndZ=0
    g21: LineSegment StartX=-1.92993 StartY=4.65926 StartZ=0 EndX=-3.07007 EndY=4.001 EndZ=0
    g22: LineSegment StartX=-3.07007 StartY=4.001 StartZ=0 EndX=-4.001 EndY=3.07007 EndZ=0
    g23: LineSegment StartX=-4.001 StartY=3.07007 StartZ=0 EndX=-4.65926 EndY=1.92993 EndZ=0
    g24: Circle CenterX=0 CenterY=0 CenterZ=0 NormalX=0 NormalY=0 NormalZ=1 AngleXU=0 Radius=5.04314
  constraints (52):
    c: Coincident(g0,g1)
    c: Coincident(g1,g2)
    c: Coincident(g2,g3)
    c: Coincident(g3,g4)
    c: Coincident(g4,g5)
    c: Coincident(g5,g6)
    c: Coincident(g6,g7)
    c: Coincident(g7,g8)
    c: Coincident(g8,g9)
    c: Coincident(g9,g10)
    c: Coincident(g10,g11)
    c: Coincident(g11,g12)
    c: Coincident(g12,g13)
    c: Coincident(g13,g14)
    c: Coincident(g14,g15)
    c: Coincident(g15,g16)
    c: Coincident(g16,g17)
    c: Coincident(g17,g18)
    c: Coincident(g18,g19)
    c: Coincident(g19,g20)
    c: Coincident(g20,g21)
    c: Coincident(g21,g22)
    c: Coincident(g22,g23)
    c: Coincident(g23,g0)
    c: Equal(g0, g1-g23) x23
    c: PointOnObject(g0,g24)
    c: PointOnObject(g1,g24)
    c: PointOnObject(g2,g24)
    c: PointOnObject(g3,g24)
    c: PointOnObject(g4,g24)
    c: PointOnObject(g5,g24)
    c: PointOnObject(g6,g24)
    c: PointOnObject(g7,g24)
    c: PointOnObject(g8,g24)
    c: PointOnObject(g9,g24)
    c: PointOnObject(g10,g24)
    c: PointOnObject(g11,g24)
    c: PointOnObject(g12,g24)
    c: PointOnObject(g13,g24)
    c: PointOnObject(g14,g24)
    c: PointOnObject(g15,g24)
    c: PointOnObject(g16,g24)
    c: PointOnObject(g17,g24)
    c: PointOnObject(g18,g24)
    c: PointOnObject(g19,g24)
    c: PointOnObject(g20,g24)
    c: PointOnObject(g21,g24)
    c: PointOnObject(g22,g24)
    c: PointOnObject(g23,g24)
    c: Coincident(g24,g-1)
    c: Horizontal(g19)
    c: DistanceX(g0,g13) = 10
FEATURE [Sketcher::SketchObject] Sketch417
  FullyConstrained = false
  MapMode = 5
  Support = -> [XY_Plane888]
  sketch-geometry (25):
    g0: LineSegment StartX=-0.789915 StartY=6 StartZ=0 EndX=-2.31591 EndY=5.59111 EndZ=0
    g1: LineSegment StartX=-2.31591 StartY=5.59111 StartZ=0 EndX=-3.68409 EndY=4.80119 EndZ=0
    g2: LineSegment StartX=-3.68409 StartY=4.80119 StartZ=0 EndX=-4.80119 EndY=3.68409 EndZ=0
    g3: LineSegment StartX=-4.80119 StartY=3.68409 StartZ=0 EndX=-5.59111 EndY=2.31591 EndZ=0
    g4: LineSegment StartX=-5.59111 StartY=2.31591 StartZ=0 EndX=-6 EndY=0.789915 EndZ=0
    g5: LineSegment StartX=-6 StartY=0.789915 StartZ=0 EndX=-6 EndY=-0.789915 EndZ=0
    g6: LineSegment StartX=-6 StartY=-0.789915 StartZ=0 EndX=-5.59111 EndY=-2.31591 EndZ=0
    g7: LineSegment StartX=-5.59111 StartY=-2.31591 StartZ=0 EndX=-4.80119 EndY=-3.68409 EndZ=0
    g8: LineSegment StartX=-4.80119 StartY=-3.68409 StartZ=0 EndX=-3.68409 EndY=-4.80119 EndZ=0
    g9: LineSegment StartX=-3.68409 StartY=-4.80119 StartZ=0 EndX=-2.31591 EndY=-5.59111 EndZ=0
    g10: LineSegment StartX=-2.31591 StartY=-5.59111 StartZ=0 EndX=-0.789915 EndY=-6 EndZ=0
    g11: LineSegment StartX=-0.789915 StartY=-6 StartZ=0 EndX=0.789915 EndY=-6 EndZ=0
    g12: LineSegment StartX=0.789915 StartY=-6 StartZ=0 EndX=2.31591 EndY=-5.59111 EndZ=0
    g13: LineSegment StartX=2.31591 StartY=-5.59111 StartZ=0 EndX=3.68409 EndY=-4.80119 EndZ=0
    g14: LineSegment StartX=3.68409 StartY=-4.80119 StartZ=0 EndX=4.80119 EndY=-3.68409 EndZ=0
    g15: LineSegment StartX=4.80119 StartY=-3.68409 StartZ=0 EndX=5.59111 EndY=-2.31591 EndZ=0
    g16: LineSegment StartX=5.59111 StartY=-2.31591 StartZ=0 EndX=6 EndY=-0.789915 EndZ=0
    g17: LineSegment StartX=6 StartY=-0.789915 StartZ=0 EndX=6 EndY=0.789915 EndZ=0
    g18: LineSegment StartX=6 StartY=0.789915 StartZ=0 EndX=5.59111 EndY=2.31591 EndZ=0
    g19: LineSegment StartX=5.59111 StartY=2.31591 StartZ=0 EndX=4.80119 EndY=3.68409 EndZ=0
    g20: LineSegment StartX=4.80119 StartY=3.68409 StartZ=0 EndX=3.68409 EndY=4.80119 EndZ=0
    g21: LineSegment StartX=3.68409 StartY=4.80119 StartZ=0 EndX=2.31591 EndY=5.59111 EndZ=0
    g22: LineSegment StartX=2.31591 StartY=5.59111 StartZ=0 EndX=0.789915 EndY=6 EndZ=0
    g23: LineSegment StartX=0.789915 StartY=6 StartZ=0 EndX=-0.789915 EndY=6 EndZ=0
    g24: Circle CenterX=0 CenterY=0 CenterZ=0 NormalX=0 NormalY=0 NormalZ=1 AngleXU=0 Radius=6.05177
  constraints (52):
    c: Coincident(g0,g1)
    c: Coincident(g1,g2)
    c: Coincident(g2,g3)
    c: Coincident(g3,g4)
    c: Coincident(g4,g5)
    c: Coincident(g5,g6)
    c: Coincident(g6,g7)
    c: Coincident(g7,g8)
    c: Coincident(g8,g9)
    c: Coincident(g9,g10)
    c: Coincident(g10,g11)
    c: Coincident(g11,g12)
    c: Coincident(g12,g13)
    c: Coincident(g13,g14)
    c: Coincident(g14,g15)
    c: Coincident(g15,g16)
    c: Coincident(g16,g17)
    c: Coincident(g17,g18)
    c: Coincident(g18,g19)
    c: Coincident(g19,g20)
    c: Coincident(g20,g21)
    c: Coincident(g21,g22)
    c: Coincident(g22,g23)
    c: Coincident(g23,g0)
    c: Equal(g0, g1-g23) x23
    c: PointOnObject(g0,g24)
    c: PointOnObject(g1,g24)
    c: PointOnObject(g2,g24)
    c: PointOnObject(g3,g24)
    c: PointOnObject(g4,g24)
    c: PointOnObject(g5,g24)
    c: PointOnObject(g6,g24)
    c: PointOnObject(g7,g24)
    c: PointOnObject(g8,g24)
    c: PointOnObject(g9,g24)
    c: PointOnObject(g10,g24)
    c: PointOnObject(g11,g24)
    c: PointOnObject(g12,g24)
    c: PointOnObject(g13,g24)
    c: PointOnObject(g14,g24)
    c: PointOnObject(g15,g24)
    c: PointOnObject(g16,g24)
    c: PointOnObject(g17,g24)
    c: PointOnObject(g18,g24)
    c: PointOnObject(g19,g24)
    c: PointOnObject(g20,g24)
    c: PointOnObject(g21,g24)
    c: PointOnObject(g22,g24)
    c: PointOnObject(g23,g24)
    c: Coincident(g24,g-1)
    c: Horizontal(g23)
    c: DistanceX(g4,g17) = 12
FEATURE [Sketcher::SketchObject] Sketch421
  AttachmentOffset = pos=(0,0,17) rot=(0,0,1;0rad)
  FullyConstrained = false
  MapMode = 5
  Placement = pos=(0,0,17) rot=(0,0,1;0rad)
  Support = -> [XY_Plane891]
  sketch-geometry (25):
    g0: LineSegment StartX=-4.65926 StartY=1.92993 StartZ=0 EndX=-5 EndY=0.658262 EndZ=0
    g1: LineSegment StartX=-5 StartY=0.658262 StartZ=0 EndX=-5 EndY=-0.658262 EndZ=0
    g2: LineSegment StartX=-5 StartY=-0.658262 StartZ=0 EndX=-4.65926 EndY=-1.92993 EndZ=0
    g3: LineSegment StartX=-4.65926 StartY=-1.92993 StartZ=0 EndX=-4.001 EndY=-3.07007 EndZ=0
    g4: LineSegment StartX=-4.001 StartY=-3.07007 StartZ=0 EndX=-3.07007 EndY=-4.001 EndZ=0
    g5: LineSegment StartX=-3.07007 StartY=-4.001 StartZ=0 EndX=-1.92993 EndY=-4.65926 EndZ=0
    g6: LineSegment StartX=-1.92993 StartY=-4.65926 StartZ=0 EndX=-0.658262 EndY=-5 EndZ=0
    g7: LineSegment StartX=-0.658262 StartY=-5 StartZ=0 EndX=0.658262 EndY=-5 EndZ=0
    g8: LineSegment StartX=0.658262 StartY=-5 StartZ=0 EndX=1.92993 EndY=-4.65926 EndZ=0
    g9: LineSegment StartX=1.92993 StartY=-4.65926 StartZ=0 EndX=3.07007 EndY=-4.001 EndZ=0
    g10: LineSegment StartX=3.07007 StartY=-4.001 StartZ=0 EndX=4.001 EndY=-3.07007 EndZ=0
    g11: LineSegment StartX=4.001 StartY=-3.07007 StartZ=0 EndX=4.65926 EndY=-1.92993 EndZ=0
    g12: LineSegment StartX=4.65926 StartY=-1.92993 StartZ=0 EndX=5 EndY=-0.658262 EndZ=0
    g13: LineSegment StartX=5 StartY=-0.658262 StartZ=0 EndX=5 EndY=0.658262 EndZ=0
    g14: LineSegment StartX=5 StartY=0.658262 StartZ=0 EndX=4.65926 EndY=1.92993 EndZ=0
    g15: LineSegment StartX=4.65926 StartY=1.92993 StartZ=0 EndX=4.001 EndY=3.07007 EndZ=0
    g16: LineSegment StartX=4.001 StartY=3.07007 StartZ=0 EndX=3.07007 EndY=4.001 EndZ=0
    g17: LineSegment StartX=3.07007 StartY=4.001 StartZ=0 EndX=1.92993 EndY=4.65926 EndZ=0
    g18: LineSegment StartX=1.92993 StartY=4.65926 StartZ=0 EndX=0.658262 EndY=5 EndZ=0
    g19: LineSegment StartX=0.658262 StartY=5 StartZ=0 EndX=-0.658262 EndY=5 EndZ=0
    g20: LineSegment StartX=-0.658262 StartY=5 StartZ=0 EndX=-1.92993 EndY=4.65926 EndZ=0
    g21: LineSegment StartX=-1.92993 StartY=4.65926 StartZ=0 EndX=-3.07007 EndY=4.001 EndZ=0
    g22: LineSegment StartX=-3.07007 StartY=4.001 StartZ=0 EndX=-4.001 EndY=3.07007 EndZ=0
    g23: LineSegment StartX=-4.001 StartY=3.07007 StartZ=0 EndX=-4.65926 EndY=1.92993 EndZ=0
    g24: Circle CenterX=0 CenterY=0 CenterZ=0 NormalX=0 NormalY=0 NormalZ=1 AngleXU=0 Radius=5.04314
  constraints (52):
    c: Coincident(g0,g1)
    c: Coincident(g1,g2)
    c: Coincident(g2,g3)
    c: Coincident(g3,g4)
    c: Coincident(g4,g5)
    c: Coincident(g5,g6)
    c: Coincident(g6,g7)
    c: Coincident(g7,g8)
    c: Coincident(g8,g9)
    c: Coincident(g9,g10)
    c: Coincident(g10,g11)
    c: Coincident(g11,g12)
    c: Coincident(g12,g13)
    c: Coincident(g13,g14)
    c: Coincident(g14,g15)
    c: Coincident(g15,g16)
    c: Coincident(g16,g17)
    c: Coincident(g17,g18)
    c: Coincident(g18,g19)
    c: Coincident(g19,g20)
    c: Coincident(g20,g21)
    c: Coincident(g21,g22)
    c: Coincident(g22,g23)
    c: Coincident(g23,g0)
    c: Equal(g0, g1-g23) x23
    c: PointOnObject(g0,g24)
    c: PointOnObject(g1,g24)
    c: PointOnObject(g2,g24)
    c: PointOnObject(g3,g24)
    c: PointOnObject(g4,g24)
    c: PointOnObject(g5,g24)
    c: PointOnObject(g6,g24)
    c: PointOnObject(g7,g24)
    c: PointOnObject(g8,g24)
    c: PointOnObject(g9,g24)
    c: PointOnObject(g10,g24)
    c: PointOnObject(g11,g24)
    c: PointOnObject(g12,g24)
    c: PointOnObject(g13,g24)
    c: PointOnObject(g14,g24)
    c: PointOnObject(g15,g24)
    c: PointOnObject(g16,g24)
    c: PointOnObject(g17,g24)
    c: PointOnObject(g18,g24)
    c: PointOnObject(g19,g24)
    c: PointOnObject(g20,g24)
    c: PointOnObject(g21,g24)
    c: PointOnObject(g22,g24)
    c: PointOnObject(g23,g24)
    c: Coincident(g24,g-1)
    c: Horizontal(g19)
    c: DistanceX(g0,g13) = 10
FEATURE [Sketcher::SketchObject] Sketch423
  FullyConstrained = false
  MapMode = 5
  Support = -> [XY_Plane891]
  sketch-geometry (25):
    g0: LineSegment StartX=-0.789915 StartY=6 StartZ=0 EndX=-2.31591 EndY=5.59111 EndZ=0
    g1: LineSegment StartX=-2.31591 StartY=5.59111 StartZ=0 EndX=-3.68409 EndY=4.80119 EndZ=0
    g2: LineSegment StartX=-3.68409 StartY=4.80119 StartZ=0 EndX=-4.80119 EndY=3.68409 EndZ=0
    g3: LineSegment StartX=-4.80119 StartY=3.68409 StartZ=0 EndX=-5.59111 EndY=2.31591 EndZ=0
    g4: LineSegment StartX=-5.59111 StartY=2.31591 StartZ=0 EndX=-6 EndY=0.789915 EndZ=0
    g5: LineSegment StartX=-6 StartY=0.789915 StartZ=0 EndX=-6 EndY=-0.789915 EndZ=0
    g6: LineSegment StartX=-6 StartY=-0.789915 StartZ=0 EndX=-5.59111 EndY=-2.31591 EndZ=0
    g7: LineSegment StartX=-5.59111 StartY=-2.31591 StartZ=0 EndX=-4.80119 EndY=-3.68409 EndZ=0
    g8: LineSegment StartX=-4.80119 StartY=-3.68409 StartZ=0 EndX=-3.68409 EndY=-4.80119 EndZ=0
    g9: LineSegment StartX=-3.68409 StartY=-4.80119 StartZ=0 EndX=-2.31591 EndY=-5.59111 EndZ=0
    g10: LineSegment StartX=-2.31591 StartY=-5.59111 StartZ=0 EndX=-0.789915 EndY=-6 EndZ=0
    g11: LineSegment StartX=-0.789915 StartY=-6 StartZ=0 EndX=0.789915 EndY=-6 EndZ=0
    g12: LineSegment StartX=0.789915 StartY=-6 StartZ=0 EndX=2.31591 EndY=-5.59111 EndZ=0
    g13: LineSegment StartX=2.31591 StartY=-5.59111 StartZ=0 EndX=3.68409 EndY=-4.80119 EndZ=0
    g14: LineSegment StartX=3.68409 StartY=-4.80119 StartZ=0 EndX=4.80119 EndY=-3.68409 EndZ=0
    g15: LineSegment StartX=4.80119 StartY=-3.68409 StartZ=0 EndX=5.59111 EndY=-2.31591 EndZ=0
    g16: LineSegment StartX=5.59111 StartY=-2.31591 StartZ=0 EndX=6 EndY=-0.789915 EndZ=0
    g17: LineSegment StartX=6 StartY=-0.789915 StartZ=0 EndX=6 EndY=0.789915 EndZ=0
    g18: LineSegment StartX=6 StartY=0.789915 StartZ=0 EndX=5.59111 EndY=2.31591 EndZ=0
    g19: LineSegment StartX=5.59111 StartY=2.31591 StartZ=0 EndX=4.80119 EndY=3.68409 EndZ=0
    g20: LineSegment StartX=4.80119 StartY=3.68409 StartZ=0 EndX=3.68409 EndY=4.80119 EndZ=0
    g21: LineSegment StartX=3.68409 StartY=4.80119 StartZ=0 EndX=2.31591 EndY=5.59111 EndZ=0
    g22: LineSegment StartX=2.31591 StartY=5.59111 StartZ=0 EndX=0.789915 EndY=6 EndZ=0
    g23: LineSegment StartX=0.789915 StartY=6 StartZ=0 EndX=-0.789915 EndY=6 EndZ=0
    g24: Circle CenterX=0 CenterY=0 CenterZ=0 NormalX=0 NormalY=0 NormalZ=1 AngleXU=0 Radius=6.05177
  constraints (52):
    c: Coincident(g0,g1)
    c: Coincident(g1,g2)
    c: Coincident(g2,g3)
    c: Coincident(g3,g4)
    c: Coincident(g4,g5)
    c: Coincident(g5,g6)
    c: Coincident(g6,g7)
    c: Coincident(g7,g8)
    c: Coincident(g8,g9)
    c: Coincident(g9,g10)
    c: Coincident(g10,g11)
    c: Coincident(g11,g12)
    c: Coincident(g12,g13)
    c: Coincident(g13,g14)
    c: Coincident(g14,g15)
    c: Coincident(g15,g16)
    c: Coincident(g16,g17)
    c: Coincident(g17,g18)
    c: Coincident(g18,g19)
    c: Coincident(g19,g20)
    c: Coincident(g20,g21)
    c: Coincident(g21,g22)
    c: Coincident(g22,g23)
    c: Coincident(g23,g0)
    c: Equal(g0, g1-g23) x23
    c: PointOnObject(g0,g24)
    c: PointOnObject(g1,g24)
    c: PointOnObject(g2,g24)
    c: PointOnObject(g3,g24)
    c: PointOnObject(g4,g24)
    c: PointOnObject(g5,g24)
    c: PointOnObject(g6,g24)
    c: PointOnObject(g7,g24)
    c: PointOnObject(g8,g24)
    c: PointOnObject(g9,g24)
    c: PointOnObject(g10,g24)
    c: PointOnObject(g11,g24)
    c: PointOnObject(g12,g24)
    c: PointOnObject(g13,g24)
    c: PointOnObject(g14,g24)
    c: PointOnObject(g15,g24)
    c: PointOnObject(g16,g24)
    c: PointOnObject(g17,g24)
    c: PointOnObject(g18,g24)
    c: PointOnObject(g19,g24)
    c: PointOnObject(g20,g24)
    c: PointOnObject(g21,g24)
    c: PointOnObject(g22,g24)
    c: PointOnObject(g23,g24)
    c: Coincident(g24,g-1)
    c: Horizontal(g23)
    c: DistanceX(g4,g17) = 12
FEATURE [PartDesign::AdditiveLoft] AdditiveLoft037
  AllowMultiFace = false
  Closed = false
  Profile = -> Sketch423
  Refine = true
  Ruled = false
  Sections = -> [Sketch413,Sketch421]
FEATURE [Sketcher::SketchObject] Sketch415
  FullyConstrained = false
  MapMode = 5
  Placement = pos=(0,0,17) rot=(0,0,1;0rad)
  Support = -> [AdditiveLoft037]
  sketch-geometry (1):
    g0: Circle CenterX=0 CenterY=0 CenterZ=0 NormalX=0 NormalY=0 NormalZ=1 AngleXU=0 Radius=4.5
  constraints (2):
    c: Coincident(g0,g-1)
    c: Radius(g0) = 4.5
FEATURE [PartDesign::Pad] Pad076
  AllowMultiFace = false
  BaseFeature = -> AdditiveLoft037
  Direction = (1,1,1)
  Length = 0.7
  Length2 = 100
  Profile = -> Sketch415
  Refine = true
  Type = 0
FEATURE [Sketcher::SketchObject] Sketch408
  FullyConstrained = false
  MapMode = 5
  Placement = pos=(0,0,0) rot=(1,0,0;3.14159rad)
  Support = -> [Pad076]
  sketch-geometry (1):
    g0: Circle CenterX=0 CenterY=0 CenterZ=0 NormalX=0 NormalY=0 NormalZ=1 AngleXU=0 Radius=5
  constraints (2):
    c: Coincident(g0,g-1)
    c: Radius(g0) = 5
FEATURE [PartDesign::Pocket] Pocket073
  AllowMultiFace = false
  BaseFeature = -> Pad076
  Direction = (1,1,1)
  Length = 1
  Length2 = 100
  Profile = -> Sketch408
  Refine = true
  Type = 0
FEATURE [Sketcher::SketchObject] Sketch418
  FullyConstrained = false
  MapMode = 5
  Placement = pos=(0,0,1) rot=(1,0,0;3.14159rad)
  Support = -> [Pocket073]
  sketch-geometry (1):
    g0: Circle CenterX=0 CenterY=0 CenterZ=0 NormalX=0 NormalY=0 NormalZ=1 AngleXU=0 Radius=4.65
  constraints (2):
    c: Coincident(g0,g-1)
    c: Radius(g0) = 4.65
FEATURE [PartDesign::Pocket] Pocket070
  AllowMultiFace = false
  BaseFeature = -> Pocket073
  Direction = (1,1,1)
  Length = 1
  Length2 = 100
  Profile = -> Sketch418
  Refine = true
  Type = 0
FEATURE [Sketcher::SketchObject] Sketch407
  FullyConstrained = false
  MapMode = 5
  Placement = pos=(0,0,2) rot=(1,0,0;3.14159rad)
  Support = -> [Pocket070]
  sketch-geometry (2):
    g0: ArcOfCircle CenterX=0 CenterY=0 CenterZ=0 NormalX=0 NormalY=0 NormalZ=1 AngleXU=0 Radius=3 StartAngle=2.19024 EndAngle=7.23453
    g1: LineSegment StartX=-1.74176 StartY=2.4426 StartZ=0 EndX=1.74176 EndY=2.4426 EndZ=0
  constraints (5):
    c: Coincident(g0,g-1)
    c: Coincident(g1,g0)
    c: Coincident(g1,g0)
    c: Horizontal(g1)
    c: Radius(g0) = 3
FEATURE [Sketcher::SketchObject] Sketch424
  AttachmentOffset = pos=(0,0,7) rot=(0,0,1;0rad)
  FullyConstrained = false
  MapMode = 5
  Placement = pos=(0,0,7) rot=(0,0,1;0rad)
  Support = -> [XY_Plane899]
  sketch-geometry (25):
    g0: LineSegment StartX=-0.724089 StartY=5.5 StartZ=0 EndX=-2.12292 EndY=5.12518 EndZ=0
    g1: LineSegment StartX=-2.12292 StartY=5.12518 StartZ=0 EndX=-3.37708 EndY=4.4011 EndZ=0
    g2: LineSegment StartX=-3.37708 StartY=4.4011 StartZ=0 EndX=-4.4011 EndY=3.37708 EndZ=0
    g3: LineSegment StartX=-4.4011 StartY=3.37708 StartZ=0 EndX=-5.12518 EndY=2.12292 EndZ=0
    g4: LineSegment StartX=-5.12518 StartY=2.12292 StartZ=0 EndX=-5.5 EndY=0.724089 EndZ=0
    g5: LineSegment StartX=-5.5 StartY=0.724089 StartZ=0 EndX=-5.5 EndY=-0.724089 EndZ=0
    g6: LineSegment StartX=-5.5 StartY=-0.724089 StartZ=0 EndX=-5.12518 EndY=-2.12292 EndZ=0
    g7: LineSegment StartX=-5.12518 StartY=-2.12292 StartZ=0 EndX=-4.4011 EndY=-3.37708 EndZ=0
    g8: LineSegment StartX=-4.4011 StartY=-3.37708 StartZ=0 EndX=-3.37708 EndY=-4.4011 EndZ=0
    g9: LineSegment StartX=-3.37708 StartY=-4.4011 StartZ=0 EndX=-2.12292 EndY=-5.12518 EndZ=0
    g10: LineSegment StartX=-2.12292 StartY=-5.12518 StartZ=0 EndX=-0.724089 EndY=-5.5 EndZ=0
    g11: LineSegment StartX=-0.724089 StartY=-5.5 StartZ=0 EndX=0.724089 EndY=-5.5 EndZ=0
    g12: LineSegment StartX=0.724089 StartY=-5.5 StartZ=0 EndX=2.12292 EndY=-5.12518 EndZ=0
    g13: LineSegment StartX=2.12292 StartY=-5.12518 StartZ=0 EndX=3.37708 EndY=-4.4011 EndZ=0
    g14: LineSegment StartX=3.37708 StartY=-4.4011 StartZ=0 EndX=4.4011 EndY=-3.37708 EndZ=0
    g15: LineSegment StartX=4.4011 StartY=-3.37708 StartZ=0 EndX=5.12518 EndY=-2.12292 EndZ=0
    g16: LineSegment StartX=5.12518 StartY=-2.12292 StartZ=0 EndX=5.5 EndY=-0.724089 EndZ=0
    g17: LineSegment StartX=5.5 StartY=-0.724089 StartZ=0 EndX=5.5 EndY=0.724089 EndZ=0
    g18: LineSegment StartX=5.5 StartY=0.724089 StartZ=0 EndX=5.12518 EndY=2.12292 EndZ=0
    g19: LineSegment StartX=5.12518 StartY=2.12292 StartZ=0 EndX=4.4011 EndY=3.37708 EndZ=0
    g20: LineSegment StartX=4.4011 StartY=3.37708 StartZ=0 EndX=3.37708 EndY=4.4011 EndZ=0
    g21: LineSegment StartX=3.37708 StartY=4.4011 StartZ=0 EndX=2.12292 EndY=5.12518 EndZ=0
    g22: LineSegment StartX=2.12292 StartY=5.12518 StartZ=0 EndX=0.724089 EndY=5.5 EndZ=0
    g23: LineSegment StartX=0.724089 StartY=5.5 StartZ=0 EndX=-0.724089 EndY=5.5 EndZ=0
    g24: Circle CenterX=0 CenterY=0 CenterZ=0 NormalX=0 NormalY=0 NormalZ=1 AngleXU=0 Radius=5.54746
  constraints (52):
    c: Coincident(g0,g1)
    c: Coincident(g1,g2)
    c: Coincident(g2,g3)
    c: Coincident(g3,g4)
    c: Coincident(g4,g5)
    c: Coincident(g5,g6)
    c: Coincident(g6,g7)
    c: Coincident(g7,g8)
    c: Coincident(g8,g9)
    c: Coincident(g9,g10)
    c: Coincident(g10,g11)
    c: Coincident(g11,g12)
    c: Coincident(g12,g13)
    c: Coincident(g13,g14)
    c: Coincident(g14,g15)
    c: Coincident(g15,g16)
    c: Coincident(g16,g17)
    c: Coincident(g17,g18)
    c: Coincident(g18,g19)
    c: Coincident(g19,g20)
    c: Coincident(g20,g21)
    c: Coincident(g21,g22)
    c: Coincident(g22,g23)
    c: Coincident(g23,g0)
    c: Equal(g0, g1-g23) x23
    c: PointOnObject(g0,g24)
    c: PointOnObject(g1,g24)
    c: PointOnObject(g2,g24)
    c: PointOnObject(g3,g24)
    c: PointOnObject(g4,g24)
    c: PointOnObject(g5,g24)
    c: PointOnObject(g6,g24)
    c: PointOnObject(g7,g24)
    c: PointOnObject(g8,g24)
    c: PointOnObject(g9,g24)
    c: PointOnObject(g10,g24)
    c: PointOnObject(g11,g24)
    c: PointOnObject(g12,g24)
    c: PointOnObject(g13,g24)
    c: PointOnObject(g14,g24)
    c: PointOnObject(g15,g24)
    c: PointOnObject(g16,g24)
    c: PointOnObject(g17,g24)
    c: PointOnObject(g18,g24)
    c: PointOnObject(g19,g24)
    c: PointOnObject(g20,g24)
    c: PointOnObject(g21,g24)
    c: PointOnObject(g22,g24)
    c: PointOnObject(g23,g24)
    c: Coincident(g24,g-1)
    c: Horizontal(g23)
    c: DistanceX(g4,g17) = 11
FEATURE [Sketcher::SketchObject] Sketch425
  FullyConstrained = false
  MapMode = 5
  Support = -> [XY_Plane899]
  sketch-geometry (25):
    g0: LineSegment StartX=-0.789915 StartY=6 StartZ=0 EndX=-2.31591 EndY=5.59111 EndZ=0
    g1: LineSegment StartX=-2.31591 StartY=5.59111 StartZ=0 EndX=-3.68409 EndY=4.80119 EndZ=0
    g2: LineSegment StartX=-3.68409 StartY=4.80119 StartZ=0 EndX=-4.80119 EndY=3.68409 EndZ=0
    g3: LineSegment StartX=-4.80119 StartY=3.68409 StartZ=0 EndX=-5.59111 EndY=2.31591 EndZ=0
    g4: LineSegment StartX=-5.59111 StartY=2.31591 StartZ=0 EndX=-6 EndY=0.789915 EndZ=0
    g5: LineSegment StartX=-6 StartY=0.789915 StartZ=0 EndX=-6 EndY=-0.789915 EndZ=0
    g6: LineSegment StartX=-6 StartY=-0.789915 StartZ=0 EndX=-5.59111 EndY=-2.31591 EndZ=0
    g7: LineSegment StartX=-5.59111 StartY=-2.31591 StartZ=0 EndX=-4.80119 EndY=-3.68409 EndZ=0
    g8: LineSegment StartX=-4.80119 StartY=-3.68409 StartZ=0 EndX=-3.68409 EndY=-4.80119 EndZ=0
    g9: LineSegment StartX=-3.68409 StartY=-4.80119 StartZ=0 EndX=-2.31591 EndY=-5.59111 EndZ=0
    g10: LineSegment StartX=-2.31591 StartY=-5.59111 StartZ=0 EndX=-0.789915 EndY=-6 EndZ=0
    g11: LineSegment StartX=-0.789915 StartY=-6 StartZ=0 EndX=0.789915 EndY=-6 EndZ=0
    g12: LineSegment StartX=0.789915 StartY=-6 StartZ=0 EndX=2.31591 EndY=-5.59111 EndZ=0
    g13: LineSegment StartX=2.31591 StartY=-5.59111 StartZ=0 EndX=3.68409 EndY=-4.80119 EndZ=0
    g14: LineSegment StartX=3.68409 StartY=-4.80119 StartZ=0 EndX=4.80119 EndY=-3.68409 EndZ=0
    g15: LineSegment StartX=4.80119 StartY=-3.68409 StartZ=0 EndX=5.59111 EndY=-2.31591 EndZ=0
    g16: LineSegment StartX=5.59111 StartY=-2.31591 StartZ=0 EndX=6 EndY=-0.789915 EndZ=0
    g17: LineSegment StartX=6 StartY=-0.789915 StartZ=0 EndX=6 EndY=0.789915 EndZ=0
    g18: LineSegment StartX=6 StartY=0.789915 StartZ=0 EndX=5.59111 EndY=2.31591 EndZ=0
    g19: LineSegment StartX=5.59111 StartY=2.31591 StartZ=0 EndX=4.80119 EndY=3.68409 EndZ=0
    g20: LineSegment StartX=4.80119 StartY=3.68409 StartZ=0 EndX=3.68409 EndY=4.80119 EndZ=0
    g21: LineSegment StartX=3.68409 StartY=4.80119 StartZ=0 EndX=2.31591 EndY=5.59111 EndZ=0
    g22: LineSegment StartX=2.31591 StartY=5.59111 StartZ=0 EndX=0.789915 EndY=6 EndZ=0
    g23: LineSegment StartX=0.789915 StartY=6 StartZ=0 EndX=-0.789915 EndY=6 EndZ=0
    g24: Circle CenterX=0 CenterY=0 CenterZ=0 NormalX=0 NormalY=0 NormalZ=1 AngleXU=0 Radius=6.05177
  constraints (52):
    c: Coincident(g0,g1)
    c: Coincident(g1,g2)
    c: Coincident(g2,g3)
    c: Coincident(g3,g4)
    c: Coincident(g4,g5)
    c: Coincident(g5,g6)
    c: Coincident(g6,g7)
    c: Coincident(g7,g8)
    c: Coincident(g8,g9)
    c: Coincident(g9,g10)
    c: Coincident(g10,g11)
    c: Coincident(g11,g12)
    c: Coincident(g12,g13)
    c: Coincident(g13,g14)
    c: Coincident(g14,g15)
    c: Coincident(g15,g16)
    c: Coincident(g16,g17)
    c: Coincident(g17,g18)
    c: Coincident(g18,g19)
    c: Coincident(g19,g20)
    c: Coincident(g20,g21)
    c: Coincident(g21,g22)
    c: Coincident(g22,g23)
    c: Coincident(g23,g0)
    c: Equal(g0, g1-g23) x23
    c: PointOnObject(g0,g24)
    c: PointOnObject(g1,g24)
    c: PointOnObject(g2,g24)
    c: PointOnObject(g3,g24)
    c: PointOnObject(g4,g24)
    c: PointOnObject(g5,g24)
    c: PointOnObject(g6,g24)
    c: PointOnObject(g7,g24)
    c: PointOnObject(g8,g24)
    c: PointOnObject(g9,g24)
    c: PointOnObject(g10,g24)
    c: PointOnObject(g11,g24)
    c: PointOnObject(g12,g24)
    c: PointOnObject(g13,g24)
    c: PointOnObject(g14,g24)
    c: PointOnObject(g15,g24)
    c: PointOnObject(g16,g24)
    c: PointOnObject(g17,g24)
    c: PointOnObject(g18,g24)
    c: PointOnObject(g19,g24)
    c: PointOnObject(g20,g24)
    c: PointOnObject(g21,g24)
    c: PointOnObject(g22,g24)
    c: PointOnObject(g23,g24)
    c: Coincident(g24,g-1)
    c: Horizontal(g23)
    c: DistanceX(g4,g17) = 12
FEATURE [Sketcher::SketchObject] Sketch426
  AttachmentOffset = pos=(0,0,17) rot=(0,0,1;0rad)
  FullyConstrained = false
  MapMode = 5
  Placement = pos=(0,0,17) rot=(0,0,1;0rad)
  Support = -> [XY_Plane899]
  sketch-geometry (25):
    g0: LineSegment StartX=-4.65926 StartY=1.92993 StartZ=0 EndX=-5 EndY=0.658262 EndZ=0
    g1: LineSegment StartX=-5 StartY=0.658262 StartZ=0 EndX=-5 EndY=-0.658262 EndZ=0
    g2: LineSegment StartX=-5 StartY=-0.658262 StartZ=0 EndX=-4.65926 EndY=-1.92993 EndZ=0
    g3: LineSegment StartX=-4.65926 StartY=-1.92993 StartZ=0 EndX=-4.001 EndY=-3.07007 EndZ=0
    g4: LineSegment StartX=-4.001 StartY=-3.07007 StartZ=0 EndX=-3.07007 EndY=-4.001 EndZ=0
    g5: LineSegment StartX=-3.07007 StartY=-4.001 StartZ=0 EndX=-1.92993 EndY=-4.65926 EndZ=0
    g6: LineSegment StartX=-1.92993 StartY=-4.65926 StartZ=0 EndX=-0.658262 EndY=-5 EndZ=0
    g7: LineSegment StartX=-0.658262 StartY=-5 StartZ=0 EndX=0.658262 EndY=-5 EndZ=0
    g8: LineSegment StartX=0.658262 StartY=-5 StartZ=0 EndX=1.92993 EndY=-4.65926 EndZ=0
    g9: LineSegment StartX=1.92993 StartY=-4.65926 StartZ=0 EndX=3.07007 EndY=-4.001 EndZ=0
    g10: LineSegment StartX=3.07007 StartY=-4.001 StartZ=0 EndX=4.001 EndY=-3.07007 EndZ=0
    g11: LineSegment StartX=4.001 StartY=-3.07007 StartZ=0 EndX=4.65926 EndY=-1.92993 EndZ=0
    g12: LineSegment StartX=4.65926 StartY=-1.92993 StartZ=0 EndX=5 EndY=-0.658262 EndZ=0
    g13: LineSegment StartX=5 StartY=-0.658262 StartZ=0 EndX=5 EndY=0.658262 EndZ=0
    g14: LineSegment StartX=5 StartY=0.658262 StartZ=0 EndX=4.65926 EndY=1.92993 EndZ=0
    g15: LineSegment StartX=4.65926 StartY=1.92993 StartZ=0 EndX=4.001 EndY=3.07007 EndZ=0
    g16: LineSegment StartX=4.001 StartY=3.07007 StartZ=0 EndX=3.07007 EndY=4.001 EndZ=0
    g17: LineSegment StartX=3.07007 StartY=4.001 StartZ=0 EndX=1.92993 EndY=4.65926 EndZ=0
    g18: LineSegment StartX=1.92993 StartY=4.65926 StartZ=0 EndX=0.658262 EndY=5 EndZ=0
    g19: LineSegment StartX=0.658262 StartY=5 StartZ=0 EndX=-0.658262 EndY=5 EndZ=0
    g20: LineSegment StartX=-0.658262 StartY=5 StartZ=0 EndX=-1.92993 EndY=4.65926 EndZ=0
    g21: LineSegment StartX=-1.92993 StartY=4.65926 StartZ=0 EndX=-3.07007 EndY=4.001 EndZ=0
    g22: LineSegment StartX=-3.07007 StartY=4.001 StartZ=0 EndX=-4.001 EndY=3.07007 EndZ=0
    g23: LineSegment StartX=-4.001 StartY=3.07007 StartZ=0 EndX=-4.65926 EndY=1.92993 EndZ=0
    g24: Circle CenterX=0 CenterY=0 CenterZ=0 NormalX=0 NormalY=0 NormalZ=1 AngleXU=0 Radius=5.04314
  constraints (52):
    c: Coincident(g0,g1)
    c: Coincident(g1,g2)
    c: Coincident(g2,g3)
    c: Coincident(g3,g4)
    c: Coincident(g4,g5)
    c: Coincident(g5,g6)
    c: Coincident(g6,g7)
    c: Coincident(g7,g8)
    c: Coincident(g8,g9)
    c: Coincident(g9,g10)
    c: Coincident(g10,g11)
    c: Coincident(g11,g12)
    c: Coincident(g12,g13)
    c: Coincident(g13,g14)
    c: Coincident(g14,g15)
    c: Coincident(g15,g16)
    c: Coincident(g16,g17)
    c: Coincident(g17,g18)
    c: Coincident(g18,g19)
    c: Coincident(g19,g20)
    c: Coincident(g20,g21)
    c: Coincident(g21,g22)
    c: Coincident(g22,g23)
    c: Coincident(g23,g0)
    c: Equal(g0, g1-g23) x23
    c: PointOnObject(g0,g24)
    c: PointOnObject(g1,g24)
    c: PointOnObject(g2,g24)
    c: PointOnObject(g3,g24)
    c: PointOnObject(g4,g24)
    c: PointOnObject(g5,g24)
    c: PointOnObject(g6,g24)
    c: PointOnObject(g7,g24)
    c: PointOnObject(g8,g24)
    c: PointOnObject(g9,g24)
    c: PointOnObject(g10,g24)
    c: PointOnObject(g11,g24)
    c: PointOnObject(g12,g24)
    c: PointOnObject(g13,g24)
    c: PointOnObject(g14,g24)
    c: PointOnObject(g15,g24)
    c: PointOnObject(g16,g24)
    c: PointOnObject(g17,g24)
    c: PointOnObject(g18,g24)
    c: PointOnObject(g19,g24)
    c: PointOnObject(g20,g24)
    c: PointOnObject(g21,g24)
    c: PointOnObject(g22,g24)
    c: PointOnObject(g23,g24)
    c: Coincident(g24,g-1)
    c: Horizontal(g19)
    c: DistanceX(g0,g13) = 10
FEATURE [PartDesign::AdditiveLoft] AdditiveLoft044
  AllowMultiFace = false
  Closed = false
  Profile = -> Sketch425
  Refine = true
  Ruled = false
  Sections = -> [Sketch424,Sketch426]
FEATURE [Sketcher::SketchObject] Sketch409
  FullyConstrained = false
  MapMode = 5
  Placement = pos=(0,0,17) rot=(0,0,1;0rad)
  Support = -> [AdditiveLoft044]
  sketch-geometry (1):
    g0: Circle CenterX=0 CenterY=0 CenterZ=0 NormalX=0 NormalY=0 NormalZ=1 AngleXU=0 Radius=4.5
  constraints (2):
    c: Coincident(g0,g-1)
    c: Radius(g0) = 4.5
FEATURE [PartDesign::AdditiveLoft] AdditiveLoft045
  AllowMultiFace = false
  Closed = false
  Profile = -> Sketch417
  Refine = true
  Ruled = false
  Sections = -> [Sketch414,Sketch416]
FEATURE [Sketcher::SketchObject] Sketch403
  FullyConstrained = false
  MapMode = 5
  Placement = pos=(0,0,17) rot=(0,0,1;0rad)
  Support = -> [AdditiveLoft045]
  sketch-geometry (1):
    g0: Circle CenterX=0 CenterY=0 CenterZ=0 NormalX=0 NormalY=0 NormalZ=1 AngleXU=0 Radius=4.5
  constraints (2):
    c: Coincident(g0,g-1)
    c: Radius(g0) = 4.5
FEATURE [PartDesign::Pad] Pad077
  AllowMultiFace = false
  BaseFeature = -> AdditiveLoft045
  Direction = (1,1,1)
  Length = 0.7
  Length2 = 100
  Profile = -> Sketch403
  Refine = true
  Type = 0
FEATURE [Sketcher::SketchObject] Sketch410
  FullyConstrained = false
  MapMode = 5
  Placement = pos=(0,0,0) rot=(1,0,0;3.14159rad)
  Support = -> [Pad077]
  sketch-geometry (1):
    g0: Circle CenterX=0 CenterY=0 CenterZ=0 NormalX=0 NormalY=0 NormalZ=1 AngleXU=0 Radius=5
  constraints (2):
    c: Coincident(g0,g-1)
    c: Radius(g0) = 5
FEATURE [PartDesign::Pocket] Pocket076
  AllowMultiFace = false
  BaseFeature = -> Pad077
  Direction = (1,1,1)
  Length = 1
  Length2 = 100
  Profile = -> Sketch410
  Refine = true
  Type = 0
FEATURE [Sketcher::SketchObject] Sketch404
  FullyConstrained = false
  MapMode = 5
  Placement = pos=(0,0,1) rot=(1,0,0;3.14159rad)
  Support = -> [Pocket076]
  sketch-geometry (1):
    g0: Circle CenterX=0 CenterY=0 CenterZ=0 NormalX=0 NormalY=0 NormalZ=1 AngleXU=0 Radius=4.65
  constraints (2):
    c: Coincident(g0,g-1)
    c: Radius(g0) = 4.65
FEATURE [PartDesign::Pocket] Pocket071
  AllowMultiFace = false
  BaseFeature = -> Pocket076
  Direction = (1,1,1)
  Length = 1
  Length2 = 100
  Profile = -> Sketch404
  Refine = true
  Type = 0
FEATURE [Sketcher::SketchObject] Sketch405
  FullyConstrained = false
  MapMode = 5
  Placement = pos=(0,0,2) rot=(1,0,0;3.14159rad)
  Support = -> [Pocket071]
  sketch-geometry (2):
    g0: ArcOfCircle CenterX=0 CenterY=0 CenterZ=0 NormalX=0 NormalY=0 NormalZ=1 AngleXU=0 Radius=3 StartAngle=2.19024 EndAngle=7.23453
    g1: LineSegment StartX=-1.74176 StartY=2.4426 StartZ=0 EndX=1.74176 EndY=2.4426 EndZ=0
  constraints (5):
    c: Coincident(g0,g-1)
    c: Coincident(g1,g0)
    c: Coincident(g1,g0)
    c: Horizontal(g1)
    c: Radius(g0) = 3
FEATURE [PartDesign::Pocket] Pocket072
  AllowMultiFace = false
  BaseFeature = -> Pocket071
  Direction = (1,1,1)
  Length = 8
  Length2 = 100
  Profile = -> Sketch405
  Refine = true
  Type = 0
FEATURE [PartDesign::Chamfer] Chamfer062
  Angle = 45
  Base = -> Pocket072 [Edge82,Edge83]
  BaseFeature = -> Pocket072
  ChamferType = 0
  FlipDirection = false
  Size = 1.4
  Size2 = 1
  SupportTransform = false
  UseAllEdges = false
FEATURE [PartDesign::Chamfer] Chamfer064
  Angle = 45
  Base = -> Chamfer062 [Edge8]
  BaseFeature = -> Chamfer062
  ChamferType = 0
  FlipDirection = false
  Size = 0.3
  Size2 = 1
  SupportTransform = false
  UseAllEdges = false
FEATURE [PartDesign::Fillet] Fillet034
  Base = -> Chamfer064 [Edge93,Face36]
  BaseFeature = -> Chamfer064
  Radius = 0.1
  SupportTransform = false
  UseAllEdges = false
FEATURE [PartDesign::Body] Body161
  Group = -> [Sketch417,Sketch414,Sketch416,AdditiveLoft045,Sketch403,Pad077,Sketch410,Pocket076,Sketch404,Pocket071,Sketch405,Pocket072,Chamfer062,Chamfer064,Fillet034]
  Origin = -> Origin920
  Tip = -> Fillet034
FEATURE [App::Part] Part143  label="Cap036"
  Group = -> [Body161]
  Origin = -> Origin906
  Placement = pos=(40.005,40.005,0) rot=(0,0,1;0rad)
  expr: .Placement.Base.x = 40.005
  expr: .Placement.Base.y = 40.005
FEATURE [PartDesign::Pocket] Pocket081
  AllowMultiFace = false
  BaseFeature = -> Pocket070
  Direction = (1,1,1)
  Length = 8
  Length2 = 100
  Profile = -> Sketch407
  Refine = true
  Type = 0
FEATURE [PartDesign::Chamfer] Chamfer057
  Angle = 45
  Base = -> Pocket081 [Edge82,Edge83]
  BaseFeature = -> Pocket081
  ChamferType = 0
  FlipDirection = false
  Size = 1.4
  Size2 = 1
  SupportTransform = false
  UseAllEdges = false
FEATURE [PartDesign::Chamfer] Chamfer063
  Angle = 45
  Base = -> Chamfer057 [Edge8]
  BaseFeature = -> Chamfer057
  ChamferType = 0
  FlipDirection = false
  Size = 0.3
  Size2 = 1
  SupportTransform = false
  UseAllEdges = false
FEATURE [PartDesign::Fillet] Fillet033
  Base = -> Chamfer063 [Edge93,Face36]
  BaseFeature = -> Chamfer063
  Radius = 0.1
  SupportTransform = false
  UseAllEdges = false
FEATURE [PartDesign::Body] Body162
  Group = -> [Sketch423,Sketch413,Sketch421,AdditiveLoft037,Sketch415,Pad076,Sketch408,Pocket073,Sketch418,Pocket070,Sketch407,Pocket081,Chamfer057,Chamfer063,Fillet033]
  Origin = -> Origin910
  Tip = -> Fillet033
FEATURE [App::Part] Part145  label="Cap038"
  Group = -> [Body162]
  Origin = -> Origin919
  Placement = pos=(-40.005,13.335,0) rot=(0,0,1;0rad)
  expr: .Placement.Base.x = -40.005
  expr: .Placement.Base.y = 13.335
FEATURE [PartDesign::Pad] Pad082
  AllowMultiFace = false
  BaseFeature = -> AdditiveLoft044
  Direction = (1,1,1)
  Length = 0.7
  Length2 = 100
  Profile = -> Sketch409
  Refine = true
  Type = 0
FEATURE [Sketcher::SketchObject] Sketch420
  FullyConstrained = false
  MapMode = 5
  Placement = pos=(0,0,0) rot=(1,0,0;3.14159rad)
  Support = -> [Pad082]
  sketch-geometry (1):
    g0: Circle CenterX=0 CenterY=0 CenterZ=0 NormalX=0 NormalY=0 NormalZ=1 AngleXU=0 Radius=5
  constraints (2):
    c: Coincident(g0,g-1)
    c: Radius(g0) = 5
FEATURE [PartDesign::Pocket] Pocket080
  AllowMultiFace = false
  BaseFeature = -> Pad082
  Direction = (1,1,1)
  Length = 1
  Length2 = 100
  Profile = -> Sketch420
  Refine = true
  Type = 0
FEATURE [Sketcher::SketchObject] Sketch412
  FullyConstrained = false
  MapMode = 5
  Placement = pos=(0,0,1) rot=(1,0,0;3.14159rad)
  Support = -> [Pocket080]
  sketch-geometry (1):
    g0: Circle CenterX=0 CenterY=0 CenterZ=0 NormalX=0 NormalY=0 NormalZ=1 AngleXU=0 Radius=4.65
  constraints (2):
    c: Coincident(g0,g-1)
    c: Radius(g0) = 4.65
FEATURE [PartDesign::Pocket] Pocket084
  AllowMultiFace = false
  BaseFeature = -> Pocket080
  Direction = (1,1,1)
  Length = 1
  Length2 = 100
  Profile = -> Sketch412
  Refine = true
  Type = 0
FEATURE [Sketcher::SketchObject] Sketch419
  FullyConstrained = false
  MapMode = 5
  Placement = pos=(0,0,2) rot=(1,0,0;3.14159rad)
  Support = -> [Pocket084]
  sketch-geometry (2):
    g0: ArcOfCircle CenterX=0 CenterY=0 CenterZ=0 NormalX=0 NormalY=0 NormalZ=1 AngleXU=0 Radius=3 StartAngle=2.19024 EndAngle=7.23453
    g1: LineSegment StartX=-1.74176 StartY=2.4426 StartZ=0 EndX=1.74176 EndY=2.4426 EndZ=0
  constraints (5):
    c: Coincident(g0,g-1)
    c: Coincident(g1,g0)
    c: Coincident(g1,g0)
    c: Horizontal(g1)
    c: Radius(g0) = 3
FEATURE [PartDesign::Pocket] Pocket077
  AllowMultiFace = false
  BaseFeature = -> Pocket084
  Direction = (1,1,1)
  Length = 8
  Length2 = 100
  Profile = -> Sketch419
  Refine = true
  Type = 0
FEATURE [PartDesign::Chamfer] Chamfer066
  Angle = 45
  Base = -> Pocket077 [Edge82,Edge83]
  BaseFeature = -> Pocket077
  ChamferType = 0
  FlipDirection = false
  Size = 1.4
  Size2 = 1
  SupportTransform = false
  UseAllEdges = false
FEATURE [PartDesign::Chamfer] Chamfer058
  Angle = 45
  Base = -> Chamfer066 [Edge8]
  BaseFeature = -> Chamfer066
  ChamferType = 0
  FlipDirection = false
  Size = 0.3
  Size2 = 1
  SupportTransform = false
  UseAllEdges = false
FEATURE [PartDesign::Fillet] Fillet031
  Base = -> Chamfer058 [Edge93,Face36]
  BaseFeature = -> Chamfer058
  Radius = 0.1
  SupportTransform = false
  UseAllEdges = false
FEATURE [PartDesign::Body] Body167
  Group = -> [Sketch425,Sketch424,Sketch426,AdditiveLoft044,Sketch409,Pad082,Sketch420,Pocket080,Sketch412,Pocket084,Sketch419,Pocket077,Chamfer066,Chamfer058,Fillet031]
  Origin = -> Origin907
  Tip = -> Fillet031
FEATURE [App::Part] Part146  label="Cap039"
  Group = -> [Body167]
  Origin = -> Origin912
  Placement = pos=(-13.335,13.335,0) rot=(0,0,1;0rad)
  expr: .Placement.Base.x = -13.335
  expr: .Placement.Base.y = 13.335
FEATURE [Sketcher::SketchObject] Sketch431
  FullyConstrained = false
  MapMode = 5
  Support = -> [XY_Plane902]
  sketch-geometry (25):
    g0: LineSegment StartX=-0.789915 StartY=6 StartZ=0 EndX=-2.31591 EndY=5.59111 EndZ=0
    g1: LineSegment StartX=-2.31591 StartY=5.59111 StartZ=0 EndX=-3.68409 EndY=4.80119 EndZ=0
    g2: LineSegment StartX=-3.68409 StartY=4.80119 StartZ=0 EndX=-4.80119 EndY=3.68409 EndZ=0
    g3: LineSegment StartX=-4.80119 StartY=3.68409 StartZ=0 EndX=-5.59111 EndY=2.31591 EndZ=0
    g4: LineSegment StartX=-5.59111 StartY=2.31591 StartZ=0 EndX=-6 EndY=0.789915 EndZ=0
    g5: LineSegment StartX=-6 StartY=0.789915 StartZ=0 EndX=-6 EndY=-0.789915 EndZ=0
    g6: LineSegment StartX=-6 StartY=-0.789915 StartZ=0 EndX=-5.59111 EndY=-2.31591 EndZ=0
    g7: LineSegment StartX=-5.59111 StartY=-2.31591 StartZ=0 EndX=-4.80119 EndY=-3.68409 EndZ=0
    g8: LineSegment StartX=-4.80119 StartY=-3.68409 StartZ=0 EndX=-3.68409 EndY=-4.80119 EndZ=0
    g9: LineSegment StartX=-3.68409 StartY=-4.80119 StartZ=0 EndX=-2.31591 EndY=-5.59111 EndZ=0
    g10: LineSegment StartX=-2.31591 StartY=-5.59111 StartZ=0 EndX=-0.789915 EndY=-6 EndZ=0
    g11: LineSegment StartX=-0.789915 StartY=-6 StartZ=0 EndX=0.789915 EndY=-6 EndZ=0
    g12: LineSegment StartX=0.789915 StartY=-6 StartZ=0 EndX=2.31591 EndY=-5.59111 EndZ=0
    g13: LineSegment StartX=2.31591 StartY=-5.59111 StartZ=0 EndX=3.68409 EndY=-4.80119 EndZ=0
    g14: LineSegment StartX=3.68409 StartY=-4.80119 StartZ=0 EndX=4.80119 EndY=-3.68409 EndZ=0
    g15: LineSegment StartX=4.80119 StartY=-3.68409 StartZ=0 EndX=5.59111 EndY=-2.31591 EndZ=0
    g16: LineSegment StartX=5.59111 StartY=-2.31591 StartZ=0 EndX=6 EndY=-0.789915 EndZ=0
    g17: LineSegment StartX=6 StartY=-0.789915 StartZ=0 EndX=6 EndY=0.789915 EndZ=0
    g18: LineSegment StartX=6 StartY=0.789915 StartZ=0 EndX=5.59111 EndY=2.31591 EndZ=0
    g19: LineSegment StartX=5.59111 StartY=2.31591 StartZ=0 EndX=4.80119 EndY=3.68409 EndZ=0
    g20: LineSegment StartX=4.80119 StartY=3.68409 StartZ=0 EndX=3.68409 EndY=4.80119 EndZ=0
    g21: LineSegment StartX=3.68409 StartY=4.80119 StartZ=0 EndX=2.31591 EndY=5.59111 EndZ=0
    g22: LineSegment StartX=2.31591 StartY=5.59111 StartZ=0 EndX=0.789915 EndY=6 EndZ=0
    g23: LineSegment StartX=0.789915 StartY=6 StartZ=0 EndX=-0.789915 EndY=6 EndZ=0
    g24: Circle CenterX=0 CenterY=0 CenterZ=0 NormalX=0 NormalY=0 NormalZ=1 AngleXU=0 Radius=6.05177
  constraints (52):
    c: Coincident(g0,g1)
    c: Coincident(g1,g2)
    c: Coincident(g2,g3)
    c: Coincident(g3,g4)
    c: Coincident(g4,g5)
    c: Coincident(g5,g6)
    c: Coincident(g6,g7)
    c: Coincident(g7,g8)
    c: Coincident(g8,g9)
    c: Coincident(g9,g10)
    c: Coincident(g10,g11)
    c: Coincident(g11,g12)
    c: Coincident(g12,g13)
    c: Coincident(g13,g14)
    c: Coincident(g14,g15)
    c: Coincident(g15,g16)
    c: Coincident(g16,g17)
    c: Coincident(g17,g18)
    c: Coincident(g18,g19)
    c: Coincident(g19,g20)
    c: Coincident(g20,g21)
    c: Coincident(g21,g22)
    c: Coincident(g22,g23)
    c: Coincident(g23,g0)
    c: Equal(g0, g1-g23) x23
    c: PointOnObject(g0,g24)
    c: PointOnObject(g1,g24)
    c: PointOnObject(g2,g24)
    c: PointOnObject(g3,g24)
    c: PointOnObject(g4,g24)
    c: PointOnObject(g5,g24)
    c: PointOnObject(g6,g24)
    c: PointOnObject(g7,g24)
    c: PointOnObject(g8,g24)
    c: PointOnObject(g9,g24)
    c: PointOnObject(g10,g24)
    c: PointOnObject(g11,g24)
    c: PointOnObject(g12,g24)
    c: PointOnObject(g13,g24)
    c: PointOnObject(g14,g24)
    c: PointOnObject(g15,g24)
    c: PointOnObject(g16,g24)
    c: PointOnObject(g17,g24)
    c: PointOnObject(g18,g24)
    c: PointOnObject(g19,g24)
    c: PointOnObject(g20,g24)
    c: PointOnObject(g21,g24)
    c: PointOnObject(g22,g24)
    c: PointOnObject(g23,g24)
    c: Coincident(g24,g-1)
    c: Horizontal(g23)
    c: DistanceX(g4,g17) = 12
FEATURE [Sketcher::SketchObject] Sketch437
  FullyConstrained = false
  MapMode = 5
  Support = -> [XY_Plane896]
  sketch-geometry (25):
    g0: LineSegment StartX=-0.789915 StartY=6 StartZ=0 EndX=-2.31591 EndY=5.59111 EndZ=0
    g1: LineSegment StartX=-2.31591 StartY=5.59111 StartZ=0 EndX=-3.68409 EndY=4.80119 EndZ=0
    g2: LineSegment StartX=-3.68409 StartY=4.80119 StartZ=0 EndX=-4.80119 EndY=3.68409 EndZ=0
    g3: LineSegment StartX=-4.80119 StartY=3.68409 StartZ=0 EndX=-5.59111 EndY=2.31591 EndZ=0
    g4: LineSegment StartX=-5.59111 StartY=2.31591 StartZ=0 EndX=-6 EndY=0.789915 EndZ=0
    g5: LineSegment StartX=-6 StartY=0.789915 StartZ=0 EndX=-6 EndY=-0.789915 EndZ=0
    g6: LineSegment StartX=-6 StartY=-0.789915 StartZ=0 EndX=-5.59111 EndY=-2.31591 EndZ=0
    g7: LineSegment StartX=-5.59111 StartY=-2.31591 StartZ=0 EndX=-4.80119 EndY=-3.68409 EndZ=0
    g8: LineSegment StartX=-4.80119 StartY=-3.68409 StartZ=0 EndX=-3.68409 EndY=-4.80119 EndZ=0
    g9: LineSegment StartX=-3.68409 StartY=-4.80119 StartZ=0 EndX=-2.31591 EndY=-5.59111 EndZ=0
    g10: LineSegment StartX=-2.31591 StartY=-5.59111 StartZ=0 EndX=-0.789915 EndY=-6 EndZ=0
    g11: LineSegment StartX=-0.789915 StartY=-6 StartZ=0 EndX=0.789915 EndY=-6 EndZ=0
    g12: LineSegment StartX=0.789915 StartY=-6 StartZ=0 EndX=2.31591 EndY=-5.59111 EndZ=0
    g13: LineSegment StartX=2.31591 StartY=-5.59111 StartZ=0 EndX=3.68409 EndY=-4.80119 EndZ=0
    g14: LineSegment StartX=3.68409 StartY=-4.80119 StartZ=0 EndX=4.80119 EndY=-3.68409 EndZ=0
    g15: LineSegment StartX=4.80119 StartY=-3.68409 StartZ=0 EndX=5.59111 EndY=-2.31591 EndZ=0
    g16: LineSegment StartX=5.59111 StartY=-2.31591 StartZ=0 EndX=6 EndY=-0.789915 EndZ=0
    g17: LineSegment StartX=6 StartY=-0.789915 StartZ=0 EndX=6 EndY=0.789915 EndZ=0
    g18: LineSegment StartX=6 StartY=0.789915 StartZ=0 EndX=5.59111 EndY=2.31591 EndZ=0
    g19: LineSegment StartX=5.59111 StartY=2.31591 StartZ=0 EndX=4.80119 EndY=3.68409 EndZ=0
    g20: LineSegment StartX=4.80119 StartY=3.68409 StartZ=0 EndX=3.68409 EndY=4.80119 EndZ=0
    g21: LineSegment StartX=3.68409 StartY=4.80119 StartZ=0 EndX=2.31591 EndY=5.59111 EndZ=0
    g22: LineSegment StartX=2.31591 StartY=5.59111 StartZ=0 EndX=0.789915 EndY=6 EndZ=0
    g23: LineSegment StartX=0.789915 StartY=6 StartZ=0 EndX=-0.789915 EndY=6 EndZ=0
    g24: Circle CenterX=0 CenterY=0 CenterZ=0 NormalX=0 NormalY=0 NormalZ=1 AngleXU=0 Radius=6.05177
  constraints (52):
    c: Coincident(g0,g1)
    c: Coincident(g1,g2)
    c: Coincident(g2,g3)
    c: Coincident(g3,g4)
    c: Coincident(g4,g5)
    c: Coincident(g5,g6)
    c: Coincident(g6,g7)
    c: Coincident(g7,g8)
    c: Coincident(g8,g9)
    c: Coincident(g9,g10)
    c: Coincident(g10,g11)
    c: Coincident(g11,g12)
    c: Coincident(g12,g13)
    c: Coincident(g13,g14)
    c: Coincident(g14,g15)
    c: Coincident(g15,g16)
    c: Coincident(g16,g17)
    c: Coincident(g17,g18)
    c: Coincident(g18,g19)
    c: Coincident(g19,g20)
    c: Coincident(g20,g21)
    c: Coincident(g21,g22)
    c: Coincident(g22,g23)
    c: Coincident(g23,g0)
    c: Equal(g0, g1-g23) x23
    c: PointOnObject(g0,g24)
    c: PointOnObject(g1,g24)
    c: PointOnObject(g2,g24)
    c: PointOnObject(g3,g24)
    c: PointOnObject(g4,g24)
    c: PointOnObject(g5,g24)
    c: PointOnObject(g6,g24)
    c: PointOnObject(g7,g24)
    c: PointOnObject(g8,g24)
    c: PointOnObject(g9,g24)
    c: PointOnObject(g10,g24)
    c: PointOnObject(g11,g24)
    c: PointOnObject(g12,g24)
    c: PointOnObject(g13,g24)
    c: PointOnObject(g14,g24)
    c: PointOnObject(g15,g24)
    c: PointOnObject(g16,g24)
    c: PointOnObject(g17,g24)
    c: PointOnObject(g18,g24)
    c: PointOnObject(g19,g24)
    c: PointOnObject(g20,g24)
    c: PointOnObject(g21,g24)
    c: PointOnObject(g22,g24)
    c: PointOnObject(g23,g24)
    c: Coincident(g24,g-1)
    c: Horizontal(g23)
    c: DistanceX(g4,g17) = 12
FEATURE [Sketcher::SketchObject] Sketch439
  AttachmentOffset = pos=(0,0,7) rot=(0,0,1;0rad)
  FullyConstrained = false
  MapMode = 5
  Placement = pos=(0,0,7) rot=(0,0,1;0rad)
  Support = -> [XY_Plane896]
  sketch-geometry (25):
    g0: LineSegment StartX=-0.724089 StartY=5.5 StartZ=0 EndX=-2.12292 EndY=5.12518 EndZ=0
    g1: LineSegment StartX=-2.12292 StartY=5.12518 StartZ=0 EndX=-3.37708 EndY=4.4011 EndZ=0
    g2: LineSegment StartX=-3.37708 StartY=4.4011 StartZ=0 EndX=-4.4011 EndY=3.37708 EndZ=0
    g3: LineSegment StartX=-4.4011 StartY=3.37708 StartZ=0 EndX=-5.12518 EndY=2.12292 EndZ=0
    g4: LineSegment StartX=-5.12518 StartY=2.12292 StartZ=0 EndX=-5.5 EndY=0.724089 EndZ=0
    g5: LineSegment StartX=-5.5 StartY=0.724089 StartZ=0 EndX=-5.5 EndY=-0.724089 EndZ=0
    g6: LineSegment StartX=-5.5 StartY=-0.724089 StartZ=0 EndX=-5.12518 EndY=-2.12292 EndZ=0
    g7: LineSegment StartX=-5.12518 StartY=-2.12292 StartZ=0 EndX=-4.4011 EndY=-3.37708 EndZ=0
    g8: LineSegment StartX=-4.4011 StartY=-3.37708 StartZ=0 EndX=-3.37708 EndY=-4.4011 EndZ=0
    g9: LineSegment StartX=-3.37708 StartY=-4.4011 StartZ=0 EndX=-2.12292 EndY=-5.12518 EndZ=0
    g10: LineSegment StartX=-2.12292 StartY=-5.12518 StartZ=0 EndX=-0.724089 EndY=-5.5 EndZ=0
    g11: LineSegment StartX=-0.724089 StartY=-5.5 StartZ=0 EndX=0.724089 EndY=-5.5 EndZ=0
    g12: LineSegment StartX=0.724089 StartY=-5.5 StartZ=0 EndX=2.12292 EndY=-5.12518 EndZ=0
    g13: LineSegment StartX=2.12292 StartY=-5.12518 StartZ=0 EndX=3.37708 EndY=-4.4011 EndZ=0
    g14: LineSegment StartX=3.37708 StartY=-4.4011 StartZ=0 EndX=4.4011 EndY=-3.37708 EndZ=0
    g15: LineSegment StartX=4.4011 StartY=-3.37708 StartZ=0 EndX=5.12518 EndY=-2.12292 EndZ=0
    g16: LineSegment StartX=5.12518 StartY=-2.12292 StartZ=0 EndX=5.5 EndY=-0.724089 EndZ=0
    g17: LineSegment StartX=5.5 StartY=-0.724089 StartZ=0 EndX=5.5 EndY=0.724089 EndZ=0
    g18: LineSegment StartX=5.5 StartY=0.724089 StartZ=0 EndX=5.12518 EndY=2.12292 EndZ=0
    g19: LineSegment StartX=5.12518 StartY=2.12292 StartZ=0 EndX=4.4011 EndY=3.37708 EndZ=0
    g20: LineSegment StartX=4.4011 StartY=3.37708 StartZ=0 EndX=3.37708 EndY=4.4011 EndZ=0
    g21: LineSegment StartX=3.37708 StartY=4.4011 StartZ=0 EndX=2.12292 EndY=5.12518 EndZ=0
    g22: LineSegment StartX=2.12292 StartY=5.12518 StartZ=0 EndX=0.724089 EndY=5.5 EndZ=0
    g23: LineSegment StartX=0.724089 StartY=5.5 StartZ=0 EndX=-0.724089 EndY=5.5 EndZ=0
    g24: Circle CenterX=0 CenterY=0 CenterZ=0 NormalX=0 NormalY=0 NormalZ=1 AngleXU=0 Radius=5.54746
  constraints (52):
    c: Coincident(g0,g1)
    c: Coincident(g1,g2)
    c: Coincident(g2,g3)
    c: Coincident(g3,g4)
    c: Coincident(g4,g5)
    c: Coincident(g5,g6)
    c: Coincident(g6,g7)
    c: Coincident(g7,g8)
    c: Coincident(g8,g9)
    c: Coincident(g9,g10)
    c: Coincident(g10,g11)
    c: Coincident(g11,g12)
    c: Coincident(g12,g13)
    c: Coincident(g13,g14)
    c: Coincident(g14,g15)
    c: Coincident(g15,g16)
    c: Coincident(g16,g17)
    c: Coincident(g17,g18)
    c: Coincident(g18,g19)
    c: Coincident(g19,g20)
    c: Coincident(g20,g21)
    c: Coincident(g21,g22)
    c: Coincident(g22,g23)
    c: Coincident(g23,g0)
    c: Equal(g0, g1-g23) x23
    c: PointOnObject(g0,g24)
    c: PointOnObject(g1,g24)
    c: PointOnObject(g2,g24)
    c: PointOnObject(g3,g24)
    c: PointOnObject(g4,g24)
    c: PointOnObject(g5,g24)
    c: PointOnObject(g6,g24)
    c: PointOnObject(g7,g24)
    c: PointOnObject(g8,g24)
    c: PointOnObject(g9,g24)
    c: PointOnObject(g10,g24)
    c: PointOnObject(g11,g24)
    c: PointOnObject(g12,g24)
    c: PointOnObject(g13,g24)
    c: PointOnObject(g14,g24)
    c: PointOnObject(g15,g24)
    c: PointOnObject(g16,g24)
    c: PointOnObject(g17,g24)
    c: PointOnObject(g18,g24)
    c: PointOnObject(g19,g24)
    c: PointOnObject(g20,g24)
    c: PointOnObject(g21,g24)
    c: PointOnObject(g22,g24)
    c: PointOnObject(g23,g24)
    c: Coincident(g24,g-1)
    c: Horizontal(g23)
    c: DistanceX(g4,g17) = 11
FEATURE [Sketcher::SketchObject] Sketch440
  AttachmentOffset = pos=(0,0,17) rot=(0,0,1;0rad)
  FullyConstrained = false
  MapMode = 5
  Placement = pos=(0,0,17) rot=(0,0,1;0rad)
  Support = -> [XY_Plane896]
  sketch-geometry (25):
    g0: LineSegment StartX=-4.65926 StartY=1.92993 StartZ=0 EndX=-5 EndY=0.658262 EndZ=0
    g1: LineSegment StartX=-5 StartY=0.658262 StartZ=0 EndX=-5 EndY=-0.658262 EndZ=0
    g2: LineSegment StartX=-5 StartY=-0.658262 StartZ=0 EndX=-4.65926 EndY=-1.92993 EndZ=0
    g3: LineSegment StartX=-4.65926 StartY=-1.92993 StartZ=0 EndX=-4.001 EndY=-3.07007 EndZ=0
    g4: LineSegment StartX=-4.001 StartY=-3.07007 StartZ=0 EndX=-3.07007 EndY=-4.001 EndZ=0
    g5: LineSegment StartX=-3.07007 StartY=-4.001 StartZ=0 EndX=-1.92993 EndY=-4.65926 EndZ=0
    g6: LineSegment StartX=-1.92993 StartY=-4.65926 StartZ=0 EndX=-0.658262 EndY=-5 EndZ=0
    g7: LineSegment StartX=-0.658262 StartY=-5 StartZ=0 EndX=0.658262 EndY=-5 EndZ=0
    g8: LineSegment StartX=0.658262 StartY=-5 StartZ=0 EndX=1.92993 EndY=-4.65926 EndZ=0
    g9: LineSegment StartX=1.92993 StartY=-4.65926 StartZ=0 EndX=3.07007 EndY=-4.001 EndZ=0
    g10: LineSegment StartX=3.07007 StartY=-4.001 StartZ=0 EndX=4.001 EndY=-3.07007 EndZ=0
    g11: LineSegment StartX=4.001 StartY=-3.07007 StartZ=0 EndX=4.65926 EndY=-1.92993 EndZ=0
    g12: LineSegment StartX=4.65926 StartY=-1.92993 StartZ=0 EndX=5 EndY=-0.658262 EndZ=0
    g13: LineSegment StartX=5 StartY=-0.658262 StartZ=0 EndX=5 EndY=0.658262 EndZ=0
    g14: LineSegment StartX=5 StartY=0.658262 StartZ=0 EndX=4.65926 EndY=1.92993 EndZ=0
    g15: LineSegment StartX=4.65926 StartY=1.92993 StartZ=0 EndX=4.001 EndY=3.07007 EndZ=0
    g16: LineSegment StartX=4.001 StartY=3.07007 StartZ=0 EndX=3.07007 EndY=4.001 EndZ=0
    g17: LineSegment StartX=3.07007 StartY=4.001 StartZ=0 EndX=1.92993 EndY=4.65926 EndZ=0
    g18: LineSegment StartX=1.92993 StartY=4.65926 StartZ=0 EndX=0.658262 EndY=5 EndZ=0
    g19: LineSegment StartX=0.658262 StartY=5 StartZ=0 EndX=-0.658262 EndY=5 EndZ=0
    g20: LineSegment StartX=-0.658262 StartY=5 StartZ=0 EndX=-1.92993 EndY=4.65926 EndZ=0
    g21: LineSegment StartX=-1.92993 StartY=4.65926 StartZ=0 EndX=-3.07007 EndY=4.001 EndZ=0
    g22: LineSegment StartX=-3.07007 StartY=4.001 StartZ=0 EndX=-4.001 EndY=3.07007 EndZ=0
    g23: LineSegment StartX=-4.001 StartY=3.07007 StartZ=0 EndX=-4.65926 EndY=1.92993 EndZ=0
    g24: Circle CenterX=0 CenterY=0 CenterZ=0 NormalX=0 NormalY=0 NormalZ=1 AngleXU=0 Radius=5.04314
  constraints (52):
    c: Coincident(g0,g1)
    c: Coincident(g1,g2)
    c: Coincident(g2,g3)
    c: Coincident(g3,g4)
    c: Coincident(g4,g5)
    c: Coincident(g5,g6)
    c: Coincident(g6,g7)
    c: Coincident(g7,g8)
    c: Coincident(g8,g9)
    c: Coincident(g9,g10)
    c: Coincident(g10,g11)
    c: Coincident(g11,g12)
    c: Coincident(g12,g13)
    c: Coincident(g13,g14)
    c: Coincident(g14,g15)
    c: Coincident(g15,g16)
    c: Coincident(g16,g17)
    c: Coincident(g17,g18)
    c: Coincident(g18,g19)
    c: Coincident(g19,g20)
    c: Coincident(g20,g21)
    c: Coincident(g21,g22)
    c: Coincident(g22,g23)
    c: Coincident(g23,g0)
    c: Equal(g0, g1-g23) x23
    c: PointOnObject(g0,g24)
    c: PointOnObject(g1,g24)
    c: PointOnObject(g2,g24)
    c: PointOnObject(g3,g24)
    c: PointOnObject(g4,g24)
    c: PointOnObject(g5,g24)
    c: PointOnObject(g6,g24)
    c: PointOnObject(g7,g24)
    c: PointOnObject(g8,g24)
    c: PointOnObject(g9,g24)
    c: PointOnObject(g10,g24)
    c: PointOnObject(g11,g24)
    c: PointOnObject(g12,g24)
    c: PointOnObject(g13,g24)
    c: PointOnObject(g14,g24)
    c: PointOnObject(g15,g24)
    c: PointOnObject(g16,g24)
    c: PointOnObject(g17,g24)
    c: PointOnObject(g18,g24)
    c: PointOnObject(g19,g24)
    c: PointOnObject(g20,g24)
    c: PointOnObject(g21,g24)
    c: PointOnObject(g22,g24)
    c: PointOnObject(g23,g24)
    c: Coincident(g24,g-1)
    c: Horizontal(g19)
    c: DistanceX(g0,g13) = 10
FEATURE [PartDesign::AdditiveLoft] AdditiveLoft046
  AllowMultiFace = false
  Closed = false
  Profile = -> Sketch437
  Refine = true
  Ruled = false
  Sections = -> [Sketch439,Sketch440]
FEATURE [Sketcher::SketchObject] Sketch436
  FullyConstrained = false
  MapMode = 5
  Placement = pos=(0,0,17) rot=(0,0,1;0rad)
  Support = -> [AdditiveLoft046]
  sketch-geometry (1):
    g0: Circle CenterX=0 CenterY=0 CenterZ=0 NormalX=0 NormalY=0 NormalZ=1 AngleXU=0 Radius=4.5
  constraints (2):
    c: Coincident(g0,g-1)
    c: Radius(g0) = 4.5
FEATURE [PartDesign::Pad] Pad078
  AllowMultiFace = false
  BaseFeature = -> AdditiveLoft046
  Direction = (1,1,1)
  Length = 0.7
  Length2 = 100
  Profile = -> Sketch436
  Refine = true
  Type = 0
FEATURE [Sketcher::SketchObject] Sketch427
  FullyConstrained = false
  MapMode = 5
  Placement = pos=(0,0,0) rot=(1,0,0;3.14159rad)
  Support = -> [Pad078]
  sketch-geometry (1):
    g0: Circle CenterX=0 CenterY=0 CenterZ=0 NormalX=0 NormalY=0 NormalZ=1 AngleXU=0 Radius=5
  constraints (2):
    c: Coincident(g0,g-1)
    c: Radius(g0) = 5
FEATURE [PartDesign::Pocket] Pocket078
  AllowMultiFace = false
  BaseFeature = -> Pad078
  Direction = (1,1,1)
  Length = 1
  Length2 = 100
  Profile = -> Sketch427
  Refine = true
  Type = 0
FEATURE [Sketcher::SketchObject] Sketch435
  FullyConstrained = false
  MapMode = 5
  Placement = pos=(0,0,1) rot=(1,0,0;3.14159rad)
  Support = -> [Pocket078]
  sketch-geometry (1):
    g0: Circle CenterX=0 CenterY=0 CenterZ=0 NormalX=0 NormalY=0 NormalZ=1 AngleXU=0 Radius=4.65
  constraints (2):
    c: Coincident(g0,g-1)
    c: Radius(g0) = 4.65
FEATURE [PartDesign::Pocket] Pocket079
  AllowMultiFace = false
  BaseFeature = -> Pocket078
  Direction = (1,1,1)
  Length = 1
  Length2 = 100
  Profile = -> Sketch435
  Refine = true
  Type = 0
FEATURE [Sketcher::SketchObject] Sketch438
  FullyConstrained = false
  MapMode = 5
  Placement = pos=(0,0,2) rot=(1,0,0;3.14159rad)
  Support = -> [Pocket079]
  sketch-geometry (2):
    g0: ArcOfCircle CenterX=0 CenterY=0 CenterZ=0 NormalX=0 NormalY=0 NormalZ=1 AngleXU=0 Radius=3 StartAngle=2.19024 EndAngle=7.23453
    g1: LineSegment StartX=-1.74176 StartY=2.4426 StartZ=0 EndX=1.74176 EndY=2.4426 EndZ=0
  constraints (5):
    c: Coincident(g0,g-1)
    c: Coincident(g1,g0)
    c: Coincident(g1,g0)
    c: Horizontal(g1)
    c: Radius(g0) = 3
FEATURE [PartDesign::Pocket] Pocket082
  AllowMultiFace = false
  BaseFeature = -> Pocket079
  Direction = (1,1,1)
  Length = 8
  Length2 = 100
  Profile = -> Sketch438
  Refine = true
  Type = 0
FEATURE [PartDesign::Chamfer] Chamfer067
  Angle = 45
  Base = -> Pocket082 [Edge82,Edge83]
  BaseFeature = -> Pocket082
  ChamferType = 0
  FlipDirection = false
  Size = 1.4
  Size2 = 1
  SupportTransform = false
  UseAllEdges = false
FEATURE [PartDesign::Chamfer] Chamfer065
  Angle = 45
  Base = -> Chamfer067 [Edge8]
  BaseFeature = -> Chamfer067
  ChamferType = 0
  FlipDirection = false
  Size = 0.3
  Size2 = 1
  SupportTransform = false
  UseAllEdges = false
FEATURE [PartDesign::Fillet] Fillet036
  Base = -> Chamfer065 [Edge93,Face36]
  BaseFeature = -> Chamfer065
  Radius = 0.1
  SupportTransform = false
  UseAllEdges = false
FEATURE [PartDesign::Body] Body175
  Group = -> [Sketch437,Sketch439,Sketch440,AdditiveLoft046,Sketch436,Pad078,Sketch427,Pocket078,Sketch435,Pocket079,Sketch438,Pocket082,Chamfer067,Chamfer065,Fillet036]
  Origin = -> Origin921
  Tip = -> Fillet036
FEATURE [App::Part] Part134  label="Cap027"
  Group = -> [Body175]
  Origin = -> Origin915
  Placement = pos=(13.335,13.335,0) rot=(0,0,1;0rad)
  expr: .Placement.Base.x = 13.335
  expr: .Placement.Base.y = 13.335
FEATURE [Sketcher::SketchObject] Sketch442
  AttachmentOffset = pos=(0,0,7) rot=(0,0,1;0rad)
  FullyConstrained = false
  MapMode = 5
  Placement = pos=(0,0,7) rot=(0,0,1;0rad)
  Support = -> [XY_Plane902]
  sketch-geometry (25):
    g0: LineSegment StartX=-0.724089 StartY=5.5 StartZ=0 EndX=-2.12292 EndY=5.12518 EndZ=0
    g1: LineSegment StartX=-2.12292 StartY=5.12518 StartZ=0 EndX=-3.37708 EndY=4.4011 EndZ=0
    g2: LineSegment StartX=-3.37708 StartY=4.4011 StartZ=0 EndX=-4.4011 EndY=3.37708 EndZ=0
    g3: LineSegment StartX=-4.4011 StartY=3.37708 StartZ=0 EndX=-5.12518 EndY=2.12292 EndZ=0
    g4: LineSegment StartX=-5.12518 StartY=2.12292 StartZ=0 EndX=-5.5 EndY=0.724089 EndZ=0
    g5: LineSegment StartX=-5.5 StartY=0.724089 StartZ=0 EndX=-5.5 EndY=-0.724089 EndZ=0
    g6: LineSegment StartX=-5.5 StartY=-0.724089 StartZ=0 EndX=-5.12518 EndY=-2.12292 EndZ=0
    g7: LineSegment StartX=-5.12518 StartY=-2.12292 StartZ=0 EndX=-4.4011 EndY=-3.37708 EndZ=0
    g8: LineSegment StartX=-4.4011 StartY=-3.37708 StartZ=0 EndX=-3.37708 EndY=-4.4011 EndZ=0
    g9: LineSegment StartX=-3.37708 StartY=-4.4011 StartZ=0 EndX=-2.12292 EndY=-5.12518 EndZ=0
    g10: LineSegment StartX=-2.12292 StartY=-5.12518 StartZ=0 EndX=-0.724089 EndY=-5.5 EndZ=0
    g11: LineSegment StartX=-0.724089 StartY=-5.5 StartZ=0 EndX=0.724089 EndY=-5.5 EndZ=0
    g12: LineSegment StartX=0.724089 StartY=-5.5 StartZ=0 EndX=2.12292 EndY=-5.12518 EndZ=0
    g13: LineSegment StartX=2.12292 StartY=-5.12518 StartZ=0 EndX=3.37708 EndY=-4.4011 EndZ=0
    g14: LineSegment StartX=3.37708 StartY=-4.4011 StartZ=0 EndX=4.4011 EndY=-3.37708 EndZ=0
    g15: LineSegment StartX=4.4011 StartY=-3.37708 StartZ=0 EndX=5.12518 EndY=-2.12292 EndZ=0
    g16: LineSegment StartX=5.12518 StartY=-2.12292 StartZ=0 EndX=5.5 EndY=-0.724089 EndZ=0
    g17: LineSegment StartX=5.5 StartY=-0.724089 StartZ=0 EndX=5.5 EndY=0.724089 EndZ=0
    g18: LineSegment StartX=5.5 StartY=0.724089 StartZ=0 EndX=5.12518 EndY=2.12292 EndZ=0
    g19: LineSegment StartX=5.12518 StartY=2.12292 StartZ=0 EndX=4.4011 EndY=3.37708 EndZ=0
    g20: LineSegment StartX=4.4011 StartY=3.37708 StartZ=0 EndX=3.37708 EndY=4.4011 EndZ=0
    g21: LineSegment StartX=3.37708 StartY=4.4011 StartZ=0 EndX=2.12292 EndY=5.12518 EndZ=0
    g22: LineSegment StartX=2.12292 StartY=5.12518 StartZ=0 EndX=0.724089 EndY=5.5 EndZ=0
    g23: LineSegment StartX=0.724089 StartY=5.5 StartZ=0 EndX=-0.724089 EndY=5.5 EndZ=0
    g24: Circle CenterX=0 CenterY=0 CenterZ=0 NormalX=0 NormalY=0 NormalZ=1 AngleXU=0 Radius=5.54746
  constraints (52):
    c: Coincident(g0,g1)
    c: Coincident(g1,g2)
    c: Coincident(g2,g3)
    c: Coincident(g3,g4)
    c: Coincident(g4,g5)
    c: Coincident(g5,g6)
    c: Coincident(g6,g7)
    c: Coincident(g7,g8)
    c: Coincident(g8,g9)
    c: Coincident(g9,g10)
    c: Coincident(g10,g11)
    c: Coincident(g11,g12)
    c: Coincident(g12,g13)
    c: Coincident(g13,g14)
    c: Coincident(g14,g15)
    c: Coincident(g15,g16)
    c: Coincident(g16,g17)
    c: Coincident(g17,g18)
    c: Coincident(g18,g19)
    c: Coincident(g19,g20)
    c: Coincident(g20,g21)
    c: Coincident(g21,g22)
    c: Coincident(g22,g23)
    c: Coincident(g23,g0)
    c: Equal(g0, g1-g23) x23
    c: PointOnObject(g0,g24)
    c: PointOnObject(g1,g24)
    c: PointOnObject(g2,g24)
    c: PointOnObject(g3,g24)
    c: PointOnObject(g4,g24)
    c: PointOnObject(g5,g24)
    c: PointOnObject(g6,g24)
    c: PointOnObject(g7,g24)
    c: PointOnObject(g8,g24)
    c: PointOnObject(g9,g24)
    c: PointOnObject(g10,g24)
    c: PointOnObject(g11,g24)
    c: PointOnObject(g12,g24)
    c: PointOnObject(g13,g24)
    c: PointOnObject(g14,g24)
    c: PointOnObject(g15,g24)
    c: PointOnObject(g16,g24)
    c: PointOnObject(g17,g24)
    c: PointOnObject(g18,g24)
    c: PointOnObject(g19,g24)
    c: PointOnObject(g20,g24)
    c: PointOnObject(g21,g24)
    c: PointOnObject(g22,g24)
    c: PointOnObject(g23,g24)
    c: Coincident(g24,g-1)
    c: Horizontal(g23)
    c: DistanceX(g4,g17) = 11
FEATURE [Sketcher::SketchObject] Sketch443
  AttachmentOffset = pos=(0,0,17) rot=(0,0,1;0rad)
  FullyConstrained = false
  MapMode = 5
  Placement = pos=(0,0,17) rot=(0,0,1;0rad)
  Support = -> [XY_Plane902]
  sketch-geometry (25):
    g0: LineSegment StartX=-4.65926 StartY=1.92993 StartZ=0 EndX=-5 EndY=0.658262 EndZ=0
    g1: LineSegment StartX=-5 StartY=0.658262 StartZ=0 EndX=-5 EndY=-0.658262 EndZ=0
    g2: LineSegment StartX=-5 StartY=-0.658262 StartZ=0 EndX=-4.65926 EndY=-1.92993 EndZ=0
    g3: LineSegment StartX=-4.65926 StartY=-1.92993 StartZ=0 EndX=-4.001 EndY=-3.07007 EndZ=0
    g4: LineSegment StartX=-4.001 StartY=-3.07007 StartZ=0 EndX=-3.07007 EndY=-4.001 EndZ=0
    g5: LineSegment StartX=-3.07007 StartY=-4.001 StartZ=0 EndX=-1.92993 EndY=-4.65926 EndZ=0
    g6: LineSegment StartX=-1.92993 StartY=-4.65926 StartZ=0 EndX=-0.658262 EndY=-5 EndZ=0
    g7: LineSegment StartX=-0.658262 StartY=-5 StartZ=0 EndX=0.658262 EndY=-5 EndZ=0
    g8: LineSegment StartX=0.658262 StartY=-5 StartZ=0 EndX=1.92993 EndY=-4.65926 EndZ=0
    g9: LineSegment StartX=1.92993 StartY=-4.65926 StartZ=0 EndX=3.07007 EndY=-4.001 EndZ=0
    g10: LineSegment StartX=3.07007 StartY=-4.001 StartZ=0 EndX=4.001 EndY=-3.07007 EndZ=0
    g11: LineSegment StartX=4.001 StartY=-3.07007 StartZ=0 EndX=4.65926 EndY=-1.92993 EndZ=0
    g12: LineSegment StartX=4.65926 StartY=-1.92993 StartZ=0 EndX=5 EndY=-0.658262 EndZ=0
    g13: LineSegment StartX=5 StartY=-0.658262 StartZ=0 EndX=5 EndY=0.658262 EndZ=0
    g14: LineSegment StartX=5 StartY=0.658262 StartZ=0 EndX=4.65926 EndY=1.92993 EndZ=0
    g15: LineSegment StartX=4.65926 StartY=1.92993 StartZ=0 EndX=4.001 EndY=3.07007 EndZ=0
    g16: LineSegment StartX=4.001 StartY=3.07007 StartZ=0 EndX=3.07007 EndY=4.001 EndZ=0
    g17: LineSegment StartX=3.07007 StartY=4.001 StartZ=0 EndX=1.92993 EndY=4.65926 EndZ=0
    g18: LineSegment StartX=1.92993 StartY=4.65926 StartZ=0 EndX=0.658262 EndY=5 EndZ=0
    g19: LineSegment StartX=0.658262 StartY=5 StartZ=0 EndX=-0.658262 EndY=5 EndZ=0
    g20: LineSegment StartX=-0.658262 StartY=5 StartZ=0 EndX=-1.92993 EndY=4.65926 EndZ=0
    g21: LineSegment StartX=-1.92993 StartY=4.65926 StartZ=0 EndX=-3.07007 EndY=4.001 EndZ=0
    g22: LineSegment StartX=-3.07007 StartY=4.001 StartZ=0 EndX=-4.001 EndY=3.07007 EndZ=0
    g23: LineSegment StartX=-4.001 StartY=3.07007 StartZ=0 EndX=-4.65926 EndY=1.92993 EndZ=0
    g24: Circle CenterX=0 CenterY=0 CenterZ=0 NormalX=0 NormalY=0 NormalZ=1 AngleXU=0 Radius=5.04314
  constraints (52):
    c: Coincident(g0,g1)
    c: Coincident(g1,g2)
    c: Coincident(g2,g3)
    c: Coincident(g3,g4)
    c: Coincident(g4,g5)
    c: Coincident(g5,g6)
    c: Coincident(g6,g7)
    c: Coincident(g7,g8)
    c: Coincident(g8,g9)
    c: Coincident(g9,g10)
    c: Coincident(g10,g11)
    c: Coincident(g11,g12)
    c: Coincident(g12,g13)
    c: Coincident(g13,g14)
    c: Coincident(g14,g15)
    c: Coincident(g15,g16)
    c: Coincident(g16,g17)
    c: Coincident(g17,g18)
    c: Coincident(g18,g19)
    c: Coincident(g19,g20)
    c: Coincident(g20,g21)
    c: Coincident(g21,g22)
    c: Coincident(g22,g23)
    c: Coincident(g23,g0)
    c: Equal(g0, g1-g23) x23
    c: PointOnObject(g0,g24)
    c: PointOnObject(g1,g24)
    c: PointOnObject(g2,g24)
    c: PointOnObject(g3,g24)
    c: PointOnObject(g4,g24)
    c: PointOnObject(g5,g24)
    c: PointOnObject(g6,g24)
    c: PointOnObject(g7,g24)
    c: PointOnObject(g8,g24)
    c: PointOnObject(g9,g24)
    c: PointOnObject(g10,g24)
    c: PointOnObject(g11,g24)
    c: PointOnObject(g12,g24)
    c: PointOnObject(g13,g24)
    c: PointOnObject(g14,g24)
    c: PointOnObject(g15,g24)
    c: PointOnObject(g16,g24)
    c: PointOnObject(g17,g24)
    c: PointOnObject(g18,g24)
    c: PointOnObject(g19,g24)
    c: PointOnObject(g20,g24)
    c: PointOnObject(g21,g24)
    c: PointOnObject(g22,g24)
    c: PointOnObject(g23,g24)
    c: Coincident(g24,g-1)
    c: Horizontal(g19)
    c: DistanceX(g0,g13) = 10
FEATURE [PartDesign::AdditiveLoft] AdditiveLoft041
  AllowMultiFace = false
  Closed = false
  Profile = -> Sketch431
  Refine = true
  Ruled = false
  Sections = -> [Sketch442,Sketch443]
FEATURE [Sketcher::SketchObject] Sketch430
  FullyConstrained = false
  MapMode = 5
  Placement = pos=(0,0,17) rot=(0,0,1;0rad)
  Support = -> [AdditiveLoft041]
  sketch-geometry (1):
    g0: Circle CenterX=0 CenterY=0 CenterZ=0 NormalX=0 NormalY=0 NormalZ=1 AngleXU=0 Radius=4.5
  constraints (2):
    c: Coincident(g0,g-1)
    c: Radius(g0) = 4.5
FEATURE [Sketcher::SketchObject] Sketch450
  AttachmentOffset = pos=(0,0,7) rot=(0,0,1;0rad)
  FullyConstrained = false
  MapMode = 5
  Placement = pos=(0,0,7) rot=(0,0,1;0rad)
  Support = -> [XY_Plane904]
  sketch-geometry (25):
    g0: LineSegment StartX=-0.724089 StartY=5.5 StartZ=0 EndX=-2.12292 EndY=5.12518 EndZ=0
    g1: LineSegment StartX=-2.12292 StartY=5.12518 StartZ=0 EndX=-3.37708 EndY=4.4011 EndZ=0
    g2: LineSegment StartX=-3.37708 StartY=4.4011 StartZ=0 EndX=-4.4011 EndY=3.37708 EndZ=0
    g3: LineSegment StartX=-4.4011 StartY=3.37708 StartZ=0 EndX=-5.12518 EndY=2.12292 EndZ=0
    g4: LineSegment StartX=-5.12518 StartY=2.12292 StartZ=0 EndX=-5.5 EndY=0.724089 EndZ=0
    g5: LineSegment StartX=-5.5 StartY=0.724089 StartZ=0 EndX=-5.5 EndY=-0.724089 EndZ=0
    g6: LineSegment StartX=-5.5 StartY=-0.724089 StartZ=0 EndX=-5.12518 EndY=-2.12292 EndZ=0
    g7: LineSegment StartX=-5.12518 StartY=-2.12292 StartZ=0 EndX=-4.4011 EndY=-3.37708 EndZ=0
    g8: LineSegment StartX=-4.4011 StartY=-3.37708 StartZ=0 EndX=-3.37708 EndY=-4.4011 EndZ=0
    g9: LineSegment StartX=-3.37708 StartY=-4.4011 StartZ=0 EndX=-2.12292 EndY=-5.12518 EndZ=0
    g10: LineSegment StartX=-2.12292 StartY=-5.12518 StartZ=0 EndX=-0.724089 EndY=-5.5 EndZ=0
    g11: LineSegment StartX=-0.724089 StartY=-5.5 StartZ=0 EndX=0.724089 EndY=-5.5 EndZ=0
    g12: LineSegment StartX=0.724089 StartY=-5.5 StartZ=0 EndX=2.12292 EndY=-5.12518 EndZ=0
    g13: LineSegment StartX=2.12292 StartY=-5.12518 StartZ=0 EndX=3.37708 EndY=-4.4011 EndZ=0
    g14: LineSegment StartX=3.37708 StartY=-4.4011 StartZ=0 EndX=4.4011 EndY=-3.37708 EndZ=0
    g15: LineSegment StartX=4.4011 StartY=-3.37708 StartZ=0 EndX=5.12518 EndY=-2.12292 EndZ=0
    g16: LineSegment StartX=5.12518 StartY=-2.12292 StartZ=0 EndX=5.5 EndY=-0.724089 EndZ=0
    g17: LineSegment StartX=5.5 StartY=-0.724089 StartZ=0 EndX=5.5 EndY=0.724089 EndZ=0
    g18: LineSegment StartX=5.5 StartY=0.724089 StartZ=0 EndX=5.12518 EndY=2.12292 EndZ=0
    g19: LineSegment StartX=5.12518 StartY=2.12292 StartZ=0 EndX=4.4011 EndY=3.37708 EndZ=0
    g20: LineSegment StartX=4.4011 StartY=3.37708 StartZ=0 EndX=3.37708 EndY=4.4011 EndZ=0
    g21: LineSegment StartX=3.37708 StartY=4.4011 StartZ=0 EndX=2.12292 EndY=5.12518 EndZ=0
    g22: LineSegment StartX=2.12292 StartY=5.12518 StartZ=0 EndX=0.724089 EndY=5.5 EndZ=0
    g23: LineSegment StartX=0.724089 StartY=5.5 StartZ=0 EndX=-0.724089 EndY=5.5 EndZ=0
    g24: Circle CenterX=0 CenterY=0 CenterZ=0 NormalX=0 NormalY=0 NormalZ=1 AngleXU=0 Radius=5.54746
  constraints (52):
    c: Coincident(g0,g1)
    c: Coincident(g1,g2)
    c: Coincident(g2,g3)
    c: Coincident(g3,g4)
    c: Coincident(g4,g5)
    c: Coincident(g5,g6)
    c: Coincident(g6,g7)
    c: Coincident(g7,g8)
    c: Coincident(g8,g9)
    c: Coincident(g9,g10)
    c: Coincident(g10,g11)
    c: Coincident(g11,g12)
    c: Coincident(g12,g13)
    c: Coincident(g13,g14)
    c: Coincident(g14,g15)
    c: Coincident(g15,g16)
    c: Coincident(g16,g17)
    c: Coincident(g17,g18)
    c: Coincident(g18,g19)
    c: Coincident(g19,g20)
    c: Coincident(g20,g21)
    c: Coincident(g21,g22)
    c: Coincident(g22,g23)
    c: Coincident(g23,g0)
    c: Equal(g0, g1-g23) x23
    c: PointOnObject(g0,g24)
    c: PointOnObject(g1,g24)
    c: PointOnObject(g2,g24)
    c: PointOnObject(g3,g24)
    c: PointOnObject(g4,g24)
    c: PointOnObject(g5,g24)
    c: PointOnObject(g6,g24)
    c: PointOnObject(g7,g24)
    c: PointOnObject(g8,g24)
    c: PointOnObject(g9,g24)
    c: PointOnObject(g10,g24)
    c: PointOnObject(g11,g24)
    c: PointOnObject(g12,g24)
    c: PointOnObject(g13,g24)
    c: PointOnObject(g14,g24)
    c: PointOnObject(g15,g24)
    c: PointOnObject(g16,g24)
    c: PointOnObject(g17,g24)
    c: PointOnObject(g18,g24)
    c: PointOnObject(g19,g24)
    c: PointOnObject(g20,g24)
    c: PointOnObject(g21,g24)
    c: PointOnObject(g22,g24)
    c: PointOnObject(g23,g24)
    c: Coincident(g24,g-1)
    c: Horizontal(g23)
    c: DistanceX(g4,g17) = 11
FEATURE [PartDesign::Pad] Pad083
  AllowMultiFace = false
  BaseFeature = -> AdditiveLoft041
  Direction = (1,1,1)
  Length = 0.7
  Length2 = 100
  Profile = -> Sketch430
  Refine = true
  Type = 0
FEATURE [Sketcher::SketchObject] Sketch434
  FullyConstrained = false
  MapMode = 5
  Placement = pos=(0,0,0) rot=(1,0,0;3.14159rad)
  Support = -> [Pad083]
  sketch-geometry (1):
    g0: Circle CenterX=0 CenterY=0 CenterZ=0 NormalX=0 NormalY=0 NormalZ=1 AngleXU=0 Radius=5
  constraints (2):
    c: Coincident(g0,g-1)
    c: Radius(g0) = 5
FEATURE [PartDesign::Pocket] Pocket087
  AllowMultiFace = false
  BaseFeature = -> Pad083
  Direction = (1,1,1)
  Length = 1
  Length2 = 100
  Profile = -> Sketch434
  Refine = true
  Type = 0
FEATURE [Sketcher::SketchObject] Sketch441
  FullyConstrained = false
  MapMode = 5
  Placement = pos=(0,0,1) rot=(1,0,0;3.14159rad)
  Support = -> [Pocket087]
  sketch-geometry (1):
    g0: Circle CenterX=0 CenterY=0 CenterZ=0 NormalX=0 NormalY=0 NormalZ=1 AngleXU=0 Radius=4.65
  constraints (2):
    c: Coincident(g0,g-1)
    c: Radius(g0) = 4.65
FEATURE [PartDesign::Pocket] Pocket083
  AllowMultiFace = false
  BaseFeature = -> Pocket087
  Direction = (1,1,1)
  Length = 1
  Length2 = 100
  Profile = -> Sketch441
  Refine = true
  Type = 0
FEATURE [Sketcher::SketchObject] Sketch433
  FullyConstrained = false
  MapMode = 5
  Placement = pos=(0,0,2) rot=(1,0,0;3.14159rad)
  Support = -> [Pocket083]
  sketch-geometry (2):
    g0: ArcOfCircle CenterX=0 CenterY=0 CenterZ=0 NormalX=0 NormalY=0 NormalZ=1 AngleXU=0 Radius=3 StartAngle=2.19024 EndAngle=7.23453
    g1: LineSegment StartX=-1.74176 StartY=2.4426 StartZ=0 EndX=1.74176 EndY=2.4426 EndZ=0
  constraints (5):
    c: Coincident(g0,g-1)
    c: Coincident(g1,g0)
    c: Coincident(g1,g0)
    c: Horizontal(g1)
    c: Radius(g0) = 3
FEATURE [PartDesign::Pocket] Pocket090
  AllowMultiFace = false
  BaseFeature = -> Pocket083
  Direction = (1,1,1)
  Length = 8
  Length2 = 100
  Profile = -> Sketch433
  Refine = true
  Type = 0
FEATURE [PartDesign::Chamfer] Chamfer069
  Angle = 45
  Base = -> Pocket090 [Edge82,Edge83]
  BaseFeature = -> Pocket090
  ChamferType = 0
  FlipDirection = false
  Size = 1.4
  Size2 = 1
  SupportTransform = false
  UseAllEdges = false
FEATURE [PartDesign::Chamfer] Chamfer068
  Angle = 45
  Base = -> Chamfer069 [Edge8]
  BaseFeature = -> Chamfer069
  ChamferType = 0
  FlipDirection = false
  Size = 0.3
  Size2 = 1
  SupportTransform = false
  UseAllEdges = false
FEATURE [PartDesign::Fillet] Fillet035
  Base = -> Chamfer068 [Edge93,Face36]
  BaseFeature = -> Chamfer068
  Radius = 0.1
  SupportTransform = false
  UseAllEdges = false
FEATURE [PartDesign::Body] Body177
  Group = -> [Sketch431,Sketch442,Sketch443,AdditiveLoft041,Sketch430,Pad083,Sketch434,Pocket087,Sketch441,Pocket083,Sketch433,Pocket090,Chamfer069,Chamfer068,Fillet035]
  Origin = -> Origin917
  Tip = -> Fillet035
FEATURE [App::Part] Part141  label="Cap034"
  Group = -> [Body177]
  Origin = -> Origin909
  Placement = pos=(40.005,13.335,0) rot=(0,0,1;0rad)
  expr: .Placement.Base.x = 40.005
  expr: .Placement.Base.y = 13.335
FEATURE [Sketcher::SketchObject] Sketch451
  AttachmentOffset = pos=(0,0,17) rot=(0,0,1;0rad)
  FullyConstrained = false
  MapMode = 5
  Placement = pos=(0,0,17) rot=(0,0,1;0rad)
  Support = -> [XY_Plane908]
  sketch-geometry (25):
    g0: LineSegment StartX=-4.65926 StartY=1.92993 StartZ=0 EndX=-5 EndY=0.658262 EndZ=0
    g1: LineSegment StartX=-5 StartY=0.658262 StartZ=0 EndX=-5 EndY=-0.658262 EndZ=0
    g2: LineSegment StartX=-5 StartY=-0.658262 StartZ=0 EndX=-4.65926 EndY=-1.92993 EndZ=0
    g3: LineSegment StartX=-4.65926 StartY=-1.92993 StartZ=0 EndX=-4.001 EndY=-3.07007 EndZ=0
    g4: LineSegment StartX=-4.001 StartY=-3.07007 StartZ=0 EndX=-3.07007 EndY=-4.001 EndZ=0
    g5: LineSegment StartX=-3.07007 StartY=-4.001 StartZ=0 EndX=-1.92993 EndY=-4.65926 EndZ=0
    g6: LineSegment StartX=-1.92993 StartY=-4.65926 StartZ=0 EndX=-0.658262 EndY=-5 EndZ=0
    g7: LineSegment StartX=-0.658262 StartY=-5 StartZ=0 EndX=0.658262 EndY=-5 EndZ=0
    g8: LineSegment StartX=0.658262 StartY=-5 StartZ=0 EndX=1.92993 EndY=-4.65926 EndZ=0
    g9: LineSegment StartX=1.92993 StartY=-4.65926 StartZ=0 EndX=3.07007 EndY=-4.001 EndZ=0
    g10: LineSegment StartX=3.07007 StartY=-4.001 StartZ=0 EndX=4.001 EndY=-3.07007 EndZ=0
    g11: LineSegment StartX=4.001 StartY=-3.07007 StartZ=0 EndX=4.65926 EndY=-1.92993 EndZ=0
    g12: LineSegment StartX=4.65926 StartY=-1.92993 StartZ=0 EndX=5 EndY=-0.658262 EndZ=0
    g13: LineSegment StartX=5 StartY=-0.658262 StartZ=0 EndX=5 EndY=0.658262 EndZ=0
    g14: LineSegment StartX=5 StartY=0.658262 StartZ=0 EndX=4.65926 EndY=1.92993 EndZ=0
    g15: LineSegment StartX=4.65926 StartY=1.92993 StartZ=0 EndX=4.001 EndY=3.07007 EndZ=0
    g16: LineSegment StartX=4.001 StartY=3.07007 StartZ=0 EndX=3.07007 EndY=4.001 EndZ=0
    g17: LineSegment StartX=3.07007 StartY=4.001 StartZ=0 EndX=1.92993 EndY=4.65926 EndZ=0
    g18: LineSegment StartX=1.92993 StartY=4.65926 StartZ=0 EndX=0.658262 EndY=5 EndZ=0
    g19: LineSegment StartX=0.658262 StartY=5 StartZ=0 EndX=-0.658262 EndY=5 EndZ=0
    g20: LineSegment StartX=-0.658262 StartY=5 StartZ=0 EndX=-1.92993 EndY=4.65926 EndZ=0
    g21: LineSegment StartX=-1.92993 StartY=4.65926 StartZ=0 EndX=-3.07007 EndY=4.001 EndZ=0
    g22: LineSegment StartX=-3.07007 StartY=4.001 StartZ=0 EndX=-4.001 EndY=3.07007 EndZ=0
    g23: LineSegment StartX=-4.001 StartY=3.07007 StartZ=0 EndX=-4.65926 EndY=1.92993 EndZ=0
    g24: Circle CenterX=0 CenterY=0 CenterZ=0 NormalX=0 NormalY=0 NormalZ=1 AngleXU=0 Radius=5.04314
  constraints (52):
    c: Coincident(g0,g1)
    c: Coincident(g1,g2)
    c: Coincident(g2,g3)
    c: Coincident(g3,g4)
    c: Coincident(g4,g5)
    c: Coincident(g5,g6)
    c: Coincident(g6,g7)
    c: Coincident(g7,g8)
    c: Coincident(g8,g9)
    c: Coincident(g9,g10)
    c: Coincident(g10,g11)
    c: Coincident(g11,g12)
    c: Coincident(g12,g13)
    c: Coincident(g13,g14)
    c: Coincident(g14,g15)
    c: Coincident(g15,g16)
    c: Coincident(g16,g17)
    c: Coincident(g17,g18)
    c: Coincident(g18,g19)
    c: Coincident(g19,g20)
    c: Coincident(g20,g21)
    c: Coincident(g21,g22)
    c: Coincident(g22,g23)
    c: Coincident(g23,g0)
    c: Equal(g0, g1-g23) x23
    c: PointOnObject(g0,g24)
    c: PointOnObject(g1,g24)
    c: PointOnObject(g2,g24)
    c: PointOnObject(g3,g24)
    c: PointOnObject(g4,g24)
    c: PointOnObject(g5,g24)
    c: PointOnObject(g6,g24)
    c: PointOnObject(g7,g24)
    c: PointOnObject(g8,g24)
    c: PointOnObject(g9,g24)
    c: PointOnObject(g10,g24)
    c: PointOnObject(g11,g24)
    c: PointOnObject(g12,g24)
    c: PointOnObject(g13,g24)
    c: PointOnObject(g14,g24)
    c: PointOnObject(g15,g24)
    c: PointOnObject(g16,g24)
    c: PointOnObject(g17,g24)
    c: PointOnObject(g18,g24)
    c: PointOnObject(g19,g24)
    c: PointOnObject(g20,g24)
    c: PointOnObject(g21,g24)
    c: PointOnObject(g22,g24)
    c: PointOnObject(g23,g24)
    c: Coincident(g24,g-1)
    c: Horizontal(g19)
    c: DistanceX(g0,g13) = 10
FEATURE [Sketcher::SketchObject] Sketch452
  AttachmentOffset = pos=(0,0,17) rot=(0,0,1;0rad)
  FullyConstrained = false
  MapMode = 5
  Placement = pos=(0,0,17) rot=(0,0,1;0rad)
  Support = -> [XY_Plane904]
  sketch-geometry (25):
    g0: LineSegment StartX=-4.65926 StartY=1.92993 StartZ=0 EndX=-5 EndY=0.658262 EndZ=0
    g1: LineSegment StartX=-5 StartY=0.658262 StartZ=0 EndX=-5 EndY=-0.658262 EndZ=0
    g2: LineSegment StartX=-5 StartY=-0.658262 StartZ=0 EndX=-4.65926 EndY=-1.92993 EndZ=0
    g3: LineSegment StartX=-4.65926 StartY=-1.92993 StartZ=0 EndX=-4.001 EndY=-3.07007 EndZ=0
    g4: LineSegment StartX=-4.001 StartY=-3.07007 StartZ=0 EndX=-3.07007 EndY=-4.001 EndZ=0
    g5: LineSegment StartX=-3.07007 StartY=-4.001 StartZ=0 EndX=-1.92993 EndY=-4.65926 EndZ=0
    g6: LineSegment StartX=-1.92993 StartY=-4.65926 StartZ=0 EndX=-0.658262 EndY=-5 EndZ=0
    g7: LineSegment StartX=-0.658262 StartY=-5 StartZ=0 EndX=0.658262 EndY=-5 EndZ=0
    g8: LineSegment StartX=0.658262 StartY=-5 StartZ=0 EndX=1.92993 EndY=-4.65926 EndZ=0
    g9: LineSegment StartX=1.92993 StartY=-4.65926 StartZ=0 EndX=3.07007 EndY=-4.001 EndZ=0
    g10: LineSegment StartX=3.07007 StartY=-4.001 StartZ=0 EndX=4.001 EndY=-3.07007 EndZ=0
    g11: LineSegment StartX=4.001 StartY=-3.07007 StartZ=0 EndX=4.65926 EndY=-1.92993 EndZ=0
    g12: LineSegment StartX=4.65926 StartY=-1.92993 StartZ=0 EndX=5 EndY=-0.658262 EndZ=0
    g13: LineSegment StartX=5 StartY=-0.658262 StartZ=0 EndX=5 EndY=0.658262 EndZ=0
    g14: LineSegment StartX=5 StartY=0.658262 StartZ=0 EndX=4.65926 EndY=1.92993 EndZ=0
    g15: LineSegment StartX=4.65926 StartY=1.92993 StartZ=0 EndX=4.001 EndY=3.07007 EndZ=0
    g16: LineSegment StartX=4.001 StartY=3.07007 StartZ=0 EndX=3.07007 EndY=4.001 EndZ=0
    g17: LineSegment StartX=3.07007 StartY=4.001 StartZ=0 EndX=1.92993 EndY=4.65926 EndZ=0
    g18: LineSegment StartX=1.92993 StartY=4.65926 StartZ=0 EndX=0.658262 EndY=5 EndZ=0
    g19: LineSegment StartX=0.658262 StartY=5 StartZ=0 EndX=-0.658262 EndY=5 EndZ=0
    g20: LineSegment StartX=-0.658262 StartY=5 StartZ=0 EndX=-1.92993 EndY=4.65926 EndZ=0
    g21: LineSegment StartX=-1.92993 StartY=4.65926 StartZ=0 EndX=-3.07007 EndY=4.001 EndZ=0
    g22: LineSegment StartX=-3.07007 StartY=4.001 StartZ=0 EndX=-4.001 EndY=3.07007 EndZ=0
    g23: LineSegment StartX=-4.001 StartY=3.07007 StartZ=0 EndX=-4.65926 EndY=1.92993 EndZ=0
    g24: Circle CenterX=0 CenterY=0 CenterZ=0 NormalX=0 NormalY=0 NormalZ=1 AngleXU=0 Radius=5.04314
  constraints (52):
    c: Coincident(g0,g1)
    c: Coincident(g1,g2)
    c: Coincident(g2,g3)
    c: Coincident(g3,g4)
    c: Coincident(g4,g5)
    c: Coincident(g5,g6)
    c: Coincident(g6,g7)
    c: Coincident(g7,g8)
    c: Coincident(g8,g9)
    c: Coincident(g9,g10)
    c: Coincident(g10,g11)
    c: Coincident(g11,g12)
    c: Coincident(g12,g13)
    c: Coincident(g13,g14)
    c: Coincident(g14,g15)
    c: Coincident(g15,g16)
    c: Coincident(g16,g17)
    c: Coincident(g17,g18)
    c: Coincident(g18,g19)
    c: Coincident(g19,g20)
    c: Coincident(g20,g21)
    c: Coincident(g21,g22)
    c: Coincident(g22,g23)
    c: Coincident(g23,g0)
    c: Equal(g0, g1-g23) x23
    c: PointOnObject(g0,g24)
    c: PointOnObject(g1,g24)
    c: PointOnObject(g2,g24)
    c: PointOnObject(g3,g24)
    c: PointOnObject(g4,g24)
    c: PointOnObject(g5,g24)
    c: PointOnObject(g6,g24)
    c: PointOnObject(g7,g24)
    c: PointOnObject(g8,g24)
    c: PointOnObject(g9,g24)
    c: PointOnObject(g10,g24)
    c: PointOnObject(g11,g24)
    c: PointOnObject(g12,g24)
    c: PointOnObject(g13,g24)
    c: PointOnObject(g14,g24)
    c: PointOnObject(g15,g24)
    c: PointOnObject(g16,g24)
    c: PointOnObject(g17,g24)
    c: PointOnObject(g18,g24)
    c: PointOnObject(g19,g24)
    c: PointOnObject(g20,g24)
    c: PointOnObject(g21,g24)
    c: PointOnObject(g22,g24)
    c: PointOnObject(g23,g24)
    c: Coincident(g24,g-1)
    c: Horizontal(g19)
    c: DistanceX(g0,g13) = 10
FEATURE [Sketcher::SketchObject] Sketch454
  AttachmentOffset = pos=(0,0,7) rot=(0,0,1;0rad)
  FullyConstrained = false
  MapMode = 5
  Placement = pos=(0,0,7) rot=(0,0,1;0rad)
  Support = -> [XY_Plane912]
  sketch-geometry (25):
    g0: LineSegment StartX=-0.724089 StartY=5.5 StartZ=0 EndX=-2.12292 EndY=5.12518 EndZ=0
    g1: LineSegment StartX=-2.12292 StartY=5.12518 StartZ=0 EndX=-3.37708 EndY=4.4011 EndZ=0
    g2: LineSegment StartX=-3.37708 StartY=4.4011 StartZ=0 EndX=-4.4011 EndY=3.37708 EndZ=0
    g3: LineSegment StartX=-4.4011 StartY=3.37708 StartZ=0 EndX=-5.12518 EndY=2.12292 EndZ=0
    g4: LineSegment StartX=-5.12518 StartY=2.12292 StartZ=0 EndX=-5.5 EndY=0.724089 EndZ=0
    g5: LineSegment StartX=-5.5 StartY=0.724089 StartZ=0 EndX=-5.5 EndY=-0.724089 EndZ=0
    g6: LineSegment StartX=-5.5 StartY=-0.724089 StartZ=0 EndX=-5.12518 EndY=-2.12292 EndZ=0
    g7: LineSegment StartX=-5.12518 StartY=-2.12292 StartZ=0 EndX=-4.4011 EndY=-3.37708 EndZ=0
    g8: LineSegment StartX=-4.4011 StartY=-3.37708 StartZ=0 EndX=-3.37708 EndY=-4.4011 EndZ=0
    g9: LineSegment StartX=-3.37708 StartY=-4.4011 StartZ=0 EndX=-2.12292 EndY=-5.12518 EndZ=0
    g10: LineSegment StartX=-2.12292 StartY=-5.12518 StartZ=0 EndX=-0.724089 EndY=-5.5 EndZ=0
    g11: LineSegment StartX=-0.724089 StartY=-5.5 StartZ=0 EndX=0.724089 EndY=-5.5 EndZ=0
    g12: LineSegment StartX=0.724089 StartY=-5.5 StartZ=0 EndX=2.12292 EndY=-5.12518 EndZ=0
    g13: LineSegment StartX=2.12292 StartY=-5.12518 StartZ=0 EndX=3.37708 EndY=-4.4011 EndZ=0
    g14: LineSegment StartX=3.37708 StartY=-4.4011 StartZ=0 EndX=4.4011 EndY=-3.37708 EndZ=0
    g15: LineSegment StartX=4.4011 StartY=-3.37708 StartZ=0 EndX=5.12518 EndY=-2.12292 EndZ=0
    g16: LineSegment StartX=5.12518 StartY=-2.12292 StartZ=0 EndX=5.5 EndY=-0.724089 EndZ=0
    g17: LineSegment StartX=5.5 StartY=-0.724089 StartZ=0 EndX=5.5 EndY=0.724089 EndZ=0
    g18: LineSegment StartX=5.5 StartY=0.724089 StartZ=0 EndX=5.12518 EndY=2.12292 EndZ=0
    g19: LineSegment StartX=5.12518 StartY=2.12292 StartZ=0 EndX=4.4011 EndY=3.37708 EndZ=0
    g20: LineSegment StartX=4.4011 StartY=3.37708 StartZ=0 EndX=3.37708 EndY=4.4011 EndZ=0
    g21: LineSegment StartX=3.37708 StartY=4.4011 StartZ=0 EndX=2.12292 EndY=5.12518 EndZ=0
    g22: LineSegment StartX=2.12292 StartY=5.12518 StartZ=0 EndX=0.724089 EndY=5.5 EndZ=0
    g23: LineSegment StartX=0.724089 StartY=5.5 StartZ=0 EndX=-0.724089 EndY=5.5 EndZ=0
    g24: Circle CenterX=0 CenterY=0 CenterZ=0 NormalX=0 NormalY=0 NormalZ=1 AngleXU=0 Radius=5.54746
  constraints (52):
    c: Coincident(g0,g1)
    c: Coincident(g1,g2)
    c: Coincident(g2,g3)
    c: Coincident(g3,g4)
    c: Coincident(g4,g5)
    c: Coincident(g5,g6)
    c: Coincident(g6,g7)
    c: Coincident(g7,g8)
    c: Coincident(g8,g9)
    c: Coincident(g9,g10)
    c: Coincident(g10,g11)
    c: Coincident(g11,g12)
    c: Coincident(g12,g13)
    c: Coincident(g13,g14)
    c: Coincident(g14,g15)
    c: Coincident(g15,g16)
    c: Coincident(g16,g17)
    c: Coincident(g17,g18)
    c: Coincident(g18,g19)
    c: Coincident(g19,g20)
    c: Coincident(g20,g21)
    c: Coincident(g21,g22)
    c: Coincident(g22,g23)
    c: Coincident(g23,g0)
    c: Equal(g0, g1-g23) x23
    c: PointOnObject(g0,g24)
    c: PointOnObject(g1,g24)
    c: PointOnObject(g2,g24)
    c: PointOnObject(g3,g24)
    c: PointOnObject(g4,g24)
    c: PointOnObject(g5,g24)
    c: PointOnObject(g6,g24)
    c: PointOnObject(g7,g24)
    c: PointOnObject(g8,g24)
    c: PointOnObject(g9,g24)
    c: PointOnObject(g10,g24)
    c: PointOnObject(g11,g24)
    c: PointOnObject(g12,g24)
    c: PointOnObject(g13,g24)
    c: PointOnObject(g14,g24)
    c: PointOnObject(g15,g24)
    c: PointOnObject(g16,g24)
    c: PointOnObject(g17,g24)
    c: PointOnObject(g18,g24)
    c: PointOnObject(g19,g24)
    c: PointOnObject(g20,g24)
    c: PointOnObject(g21,g24)
    c: PointOnObject(g22,g24)
    c: PointOnObject(g23,g24)
    c: Coincident(g24,g-1)
    c: Horizontal(g23)
    c: DistanceX(g4,g17) = 11
FEATURE [Sketcher::SketchObject] Sketch455
  AttachmentOffset = pos=(0,0,7) rot=(0,0,1;0rad)
  FullyConstrained = false
  MapMode = 5
  Placement = pos=(0,0,7) rot=(0,0,1;0rad)
  Support = -> [XY_Plane908]
  sketch-geometry (25):
    g0: LineSegment StartX=-0.724089 StartY=5.5 StartZ=0 EndX=-2.12292 EndY=5.12518 EndZ=0
    g1: LineSegment StartX=-2.12292 StartY=5.12518 StartZ=0 EndX=-3.37708 EndY=4.4011 EndZ=0
    g2: LineSegment StartX=-3.37708 StartY=4.4011 StartZ=0 EndX=-4.4011 EndY=3.37708 EndZ=0
    g3: LineSegment StartX=-4.4011 StartY=3.37708 StartZ=0 EndX=-5.12518 EndY=2.12292 EndZ=0
    g4: LineSegment StartX=-5.12518 StartY=2.12292 StartZ=0 EndX=-5.5 EndY=0.724089 EndZ=0
    g5: LineSegment StartX=-5.5 StartY=0.724089 StartZ=0 EndX=-5.5 EndY=-0.724089 EndZ=0
    g6: LineSegment StartX=-5.5 StartY=-0.724089 StartZ=0 EndX=-5.12518 EndY=-2.12292 EndZ=0
    g7: LineSegment StartX=-5.12518 StartY=-2.12292 StartZ=0 EndX=-4.4011 EndY=-3.37708 EndZ=0
    g8: LineSegment StartX=-4.4011 StartY=-3.37708 StartZ=0 EndX=-3.37708 EndY=-4.4011 EndZ=0
    g9: LineSegment StartX=-3.37708 StartY=-4.4011 StartZ=0 EndX=-2.12292 EndY=-5.12518 EndZ=0
    g10: LineSegment StartX=-2.12292 StartY=-5.12518 StartZ=0 EndX=-0.724089 EndY=-5.5 EndZ=0
    g11: LineSegment StartX=-0.724089 StartY=-5.5 StartZ=0 EndX=0.724089 EndY=-5.5 EndZ=0
    g12: LineSegment StartX=0.724089 StartY=-5.5 StartZ=0 EndX=2.12292 EndY=-5.12518 EndZ=0
    g13: LineSegment StartX=2.12292 StartY=-5.12518 StartZ=0 EndX=3.37708 EndY=-4.4011 EndZ=0
    g14: LineSegment StartX=3.37708 StartY=-4.4011 StartZ=0 EndX=4.4011 EndY=-3.37708 EndZ=0
    g15: LineSegment StartX=4.4011 StartY=-3.37708 StartZ=0 EndX=5.12518 EndY=-2.12292 EndZ=0
    g16: LineSegment StartX=5.12518 StartY=-2.12292 StartZ=0 EndX=5.5 EndY=-0.724089 EndZ=0
    g17: LineSegment StartX=5.5 StartY=-0.724089 StartZ=0 EndX=5.5 EndY=0.724089 EndZ=0
    g18: LineSegment StartX=5.5 StartY=0.724089 StartZ=0 EndX=5.12518 EndY=2.12292 EndZ=0
    g19: LineSegment StartX=5.12518 StartY=2.12292 StartZ=0 EndX=4.4011 EndY=3.37708 EndZ=0
    g20: LineSegment StartX=4.4011 StartY=3.37708 StartZ=0 EndX=3.37708 EndY=4.4011 EndZ=0
    g21: LineSegment StartX=3.37708 StartY=4.4011 StartZ=0 EndX=2.12292 EndY=5.12518 EndZ=0
    g22: LineSegment StartX=2.12292 StartY=5.12518 StartZ=0 EndX=0.724089 EndY=5.5 EndZ=0
    g23: LineSegment StartX=0.724089 StartY=5.5 StartZ=0 EndX=-0.724089 EndY=5.5 EndZ=0
    g24: Circle CenterX=0 CenterY=0 CenterZ=0 NormalX=0 NormalY=0 NormalZ=1 AngleXU=0 Radius=5.54746
  constraints (52):
    c: Coincident(g0,g1)
    c: Coincident(g1,g2)
    c: Coincident(g2,g3)
    c: Coincident(g3,g4)
    c: Coincident(g4,g5)
    c: Coincident(g5,g6)
    c: Coincident(g6,g7)
    c: Coincident(g7,g8)
    c: Coincident(g8,g9)
    c: Coincident(g9,g10)
    c: Coincident(g10,g11)
    c: Coincident(g11,g12)
    c: Coincident(g12,g13)
    c: Coincident(g13,g14)
    c: Coincident(g14,g15)
    c: Coincident(g15,g16)
    c: Coincident(g16,g17)
    c: Coincident(g17,g18)
    c: Coincident(g18,g19)
    c: Coincident(g19,g20)
    c: Coincident(g20,g21)
    c: Coincident(g21,g22)
    c: Coincident(g22,g23)
    c: Coincident(g23,g0)
    c: Equal(g0, g1-g23) x23
    c: PointOnObject(g0,g24)
    c: PointOnObject(g1,g24)
    c: PointOnObject(g2,g24)
    c: PointOnObject(g3,g24)
    c: PointOnObject(g4,g24)
    c: PointOnObject(g5,g24)
    c: PointOnObject(g6,g24)
    c: PointOnObject(g7,g24)
    c: PointOnObject(g8,g24)
    c: PointOnObject(g9,g24)
    c: PointOnObject(g10,g24)
    c: PointOnObject(g11,g24)
    c: PointOnObject(g12,g24)
    c: PointOnObject(g13,g24)
    c: PointOnObject(g14,g24)
    c: PointOnObject(g15,g24)
    c: PointOnObject(g16,g24)
    c: PointOnObject(g17,g24)
    c: PointOnObject(g18,g24)
    c: PointOnObject(g19,g24)
    c: PointOnObject(g20,g24)
    c: PointOnObject(g21,g24)
    c: PointOnObject(g22,g24)
    c: PointOnObject(g23,g24)
    c: Coincident(g24,g-1)
    c: Horizontal(g23)
    c: DistanceX(g4,g17) = 11
FEATURE [Sketcher::SketchObject] Sketch460
  FullyConstrained = false
  MapMode = 5
  Support = -> [XY_Plane908]
  sketch-geometry (25):
    g0: LineSegment StartX=-0.789915 StartY=6 StartZ=0 EndX=-2.31591 EndY=5.59111 EndZ=0
    g1: LineSegment StartX=-2.31591 StartY=5.59111 StartZ=0 EndX=-3.68409 EndY=4.80119 EndZ=0
    g2: LineSegment StartX=-3.68409 StartY=4.80119 StartZ=0 EndX=-4.80119 EndY=3.68409 EndZ=0
    g3: LineSegment StartX=-4.80119 StartY=3.68409 StartZ=0 EndX=-5.59111 EndY=2.31591 EndZ=0
    g4: LineSegment StartX=-5.59111 StartY=2.31591 StartZ=0 EndX=-6 EndY=0.789915 EndZ=0
    g5: LineSegment StartX=-6 StartY=0.789915 StartZ=0 EndX=-6 EndY=-0.789915 EndZ=0
    g6: LineSegment StartX=-6 StartY=-0.789915 StartZ=0 EndX=-5.59111 EndY=-2.31591 EndZ=0
    g7: LineSegment StartX=-5.59111 StartY=-2.31591 StartZ=0 EndX=-4.80119 EndY=-3.68409 EndZ=0
    g8: LineSegment StartX=-4.80119 StartY=-3.68409 StartZ=0 EndX=-3.68409 EndY=-4.80119 EndZ=0
    g9: LineSegment StartX=-3.68409 StartY=-4.80119 StartZ=0 EndX=-2.31591 EndY=-5.59111 EndZ=0
    g10: LineSegment StartX=-2.31591 StartY=-5.59111 StartZ=0 EndX=-0.789915 EndY=-6 EndZ=0
    g11: LineSegment StartX=-0.789915 StartY=-6 StartZ=0 EndX=0.789915 EndY=-6 EndZ=0
    g12: LineSegment StartX=0.789915 StartY=-6 StartZ=0 EndX=2.31591 EndY=-5.59111 EndZ=0
    g13: LineSegment StartX=2.31591 StartY=-5.59111 StartZ=0 EndX=3.68409 EndY=-4.80119 EndZ=0
    g14: LineSegment StartX=3.68409 StartY=-4.80119 StartZ=0 EndX=4.80119 EndY=-3.68409 EndZ=0
    g15: LineSegment StartX=4.80119 StartY=-3.68409 StartZ=0 EndX=5.59111 EndY=-2.31591 EndZ=0
    g16: LineSegment StartX=5.59111 StartY=-2.31591 StartZ=0 EndX=6 EndY=-0.789915 EndZ=0
    g17: LineSegment StartX=6 StartY=-0.789915 StartZ=0 EndX=6 EndY=0.789915 EndZ=0
    g18: LineSegment StartX=6 StartY=0.789915 StartZ=0 EndX=5.59111 EndY=2.31591 EndZ=0
    g19: LineSegment StartX=5.59111 StartY=2.31591 StartZ=0 EndX=4.80119 EndY=3.68409 EndZ=0
    g20: LineSegment StartX=4.80119 StartY=3.68409 StartZ=0 EndX=3.68409 EndY=4.80119 EndZ=0
    g21: LineSegment StartX=3.68409 StartY=4.80119 StartZ=0 EndX=2.31591 EndY=5.59111 EndZ=0
    g22: LineSegment StartX=2.31591 StartY=5.59111 StartZ=0 EndX=0.789915 EndY=6 EndZ=0
    g23: LineSegment StartX=0.789915 StartY=6 StartZ=0 EndX=-0.789915 EndY=6 EndZ=0
    g24: Circle CenterX=0 CenterY=0 CenterZ=0 NormalX=0 NormalY=0 NormalZ=1 AngleXU=0 Radius=6.05177
  constraints (52):
    c: Coincident(g0,g1)
    c: Coincident(g1,g2)
    c: Coincident(g2,g3)
    c: Coincident(g3,g4)
    c: Coincident(g4,g5)
    c: Coincident(g5,g6)
    c: Coincident(g6,g7)
    c: Coincident(g7,g8)
    c: Coincident(g8,g9)
    c: Coincident(g9,g10)
    c: Coincident(g10,g11)
    c: Coincident(g11,g12)
    c: Coincident(g12,g13)
    c: Coincident(g13,g14)
    c: Coincident(g14,g15)
    c: Coincident(g15,g16)
    c: Coincident(g16,g17)
    c: Coincident(g17,g18)
    c: Coincident(g18,g19)
    c: Coincident(g19,g20)
    c: Coincident(g20,g21)
    c: Coincident(g21,g22)
    c: Coincident(g22,g23)
    c: Coincident(g23,g0)
    c: Equal(g0, g1-g23) x23
    c: PointOnObject(g0,g24)
    c: PointOnObject(g1,g24)
    c: PointOnObject(g2,g24)
    c: PointOnObject(g3,g24)
    c: PointOnObject(g4,g24)
    c: PointOnObject(g5,g24)
    c: PointOnObject(g6,g24)
    c: PointOnObject(g7,g24)
    c: PointOnObject(g8,g24)
    c: PointOnObject(g9,g24)
    c: PointOnObject(g10,g24)
    c: PointOnObject(g11,g24)
    c: PointOnObject(g12,g24)
    c: PointOnObject(g13,g24)
    c: PointOnObject(g14,g24)
    c: PointOnObject(g15,g24)
    c: PointOnObject(g16,g24)
    c: PointOnObject(g17,g24)
    c: PointOnObject(g18,g24)
    c: PointOnObject(g19,g24)
    c: PointOnObject(g20,g24)
    c: PointOnObject(g21,g24)
    c: PointOnObject(g22,g24)
    c: PointOnObject(g23,g24)
    c: Coincident(g24,g-1)
    c: Horizontal(g23)
    c: DistanceX(g4,g17) = 12
FEATURE [PartDesign::AdditiveLoft] AdditiveLoft038
  AllowMultiFace = false
  Closed = false
  Profile = -> Sketch460
  Refine = true
  Ruled = false
  Sections = -> [Sketch455,Sketch451]
FEATURE [Sketcher::SketchObject] Sketch459
  FullyConstrained = false
  MapMode = 5
  Placement = pos=(0,0,17) rot=(0,0,1;0rad)
  Support = -> [AdditiveLoft038]
  sketch-geometry (1):
    g0: Circle CenterX=0 CenterY=0 CenterZ=0 NormalX=0 NormalY=0 NormalZ=1 AngleXU=0 Radius=4.5
  constraints (2):
    c: Coincident(g0,g-1)
    c: Radius(g0) = 4.5
FEATURE [PartDesign::Pad] Pad084
  AllowMultiFace = false
  BaseFeature = -> AdditiveLoft038
  Direction = (1,1,1)
  Length = 0.7
  Length2 = 100
  Profile = -> Sketch459
  Refine = true
  Type = 0
FEATURE [Sketcher::SketchObject] Sketch458
  FullyConstrained = false
  MapMode = 5
  Placement = pos=(0,0,0) rot=(1,0,0;3.14159rad)
  Support = -> [Pad084]
  sketch-geometry (1):
    g0: Circle CenterX=0 CenterY=0 CenterZ=0 NormalX=0 NormalY=0 NormalZ=1 AngleXU=0 Radius=5
  constraints (2):
    c: Coincident(g0,g-1)
    c: Radius(g0) = 5
FEATURE [PartDesign::Pocket] Pocket091
  AllowMultiFace = false
  BaseFeature = -> Pad084
  Direction = (1,1,1)
  Length = 1
  Length2 = 100
  Profile = -> Sketch458
  Refine = true
  Type = 0
FEATURE [Sketcher::SketchObject] Sketch449
  FullyConstrained = false
  MapMode = 5
  Placement = pos=(0,0,1) rot=(1,0,0;3.14159rad)
  Support = -> [Pocket091]
  sketch-geometry (1):
    g0: Circle CenterX=0 CenterY=0 CenterZ=0 NormalX=0 NormalY=0 NormalZ=1 AngleXU=0 Radius=4.65
  constraints (2):
    c: Coincident(g0,g-1)
    c: Radius(g0) = 4.65
FEATURE [PartDesign::Pocket] Pocket089
  AllowMultiFace = false
  BaseFeature = -> Pocket091
  Direction = (1,1,1)
  Length = 1
  Length2 = 100
  Profile = -> Sketch449
  Refine = true
  Type = 0
FEATURE [Sketcher::SketchObject] Sketch447
  FullyConstrained = false
  MapMode = 5
  Placement = pos=(0,0,2) rot=(1,0,0;3.14159rad)
  Support = -> [Pocket089]
  sketch-geometry (2):
    g0: ArcOfCircle CenterX=0 CenterY=0 CenterZ=0 NormalX=0 NormalY=0 NormalZ=1 AngleXU=0 Radius=3 StartAngle=2.19024 EndAngle=7.23453
    g1: LineSegment StartX=-1.74176 StartY=2.4426 StartZ=0 EndX=1.74176 EndY=2.4426 EndZ=0
  constraints (5):
    c: Coincident(g0,g-1)
    c: Coincident(g1,g0)
    c: Coincident(g1,g0)
    c: Horizontal(g1)
    c: Radius(g0) = 3
FEATURE [Sketcher::SketchObject] Sketch462
  FullyConstrained = false
  MapMode = 5
  Support = -> [XY_Plane904]
  sketch-geometry (25):
    g0: LineSegment StartX=-0.789915 StartY=6 StartZ=0 EndX=-2.31591 EndY=5.59111 EndZ=0
    g1: LineSegment StartX=-2.31591 StartY=5.59111 StartZ=0 EndX=-3.68409 EndY=4.80119 EndZ=0
    g2: LineSegment StartX=-3.68409 StartY=4.80119 StartZ=0 EndX=-4.80119 EndY=3.68409 EndZ=0
    g3: LineSegment StartX=-4.80119 StartY=3.68409 StartZ=0 EndX=-5.59111 EndY=2.31591 EndZ=0
    g4: LineSegment StartX=-5.59111 StartY=2.31591 StartZ=0 EndX=-6 EndY=0.789915 EndZ=0
    g5: LineSegment StartX=-6 StartY=0.789915 StartZ=0 EndX=-6 EndY=-0.789915 EndZ=0
    g6: LineSegment StartX=-6 StartY=-0.789915 StartZ=0 EndX=-5.59111 EndY=-2.31591 EndZ=0
    g7: LineSegment StartX=-5.59111 StartY=-2.31591 StartZ=0 EndX=-4.80119 EndY=-3.68409 EndZ=0
    g8: LineSegment StartX=-4.80119 StartY=-3.68409 StartZ=0 EndX=-3.68409 EndY=-4.80119 EndZ=0
    g9: LineSegment StartX=-3.68409 StartY=-4.80119 StartZ=0 EndX=-2.31591 EndY=-5.59111 EndZ=0
    g10: LineSegment StartX=-2.31591 StartY=-5.59111 StartZ=0 EndX=-0.789915 EndY=-6 EndZ=0
    g11: LineSegment StartX=-0.789915 StartY=-6 StartZ=0 EndX=0.789915 EndY=-6 EndZ=0
    g12: LineSegment StartX=0.789915 StartY=-6 StartZ=0 EndX=2.31591 EndY=-5.59111 EndZ=0
    g13: LineSegment StartX=2.31591 StartY=-5.59111 StartZ=0 EndX=3.68409 EndY=-4.80119 EndZ=0
    g14: LineSegment StartX=3.68409 StartY=-4.80119 StartZ=0 EndX=4.80119 EndY=-3.68409 EndZ=0
    g15: LineSegment StartX=4.80119 StartY=-3.68409 StartZ=0 EndX=5.59111 EndY=-2.31591 EndZ=0
    g16: LineSegment StartX=5.59111 StartY=-2.31591 StartZ=0 EndX=6 EndY=-0.789915 EndZ=0
    g17: LineSegment StartX=6 StartY=-0.789915 StartZ=0 EndX=6 EndY=0.789915 EndZ=0
    g18: LineSegment StartX=6 StartY=0.789915 StartZ=0 EndX=5.59111 EndY=2.31591 EndZ=0
    g19: LineSegment StartX=5.59111 StartY=2.31591 StartZ=0 EndX=4.80119 EndY=3.68409 EndZ=0
    g20: LineSegment StartX=4.80119 StartY=3.68409 StartZ=0 EndX=3.68409 EndY=4.80119 EndZ=0
    g21: LineSegment StartX=3.68409 StartY=4.80119 StartZ=0 EndX=2.31591 EndY=5.59111 EndZ=0
    g22: LineSegment StartX=2.31591 StartY=5.59111 StartZ=0 EndX=0.789915 EndY=6 EndZ=0
    g23: LineSegment StartX=0.789915 StartY=6 StartZ=0 EndX=-0.789915 EndY=6 EndZ=0
    g24: Circle CenterX=0 CenterY=0 CenterZ=0 NormalX=0 NormalY=0 NormalZ=1 AngleXU=0 Radius=6.05177
  constraints (52):
    c: Coincident(g0,g1)
    c: Coincident(g1,g2)
    c: Coincident(g2,g3)
    c: Coincident(g3,g4)
    c: Coincident(g4,g5)
    c: Coincident(g5,g6)
    c: Coincident(g6,g7)
    c: Coincident(g7,g8)
    c: Coincident(g8,g9)
    c: Coincident(g9,g10)
    c: Coincident(g10,g11)
    c: Coincident(g11,g12)
    c: Coincident(g12,g13)
    c: Coincident(g13,g14)
    c: Coincident(g14,g15)
    c: Coincident(g15,g16)
    c: Coincident(g16,g17)
    c: Coincident(g17,g18)
    c: Coincident(g18,g19)
    c: Coincident(g19,g20)
    c: Coincident(g20,g21)
    c: Coincident(g21,g22)
    c: Coincident(g22,g23)
    c: Coincident(g23,g0)
    c: Equal(g0, g1-g23) x23
    c: PointOnObject(g0,g24)
    c: PointOnObject(g1,g24)
    c: PointOnObject(g2,g24)
    c: PointOnObject(g3,g24)
    c: PointOnObject(g4,g24)
    c: PointOnObject(g5,g24)
    c: PointOnObject(g6,g24)
    c: PointOnObject(g7,g24)
    c: PointOnObject(g8,g24)
    c: PointOnObject(g9,g24)
    c: PointOnObject(g10,g24)
    c: PointOnObject(g11,g24)
    c: PointOnObject(g12,g24)
    c: PointOnObject(g13,g24)
    c: PointOnObject(g14,g24)
    c: PointOnObject(g15,g24)
    c: PointOnObject(g16,g24)
    c: PointOnObject(g17,g24)
    c: PointOnObject(g18,g24)
    c: PointOnObject(g19,g24)
    c: PointOnObject(g20,g24)
    c: PointOnObject(g21,g24)
    c: PointOnObject(g22,g24)
    c: PointOnObject(g23,g24)
    c: Coincident(g24,g-1)
    c: Horizontal(g23)
    c: DistanceX(g4,g17) = 12
FEATURE [PartDesign::AdditiveLoft] AdditiveLoft032
  AllowMultiFace = false
  Closed = false
  Profile = -> Sketch462
  Refine = true
  Ruled = false
  Sections = -> [Sketch450,Sketch452]
FEATURE [Sketcher::SketchObject] Sketch446
  FullyConstrained = false
  MapMode = 5
  Placement = pos=(0,0,17) rot=(0,0,1;0rad)
  Support = -> [AdditiveLoft032]
  sketch-geometry (1):
    g0: Circle CenterX=0 CenterY=0 CenterZ=0 NormalX=0 NormalY=0 NormalZ=1 AngleXU=0 Radius=4.5
  constraints (2):
    c: Coincident(g0,g-1)
    c: Radius(g0) = 4.5
FEATURE [PartDesign::Pad] Pad087
  AllowMultiFace = false
  BaseFeature = -> AdditiveLoft032
  Direction = (1,1,1)
  Length = 0.7
  Length2 = 100
  Profile = -> Sketch446
  Refine = true
  Type = 0
FEATURE [Sketcher::SketchObject] Sketch448
  FullyConstrained = false
  MapMode = 5
  Placement = pos=(0,0,0) rot=(1,0,0;3.14159rad)
  Support = -> [Pad087]
  sketch-geometry (1):
    g0: Circle CenterX=0 CenterY=0 CenterZ=0 NormalX=0 NormalY=0 NormalZ=1 AngleXU=0 Radius=5
  constraints (2):
    c: Coincident(g0,g-1)
    c: Radius(g0) = 5
FEATURE [PartDesign::Pocket] Pocket086
  AllowMultiFace = false
  BaseFeature = -> Pad087
  Direction = (1,1,1)
  Length = 1
  Length2 = 100
  Profile = -> Sketch448
  Refine = true
  Type = 0
FEATURE [Sketcher::SketchObject] Sketch445
  FullyConstrained = false
  MapMode = 5
  Placement = pos=(0,0,1) rot=(1,0,0;3.14159rad)
  Support = -> [Pocket086]
  sketch-geometry (1):
    g0: Circle CenterX=0 CenterY=0 CenterZ=0 NormalX=0 NormalY=0 NormalZ=1 AngleXU=0 Radius=4.65
  constraints (2):
    c: Coincident(g0,g-1)
    c: Radius(g0) = 4.65
FEATURE [PartDesign::Pocket] Pocket088
  AllowMultiFace = false
  BaseFeature = -> Pocket086
  Direction = (1,1,1)
  Length = 1
  Length2 = 100
  Profile = -> Sketch445
  Refine = true
  Type = 0
FEATURE [Sketcher::SketchObject] Sketch444
  FullyConstrained = false
  MapMode = 5
  Placement = pos=(0,0,2) rot=(1,0,0;3.14159rad)
  Support = -> [Pocket088]
  sketch-geometry (2):
    g0: ArcOfCircle CenterX=0 CenterY=0 CenterZ=0 NormalX=0 NormalY=0 NormalZ=1 AngleXU=0 Radius=3 StartAngle=2.19024 EndAngle=7.23453
    g1: LineSegment StartX=-1.74176 StartY=2.4426 StartZ=0 EndX=1.74176 EndY=2.4426 EndZ=0
  constraints (5):
    c: Coincident(g0,g-1)
    c: Coincident(g1,g0)
    c: Coincident(g1,g0)
    c: Horizontal(g1)
    c: Radius(g0) = 3
FEATURE [PartDesign::Pocket] Pocket085
  AllowMultiFace = false
  BaseFeature = -> Pocket088
  Direction = (1,1,1)
  Length = 8
  Length2 = 100
  Profile = -> Sketch444
  Refine = true
  Type = 0
FEATURE [PartDesign::Chamfer] Chamfer070
  Angle = 45
  Base = -> Pocket085 [Edge82,Edge83]
  BaseFeature = -> Pocket085
  ChamferType = 0
  FlipDirection = false
  Size = 1.4
  Size2 = 1
  SupportTransform = false
  UseAllEdges = false
FEATURE [PartDesign::Chamfer] Chamfer059
  Angle = 45
  Base = -> Chamfer070 [Edge8]
  BaseFeature = -> Chamfer070
  ChamferType = 0
  FlipDirection = false
  Size = 0.3
  Size2 = 1
  SupportTransform = false
  UseAllEdges = false
FEATURE [PartDesign::Fillet] Fillet032
  Base = -> Chamfer059 [Edge93,Face36]
  BaseFeature = -> Chamfer059
  Radius = 0.1
  SupportTransform = false
  UseAllEdges = false
FEATURE [PartDesign::Body] Body170
  Group = -> [Sketch462,Sketch450,Sketch452,AdditiveLoft032,Sketch446,Pad087,Sketch448,Pocket086,Sketch445,Pocket088,Sketch444,Pocket085,Chamfer070,Chamfer059,Fillet032]
  Origin = -> Origin953
  Tip = -> Fillet032
FEATURE [App::Part] Part148  label="Cap041"
  Group = -> [Body170]
  Origin = -> Origin942
  Placement = pos=(-40.005,-40.005,0) rot=(0,0,1;0rad)
  expr: .Placement.Base.x = -40.005
  expr: .Placement.Base.y = -40.005
FEATURE [Sketcher::SketchObject] Sketch466
  AttachmentOffset = pos=(0,0,17) rot=(0,0,1;0rad)
  FullyConstrained = false
  MapMode = 5
  Placement = pos=(0,0,17) rot=(0,0,1;0rad)
  Support = -> [XY_Plane912]
  sketch-geometry (25):
    g0: LineSegment StartX=-4.65926 StartY=1.92993 StartZ=0 EndX=-5 EndY=0.658262 EndZ=0
    g1: LineSegment StartX=-5 StartY=0.658262 StartZ=0 EndX=-5 EndY=-0.658262 EndZ=0
    g2: LineSegment StartX=-5 StartY=-0.658262 StartZ=0 EndX=-4.65926 EndY=-1.92993 EndZ=0
    g3: LineSegment StartX=-4.65926 StartY=-1.92993 StartZ=0 EndX=-4.001 EndY=-3.07007 EndZ=0
    g4: LineSegment StartX=-4.001 StartY=-3.07007 StartZ=0 EndX=-3.07007 EndY=-4.001 EndZ=0
    g5: LineSegment StartX=-3.07007 StartY=-4.001 StartZ=0 EndX=-1.92993 EndY=-4.65926 EndZ=0
    g6: LineSegment StartX=-1.92993 StartY=-4.65926 StartZ=0 EndX=-0.658262 EndY=-5 EndZ=0
    g7: LineSegment StartX=-0.658262 StartY=-5 StartZ=0 EndX=0.658262 EndY=-5 EndZ=0
    g8: LineSegment StartX=0.658262 StartY=-5 StartZ=0 EndX=1.92993 EndY=-4.65926 EndZ=0
    g9: LineSegment StartX=1.92993 StartY=-4.65926 StartZ=0 EndX=3.07007 EndY=-4.001 EndZ=0
    g10: LineSegment StartX=3.07007 StartY=-4.001 StartZ=0 EndX=4.001 EndY=-3.07007 EndZ=0
    g11: LineSegment StartX=4.001 StartY=-3.07007 StartZ=0 EndX=4.65926 EndY=-1.92993 EndZ=0
    g12: LineSegment StartX=4.65926 StartY=-1.92993 StartZ=0 EndX=5 EndY=-0.658262 EndZ=0
    g13: LineSegment StartX=5 StartY=-0.658262 StartZ=0 EndX=5 EndY=0.658262 EndZ=0
    g14: LineSegment StartX=5 StartY=0.658262 StartZ=0 EndX=4.65926 EndY=1.92993 EndZ=0
    g15: LineSegment StartX=4.65926 StartY=1.92993 StartZ=0 EndX=4.001 EndY=3.07007 EndZ=0
    g16: LineSegment StartX=4.001 StartY=3.07007 StartZ=0 EndX=3.07007 EndY=4.001 EndZ=0
    g17: LineSegment StartX=3.07007 StartY=4.001 StartZ=0 EndX=1.92993 EndY=4.65926 EndZ=0
    g18: LineSegment StartX=1.92993 StartY=4.65926 StartZ=0 EndX=0.658262 EndY=5 EndZ=0
    g19: LineSegment StartX=0.658262 StartY=5 StartZ=0 EndX=-0.658262 EndY=5 EndZ=0
    g20: LineSegment StartX=-0.658262 StartY=5 StartZ=0 EndX=-1.92993 EndY=4.65926 EndZ=0
    g21: LineSegment StartX=-1.92993 StartY=4.65926 StartZ=0 EndX=-3.07007 EndY=4.001 EndZ=0
    g22: LineSegment StartX=-3.07007 StartY=4.001 StartZ=0 EndX=-4.001 EndY=3.07007 EndZ=0
    g23: LineSegment StartX=-4.001 StartY=3.07007 StartZ=0 EndX=-4.65926 EndY=1.92993 EndZ=0
    g24: Circle CenterX=0 CenterY=0 CenterZ=0 NormalX=0 NormalY=0 NormalZ=1 AngleXU=0 Radius=5.04314
  constraints (52):
    c: Coincident(g0,g1)
    c: Coincident(g1,g2)
    c: Coincident(g2,g3)
    c: Coincident(g3,g4)
    c: Coincident(g4,g5)
    c: Coincident(g5,g6)
    c: Coincident(g6,g7)
    c: Coincident(g7,g8)
    c: Coincident(g8,g9)
    c: Coincident(g9,g10)
    c: Coincident(g10,g11)
    c: Coincident(g11,g12)
    c: Coincident(g12,g13)
    c: Coincident(g13,g14)
    c: Coincident(g14,g15)
    c: Coincident(g15,g16)
    c: Coincident(g16,g17)
    c: Coincident(g17,g18)
    c: Coincident(g18,g19)
    c: Coincident(g19,g20)
    c: Coincident(g20,g21)
    c: Coincident(g21,g22)
    c: Coincident(g22,g23)
    c: Coincident(g23,g0)
    c: Equal(g0, g1-g23) x23
    c: PointOnObject(g0,g24)
    c: PointOnObject(g1,g24)
    c: PointOnObject(g2,g24)
    c: PointOnObject(g3,g24)
    c: PointOnObject(g4,g24)
    c: PointOnObject(g5,g24)
    c: PointOnObject(g6,g24)
    c: PointOnObject(g7,g24)
    c: PointOnObject(g8,g24)
    c: PointOnObject(g9,g24)
    c: PointOnObject(g10,g24)
    c: PointOnObject(g11,g24)
    c: PointOnObject(g12,g24)
    c: PointOnObject(g13,g24)
    c: PointOnObject(g14,g24)
    c: PointOnObject(g15,g24)
    c: PointOnObject(g16,g24)
    c: PointOnObject(g17,g24)
    c: PointOnObject(g18,g24)
    c: PointOnObject(g19,g24)
    c: PointOnObject(g20,g24)
    c: PointOnObject(g21,g24)
    c: PointOnObject(g22,g24)
    c: PointOnObject(g23,g24)
    c: Coincident(g24,g-1)
    c: Horizontal(g19)
    c: DistanceX(g0,g13) = 10
FEATURE [Sketcher::SketchObject] Sketch467
  FullyConstrained = false
  MapMode = 5
  Support = -> [XY_Plane912]
  sketch-geometry (25):
    g0: LineSegment StartX=-0.789915 StartY=6 StartZ=0 EndX=-2.31591 EndY=5.59111 EndZ=0
    g1: LineSegment StartX=-2.31591 StartY=5.59111 StartZ=0 EndX=-3.68409 EndY=4.80119 EndZ=0
    g2: LineSegment StartX=-3.68409 StartY=4.80119 StartZ=0 EndX=-4.80119 EndY=3.68409 EndZ=0
    g3: LineSegment StartX=-4.80119 StartY=3.68409 StartZ=0 EndX=-5.59111 EndY=2.31591 EndZ=0
    g4: LineSegment StartX=-5.59111 StartY=2.31591 StartZ=0 EndX=-6 EndY=0.789915 EndZ=0
    g5: LineSegment StartX=-6 StartY=0.789915 StartZ=0 EndX=-6 EndY=-0.789915 EndZ=0
    g6: LineSegment StartX=-6 StartY=-0.789915 StartZ=0 EndX=-5.59111 EndY=-2.31591 EndZ=0
    g7: LineSegment StartX=-5.59111 StartY=-2.31591 StartZ=0 EndX=-4.80119 EndY=-3.68409 EndZ=0
    g8: LineSegment StartX=-4.80119 StartY=-3.68409 StartZ=0 EndX=-3.68409 EndY=-4.80119 EndZ=0
    g9: LineSegment StartX=-3.68409 StartY=-4.80119 StartZ=0 EndX=-2.31591 EndY=-5.59111 EndZ=0
    g10: LineSegment StartX=-2.31591 StartY=-5.59111 StartZ=0 EndX=-0.789915 EndY=-6 EndZ=0
    g11: LineSegment StartX=-0.789915 StartY=-6 StartZ=0 EndX=0.789915 EndY=-6 EndZ=0
    g12: LineSegment StartX=0.789915 StartY=-6 StartZ=0 EndX=2.31591 EndY=-5.59111 EndZ=0
    g13: LineSegment StartX=2.31591 StartY=-5.59111 StartZ=0 EndX=3.68409 EndY=-4.80119 EndZ=0
    g14: LineSegment StartX=3.68409 StartY=-4.80119 StartZ=0 EndX=4.80119 EndY=-3.68409 EndZ=0
    g15: LineSegment StartX=4.80119 StartY=-3.68409 StartZ=0 EndX=5.59111 EndY=-2.31591 EndZ=0
    g16: LineSegment StartX=5.59111 StartY=-2.31591 StartZ=0 EndX=6 EndY=-0.789915 EndZ=0
    g17: LineSegment StartX=6 StartY=-0.789915 StartZ=0 EndX=6 EndY=0.789915 EndZ=0
    g18: LineSegment StartX=6 StartY=0.789915 StartZ=0 EndX=5.59111 EndY=2.31591 EndZ=0
    g19: LineSegment StartX=5.59111 StartY=2.31591 StartZ=0 EndX=4.80119 EndY=3.68409 EndZ=0
    g20: LineSegment StartX=4.80119 StartY=3.68409 StartZ=0 EndX=3.68409 EndY=4.80119 EndZ=0
    g21: LineSegment StartX=3.68409 StartY=4.80119 StartZ=0 EndX=2.31591 EndY=5.59111 EndZ=0
    g22: LineSegment StartX=2.31591 StartY=5.59111 StartZ=0 EndX=0.789915 EndY=6 EndZ=0
    g23: LineSegment StartX=0.789915 StartY=6 StartZ=0 EndX=-0.789915 EndY=6 EndZ=0
    g24: Circle CenterX=0 CenterY=0 CenterZ=0 NormalX=0 NormalY=0 NormalZ=1 AngleXU=0 Radius=6.05177
  constraints (52):
    c: Coincident(g0,g1)
    c: Coincident(g1,g2)
    c: Coincident(g2,g3)
    c: Coincident(g3,g4)
    c: Coincident(g4,g5)
    c: Coincident(g5,g6)
    c: Coincident(g6,g7)
    c: Coincident(g7,g8)
    c: Coincident(g8,g9)
    c: Coincident(g9,g10)
    c: Coincident(g10,g11)
    c: Coincident(g11,g12)
    c: Coincident(g12,g13)
    c: Coincident(g13,g14)
    c: Coincident(g14,g15)
    c: Coincident(g15,g16)
    c: Coincident(g16,g17)
    c: Coincident(g17,g18)
    c: Coincident(g18,g19)
    c: Coincident(g19,g20)
    c: Coincident(g20,g21)
    c: Coincident(g21,g22)
    c: Coincident(g22,g23)
    c: Coincident(g23,g0)
    c: Equal(g0, g1-g23) x23
    c: PointOnObject(g0,g24)
    c: PointOnObject(g1,g24)
    c: PointOnObject(g2,g24)
    c: PointOnObject(g3,g24)
    c: PointOnObject(g4,g24)
    c: PointOnObject(g5,g24)
    c: PointOnObject(g6,g24)
    c: PointOnObject(g7,g24)
    c: PointOnObject(g8,g24)
    c: PointOnObject(g9,g24)
    c: PointOnObject(g10,g24)
    c: PointOnObject(g11,g24)
    c: PointOnObject(g12,g24)
    c: PointOnObject(g13,g24)
    c: PointOnObject(g14,g24)
    c: PointOnObject(g15,g24)
    c: PointOnObject(g16,g24)
    c: PointOnObject(g17,g24)
    c: PointOnObject(g18,g24)
    c: PointOnObject(g19,g24)
    c: PointOnObject(g20,g24)
    c: PointOnObject(g21,g24)
    c: PointOnObject(g22,g24)
    c: PointOnObject(g23,g24)
    c: Coincident(g24,g-1)
    c: Horizontal(g23)
    c: DistanceX(g4,g17) = 12
FEATURE [PartDesign::AdditiveLoft] AdditiveLoft035
  AllowMultiFace = false
  Closed = false
  Profile = -> Sketch467
  Refine = true
  Ruled = false
  Sections = -> [Sketch454,Sketch466]
FEATURE [Sketcher::SketchObject] Sketch456
  FullyConstrained = false
  MapMode = 5
  Placement = pos=(0,0,17) rot=(0,0,1;0rad)
  Support = -> [AdditiveLoft035]
  sketch-geometry (1):
    g0: Circle CenterX=0 CenterY=0 CenterZ=0 NormalX=0 NormalY=0 NormalZ=1 AngleXU=0 Radius=4.5
  constraints (2):
    c: Coincident(g0,g-1)
    c: Radius(g0) = 4.5
FEATURE [Sketcher::SketchObject] Sketch472
  AttachmentOffset = pos=(0,0,7) rot=(0,0,1;0rad)
  FullyConstrained = false
  MapMode = 5
  Placement = pos=(0,0,7) rot=(0,0,1;0rad)
  Support = -> [XY_Plane915]
  sketch-geometry (25):
    g0: LineSegment StartX=-0.724089 StartY=5.5 StartZ=0 EndX=-2.12292 EndY=5.12518 EndZ=0
    g1: LineSegment StartX=-2.12292 StartY=5.12518 StartZ=0 EndX=-3.37708 EndY=4.4011 EndZ=0
    g2: LineSegment StartX=-3.37708 StartY=4.4011 StartZ=0 EndX=-4.4011 EndY=3.37708 EndZ=0
    g3: LineSegment StartX=-4.4011 StartY=3.37708 StartZ=0 EndX=-5.12518 EndY=2.12292 EndZ=0
    g4: LineSegment StartX=-5.12518 StartY=2.12292 StartZ=0 EndX=-5.5 EndY=0.724089 EndZ=0
    g5: LineSegment StartX=-5.5 StartY=0.724089 StartZ=0 EndX=-5.5 EndY=-0.724089 EndZ=0
    g6: LineSegment StartX=-5.5 StartY=-0.724089 StartZ=0 EndX=-5.12518 EndY=-2.12292 EndZ=0
    g7: LineSegment StartX=-5.12518 StartY=-2.12292 StartZ=0 EndX=-4.4011 EndY=-3.37708 EndZ=0
    g8: LineSegment StartX=-4.4011 StartY=-3.37708 StartZ=0 EndX=-3.37708 EndY=-4.4011 EndZ=0
    g9: LineSegment StartX=-3.37708 StartY=-4.4011 StartZ=0 EndX=-2.12292 EndY=-5.12518 EndZ=0
    g10: LineSegment StartX=-2.12292 StartY=-5.12518 StartZ=0 EndX=-0.724089 EndY=-5.5 EndZ=0
    g11: LineSegment StartX=-0.724089 StartY=-5.5 StartZ=0 EndX=0.724089 EndY=-5.5 EndZ=0
    g12: LineSegment StartX=0.724089 StartY=-5.5 StartZ=0 EndX=2.12292 EndY=-5.12518 EndZ=0
    g13: LineSegment StartX=2.12292 StartY=-5.12518 StartZ=0 EndX=3.37708 EndY=-4.4011 EndZ=0
    g14: LineSegment StartX=3.37708 StartY=-4.4011 StartZ=0 EndX=4.4011 EndY=-3.37708 EndZ=0
    g15: LineSegment StartX=4.4011 StartY=-3.37708 StartZ=0 EndX=5.12518 EndY=-2.12292 EndZ=0
    g16: LineSegment StartX=5.12518 StartY=-2.12292 StartZ=0 EndX=5.5 EndY=-0.724089 EndZ=0
    g17: LineSegment StartX=5.5 StartY=-0.724089 StartZ=0 EndX=5.5 EndY=0.724089 EndZ=0
    g18: LineSegment StartX=5.5 StartY=0.724089 StartZ=0 EndX=5.12518 EndY=2.12292 EndZ=0
    g19: LineSegment StartX=5.12518 StartY=2.12292 StartZ=0 EndX=4.4011 EndY=3.37708 EndZ=0
    g20: LineSegment StartX=4.4011 StartY=3.37708 StartZ=0 EndX=3.37708 EndY=4.4011 EndZ=0
    g21: LineSegment StartX=3.37708 StartY=4.4011 StartZ=0 EndX=2.12292 EndY=5.12518 EndZ=0
    g22: LineSegment StartX=2.12292 StartY=5.12518 StartZ=0 EndX=0.724089 EndY=5.5 EndZ=0
    g23: LineSegment StartX=0.724089 StartY=5.5 StartZ=0 EndX=-0.724089 EndY=5.5 EndZ=0
    g24: Circle CenterX=0 CenterY=0 CenterZ=0 NormalX=0 NormalY=0 NormalZ=1 AngleXU=0 Radius=5.54746
  constraints (52):
    c: Coincident(g0,g1)
    c: Coincident(g1,g2)
    c: Coincident(g2,g3)
    c: Coincident(g3,g4)
    c: Coincident(g4,g5)
    c: Coincident(g5,g6)
    c: Coincident(g6,g7)
    c: Coincident(g7,g8)
    c: Coincident(g8,g9)
    c: Coincident(g9,g10)
    c: Coincident(g10,g11)
    c: Coincident(g11,g12)
    c: Coincident(g12,g13)
    c: Coincident(g13,g14)
    c: Coincident(g14,g15)
    c: Coincident(g15,g16)
    c: Coincident(g16,g17)
    c: Coincident(g17,g18)
    c: Coincident(g18,g19)
    c: Coincident(g19,g20)
    c: Coincident(g20,g21)
    c: Coincident(g21,g22)
    c: Coincident(g22,g23)
    c: Coincident(g23,g0)
    c: Equal(g0, g1-g23) x23
    c: PointOnObject(g0,g24)
    c: PointOnObject(g1,g24)
    c: PointOnObject(g2,g24)
    c: PointOnObject(g3,g24)
    c: PointOnObject(g4,g24)
    c: PointOnObject(g5,g24)
    c: PointOnObject(g6,g24)
    c: PointOnObject(g7,g24)
    c: PointOnObject(g8,g24)
    c: PointOnObject(g9,g24)
    c: PointOnObject(g10,g24)
    c: PointOnObject(g11,g24)
    c: PointOnObject(g12,g24)
    c: PointOnObject(g13,g24)
    c: PointOnObject(g14,g24)
    c: PointOnObject(g15,g24)
    c: PointOnObject(g16,g24)
    c: PointOnObject(g17,g24)
    c: PointOnObject(g18,g24)
    c: PointOnObject(g19,g24)
    c: PointOnObject(g20,g24)
    c: PointOnObject(g21,g24)
    c: PointOnObject(g22,g24)
    c: PointOnObject(g23,g24)
    c: Coincident(g24,g-1)
    c: Horizontal(g23)
    c: DistanceX(g4,g17) = 11
FEATURE [Sketcher::SketchObject] Sketch473
  FullyConstrained = false
  MapMode = 5
  Support = -> [XY_Plane915]
  sketch-geometry (25):
    g0: LineSegment StartX=-0.789915 StartY=6 StartZ=0 EndX=-2.31591 EndY=5.59111 EndZ=0
    g1: LineSegment StartX=-2.31591 StartY=5.59111 StartZ=0 EndX=-3.68409 EndY=4.80119 EndZ=0
    g2: LineSegment StartX=-3.68409 StartY=4.80119 StartZ=0 EndX=-4.80119 EndY=3.68409 EndZ=0
    g3: LineSegment StartX=-4.80119 StartY=3.68409 StartZ=0 EndX=-5.59111 EndY=2.31591 EndZ=0
    g4: LineSegment StartX=-5.59111 StartY=2.31591 StartZ=0 EndX=-6 EndY=0.789915 EndZ=0
    g5: LineSegment StartX=-6 StartY=0.789915 StartZ=0 EndX=-6 EndY=-0.789915 EndZ=0
    g6: LineSegment StartX=-6 StartY=-0.789915 StartZ=0 EndX=-5.59111 EndY=-2.31591 EndZ=0
    g7: LineSegment StartX=-5.59111 StartY=-2.31591 StartZ=0 EndX=-4.80119 EndY=-3.68409 EndZ=0
    g8: LineSegment StartX=-4.80119 StartY=-3.68409 StartZ=0 EndX=-3.68409 EndY=-4.80119 EndZ=0
    g9: LineSegment StartX=-3.68409 StartY=-4.80119 StartZ=0 EndX=-2.31591 EndY=-5.59111 EndZ=0
    g10: LineSegment StartX=-2.31591 StartY=-5.59111 StartZ=0 EndX=-0.789915 EndY=-6 EndZ=0
    g11: LineSegment StartX=-0.789915 StartY=-6 StartZ=0 EndX=0.789915 EndY=-6 EndZ=0
    g12: LineSegment StartX=0.789915 StartY=-6 StartZ=0 EndX=2.31591 EndY=-5.59111 EndZ=0
    g13: LineSegment StartX=2.31591 StartY=-5.59111 StartZ=0 EndX=3.68409 EndY=-4.80119 EndZ=0
    g14: LineSegment StartX=3.68409 StartY=-4.80119 StartZ=0 EndX=4.80119 EndY=-3.68409 EndZ=0
    g15: LineSegment StartX=4.80119 StartY=-3.68409 StartZ=0 EndX=5.59111 EndY=-2.31591 EndZ=0
    g16: LineSegment StartX=5.59111 StartY=-2.31591 StartZ=0 EndX=6 EndY=-0.789915 EndZ=0
    g17: LineSegment StartX=6 StartY=-0.789915 StartZ=0 EndX=6 EndY=0.789915 EndZ=0
    g18: LineSegment StartX=6 StartY=0.789915 StartZ=0 EndX=5.59111 EndY=2.31591 EndZ=0
    g19: LineSegment StartX=5.59111 StartY=2.31591 StartZ=0 EndX=4.80119 EndY=3.68409 EndZ=0
    g20: LineSegment StartX=4.80119 StartY=3.68409 StartZ=0 EndX=3.68409 EndY=4.80119 EndZ=0
    g21: LineSegment StartX=3.68409 StartY=4.80119 StartZ=0 EndX=2.31591 EndY=5.59111 EndZ=0
    g22: LineSegment StartX=2.31591 StartY=5.59111 StartZ=0 EndX=0.789915 EndY=6 EndZ=0
    g23: LineSegment StartX=0.789915 StartY=6 StartZ=0 EndX=-0.789915 EndY=6 EndZ=0
    g24: Circle CenterX=0 CenterY=0 CenterZ=0 NormalX=0 NormalY=0 NormalZ=1 AngleXU=0 Radius=6.05177
  constraints (52):
    c: Coincident(g0,g1)
    c: Coincident(g1,g2)
    c: Coincident(g2,g3)
    c: Coincident(g3,g4)
    c: Coincident(g4,g5)
    c: Coincident(g5,g6)
    c: Coincident(g6,g7)
    c: Coincident(g7,g8)
    c: Coincident(g8,g9)
    c: Coincident(g9,g10)
    c: Coincident(g10,g11)
    c: Coincident(g11,g12)
    c: Coincident(g12,g13)
    c: Coincident(g13,g14)
    c: Coincident(g14,g15)
    c: Coincident(g15,g16)
    c: Coincident(g16,g17)
    c: Coincident(g17,g18)
    c: Coincident(g18,g19)
    c: Coincident(g19,g20)
    c: Coincident(g20,g21)
    c: Coincident(g21,g22)
    c: Coincident(g22,g23)
    c: Coincident(g23,g0)
    c: Equal(g0, g1-g23) x23
    c: PointOnObject(g0,g24)
    c: PointOnObject(g1,g24)
    c: PointOnObject(g2,g24)
    c: PointOnObject(g3,g24)
    c: PointOnObject(g4,g24)
    c: PointOnObject(g5,g24)
    c: PointOnObject(g6,g24)
    c: PointOnObject(g7,g24)
    c: PointOnObject(g8,g24)
    c: PointOnObject(g9,g24)
    c: PointOnObject(g10,g24)
    c: PointOnObject(g11,g24)
    c: PointOnObject(g12,g24)
    c: PointOnObject(g13,g24)
    c: PointOnObject(g14,g24)
    c: PointOnObject(g15,g24)
    c: PointOnObject(g16,g24)
    c: PointOnObject(g17,g24)
    c: PointOnObject(g18,g24)
    c: PointOnObject(g19,g24)
    c: PointOnObject(g20,g24)
    c: PointOnObject(g21,g24)
    c: PointOnObject(g22,g24)
    c: PointOnObject(g23,g24)
    c: Coincident(g24,g-1)
    c: Horizontal(g23)
    c: DistanceX(g4,g17) = 12
FEATURE [Sketcher::SketchObject] Sketch474
  AttachmentOffset = pos=(0,0,17) rot=(0,0,1;0rad)
  FullyConstrained = false
  MapMode = 5
  Placement = pos=(0,0,17) rot=(0,0,1;0rad)
  Support = -> [XY_Plane915]
  sketch-geometry (25):
    g0: LineSegment StartX=-4.65926 StartY=1.92993 StartZ=0 EndX=-5 EndY=0.658262 EndZ=0
    g1: LineSegment StartX=-5 StartY=0.658262 StartZ=0 EndX=-5 EndY=-0.658262 EndZ=0
    g2: LineSegment StartX=-5 StartY=-0.658262 StartZ=0 EndX=-4.65926 EndY=-1.92993 EndZ=0
    g3: LineSegment StartX=-4.65926 StartY=-1.92993 StartZ=0 EndX=-4.001 EndY=-3.07007 EndZ=0
    g4: LineSegment StartX=-4.001 StartY=-3.07007 StartZ=0 EndX=-3.07007 EndY=-4.001 EndZ=0
    g5: LineSegment StartX=-3.07007 StartY=-4.001 StartZ=0 EndX=-1.92993 EndY=-4.65926 EndZ=0
    g6: LineSegment StartX=-1.92993 StartY=-4.65926 StartZ=0 EndX=-0.658262 EndY=-5 EndZ=0
    g7: LineSegment StartX=-0.658262 StartY=-5 StartZ=0 EndX=0.658262 EndY=-5 EndZ=0
    g8: LineSegment StartX=0.658262 StartY=-5 StartZ=0 EndX=1.92993 EndY=-4.65926 EndZ=0
    g9: LineSegment StartX=1.92993 StartY=-4.65926 StartZ=0 EndX=3.07007 EndY=-4.001 EndZ=0
    g10: LineSegment StartX=3.07007 StartY=-4.001 StartZ=0 EndX=4.001 EndY=-3.07007 EndZ=0
    g11: LineSegment StartX=4.001 StartY=-3.07007 StartZ=0 EndX=4.65926 EndY=-1.92993 EndZ=0
    g12: LineSegment StartX=4.65926 StartY=-1.92993 StartZ=0 EndX=5 EndY=-0.658262 EndZ=0
    g13: LineSegment StartX=5 StartY=-0.658262 StartZ=0 EndX=5 EndY=0.658262 EndZ=0
    g14: LineSegment StartX=5 StartY=0.658262 StartZ=0 EndX=4.65926 EndY=1.92993 EndZ=0
    g15: LineSegment StartX=4.65926 StartY=1.92993 StartZ=0 EndX=4.001 EndY=3.07007 EndZ=0
    g16: LineSegment StartX=4.001 StartY=3.07007 StartZ=0 EndX=3.07007 EndY=4.001 EndZ=0
    g17: LineSegment StartX=3.07007 StartY=4.001 StartZ=0 EndX=1.92993 EndY=4.65926 EndZ=0
    g18: LineSegment StartX=1.92993 StartY=4.65926 StartZ=0 EndX=0.658262 EndY=5 EndZ=0
    g19: LineSegment StartX=0.658262 StartY=5 StartZ=0 EndX=-0.658262 EndY=5 EndZ=0
    g20: LineSegment StartX=-0.658262 StartY=5 StartZ=0 EndX=-1.92993 EndY=4.65926 EndZ=0
    g21: LineSegment StartX=-1.92993 StartY=4.65926 StartZ=0 EndX=-3.07007 EndY=4.001 EndZ=0
    g22: LineSegment StartX=-3.07007 StartY=4.001 StartZ=0 EndX=-4.001 EndY=3.07007 EndZ=0
    g23: LineSegment StartX=-4.001 StartY=3.07007 StartZ=0 EndX=-4.65926 EndY=1.92993 EndZ=0
    g24: Circle CenterX=0 CenterY=0 CenterZ=0 NormalX=0 NormalY=0 NormalZ=1 AngleXU=0 Radius=5.04314
  constraints (52):
    c: Coincident(g0,g1)
    c: Coincident(g1,g2)
    c: Coincident(g2,g3)
    c: Coincident(g3,g4)
    c: Coincident(g4,g5)
    c: Coincident(g5,g6)
    c: Coincident(g6,g7)
    c: Coincident(g7,g8)
    c: Coincident(g8,g9)
    c: Coincident(g9,g10)
    c: Coincident(g10,g11)
    c: Coincident(g11,g12)
    c: Coincident(g12,g13)
    c: Coincident(g13,g14)
    c: Coincident(g14,g15)
    c: Coincident(g15,g16)
    c: Coincident(g16,g17)
    c: Coincident(g17,g18)
    c: Coincident(g18,g19)
    c: Coincident(g19,g20)
    c: Coincident(g20,g21)
    c: Coincident(g21,g22)
    c: Coincident(g22,g23)
    c: Coincident(g23,g0)
    c: Equal(g0, g1-g23) x23
    c: PointOnObject(g0,g24)
    c: PointOnObject(g1,g24)
    c: PointOnObject(g2,g24)
    c: PointOnObject(g3,g24)
    c: PointOnObject(g4,g24)
    c: PointOnObject(g5,g24)
    c: PointOnObject(g6,g24)
    c: PointOnObject(g7,g24)
    c: PointOnObject(g8,g24)
    c: PointOnObject(g9,g24)
    c: PointOnObject(g10,g24)
    c: PointOnObject(g11,g24)
    c: PointOnObject(g12,g24)
    c: PointOnObject(g13,g24)
    c: PointOnObject(g14,g24)
    c: PointOnObject(g15,g24)
    c: PointOnObject(g16,g24)
    c: PointOnObject(g17,g24)
    c: PointOnObject(g18,g24)
    c: PointOnObject(g19,g24)
    c: PointOnObject(g20,g24)
    c: PointOnObject(g21,g24)
    c: PointOnObject(g22,g24)
    c: PointOnObject(g23,g24)
    c: Coincident(g24,g-1)
    c: Horizontal(g19)
    c: DistanceX(g0,g13) = 10
FEATURE [PartDesign::AdditiveLoft] AdditiveLoft034
  AllowMultiFace = false
  Closed = false
  Profile = -> Sketch473
  Refine = true
  Ruled = false
  Sections = -> [Sketch472,Sketch474]
FEATURE [Sketcher::SketchObject] Sketch470
  FullyConstrained = false
  MapMode = 5
  Placement = pos=(0,0,17) rot=(0,0,1;0rad)
  Support = -> [AdditiveLoft034]
  sketch-geometry (1):
    g0: Circle CenterX=0 CenterY=0 CenterZ=0 NormalX=0 NormalY=0 NormalZ=1 AngleXU=0 Radius=4.5
  constraints (2):
    c: Coincident(g0,g-1)
    c: Radius(g0) = 4.5
FEATURE [PartDesign::Pocket] Pocket092
  AllowMultiFace = false
  BaseFeature = -> Pocket089
  Direction = (1,1,1)
  Length = 8
  Length2 = 100
  Profile = -> Sketch447
  Refine = true
  Type = 0
FEATURE [PartDesign::Chamfer] Chamfer084
  Angle = 45
  Base = -> Pocket092 [Edge82,Edge83]
  BaseFeature = -> Pocket092
  ChamferType = 0
  FlipDirection = false
  Size = 1.4
  Size2 = 1
  SupportTransform = false
  UseAllEdges = false
FEATURE [PartDesign::Chamfer] Chamfer071
  Angle = 45
  Base = -> Chamfer084 [Edge8]
  BaseFeature = -> Chamfer084
  ChamferType = 0
  FlipDirection = false
  Size = 0.3
  Size2 = 1
  SupportTransform = false
  UseAllEdges = false
FEATURE [PartDesign::Fillet] Fillet038
  Base = -> Chamfer071 [Edge93,Face36]
  BaseFeature = -> Chamfer071
  Radius = 0.1
  SupportTransform = false
  UseAllEdges = false
FEATURE [PartDesign::Body] Body180
  Group = -> [Sketch460,Sketch455,Sketch451,AdditiveLoft038,Sketch459,Pad084,Sketch458,Pocket091,Sketch449,Pocket089,Sketch447,Pocket092,Chamfer084,Chamfer071,Fillet038]
  Origin = -> Origin939
  Tip = -> Fillet038
FEATURE [App::Part] Part154  label="Cap042"
  Group = -> [Body180]
  Origin = -> Origin931
  Placement = pos=(-13.335,-40.005,0) rot=(0,0,1;0rad)
  expr: .Placement.Base.x = -13.335
  expr: .Placement.Base.y = -40.005
FEATURE [PartDesign::Pad] Pad089
  AllowMultiFace = false
  BaseFeature = -> AdditiveLoft035
  Direction = (1,1,1)
  Length = 0.7
  Length2 = 100
  Profile = -> Sketch456
  Refine = true
  Type = 0
FEATURE [Sketcher::SketchObject] Sketch465
  FullyConstrained = false
  MapMode = 5
  Placement = pos=(0,0,0) rot=(1,0,0;3.14159rad)
  Support = -> [Pad089]
  sketch-geometry (1):
    g0: Circle CenterX=0 CenterY=0 CenterZ=0 NormalX=0 NormalY=0 NormalZ=1 AngleXU=0 Radius=5
  constraints (2):
    c: Coincident(g0,g-1)
    c: Radius(g0) = 5
FEATURE [PartDesign::Pocket] Pocket096
  AllowMultiFace = false
  BaseFeature = -> Pad089
  Direction = (1,1,1)
  Length = 1
  Length2 = 100
  Profile = -> Sketch465
  Refine = true
  Type = 0
FEATURE [Sketcher::SketchObject] Sketch463
  FullyConstrained = false
  MapMode = 5
  Placement = pos=(0,0,1) rot=(1,0,0;3.14159rad)
  Support = -> [Pocket096]
  sketch-geometry (1):
    g0: Circle CenterX=0 CenterY=0 CenterZ=0 NormalX=0 NormalY=0 NormalZ=1 AngleXU=0 Radius=4.65
  constraints (2):
    c: Coincident(g0,g-1)
    c: Radius(g0) = 4.65
FEATURE [PartDesign::Pad] Pad091
  AllowMultiFace = false
  BaseFeature = -> AdditiveLoft034
  Direction = (1,1,1)
  Length = 0.7
  Length2 = 100
  Profile = -> Sketch470
  Refine = true
  Type = 0
FEATURE [Sketcher::SketchObject] Sketch469
  FullyConstrained = false
  MapMode = 5
  Placement = pos=(0,0,0) rot=(1,0,0;3.14159rad)
  Support = -> [Pad091]
  sketch-geometry (1):
    g0: Circle CenterX=0 CenterY=0 CenterZ=0 NormalX=0 NormalY=0 NormalZ=1 AngleXU=0 Radius=5
  constraints (2):
    c: Coincident(g0,g-1)
    c: Radius(g0) = 5
FEATURE [PartDesign::Pocket] Pocket097
  AllowMultiFace = false
  BaseFeature = -> Pad091
  Direction = (1,1,1)
  Length = 1
  Length2 = 100
  Profile = -> Sketch469
  Refine = true
  Type = 0
FEATURE [Sketcher::SketchObject] Sketch457
  FullyConstrained = false
  MapMode = 5
  Placement = pos=(0,0,1) rot=(1,0,0;3.14159rad)
  Support = -> [Pocket097]
  sketch-geometry (1):
    g0: Circle CenterX=0 CenterY=0 CenterZ=0 NormalX=0 NormalY=0 NormalZ=1 AngleXU=0 Radius=4.65
  constraints (2):
    c: Coincident(g0,g-1)
    c: Radius(g0) = 4.65
FEATURE [PartDesign::Pocket] Pocket094
  AllowMultiFace = false
  BaseFeature = -> Pocket097
  Direction = (1,1,1)
  Length = 1
  Length2 = 100
  Profile = -> Sketch457
  Refine = true
  Type = 0
FEATURE [Sketcher::SketchObject] Sketch471
  FullyConstrained = false
  MapMode = 5
  Placement = pos=(0,0,2) rot=(1,0,0;3.14159rad)
  Support = -> [Pocket094]
  sketch-geometry (2):
    g0: ArcOfCircle CenterX=0 CenterY=0 CenterZ=0 NormalX=0 NormalY=0 NormalZ=1 AngleXU=0 Radius=3 StartAngle=2.19024 EndAngle=7.23453
    g1: LineSegment StartX=-1.74176 StartY=2.4426 StartZ=0 EndX=1.74176 EndY=2.4426 EndZ=0
  constraints (5):
    c: Coincident(g0,g-1)
    c: Coincident(g1,g0)
    c: Coincident(g1,g0)
    c: Horizontal(g1)
    c: Radius(g0) = 3
FEATURE [PartDesign::Pocket] Pocket098
  AllowMultiFace = false
  BaseFeature = -> Pocket096
  Direction = (1,1,1)
  Length = 1
  Length2 = 100
  Profile = -> Sketch463
  Refine = true
  Type = 0
FEATURE [Sketcher::SketchObject] Sketch453
  FullyConstrained = false
  MapMode = 5
  Placement = pos=(0,0,2) rot=(1,0,0;3.14159rad)
  Support = -> [Pocket098]
  sketch-geometry (2):
    g0: ArcOfCircle CenterX=0 CenterY=0 CenterZ=0 NormalX=0 NormalY=0 NormalZ=1 AngleXU=0 Radius=3 StartAngle=2.19024 EndAngle=7.23453
    g1: LineSegment StartX=-1.74176 StartY=2.4426 StartZ=0 EndX=1.74176 EndY=2.4426 EndZ=0
  constraints (5):
    c: Coincident(g0,g-1)
    c: Coincident(g1,g0)
    c: Coincident(g1,g0)
    c: Horizontal(g1)
    c: Radius(g0) = 3
FEATURE [PartDesign::Pocket] Pocket093
  AllowMultiFace = false
  BaseFeature = -> Pocket098
  Direction = (1,1,1)
  Length = 8
  Length2 = 100
  Profile = -> Sketch453
  Refine = true
  Type = 0
FEATURE [PartDesign::Chamfer] Chamfer082
  Angle = 45
  Base = -> Pocket093 [Edge82,Edge83]
  BaseFeature = -> Pocket093
  ChamferType = 0
  FlipDirection = false
  Size = 1.4
  Size2 = 1
  SupportTransform = false
  UseAllEdges = false
FEATURE [PartDesign::Chamfer] Chamfer083
  Angle = 45
  Base = -> Chamfer082 [Edge8]
  BaseFeature = -> Chamfer082
  ChamferType = 0
  FlipDirection = false
  Size = 0.3
  Size2 = 1
  SupportTransform = false
  UseAllEdges = false
FEATURE [PartDesign::Fillet] Fillet037
  Base = -> Chamfer083 [Edge93,Face36]
  BaseFeature = -> Chamfer083
  Radius = 0.1
  SupportTransform = false
  UseAllEdges = false
FEATURE [PartDesign::Body] Body179
  Group = -> [Sketch467,Sketch454,Sketch466,AdditiveLoft035,Sketch456,Pad089,Sketch465,Pocket096,Sketch463,Pocket098,Sketch453,Pocket093,Chamfer082,Chamfer083,Fillet037]
  Origin = -> Origin925
  Tip = -> Fillet037
FEATURE [App::Part] Part137  label="Cap030"
  Group = -> [Body179]
  Origin = -> Origin923
  Placement = pos=(13.335,-40.005,0) rot=(0,0,1;0rad)
  expr: .Placement.Base.x = 13.335
  expr: .Placement.Base.y = -40.005
FEATURE [PartDesign::Pocket] Pocket099
  AllowMultiFace = false
  BaseFeature = -> Pocket094
  Direction = (1,1,1)
  Length = 8
  Length2 = 100
  Profile = -> Sketch471
  Refine = true
  Type = 0
FEATURE [PartDesign::Chamfer] Chamfer080
  Angle = 45
  Base = -> Pocket099 [Edge82,Edge83]
  BaseFeature = -> Pocket099
  ChamferType = 0
  FlipDirection = false
  Size = 1.4
  Size2 = 1
  SupportTransform = false
  UseAllEdges = false
FEATURE [PartDesign::Chamfer] Chamfer072
  Angle = 45
  Base = -> Chamfer080 [Edge8]
  BaseFeature = -> Chamfer080
  ChamferType = 0
  FlipDirection = false
  Size = 0.3
  Size2 = 1
  SupportTransform = false
  UseAllEdges = false
FEATURE [PartDesign::Fillet] Fillet042
  Base = -> Chamfer072 [Edge93,Face36]
  BaseFeature = -> Chamfer072
  Radius = 0.1
  SupportTransform = false
  UseAllEdges = false
FEATURE [PartDesign::Body] Body182
  Group = -> [Sketch473,Sketch472,Sketch474,AdditiveLoft034,Sketch470,Pad091,Sketch469,Pocket097,Sketch457,Pocket094,Sketch471,Pocket099,Chamfer080,Chamfer072,Fillet042]
  Origin = -> Origin946
  Tip = -> Fillet042
FEATURE [App::Part] Part147  label="Cap040"
  Group = -> [Body182]
  Origin = -> Origin952
  Placement = pos=(40.005,-40.005,0) rot=(0,0,1;0rad)
  expr: .Placement.Base.x = 40.005
  expr: .Placement.Base.y = -40.005
FEATURE [Sketcher::SketchObject] Sketch477
  AttachmentOffset = pos=(0,0,17) rot=(0,0,1;0rad)
  FullyConstrained = false
  MapMode = 5
  Placement = pos=(0,0,17) rot=(0,0,1;0rad)
  Support = -> [XY_Plane918]
  sketch-geometry (25):
    g0: LineSegment StartX=-4.65926 StartY=1.92993 StartZ=0 EndX=-5 EndY=0.658262 EndZ=0
    g1: LineSegment StartX=-5 StartY=0.658262 StartZ=0 EndX=-5 EndY=-0.658262 EndZ=0
    g2: LineSegment StartX=-5 StartY=-0.658262 StartZ=0 EndX=-4.65926 EndY=-1.92993 EndZ=0
    g3: LineSegment StartX=-4.65926 StartY=-1.92993 StartZ=0 EndX=-4.001 EndY=-3.07007 EndZ=0
    g4: LineSegment StartX=-4.001 StartY=-3.07007 StartZ=0 EndX=-3.07007 EndY=-4.001 EndZ=0
    g5: LineSegment StartX=-3.07007 StartY=-4.001 StartZ=0 EndX=-1.92993 EndY=-4.65926 EndZ=0
    g6: LineSegment StartX=-1.92993 StartY=-4.65926 StartZ=0 EndX=-0.658262 EndY=-5 EndZ=0
    g7: LineSegment StartX=-0.658262 StartY=-5 StartZ=0 EndX=0.658262 EndY=-5 EndZ=0
    g8: LineSegment StartX=0.658262 StartY=-5 StartZ=0 EndX=1.92993 EndY=-4.65926 EndZ=0
    g9: LineSegment StartX=1.92993 StartY=-4.65926 StartZ=0 EndX=3.07007 EndY=-4.001 EndZ=0
    g10: LineSegment StartX=3.07007 StartY=-4.001 StartZ=0 EndX=4.001 EndY=-3.07007 EndZ=0
    g11: LineSegment StartX=4.001 StartY=-3.07007 StartZ=0 EndX=4.65926 EndY=-1.92993 EndZ=0
    g12: LineSegment StartX=4.65926 StartY=-1.92993 StartZ=0 EndX=5 EndY=-0.658262 EndZ=0
    g13: LineSegment StartX=5 StartY=-0.658262 StartZ=0 EndX=5 EndY=0.658262 EndZ=0
    g14: LineSegment StartX=5 StartY=0.658262 StartZ=0 EndX=4.65926 EndY=1.92993 EndZ=0
    g15: LineSegment StartX=4.65926 StartY=1.92993 StartZ=0 EndX=4.001 EndY=3.07007 EndZ=0
    g16: LineSegment StartX=4.001 StartY=3.07007 StartZ=0 EndX=3.07007 EndY=4.001 EndZ=0
    g17: LineSegment StartX=3.07007 StartY=4.001 StartZ=0 EndX=1.92993 EndY=4.65926 EndZ=0
    g18: LineSegment StartX=1.92993 StartY=4.65926 StartZ=0 EndX=0.658262 EndY=5 EndZ=0
    g19: LineSegment StartX=0.658262 StartY=5 StartZ=0 EndX=-0.658262 EndY=5 EndZ=0
    g20: LineSegment StartX=-0.658262 StartY=5 StartZ=0 EndX=-1.92993 EndY=4.65926 EndZ=0
    g21: LineSegment StartX=-1.92993 StartY=4.65926 StartZ=0 EndX=-3.07007 EndY=4.001 EndZ=0
    g22: LineSegment StartX=-3.07007 StartY=4.001 StartZ=0 EndX=-4.001 EndY=3.07007 EndZ=0
    g23: LineSegment StartX=-4.001 StartY=3.07007 StartZ=0 EndX=-4.65926 EndY=1.92993 EndZ=0
    g24: Circle CenterX=0 CenterY=0 CenterZ=0 NormalX=0 NormalY=0 NormalZ=1 AngleXU=0 Radius=5.04314
  constraints (52):
    c: Coincident(g0,g1)
    c: Coincident(g1,g2)
    c: Coincident(g2,g3)
    c: Coincident(g3,g4)
    c: Coincident(g4,g5)
    c: Coincident(g5,g6)
    c: Coincident(g6,g7)
    c: Coincident(g7,g8)
    c: Coincident(g8,g9)
    c: Coincident(g9,g10)
    c: Coincident(g10,g11)
    c: Coincident(g11,g12)
    c: Coincident(g12,g13)
    c: Coincident(g13,g14)
    c: Coincident(g14,g15)
    c: Coincident(g15,g16)
    c: Coincident(g16,g17)
    c: Coincident(g17,g18)
    c: Coincident(g18,g19)
    c: Coincident(g19,g20)
    c: Coincident(g20,g21)
    c: Coincident(g21,g22)
    c: Coincident(g22,g23)
    c: Coincident(g23,g0)
    c: Equal(g0, g1-g23) x23
    c: PointOnObject(g0,g24)
    c: PointOnObject(g1,g24)
    c: PointOnObject(g2,g24)
    c: PointOnObject(g3,g24)
    c: PointOnObject(g4,g24)
    c: PointOnObject(g5,g24)
    c: PointOnObject(g6,g24)
    c: PointOnObject(g7,g24)
    c: PointOnObject(g8,g24)
    c: PointOnObject(g9,g24)
    c: PointOnObject(g10,g24)
    c: PointOnObject(g11,g24)
    c: PointOnObject(g12,g24)
    c: PointOnObject(g13,g24)
    c: PointOnObject(g14,g24)
    c: PointOnObject(g15,g24)
    c: PointOnObject(g16,g24)
    c: PointOnObject(g17,g24)
    c: PointOnObject(g18,g24)
    c: PointOnObject(g19,g24)
    c: PointOnObject(g20,g24)
    c: PointOnObject(g21,g24)
    c: PointOnObject(g22,g24)
    c: PointOnObject(g23,g24)
    c: Coincident(g24,g-1)
    c: Horizontal(g19)
    c: DistanceX(g0,g13) = 10
FEATURE [Sketcher::SketchObject] Sketch479
  AttachmentOffset = pos=(0,0,17) rot=(0,0,1;0rad)
  FullyConstrained = false
  MapMode = 5
  Placement = pos=(0,0,17) rot=(0,0,1;0rad)
  Support = -> [XY_Plane919]
  sketch-geometry (25):
    g0: LineSegment StartX=-4.65926 StartY=1.92993 StartZ=0 EndX=-5 EndY=0.658262 EndZ=0
    g1: LineSegment StartX=-5 StartY=0.658262 StartZ=0 EndX=-5 EndY=-0.658262 EndZ=0
    g2: LineSegment StartX=-5 StartY=-0.658262 StartZ=0 EndX=-4.65926 EndY=-1.92993 EndZ=0
    g3: LineSegment StartX=-4.65926 StartY=-1.92993 StartZ=0 EndX=-4.001 EndY=-3.07007 EndZ=0
    g4: LineSegment StartX=-4.001 StartY=-3.07007 StartZ=0 EndX=-3.07007 EndY=-4.001 EndZ=0
    g5: LineSegment StartX=-3.07007 StartY=-4.001 StartZ=0 EndX=-1.92993 EndY=-4.65926 EndZ=0
    g6: LineSegment StartX=-1.92993 StartY=-4.65926 StartZ=0 EndX=-0.658262 EndY=-5 EndZ=0
    g7: LineSegment StartX=-0.658262 StartY=-5 StartZ=0 EndX=0.658262 EndY=-5 EndZ=0
    g8: LineSegment StartX=0.658262 StartY=-5 StartZ=0 EndX=1.92993 EndY=-4.65926 EndZ=0
    g9: LineSegment StartX=1.92993 StartY=-4.65926 StartZ=0 EndX=3.07007 EndY=-4.001 EndZ=0
    g10: LineSegment StartX=3.07007 StartY=-4.001 StartZ=0 EndX=4.001 EndY=-3.07007 EndZ=0
    g11: LineSegment StartX=4.001 StartY=-3.07007 StartZ=0 EndX=4.65926 EndY=-1.92993 EndZ=0
    g12: LineSegment StartX=4.65926 StartY=-1.92993 StartZ=0 EndX=5 EndY=-0.658262 EndZ=0
    g13: LineSegment StartX=5 StartY=-0.658262 StartZ=0 EndX=5 EndY=0.658262 EndZ=0
    g14: LineSegment StartX=5 StartY=0.658262 StartZ=0 EndX=4.65926 EndY=1.92993 EndZ=0
    g15: LineSegment StartX=4.65926 StartY=1.92993 StartZ=0 EndX=4.001 EndY=3.07007 EndZ=0
    g16: LineSegment StartX=4.001 StartY=3.07007 StartZ=0 EndX=3.07007 EndY=4.001 EndZ=0
    g17: LineSegment StartX=3.07007 StartY=4.001 StartZ=0 EndX=1.92993 EndY=4.65926 EndZ=0
    g18: LineSegment StartX=1.92993 StartY=4.65926 StartZ=0 EndX=0.658262 EndY=5 EndZ=0
    g19: LineSegment StartX=0.658262 StartY=5 StartZ=0 EndX=-0.658262 EndY=5 EndZ=0
    g20: LineSegment StartX=-0.658262 StartY=5 StartZ=0 EndX=-1.92993 EndY=4.65926 EndZ=0
    g21: LineSegment StartX=-1.92993 StartY=4.65926 StartZ=0 EndX=-3.07007 EndY=4.001 EndZ=0
    g22: LineSegment StartX=-3.07007 StartY=4.001 StartZ=0 EndX=-4.001 EndY=3.07007 EndZ=0
    g23: LineSegment StartX=-4.001 StartY=3.07007 StartZ=0 EndX=-4.65926 EndY=1.92993 EndZ=0
    g24: Circle CenterX=0 CenterY=0 CenterZ=0 NormalX=0 NormalY=0 NormalZ=1 AngleXU=0 Radius=5.04314
  constraints (52):
    c: Coincident(g0,g1)
    c: Coincident(g1,g2)
    c: Coincident(g2,g3)
    c: Coincident(g3,g4)
    c: Coincident(g4,g5)
    c: Coincident(g5,g6)
    c: Coincident(g6,g7)
    c: Coincident(g7,g8)
    c: Coincident(g8,g9)
    c: Coincident(g9,g10)
    c: Coincident(g10,g11)
    c: Coincident(g11,g12)
    c: Coincident(g12,g13)
    c: Coincident(g13,g14)
    c: Coincident(g14,g15)
    c: Coincident(g15,g16)
    c: Coincident(g16,g17)
    c: Coincident(g17,g18)
    c: Coincident(g18,g19)
    c: Coincident(g19,g20)
    c: Coincident(g20,g21)
    c: Coincident(g21,g22)
    c: Coincident(g22,g23)
    c: Coincident(g23,g0)
    c: Equal(g0, g1-g23) x23
    c: PointOnObject(g0,g24)
    c: PointOnObject(g1,g24)
    c: PointOnObject(g2,g24)
    c: PointOnObject(g3,g24)
    c: PointOnObject(g4,g24)
    c: PointOnObject(g5,g24)
    c: PointOnObject(g6,g24)
    c: PointOnObject(g7,g24)
    c: PointOnObject(g8,g24)
    c: PointOnObject(g9,g24)
    c: PointOnObject(g10,g24)
    c: PointOnObject(g11,g24)
    c: PointOnObject(g12,g24)
    c: PointOnObject(g13,g24)
    c: PointOnObject(g14,g24)
    c: PointOnObject(g15,g24)
    c: PointOnObject(g16,g24)
    c: PointOnObject(g17,g24)
    c: PointOnObject(g18,g24)
    c: PointOnObject(g19,g24)
    c: PointOnObject(g20,g24)
    c: PointOnObject(g21,g24)
    c: PointOnObject(g22,g24)
    c: PointOnObject(g23,g24)
    c: Coincident(g24,g-1)
    c: Horizontal(g19)
    c: DistanceX(g0,g13) = 10
FEATURE [Sketcher::SketchObject] Sketch483
  AttachmentOffset = pos=(0,0,7) rot=(0,0,1;0rad)
  FullyConstrained = false
  MapMode = 5
  Placement = pos=(0,0,7) rot=(0,0,1;0rad)
  Support = -> [XY_Plane918]
  sketch-geometry (25):
    g0: LineSegment StartX=-0.724089 StartY=5.5 StartZ=0 EndX=-2.12292 EndY=5.12518 EndZ=0
    g1: LineSegment StartX=-2.12292 StartY=5.12518 StartZ=0 EndX=-3.37708 EndY=4.4011 EndZ=0
    g2: LineSegment StartX=-3.37708 StartY=4.4011 StartZ=0 EndX=-4.4011 EndY=3.37708 EndZ=0
    g3: LineSegment StartX=-4.4011 StartY=3.37708 StartZ=0 EndX=-5.12518 EndY=2.12292 EndZ=0
    g4: LineSegment StartX=-5.12518 StartY=2.12292 StartZ=0 EndX=-5.5 EndY=0.724089 EndZ=0
    g5: LineSegment StartX=-5.5 StartY=0.724089 StartZ=0 EndX=-5.5 EndY=-0.724089 EndZ=0
    g6: LineSegment StartX=-5.5 StartY=-0.724089 StartZ=0 EndX=-5.12518 EndY=-2.12292 EndZ=0
    g7: LineSegment StartX=-5.12518 StartY=-2.12292 StartZ=0 EndX=-4.4011 EndY=-3.37708 EndZ=0
    g8: LineSegment StartX=-4.4011 StartY=-3.37708 StartZ=0 EndX=-3.37708 EndY=-4.4011 EndZ=0
    g9: LineSegment StartX=-3.37708 StartY=-4.4011 StartZ=0 EndX=-2.12292 EndY=-5.12518 EndZ=0
    g10: LineSegment StartX=-2.12292 StartY=-5.12518 StartZ=0 EndX=-0.724089 EndY=-5.5 EndZ=0
    g11: LineSegment StartX=-0.724089 StartY=-5.5 StartZ=0 EndX=0.724089 EndY=-5.5 EndZ=0
    g12: LineSegment StartX=0.724089 StartY=-5.5 StartZ=0 EndX=2.12292 EndY=-5.12518 EndZ=0
    g13: LineSegment StartX=2.12292 StartY=-5.12518 StartZ=0 EndX=3.37708 EndY=-4.4011 EndZ=0
    g14: LineSegment StartX=3.37708 StartY=-4.4011 StartZ=0 EndX=4.4011 EndY=-3.37708 EndZ=0
    g15: LineSegment StartX=4.4011 StartY=-3.37708 StartZ=0 EndX=5.12518 EndY=-2.12292 EndZ=0
    g16: LineSegment StartX=5.12518 StartY=-2.12292 StartZ=0 EndX=5.5 EndY=-0.724089 EndZ=0
    g17: LineSegment StartX=5.5 StartY=-0.724089 StartZ=0 EndX=5.5 EndY=0.724089 EndZ=0
    g18: LineSegment StartX=5.5 StartY=0.724089 StartZ=0 EndX=5.12518 EndY=2.12292 EndZ=0
    g19: LineSegment StartX=5.12518 StartY=2.12292 StartZ=0 EndX=4.4011 EndY=3.37708 EndZ=0
    g20: LineSegment StartX=4.4011 StartY=3.37708 StartZ=0 EndX=3.37708 EndY=4.4011 EndZ=0
    g21: LineSegment StartX=3.37708 StartY=4.4011 StartZ=0 EndX=2.12292 EndY=5.12518 EndZ=0
    g22: LineSegment StartX=2.12292 StartY=5.12518 StartZ=0 EndX=0.724089 EndY=5.5 EndZ=0
    g23: LineSegment StartX=0.724089 StartY=5.5 StartZ=0 EndX=-0.724089 EndY=5.5 EndZ=0
    g24: Circle CenterX=0 CenterY=0 CenterZ=0 NormalX=0 NormalY=0 NormalZ=1 AngleXU=0 Radius=5.54746
  constraints (52):
    c: Coincident(g0,g1)
    c: Coincident(g1,g2)
    c: Coincident(g2,g3)
    c: Coincident(g3,g4)
    c: Coincident(g4,g5)
    c: Coincident(g5,g6)
    c: Coincident(g6,g7)
    c: Coincident(g7,g8)
    c: Coincident(g8,g9)
    c: Coincident(g9,g10)
    c: Coincident(g10,g11)
    c: Coincident(g11,g12)
    c: Coincident(g12,g13)
    c: Coincident(g13,g14)
    c: Coincident(g14,g15)
    c: Coincident(g15,g16)
    c: Coincident(g16,g17)
    c: Coincident(g17,g18)
    c: Coincident(g18,g19)
    c: Coincident(g19,g20)
    c: Coincident(g20,g21)
    c: Coincident(g21,g22)
    c: Coincident(g22,g23)
    c: Coincident(g23,g0)
    c: Equal(g0, g1-g23) x23
    c: PointOnObject(g0,g24)
    c: PointOnObject(g1,g24)
    c: PointOnObject(g2,g24)
    c: PointOnObject(g3,g24)
    c: PointOnObject(g4,g24)
    c: PointOnObject(g5,g24)
    c: PointOnObject(g6,g24)
    c: PointOnObject(g7,g24)
    c: PointOnObject(g8,g24)
    c: PointOnObject(g9,g24)
    c: PointOnObject(g10,g24)
    c: PointOnObject(g11,g24)
    c: PointOnObject(g12,g24)
    c: PointOnObject(g13,g24)
    c: PointOnObject(g14,g24)
    c: PointOnObject(g15,g24)
    c: PointOnObject(g16,g24)
    c: PointOnObject(g17,g24)
    c: PointOnObject(g18,g24)
    c: PointOnObject(g19,g24)
    c: PointOnObject(g20,g24)
    c: PointOnObject(g21,g24)
    c: PointOnObject(g22,g24)
    c: PointOnObject(g23,g24)
    c: Coincident(g24,g-1)
    c: Horizontal(g23)
    c: DistanceX(g4,g17) = 11
FEATURE [Sketcher::SketchObject] Sketch488
  FullyConstrained = false
  MapMode = 5
  Support = -> [XY_Plane918]
  sketch-geometry (25):
    g0: LineSegment StartX=-0.789915 StartY=6 StartZ=0 EndX=-2.31591 EndY=5.59111 EndZ=0
    g1: LineSegment StartX=-2.31591 StartY=5.59111 StartZ=0 EndX=-3.68409 EndY=4.80119 EndZ=0
    g2: LineSegment StartX=-3.68409 StartY=4.80119 StartZ=0 EndX=-4.80119 EndY=3.68409 EndZ=0
    g3: LineSegment StartX=-4.80119 StartY=3.68409 StartZ=0 EndX=-5.59111 EndY=2.31591 EndZ=0
    g4: LineSegment StartX=-5.59111 StartY=2.31591 StartZ=0 EndX=-6 EndY=0.789915 EndZ=0
    g5: LineSegment StartX=-6 StartY=0.789915 StartZ=0 EndX=-6 EndY=-0.789915 EndZ=0
    g6: LineSegment StartX=-6 StartY=-0.789915 StartZ=0 EndX=-5.59111 EndY=-2.31591 EndZ=0
    g7: LineSegment StartX=-5.59111 StartY=-2.31591 StartZ=0 EndX=-4.80119 EndY=-3.68409 EndZ=0
    g8: LineSegment StartX=-4.80119 StartY=-3.68409 StartZ=0 EndX=-3.68409 EndY=-4.80119 EndZ=0
    g9: LineSegment StartX=-3.68409 StartY=-4.80119 StartZ=0 EndX=-2.31591 EndY=-5.59111 EndZ=0
    g10: LineSegment StartX=-2.31591 StartY=-5.59111 StartZ=0 EndX=-0.789915 EndY=-6 EndZ=0
    g11: LineSegment StartX=-0.789915 StartY=-6 StartZ=0 EndX=0.789915 EndY=-6 EndZ=0
    g12: LineSegment StartX=0.789915 StartY=-6 StartZ=0 EndX=2.31591 EndY=-5.59111 EndZ=0
    g13: LineSegment StartX=2.31591 StartY=-5.59111 StartZ=0 EndX=3.68409 EndY=-4.80119 EndZ=0
    g14: LineSegment StartX=3.68409 StartY=-4.80119 StartZ=0 EndX=4.80119 EndY=-3.68409 EndZ=0
    g15: LineSegment StartX=4.80119 StartY=-3.68409 StartZ=0 EndX=5.59111 EndY=-2.31591 EndZ=0
    g16: LineSegment StartX=5.59111 StartY=-2.31591 StartZ=0 EndX=6 EndY=-0.789915 EndZ=0
    g17: LineSegment StartX=6 StartY=-0.789915 StartZ=0 EndX=6 EndY=0.789915 EndZ=0
    g18: LineSegment StartX=6 StartY=0.789915 StartZ=0 EndX=5.59111 EndY=2.31591 EndZ=0
    g19: LineSegment StartX=5.59111 StartY=2.31591 StartZ=0 EndX=4.80119 EndY=3.68409 EndZ=0
    g20: LineSegment StartX=4.80119 StartY=3.68409 StartZ=0 EndX=3.68409 EndY=4.80119 EndZ=0
    g21: LineSegment StartX=3.68409 StartY=4.80119 StartZ=0 EndX=2.31591 EndY=5.59111 EndZ=0
    g22: LineSegment StartX=2.31591 StartY=5.59111 StartZ=0 EndX=0.789915 EndY=6 EndZ=0
    g23: LineSegment StartX=0.789915 StartY=6 StartZ=0 EndX=-0.789915 EndY=6 EndZ=0
    g24: Circle CenterX=0 CenterY=0 CenterZ=0 NormalX=0 NormalY=0 NormalZ=1 AngleXU=0 Radius=6.05177
  constraints (52):
    c: Coincident(g0,g1)
    c: Coincident(g1,g2)
    c: Coincident(g2,g3)
    c: Coincident(g3,g4)
    c: Coincident(g4,g5)
    c: Coincident(g5,g6)
    c: Coincident(g6,g7)
    c: Coincident(g7,g8)
    c: Coincident(g8,g9)
    c: Coincident(g9,g10)
    c: Coincident(g10,g11)
    c: Coincident(g11,g12)
    c: Coincident(g12,g13)
    c: Coincident(g13,g14)
    c: Coincident(g14,g15)
    c: Coincident(g15,g16)
    c: Coincident(g16,g17)
    c: Coincident(g17,g18)
    c: Coincident(g18,g19)
    c: Coincident(g19,g20)
    c: Coincident(g20,g21)
    c: Coincident(g21,g22)
    c: Coincident(g22,g23)
    c: Coincident(g23,g0)
    c: Equal(g0, g1-g23) x23
    c: PointOnObject(g0,g24)
    c: PointOnObject(g1,g24)
    c: PointOnObject(g2,g24)
    c: PointOnObject(g3,g24)
    c: PointOnObject(g4,g24)
    c: PointOnObject(g5,g24)
    c: PointOnObject(g6,g24)
    c: PointOnObject(g7,g24)
    c: PointOnObject(g8,g24)
    c: PointOnObject(g9,g24)
    c: PointOnObject(g10,g24)
    c: PointOnObject(g11,g24)
    c: PointOnObject(g12,g24)
    c: PointOnObject(g13,g24)
    c: PointOnObject(g14,g24)
    c: PointOnObject(g15,g24)
    c: PointOnObject(g16,g24)
    c: PointOnObject(g17,g24)
    c: PointOnObject(g18,g24)
    c: PointOnObject(g19,g24)
    c: PointOnObject(g20,g24)
    c: PointOnObject(g21,g24)
    c: PointOnObject(g22,g24)
    c: PointOnObject(g23,g24)
    c: Coincident(g24,g-1)
    c: Horizontal(g23)
    c: DistanceX(g4,g17) = 12
FEATURE [PartDesign::AdditiveLoft] AdditiveLoft033
  AllowMultiFace = false
  Closed = false
  Profile = -> Sketch488
  Refine = true
  Ruled = false
  Sections = -> [Sketch483,Sketch477]
FEATURE [Sketcher::SketchObject] Sketch486
  FullyConstrained = false
  MapMode = 5
  Placement = pos=(0,0,17) rot=(0,0,1;0rad)
  Support = -> [AdditiveLoft033]
  sketch-geometry (1):
    g0: Circle CenterX=0 CenterY=0 CenterZ=0 NormalX=0 NormalY=0 NormalZ=1 AngleXU=0 Radius=4.5
  constraints (2):
    c: Coincident(g0,g-1)
    c: Radius(g0) = 4.5
FEATURE [Sketcher::SketchObject] Sketch489
  AttachmentOffset = pos=(0,0,7) rot=(0,0,1;0rad)
  FullyConstrained = false
  MapMode = 5
  Placement = pos=(0,0,7) rot=(0,0,1;0rad)
  Support = -> [XY_Plane919]
  sketch-geometry (25):
    g0: LineSegment StartX=-0.724089 StartY=5.5 StartZ=0 EndX=-2.12292 EndY=5.12518 EndZ=0
    g1: LineSegment StartX=-2.12292 StartY=5.12518 StartZ=0 EndX=-3.37708 EndY=4.4011 EndZ=0
    g2: LineSegment StartX=-3.37708 StartY=4.4011 StartZ=0 EndX=-4.4011 EndY=3.37708 EndZ=0
    g3: LineSegment StartX=-4.4011 StartY=3.37708 StartZ=0 EndX=-5.12518 EndY=2.12292 EndZ=0
    g4: LineSegment StartX=-5.12518 StartY=2.12292 StartZ=0 EndX=-5.5 EndY=0.724089 EndZ=0
    g5: LineSegment StartX=-5.5 StartY=0.724089 StartZ=0 EndX=-5.5 EndY=-0.724089 EndZ=0
    g6: LineSegment StartX=-5.5 StartY=-0.724089 StartZ=0 EndX=-5.12518 EndY=-2.12292 EndZ=0
    g7: LineSegment StartX=-5.12518 StartY=-2.12292 StartZ=0 EndX=-4.4011 EndY=-3.37708 EndZ=0
    g8: LineSegment StartX=-4.4011 StartY=-3.37708 StartZ=0 EndX=-3.37708 EndY=-4.4011 EndZ=0
    g9: LineSegment StartX=-3.37708 StartY=-4.4011 StartZ=0 EndX=-2.12292 EndY=-5.12518 EndZ=0
    g10: LineSegment StartX=-2.12292 StartY=-5.12518 StartZ=0 EndX=-0.724089 EndY=-5.5 EndZ=0
    g11: LineSegment StartX=-0.724089 StartY=-5.5 StartZ=0 EndX=0.724089 EndY=-5.5 EndZ=0
    g12: LineSegment StartX=0.724089 StartY=-5.5 StartZ=0 EndX=2.12292 EndY=-5.12518 EndZ=0
    g13: LineSegment StartX=2.12292 StartY=-5.12518 StartZ=0 EndX=3.37708 EndY=-4.4011 EndZ=0
    g14: LineSegment StartX=3.37708 StartY=-4.4011 StartZ=0 EndX=4.4011 EndY=-3.37708 EndZ=0
    g15: LineSegment StartX=4.4011 StartY=-3.37708 StartZ=0 EndX=5.12518 EndY=-2.12292 EndZ=0
    g16: LineSegment StartX=5.12518 StartY=-2.12292 StartZ=0 EndX=5.5 EndY=-0.724089 EndZ=0
    g17: LineSegment StartX=5.5 StartY=-0.724089 StartZ=0 EndX=5.5 EndY=0.724089 EndZ=0
    g18: LineSegment StartX=5.5 StartY=0.724089 StartZ=0 EndX=5.12518 EndY=2.12292 EndZ=0
    g19: LineSegment StartX=5.12518 StartY=2.12292 StartZ=0 EndX=4.4011 EndY=3.37708 EndZ=0
    g20: LineSegment StartX=4.4011 StartY=3.37708 StartZ=0 EndX=3.37708 EndY=4.4011 EndZ=0
    g21: LineSegment StartX=3.37708 StartY=4.4011 StartZ=0 EndX=2.12292 EndY=5.12518 EndZ=0
    g22: LineSegment StartX=2.12292 StartY=5.12518 StartZ=0 EndX=0.724089 EndY=5.5 EndZ=0
    g23: LineSegment StartX=0.724089 StartY=5.5 StartZ=0 EndX=-0.724089 EndY=5.5 EndZ=0
    g24: Circle CenterX=0 CenterY=0 CenterZ=0 NormalX=0 NormalY=0 NormalZ=1 AngleXU=0 Radius=5.54746
  constraints (52):
    c: Coincident(g0,g1)
    c: Coincident(g1,g2)
    c: Coincident(g2,g3)
    c: Coincident(g3,g4)
    c: Coincident(g4,g5)
    c: Coincident(g5,g6)
    c: Coincident(g6,g7)
    c: Coincident(g7,g8)
    c: Coincident(g8,g9)
    c: Coincident(g9,g10)
    c: Coincident(g10,g11)
    c: Coincident(g11,g12)
    c: Coincident(g12,g13)
    c: Coincident(g13,g14)
    c: Coincident(g14,g15)
    c: Coincident(g15,g16)
    c: Coincident(g16,g17)
    c: Coincident(g17,g18)
    c: Coincident(g18,g19)
    c: Coincident(g19,g20)
    c: Coincident(g20,g21)
    c: Coincident(g21,g22)
    c: Coincident(g22,g23)
    c: Coincident(g23,g0)
    c: Equal(g0, g1-g23) x23
    c: PointOnObject(g0,g24)
    c: PointOnObject(g1,g24)
    c: PointOnObject(g2,g24)
    c: PointOnObject(g3,g24)
    c: PointOnObject(g4,g24)
    c: PointOnObject(g5,g24)
    c: PointOnObject(g6,g24)
    c: PointOnObject(g7,g24)
    c: PointOnObject(g8,g24)
    c: PointOnObject(g9,g24)
    c: PointOnObject(g10,g24)
    c: PointOnObject(g11,g24)
    c: PointOnObject(g12,g24)
    c: PointOnObject(g13,g24)
    c: PointOnObject(g14,g24)
    c: PointOnObject(g15,g24)
    c: PointOnObject(g16,g24)
    c: PointOnObject(g17,g24)
    c: PointOnObject(g18,g24)
    c: PointOnObject(g19,g24)
    c: PointOnObject(g20,g24)
    c: PointOnObject(g21,g24)
    c: PointOnObject(g22,g24)
    c: PointOnObject(g23,g24)
    c: Coincident(g24,g-1)
    c: Horizontal(g23)
    c: DistanceX(g4,g17) = 11
FEATURE [Sketcher::SketchObject] Sketch490
  FullyConstrained = false
  MapMode = 5
  Support = -> [XY_Plane919]
  sketch-geometry (25):
    g0: LineSegment StartX=-0.789915 StartY=6 StartZ=0 EndX=-2.31591 EndY=5.59111 EndZ=0
    g1: LineSegment StartX=-2.31591 StartY=5.59111 StartZ=0 EndX=-3.68409 EndY=4.80119 EndZ=0
    g2: LineSegment StartX=-3.68409 StartY=4.80119 StartZ=0 EndX=-4.80119 EndY=3.68409 EndZ=0
    g3: LineSegment StartX=-4.80119 StartY=3.68409 StartZ=0 EndX=-5.59111 EndY=2.31591 EndZ=0
    g4: LineSegment StartX=-5.59111 StartY=2.31591 StartZ=0 EndX=-6 EndY=0.789915 EndZ=0
    g5: LineSegment StartX=-6 StartY=0.789915 StartZ=0 EndX=-6 EndY=-0.789915 EndZ=0
    g6: LineSegment StartX=-6 StartY=-0.789915 StartZ=0 EndX=-5.59111 EndY=-2.31591 EndZ=0
    g7: LineSegment StartX=-5.59111 StartY=-2.31591 StartZ=0 EndX=-4.80119 EndY=-3.68409 EndZ=0
    g8: LineSegment StartX=-4.80119 StartY=-3.68409 StartZ=0 EndX=-3.68409 EndY=-4.80119 EndZ=0
    g9: LineSegment StartX=-3.68409 StartY=-4.80119 StartZ=0 EndX=-2.31591 EndY=-5.59111 EndZ=0
    g10: LineSegment StartX=-2.31591 StartY=-5.59111 StartZ=0 EndX=-0.789915 EndY=-6 EndZ=0
    g11: LineSegment StartX=-0.789915 StartY=-6 StartZ=0 EndX=0.789915 EndY=-6 EndZ=0
    g12: LineSegment StartX=0.789915 StartY=-6 StartZ=0 EndX=2.31591 EndY=-5.59111 EndZ=0
    g13: LineSegment StartX=2.31591 StartY=-5.59111 StartZ=0 EndX=3.68409 EndY=-4.80119 EndZ=0
    g14: LineSegment StartX=3.68409 StartY=-4.80119 StartZ=0 EndX=4.80119 EndY=-3.68409 EndZ=0
    g15: LineSegment StartX=4.80119 StartY=-3.68409 StartZ=0 EndX=5.59111 EndY=-2.31591 EndZ=0
    g16: LineSegment StartX=5.59111 StartY=-2.31591 StartZ=0 EndX=6 EndY=-0.789915 EndZ=0
    g17: LineSegment StartX=6 StartY=-0.789915 StartZ=0 EndX=6 EndY=0.789915 EndZ=0
    g18: LineSegment StartX=6 StartY=0.789915 StartZ=0 EndX=5.59111 EndY=2.31591 EndZ=0
    g19: LineSegment StartX=5.59111 StartY=2.31591 StartZ=0 EndX=4.80119 EndY=3.68409 EndZ=0
    g20: LineSegment StartX=4.80119 StartY=3.68409 StartZ=0 EndX=3.68409 EndY=4.80119 EndZ=0
    g21: LineSegment StartX=3.68409 StartY=4.80119 StartZ=0 EndX=2.31591 EndY=5.59111 EndZ=0
    g22: LineSegment StartX=2.31591 StartY=5.59111 StartZ=0 EndX=0.789915 EndY=6 EndZ=0
    g23: LineSegment StartX=0.789915 StartY=6 StartZ=0 EndX=-0.789915 EndY=6 EndZ=0
    g24: Circle CenterX=0 CenterY=0 CenterZ=0 NormalX=0 NormalY=0 NormalZ=1 AngleXU=0 Radius=6.05177
  constraints (52):
    c: Coincident(g0,g1)
    c: Coincident(g1,g2)
    c: Coincident(g2,g3)
    c: Coincident(g3,g4)
    c: Coincident(g4,g5)
    c: Coincident(g5,g6)
    c: Coincident(g6,g7)
    c: Coincident(g7,g8)
    c: Coincident(g8,g9)
    c: Coincident(g9,g10)
    c: Coincident(g10,g11)
    c: Coincident(g11,g12)
    c: Coincident(g12,g13)
    c: Coincident(g13,g14)
    c: Coincident(g14,g15)
    c: Coincident(g15,g16)
    c: Coincident(g16,g17)
    c: Coincident(g17,g18)
    c: Coincident(g18,g19)
    c: Coincident(g19,g20)
    c: Coincident(g20,g21)
    c: Coincident(g21,g22)
    c: Coincident(g22,g23)
    c: Coincident(g23,g0)
    c: Equal(g0, g1-g23) x23
    c: PointOnObject(g0,g24)
    c: PointOnObject(g1,g24)
    c: PointOnObject(g2,g24)
    c: PointOnObject(g3,g24)
    c: PointOnObject(g4,g24)
    c: PointOnObject(g5,g24)
    c: PointOnObject(g6,g24)
    c: PointOnObject(g7,g24)
    c: PointOnObject(g8,g24)
    c: PointOnObject(g9,g24)
    c: PointOnObject(g10,g24)
    c: PointOnObject(g11,g24)
    c: PointOnObject(g12,g24)
    c: PointOnObject(g13,g24)
    c: PointOnObject(g14,g24)
    c: PointOnObject(g15,g24)
    c: PointOnObject(g16,g24)
    c: PointOnObject(g17,g24)
    c: PointOnObject(g18,g24)
    c: PointOnObject(g19,g24)
    c: PointOnObject(g20,g24)
    c: PointOnObject(g21,g24)
    c: PointOnObject(g22,g24)
    c: PointOnObject(g23,g24)
    c: Coincident(g24,g-1)
    c: Horizontal(g23)
    c: DistanceX(g4,g17) = 12
FEATURE [PartDesign::AdditiveLoft] AdditiveLoft039
  AllowMultiFace = false
  Closed = false
  Profile = -> Sketch490
  Refine = true
  Ruled = false
  Sections = -> [Sketch489,Sketch479]
FEATURE [Sketcher::SketchObject] Sketch476
  FullyConstrained = false
  MapMode = 5
  Placement = pos=(0,0,17) rot=(0,0,1;0rad)
  Support = -> [AdditiveLoft039]
  sketch-geometry (1):
    g0: Circle CenterX=0 CenterY=0 CenterZ=0 NormalX=0 NormalY=0 NormalZ=1 AngleXU=0 Radius=4.5
  constraints (2):
    c: Coincident(g0,g-1)
    c: Radius(g0) = 4.5
FEATURE [PartDesign::Pad] Pad093
  AllowMultiFace = false
  BaseFeature = -> AdditiveLoft039
  Direction = (1,1,1)
  Length = 0.7
  Length2 = 100
  Profile = -> Sketch476
  Refine = true
  Type = 0
FEATURE [Sketcher::SketchObject] Sketch487
  FullyConstrained = false
  MapMode = 5
  Placement = pos=(0,0,0) rot=(1,0,0;3.14159rad)
  Support = -> [Pad093]
  sketch-geometry (1):
    g0: Circle CenterX=0 CenterY=0 CenterZ=0 NormalX=0 NormalY=0 NormalZ=1 AngleXU=0 Radius=5
  constraints (2):
    c: Coincident(g0,g-1)
    c: Radius(g0) = 5
FEATURE [Sketcher::SketchObject] Sketch492
  AttachmentOffset = pos=(0,0,7) rot=(0,0,1;0rad)
  FullyConstrained = false
  MapMode = 5
  Placement = pos=(0,0,7) rot=(0,0,1;0rad)
  Support = -> [XY_Plane928]
  sketch-geometry (25):
    g0: LineSegment StartX=-0.724089 StartY=5.5 StartZ=0 EndX=-2.12292 EndY=5.12518 EndZ=0
    g1: LineSegment StartX=-2.12292 StartY=5.12518 StartZ=0 EndX=-3.37708 EndY=4.4011 EndZ=0
    g2: LineSegment StartX=-3.37708 StartY=4.4011 StartZ=0 EndX=-4.4011 EndY=3.37708 EndZ=0
    g3: LineSegment StartX=-4.4011 StartY=3.37708 StartZ=0 EndX=-5.12518 EndY=2.12292 EndZ=0
    g4: LineSegment StartX=-5.12518 StartY=2.12292 StartZ=0 EndX=-5.5 EndY=0.724089 EndZ=0
    g5: LineSegment StartX=-5.5 StartY=0.724089 StartZ=0 EndX=-5.5 EndY=-0.724089 EndZ=0
    g6: LineSegment StartX=-5.5 StartY=-0.724089 StartZ=0 EndX=-5.12518 EndY=-2.12292 EndZ=0
    g7: LineSegment StartX=-5.12518 StartY=-2.12292 StartZ=0 EndX=-4.4011 EndY=-3.37708 EndZ=0
    g8: LineSegment StartX=-4.4011 StartY=-3.37708 StartZ=0 EndX=-3.37708 EndY=-4.4011 EndZ=0
    g9: LineSegment StartX=-3.37708 StartY=-4.4011 StartZ=0 EndX=-2.12292 EndY=-5.12518 EndZ=0
    g10: LineSegment StartX=-2.12292 StartY=-5.12518 StartZ=0 EndX=-0.724089 EndY=-5.5 EndZ=0
    g11: LineSegment StartX=-0.724089 StartY=-5.5 StartZ=0 EndX=0.724089 EndY=-5.5 EndZ=0
    g12: LineSegment StartX=0.724089 StartY=-5.5 StartZ=0 EndX=2.12292 EndY=-5.12518 EndZ=0
    g13: LineSegment StartX=2.12292 StartY=-5.12518 StartZ=0 EndX=3.37708 EndY=-4.4011 EndZ=0
    g14: LineSegment StartX=3.37708 StartY=-4.4011 StartZ=0 EndX=4.4011 EndY=-3.37708 EndZ=0
    g15: LineSegment StartX=4.4011 StartY=-3.37708 StartZ=0 EndX=5.12518 EndY=-2.12292 EndZ=0
    g16: LineSegment StartX=5.12518 StartY=-2.12292 StartZ=0 EndX=5.5 EndY=-0.724089 EndZ=0
    g17: LineSegment StartX=5.5 StartY=-0.724089 StartZ=0 EndX=5.5 EndY=0.724089 EndZ=0
    g18: LineSegment StartX=5.5 StartY=0.724089 StartZ=0 EndX=5.12518 EndY=2.12292 EndZ=0
    g19: LineSegment StartX=5.12518 StartY=2.12292 StartZ=0 EndX=4.4011 EndY=3.37708 EndZ=0
    g20: LineSegment StartX=4.4011 StartY=3.37708 StartZ=0 EndX=3.37708 EndY=4.4011 EndZ=0
    g21: LineSegment StartX=3.37708 StartY=4.4011 StartZ=0 EndX=2.12292 EndY=5.12518 EndZ=0
    g22: LineSegment StartX=2.12292 StartY=5.12518 StartZ=0 EndX=0.724089 EndY=5.5 EndZ=0
    g23: LineSegment StartX=0.724089 StartY=5.5 StartZ=0 EndX=-0.724089 EndY=5.5 EndZ=0
    g24: Circle CenterX=0 CenterY=0 CenterZ=0 NormalX=0 NormalY=0 NormalZ=1 AngleXU=0 Radius=5.54746
  constraints (52):
    c: Coincident(g0,g1)
    c: Coincident(g1,g2)
    c: Coincident(g2,g3)
    c: Coincident(g3,g4)
    c: Coincident(g4,g5)
    c: Coincident(g5,g6)
    c: Coincident(g6,g7)
    c: Coincident(g7,g8)
    c: Coincident(g8,g9)
    c: Coincident(g9,g10)
    c: Coincident(g10,g11)
    c: Coincident(g11,g12)
    c: Coincident(g12,g13)
    c: Coincident(g13,g14)
    c: Coincident(g14,g15)
    c: Coincident(g15,g16)
    c: Coincident(g16,g17)
    c: Coincident(g17,g18)
    c: Coincident(g18,g19)
    c: Coincident(g19,g20)
    c: Coincident(g20,g21)
    c: Coincident(g21,g22)
    c: Coincident(g22,g23)
    c: Coincident(g23,g0)
    c: Equal(g0, g1-g23) x23
    c: PointOnObject(g0,g24)
    c: PointOnObject(g1,g24)
    c: PointOnObject(g2,g24)
    c: PointOnObject(g3,g24)
    c: PointOnObject(g4,g24)
    c: PointOnObject(g5,g24)
    c: PointOnObject(g6,g24)
    c: PointOnObject(g7,g24)
    c: PointOnObject(g8,g24)
    c: PointOnObject(g9,g24)
    c: PointOnObject(g10,g24)
    c: PointOnObject(g11,g24)
    c: PointOnObject(g12,g24)
    c: PointOnObject(g13,g24)
    c: PointOnObject(g14,g24)
    c: PointOnObject(g15,g24)
    c: PointOnObject(g16,g24)
    c: PointOnObject(g17,g24)
    c: PointOnObject(g18,g24)
    c: PointOnObject(g19,g24)
    c: PointOnObject(g20,g24)
    c: PointOnObject(g21,g24)
    c: PointOnObject(g22,g24)
    c: PointOnObject(g23,g24)
    c: Coincident(g24,g-1)
    c: Horizontal(g23)
    c: DistanceX(g4,g17) = 11
FEATURE [Sketcher::SketchObject] Sketch493
  FullyConstrained = false
  MapMode = 5
  Support = -> [XY_Plane928]
  sketch-geometry (25):
    g0: LineSegment StartX=-0.789915 StartY=6 StartZ=0 EndX=-2.31591 EndY=5.59111 EndZ=0
    g1: LineSegment StartX=-2.31591 StartY=5.59111 StartZ=0 EndX=-3.68409 EndY=4.80119 EndZ=0
    g2: LineSegment StartX=-3.68409 StartY=4.80119 StartZ=0 EndX=-4.80119 EndY=3.68409 EndZ=0
    g3: LineSegment StartX=-4.80119 StartY=3.68409 StartZ=0 EndX=-5.59111 EndY=2.31591 EndZ=0
    g4: LineSegment StartX=-5.59111 StartY=2.31591 StartZ=0 EndX=-6 EndY=0.789915 EndZ=0
    g5: LineSegment StartX=-6 StartY=0.789915 StartZ=0 EndX=-6 EndY=-0.789915 EndZ=0
    g6: LineSegment StartX=-6 StartY=-0.789915 StartZ=0 EndX=-5.59111 EndY=-2.31591 EndZ=0
    g7: LineSegment StartX=-5.59111 StartY=-2.31591 StartZ=0 EndX=-4.80119 EndY=-3.68409 EndZ=0
    g8: LineSegment StartX=-4.80119 StartY=-3.68409 StartZ=0 EndX=-3.68409 EndY=-4.80119 EndZ=0
    g9: LineSegment StartX=-3.68409 StartY=-4.80119 StartZ=0 EndX=-2.31591 EndY=-5.59111 EndZ=0
    g10: LineSegment StartX=-2.31591 StartY=-5.59111 StartZ=0 EndX=-0.789915 EndY=-6 EndZ=0
    g11: LineSegment StartX=-0.789915 StartY=-6 StartZ=0 EndX=0.789915 EndY=-6 EndZ=0
    g12: LineSegment StartX=0.789915 StartY=-6 StartZ=0 EndX=2.31591 EndY=-5.59111 EndZ=0
    g13: LineSegment StartX=2.31591 StartY=-5.59111 StartZ=0 EndX=3.68409 EndY=-4.80119 EndZ=0
    g14: LineSegment StartX=3.68409 StartY=-4.80119 StartZ=0 EndX=4.80119 EndY=-3.68409 EndZ=0
    g15: LineSegment StartX=4.80119 StartY=-3.68409 StartZ=0 EndX=5.59111 EndY=-2.31591 EndZ=0
    g16: LineSegment StartX=5.59111 StartY=-2.31591 StartZ=0 EndX=6 EndY=-0.789915 EndZ=0
    g17: LineSegment StartX=6 StartY=-0.789915 StartZ=0 EndX=6 EndY=0.789915 EndZ=0
    g18: LineSegment StartX=6 StartY=0.789915 StartZ=0 EndX=5.59111 EndY=2.31591 EndZ=0
    g19: LineSegment StartX=5.59111 StartY=2.31591 StartZ=0 EndX=4.80119 EndY=3.68409 EndZ=0
    g20: LineSegment StartX=4.80119 StartY=3.68409 StartZ=0 EndX=3.68409 EndY=4.80119 EndZ=0
    g21: LineSegment StartX=3.68409 StartY=4.80119 StartZ=0 EndX=2.31591 EndY=5.59111 EndZ=0
    g22: LineSegment StartX=2.31591 StartY=5.59111 StartZ=0 EndX=0.789915 EndY=6 EndZ=0
    g23: LineSegment StartX=0.789915 StartY=6 StartZ=0 EndX=-0.789915 EndY=6 EndZ=0
    g24: Circle CenterX=0 CenterY=0 CenterZ=0 NormalX=0 NormalY=0 NormalZ=1 AngleXU=0 Radius=6.05177
  constraints (52):
    c: Coincident(g0,g1)
    c: Coincident(g1,g2)
    c: Coincident(g2,g3)
    c: Coincident(g3,g4)
    c: Coincident(g4,g5)
    c: Coincident(g5,g6)
    c: Coincident(g6,g7)
    c: Coincident(g7,g8)
    c: Coincident(g8,g9)
    c: Coincident(g9,g10)
    c: Coincident(g10,g11)
    c: Coincident(g11,g12)
    c: Coincident(g12,g13)
    c: Coincident(g13,g14)
    c: Coincident(g14,g15)
    c: Coincident(g15,g16)
    c: Coincident(g16,g17)
    c: Coincident(g17,g18)
    c: Coincident(g18,g19)
    c: Coincident(g19,g20)
    c: Coincident(g20,g21)
    c: Coincident(g21,g22)
    c: Coincident(g22,g23)
    c: Coincident(g23,g0)
    c: Equal(g0, g1-g23) x23
    c: PointOnObject(g0,g24)
    c: PointOnObject(g1,g24)
    c: PointOnObject(g2,g24)
    c: PointOnObject(g3,g24)
    c: PointOnObject(g4,g24)
    c: PointOnObject(g5,g24)
    c: PointOnObject(g6,g24)
    c: PointOnObject(g7,g24)
    c: PointOnObject(g8,g24)
    c: PointOnObject(g9,g24)
    c: PointOnObject(g10,g24)
    c: PointOnObject(g11,g24)
    c: PointOnObject(g12,g24)
    c: PointOnObject(g13,g24)
    c: PointOnObject(g14,g24)
    c: PointOnObject(g15,g24)
    c: PointOnObject(g16,g24)
    c: PointOnObject(g17,g24)
    c: PointOnObject(g18,g24)
    c: PointOnObject(g19,g24)
    c: PointOnObject(g20,g24)
    c: PointOnObject(g21,g24)
    c: PointOnObject(g22,g24)
    c: PointOnObject(g23,g24)
    c: Coincident(g24,g-1)
    c: Horizontal(g23)
    c: DistanceX(g4,g17) = 12
FEATURE [Sketcher::SketchObject] Sketch494
  AttachmentOffset = pos=(0,0,17) rot=(0,0,1;0rad)
  FullyConstrained = false
  MapMode = 5
  Placement = pos=(0,0,17) rot=(0,0,1;0rad)
  Support = -> [XY_Plane928]
  sketch-geometry (25):
    g0: LineSegment StartX=-4.65926 StartY=1.92993 StartZ=0 EndX=-5 EndY=0.658262 EndZ=0
    g1: LineSegment StartX=-5 StartY=0.658262 StartZ=0 EndX=-5 EndY=-0.658262 EndZ=0
    g2: LineSegment StartX=-5 StartY=-0.658262 StartZ=0 EndX=-4.65926 EndY=-1.92993 EndZ=0
    g3: LineSegment StartX=-4.65926 StartY=-1.92993 StartZ=0 EndX=-4.001 EndY=-3.07007 EndZ=0
    g4: LineSegment StartX=-4.001 StartY=-3.07007 StartZ=0 EndX=-3.07007 EndY=-4.001 EndZ=0
    g5: LineSegment StartX=-3.07007 StartY=-4.001 StartZ=0 EndX=-1.92993 EndY=-4.65926 EndZ=0
    g6: LineSegment StartX=-1.92993 StartY=-4.65926 StartZ=0 EndX=-0.658262 EndY=-5 EndZ=0
    g7: LineSegment StartX=-0.658262 StartY=-5 StartZ=0 EndX=0.658262 EndY=-5 EndZ=0
    g8: LineSegment StartX=0.658262 StartY=-5 StartZ=0 EndX=1.92993 EndY=-4.65926 EndZ=0
    g9: LineSegment StartX=1.92993 StartY=-4.65926 StartZ=0 EndX=3.07007 EndY=-4.001 EndZ=0
    g10: LineSegment StartX=3.07007 StartY=-4.001 StartZ=0 EndX=4.001 EndY=-3.07007 EndZ=0
    g11: LineSegment StartX=4.001 StartY=-3.07007 StartZ=0 EndX=4.65926 EndY=-1.92993 EndZ=0
    g12: LineSegment StartX=4.65926 StartY=-1.92993 StartZ=0 EndX=5 EndY=-0.658262 EndZ=0
    g13: LineSegment StartX=5 StartY=-0.658262 StartZ=0 EndX=5 EndY=0.658262 EndZ=0
    g14: LineSegment StartX=5 StartY=0.658262 StartZ=0 EndX=4.65926 EndY=1.92993 EndZ=0
    g15: LineSegment StartX=4.65926 StartY=1.92993 StartZ=0 EndX=4.001 EndY=3.07007 EndZ=0
    g16: LineSegment StartX=4.001 StartY=3.07007 StartZ=0 EndX=3.07007 EndY=4.001 EndZ=0
    g17: LineSegment StartX=3.07007 StartY=4.001 StartZ=0 EndX=1.92993 EndY=4.65926 EndZ=0
    g18: LineSegment StartX=1.92993 StartY=4.65926 StartZ=0 EndX=0.658262 EndY=5 EndZ=0
    g19: LineSegment StartX=0.658262 StartY=5 StartZ=0 EndX=-0.658262 EndY=5 EndZ=0
    g20: LineSegment StartX=-0.658262 StartY=5 StartZ=0 EndX=-1.92993 EndY=4.65926 EndZ=0
    g21: LineSegment StartX=-1.92993 StartY=4.65926 StartZ=0 EndX=-3.07007 EndY=4.001 EndZ=0
    g22: LineSegment StartX=-3.07007 StartY=4.001 StartZ=0 EndX=-4.001 EndY=3.07007 EndZ=0
    g23: LineSegment StartX=-4.001 StartY=3.07007 StartZ=0 EndX=-4.65926 EndY=1.92993 EndZ=0
    g24: Circle CenterX=0 CenterY=0 CenterZ=0 NormalX=0 NormalY=0 NormalZ=1 AngleXU=0 Radius=5.04314
  constraints (52):
    c: Coincident(g0,g1)
    c: Coincident(g1,g2)
    c: Coincident(g2,g3)
    c: Coincident(g3,g4)
    c: Coincident(g4,g5)
    c: Coincident(g5,g6)
    c: Coincident(g6,g7)
    c: Coincident(g7,g8)
    c: Coincident(g8,g9)
    c: Coincident(g9,g10)
    c: Coincident(g10,g11)
    c: Coincident(g11,g12)
    c: Coincident(g12,g13)
    c: Coincident(g13,g14)
    c: Coincident(g14,g15)
    c: Coincident(g15,g16)
    c: Coincident(g16,g17)
    c: Coincident(g17,g18)
    c: Coincident(g18,g19)
    c: Coincident(g19,g20)
    c: Coincident(g20,g21)
    c: Coincident(g21,g22)
    c: Coincident(g22,g23)
    c: Coincident(g23,g0)
    c: Equal(g0, g1-g23) x23
    c: PointOnObject(g0,g24)
    c: PointOnObject(g1,g24)
    c: PointOnObject(g2,g24)
    c: PointOnObject(g3,g24)
    c: PointOnObject(g4,g24)
    c: PointOnObject(g5,g24)
    c: PointOnObject(g6,g24)
    c: PointOnObject(g7,g24)
    c: PointOnObject(g8,g24)
    c: PointOnObject(g9,g24)
    c: PointOnObject(g10,g24)
    c: PointOnObject(g11,g24)
    c: PointOnObject(g12,g24)
    c: PointOnObject(g13,g24)
    c: PointOnObject(g14,g24)
    c: PointOnObject(g15,g24)
    c: PointOnObject(g16,g24)
    c: PointOnObject(g17,g24)
    c: PointOnObject(g18,g24)
    c: PointOnObject(g19,g24)
    c: PointOnObject(g20,g24)
    c: PointOnObject(g21,g24)
    c: PointOnObject(g22,g24)
    c: PointOnObject(g23,g24)
    c: Coincident(g24,g-1)
    c: Horizontal(g19)
    c: DistanceX(g0,g13) = 10
FEATURE [PartDesign::AdditiveLoft] AdditiveLoft040
  AllowMultiFace = false
  Closed = false
  Profile = -> Sketch493
  Refine = true
  Ruled = false
  Sections = -> [Sketch492,Sketch494]
FEATURE [Sketcher::SketchObject] Sketch491
  FullyConstrained = false
  MapMode = 5
  Placement = pos=(0,0,17) rot=(0,0,1;0rad)
  Support = -> [AdditiveLoft040]
  sketch-geometry (1):
    g0: Circle CenterX=0 CenterY=0 CenterZ=0 NormalX=0 NormalY=0 NormalZ=1 AngleXU=0 Radius=4.5
  constraints (2):
    c: Coincident(g0,g-1)
    c: Radius(g0) = 4.5
FEATURE [PartDesign::Pad] Pad095
  AllowMultiFace = false
  BaseFeature = -> AdditiveLoft033
  Direction = (1,1,1)
  Length = 0.7
  Length2 = 100
  Profile = -> Sketch486
  Refine = true
  Type = 0
FEATURE [Sketcher::SketchObject] Sketch481
  FullyConstrained = false
  MapMode = 5
  Placement = pos=(0,0,0) rot=(1,0,0;3.14159rad)
  Support = -> [Pad095]
  sketch-geometry (1):
    g0: Circle CenterX=0 CenterY=0 CenterZ=0 NormalX=0 NormalY=0 NormalZ=1 AngleXU=0 Radius=5
  constraints (2):
    c: Coincident(g0,g-1)
    c: Radius(g0) = 5
FEATURE [PartDesign::Pocket] Pocket101
  AllowMultiFace = false
  BaseFeature = -> Pad095
  Direction = (1,1,1)
  Length = 1
  Length2 = 100
  Profile = -> Sketch481
  Refine = true
  Type = 0
FEATURE [Sketcher::SketchObject] Sketch478
  FullyConstrained = false
  MapMode = 5
  Placement = pos=(0,0,1) rot=(1,0,0;3.14159rad)
  Support = -> [Pocket101]
  sketch-geometry (1):
    g0: Circle CenterX=0 CenterY=0 CenterZ=0 NormalX=0 NormalY=0 NormalZ=1 AngleXU=0 Radius=4.65
  constraints (2):
    c: Coincident(g0,g-1)
    c: Radius(g0) = 4.65
FEATURE [PartDesign::Pocket] Pocket095
  AllowMultiFace = false
  BaseFeature = -> Pocket101
  Direction = (1,1,1)
  Length = 1
  Length2 = 100
  Profile = -> Sketch478
  Refine = true
  Type = 0
FEATURE [Sketcher::SketchObject] Sketch485
  FullyConstrained = false
  MapMode = 5
  Placement = pos=(0,0,2) rot=(1,0,0;3.14159rad)
  Support = -> [Pocket095]
  sketch-geometry (2):
    g0: ArcOfCircle CenterX=0 CenterY=0 CenterZ=0 NormalX=0 NormalY=0 NormalZ=1 AngleXU=0 Radius=3 StartAngle=2.19024 EndAngle=7.23453
    g1: LineSegment StartX=-1.74176 StartY=2.4426 StartZ=0 EndX=1.74176 EndY=2.4426 EndZ=0
  constraints (5):
    c: Coincident(g0,g-1)
    c: Coincident(g1,g0)
    c: Coincident(g1,g0)
    c: Horizontal(g1)
    c: Radius(g0) = 3
FEATURE [PartDesign::Pocket] Pocket102
  AllowMultiFace = false
  BaseFeature = -> Pocket095
  Direction = (1,1,1)
  Length = 8
  Length2 = 100
  Profile = -> Sketch485
  Refine = true
  Type = 0
FEATURE [PartDesign::Chamfer] Chamfer079
  Angle = 45
  Base = -> Pocket102 [Edge82,Edge83]
  BaseFeature = -> Pocket102
  ChamferType = 0
  FlipDirection = false
  Size = 1.4
  Size2 = 1
  SupportTransform = false
  UseAllEdges = false
FEATURE [PartDesign::Chamfer] Chamfer073
  Angle = 45
  Base = -> Chamfer079 [Edge8]
  BaseFeature = -> Chamfer079
  ChamferType = 0
  FlipDirection = false
  Size = 0.3
  Size2 = 1
  SupportTransform = false
  UseAllEdges = false
FEATURE [PartDesign::Fillet] Fillet039
  Base = -> Chamfer073 [Edge93,Face36]
  BaseFeature = -> Chamfer073
  Radius = 0.1
  SupportTransform = false
  UseAllEdges = false
FEATURE [PartDesign::Body] Body174
  Group = -> [Sketch488,Sketch483,Sketch477,AdditiveLoft033,Sketch486,Pad095,Sketch481,Pocket101,Sketch478,Pocket095,Sketch485,Pocket102,Chamfer079,Chamfer073,Fillet039]
  Origin = -> Origin934
  Tip = -> Fillet039
FEATURE [App::Part] Part138  label="Cap031"
  Group = -> [Body174]
  Origin = -> Origin924
  Placement = pos=(-40.005,-13.335,0) rot=(0,0,1;0rad)
  expr: .Placement.Base.x = -40.005
  expr: .Placement.Base.y = -13.335
FEATURE [PartDesign::Pad] Pad096
  AllowMultiFace = false
  BaseFeature = -> AdditiveLoft040
  Direction = (1,1,1)
  Length = 0.7
  Length2 = 100
  Profile = -> Sketch491
  Refine = true
  Type = 0
FEATURE [Sketcher::SketchObject] Sketch497
  FullyConstrained = false
  MapMode = 5
  Placement = pos=(0,0,0) rot=(1,0,0;3.14159rad)
  Support = -> [Pad096]
  sketch-geometry (1):
    g0: Circle CenterX=0 CenterY=0 CenterZ=0 NormalX=0 NormalY=0 NormalZ=1 AngleXU=0 Radius=5
  constraints (2):
    c: Coincident(g0,g-1)
    c: Radius(g0) = 5
FEATURE [PartDesign::Pocket] Pocket104
  AllowMultiFace = false
  BaseFeature = -> Pad096
  Direction = (1,1,1)
  Length = 1
  Length2 = 100
  Profile = -> Sketch497
  Refine = true
  Type = 0
FEATURE [Sketcher::SketchObject] Sketch498
  FullyConstrained = false
  MapMode = 5
  Placement = pos=(0,0,1) rot=(1,0,0;3.14159rad)
  Support = -> [Pocket104]
  sketch-geometry (1):
    g0: Circle CenterX=0 CenterY=0 CenterZ=0 NormalX=0 NormalY=0 NormalZ=1 AngleXU=0 Radius=4.65
  constraints (2):
    c: Coincident(g0,g-1)
    c: Radius(g0) = 4.65
FEATURE [PartDesign::Pocket] Pocket103
  AllowMultiFace = false
  BaseFeature = -> Pocket104
  Direction = (1,1,1)
  Length = 1
  Length2 = 100
  Profile = -> Sketch498
  Refine = true
  Type = 0
FEATURE [Sketcher::SketchObject] Sketch496
  FullyConstrained = false
  MapMode = 5
  Placement = pos=(0,0,2) rot=(1,0,0;3.14159rad)
  Support = -> [Pocket103]
  sketch-geometry (2):
    g0: ArcOfCircle CenterX=0 CenterY=0 CenterZ=0 NormalX=0 NormalY=0 NormalZ=1 AngleXU=0 Radius=3 StartAngle=2.19024 EndAngle=7.23453
    g1: LineSegment StartX=-1.74176 StartY=2.4426 StartZ=0 EndX=1.74176 EndY=2.4426 EndZ=0
  constraints (5):
    c: Coincident(g0,g-1)
    c: Coincident(g1,g0)
    c: Coincident(g1,g0)
    c: Horizontal(g1)
    c: Radius(g0) = 3
FEATURE [PartDesign::Pocket] Pocket105
  AllowMultiFace = false
  BaseFeature = -> Pad093
  Direction = (1,1,1)
  Length = 1
  Length2 = 100
  Profile = -> Sketch487
  Refine = true
  Type = 0
FEATURE [Sketcher::SketchObject] Sketch475
  FullyConstrained = false
  MapMode = 5
  Placement = pos=(0,0,1) rot=(1,0,0;3.14159rad)
  Support = -> [Pocket105]
  sketch-geometry (1):
    g0: Circle CenterX=0 CenterY=0 CenterZ=0 NormalX=0 NormalY=0 NormalZ=1 AngleXU=0 Radius=4.65
  constraints (2):
    c: Coincident(g0,g-1)
    c: Radius(g0) = 4.65
FEATURE [PartDesign::Pocket] Pocket100
  AllowMultiFace = false
  BaseFeature = -> Pocket105
  Direction = (1,1,1)
  Length = 1
  Length2 = 100
  Profile = -> Sketch475
  Refine = true
  Type = 0
FEATURE [Sketcher::SketchObject] Sketch482
  FullyConstrained = false
  MapMode = 5
  Placement = pos=(0,0,2) rot=(1,0,0;3.14159rad)
  Support = -> [Pocket100]
  sketch-geometry (2):
    g0: ArcOfCircle CenterX=0 CenterY=0 CenterZ=0 NormalX=0 NormalY=0 NormalZ=1 AngleXU=0 Radius=3 StartAngle=2.19024 EndAngle=7.23453
    g1: LineSegment StartX=-1.74176 StartY=2.4426 StartZ=0 EndX=1.74176 EndY=2.4426 EndZ=0
  constraints (5):
    c: Coincident(g0,g-1)
    c: Coincident(g1,g0)
    c: Coincident(g1,g0)
    c: Horizontal(g1)
    c: Radius(g0) = 3
FEATURE [PartDesign::Pocket] Pocket106
  AllowMultiFace = false
  BaseFeature = -> Pocket100
  Direction = (1,1,1)
  Length = 8
  Length2 = 100
  Profile = -> Sketch482
  Refine = true
  Type = 0
FEATURE [PartDesign::Chamfer] Chamfer076
  Angle = 45
  Base = -> Pocket106 [Edge82,Edge83]
  BaseFeature = -> Pocket106
  ChamferType = 0
  FlipDirection = false
  Size = 1.4
  Size2 = 1
  SupportTransform = false
  UseAllEdges = false
FEATURE [PartDesign::Chamfer] Chamfer075
  Angle = 45
  Base = -> Chamfer076 [Edge8]
  BaseFeature = -> Chamfer076
  ChamferType = 0
  FlipDirection = false
  Size = 0.3
  Size2 = 1
  SupportTransform = false
  UseAllEdges = false
FEATURE [PartDesign::Fillet] Fillet040
  Base = -> Chamfer075 [Edge93,Face36]
  BaseFeature = -> Chamfer075
  Radius = 0.1
  SupportTransform = false
  UseAllEdges = false
FEATURE [PartDesign::Body] Body184
  Group = -> [Sketch490,Sketch489,Sketch479,AdditiveLoft039,Sketch476,Pad093,Sketch487,Pocket105,Sketch475,Pocket100,Sketch482,Pocket106,Chamfer076,Chamfer075,Fillet040]
  Origin = -> Origin937
  Tip = -> Fillet040
FEATURE [App::Part] Part136  label="Cap029"
  Group = -> [Body184]
  Origin = -> Origin938
  Placement = pos=(-13.335,-13.335,0) rot=(0,0,1;0rad)
  expr: .Placement.Base.x = -13.335
  expr: .Placement.Base.y = -13.335
FEATURE [PartDesign::Pocket] Pocket107
  AllowMultiFace = false
  BaseFeature = -> Pocket103
  Direction = (1,1,1)
  Length = 8
  Length2 = 100
  Profile = -> Sketch496
  Refine = true
  Type = 0
FEATURE [PartDesign::Chamfer] Chamfer078
  Angle = 45
  Base = -> Pocket107 [Edge82,Edge83]
  BaseFeature = -> Pocket107
  ChamferType = 0
  FlipDirection = false
  Size = 1.4
  Size2 = 1
  SupportTransform = false
  UseAllEdges = false
FEATURE [PartDesign::Chamfer] Chamfer074
  Angle = 45
  Base = -> Chamfer078 [Edge8]
  BaseFeature = -> Chamfer078
  ChamferType = 0
  FlipDirection = false
  Size = 0.3
  Size2 = 1
  SupportTransform = false
  UseAllEdges = false
FEATURE [PartDesign::Fillet] Fillet043
  Base = -> Chamfer074 [Edge93,Face36]
  BaseFeature = -> Chamfer074
  Radius = 0.1
  SupportTransform = false
  UseAllEdges = false
FEATURE [PartDesign::Body] Body186
  Group = -> [Sketch493,Sketch492,Sketch494,AdditiveLoft040,Sketch491,Pad096,Sketch497,Pocket104,Sketch498,Pocket103,Sketch496,Pocket107,Chamfer078,Chamfer074,Fillet043]
  Origin = -> Origin929
  Tip = -> Fillet043
FEATURE [App::Part] Part144  label="Cap037"
  Group = -> [Body186]
  Origin = -> Origin928
  Placement = pos=(13.335,-13.335,0) rot=(0,0,1;0rad)
  expr: .Placement.Base.x = 13.335
  expr: .Placement.Base.y = -13.335
FEATURE [Sketcher::SketchObject] Sketch500
  FullyConstrained = false
  MapMode = 5
  Placement = pos=(0,0,0) rot=(0.57735,0.57735,0.57735;2.0944rad)
  Support = -> [YZ_Plane947]
  sketch-geometry (6):
    g0: LineSegment StartX=0 StartY=0 StartZ=0 EndX=-1.6 EndY=0 EndZ=0
    g1: LineSegment StartX=-1.6 StartY=0 StartZ=0 EndX=-1.6 EndY=-0.4 EndZ=0
    g2: LineSegment StartX=-1.6 StartY=-0.4 StartZ=0 EndX=-1.5 EndY=-0.4 EndZ=0
    g3: LineSegment StartX=-1.5 StartY=-0.4 StartZ=0 EndX=-1.5 EndY=-7 EndZ=0
    g4: LineSegment StartX=-1.5 StartY=-7 StartZ=0 EndX=0 EndY=-7 EndZ=0
    g5: LineSegment StartX=0 StartY=-7 StartZ=0 EndX=0 EndY=0 EndZ=0
  constraints (17):
    c: Coincident(g0,g-1)
    c: Horizontal(g0)
    c: Coincident(g1,g0)
    c: Coincident(g2,g1)
    c: Coincident(g3,g2)
    c: Vertical(g3)
    c: Coincident(g4,g3)
    c: Coincident(g5,g4)
    c: Coincident(g5,g-1)
    c: Vertical(g5)
    c: Horizontal(g4)
    c: Horizontal(g2)
    c: Vertical(g1)
    c: DistanceY(g1,g1) = 0.4
    c: DistanceX(g4,g4) = 1.5
    c: DistanceX(g0,g0) = 1.6
    c: DistanceY(g5,g5) = 7
FEATURE [PartDesign::Revolution] Revolution054
  AllowMultiFace = false
  Angle = 360
  Axis = (0,0,1)
  Base = (0,0,0)
  Placement = pos=(0,0,0) rot=(0.57735,0.57735,0.57735;2.0944rad)
  Profile = -> Sketch500
  ReferenceAxis = -> Sketch500 [V_Axis]
FEATURE [Sketcher::SketchObject] Sketch503
  AttachmentOffset = pos=(0,0,7) rot=(0,0,1;0rad)
  FullyConstrained = false
  MapMode = 5
  Placement = pos=(0,0,7) rot=(0,0,1;0rad)
  Support = -> [XY_Plane927]
  sketch-geometry (25):
    g0: LineSegment StartX=-0.724089 StartY=5.5 StartZ=0 EndX=-2.12292 EndY=5.12518 EndZ=0
    g1: LineSegment StartX=-2.12292 StartY=5.12518 StartZ=0 EndX=-3.37708 EndY=4.4011 EndZ=0
    g2: LineSegment StartX=-3.37708 StartY=4.4011 StartZ=0 EndX=-4.4011 EndY=3.37708 EndZ=0
    g3: LineSegment StartX=-4.4011 StartY=3.37708 StartZ=0 EndX=-5.12518 EndY=2.12292 EndZ=0
    g4: LineSegment StartX=-5.12518 StartY=2.12292 StartZ=0 EndX=-5.5 EndY=0.724089 EndZ=0
    g5: LineSegment StartX=-5.5 StartY=0.724089 StartZ=0 EndX=-5.5 EndY=-0.724089 EndZ=0
    g6: LineSegment StartX=-5.5 StartY=-0.724089 StartZ=0 EndX=-5.12518 EndY=-2.12292 EndZ=0
    g7: LineSegment StartX=-5.12518 StartY=-2.12292 StartZ=0 EndX=-4.4011 EndY=-3.37708 EndZ=0
    g8: LineSegment StartX=-4.4011 StartY=-3.37708 StartZ=0 EndX=-3.37708 EndY=-4.4011 EndZ=0
    g9: LineSegment StartX=-3.37708 StartY=-4.4011 StartZ=0 EndX=-2.12292 EndY=-5.12518 EndZ=0
    g10: LineSegment StartX=-2.12292 StartY=-5.12518 StartZ=0 EndX=-0.724089 EndY=-5.5 EndZ=0
    g11: LineSegment StartX=-0.724089 StartY=-5.5 StartZ=0 EndX=0.724089 EndY=-5.5 EndZ=0
    g12: LineSegment StartX=0.724089 StartY=-5.5 StartZ=0 EndX=2.12292 EndY=-5.12518 EndZ=0
    g13: LineSegment StartX=2.12292 StartY=-5.12518 StartZ=0 EndX=3.37708 EndY=-4.4011 EndZ=0
    g14: LineSegment StartX=3.37708 StartY=-4.4011 StartZ=0 EndX=4.4011 EndY=-3.37708 EndZ=0
    g15: LineSegment StartX=4.4011 StartY=-3.37708 StartZ=0 EndX=5.12518 EndY=-2.12292 EndZ=0
    g16: LineSegment StartX=5.12518 StartY=-2.12292 StartZ=0 EndX=5.5 EndY=-0.724089 EndZ=0
    g17: LineSegment StartX=5.5 StartY=-0.724089 StartZ=0 EndX=5.5 EndY=0.724089 EndZ=0
    g18: LineSegment StartX=5.5 StartY=0.724089 StartZ=0 EndX=5.12518 EndY=2.12292 EndZ=0
    g19: LineSegment StartX=5.12518 StartY=2.12292 StartZ=0 EndX=4.4011 EndY=3.37708 EndZ=0
    g20: LineSegment StartX=4.4011 StartY=3.37708 StartZ=0 EndX=3.37708 EndY=4.4011 EndZ=0
    g21: LineSegment StartX=3.37708 StartY=4.4011 StartZ=0 EndX=2.12292 EndY=5.12518 EndZ=0
    g22: LineSegment StartX=2.12292 StartY=5.12518 StartZ=0 EndX=0.724089 EndY=5.5 EndZ=0
    g23: LineSegment StartX=0.724089 StartY=5.5 StartZ=0 EndX=-0.724089 EndY=5.5 EndZ=0
    g24: Circle CenterX=0 CenterY=0 CenterZ=0 NormalX=0 NormalY=0 NormalZ=1 AngleXU=0 Radius=5.54746
  constraints (52):
    c: Coincident(g0,g1)
    c: Coincident(g1,g2)
    c: Coincident(g2,g3)
    c: Coincident(g3,g4)
    c: Coincident(g4,g5)
    c: Coincident(g5,g6)
    c: Coincident(g6,g7)
    c: Coincident(g7,g8)
    c: Coincident(g8,g9)
    c: Coincident(g9,g10)
    c: Coincident(g10,g11)
    c: Coincident(g11,g12)
    c: Coincident(g12,g13)
    c: Coincident(g13,g14)
    c: Coincident(g14,g15)
    c: Coincident(g15,g16)
    c: Coincident(g16,g17)
    c: Coincident(g17,g18)
    c: Coincident(g18,g19)
    c: Coincident(g19,g20)
    c: Coincident(g20,g21)
    c: Coincident(g21,g22)
    c: Coincident(g22,g23)
    c: Coincident(g23,g0)
    c: Equal(g0, g1-g23) x23
    c: PointOnObject(g0,g24)
    c: PointOnObject(g1,g24)
    c: PointOnObject(g2,g24)
    c: PointOnObject(g3,g24)
    c: PointOnObject(g4,g24)
    c: PointOnObject(g5,g24)
    c: PointOnObject(g6,g24)
    c: PointOnObject(g7,g24)
    c: PointOnObject(g8,g24)
    c: PointOnObject(g9,g24)
    c: PointOnObject(g10,g24)
    c: PointOnObject(g11,g24)
    c: PointOnObject(g12,g24)
    c: PointOnObject(g13,g24)
    c: PointOnObject(g14,g24)
    c: PointOnObject(g15,g24)
    c: PointOnObject(g16,g24)
    c: PointOnObject(g17,g24)
    c: PointOnObject(g18,g24)
    c: PointOnObject(g19,g24)
    c: PointOnObject(g20,g24)
    c: PointOnObject(g21,g24)
    c: PointOnObject(g22,g24)
    c: PointOnObject(g23,g24)
    c: Coincident(g24,g-1)
    c: Horizontal(g23)
    c: DistanceX(g4,g17) = 11
FEATURE [Sketcher::SketchObject] Sketch505
  FullyConstrained = false
  MapMode = 5
  Support = -> [XY_Plane927]
  sketch-geometry (25):
    g0: LineSegment StartX=-0.789915 StartY=6 StartZ=0 EndX=-2.31591 EndY=5.59111 EndZ=0
    g1: LineSegment StartX=-2.31591 StartY=5.59111 StartZ=0 EndX=-3.68409 EndY=4.80119 EndZ=0
    g2: LineSegment StartX=-3.68409 StartY=4.80119 StartZ=0 EndX=-4.80119 EndY=3.68409 EndZ=0
    g3: LineSegment StartX=-4.80119 StartY=3.68409 StartZ=0 EndX=-5.59111 EndY=2.31591 EndZ=0
    g4: LineSegment StartX=-5.59111 StartY=2.31591 StartZ=0 EndX=-6 EndY=0.789915 EndZ=0
    g5: LineSegment StartX=-6 StartY=0.789915 StartZ=0 EndX=-6 EndY=-0.789915 EndZ=0
    g6: LineSegment StartX=-6 StartY=-0.789915 StartZ=0 EndX=-5.59111 EndY=-2.31591 EndZ=0
    g7: LineSegment StartX=-5.59111 StartY=-2.31591 StartZ=0 EndX=-4.80119 EndY=-3.68409 EndZ=0
    g8: LineSegment StartX=-4.80119 StartY=-3.68409 StartZ=0 EndX=-3.68409 EndY=-4.80119 EndZ=0
    g9: LineSegment StartX=-3.68409 StartY=-4.80119 StartZ=0 EndX=-2.31591 EndY=-5.59111 EndZ=0
    g10: LineSegment StartX=-2.31591 StartY=-5.59111 StartZ=0 EndX=-0.789915 EndY=-6 EndZ=0
    g11: LineSegment StartX=-0.789915 StartY=-6 StartZ=0 EndX=0.789915 EndY=-6 EndZ=0
    g12: LineSegment StartX=0.789915 StartY=-6 StartZ=0 EndX=2.31591 EndY=-5.59111 EndZ=0
    g13: LineSegment StartX=2.31591 StartY=-5.59111 StartZ=0 EndX=3.68409 EndY=-4.80119 EndZ=0
    g14: LineSegment StartX=3.68409 StartY=-4.80119 StartZ=0 EndX=4.80119 EndY=-3.68409 EndZ=0
    g15: LineSegment StartX=4.80119 StartY=-3.68409 StartZ=0 EndX=5.59111 EndY=-2.31591 EndZ=0
    g16: LineSegment StartX=5.59111 StartY=-2.31591 StartZ=0 EndX=6 EndY=-0.789915 EndZ=0
    g17: LineSegment StartX=6 StartY=-0.789915 StartZ=0 EndX=6 EndY=0.789915 EndZ=0
    g18: LineSegment StartX=6 StartY=0.789915 StartZ=0 EndX=5.59111 EndY=2.31591 EndZ=0
    g19: LineSegment StartX=5.59111 StartY=2.31591 StartZ=0 EndX=4.80119 EndY=3.68409 EndZ=0
    g20: LineSegment StartX=4.80119 StartY=3.68409 StartZ=0 EndX=3.68409 EndY=4.80119 EndZ=0
    g21: LineSegment StartX=3.68409 StartY=4.80119 StartZ=0 EndX=2.31591 EndY=5.59111 EndZ=0
    g22: LineSegment StartX=2.31591 StartY=5.59111 StartZ=0 EndX=0.789915 EndY=6 EndZ=0
    g23: LineSegment StartX=0.789915 StartY=6 StartZ=0 EndX=-0.789915 EndY=6 EndZ=0
    g24: Circle CenterX=0 CenterY=0 CenterZ=0 NormalX=0 NormalY=0 NormalZ=1 AngleXU=0 Radius=6.05177
  constraints (52):
    c: Coincident(g0,g1)
    c: Coincident(g1,g2)
    c: Coincident(g2,g3)
    c: Coincident(g3,g4)
    c: Coincident(g4,g5)
    c: Coincident(g5,g6)
    c: Coincident(g6,g7)
    c: Coincident(g7,g8)
    c: Coincident(g8,g9)
    c: Coincident(g9,g10)
    c: Coincident(g10,g11)
    c: Coincident(g11,g12)
    c: Coincident(g12,g13)
    c: Coincident(g13,g14)
    c: Coincident(g14,g15)
    c: Coincident(g15,g16)
    c: Coincident(g16,g17)
    c: Coincident(g17,g18)
    c: Coincident(g18,g19)
    c: Coincident(g19,g20)
    c: Coincident(g20,g21)
    c: Coincident(g21,g22)
    c: Coincident(g22,g23)
    c: Coincident(g23,g0)
    c: Equal(g0, g1-g23) x23
    c: PointOnObject(g0,g24)
    c: PointOnObject(g1,g24)
    c: PointOnObject(g2,g24)
    c: PointOnObject(g3,g24)
    c: PointOnObject(g4,g24)
    c: PointOnObject(g5,g24)
    c: PointOnObject(g6,g24)
    c: PointOnObject(g7,g24)
    c: PointOnObject(g8,g24)
    c: PointOnObject(g9,g24)
    c: PointOnObject(g10,g24)
    c: PointOnObject(g11,g24)
    c: PointOnObject(g12,g24)
    c: PointOnObject(g13,g24)
    c: PointOnObject(g14,g24)
    c: PointOnObject(g15,g24)
    c: PointOnObject(g16,g24)
    c: PointOnObject(g17,g24)
    c: PointOnObject(g18,g24)
    c: PointOnObject(g19,g24)
    c: PointOnObject(g20,g24)
    c: PointOnObject(g21,g24)
    c: PointOnObject(g22,g24)
    c: PointOnObject(g23,g24)
    c: Coincident(g24,g-1)
    c: Horizontal(g23)
    c: DistanceX(g4,g17) = 12
FEATURE [Sketcher::SketchObject] Sketch506
  FullyConstrained = false
  MapMode = 5
  Placement = pos=(0,0,0) rot=(0.57735,0.57735,0.57735;2.0944rad)
  Support = -> [YZ_Plane945]
  sketch-geometry (6):
    g0: LineSegment StartX=0 StartY=0 StartZ=0 EndX=-1.6 EndY=0 EndZ=0
    g1: LineSegment StartX=-1.6 StartY=0 StartZ=0 EndX=-1.6 EndY=-0.4 EndZ=0
    g2: LineSegment StartX=-1.6 StartY=-0.4 StartZ=0 EndX=-1.5 EndY=-0.4 EndZ=0
    g3: LineSegment StartX=-1.5 StartY=-0.4 StartZ=0 EndX=-1.5 EndY=-7 EndZ=0
    g4: LineSegment StartX=-1.5 StartY=-7 StartZ=0 EndX=0 EndY=-7 EndZ=0
    g5: LineSegment StartX=0 StartY=-7 StartZ=0 EndX=0 EndY=0 EndZ=0
  constraints (17):
    c: Coincident(g0,g-1)
    c: Horizontal(g0)
    c: Coincident(g1,g0)
    c: Coincident(g2,g1)
    c: Coincident(g3,g2)
    c: Vertical(g3)
    c: Coincident(g4,g3)
    c: Coincident(g5,g4)
    c: Coincident(g5,g-1)
    c: Vertical(g5)
    c: Horizontal(g4)
    c: Horizontal(g2)
    c: Vertical(g1)
    c: DistanceY(g1,g1) = 0.4
    c: DistanceX(g4,g4) = 1.5
    c: DistanceX(g0,g0) = 1.6
    c: DistanceY(g5,g5) = 7
FEATURE [PartDesign::Revolution] Revolution057
  AllowMultiFace = false
  Angle = 360
  Axis = (0,0,1)
  Base = (0,0,0)
  Placement = pos=(0,0,0) rot=(0.57735,0.57735,0.57735;2.0944rad)
  Profile = -> Sketch506
  ReferenceAxis = -> Sketch506 [V_Axis]
FEATURE [Sketcher::SketchObject] Sketch509
  AttachmentOffset = pos=(0,0,17) rot=(0,0,1;0rad)
  FullyConstrained = false
  MapMode = 5
  Placement = pos=(0,0,17) rot=(0,0,1;0rad)
  Support = -> [XY_Plane927]
  sketch-geometry (25):
    g0: LineSegment StartX=-4.65926 StartY=1.92993 StartZ=0 EndX=-5 EndY=0.658262 EndZ=0
    g1: LineSegment StartX=-5 StartY=0.658262 StartZ=0 EndX=-5 EndY=-0.658262 EndZ=0
    g2: LineSegment StartX=-5 StartY=-0.658262 StartZ=0 EndX=-4.65926 EndY=-1.92993 EndZ=0
    g3: LineSegment StartX=-4.65926 StartY=-1.92993 StartZ=0 EndX=-4.001 EndY=-3.07007 EndZ=0
    g4: LineSegment StartX=-4.001 StartY=-3.07007 StartZ=0 EndX=-3.07007 EndY=-4.001 EndZ=0
    g5: LineSegment StartX=-3.07007 StartY=-4.001 StartZ=0 EndX=-1.92993 EndY=-4.65926 EndZ=0
    g6: LineSegment StartX=-1.92993 StartY=-4.65926 StartZ=0 EndX=-0.658262 EndY=-5 EndZ=0
    g7: LineSegment StartX=-0.658262 StartY=-5 StartZ=0 EndX=0.658262 EndY=-5 EndZ=0
    g8: LineSegment StartX=0.658262 StartY=-5 StartZ=0 EndX=1.92993 EndY=-4.65926 EndZ=0
    g9: LineSegment StartX=1.92993 StartY=-4.65926 StartZ=0 EndX=3.07007 EndY=-4.001 EndZ=0
    g10: LineSegment StartX=3.07007 StartY=-4.001 StartZ=0 EndX=4.001 EndY=-3.07007 EndZ=0
    g11: LineSegment StartX=4.001 StartY=-3.07007 StartZ=0 EndX=4.65926 EndY=-1.92993 EndZ=0
    g12: LineSegment StartX=4.65926 StartY=-1.92993 StartZ=0 EndX=5 EndY=-0.658262 EndZ=0
    g13: LineSegment StartX=5 StartY=-0.658262 StartZ=0 EndX=5 EndY=0.658262 EndZ=0
    g14: LineSegment StartX=5 StartY=0.658262 StartZ=0 EndX=4.65926 EndY=1.92993 EndZ=0
    g15: LineSegment StartX=4.65926 StartY=1.92993 StartZ=0 EndX=4.001 EndY=3.07007 EndZ=0
    g16: LineSegment StartX=4.001 StartY=3.07007 StartZ=0 EndX=3.07007 EndY=4.001 EndZ=0
    g17: LineSegment StartX=3.07007 StartY=4.001 StartZ=0 EndX=1.92993 EndY=4.65926 EndZ=0
    g18: LineSegment StartX=1.92993 StartY=4.65926 StartZ=0 EndX=0.658262 EndY=5 EndZ=0
    g19: LineSegment StartX=0.658262 StartY=5 StartZ=0 EndX=-0.658262 EndY=5 EndZ=0
    g20: LineSegment StartX=-0.658262 StartY=5 StartZ=0 EndX=-1.92993 EndY=4.65926 EndZ=0
    g21: LineSegment StartX=-1.92993 StartY=4.65926 StartZ=0 EndX=-3.07007 EndY=4.001 EndZ=0
    g22: LineSegment StartX=-3.07007 StartY=4.001 StartZ=0 EndX=-4.001 EndY=3.07007 EndZ=0
    g23: LineSegment StartX=-4.001 StartY=3.07007 StartZ=0 EndX=-4.65926 EndY=1.92993 EndZ=0
    g24: Circle CenterX=0 CenterY=0 CenterZ=0 NormalX=0 NormalY=0 NormalZ=1 AngleXU=0 Radius=5.04314
  constraints (52):
    c: Coincident(g0,g1)
    c: Coincident(g1,g2)
    c: Coincident(g2,g3)
    c: Coincident(g3,g4)
    c: Coincident(g4,g5)
    c: Coincident(g5,g6)
    c: Coincident(g6,g7)
    c: Coincident(g7,g8)
    c: Coincident(g8,g9)
    c: Coincident(g9,g10)
    c: Coincident(g10,g11)
    c: Coincident(g11,g12)
    c: Coincident(g12,g13)
    c: Coincident(g13,g14)
    c: Coincident(g14,g15)
    c: Coincident(g15,g16)
    c: Coincident(g16,g17)
    c: Coincident(g17,g18)
    c: Coincident(g18,g19)
    c: Coincident(g19,g20)
    c: Coincident(g20,g21)
    c: Coincident(g21,g22)
    c: Coincident(g22,g23)
    c: Coincident(g23,g0)
    c: Equal(g0, g1-g23) x23
    c: PointOnObject(g0,g24)
    c: PointOnObject(g1,g24)
    c: PointOnObject(g2,g24)
    c: PointOnObject(g3,g24)
    c: PointOnObject(g4,g24)
    c: PointOnObject(g5,g24)
    c: PointOnObject(g6,g24)
    c: PointOnObject(g7,g24)
    c: PointOnObject(g8,g24)
    c: PointOnObject(g9,g24)
    c: PointOnObject(g10,g24)
    c: PointOnObject(g11,g24)
    c: PointOnObject(g12,g24)
    c: PointOnObject(g13,g24)
    c: PointOnObject(g14,g24)
    c: PointOnObject(g15,g24)
    c: PointOnObject(g16,g24)
    c: PointOnObject(g17,g24)
    c: PointOnObject(g18,g24)
    c: PointOnObject(g19,g24)
    c: PointOnObject(g20,g24)
    c: PointOnObject(g21,g24)
    c: PointOnObject(g22,g24)
    c: PointOnObject(g23,g24)
    c: Coincident(g24,g-1)
    c: Horizontal(g19)
    c: DistanceX(g0,g13) = 10
FEATURE [PartDesign::AdditiveLoft] AdditiveLoft036
  AllowMultiFace = false
  Closed = false
  Profile = -> Sketch505
  Refine = true
  Ruled = false
  Sections = -> [Sketch503,Sketch509]
FEATURE [Sketcher::SketchObject] Sketch502
  FullyConstrained = false
  MapMode = 5
  Placement = pos=(0,0,17) rot=(0,0,1;0rad)
  Support = -> [AdditiveLoft036]
  sketch-geometry (1):
    g0: Circle CenterX=0 CenterY=0 CenterZ=0 NormalX=0 NormalY=0 NormalZ=1 AngleXU=0 Radius=4.5
  constraints (2):
    c: Coincident(g0,g-1)
    c: Radius(g0) = 4.5
FEATURE [PartDesign::Pad] Pad099
  AllowMultiFace = false
  BaseFeature = -> AdditiveLoft036
  Direction = (1,1,1)
  Length = 0.7
  Length2 = 100
  Profile = -> Sketch502
  Refine = true
  Type = 0
FEATURE [Sketcher::SketchObject] Sketch501
  FullyConstrained = false
  MapMode = 5
  Placement = pos=(0,0,0) rot=(1,0,0;3.14159rad)
  Support = -> [Pad099]
  sketch-geometry (1):
    g0: Circle CenterX=0 CenterY=0 CenterZ=0 NormalX=0 NormalY=0 NormalZ=1 AngleXU=0 Radius=5
  constraints (2):
    c: Coincident(g0,g-1)
    c: Radius(g0) = 5
FEATURE [PartDesign::Pocket] Pocket108
  AllowMultiFace = false
  BaseFeature = -> Pad099
  Direction = (1,1,1)
  Length = 1
  Length2 = 100
  Profile = -> Sketch501
  Refine = true
  Type = 0
FEATURE [Sketcher::SketchObject] Sketch508
  FullyConstrained = false
  MapMode = 5
  Placement = pos=(0,0,1) rot=(1,0,0;3.14159rad)
  Support = -> [Pocket108]
  sketch-geometry (1):
    g0: Circle CenterX=0 CenterY=0 CenterZ=0 NormalX=0 NormalY=0 NormalZ=1 AngleXU=0 Radius=4.65
  constraints (2):
    c: Coincident(g0,g-1)
    c: Radius(g0) = 4.65
FEATURE [PartDesign::Pocket] Pocket109
  AllowMultiFace = false
  BaseFeature = -> Pocket108
  Direction = (1,1,1)
  Length = 1
  Length2 = 100
  Profile = -> Sketch508
  Refine = true
  Type = 0
FEATURE [Sketcher::SketchObject] Sketch499
  FullyConstrained = false
  MapMode = 5
  Placement = pos=(0,0,2) rot=(1,0,0;3.14159rad)
  Support = -> [Pocket109]
  sketch-geometry (2):
    g0: ArcOfCircle CenterX=0 CenterY=0 CenterZ=0 NormalX=0 NormalY=0 NormalZ=1 AngleXU=0 Radius=3 StartAngle=2.19024 EndAngle=7.23453
    g1: LineSegment StartX=-1.74176 StartY=2.4426 StartZ=0 EndX=1.74176 EndY=2.4426 EndZ=0
  constraints (5):
    c: Coincident(g0,g-1)
    c: Coincident(g1,g0)
    c: Coincident(g1,g0)
    c: Horizontal(g1)
    c: Radius(g0) = 3
FEATURE [PartDesign::Pocket] Pocket110
  AllowMultiFace = false
  BaseFeature = -> Pocket109
  Direction = (1,1,1)
  Length = 8
  Length2 = 100
  Profile = -> Sketch499
  Refine = true
  Type = 0
FEATURE [PartDesign::Chamfer] Chamfer077
  Angle = 45
  Base = -> Pocket110 [Edge82,Edge83]
  BaseFeature = -> Pocket110
  ChamferType = 0
  FlipDirection = false
  Size = 1.4
  Size2 = 1
  SupportTransform = false
  UseAllEdges = false
FEATURE [PartDesign::Chamfer] Chamfer081
  Angle = 45
  Base = -> Chamfer077 [Edge8]
  BaseFeature = -> Chamfer077
  ChamferType = 0
  FlipDirection = false
  Size = 0.3
  Size2 = 1
  SupportTransform = false
  UseAllEdges = false
FEATURE [PartDesign::Fillet] Fillet041
  Base = -> Chamfer081 [Edge93,Face36]
  BaseFeature = -> Chamfer081
  Radius = 0.1
  SupportTransform = false
  UseAllEdges = false
FEATURE [Sketcher::SketchObject] Sketch510
  FullyConstrained = false
  MapMode = 5
  Placement = pos=(0,0,0) rot=(0.57735,0.57735,0.57735;2.0944rad)
  Support = -> [YZ_Plane946]
  sketch-geometry (6):
    g0: LineSegment StartX=0 StartY=0 StartZ=0 EndX=-1.6 EndY=0 EndZ=0
    g1: LineSegment StartX=-1.6 StartY=0 StartZ=0 EndX=-1.6 EndY=-0.4 EndZ=0
    g2: LineSegment StartX=-1.6 StartY=-0.4 StartZ=0 EndX=-1.5 EndY=-0.4 EndZ=0
    g3: LineSegment StartX=-1.5 StartY=-0.4 StartZ=0 EndX=-1.5 EndY=-7 EndZ=0
    g4: LineSegment StartX=-1.5 StartY=-7 StartZ=0 EndX=0 EndY=-7 EndZ=0
    g5: LineSegment StartX=0 StartY=-7 StartZ=0 EndX=0 EndY=0 EndZ=0
  constraints (17):
    c: Coincident(g0,g-1)
    c: Horizontal(g0)
    c: Coincident(g1,g0)
    c: Coincident(g2,g1)
    c: Coincident(g3,g2)
    c: Vertical(g3)
    c: Coincident(g4,g3)
    c: Coincident(g5,g4)
    c: Coincident(g5,g-1)
    c: Vertical(g5)
    c: Horizontal(g4)
    c: Horizontal(g2)
    c: Vertical(g1)
    c: DistanceY(g1,g1) = 0.4
    c: DistanceX(g4,g4) = 1.5
    c: DistanceX(g0,g0) = 1.6
    c: DistanceY(g5,g5) = 7
FEATURE [PartDesign::Revolution] Revolution056
  AllowMultiFace = false
  Angle = 360
  Axis = (0,0,1)
  Base = (0,0,0)
  Placement = pos=(0,0,0) rot=(0.57735,0.57735,0.57735;2.0944rad)
  Profile = -> Sketch510
  ReferenceAxis = -> Sketch510 [V_Axis]
FEATURE [Sketcher::SketchObject] Sketch511
  FullyConstrained = false
  MapMode = 5
  Placement = pos=(0,0,0) rot=(0.57735,0.57735,0.57735;2.0944rad)
  Support = -> [YZ_Plane951]
  sketch-geometry (6):
    g0: LineSegment StartX=0 StartY=0 StartZ=0 EndX=-1.6 EndY=0 EndZ=0
    g1: LineSegment StartX=-1.6 StartY=0 StartZ=0 EndX=-1.6 EndY=-0.4 EndZ=0
    g2: LineSegment StartX=-1.6 StartY=-0.4 StartZ=0 EndX=-1.5 EndY=-0.4 EndZ=0
    g3: LineSegment StartX=-1.5 StartY=-0.4 StartZ=0 EndX=-1.5 EndY=-7 EndZ=0
    g4: LineSegment StartX=-1.5 StartY=-7 StartZ=0 EndX=0 EndY=-7 EndZ=0
    g5: LineSegment StartX=0 StartY=-7 StartZ=0 EndX=0 EndY=0 EndZ=0
  constraints (17):
    c: Coincident(g0,g-1)
    c: Horizontal(g0)
    c: Coincident(g1,g0)
    c: Coincident(g2,g1)
    c: Coincident(g3,g2)
    c: Vertical(g3)
    c: Coincident(g4,g3)
    c: Coincident(g5,g4)
    c: Coincident(g5,g-1)
    c: Vertical(g5)
    c: Horizontal(g4)
    c: Horizontal(g2)
    c: Vertical(g1)
    c: DistanceY(g1,g1) = 0.4
    c: DistanceX(g4,g4) = 1.5
    c: DistanceX(g0,g0) = 1.6
    c: DistanceY(g5,g5) = 7
FEATURE [PartDesign::Revolution] Revolution053
  AllowMultiFace = false
  Angle = 360
  Axis = (0,0,1)
  Base = (0,0,0)
  Placement = pos=(0,0,0) rot=(0.57735,0.57735,0.57735;2.0944rad)
  Profile = -> Sketch511
  ReferenceAxis = -> Sketch511 [V_Axis]
FEATURE [Sketcher::SketchObject] Sketch512
  FullyConstrained = false
  MapMode = 5
  Placement = pos=(0,0,0) rot=(0.57735,0.57735,0.57735;2.0944rad)
  Support = -> [YZ_Plane963]
  sketch-geometry (6):
    g0: LineSegment StartX=0 StartY=0 StartZ=0 EndX=-1.6 EndY=0 EndZ=0
    g1: LineSegment StartX=-1.6 StartY=0 StartZ=0 EndX=-1.6 EndY=-0.4 EndZ=0
    g2: LineSegment StartX=-1.6 StartY=-0.4 StartZ=0 EndX=-1.5 EndY=-0.4 EndZ=0
    g3: LineSegment StartX=-1.5 StartY=-0.4 StartZ=0 EndX=-1.5 EndY=-7 EndZ=0
    g4: LineSegment StartX=-1.5 StartY=-7 StartZ=0 EndX=0 EndY=-7 EndZ=0
    g5: LineSegment StartX=0 StartY=-7 StartZ=0 EndX=0 EndY=0 EndZ=0
  constraints (17):
    c: Coincident(g0,g-1)
    c: Horizontal(g0)
    c: Coincident(g1,g0)
    c: Coincident(g2,g1)
    c: Coincident(g3,g2)
    c: Vertical(g3)
    c: Coincident(g4,g3)
    c: Coincident(g5,g4)
    c: Coincident(g5,g-1)
    c: Vertical(g5)
    c: Horizontal(g4)
    c: Horizontal(g2)
    c: Vertical(g1)
    c: DistanceY(g1,g1) = 0.4
    c: DistanceX(g4,g4) = 1.5
    c: DistanceX(g0,g0) = 1.6
    c: DistanceY(g5,g5) = 7
FEATURE [PartDesign::Revolution] Revolution052
  AllowMultiFace = false
  Angle = 360
  Axis = (0,0,1)
  Base = (0,0,0)
  Placement = pos=(0,0,0) rot=(0.57735,0.57735,0.57735;2.0944rad)
  Profile = -> Sketch512
  ReferenceAxis = -> Sketch512 [V_Axis]
FEATURE [Sketcher::SketchObject] Sketch513
  FullyConstrained = false
  MapMode = 5
  Placement = pos=(0,0,0) rot=(0.57735,0.57735,0.57735;2.0944rad)
  Support = -> [YZ_Plane964]
  sketch-geometry (6):
    g0: LineSegment StartX=0 StartY=0 StartZ=0 EndX=-1.6 EndY=0 EndZ=0
    g1: LineSegment StartX=-1.6 StartY=0 StartZ=0 EndX=-1.6 EndY=-0.4 EndZ=0
    g2: LineSegment StartX=-1.6 StartY=-0.4 StartZ=0 EndX=-1.5 EndY=-0.4 EndZ=0
    g3: LineSegment StartX=-1.5 StartY=-0.4 StartZ=0 EndX=-1.5 EndY=-7 EndZ=0
    g4: LineSegment StartX=-1.5 StartY=-7 StartZ=0 EndX=0 EndY=-7 EndZ=0
    g5: LineSegment StartX=0 StartY=-7 StartZ=0 EndX=0 EndY=0 EndZ=0
  constraints (17):
    c: Coincident(g0,g-1)
    c: Horizontal(g0)
    c: Coincident(g1,g0)
    c: Coincident(g2,g1)
    c: Coincident(g3,g2)
    c: Vertical(g3)
    c: Coincident(g4,g3)
    c: Coincident(g5,g4)
    c: Coincident(g5,g-1)
    c: Vertical(g5)
    c: Horizontal(g4)
    c: Horizontal(g2)
    c: Vertical(g1)
    c: DistanceY(g1,g1) = 0.4
    c: DistanceX(g4,g4) = 1.5
    c: DistanceX(g0,g0) = 1.6
    c: DistanceY(g5,g5) = 7
FEATURE [PartDesign::Revolution] Revolution058
  AllowMultiFace = false
  Angle = 360
  Axis = (0,0,1)
  Base = (0,0,0)
  Placement = pos=(0,0,0) rot=(0.57735,0.57735,0.57735;2.0944rad)
  Profile = -> Sketch513
  ReferenceAxis = -> Sketch513 [V_Axis]
FEATURE [Sketcher::SketchObject] Sketch514
  FullyConstrained = false
  MapMode = 5
  Placement = pos=(0,0,0) rot=(0.57735,0.57735,0.57735;2.0944rad)
  Support = -> [YZ_Plane952]
  sketch-geometry (6):
    g0: LineSegment StartX=0 StartY=0 StartZ=0 EndX=-1.6 EndY=0 EndZ=0
    g1: LineSegment StartX=-1.6 StartY=0 StartZ=0 EndX=-1.6 EndY=-0.4 EndZ=0
    g2: LineSegment StartX=-1.6 StartY=-0.4 StartZ=0 EndX=-1.5 EndY=-0.4 EndZ=0
    g3: LineSegment StartX=-1.5 StartY=-0.4 StartZ=0 EndX=-1.5 EndY=-7 EndZ=0
    g4: LineSegment StartX=-1.5 StartY=-7 StartZ=0 EndX=0 EndY=-7 EndZ=0
    g5: LineSegment StartX=0 StartY=-7 StartZ=0 EndX=0 EndY=0 EndZ=0
  constraints (17):
    c: Coincident(g0,g-1)
    c: Horizontal(g0)
    c: Coincident(g1,g0)
    c: Coincident(g2,g1)
    c: Coincident(g3,g2)
    c: Vertical(g3)
    c: Coincident(g4,g3)
    c: Coincident(g5,g4)
    c: Coincident(g5,g-1)
    c: Vertical(g5)
    c: Horizontal(g4)
    c: Horizontal(g2)
    c: Vertical(g1)
    c: DistanceY(g1,g1) = 0.4
    c: DistanceX(g4,g4) = 1.5
    c: DistanceX(g0,g0) = 1.6
    c: DistanceY(g5,g5) = 7
FEATURE [PartDesign::Revolution] Revolution055
  AllowMultiFace = false
  Angle = 360
  Axis = (0,0,1)
  Base = (0,0,0)
  Placement = pos=(0,0,0) rot=(0.57735,0.57735,0.57735;2.0944rad)
  Profile = -> Sketch514
  ReferenceAxis = -> Sketch514 [V_Axis]
FEATURE [Sketcher::SketchObject] Sketch515
  FullyConstrained = false
  MapMode = 5
  Placement = pos=(0,0,0) rot=(0.57735,0.57735,0.57735;2.0944rad)
  Support = -> [YZ_Plane960]
  sketch-geometry (6):
    g0: LineSegment StartX=0 StartY=0 StartZ=0 EndX=-1.6 EndY=0 EndZ=0
    g1: LineSegment StartX=-1.6 StartY=0 StartZ=0 EndX=-1.6 EndY=-0.4 EndZ=0
    g2: LineSegment StartX=-1.6 StartY=-0.4 StartZ=0 EndX=-1.5 EndY=-0.4 EndZ=0
    g3: LineSegment StartX=-1.5 StartY=-0.4 StartZ=0 EndX=-1.5 EndY=-7 EndZ=0
    g4: LineSegment StartX=-1.5 StartY=-7 StartZ=0 EndX=0 EndY=-7 EndZ=0
    g5: LineSegment StartX=0 StartY=-7 StartZ=0 EndX=0 EndY=0 EndZ=0
  constraints (17):
    c: Coincident(g0,g-1)
    c: Horizontal(g0)
    c: Coincident(g1,g0)
    c: Coincident(g2,g1)
    c: Coincident(g3,g2)
    c: Vertical(g3)
    c: Coincident(g4,g3)
    c: Coincident(g5,g4)
    c: Coincident(g5,g-1)
    c: Vertical(g5)
    c: Horizontal(g4)
    c: Horizontal(g2)
    c: Vertical(g1)
    c: DistanceY(g1,g1) = 0.4
    c: DistanceX(g4,g4) = 1.5
    c: DistanceX(g0,g0) = 1.6
    c: DistanceY(g5,g5) = 7
FEATURE [Sketcher::SketchObject] Sketch516
  FullyConstrained = false
  MapMode = 5
  Placement = pos=(0,0,0) rot=(0.57735,0.57735,0.57735;2.0944rad)
  Support = -> [YZ_Plane962]
  sketch-geometry (6):
    g0: LineSegment StartX=0 StartY=0 StartZ=0 EndX=-1.6 EndY=0 EndZ=0
    g1: LineSegment StartX=-1.6 StartY=0 StartZ=0 EndX=-1.6 EndY=-0.4 EndZ=0
    g2: LineSegment StartX=-1.6 StartY=-0.4 StartZ=0 EndX=-1.5 EndY=-0.4 EndZ=0
    g3: LineSegment StartX=-1.5 StartY=-0.4 StartZ=0 EndX=-1.5 EndY=-7 EndZ=0
    g4: LineSegment StartX=-1.5 StartY=-7 StartZ=0 EndX=0 EndY=-7 EndZ=0
    g5: LineSegment StartX=0 StartY=-7 StartZ=0 EndX=0 EndY=0 EndZ=0
  constraints (17):
    c: Coincident(g0,g-1)
    c: Horizontal(g0)
    c: Coincident(g1,g0)
    c: Coincident(g2,g1)
    c: Coincident(g3,g2)
    c: Vertical(g3)
    c: Coincident(g4,g3)
    c: Coincident(g5,g4)
    c: Coincident(g5,g-1)
    c: Vertical(g5)
    c: Horizontal(g4)
    c: Horizontal(g2)
    c: Vertical(g1)
    c: DistanceY(g1,g1) = 0.4
    c: DistanceX(g4,g4) = 1.5
    c: DistanceX(g0,g0) = 1.6
    c: DistanceY(g5,g5) = 7
FEATURE [PartDesign::Revolution] Revolution051
  AllowMultiFace = false
  Angle = 360
  Axis = (0,0,1)
  Base = (0,0,0)
  Placement = pos=(0,0,0) rot=(0.57735,0.57735,0.57735;2.0944rad)
  Profile = -> Sketch516
  ReferenceAxis = -> Sketch516 [V_Axis]
FEATURE [Sketcher::SketchObject] Sketch517
  FullyConstrained = false
  MapMode = 5
  Placement = pos=(0,0,0) rot=(0.57735,0.57735,0.57735;2.0944rad)
  Support = -> [YZ_Plane955]
  sketch-geometry (6):
    g0: LineSegment StartX=0 StartY=0 StartZ=0 EndX=-1.6 EndY=0 EndZ=0
    g1: LineSegment StartX=-1.6 StartY=0 StartZ=0 EndX=-1.6 EndY=-0.4 EndZ=0
    g2: LineSegment StartX=-1.6 StartY=-0.4 StartZ=0 EndX=-1.5 EndY=-0.4 EndZ=0
    g3: LineSegment StartX=-1.5 StartY=-0.4 StartZ=0 EndX=-1.5 EndY=-7 EndZ=0
    g4: LineSegment StartX=-1.5 StartY=-7 StartZ=0 EndX=0 EndY=-7 EndZ=0
    g5: LineSegment StartX=0 StartY=-7 StartZ=0 EndX=0 EndY=0 EndZ=0
  constraints (17):
    c: Coincident(g0,g-1)
    c: Horizontal(g0)
    c: Coincident(g1,g0)
    c: Coincident(g2,g1)
    c: Coincident(g3,g2)
    c: Vertical(g3)
    c: Coincident(g4,g3)
    c: Coincident(g5,g4)
    c: Coincident(g5,g-1)
    c: Vertical(g5)
    c: Horizontal(g4)
    c: Horizontal(g2)
    c: Vertical(g1)
    c: DistanceY(g1,g1) = 0.4
    c: DistanceX(g4,g4) = 1.5
    c: DistanceX(g0,g0) = 1.6
    c: DistanceY(g5,g5) = 7
FEATURE [PartDesign::Revolution] Revolution059
  AllowMultiFace = false
  Angle = 360
  Axis = (0,0,1)
  Base = (0,0,0)
  Placement = pos=(0,0,0) rot=(0.57735,0.57735,0.57735;2.0944rad)
  Profile = -> Sketch517
  ReferenceAxis = -> Sketch517 [V_Axis]
FEATURE [Sketcher::SketchObject] Sketch518
  FullyConstrained = false
  MapMode = 5
  Placement = pos=(0,0,0) rot=(0.57735,0.57735,0.57735;2.0944rad)
  Support = -> [YZ_Plane953]
  sketch-geometry (6):
    g0: LineSegment StartX=0 StartY=0 StartZ=0 EndX=-1.6 EndY=0 EndZ=0
    g1: LineSegment StartX=-1.6 StartY=0 StartZ=0 EndX=-1.6 EndY=-0.4 EndZ=0
    g2: LineSegment StartX=-1.6 StartY=-0.4 StartZ=0 EndX=-1.5 EndY=-0.4 EndZ=0
    g3: LineSegment StartX=-1.5 StartY=-0.4 StartZ=0 EndX=-1.5 EndY=-7 EndZ=0
    g4: LineSegment StartX=-1.5 StartY=-7 StartZ=0 EndX=0 EndY=-7 EndZ=0
    g5: LineSegment StartX=0 StartY=-7 StartZ=0 EndX=0 EndY=0 EndZ=0
  constraints (17):
    c: Coincident(g0,g-1)
    c: Horizontal(g0)
    c: Coincident(g1,g0)
    c: Coincident(g2,g1)
    c: Coincident(g3,g2)
    c: Vertical(g3)
    c: Coincident(g4,g3)
    c: Coincident(g5,g4)
    c: Coincident(g5,g-1)
    c: Vertical(g5)
    c: Horizontal(g4)
    c: Horizontal(g2)
    c: Vertical(g1)
    c: DistanceY(g1,g1) = 0.4
    c: DistanceX(g4,g4) = 1.5
    c: DistanceX(g0,g0) = 1.6
    c: DistanceY(g5,g5) = 7
FEATURE [PartDesign::Revolution] Revolution061
  AllowMultiFace = false
  Angle = 360
  Axis = (0,0,1)
  Base = (0,0,0)
  Placement = pos=(0,0,0) rot=(0.57735,0.57735,0.57735;2.0944rad)
  Profile = -> Sketch518
  ReferenceAxis = -> Sketch518 [V_Axis]
FEATURE [Sketcher::SketchObject] Sketch519
  FullyConstrained = false
  MapMode = 5
  Placement = pos=(0,0,0) rot=(0.57735,0.57735,0.57735;2.0944rad)
  Support = -> [YZ_Plane966]
  sketch-geometry (6):
    g0: LineSegment StartX=0 StartY=0 StartZ=0 EndX=-1.6 EndY=0 EndZ=0
    g1: LineSegment StartX=-1.6 StartY=0 StartZ=0 EndX=-1.6 EndY=-0.4 EndZ=0
    g2: LineSegment StartX=-1.6 StartY=-0.4 StartZ=0 EndX=-1.5 EndY=-0.4 EndZ=0
    g3: LineSegment StartX=-1.5 StartY=-0.4 StartZ=0 EndX=-1.5 EndY=-7 EndZ=0
    g4: LineSegment StartX=-1.5 StartY=-7 StartZ=0 EndX=0 EndY=-7 EndZ=0
    g5: LineSegment StartX=0 StartY=-7 StartZ=0 EndX=0 EndY=0 EndZ=0
  constraints (17):
    c: Coincident(g0,g-1)
    c: Horizontal(g0)
    c: Coincident(g1,g0)
    c: Coincident(g2,g1)
    c: Coincident(g3,g2)
    c: Vertical(g3)
    c: Coincident(g4,g3)
    c: Coincident(g5,g4)
    c: Coincident(g5,g-1)
    c: Vertical(g5)
    c: Horizontal(g4)
    c: Horizontal(g2)
    c: Vertical(g1)
    c: DistanceY(g1,g1) = 0.4
    c: DistanceX(g4,g4) = 1.5
    c: DistanceX(g0,g0) = 1.6
    c: DistanceY(g5,g5) = 7
FEATURE [Sketcher::SketchObject] Sketch520
  FullyConstrained = false
  MapMode = 5
  Placement = pos=(0,0,0) rot=(0.57735,0.57735,0.57735;2.0944rad)
  Support = -> [YZ_Plane965]
  sketch-geometry (6):
    g0: LineSegment StartX=0 StartY=0 StartZ=0 EndX=-1.6 EndY=0 EndZ=0
    g1: LineSegment StartX=-1.6 StartY=0 StartZ=0 EndX=-1.6 EndY=-0.4 EndZ=0
    g2: LineSegment StartX=-1.6 StartY=-0.4 StartZ=0 EndX=-1.5 EndY=-0.4 EndZ=0
    g3: LineSegment StartX=-1.5 StartY=-0.4 StartZ=0 EndX=-1.5 EndY=-7 EndZ=0
    g4: LineSegment StartX=-1.5 StartY=-7 StartZ=0 EndX=0 EndY=-7 EndZ=0
    g5: LineSegment StartX=0 StartY=-7 StartZ=0 EndX=0 EndY=0 EndZ=0
  constraints (17):
    c: Coincident(g0,g-1)
    c: Horizontal(g0)
    c: Coincident(g1,g0)
    c: Coincident(g2,g1)
    c: Coincident(g3,g2)
    c: Vertical(g3)
    c: Coincident(g4,g3)
    c: Coincident(g5,g4)
    c: Coincident(g5,g-1)
    c: Vertical(g5)
    c: Horizontal(g4)
    c: Horizontal(g2)
    c: Vertical(g1)
    c: DistanceY(g1,g1) = 0.4
    c: DistanceX(g4,g4) = 1.5
    c: DistanceX(g0,g0) = 1.6
    c: DistanceY(g5,g5) = 7
FEATURE [Sketcher::SketchObject] Sketch521
  FullyConstrained = false
  MapMode = 5
  Placement = pos=(0,0,0) rot=(0.57735,0.57735,0.57735;2.0944rad)
  Support = -> [YZ_Plane961]
  sketch-geometry (6):
    g0: LineSegment StartX=0 StartY=0 StartZ=0 EndX=-1.6 EndY=0 EndZ=0
    g1: LineSegment StartX=-1.6 StartY=0 StartZ=0 EndX=-1.6 EndY=-0.4 EndZ=0
    g2: LineSegment StartX=-1.6 StartY=-0.4 StartZ=0 EndX=-1.5 EndY=-0.4 EndZ=0
    g3: LineSegment StartX=-1.5 StartY=-0.4 StartZ=0 EndX=-1.5 EndY=-7 EndZ=0
    g4: LineSegment StartX=-1.5 StartY=-7 StartZ=0 EndX=0 EndY=-7 EndZ=0
    g5: LineSegment StartX=0 StartY=-7 StartZ=0 EndX=0 EndY=0 EndZ=0
  constraints (17):
    c: Coincident(g0,g-1)
    c: Horizontal(g0)
    c: Coincident(g1,g0)
    c: Coincident(g2,g1)
    c: Coincident(g3,g2)
    c: Vertical(g3)
    c: Coincident(g4,g3)
    c: Coincident(g5,g4)
    c: Coincident(g5,g-1)
    c: Vertical(g5)
    c: Horizontal(g4)
    c: Horizontal(g2)
    c: Vertical(g1)
    c: DistanceY(g1,g1) = 0.4
    c: DistanceX(g4,g4) = 1.5
    c: DistanceX(g0,g0) = 1.6
    c: DistanceY(g5,g5) = 7
FEATURE [Sketcher::SketchObject] Sketch522
  FullyConstrained = false
  MapMode = 5
  Placement = pos=(0,0,0) rot=(0.57735,0.57735,0.57735;2.0944rad)
  Support = -> [YZ_Plane959]
  sketch-geometry (6):
    g0: LineSegment StartX=0 StartY=0 StartZ=0 EndX=-1.6 EndY=0 EndZ=0
    g1: LineSegment StartX=-1.6 StartY=0 StartZ=0 EndX=-1.6 EndY=-0.4 EndZ=0
    g2: LineSegment StartX=-1.6 StartY=-0.4 StartZ=0 EndX=-1.5 EndY=-0.4 EndZ=0
    g3: LineSegment StartX=-1.5 StartY=-0.4 StartZ=0 EndX=-1.5 EndY=-7 EndZ=0
    g4: LineSegment StartX=-1.5 StartY=-7 StartZ=0 EndX=0 EndY=-7 EndZ=0
    g5: LineSegment StartX=0 StartY=-7 StartZ=0 EndX=0 EndY=0 EndZ=0
  constraints (17):
    c: Coincident(g0,g-1)
    c: Horizontal(g0)
    c: Coincident(g1,g0)
    c: Coincident(g2,g1)
    c: Coincident(g3,g2)
    c: Vertical(g3)
    c: Coincident(g4,g3)
    c: Coincident(g5,g4)
    c: Coincident(g5,g-1)
    c: Vertical(g5)
    c: Horizontal(g4)
    c: Horizontal(g2)
    c: Vertical(g1)
    c: DistanceY(g1,g1) = 0.4
    c: DistanceX(g4,g4) = 1.5
    c: DistanceX(g0,g0) = 1.6
    c: DistanceY(g5,g5) = 7
FEATURE [PartDesign::Body] Body187
  Group = -> [Sketch512,Revolution052]
  Origin = -> Origin895
  Tip = -> Revolution052
FEATURE [App::Part] Part152  label="Lightpipe053"
  Group = -> [Body187]
  Origin = -> Origin956
  Placement = pos=(40.005,-13.335,0) rot=(0,0,1;0rad)
  expr: .Placement.Base.x = 40.005
  expr: .Placement.Base.y = -13.335
FEATURE [PartDesign::Body] Body188
  Group = -> [Sketch513,Revolution058]
  Origin = -> Origin903
  Tip = -> Revolution058
FEATURE [App::Part] Part158  label="Lightpipe058"
  Group = -> [Body188]
  Origin = -> Origin957
  Placement = pos=(-40.005,-13.335,0) rot=(0,0,1;0rad)
  expr: .Placement.Base.x = -40.005
  expr: .Placement.Base.y = -13.335
FEATURE [PartDesign::Body] Body189
  Group = -> [Sketch517,Revolution059]
  Origin = -> Origin901
  Tip = -> Revolution059
FEATURE [App::Part] Part153  label="Lightpipe054"
  Group = -> [Body189]
  Origin = -> Origin965
  Placement = pos=(13.335,-40.005,0) rot=(0,0,1;0rad)
  expr: .Placement.Base.x = 13.335
  expr: .Placement.Base.y = -40.005
FEATURE [PartDesign::Body] Body190
  Group = -> [Sketch505,Sketch503,Sketch509,AdditiveLoft036,Sketch502,Pad099,Sketch501,Pocket108,Sketch508,Pocket109,Sketch499,Pocket110,Chamfer077,Chamfer081,Fillet041]
  Origin = -> Origin932
  Tip = -> Fillet041
FEATURE [App::Part] Part139  label="Cap032"
  Group = -> [Body190]
  Origin = -> Origin930
  Placement = pos=(40.005,-13.335,0) rot=(0,0,1;0rad)
  expr: .Placement.Base.x = 40.005
  expr: .Placement.Base.y = -13.335
FEATURE [App::Part] Part149  label="EN16_Caps"
  Group = -> [Part140,Part142,Part135,Part143,Part141,Part134,Part145,Part146,Part139,Part144,Part136,Part147,Part138,Part137,Part148,Part154]
  Origin = -> Origin947
FEATURE [PartDesign::Body] Body191
  Group = -> [Sketch518,Revolution061]
  Origin = -> Origin902
  Tip = -> Revolution061
FEATURE [App::Part] Part156  label="Lightpipe056"
  Group = -> [Body191]
  Origin = -> Origin964
  Placement = pos=(-40.005,-40.005,0) rot=(0,0,1;0rad)
  expr: .Placement.Base.x = -40.005
  expr: .Placement.Base.y = -40.005
FEATURE [PartDesign::Body] Body194
  Group = -> [Sketch511,Revolution053]
  Origin = -> Origin967
  Tip = -> Revolution053
FEATURE [PartDesign::Body] Body195
  Group = -> [Sketch500,Revolution054]
  Origin = -> Origin968
  Tip = -> Revolution054
FEATURE [App::Part] Part132  label="Lightpipe049"
  Group = -> [Body195]
  Origin = -> Origin951
  Placement = pos=(40.005,40.005,0) rot=(0,0,1;0rad)
  expr: .Placement.Base.x = 40.005
  expr: .Placement.Base.y = 40.005
FEATURE [PartDesign::Body] Body196
  Group = -> [Sketch514,Revolution055]
  Origin = -> Origin954
  Tip = -> Revolution055
FEATURE [App::Part] Part155  label="Lightpipe055"
  Group = -> [Body196]
  Origin = -> Origin943
  Placement = pos=(40.005,13.335,0) rot=(0,0,1;0rad)
  expr: .Placement.Base.x = 40.005
  expr: .Placement.Base.y = 13.335
FEATURE [PartDesign::Body] Body201
  Group = -> [Sketch506,Revolution057]
  Origin = -> Origin960
  Tip = -> Revolution057
FEATURE [PartDesign::Body] Body202
  Group = -> [Sketch510,Revolution056]
  Origin = -> Origin959
  Tip = -> Revolution056
FEATURE [PartDesign::Body] Body204
  Group = -> [Sketch516,Revolution051]
  Origin = -> Origin905
  Tip = -> Revolution051
FEATURE [App::Part] Part133  label="Lightpipe050"
  Group = -> [Body204]
  Origin = -> Origin966
  Placement = pos=(13.335,-13.335,0) rot=(0,0,1;0rad)
  expr: .Placement.Base.x = 13.335
  expr: .Placement.Base.y = -13.335
FEATURE [PartDesign::Revolution] Revolution062
  AllowMultiFace = false
  Angle = 360
  Axis = (0,0,1)
  Base = (0,0,0)
  Placement = pos=(0,0,0) rot=(0.57735,0.57735,0.57735;2.0944rad)
  Profile = -> Sketch520
  ReferenceAxis = -> Sketch520 [V_Axis]
FEATURE [PartDesign::Body] Body197
  Group = -> [Sketch520,Revolution062]
  Origin = -> Origin955
  Tip = -> Revolution062
FEATURE [App::Part] Part150  label="Lightpipe051"
  Group = -> [Body197]
  Origin = -> Origin944
  Placement = pos=(13.335,13.335,0) rot=(0,0,1;0rad)
  expr: .Placement.Base.x = 13.335
  expr: .Placement.Base.y = 13.335
FEATURE [PartDesign::Revolution] Revolution063
  AllowMultiFace = false
  Angle = 360
  Axis = (0,0,1)
  Base = (0,0,0)
  Placement = pos=(0,0,0) rot=(0.57735,0.57735,0.57735;2.0944rad)
  Profile = -> Sketch519
  ReferenceAxis = -> Sketch519 [V_Axis]
FEATURE [PartDesign::Body] Body198
  Group = -> [Sketch519,Revolution063]
  Origin = -> Origin898
  Tip = -> Revolution063
FEATURE [PartDesign::Revolution] Revolution064
  AllowMultiFace = false
  Angle = 360
  Axis = (0,0,1)
  Base = (0,0,0)
  Placement = pos=(0,0,0) rot=(0.57735,0.57735,0.57735;2.0944rad)
  Profile = -> Sketch522
  ReferenceAxis = -> Sketch522 [V_Axis]
FEATURE [PartDesign::Body] Body199
  Group = -> [Sketch522,Revolution064]
  Origin = -> Origin899
  Tip = -> Revolution064
FEATURE [App::Part] Part159  label="Lightpipe059"
  Group = -> [Body199]
  Origin = -> Origin949
  Placement = pos=(-13.335,13.335,0) rot=(0,0,1;0rad)
  expr: .Placement.Base.x = -13.335
  expr: .Placement.Base.y = 13.335
FEATURE [PartDesign::Revolution] Revolution065
  AllowMultiFace = false
  Angle = 360
  Axis = (0,0,1)
  Base = (0,0,0)
  Placement = pos=(0,0,0) rot=(0.57735,0.57735,0.57735;2.0944rad)
  Profile = -> Sketch515
  ReferenceAxis = -> Sketch515 [V_Axis]
FEATURE [PartDesign::Body] Body200
  Group = -> [Sketch515,Revolution065]
  Origin = -> Origin894
  Tip = -> Revolution065
FEATURE [App::Part] Part160  label="Lightpipe060"
  Group = -> [Body200]
  Origin = -> Origin961
  Placement = pos=(40.005,-40.005,0) rot=(0,0,1;0rad)
  expr: .Placement.Base.x = 40.005
  expr: .Placement.Base.y = -40.005
FEATURE [PartDesign::Revolution] Revolution066
  AllowMultiFace = false
  Angle = 360
  Axis = (0,0,1)
  Base = (0,0,0)
  Placement = pos=(0,0,0) rot=(0.57735,0.57735,0.57735;2.0944rad)
  Profile = -> Sketch521
  ReferenceAxis = -> Sketch521 [V_Axis]
FEATURE [PartDesign::Body] Body203
  Group = -> [Sketch521,Revolution066]
  Origin = -> Origin900
  Tip = -> Revolution066
FEATURE [App::Part] Part151  label="Lightpipe052"
  Group = -> [Body203]
  Origin = -> Origin963
  Placement = pos=(-13.335,-13.335,0) rot=(0,0,1;0rad)
  expr: .Placement.Base.x = -13.335
  expr: .Placement.Base.y = -13.335
FEATURE [App::Part] Part163  label="Lightpipe061"
  Group = -> [Body198]
  Origin = -> Origin940
  Placement = pos=(-40.005,13.335,0) rot=(0,0,1;0rad)
  expr: .Placement.Base.x = -40.005
  expr: .Placement.Base.y = 13.335
FEATURE [App::Part] Part164  label="Lightpipe062"
  Group = -> [Body201]
  Origin = -> Origin941
  Placement = pos=(-13.34,40.005,0) rot=(0,0,1;0rad)
  expr: .Placement.Base.x = -13.335
  expr: .Placement.Base.y = 40.005
FEATURE [App::Part] Part165  label="Lightpipe063"
  Group = -> [Body202]
  Origin = -> Origin962
  Placement = pos=(-40.005,40.005,0) rot=(0,0,1;0rad)
  expr: .Placement.Base.x = -40.005
  expr: .Placement.Base.y = 40.005
FEATURE [App::Part] Part168  label="Lightpipe064"
  Group = -> [Body194]
  Origin = -> Origin950
  Placement = pos=(13.335,40.005,0) rot=(0,0,1;0rad)
  expr: .Placement.Base.x = 13.335
  expr: .Placement.Base.y = 40.005
FEATURE [Sketcher::SketchObject] Sketch523
  FullyConstrained = false
  MapMode = 5
  Placement = pos=(0,0,0) rot=(0.57735,0.57735,0.57735;2.0944rad)
  Support = -> [YZ_Plane954]
  sketch-geometry (6):
    g0: LineSegment StartX=0 StartY=0 StartZ=0 EndX=-1.6 EndY=0 EndZ=0
    g1: LineSegment StartX=-1.6 StartY=0 StartZ=0 EndX=-1.6 EndY=-0.4 EndZ=0
    g2: LineSegment StartX=-1.6 StartY=-0.4 StartZ=0 EndX=-1.5 EndY=-0.4 EndZ=0
    g3: LineSegment StartX=-1.5 StartY=-0.4 StartZ=0 EndX=-1.5 EndY=-7 EndZ=0
    g4: LineSegment StartX=-1.5 StartY=-7 StartZ=0 EndX=0 EndY=-7 EndZ=0
    g5: LineSegment StartX=0 StartY=-7 StartZ=0 EndX=0 EndY=0 EndZ=0
  constraints (17):
    c: Coincident(g0,g-1)
    c: Horizontal(g0)
    c: Coincident(g1,g0)
    c: Coincident(g2,g1)
    c: Coincident(g3,g2)
    c: Vertical(g3)
    c: Coincident(g4,g3)
    c: Coincident(g5,g4)
    c: Coincident(g5,g-1)
    c: Vertical(g5)
    c: Horizontal(g4)
    c: Horizontal(g2)
    c: Vertical(g1)
    c: DistanceY(g1,g1) = 0.4
    c: DistanceX(g4,g4) = 1.5
    c: DistanceX(g0,g0) = 1.6
    c: DistanceY(g5,g5) = 7
FEATURE [PartDesign::Revolution] Revolution060
  AllowMultiFace = false
  Angle = 360
  Axis = (0,0,1)
  Base = (0,0,0)
  Placement = pos=(0,0,0) rot=(0.57735,0.57735,0.57735;2.0944rad)
  Profile = -> Sketch523
  ReferenceAxis = -> Sketch523 [V_Axis]
FEATURE [PartDesign::Body] Body205
  Group = -> [Sketch523,Revolution060]
  Origin = -> Origin897
  Tip = -> Revolution060
FEATURE [App::Part] Part157  label="Lightpipe057"
  Group = -> [Body205]
  Origin = -> Origin969
  Placement = pos=(-13.335,-40.005,0) rot=(0,0,1;0rad)
  expr: .Placement.Base.x = -13.335
  expr: .Placement.Base.y = -40.005
FEATURE [App::Part] Part162  label="EN16_Lightpipes"
  Group = -> [Part165,Part164,Part168,Part132,Part155,Part150,Part163,Part159,Part152,Part133,Part151,Part160,Part158,Part153,Part156,Part157]
  Origin = -> Origin958
  Placement = pos=(0,8.5,0) rot=(0,0,1;0rad)
  expr: .Placement.Base.y = 8.5
FEATURE [Part::Feature] Part__Feature1025  label="grid_frontpanel_P017"
  Placement = pos=(0,0,-1.6) rot=(0,0,1;0rad)
  shape: bbox 106.6 x 106.6 x 1.5 mm, 82 faces (baked)
FEATURE [App::Part] Part166  label="EN16_Frontpanel"
  Group = -> [Part__Feature1025]
  Origin = -> Origin893
FEATURE [App::Part] Part161  label="EN16"
  Group = -> [Part149,Part162,Part166]
  Origin = -> Origin896
FEATURE [Part::Feature] Part__Feature  label="Open CASCADE STEP translator 7.3 2"
  shape: bbox 104.4 x 104.4 x 1 mm, 50 faces (baked)
FEATURE [App::Part] Part036  label="PO16"
  Group = -> [Part016,Part033,Part035,Part__Feature]
  Origin = -> Origin118
  Placement = pos=(0,0,1.5) rot=(0,0,1;0rad)
FEATURE [Part::Feature] Part__Feature1026  label="G4_Unibody"
  shape: bbox 164.7 x 164.7 x 137 mm, 1011 faces (baked)
FEATURE [Part::Feature] Part__Feature1027  label="CoverClip"
  shape: bbox 1.87 x 3.9 x 2.25 mm, 19 faces (baked)
FEATURE [Part::Feature] Part__Feature1028  label="MagnetCover"
  shape: bbox 8.525 x 8.525 x 2 mm, 35 faces (baked)
FEATURE [App::VRMLObject] INTERFACE
FEATURE [App::VRMLObject] INTERFACE001
FEATURE [App::VRMLObject] INTERFACE002
FEATURE [App::VRMLObject] INTERFACE003
FEATURE [App::Part] Part170
  Group = -> [INTERFACE001]
  Origin = -> Origin971
  Placement = pos=(0,50.85,0) rot=(1,0,0;1.55334rad)
FEATURE [App::Part] Part054  label="Interface002"
  Group = -> [Part170]
  Origin = -> Origin250
  Placement = pos=(0,0,0) rot=(0,0,1;1.5708rad)
FEATURE [App::Part] Part172
  Group = -> [INTERFACE003]
  Origin = -> Origin973
  Placement = pos=(0,50.85,0) rot=(1,0,0;1.55334rad)
FEATURE [App::Part] Part056  label="Interface004"
  Group = -> [Part172]
  Origin = -> Origin394
  Placement = pos=(0,0,0) rot=(0,0,1;4.71239rad)
FEATURE [App::VRMLObject] edge_plating_test
  Placement = pos=(0,0,-8.8) rot=(0,0,1;0rad)
FEATURE [Part::Feature] Part__Feature1029  label="Open CASCADE STEP translator 7.3 3"
  shape: bbox 104.4 x 104.4 x 1 mm, 50 faces (baked)
FEATURE [App::Part] Part080  label="BU16"
  Group = -> [Part093,Part__Feature1029]
  Origin = -> Origin771
FEATURE [Part::Feature] Part__Feature1030  label="Open CASCADE STEP translator 7.3 11"
  shape: bbox 104.4 x 104.4 x 1 mm, 46 faces (baked)
FEATURE [Part::Feature] Part__Feature1031  label="Open CASCADE STEP translator 7.3 5"
  shape: bbox 104.4 x 104.4 x 1 mm, 50 faces (baked)
FEATURE [Part::Feature] Part__Feature1032  label="Open CASCADE STEP translator 7.3 4"
  shape: bbox 104.4 x 104.4 x 1 mm, 54 faces (baked)
FEATURE [Part::Feature] Part__Feature1033  label="Body206"
  shape: bbox 4.4 x 4.4 x 9.692 mm, 7 faces (baked)
FEATURE [App::Part] Part101  label="Lightpipe036"
  Group = -> [Part__Feature1033]
  Origin = -> Origin815
  Placement = pos=(40.005,-40.005,-9.45) rot=(0,0,1;0rad)
  expr: .Placement.Base.x = 40.005
  expr: .Placement.Base.y = -40.005
FEATURE [Part::Feature] Part__Feature1034  label="Body207"
  shape: bbox 4.4 x 4.4 x 9.692 mm, 7 faces (baked)
FEATURE [App::Part] Part111  label="Lightpipe044"
  Group = -> [Part__Feature1034]
  Origin = -> Origin827
  Placement = pos=(13.34,-40.01,-9.45) rot=(0,0,1;0rad)
  expr: .Placement.Base.x = 13.335
  expr: .Placement.Base.y = -40.005
FEATURE [Part::Feature] Part__Feature1035  label="Body208"
  shape: bbox 4.4 x 4.4 x 9.692 mm, 7 faces (baked)
FEATURE [App::Part] Part102  label="Lightpipe037"
  Group = -> [Part__Feature1035]
  Origin = -> Origin826
  Placement = pos=(-40.01,-40.01,-9.45) rot=(0,0,1;0rad)
  expr: .Placement.Base.x = -40.005
  expr: .Placement.Base.y = -40.005
FEATURE [Part::Feature] Part__Feature1036  label="Body209"
  shape: bbox 4.4 x 4.4 x 9.692 mm, 7 faces (baked)
FEATURE [App::Part] Part115  label="Lightpipe048"
  Group = -> [Part__Feature1036]
  Origin = -> Origin830
  Placement = pos=(-13.34,-40.01,-9.45) rot=(0,0,1;0rad)
  expr: .Placement.Base.x = -13.335
  expr: .Placement.Base.y = -40.005
FEATURE [Part::Feature] Part__Feature1037  label="Body210"
  Placement = pos=(0,-0.5,0) rot=(0,0,1;0rad)
  shape: bbox 4.4 x 4.4 x 9.692 mm, 7 faces (baked)
FEATURE [App::Part] Part114  label="Lightpipe047"
  Group = -> [Part__Feature1037]
  Origin = -> Origin822
  Placement = pos=(40.005,40.005,-9.45) rot=(0,0,1;0rad)
  expr: .Placement.Base.x = 40.005
  expr: .Placement.Base.y = 40.005
FEATURE [App::Part] Part104  label="BU16_Lightpipes001"
  Group = -> [Part112,Part106,Part113,Part114,Part099,Part109,Part105,Part103,Part101,Part111,Part102,Part115]
  Origin = -> Origin825
  Placement = pos=(0,8.5,0) rot=(0,0,1;0rad)
  expr: .Placement.Base.y = 8.5
FEATURE [App::Part] Part108  label="PBF4"
  Group = -> [Part104,Part131,Part__Feature1032]
  Origin = -> Origin818
  Placement = pos=(0,0,1.5) rot=(0,0,1;0rad)
FEATURE [App::VRMLObject] EF44
  Placement = pos=(0,0,-8.8) rot=(0,0,1;0rad)
FEATURE [App::VRMLObject] INTERFACE004
FEATURE [App::Part] Part169
  Group = -> [INTERFACE,INTERFACE004]
  Origin = -> Origin970
  Placement = pos=(0,50.85,0) rot=(1,0,0;1.55334rad)
FEATURE [App::Part] Part052  label="Interface001"
  Group = -> [Part169]
  Origin = -> Origin220
FEATURE [App::VRMLObject] INTERFACE005
FEATURE [App::Part] Part171
  Group = -> [INTERFACE002,INTERFACE005]
  Origin = -> Origin972
  Placement = pos=(0,50.85,0) rot=(1,0,0;1.55334rad)
FEATURE [App::Part] Part055  label="Interface003"
  Group = -> [Part171]
  Origin = -> Origin322
  Placement = pos=(0,0,0) rot=(0,0,1;3.14159rad)
FEATURE [App::Part] Part053  label="InterfaceBoards"
  Group = -> [Part052,Part054,Part055,Part056]
  Origin = -> Origin221
  Placement = pos=(0,0,0.1) rot=(0,0,1;0rad)
FEATURE [App::Part] Part046  label="Common"
  Group = -> [Part037,Part047,Part053,Part057,Part079,Part__Feature1021]
  Origin = -> Origin136
FEATURE [App::VRMLObject] INTERFACE006
FEATURE [App::VRMLObject] INTERFACE007
